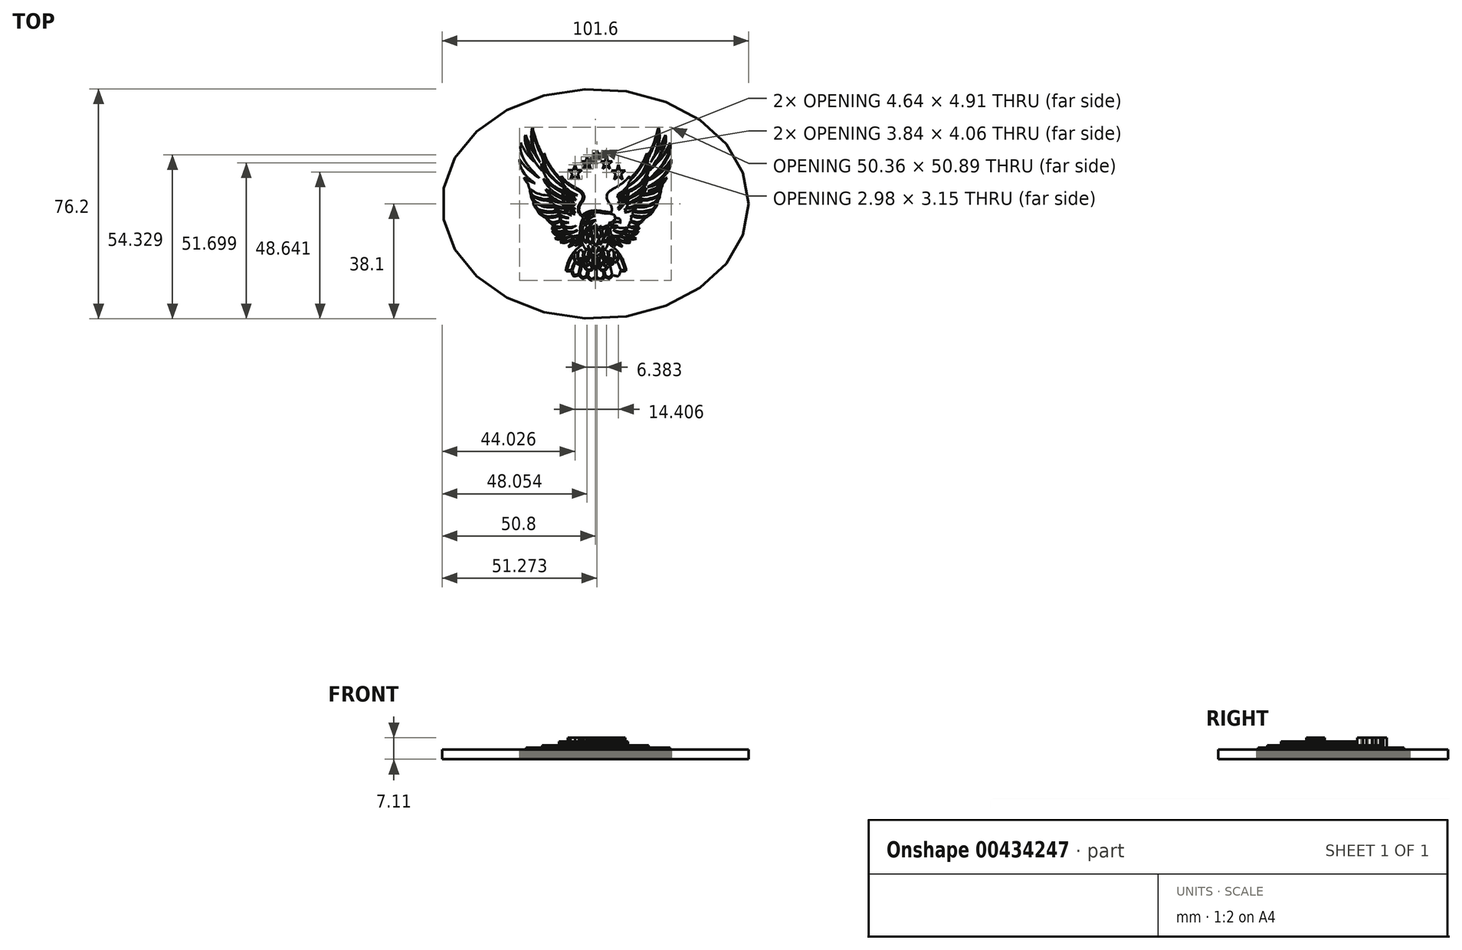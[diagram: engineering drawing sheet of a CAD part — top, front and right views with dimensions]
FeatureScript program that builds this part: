
annotation { "Feature Type Name" : "Feature", "Feature Type Description" : "" }
export const myFeature = defineFeature(function(context is Context, id is Id, definition is map)
    precondition{}
    {
        {
            var Q0;
            Q0=qCreatedBy(makeId("Top.planeOp"),FACE);
            var sketch = newSketch(context, id + "F0", { "sketchPlane" : qUnion([Q0])});
            skLineSegment(sketch, "E0", {"start": v(-20.82, 7.1) * mm, "end": v(-20.84, 7.08) * mm});
            skLineSegment(sketch, "E1", {"start": v(-20.84, 7.08) * mm, "end": v(-20.86, 7.06) * mm});
            skLineSegment(sketch, "E2", {"start": v(-20.86, 7.06) * mm, "end": v(-20.9, 7) * mm});
            skLineSegment(sketch, "E3", {"start": v(-20.9, 7) * mm, "end": v(-20.98, 6.92) * mm});
            skLineSegment(sketch, "E4", {"start": v(-20.98, 6.92) * mm, "end": v(-21.02, 6.88) * mm});
            skLineSegment(sketch, "E5", {"start": v(-21.02, 6.88) * mm, "end": v(-21.04, 6.84) * mm});
            skLineSegment(sketch, "E6", {"start": v(-21.04, 6.84) * mm, "end": v(-21.06, 6.76) * mm});
            skLineSegment(sketch, "E7", {"start": v(-21.06, 6.76) * mm, "end": v(-20.72, 6.6) * mm});
            skLineSegment(sketch, "E8", {"start": v(-20.72, 6.6) * mm, "end": v(-20.26, 6.42) * mm});
            skLineSegment(sketch, "E9", {"start": v(-20.26, 6.42) * mm, "end": v(-19.73, 6.22) * mm});
            skLineSegment(sketch, "E10", {"start": v(-19.73, 6.22) * mm, "end": v(-19.15, 6.01) * mm});
            skLineSegment(sketch, "E11", {"start": v(-19.15, 6.01) * mm, "end": v(-18.58, 5.83) * mm});
            skLineSegment(sketch, "E12", {"start": v(-18.58, 5.83) * mm, "end": v(-18.04, 5.68) * mm});
            skLineSegment(sketch, "E13", {"start": v(-18.04, 5.68) * mm, "end": v(-17.57, 5.58) * mm});
            skLineSegment(sketch, "E14", {"start": v(-17.57, 5.58) * mm, "end": v(-17.21, 5.54) * mm});
            skLineSegment(sketch, "E15", {"start": v(-17.21, 5.54) * mm, "end": v(-17.83, 5.88) * mm});
            skLineSegment(sketch, "E16", {"start": v(-17.83, 5.88) * mm, "end": v(-18.43, 6.24) * mm});
            skLineSegment(sketch, "E17", {"start": v(-18.43, 6.24) * mm, "end": v(-19, 6.59) * mm});
            skLineSegment(sketch, "E18", {"start": v(-19, 6.59) * mm, "end": v(-19.52, 6.93) * mm});
            skLineSegment(sketch, "E19", {"start": v(-19.52, 6.93) * mm, "end": v(-20.03, 7.28) * mm});
            skLineSegment(sketch, "E20", {"start": v(-20.03, 7.28) * mm, "end": v(-20.53, 7.64) * mm});
            skLineSegment(sketch, "E21", {"start": v(-20.53, 7.64) * mm, "end": v(-21.03, 8.03) * mm});
            skLineSegment(sketch, "E22", {"start": v(-21.03, 8.03) * mm, "end": v(-21.52, 8.46) * mm});
            skLineSegment(sketch, "E23", {"start": v(-21.52, 8.46) * mm, "end": v(-22.03, 8.94) * mm});
            skLineSegment(sketch, "E24", {"start": v(-22.03, 8.94) * mm, "end": v(-22.36, 9.27) * mm});
            skLineSegment(sketch, "E25", {"start": v(-22.36, 9.27) * mm, "end": v(-22.68, 9.63) * mm});
            skLineSegment(sketch, "E26", {"start": v(-22.68, 9.63) * mm, "end": v(-22.99, 10) * mm});
            skLineSegment(sketch, "E27", {"start": v(-22.99, 10) * mm, "end": v(-23.28, 10.4) * mm});
            skLineSegment(sketch, "E28", {"start": v(-23.28, 10.4) * mm, "end": v(-23.56, 10.8) * mm});
            skLineSegment(sketch, "E29", {"start": v(-23.56, 10.8) * mm, "end": v(-23.81, 11.21) * mm});
            skLineSegment(sketch, "E30", {"start": v(-23.81, 11.21) * mm, "end": v(-24.04, 11.64) * mm});
            skLineSegment(sketch, "E31", {"start": v(-24.04, 11.64) * mm, "end": v(-24.24, 12.06) * mm});
            skLineSegment(sketch, "E32", {"start": v(-24.24, 12.06) * mm, "end": v(-24.37, 12.37) * mm});
            skLineSegment(sketch, "E33", {"start": v(-24.37, 12.37) * mm, "end": v(-24.52, 12.75) * mm});
            skLineSegment(sketch, "E34", {"start": v(-24.52, 12.75) * mm, "end": v(-24.59, 12.95) * mm});
            skLineSegment(sketch, "E35", {"start": v(-24.59, 12.95) * mm, "end": v(-24.65, 13.15) * mm});
            skLineSegment(sketch, "E36", {"start": v(-24.65, 13.15) * mm, "end": v(-24.7, 13.32) * mm});
            skLineSegment(sketch, "E37", {"start": v(-24.7, 13.32) * mm, "end": v(-24.72, 13.47) * mm});
            skLineSegment(sketch, "E38", {"start": v(-24.72, 13.47) * mm, "end": v(-22.85, 11.41) * mm});
            skLineSegment(sketch, "E39", {"start": v(-22.85, 11.41) * mm, "end": v(-22.45, 11.02) * mm});
            skLineSegment(sketch, "E40", {"start": v(-22.45, 11.02) * mm, "end": v(-22.25, 10.83) * mm});
            skLineSegment(sketch, "E41", {"start": v(-22.25, 10.83) * mm, "end": v(-22.04, 10.64) * mm});
            skLineSegment(sketch, "E42", {"start": v(-22.04, 10.64) * mm, "end": v(-21.83, 10.46) * mm});
            skLineSegment(sketch, "E43", {"start": v(-21.83, 10.46) * mm, "end": v(-21.61, 10.27) * mm});
            skLineSegment(sketch, "E44", {"start": v(-21.61, 10.27) * mm, "end": v(-21.23, 9.96) * mm});
            skLineSegment(sketch, "E45", {"start": v(-21.23, 9.96) * mm, "end": v(-20.76, 9.6) * mm});
            skLineSegment(sketch, "E46", {"start": v(-20.76, 9.6) * mm, "end": v(-20.23, 9.24) * mm});
            skLineSegment(sketch, "E47", {"start": v(-20.23, 9.24) * mm, "end": v(-19.67, 8.87) * mm});
            skLineSegment(sketch, "E48", {"start": v(-19.67, 8.87) * mm, "end": v(-19.1, 8.54) * mm});
            skLineSegment(sketch, "E49", {"start": v(-19.1, 8.54) * mm, "end": v(-18.57, 8.25) * mm});
            skLineSegment(sketch, "E50", {"start": v(-18.57, 8.25) * mm, "end": v(-18.09, 8.03) * mm});
            skLineSegment(sketch, "E51", {"start": v(-18.09, 8.03) * mm, "end": v(-17.69, 7.9) * mm});
            skLineSegment(sketch, "E52", {"start": v(-17.69, 7.9) * mm, "end": v(-20.38, 10.8) * mm});
            skLineSegment(sketch, "E53", {"start": v(-20.38, 10.8) * mm, "end": v(-20.56, 11) * mm});
            skLineSegment(sketch, "E54", {"start": v(-20.56, 11) * mm, "end": v(-20.75, 11.23) * mm});
            skLineSegment(sketch, "E55", {"start": v(-20.75, 11.23) * mm, "end": v(-20.94, 11.46) * mm});
            skLineSegment(sketch, "E56", {"start": v(-20.94, 11.46) * mm, "end": v(-21.14, 11.7) * mm});
            skLineSegment(sketch, "E57", {"start": v(-21.14, 11.7) * mm, "end": v(-21.33, 11.95) * mm});
            skLineSegment(sketch, "E58", {"start": v(-21.33, 11.95) * mm, "end": v(-21.51, 12.19) * mm});
            skLineSegment(sketch, "E59", {"start": v(-21.51, 12.19) * mm, "end": v(-21.7, 12.42) * mm});
            skLineSegment(sketch, "E60", {"start": v(-21.7, 12.42) * mm, "end": v(-21.86, 12.65) * mm});
            skLineSegment(sketch, "E61", {"start": v(-21.86, 12.65) * mm, "end": v(-22.08, 12.95) * mm});
            skLineSegment(sketch, "E62", {"start": v(-22.08, 12.95) * mm, "end": v(-22.31, 13.27) * mm});
            skLineSegment(sketch, "E63", {"start": v(-22.31, 13.27) * mm, "end": v(-22.54, 13.6) * mm});
            skLineSegment(sketch, "E64", {"start": v(-22.54, 13.6) * mm, "end": v(-22.76, 13.94) * mm});
            skLineSegment(sketch, "E65", {"start": v(-22.76, 13.94) * mm, "end": v(-22.98, 14.3) * mm});
            skLineSegment(sketch, "E66", {"start": v(-22.98, 14.3) * mm, "end": v(-23.2, 14.66) * mm});
            skLineSegment(sketch, "E67", {"start": v(-23.2, 14.66) * mm, "end": v(-23.4, 15.02) * mm});
            skLineSegment(sketch, "E68", {"start": v(-23.4, 15.02) * mm, "end": v(-23.58, 15.4) * mm});
            skLineSegment(sketch, "E69", {"start": v(-23.58, 15.4) * mm, "end": v(-23.72, 15.7) * mm});
            skLineSegment(sketch, "E70", {"start": v(-23.72, 15.7) * mm, "end": v(-23.88, 16.08) * mm});
            skLineSegment(sketch, "E71", {"start": v(-23.88, 16.08) * mm, "end": v(-24.06, 16.53) * mm});
            skLineSegment(sketch, "E72", {"start": v(-24.06, 16.53) * mm, "end": v(-24.23, 17.02) * mm});
            skLineSegment(sketch, "E73", {"start": v(-24.23, 17.02) * mm, "end": v(-24.37, 17.52) * mm});
            skLineSegment(sketch, "E74", {"start": v(-24.37, 17.52) * mm, "end": v(-24.49, 18) * mm});
            skLineSegment(sketch, "E75", {"start": v(-24.49, 18) * mm, "end": v(-24.55, 18.45) * mm});
            skLineSegment(sketch, "E76", {"start": v(-24.55, 18.45) * mm, "end": v(-24.55, 18.83) * mm});
            skLineSegment(sketch, "E77", {"start": v(-24.55, 18.83) * mm, "end": v(-24.45, 18.64) * mm});
            skLineSegment(sketch, "E78", {"start": v(-24.45, 18.64) * mm, "end": v(-24.27, 18.34) * mm});
            skLineSegment(sketch, "E79", {"start": v(-24.27, 18.34) * mm, "end": v(-24.03, 17.97) * mm});
            skLineSegment(sketch, "E80", {"start": v(-24.03, 17.97) * mm, "end": v(-23.76, 17.57) * mm});
            skLineSegment(sketch, "E81", {"start": v(-23.76, 17.57) * mm, "end": v(-23.47, 17.15) * mm});
            skLineSegment(sketch, "E82", {"start": v(-23.47, 17.15) * mm, "end": v(-23.2, 16.76) * mm});
            skLineSegment(sketch, "E83", {"start": v(-23.2, 16.76) * mm, "end": v(-22.96, 16.43) * mm});
            skLineSegment(sketch, "E84", {"start": v(-22.96, 16.43) * mm, "end": v(-22.79, 16.18) * mm});
            skLineSegment(sketch, "E85", {"start": v(-22.79, 16.18) * mm, "end": v(-22.51, 15.83) * mm});
            skLineSegment(sketch, "E86", {"start": v(-22.51, 15.83) * mm, "end": v(-21.93, 15.12) * mm});
            skLineSegment(sketch, "E87", {"start": v(-21.93, 15.12) * mm, "end": v(-21.63, 14.8) * mm});
            skLineSegment(sketch, "E88", {"start": v(-21.63, 14.8) * mm, "end": v(-20.56, 13.66) * mm});
            skLineSegment(sketch, "E89", {"start": v(-20.56, 13.66) * mm, "end": v(-20.4, 13.52) * mm});
            skLineSegment(sketch, "E90", {"start": v(-20.4, 13.52) * mm, "end": v(-20.33, 13.43) * mm});
            skLineSegment(sketch, "E91", {"start": v(-20.33, 13.43) * mm, "end": v(-20.26, 13.33) * mm});
            skLineSegment(sketch, "E92", {"start": v(-20.26, 13.33) * mm, "end": v(-19.96, 13) * mm});
            skLineSegment(sketch, "E93", {"start": v(-19.96, 13) * mm, "end": v(-19.58, 12.62) * mm});
            skLineSegment(sketch, "E94", {"start": v(-19.58, 12.62) * mm, "end": v(-19.2, 12.23) * mm});
            skLineSegment(sketch, "E95", {"start": v(-19.2, 12.23) * mm, "end": v(-18.86, 11.9) * mm});
            skLineSegment(sketch, "E96", {"start": v(-18.86, 11.9) * mm, "end": v(-18.72, 11.76) * mm});
            skLineSegment(sketch, "E97", {"start": v(-18.72, 11.76) * mm, "end": v(-18.55, 11.62) * mm});
            skLineSegment(sketch, "E98", {"start": v(-18.55, 11.62) * mm, "end": v(-18.37, 11.46) * mm});
            skLineSegment(sketch, "E99", {"start": v(-18.37, 11.46) * mm, "end": v(-18.2, 11.31) * mm});
            skLineSegment(sketch, "E100", {"start": v(-18.2, 11.31) * mm, "end": v(-18.03, 11.18) * mm});
            skLineSegment(sketch, "E101", {"start": v(-18.03, 11.18) * mm, "end": v(-17.9, 11.09) * mm});
            skLineSegment(sketch, "E102", {"start": v(-17.9, 11.09) * mm, "end": v(-17.8, 11.03) * mm});
            skLineSegment(sketch, "E103", {"start": v(-17.8, 11.03) * mm, "end": v(-17.73, 10.99) * mm});
            skLineSegment(sketch, "E104", {"start": v(-17.73, 10.99) * mm, "end": v(-17.68, 10.95) * mm});
            skLineSegment(sketch, "E105", {"start": v(-17.68, 10.95) * mm, "end": v(-17.63, 10.9) * mm});
            skLineSegment(sketch, "E106", {"start": v(-17.63, 10.9) * mm, "end": v(-17.6, 10.81) * mm});
            skLineSegment(sketch, "E107", {"start": v(-17.6, 10.81) * mm, "end": v(-17.57, 10.69) * mm});
            skLineSegment(sketch, "E108", {"start": v(-17.57, 10.69) * mm, "end": v(-17.51, 10.45) * mm});
            skLineSegment(sketch, "E109", {"start": v(-17.51, 10.45) * mm, "end": v(-17.44, 10.2) * mm});
            skLineSegment(sketch, "E110", {"start": v(-17.44, 10.2) * mm, "end": v(-17.36, 9.97) * mm});
            skLineSegment(sketch, "E111", {"start": v(-17.36, 9.97) * mm, "end": v(-17.26, 9.73) * mm});
            skLineSegment(sketch, "E112", {"start": v(-17.26, 9.73) * mm, "end": v(-17.16, 9.5) * mm});
            skLineSegment(sketch, "E113", {"start": v(-17.16, 9.5) * mm, "end": v(-17.05, 9.28) * mm});
            skLineSegment(sketch, "E114", {"start": v(-17.05, 9.28) * mm, "end": v(-16.94, 9.07) * mm});
            skLineSegment(sketch, "E115", {"start": v(-16.94, 9.07) * mm, "end": v(-16.83, 8.88) * mm});
            skLineSegment(sketch, "E116", {"start": v(-16.83, 8.88) * mm, "end": v(-16.6, 8.5) * mm});
            skLineSegment(sketch, "E117", {"start": v(-16.6, 8.5) * mm, "end": v(-16.33, 8.14) * mm});
            skLineSegment(sketch, "E118", {"start": v(-16.33, 8.14) * mm, "end": v(-16.2, 7.99) * mm});
            skLineSegment(sketch, "E119", {"start": v(-16.2, 7.99) * mm, "end": v(-16.03, 7.78) * mm});
            skLineSegment(sketch, "E120", {"start": v(-16.03, 7.78) * mm, "end": v(-15.94, 7.67) * mm});
            skLineSegment(sketch, "E121", {"start": v(-15.94, 7.67) * mm, "end": v(-15.86, 7.57) * mm});
            skLineSegment(sketch, "E122", {"start": v(-15.86, 7.57) * mm, "end": v(-15.8, 7.48) * mm});
            skLineSegment(sketch, "E123", {"start": v(-15.8, 7.48) * mm, "end": v(-15.77, 7.42) * mm});
            skLineSegment(sketch, "E124", {"start": v(-15.77, 7.42) * mm, "end": v(-16, 7.58) * mm});
            skLineSegment(sketch, "E125", {"start": v(-16, 7.58) * mm, "end": v(-16.26, 7.8) * mm});
            skLineSegment(sketch, "E126", {"start": v(-16.26, 7.8) * mm, "end": v(-16.55, 8.04) * mm});
            skLineSegment(sketch, "E127", {"start": v(-16.55, 8.04) * mm, "end": v(-16.84, 8.3) * mm});
            skLineSegment(sketch, "E128", {"start": v(-16.84, 8.3) * mm, "end": v(-17.13, 8.55) * mm});
            skLineSegment(sketch, "E129", {"start": v(-17.13, 8.55) * mm, "end": v(-17.39, 8.76) * mm});
            skLineSegment(sketch, "E130", {"start": v(-17.39, 8.76) * mm, "end": v(-17.6, 8.92) * mm});
            skLineSegment(sketch, "E131", {"start": v(-17.6, 8.92) * mm, "end": v(-17.75, 9.01) * mm});
            skLineSegment(sketch, "E132", {"start": v(-17.75, 9.01) * mm, "end": v(-17.72, 8.83) * mm});
            skLineSegment(sketch, "E133", {"start": v(-17.72, 8.83) * mm, "end": v(-17.66, 8.61) * mm});
            skLineSegment(sketch, "E134", {"start": v(-17.66, 8.61) * mm, "end": v(-17.59, 8.38) * mm});
            skLineSegment(sketch, "E135", {"start": v(-17.59, 8.38) * mm, "end": v(-17.5, 8.14) * mm});
            skLineSegment(sketch, "E136", {"start": v(-17.5, 8.14) * mm, "end": v(-17.41, 7.9) * mm});
            skLineSegment(sketch, "E137", {"start": v(-17.41, 7.9) * mm, "end": v(-17.32, 7.67) * mm});
            skLineSegment(sketch, "E138", {"start": v(-17.32, 7.67) * mm, "end": v(-17.24, 7.47) * mm});
            skLineSegment(sketch, "E139", {"start": v(-17.24, 7.47) * mm, "end": v(-17.16, 7.3) * mm});
            skLineSegment(sketch, "E140", {"start": v(-17.16, 7.3) * mm, "end": v(-17.07, 7.1) * mm});
            skLineSegment(sketch, "E141", {"start": v(-17.07, 7.1) * mm, "end": v(-16.98, 6.9) * mm});
            skLineSegment(sketch, "E142", {"start": v(-16.98, 6.9) * mm, "end": v(-16.88, 6.72) * mm});
            skLineSegment(sketch, "E143", {"start": v(-16.88, 6.72) * mm, "end": v(-16.78, 6.54) * mm});
            skLineSegment(sketch, "E144", {"start": v(-16.78, 6.54) * mm, "end": v(-16.56, 6.2) * mm});
            skLineSegment(sketch, "E145", {"start": v(-16.56, 6.2) * mm, "end": v(-16.33, 5.85) * mm});
            skLineSegment(sketch, "E146", {"start": v(-16.33, 5.85) * mm, "end": v(-16.15, 5.62) * mm});
            skLineSegment(sketch, "E147", {"start": v(-16.15, 5.62) * mm, "end": v(-15.96, 5.38) * mm});
            skLineSegment(sketch, "E148", {"start": v(-15.96, 5.38) * mm, "end": v(-15.75, 5.15) * mm});
            skLineSegment(sketch, "E149", {"start": v(-15.75, 5.15) * mm, "end": v(-15.52, 4.92) * mm});
            skLineSegment(sketch, "E150", {"start": v(-15.52, 4.92) * mm, "end": v(-15.3, 4.7) * mm});
            skLineSegment(sketch, "E151", {"start": v(-15.3, 4.7) * mm, "end": v(-15.06, 4.49) * mm});
            skLineSegment(sketch, "E152", {"start": v(-15.06, 4.49) * mm, "end": v(-14.82, 4.3) * mm});
            skLineSegment(sketch, "E153", {"start": v(-14.82, 4.3) * mm, "end": v(-14.6, 4.12) * mm});
            skLineSegment(sketch, "E154", {"start": v(-14.6, 4.12) * mm, "end": v(-14.43, 4.01) * mm});
            skLineSegment(sketch, "E155", {"start": v(-14.43, 4.01) * mm, "end": v(-14.26, 3.89) * mm});
            skLineSegment(sketch, "E156", {"start": v(-14.26, 3.89) * mm, "end": v(-14.1, 3.76) * mm});
            skLineSegment(sketch, "E157", {"start": v(-14.1, 3.76) * mm, "end": v(-13.94, 3.64) * mm});
            skLineSegment(sketch, "E158", {"start": v(-13.94, 3.64) * mm, "end": v(-14.2, 3.75) * mm});
            skLineSegment(sketch, "E159", {"start": v(-14.2, 3.75) * mm, "end": v(-14.57, 3.95) * mm});
            skLineSegment(sketch, "E160", {"start": v(-14.57, 3.95) * mm, "end": v(-15, 4.2) * mm});
            skLineSegment(sketch, "E161", {"start": v(-15, 4.2) * mm, "end": v(-15.47, 4.48) * mm});
            skLineSegment(sketch, "E162", {"start": v(-15.47, 4.48) * mm, "end": v(-15.93, 4.77) * mm});
            skLineSegment(sketch, "E163", {"start": v(-15.93, 4.77) * mm, "end": v(-16.36, 5.03) * mm});
            skLineSegment(sketch, "E164", {"start": v(-16.36, 5.03) * mm, "end": v(-16.7, 5.24) * mm});
            skLineSegment(sketch, "E165", {"start": v(-16.7, 5.24) * mm, "end": v(-16.95, 5.36) * mm});
            skLineSegment(sketch, "E166", {"start": v(-16.95, 5.36) * mm, "end": v(-16.85, 5.01) * mm});
            skLineSegment(sketch, "E167", {"start": v(-16.85, 5.01) * mm, "end": v(-16.72, 4.68) * mm});
            skLineSegment(sketch, "E168", {"start": v(-16.72, 4.68) * mm, "end": v(-16.57, 4.36) * mm});
            skLineSegment(sketch, "E169", {"start": v(-16.57, 4.36) * mm, "end": v(-16.42, 4.07) * mm});
            skLineSegment(sketch, "E170", {"start": v(-16.42, 4.07) * mm, "end": v(-16.28, 3.81) * mm});
            skLineSegment(sketch, "E171", {"start": v(-16.28, 3.81) * mm, "end": v(-16.15, 3.6) * mm});
            skLineSegment(sketch, "E172", {"start": v(-16.15, 3.6) * mm, "end": v(-16.05, 3.42) * mm});
            skLineSegment(sketch, "E173", {"start": v(-16.05, 3.42) * mm, "end": v(-15.99, 3.3) * mm});
            skLineSegment(sketch, "E174", {"start": v(-15.99, 3.3) * mm, "end": v(-16.72, 3.37) * mm});
            skLineSegment(sketch, "E175", {"start": v(-16.72, 3.37) * mm, "end": v(-17.6, 3.5) * mm});
            skLineSegment(sketch, "E176", {"start": v(-17.6, 3.5) * mm, "end": v(-18.53, 3.72) * mm});
            skLineSegment(sketch, "E177", {"start": v(-18.53, 3.72) * mm, "end": v(-19.47, 4.01) * mm});
            skLineSegment(sketch, "E178", {"start": v(-19.47, 4.01) * mm, "end": v(-20.34, 4.4) * mm});
            skLineSegment(sketch, "E179", {"start": v(-20.34, 4.4) * mm, "end": v(-21.08, 4.87) * mm});
            skLineSegment(sketch, "E180", {"start": v(-21.08, 4.87) * mm, "end": v(-21.62, 5.46) * mm});
            skLineSegment(sketch, "E181", {"start": v(-21.62, 5.46) * mm, "end": v(-21.89, 6.15) * mm});
            skLineSegment(sketch, "E182", {"start": v(-21.89, 6.15) * mm, "end": v(-21.76, 6.09) * mm});
            skLineSegment(sketch, "E183", {"start": v(-21.76, 6.09) * mm, "end": v(-21.64, 6) * mm});
            skLineSegment(sketch, "E184", {"start": v(-21.64, 6) * mm, "end": v(-21.51, 5.9) * mm});
            skLineSegment(sketch, "E185", {"start": v(-21.51, 5.9) * mm, "end": v(-21.4, 5.81) * mm});
            skLineSegment(sketch, "E186", {"start": v(-21.4, 5.81) * mm, "end": v(-21.03, 5.56) * mm});
            skLineSegment(sketch, "E187", {"start": v(-21.03, 5.56) * mm, "end": v(-20.56, 5.3) * mm});
            skLineSegment(sketch, "E188", {"start": v(-20.56, 5.3) * mm, "end": v(-20.03, 5.05) * mm});
            skLineSegment(sketch, "E189", {"start": v(-20.03, 5.05) * mm, "end": v(-19.46, 4.8) * mm});
            skLineSegment(sketch, "E190", {"start": v(-19.46, 4.8) * mm, "end": v(-18.89, 4.6) * mm});
            skLineSegment(sketch, "E191", {"start": v(-18.89, 4.6) * mm, "end": v(-18.33, 4.44) * mm});
            skLineSegment(sketch, "E192", {"start": v(-18.33, 4.44) * mm, "end": v(-17.84, 4.35) * mm});
            skLineSegment(sketch, "E193", {"start": v(-17.84, 4.35) * mm, "end": v(-17.42, 4.34) * mm});
            skLineSegment(sketch, "E194", {"start": v(-17.42, 4.34) * mm, "end": v(-17.6, 4.36) * mm});
            skLineSegment(sketch, "E195", {"start": v(-17.6, 4.36) * mm, "end": v(-17.92, 4.46) * mm});
            skLineSegment(sketch, "E196", {"start": v(-17.92, 4.46) * mm, "end": v(-18.32, 4.6) * mm});
            skLineSegment(sketch, "E197", {"start": v(-18.32, 4.6) * mm, "end": v(-18.76, 4.76) * mm});
            skLineSegment(sketch, "E198", {"start": v(-18.76, 4.76) * mm, "end": v(-19.2, 4.93) * mm});
            skLineSegment(sketch, "E199", {"start": v(-19.2, 4.93) * mm, "end": v(-19.6, 5.1) * mm});
            skLineSegment(sketch, "E200", {"start": v(-19.6, 5.1) * mm, "end": v(-19.92, 5.23) * mm});
            skLineSegment(sketch, "E201", {"start": v(-19.92, 5.23) * mm, "end": v(-20.1, 5.32) * mm});
            skLineSegment(sketch, "E202", {"start": v(-20.1, 5.32) * mm, "end": v(-20.43, 5.5) * mm});
            skLineSegment(sketch, "E203", {"start": v(-20.43, 5.5) * mm, "end": v(-20.72, 5.67) * mm});
            skLineSegment(sketch, "E204", {"start": v(-20.72, 5.67) * mm, "end": v(-20.99, 5.85) * mm});
            skLineSegment(sketch, "E205", {"start": v(-20.99, 5.85) * mm, "end": v(-21.26, 6.04) * mm});
            skLineSegment(sketch, "E206", {"start": v(-21.26, 6.04) * mm, "end": v(-21.38, 6.15) * mm});
            skLineSegment(sketch, "E207", {"start": v(-21.38, 6.15) * mm, "end": v(-21.5, 6.26) * mm});
            skLineSegment(sketch, "E208", {"start": v(-21.5, 6.26) * mm, "end": v(-21.64, 6.37) * mm});
            skLineSegment(sketch, "E209", {"start": v(-21.64, 6.37) * mm, "end": v(-21.76, 6.48) * mm});
            skLineSegment(sketch, "E210", {"start": v(-21.76, 6.48) * mm, "end": v(-21.87, 6.59) * mm});
            skLineSegment(sketch, "E211", {"start": v(-21.87, 6.59) * mm, "end": v(-21.96, 6.68) * mm});
            skLineSegment(sketch, "E212", {"start": v(-21.96, 6.68) * mm, "end": v(-22.03, 6.76) * mm});
            skLineSegment(sketch, "E213", {"start": v(-22.03, 6.76) * mm, "end": v(-22.1, 6.83) * mm});
            skLineSegment(sketch, "E214", {"start": v(-22.1, 6.83) * mm, "end": v(-22.15, 6.87) * mm});
            skLineSegment(sketch, "E215", {"start": v(-22.15, 6.87) * mm, "end": v(-22.2, 6.9) * mm});
            skLineSegment(sketch, "E216", {"start": v(-22.2, 6.9) * mm, "end": v(-22.27, 6.92) * mm});
            skLineSegment(sketch, "E217", {"start": v(-22.27, 6.92) * mm, "end": v(-22.28, 6.93) * mm});
            skLineSegment(sketch, "E218", {"start": v(-22.28, 6.93) * mm, "end": v(-22.3, 6.92) * mm});
            skLineSegment(sketch, "E219", {"start": v(-22.3, 6.92) * mm, "end": v(-22.37, 6.9) * mm});
            skLineSegment(sketch, "E220", {"start": v(-22.37, 6.9) * mm, "end": v(-22.42, 6.87) * mm});
            skLineSegment(sketch, "E221", {"start": v(-22.42, 6.87) * mm, "end": v(-22.45, 6.85) * mm});
            skLineSegment(sketch, "E222", {"start": v(-22.45, 6.85) * mm, "end": v(-22.47, 6.82) * mm});
            skLineSegment(sketch, "E223", {"start": v(-22.47, 6.82) * mm, "end": v(-22.5, 6.8) * mm});
            skLineSegment(sketch, "E224", {"start": v(-22.5, 6.8) * mm, "end": v(-22.4, 6.63) * mm});
            skLineSegment(sketch, "E225", {"start": v(-22.4, 6.63) * mm, "end": v(-22.32, 6.53) * mm});
            skLineSegment(sketch, "E226", {"start": v(-22.32, 6.53) * mm, "end": v(-22.28, 6.44) * mm});
            skLineSegment(sketch, "E227", {"start": v(-22.28, 6.44) * mm, "end": v(-22.26, 6.37) * mm});
            skLineSegment(sketch, "E228", {"start": v(-22.26, 6.37) * mm, "end": v(-22.21, 6.16) * mm});
            skLineSegment(sketch, "E229", {"start": v(-22.21, 6.16) * mm, "end": v(-22.1, 5.74) * mm});
            skLineSegment(sketch, "E230", {"start": v(-22.1, 5.74) * mm, "end": v(-22.04, 5.57) * mm});
            skLineSegment(sketch, "E231", {"start": v(-22.04, 5.57) * mm, "end": v(-21.98, 5.4) * mm});
            skLineSegment(sketch, "E232", {"start": v(-21.98, 5.4) * mm, "end": v(-21.92, 5.26) * mm});
            skLineSegment(sketch, "E233", {"start": v(-21.92, 5.26) * mm, "end": v(-21.86, 5.12) * mm});
            skLineSegment(sketch, "E234", {"start": v(-21.86, 5.12) * mm, "end": v(-21.8, 5) * mm});
            skLineSegment(sketch, "E235", {"start": v(-21.8, 5) * mm, "end": v(-21.76, 4.88) * mm});
            skLineSegment(sketch, "E236", {"start": v(-21.76, 4.88) * mm, "end": v(-21.73, 4.78) * mm});
            skLineSegment(sketch, "E237", {"start": v(-21.73, 4.78) * mm, "end": v(-21.72, 4.69) * mm});
            skLineSegment(sketch, "E238", {"start": v(-21.72, 4.69) * mm, "end": v(-21.7, 4.26) * mm});
            skLineSegment(sketch, "E239", {"start": v(-21.7, 4.26) * mm, "end": v(-21.66, 3.96) * mm});
            skLineSegment(sketch, "E240", {"start": v(-21.66, 3.96) * mm, "end": v(-21.63, 3.74) * mm});
            skLineSegment(sketch, "E241", {"start": v(-21.63, 3.74) * mm, "end": v(-21.6, 3.58) * mm});
            skLineSegment(sketch, "E242", {"start": v(-21.6, 3.58) * mm, "end": v(-21.56, 3.44) * mm});
            skLineSegment(sketch, "E243", {"start": v(-21.56, 3.44) * mm, "end": v(-21.51, 3.29) * mm});
            skLineSegment(sketch, "E244", {"start": v(-21.51, 3.29) * mm, "end": v(-21.46, 3.1) * mm});
            skLineSegment(sketch, "E245", {"start": v(-21.46, 3.1) * mm, "end": v(-21.4, 2.82) * mm});
            skLineSegment(sketch, "E246", {"start": v(-21.4, 2.82) * mm, "end": v(-21.37, 2.66) * mm});
            skLineSegment(sketch, "E247", {"start": v(-21.37, 2.66) * mm, "end": v(-21.36, 2.5) * mm});
            skLineSegment(sketch, "E248", {"start": v(-21.36, 2.5) * mm, "end": v(-21.35, 2.33) * mm});
            skLineSegment(sketch, "E249", {"start": v(-21.35, 2.33) * mm, "end": v(-21.32, 2.15) * mm});
            skLineSegment(sketch, "E250", {"start": v(-21.32, 2.15) * mm, "end": v(-21.28, 2) * mm});
            skLineSegment(sketch, "E251", {"start": v(-21.28, 2) * mm, "end": v(-21.23, 1.87) * mm});
            skLineSegment(sketch, "E252", {"start": v(-21.23, 1.87) * mm, "end": v(-21.18, 1.74) * mm});
            skLineSegment(sketch, "E253", {"start": v(-21.18, 1.74) * mm, "end": v(-21.12, 1.6) * mm});
            skLineSegment(sketch, "E254", {"start": v(-21.12, 1.6) * mm, "end": v(-21.06, 1.48) * mm});
            skLineSegment(sketch, "E255", {"start": v(-21.06, 1.48) * mm, "end": v(-20.99, 1.37) * mm});
            skLineSegment(sketch, "E256", {"start": v(-20.99, 1.37) * mm, "end": v(-20.92, 1.26) * mm});
            skLineSegment(sketch, "E257", {"start": v(-20.92, 1.26) * mm, "end": v(-20.85, 1.16) * mm});
            skLineSegment(sketch, "E258", {"start": v(-20.85, 1.16) * mm, "end": v(-20.73, 0.99) * mm});
            skLineSegment(sketch, "E259", {"start": v(-20.73, 0.99) * mm, "end": v(-20.66, 0.87) * mm});
            skLineSegment(sketch, "E260", {"start": v(-20.66, 0.87) * mm, "end": v(-20.63, 0.77) * mm});
            skLineSegment(sketch, "E261", {"start": v(-20.63, 0.77) * mm, "end": v(-20.63, 0.68) * mm});
            skLineSegment(sketch, "E262", {"start": v(-20.63, 0.68) * mm, "end": v(-20.63, 0.58) * mm});
            skLineSegment(sketch, "E263", {"start": v(-20.63, 0.58) * mm, "end": v(-20.63, 0.44) * mm});
            skLineSegment(sketch, "E264", {"start": v(-20.63, 0.44) * mm, "end": v(-20.6, 0.25) * mm});
            skLineSegment(sketch, "E265", {"start": v(-20.6, 0.25) * mm, "end": v(-20.55, 0) * mm});
            skLineSegment(sketch, "E266", {"start": v(-20.55, 0) * mm, "end": v(-20.45, -0.32) * mm});
            skLineSegment(sketch, "E267", {"start": v(-20.45, -0.32) * mm, "end": v(-20.35, -0.6) * mm});
            skLineSegment(sketch, "E268", {"start": v(-20.35, -0.6) * mm, "end": v(-20.23, -0.83) * mm});
            skLineSegment(sketch, "E269", {"start": v(-20.23, -0.83) * mm, "end": v(-20.1, -1.04) * mm});
            skLineSegment(sketch, "E270", {"start": v(-20.1, -1.04) * mm, "end": v(-19.97, -1.23) * mm});
            skLineSegment(sketch, "E271", {"start": v(-19.97, -1.23) * mm, "end": v(-19.81, -1.42) * mm});
            skLineSegment(sketch, "E272", {"start": v(-19.81, -1.42) * mm, "end": v(-19.65, -1.62) * mm});
            skLineSegment(sketch, "E273", {"start": v(-19.65, -1.62) * mm, "end": v(-19.47, -1.84) * mm});
            skLineSegment(sketch, "E274", {"start": v(-19.47, -1.84) * mm, "end": v(-19.4, -1.94) * mm});
            skLineSegment(sketch, "E275", {"start": v(-19.4, -1.94) * mm, "end": v(-19.34, -2.05) * mm});
            skLineSegment(sketch, "E276", {"start": v(-19.34, -2.05) * mm, "end": v(-19.28, -2.18) * mm});
            skLineSegment(sketch, "E277", {"start": v(-19.28, -2.18) * mm, "end": v(-19.23, -2.3) * mm});
            skLineSegment(sketch, "E278", {"start": v(-19.23, -2.3) * mm, "end": v(-19.16, -2.44) * mm});
            skLineSegment(sketch, "E279", {"start": v(-19.16, -2.44) * mm, "end": v(-19.1, -2.55) * mm});
            skLineSegment(sketch, "E280", {"start": v(-19.1, -2.55) * mm, "end": v(-19.02, -2.66) * mm});
            skLineSegment(sketch, "E281", {"start": v(-19.02, -2.66) * mm, "end": v(-18.94, -2.77) * mm});
            skLineSegment(sketch, "E282", {"start": v(-18.94, -2.77) * mm, "end": v(-18.64, -3.16) * mm});
            skLineSegment(sketch, "E283", {"start": v(-18.64, -3.16) * mm, "end": v(-18.28, -3.51) * mm});
            skLineSegment(sketch, "E284", {"start": v(-18.28, -3.51) * mm, "end": v(-17.9, -3.81) * mm});
            skLineSegment(sketch, "E285", {"start": v(-17.9, -3.81) * mm, "end": v(-17.5, -4.08) * mm});
            skLineSegment(sketch, "E286", {"start": v(-17.5, -4.08) * mm, "end": v(-17.13, -4.3) * mm});
            skLineSegment(sketch, "E287", {"start": v(-17.13, -4.3) * mm, "end": v(-16.82, -4.47) * mm});
            skLineSegment(sketch, "E288", {"start": v(-16.82, -4.47) * mm, "end": v(-16.6, -4.6) * mm});
            skLineSegment(sketch, "E289", {"start": v(-16.6, -4.6) * mm, "end": v(-16.47, -4.68) * mm});
            skLineSegment(sketch, "E290", {"start": v(-16.47, -4.68) * mm, "end": v(-16.4, -4.77) * mm});
            skLineSegment(sketch, "E291", {"start": v(-16.4, -4.77) * mm, "end": v(-16.32, -4.88) * mm});
            skLineSegment(sketch, "E292", {"start": v(-16.32, -4.88) * mm, "end": v(-16.25, -5) * mm});
            skLineSegment(sketch, "E293", {"start": v(-16.25, -5) * mm, "end": v(-16.18, -5.1) * mm});
            skLineSegment(sketch, "E294", {"start": v(-16.18, -5.1) * mm, "end": v(-16.02, -5.33) * mm});
            skLineSegment(sketch, "E295", {"start": v(-16.02, -5.33) * mm, "end": v(-15.9, -5.47) * mm});
            skLineSegment(sketch, "E296", {"start": v(-15.9, -5.47) * mm, "end": v(-15.81, -5.57) * mm});
            skLineSegment(sketch, "E297", {"start": v(-15.81, -5.57) * mm, "end": v(-15.7, -5.7) * mm});
            skLineSegment(sketch, "E298", {"start": v(-15.7, -5.7) * mm, "end": v(-15.66, -5.77) * mm});
            skLineSegment(sketch, "E299", {"start": v(-15.66, -5.77) * mm, "end": v(-15.62, -5.8) * mm});
            skLineSegment(sketch, "E300", {"start": v(-15.62, -5.8) * mm, "end": v(-15.59, -5.84) * mm});
            skLineSegment(sketch, "E301", {"start": v(-15.59, -5.84) * mm, "end": v(-15.52, -5.9) * mm});
            skLineSegment(sketch, "E302", {"start": v(-15.52, -5.9) * mm, "end": v(-15.41, -5.98) * mm});
            skLineSegment(sketch, "E303", {"start": v(-15.41, -5.98) * mm, "end": v(-15.32, -6.06) * mm});
            skLineSegment(sketch, "E304", {"start": v(-15.32, -6.06) * mm, "end": v(-15.22, -6.14) * mm});
            skLineSegment(sketch, "E305", {"start": v(-15.22, -6.14) * mm, "end": v(-15.1, -6.22) * mm});
            skLineSegment(sketch, "E306", {"start": v(-15.1, -6.22) * mm, "end": v(-14.88, -6.34) * mm});
            skLineSegment(sketch, "E307", {"start": v(-14.88, -6.34) * mm, "end": v(-14.75, -6.4) * mm});
            skLineSegment(sketch, "E308", {"start": v(-14.75, -6.4) * mm, "end": v(-14.68, -6.43) * mm});
            skLineSegment(sketch, "E309", {"start": v(-14.68, -6.43) * mm, "end": v(-14.65, -6.46) * mm});
            skLineSegment(sketch, "E310", {"start": v(-14.65, -6.46) * mm, "end": v(-14.62, -6.5) * mm});
            skLineSegment(sketch, "E311", {"start": v(-14.62, -6.5) * mm, "end": v(-14.58, -6.59) * mm});
            skLineSegment(sketch, "E312", {"start": v(-14.58, -6.59) * mm, "end": v(-14.51, -6.73) * mm});
            skLineSegment(sketch, "E313", {"start": v(-14.51, -6.73) * mm, "end": v(-14.38, -6.97) * mm});
            skLineSegment(sketch, "E314", {"start": v(-14.38, -6.97) * mm, "end": v(-14.28, -7.14) * mm});
            skLineSegment(sketch, "E315", {"start": v(-14.28, -7.14) * mm, "end": v(-14.17, -7.3) * mm});
            skLineSegment(sketch, "E316", {"start": v(-14.17, -7.3) * mm, "end": v(-14.1, -7.37) * mm});
            skLineSegment(sketch, "E317", {"start": v(-14.1, -7.37) * mm, "end": v(-14.04, -7.44) * mm});
            skLineSegment(sketch, "E318", {"start": v(-14.04, -7.44) * mm, "end": v(-13.96, -7.51) * mm});
            skLineSegment(sketch, "E319", {"start": v(-13.96, -7.51) * mm, "end": v(-13.87, -7.58) * mm});
            skLineSegment(sketch, "E320", {"start": v(-13.87, -7.58) * mm, "end": v(-13.65, -7.75) * mm});
            skLineSegment(sketch, "E321", {"start": v(-13.65, -7.75) * mm, "end": v(-14.57, -7.97) * mm});
            skLineSegment(sketch, "E322", {"start": v(-14.57, -7.97) * mm, "end": v(-14.5, -8.18) * mm});
            skLineSegment(sketch, "E323", {"start": v(-14.5, -8.18) * mm, "end": v(-14.38, -8.37) * mm});
            skLineSegment(sketch, "E324", {"start": v(-14.38, -8.37) * mm, "end": v(-14.22, -8.55) * mm});
            skLineSegment(sketch, "E325", {"start": v(-14.22, -8.55) * mm, "end": v(-14.02, -8.71) * mm});
            skLineSegment(sketch, "E326", {"start": v(-14.02, -8.71) * mm, "end": v(-13.64, -8.98) * mm});
            skLineSegment(sketch, "E327", {"start": v(-13.64, -8.98) * mm, "end": v(-13.39, -9.16) * mm});
            skLineSegment(sketch, "E328", {"start": v(-13.39, -9.16) * mm, "end": v(-14.3, -9.05) * mm});
            skLineSegment(sketch, "E329", {"start": v(-14.3, -9.05) * mm, "end": v(-14.2, -9.3) * mm});
            skLineSegment(sketch, "E330", {"start": v(-14.2, -9.3) * mm, "end": v(-14.06, -9.53) * mm});
            skLineSegment(sketch, "E331", {"start": v(-14.06, -9.53) * mm, "end": v(-13.88, -9.75) * mm});
            skLineSegment(sketch, "E332", {"start": v(-13.88, -9.75) * mm, "end": v(-13.66, -9.95) * mm});
            skLineSegment(sketch, "E333", {"start": v(-13.66, -9.95) * mm, "end": v(-13.42, -10.13) * mm});
            skLineSegment(sketch, "E334", {"start": v(-13.42, -10.13) * mm, "end": v(-13.17, -10.28) * mm});
            skLineSegment(sketch, "E335", {"start": v(-13.17, -10.28) * mm, "end": v(-12.91, -10.41) * mm});
            skLineSegment(sketch, "E336", {"start": v(-12.91, -10.41) * mm, "end": v(-12.67, -10.5) * mm});
            skLineSegment(sketch, "E337", {"start": v(-12.67, -10.5) * mm, "end": v(-12.46, -10.55) * mm});
            skLineSegment(sketch, "E338", {"start": v(-12.46, -10.55) * mm, "end": v(-12.23, -10.6) * mm});
            skLineSegment(sketch, "E339", {"start": v(-12.23, -10.6) * mm, "end": v(-12.01, -10.64) * mm});
            skLineSegment(sketch, "E340", {"start": v(-12.01, -10.64) * mm, "end": v(-11.82, -10.7) * mm});
            skLineSegment(sketch, "E341", {"start": v(-11.82, -10.7) * mm, "end": v(-11.9, -10.75) * mm});
            skLineSegment(sketch, "E342", {"start": v(-11.9, -10.75) * mm, "end": v(-12.23, -10.91) * mm});
            skLineSegment(sketch, "E343", {"start": v(-12.23, -10.91) * mm, "end": v(-12.66, -11.1) * mm});
            skLineSegment(sketch, "E344", {"start": v(-12.66, -11.1) * mm, "end": v(-12.88, -11.21) * mm});
            skLineSegment(sketch, "E345", {"start": v(-12.88, -11.21) * mm, "end": v(-13.1, -11.31) * mm});
            skLineSegment(sketch, "E346", {"start": v(-13.1, -11.31) * mm, "end": v(-13.32, -11.41) * mm});
            skLineSegment(sketch, "E347", {"start": v(-13.32, -11.41) * mm, "end": v(-13.53, -11.53) * mm});
            skLineSegment(sketch, "E348", {"start": v(-13.53, -11.53) * mm, "end": v(-13.37, -11.62) * mm});
            skLineSegment(sketch, "E349", {"start": v(-13.37, -11.62) * mm, "end": v(-12.97, -11.74) * mm});
            skLineSegment(sketch, "E350", {"start": v(-12.97, -11.74) * mm, "end": v(-12.55, -11.82) * mm});
            skLineSegment(sketch, "E351", {"start": v(-12.55, -11.82) * mm, "end": v(-12.12, -11.85) * mm});
            skLineSegment(sketch, "E352", {"start": v(-12.12, -11.85) * mm, "end": v(-11.67, -11.84) * mm});
            skLineSegment(sketch, "E353", {"start": v(-11.67, -11.84) * mm, "end": v(-11.23, -11.8) * mm});
            skLineSegment(sketch, "E354", {"start": v(-11.23, -11.8) * mm, "end": v(-10.79, -11.75) * mm});
            skLineSegment(sketch, "E355", {"start": v(-10.79, -11.75) * mm, "end": v(-10.36, -11.68) * mm});
            skLineSegment(sketch, "E356", {"start": v(-10.36, -11.68) * mm, "end": v(-9.96, -11.6) * mm});
            skLineSegment(sketch, "E357", {"start": v(-9.96, -11.6) * mm, "end": v(-10.04, -11.7) * mm});
            skLineSegment(sketch, "E358", {"start": v(-10.04, -11.7) * mm, "end": v(-10.16, -11.81) * mm});
            skLineSegment(sketch, "E359", {"start": v(-10.16, -11.81) * mm, "end": v(-10.32, -11.94) * mm});
            skLineSegment(sketch, "E360", {"start": v(-10.32, -11.94) * mm, "end": v(-10.49, -12.06) * mm});
            skLineSegment(sketch, "E361", {"start": v(-10.49, -12.06) * mm, "end": v(-10.85, -12.3) * mm});
            skLineSegment(sketch, "E362", {"start": v(-10.85, -12.3) * mm, "end": v(-11.15, -12.5) * mm});
            skLineSegment(sketch, "E363", {"start": v(-11.15, -12.5) * mm, "end": v(-11.38, -12.63) * mm});
            skLineSegment(sketch, "E364", {"start": v(-11.38, -12.63) * mm, "end": v(-11.63, -12.78) * mm});
            skLineSegment(sketch, "E365", {"start": v(-11.63, -12.78) * mm, "end": v(-11.42, -12.89) * mm});
            skLineSegment(sketch, "E366", {"start": v(-11.42, -12.89) * mm, "end": v(-10.8, -12.97) * mm});
            skLineSegment(sketch, "E367", {"start": v(-10.8, -12.97) * mm, "end": v(-10.2, -12.94) * mm});
            skLineSegment(sketch, "E368", {"start": v(-10.2, -12.94) * mm, "end": v(-9.64, -12.82) * mm});
            skLineSegment(sketch, "E369", {"start": v(-9.64, -12.82) * mm, "end": v(-9.11, -12.64) * mm});
            skLineSegment(sketch, "E370", {"start": v(-9.11, -12.64) * mm, "end": v(-8.63, -12.43) * mm});
            skLineSegment(sketch, "E371", {"start": v(-8.63, -12.43) * mm, "end": v(-8.2, -12.22) * mm});
            skLineSegment(sketch, "E372", {"start": v(-8.2, -12.22) * mm, "end": v(-7.85, -12.04) * mm});
            skLineSegment(sketch, "E373", {"start": v(-7.85, -12.04) * mm, "end": v(-7.56, -11.92) * mm});
            skLineSegment(sketch, "E374", {"start": v(-7.56, -11.92) * mm, "end": v(-7.69, -12.26) * mm});
            skLineSegment(sketch, "E375", {"start": v(-7.69, -12.26) * mm, "end": v(-7.84, -12.58) * mm});
            skLineSegment(sketch, "E376", {"start": v(-7.84, -12.58) * mm, "end": v(-8.02, -12.9) * mm});
            skLineSegment(sketch, "E377", {"start": v(-8.02, -12.9) * mm, "end": v(-8.2, -13.19) * mm});
            skLineSegment(sketch, "E378", {"start": v(-8.2, -13.19) * mm, "end": v(-8.4, -13.47) * mm});
            skLineSegment(sketch, "E379", {"start": v(-8.4, -13.47) * mm, "end": v(-8.6, -13.74) * mm});
            skLineSegment(sketch, "E380", {"start": v(-8.6, -13.74) * mm, "end": v(-8.8, -14) * mm});
            skLineSegment(sketch, "E381", {"start": v(-8.8, -14) * mm, "end": v(-8.98, -14.23) * mm});
            skLineSegment(sketch, "E382", {"start": v(-8.98, -14.23) * mm, "end": v(-8.68, -14.2) * mm});
            skLineSegment(sketch, "E383", {"start": v(-8.68, -14.2) * mm, "end": v(-8.39, -14.1) * mm});
            skLineSegment(sketch, "E384", {"start": v(-8.39, -14.1) * mm, "end": v(-8.1, -13.99) * mm});
            skLineSegment(sketch, "E385", {"start": v(-8.1, -13.99) * mm, "end": v(-7.82, -13.84) * mm});
            skLineSegment(sketch, "E386", {"start": v(-7.82, -13.84) * mm, "end": v(-7.57, -13.67) * mm});
            skLineSegment(sketch, "E387", {"start": v(-7.57, -13.67) * mm, "end": v(-7.34, -13.5) * mm});
            skLineSegment(sketch, "E388", {"start": v(-7.34, -13.5) * mm, "end": v(-7.14, -13.32) * mm});
            skLineSegment(sketch, "E389", {"start": v(-7.14, -13.32) * mm, "end": v(-6.98, -13.16) * mm});
            skLineSegment(sketch, "E390", {"start": v(-6.98, -13.16) * mm, "end": v(-6.83, -12.97) * mm});
            skLineSegment(sketch, "E391", {"start": v(-6.83, -12.97) * mm, "end": v(-6.74, -12.88) * mm});
            skLineSegment(sketch, "E392", {"start": v(-6.74, -12.88) * mm, "end": v(-6.67, -12.79) * mm});
            skLineSegment(sketch, "E393", {"start": v(-6.67, -12.79) * mm, "end": v(-6.6, -12.69) * mm});
            skLineSegment(sketch, "E394", {"start": v(-6.6, -12.69) * mm, "end": v(-6.52, -12.58) * mm});
            skLineSegment(sketch, "E395", {"start": v(-6.52, -12.58) * mm, "end": v(-6.26, -12.17) * mm});
            skLineSegment(sketch, "E396", {"start": v(-6.26, -12.17) * mm, "end": v(-6.04, -11.8) * mm});
            skLineSegment(sketch, "E397", {"start": v(-6.04, -11.8) * mm, "end": v(-5.96, -11.71) * mm});
            skLineSegment(sketch, "E398", {"start": v(-5.96, -11.71) * mm, "end": v(-6.01, -12.19) * mm});
            skLineSegment(sketch, "E399", {"start": v(-6.01, -12.19) * mm, "end": v(-6.1, -12.59) * mm});
            skLineSegment(sketch, "E400", {"start": v(-6.1, -12.59) * mm, "end": v(-6.2, -12.92) * mm});
            skLineSegment(sketch, "E401", {"start": v(-6.2, -12.92) * mm, "end": v(-6.34, -13.2) * mm});
            skLineSegment(sketch, "E402", {"start": v(-6.34, -13.2) * mm, "end": v(-6.47, -13.44) * mm});
            skLineSegment(sketch, "E403", {"start": v(-6.47, -13.44) * mm, "end": v(-6.59, -13.63) * mm});
            skLineSegment(sketch, "E404", {"start": v(-6.59, -13.63) * mm, "end": v(-6.7, -13.8) * mm});
            skLineSegment(sketch, "E405", {"start": v(-6.7, -13.8) * mm, "end": v(-6.76, -13.94) * mm});
            skLineSegment(sketch, "E406", {"start": v(-6.76, -13.94) * mm, "end": v(-6.5, -13.82) * mm});
            skLineSegment(sketch, "E407", {"start": v(-6.5, -13.82) * mm, "end": v(-6.24, -13.7) * mm});
            skLineSegment(sketch, "E408", {"start": v(-6.24, -13.7) * mm, "end": v(-5.97, -13.56) * mm});
            skLineSegment(sketch, "E409", {"start": v(-5.97, -13.56) * mm, "end": v(-5.72, -13.42) * mm});
            skLineSegment(sketch, "E410", {"start": v(-5.72, -13.42) * mm, "end": v(-5.52, -13.29) * mm});
            skLineSegment(sketch, "E411", {"start": v(-5.52, -13.29) * mm, "end": v(-5.37, -13.19) * mm});
            skLineSegment(sketch, "E412", {"start": v(-5.37, -13.19) * mm, "end": v(-5.27, -13.1) * mm});
            skLineSegment(sketch, "E413", {"start": v(-5.27, -13.1) * mm, "end": v(-5.19, -13.03) * mm});
            skLineSegment(sketch, "E414", {"start": v(-5.19, -13.03) * mm, "end": v(-5.06, -12.9) * mm});
            skLineSegment(sketch, "E415", {"start": v(-5.06, -12.9) * mm, "end": v(-4.86, -12.71) * mm});
            skLineSegment(sketch, "E416", {"start": v(-4.86, -12.71) * mm, "end": v(-4.57, -13.61) * mm});
            skLineSegment(sketch, "E417", {"start": v(-4.57, -13.61) * mm, "end": v(-6.43, -15.2) * mm});
            skLineSegment(sketch, "E418", {"start": v(-6.43, -15.2) * mm, "end": v(-7.03, -15.86) * mm});
            skLineSegment(sketch, "E419", {"start": v(-7.03, -15.86) * mm, "end": v(-7.35, -16.25) * mm});
            skLineSegment(sketch, "E420", {"start": v(-7.35, -16.25) * mm, "end": v(-7.66, -16.67) * mm});
            skLineSegment(sketch, "E421", {"start": v(-7.66, -16.67) * mm, "end": v(-7.96, -17.1) * mm});
            skLineSegment(sketch, "E422", {"start": v(-7.96, -17.1) * mm, "end": v(-8.24, -17.56) * mm});
            skLineSegment(sketch, "E423", {"start": v(-8.24, -17.56) * mm, "end": v(-8.5, -18.03) * mm});
            skLineSegment(sketch, "E424", {"start": v(-8.5, -18.03) * mm, "end": v(-8.73, -18.5) * mm});
            skLineSegment(sketch, "E425", {"start": v(-8.73, -18.5) * mm, "end": v(-8.94, -18.98) * mm});
            skLineSegment(sketch, "E426", {"start": v(-8.94, -18.98) * mm, "end": v(-9.1, -19.45) * mm});
            skLineSegment(sketch, "E427", {"start": v(-9.1, -19.45) * mm, "end": v(-9.21, -19.77) * mm});
            skLineSegment(sketch, "E428", {"start": v(-9.21, -19.77) * mm, "end": v(-9.32, -20.1) * mm});
            skLineSegment(sketch, "E429", {"start": v(-9.32, -20.1) * mm, "end": v(-9.43, -20.45) * mm});
            skLineSegment(sketch, "E430", {"start": v(-9.43, -20.45) * mm, "end": v(-9.53, -20.8) * mm});
            skLineSegment(sketch, "E431", {"start": v(-9.53, -20.8) * mm, "end": v(-9.63, -21.15) * mm});
            skLineSegment(sketch, "E432", {"start": v(-9.63, -21.15) * mm, "end": v(-9.72, -21.5) * mm});
            skLineSegment(sketch, "E433", {"start": v(-9.72, -21.5) * mm, "end": v(-9.79, -21.85) * mm});
            skLineSegment(sketch, "E434", {"start": v(-9.79, -21.85) * mm, "end": v(-9.84, -22.2) * mm});
            skLineSegment(sketch, "E435", {"start": v(-9.84, -22.2) * mm, "end": v(-9.67, -22.29) * mm});
            skLineSegment(sketch, "E436", {"start": v(-9.67, -22.29) * mm, "end": v(-9.44, -22.34) * mm});
            skLineSegment(sketch, "E437", {"start": v(-9.44, -22.34) * mm, "end": v(-9.19, -22.38) * mm});
            skLineSegment(sketch, "E438", {"start": v(-9.19, -22.38) * mm, "end": v(-8.92, -22.4) * mm});
            skLineSegment(sketch, "E439", {"start": v(-8.92, -22.4) * mm, "end": v(-8.64, -22.38) * mm});
            skLineSegment(sketch, "E440", {"start": v(-8.64, -22.38) * mm, "end": v(-8.38, -22.36) * mm});
            skLineSegment(sketch, "E441", {"start": v(-8.38, -22.36) * mm, "end": v(-8.14, -22.33) * mm});
            skLineSegment(sketch, "E442", {"start": v(-8.14, -22.33) * mm, "end": v(-7.94, -22.28) * mm});
            skLineSegment(sketch, "E443", {"start": v(-7.94, -22.28) * mm, "end": v(-7.9, -22.4) * mm});
            skLineSegment(sketch, "E444", {"start": v(-7.9, -22.4) * mm, "end": v(-7.84, -22.6) * mm});
            skLineSegment(sketch, "E445", {"start": v(-7.84, -22.6) * mm, "end": v(-7.78, -22.85) * mm});
            skLineSegment(sketch, "E446", {"start": v(-7.78, -22.85) * mm, "end": v(-7.7, -23.12) * mm});
            skLineSegment(sketch, "E447", {"start": v(-7.7, -23.12) * mm, "end": v(-7.63, -23.38) * mm});
            skLineSegment(sketch, "E448", {"start": v(-7.63, -23.38) * mm, "end": v(-7.54, -23.61) * mm});
            skLineSegment(sketch, "E449", {"start": v(-7.54, -23.61) * mm, "end": v(-7.45, -23.8) * mm});
            skLineSegment(sketch, "E450", {"start": v(-7.45, -23.8) * mm, "end": v(-7.35, -23.9) * mm});
            skLineSegment(sketch, "E451", {"start": v(-7.35, -23.9) * mm, "end": v(-7.13, -23.96) * mm});
            skLineSegment(sketch, "E452", {"start": v(-7.13, -23.96) * mm, "end": v(-6.89, -23.99) * mm});
            skLineSegment(sketch, "E453", {"start": v(-6.89, -23.99) * mm, "end": v(-6.63, -23.97) * mm});
            skLineSegment(sketch, "E454", {"start": v(-6.63, -23.97) * mm, "end": v(-6.38, -23.92) * mm});
            skLineSegment(sketch, "E455", {"start": v(-6.38, -23.92) * mm, "end": v(-6.12, -23.86) * mm});
            skLineSegment(sketch, "E456", {"start": v(-6.12, -23.86) * mm, "end": v(-5.88, -23.79) * mm});
            skLineSegment(sketch, "E457", {"start": v(-5.88, -23.79) * mm, "end": v(-5.65, -23.73) * mm});
            skLineSegment(sketch, "E458", {"start": v(-5.65, -23.73) * mm, "end": v(-5.46, -23.68) * mm});
            skLineSegment(sketch, "E459", {"start": v(-5.46, -23.68) * mm, "end": v(-5.38, -23.76) * mm});
            skLineSegment(sketch, "E460", {"start": v(-5.38, -23.76) * mm, "end": v(-5.34, -23.83) * mm});
            skLineSegment(sketch, "E461", {"start": v(-5.34, -23.83) * mm, "end": v(-5.3, -23.9) * mm});
            skLineSegment(sketch, "E462", {"start": v(-5.3, -23.9) * mm, "end": v(-5.23, -24) * mm});
            skLineSegment(sketch, "E463", {"start": v(-5.23, -24) * mm, "end": v(-5.05, -24.2) * mm});
            skLineSegment(sketch, "E464", {"start": v(-5.05, -24.2) * mm, "end": v(-4.8, -24.44) * mm});
            skLineSegment(sketch, "E465", {"start": v(-4.8, -24.44) * mm, "end": v(-4.67, -24.56) * mm});
            skLineSegment(sketch, "E466", {"start": v(-4.67, -24.56) * mm, "end": v(-4.55, -24.66) * mm});
            skLineSegment(sketch, "E467", {"start": v(-4.55, -24.66) * mm, "end": v(-4.44, -24.74) * mm});
            skLineSegment(sketch, "E468", {"start": v(-4.44, -24.74) * mm, "end": v(-4.34, -24.78) * mm});
            skLineSegment(sketch, "E469", {"start": v(-4.34, -24.78) * mm, "end": v(-4.17, -24.8) * mm});
            skLineSegment(sketch, "E470", {"start": v(-4.17, -24.8) * mm, "end": v(-3.94, -24.75) * mm});
            skLineSegment(sketch, "E471", {"start": v(-3.94, -24.75) * mm, "end": v(-3.69, -24.67) * mm});
            skLineSegment(sketch, "E472", {"start": v(-3.69, -24.67) * mm, "end": v(-3.42, -24.57) * mm});
            skLineSegment(sketch, "E473", {"start": v(-3.42, -24.57) * mm, "end": v(-3.18, -24.46) * mm});
            skLineSegment(sketch, "E474", {"start": v(-3.18, -24.46) * mm, "end": v(-2.96, -24.37) * mm});
            skLineSegment(sketch, "E475", {"start": v(-2.96, -24.37) * mm, "end": v(-2.8, -24.3) * mm});
            skLineSegment(sketch, "E476", {"start": v(-2.8, -24.3) * mm, "end": v(-2.73, -24.27) * mm});
            skLineSegment(sketch, "E477", {"start": v(-2.73, -24.27) * mm, "end": v(-2.68, -24.3) * mm});
            skLineSegment(sketch, "E478", {"start": v(-2.68, -24.3) * mm, "end": v(-2.63, -24.35) * mm});
            skLineSegment(sketch, "E479", {"start": v(-2.63, -24.35) * mm, "end": v(-2.6, -24.41) * mm});
            skLineSegment(sketch, "E480", {"start": v(-2.6, -24.41) * mm, "end": v(-2.55, -24.5) * mm});
            skLineSegment(sketch, "E481", {"start": v(-2.55, -24.5) * mm, "end": v(-2.5, -24.58) * mm});
            skLineSegment(sketch, "E482", {"start": v(-2.5, -24.58) * mm, "end": v(-2.43, -24.69) * mm});
            skLineSegment(sketch, "E483", {"start": v(-2.43, -24.69) * mm, "end": v(-2.34, -24.8) * mm});
            skLineSegment(sketch, "E484", {"start": v(-2.34, -24.8) * mm, "end": v(-2.21, -24.93) * mm});
            skLineSegment(sketch, "E485", {"start": v(-2.21, -24.93) * mm, "end": v(-2.08, -25.04) * mm});
            skLineSegment(sketch, "E486", {"start": v(-2.08, -25.04) * mm, "end": v(-1.87, -25.18) * mm});
            skLineSegment(sketch, "E487", {"start": v(-1.87, -25.18) * mm, "end": v(-1.76, -25.25) * mm});
            skLineSegment(sketch, "E488", {"start": v(-1.76, -25.25) * mm, "end": v(-1.65, -25.31) * mm});
            skLineSegment(sketch, "E489", {"start": v(-1.65, -25.31) * mm, "end": v(-1.55, -25.36) * mm});
            skLineSegment(sketch, "E490", {"start": v(-1.55, -25.36) * mm, "end": v(-1.48, -25.38) * mm});
            skLineSegment(sketch, "E491", {"start": v(-1.48, -25.38) * mm, "end": v(-1.3, -25.37) * mm});
            skLineSegment(sketch, "E492", {"start": v(-1.3, -25.37) * mm, "end": v(-1.08, -25.31) * mm});
            skLineSegment(sketch, "E493", {"start": v(-1.08, -25.31) * mm, "end": v(-0.84, -25.22) * mm});
            skLineSegment(sketch, "E494", {"start": v(-0.84, -25.22) * mm, "end": v(-0.59, -25.1) * mm});
            skLineSegment(sketch, "E495", {"start": v(-0.59, -25.1) * mm, "end": v(-0.35, -24.97) * mm});
            skLineSegment(sketch, "E496", {"start": v(-0.35, -24.97) * mm, "end": v(-0.13, -24.84) * mm});
            skLineSegment(sketch, "E497", {"start": v(-0.13, -24.84) * mm, "end": v(0.06, -24.73) * mm});
            skLineSegment(sketch, "E498", {"start": v(0.06, -24.73) * mm, "end": v(0.19, -24.64) * mm});
            skLineSegment(sketch, "E499", {"start": v(0.19, -24.64) * mm, "end": v(0.34, -24.75) * mm});
            skLineSegment(sketch, "E500", {"start": v(0.34, -24.75) * mm, "end": v(0.52, -24.86) * mm});
            skLineSegment(sketch, "E501", {"start": v(0.52, -24.86) * mm, "end": v(0.72, -24.98) * mm});
            skLineSegment(sketch, "E502", {"start": v(0.72, -24.98) * mm, "end": v(0.94, -25.1) * mm});
            skLineSegment(sketch, "E503", {"start": v(0.94, -25.1) * mm, "end": v(1.17, -25.22) * mm});
            skLineSegment(sketch, "E504", {"start": v(1.17, -25.22) * mm, "end": v(1.4, -25.32) * mm});
            skLineSegment(sketch, "E505", {"start": v(1.4, -25.32) * mm, "end": v(1.62, -25.4) * mm});
            skLineSegment(sketch, "E506", {"start": v(1.62, -25.4) * mm, "end": v(1.83, -25.44) * mm});
            skLineSegment(sketch, "E507", {"start": v(1.83, -25.44) * mm, "end": v(1.94, -25.44) * mm});
            skLineSegment(sketch, "E508", {"start": v(1.94, -25.44) * mm, "end": v(2.03, -25.43) * mm});
            skLineSegment(sketch, "E509", {"start": v(2.03, -25.43) * mm, "end": v(2.12, -25.4) * mm});
            skLineSegment(sketch, "E510", {"start": v(2.12, -25.4) * mm, "end": v(2.2, -25.34) * mm});
            skLineSegment(sketch, "E511", {"start": v(2.2, -25.34) * mm, "end": v(2.36, -25.19) * mm});
            skLineSegment(sketch, "E512", {"start": v(2.36, -25.19) * mm, "end": v(2.55, -24.98) * mm});
            skLineSegment(sketch, "E513", {"start": v(2.55, -24.98) * mm, "end": v(2.83, -24.64) * mm});
            skLineSegment(sketch, "E514", {"start": v(2.83, -24.64) * mm, "end": v(2.9, -24.54) * mm});
            skLineSegment(sketch, "E515", {"start": v(2.9, -24.54) * mm, "end": v(2.95, -24.45) * mm});
            skLineSegment(sketch, "E516", {"start": v(2.95, -24.45) * mm, "end": v(3, -24.36) * mm});
            skLineSegment(sketch, "E517", {"start": v(3, -24.36) * mm, "end": v(3.08, -24.26) * mm});
            skLineSegment(sketch, "E518", {"start": v(3.08, -24.26) * mm, "end": v(3.26, -24.34) * mm});
            skLineSegment(sketch, "E519", {"start": v(3.26, -24.34) * mm, "end": v(3.43, -24.43) * mm});
            skLineSegment(sketch, "E520", {"start": v(3.43, -24.43) * mm, "end": v(3.6, -24.5) * mm});
            skLineSegment(sketch, "E521", {"start": v(3.6, -24.5) * mm, "end": v(3.8, -24.59) * mm});
            skLineSegment(sketch, "E522", {"start": v(3.8, -24.59) * mm, "end": v(4.1, -24.69) * mm});
            skLineSegment(sketch, "E523", {"start": v(4.1, -24.69) * mm, "end": v(4.32, -24.76) * mm});
            skLineSegment(sketch, "E524", {"start": v(4.32, -24.76) * mm, "end": v(4.5, -24.79) * mm});
            skLineSegment(sketch, "E525", {"start": v(4.5, -24.79) * mm, "end": v(4.65, -24.78) * mm});
            skLineSegment(sketch, "E526", {"start": v(4.65, -24.78) * mm, "end": v(4.8, -24.72) * mm});
            skLineSegment(sketch, "E527", {"start": v(4.8, -24.72) * mm, "end": v(4.94, -24.63) * mm});
            skLineSegment(sketch, "E528", {"start": v(4.94, -24.63) * mm, "end": v(5.1, -24.48) * mm});
            skLineSegment(sketch, "E529", {"start": v(5.1, -24.48) * mm, "end": v(5.31, -24.29) * mm});
            skLineSegment(sketch, "E530", {"start": v(5.31, -24.29) * mm, "end": v(5.45, -24.14) * mm});
            skLineSegment(sketch, "E531", {"start": v(5.45, -24.14) * mm, "end": v(5.57, -23.98) * mm});
            skLineSegment(sketch, "E532", {"start": v(5.57, -23.98) * mm, "end": v(5.7, -23.82) * mm});
            skLineSegment(sketch, "E533", {"start": v(5.7, -23.82) * mm, "end": v(5.82, -23.67) * mm});
            skLineSegment(sketch, "E534", {"start": v(5.82, -23.67) * mm, "end": v(5.99, -23.72) * mm});
            skLineSegment(sketch, "E535", {"start": v(5.99, -23.72) * mm, "end": v(6.23, -23.8) * mm});
            skLineSegment(sketch, "E536", {"start": v(6.23, -23.8) * mm, "end": v(6.53, -23.87) * mm});
            skLineSegment(sketch, "E537", {"start": v(6.53, -23.87) * mm, "end": v(6.84, -23.94) * mm});
            skLineSegment(sketch, "E538", {"start": v(6.84, -23.94) * mm, "end": v(7.15, -23.98) * mm});
            skLineSegment(sketch, "E539", {"start": v(7.15, -23.98) * mm, "end": v(7.43, -23.99) * mm});
            skLineSegment(sketch, "E540", {"start": v(7.43, -23.99) * mm, "end": v(7.64, -23.94) * mm});
            skLineSegment(sketch, "E541", {"start": v(7.64, -23.94) * mm, "end": v(7.77, -23.83) * mm});
            skLineSegment(sketch, "E542", {"start": v(7.77, -23.83) * mm, "end": v(7.7, -23.75) * mm});
            skLineSegment(sketch, "E543", {"start": v(7.7, -23.75) * mm, "end": v(7.62, -23.69) * mm});
            skLineSegment(sketch, "E544", {"start": v(7.62, -23.69) * mm, "end": v(7.52, -23.64) * mm});
            skLineSegment(sketch, "E545", {"start": v(7.52, -23.64) * mm, "end": v(7.4, -23.6) * mm});
            skLineSegment(sketch, "E546", {"start": v(7.4, -23.6) * mm, "end": v(7.2, -23.56) * mm});
            skLineSegment(sketch, "E547", {"start": v(7.2, -23.56) * mm, "end": v(7.02, -23.52) * mm});
            skLineSegment(sketch, "E548", {"start": v(7.02, -23.52) * mm, "end": v(6.98, -23.5) * mm});
            skLineSegment(sketch, "E549", {"start": v(6.98, -23.5) * mm, "end": v(6.8, -23.47) * mm});
            skLineSegment(sketch, "E550", {"start": v(6.8, -23.47) * mm, "end": v(6.65, -23.45) * mm});
            skLineSegment(sketch, "E551", {"start": v(6.65, -23.45) * mm, "end": v(6.53, -23.43) * mm});
            skLineSegment(sketch, "E552", {"start": v(6.53, -23.43) * mm, "end": v(6.42, -23.4) * mm});
            skLineSegment(sketch, "E553", {"start": v(6.42, -23.4) * mm, "end": v(6.32, -23.37) * mm});
            skLineSegment(sketch, "E554", {"start": v(6.32, -23.37) * mm, "end": v(6.22, -23.32) * mm});
            skLineSegment(sketch, "E555", {"start": v(6.22, -23.32) * mm, "end": v(6.1, -23.26) * mm});
            skLineSegment(sketch, "E556", {"start": v(6.1, -23.26) * mm, "end": v(5.95, -23.19) * mm});
            skLineSegment(sketch, "E557", {"start": v(5.95, -23.19) * mm, "end": v(5.92, -22.99) * mm});
            skLineSegment(sketch, "E558", {"start": v(5.92, -22.99) * mm, "end": v(5.88, -22.75) * mm});
            skLineSegment(sketch, "E559", {"start": v(5.88, -22.75) * mm, "end": v(5.83, -22.48) * mm});
            skLineSegment(sketch, "E560", {"start": v(5.83, -22.48) * mm, "end": v(5.77, -22.2) * mm});
            skLineSegment(sketch, "E561", {"start": v(5.77, -22.2) * mm, "end": v(5.7, -21.92) * mm});
            skLineSegment(sketch, "E562", {"start": v(5.7, -21.92) * mm, "end": v(5.64, -21.65) * mm});
            skLineSegment(sketch, "E563", {"start": v(5.64, -21.65) * mm, "end": v(5.58, -21.4) * mm});
            skLineSegment(sketch, "E564", {"start": v(5.58, -21.4) * mm, "end": v(5.52, -21.2) * mm});
            skLineSegment(sketch, "E565", {"start": v(5.52, -21.2) * mm, "end": v(5.47, -21.04) * mm});
            skLineSegment(sketch, "E566", {"start": v(5.47, -21.04) * mm, "end": v(5.41, -20.87) * mm});
            skLineSegment(sketch, "E567", {"start": v(5.41, -20.87) * mm, "end": v(5.36, -20.7) * mm});
            skLineSegment(sketch, "E568", {"start": v(5.36, -20.7) * mm, "end": v(5.34, -20.52) * mm});
            skLineSegment(sketch, "E569", {"start": v(5.34, -20.52) * mm, "end": v(5.48, -20.48) * mm});
            skLineSegment(sketch, "E570", {"start": v(5.48, -20.48) * mm, "end": v(5.59, -20.42) * mm});
            skLineSegment(sketch, "E571", {"start": v(5.59, -20.42) * mm, "end": v(5.68, -20.36) * mm});
            skLineSegment(sketch, "E572", {"start": v(5.68, -20.36) * mm, "end": v(5.76, -20.3) * mm});
            skLineSegment(sketch, "E573", {"start": v(5.76, -20.3) * mm, "end": v(5.84, -20.23) * mm});
            skLineSegment(sketch, "E574", {"start": v(5.84, -20.23) * mm, "end": v(5.93, -20.17) * mm});
            skLineSegment(sketch, "E575", {"start": v(5.93, -20.17) * mm, "end": v(6.04, -20.11) * mm});
            skLineSegment(sketch, "E576", {"start": v(6.04, -20.11) * mm, "end": v(6.18, -20.07) * mm});
            skLineSegment(sketch, "E577", {"start": v(6.18, -20.07) * mm, "end": v(6.32, -20.03) * mm});
            skLineSegment(sketch, "E578", {"start": v(6.32, -20.03) * mm, "end": v(6.45, -19.98) * mm});
            skLineSegment(sketch, "E579", {"start": v(6.45, -19.98) * mm, "end": v(6.56, -19.94) * mm});
            skLineSegment(sketch, "E580", {"start": v(6.56, -19.94) * mm, "end": v(6.66, -19.88) * mm});
            skLineSegment(sketch, "E581", {"start": v(6.66, -19.88) * mm, "end": v(6.76, -19.82) * mm});
            skLineSegment(sketch, "E582", {"start": v(6.76, -19.82) * mm, "end": v(6.85, -19.76) * mm});
            skLineSegment(sketch, "E583", {"start": v(6.85, -19.76) * mm, "end": v(6.93, -19.68) * mm});
            skLineSegment(sketch, "E584", {"start": v(6.93, -19.68) * mm, "end": v(7.02, -19.6) * mm});
            skLineSegment(sketch, "E585", {"start": v(7.02, -19.6) * mm, "end": v(7.08, -19.67) * mm});
            skLineSegment(sketch, "E586", {"start": v(7.08, -19.67) * mm, "end": v(7.15, -19.8) * mm});
            skLineSegment(sketch, "E587", {"start": v(7.15, -19.8) * mm, "end": v(7.23, -19.98) * mm});
            skLineSegment(sketch, "E588", {"start": v(7.23, -19.98) * mm, "end": v(7.3, -20.17) * mm});
            skLineSegment(sketch, "E589", {"start": v(7.3, -20.17) * mm, "end": v(7.46, -20.55) * mm});
            skLineSegment(sketch, "E590", {"start": v(7.46, -20.55) * mm, "end": v(7.57, -20.83) * mm});
            skLineSegment(sketch, "E591", {"start": v(7.57, -20.83) * mm, "end": v(7.68, -21.14) * mm});
            skLineSegment(sketch, "E592", {"start": v(7.68, -21.14) * mm, "end": v(7.81, -21.5) * mm});
            skLineSegment(sketch, "E593", {"start": v(7.81, -21.5) * mm, "end": v(7.87, -21.7) * mm});
            skLineSegment(sketch, "E594", {"start": v(7.87, -21.7) * mm, "end": v(7.9, -21.87) * mm});
            skLineSegment(sketch, "E595", {"start": v(7.9, -21.87) * mm, "end": v(7.91, -22.05) * mm});
            skLineSegment(sketch, "E596", {"start": v(7.91, -22.05) * mm, "end": v(7.9, -22.21) * mm});
            skLineSegment(sketch, "E597", {"start": v(7.9, -22.21) * mm, "end": v(8.27, -22.26) * mm});
            skLineSegment(sketch, "E598", {"start": v(8.27, -22.26) * mm, "end": v(8.5, -22.35) * mm});
            skLineSegment(sketch, "E599", {"start": v(8.5, -22.35) * mm, "end": v(8.75, -22.39) * mm});
            skLineSegment(sketch, "E600", {"start": v(8.75, -22.39) * mm, "end": v(9, -22.4) * mm});
            skLineSegment(sketch, "E601", {"start": v(9, -22.4) * mm, "end": v(9.24, -22.38) * mm});
            skLineSegment(sketch, "E602", {"start": v(9.24, -22.38) * mm, "end": v(9.48, -22.35) * mm});
            skLineSegment(sketch, "E603", {"start": v(9.48, -22.35) * mm, "end": v(9.72, -22.31) * mm});
            skLineSegment(sketch, "E604", {"start": v(9.72, -22.31) * mm, "end": v(9.96, -22.27) * mm});
            skLineSegment(sketch, "E605", {"start": v(9.96, -22.27) * mm, "end": v(10.18, -22.24) * mm});
            skLineSegment(sketch, "E606", {"start": v(10.18, -22.24) * mm, "end": v(10.16, -21.96) * mm});
            skLineSegment(sketch, "E607", {"start": v(10.16, -21.96) * mm, "end": v(10.1, -21.61) * mm});
            skLineSegment(sketch, "E608", {"start": v(10.1, -21.61) * mm, "end": v(10, -21.22) * mm});
            skLineSegment(sketch, "E609", {"start": v(10, -21.22) * mm, "end": v(9.9, -20.8) * mm});
            skLineSegment(sketch, "E610", {"start": v(9.9, -20.8) * mm, "end": v(9.77, -20.4) * mm});
            skLineSegment(sketch, "E611", {"start": v(9.77, -20.4) * mm, "end": v(9.65, -20.01) * mm});
            skLineSegment(sketch, "E612", {"start": v(9.65, -20.01) * mm, "end": v(9.53, -19.67) * mm});
            skLineSegment(sketch, "E613", {"start": v(9.53, -19.67) * mm, "end": v(9.44, -19.4) * mm});
            skLineSegment(sketch, "E614", {"start": v(9.44, -19.4) * mm, "end": v(9.29, -19) * mm});
            skLineSegment(sketch, "E615", {"start": v(9.29, -19) * mm, "end": v(9.12, -18.61) * mm});
            skLineSegment(sketch, "E616", {"start": v(9.12, -18.61) * mm, "end": v(8.95, -18.23) * mm});
            skLineSegment(sketch, "E617", {"start": v(8.95, -18.23) * mm, "end": v(8.76, -17.86) * mm});
            skLineSegment(sketch, "E618", {"start": v(8.76, -17.86) * mm, "end": v(8.55, -17.5) * mm});
            skLineSegment(sketch, "E619", {"start": v(8.55, -17.5) * mm, "end": v(8.34, -17.15) * mm});
            skLineSegment(sketch, "E620", {"start": v(8.34, -17.15) * mm, "end": v(8.11, -16.8) * mm});
            skLineSegment(sketch, "E621", {"start": v(8.11, -16.8) * mm, "end": v(7.87, -16.48) * mm});
            skLineSegment(sketch, "E622", {"start": v(7.87, -16.48) * mm, "end": v(7.78, -16.34) * mm});
            skLineSegment(sketch, "E623", {"start": v(7.78, -16.34) * mm, "end": v(7.7, -16.2) * mm});
            skLineSegment(sketch, "E624", {"start": v(7.7, -16.2) * mm, "end": v(7.66, -16.12) * mm});
            skLineSegment(sketch, "E625", {"start": v(7.66, -16.12) * mm, "end": v(7.62, -16.06) * mm});
            skLineSegment(sketch, "E626", {"start": v(7.62, -16.06) * mm, "end": v(7.56, -16) * mm});
            skLineSegment(sketch, "E627", {"start": v(7.56, -16) * mm, "end": v(7.5, -15.93) * mm});
            skLineSegment(sketch, "E628", {"start": v(7.5, -15.93) * mm, "end": v(7.37, -15.83) * mm});
            skLineSegment(sketch, "E629", {"start": v(7.37, -15.83) * mm, "end": v(7.22, -15.68) * mm});
            skLineSegment(sketch, "E630", {"start": v(7.22, -15.68) * mm, "end": v(7.05, -15.5) * mm});
            skLineSegment(sketch, "E631", {"start": v(7.05, -15.5) * mm, "end": v(6.87, -15.32) * mm});
            skLineSegment(sketch, "E632", {"start": v(6.87, -15.32) * mm, "end": v(6.68, -15.12) * mm});
            skLineSegment(sketch, "E633", {"start": v(6.68, -15.12) * mm, "end": v(6.5, -14.93) * mm});
            skLineSegment(sketch, "E634", {"start": v(6.5, -14.93) * mm, "end": v(6.3, -14.75) * mm});
            skLineSegment(sketch, "E635", {"start": v(6.3, -14.75) * mm, "end": v(6.13, -14.59) * mm});
            skLineSegment(sketch, "E636", {"start": v(6.13, -14.59) * mm, "end": v(5.95, -14.43) * mm});
            skLineSegment(sketch, "E637", {"start": v(5.95, -14.43) * mm, "end": v(5.76, -14.27) * mm});
            skLineSegment(sketch, "E638", {"start": v(5.76, -14.27) * mm, "end": v(5.57, -14.1) * mm});
            skLineSegment(sketch, "E639", {"start": v(5.57, -14.1) * mm, "end": v(5.38, -13.95) * mm});
            skLineSegment(sketch, "E640", {"start": v(5.38, -13.95) * mm, "end": v(5.18, -13.8) * mm});
            skLineSegment(sketch, "E641", {"start": v(5.18, -13.8) * mm, "end": v(4.98, -13.66) * mm});
            skLineSegment(sketch, "E642", {"start": v(4.98, -13.66) * mm, "end": v(4.78, -13.53) * mm});
            skLineSegment(sketch, "E643", {"start": v(4.78, -13.53) * mm, "end": v(4.56, -13.4) * mm});
            skLineSegment(sketch, "E644", {"start": v(4.56, -13.4) * mm, "end": v(4.76, -12.63) * mm});
            skLineSegment(sketch, "E645", {"start": v(4.76, -12.63) * mm, "end": v(4.88, -12.73) * mm});
            skLineSegment(sketch, "E646", {"start": v(4.88, -12.73) * mm, "end": v(5.1, -12.93) * mm});
            skLineSegment(sketch, "E647", {"start": v(5.1, -12.93) * mm, "end": v(5.23, -13.04) * mm});
            skLineSegment(sketch, "E648", {"start": v(5.23, -13.04) * mm, "end": v(5.37, -13.16) * mm});
            skLineSegment(sketch, "E649", {"start": v(5.37, -13.16) * mm, "end": v(5.51, -13.27) * mm});
            skLineSegment(sketch, "E650", {"start": v(5.51, -13.27) * mm, "end": v(5.64, -13.37) * mm});
            skLineSegment(sketch, "E651", {"start": v(5.64, -13.37) * mm, "end": v(5.88, -13.51) * mm});
            skLineSegment(sketch, "E652", {"start": v(5.88, -13.51) * mm, "end": v(6.17, -13.67) * mm});
            skLineSegment(sketch, "E653", {"start": v(6.17, -13.67) * mm, "end": v(6.32, -13.74) * mm});
            skLineSegment(sketch, "E654", {"start": v(6.32, -13.74) * mm, "end": v(6.47, -13.81) * mm});
            skLineSegment(sketch, "E655", {"start": v(6.47, -13.81) * mm, "end": v(6.6, -13.87) * mm});
            skLineSegment(sketch, "E656", {"start": v(6.6, -13.87) * mm, "end": v(6.74, -13.92) * mm});
            skLineSegment(sketch, "E657", {"start": v(6.74, -13.92) * mm, "end": v(6.67, -13.78) * mm});
            skLineSegment(sketch, "E658", {"start": v(6.67, -13.78) * mm, "end": v(6.56, -13.6) * mm});
            skLineSegment(sketch, "E659", {"start": v(6.56, -13.6) * mm, "end": v(6.43, -13.37) * mm});
            skLineSegment(sketch, "E660", {"start": v(6.43, -13.37) * mm, "end": v(6.3, -13.1) * mm});
            skLineSegment(sketch, "E661", {"start": v(6.3, -13.1) * mm, "end": v(6.16, -12.8) * mm});
            skLineSegment(sketch, "E662", {"start": v(6.16, -12.8) * mm, "end": v(6.05, -12.46) * mm});
            skLineSegment(sketch, "E663", {"start": v(6.05, -12.46) * mm, "end": v(5.98, -12.08) * mm});
            skLineSegment(sketch, "E664", {"start": v(5.98, -12.08) * mm, "end": v(5.96, -11.67) * mm});
            skLineSegment(sketch, "E665", {"start": v(5.96, -11.67) * mm, "end": v(6.08, -11.88) * mm});
            skLineSegment(sketch, "E666", {"start": v(6.08, -11.88) * mm, "end": v(6.2, -12.09) * mm});
            skLineSegment(sketch, "E667", {"start": v(6.2, -12.09) * mm, "end": v(6.34, -12.3) * mm});
            skLineSegment(sketch, "E668", {"start": v(6.34, -12.3) * mm, "end": v(6.47, -12.5) * mm});
            skLineSegment(sketch, "E669", {"start": v(6.47, -12.5) * mm, "end": v(6.7, -12.8) * mm});
            skLineSegment(sketch, "E670", {"start": v(6.7, -12.8) * mm, "end": v(6.94, -13.1) * mm});
            skLineSegment(sketch, "E671", {"start": v(6.94, -13.1) * mm, "end": v(7.2, -13.38) * mm});
            skLineSegment(sketch, "E672", {"start": v(7.2, -13.38) * mm, "end": v(7.5, -13.63) * mm});
            skLineSegment(sketch, "E673", {"start": v(7.5, -13.63) * mm, "end": v(7.83, -13.85) * mm});
            skLineSegment(sketch, "E674", {"start": v(7.83, -13.85) * mm, "end": v(8.18, -14.03) * mm});
            skLineSegment(sketch, "E675", {"start": v(8.18, -14.03) * mm, "end": v(8.57, -14.16) * mm});
            skLineSegment(sketch, "E676", {"start": v(8.57, -14.16) * mm, "end": v(8.98, -14.24) * mm});
            skLineSegment(sketch, "E677", {"start": v(8.98, -14.24) * mm, "end": v(8.18, -13.16) * mm});
            skLineSegment(sketch, "E678", {"start": v(8.18, -13.16) * mm, "end": v(8.03, -12.92) * mm});
            skLineSegment(sketch, "E679", {"start": v(8.03, -12.92) * mm, "end": v(7.84, -12.57) * mm});
            skLineSegment(sketch, "E680", {"start": v(7.84, -12.57) * mm, "end": v(7.75, -12.39) * mm});
            skLineSegment(sketch, "E681", {"start": v(7.75, -12.39) * mm, "end": v(7.67, -12.2) * mm});
            skLineSegment(sketch, "E682", {"start": v(7.67, -12.2) * mm, "end": v(7.6, -12.05) * mm});
            skLineSegment(sketch, "E683", {"start": v(7.6, -12.05) * mm, "end": v(7.58, -11.92) * mm});
            skLineSegment(sketch, "E684", {"start": v(7.58, -11.92) * mm, "end": v(7.78, -12.03) * mm});
            skLineSegment(sketch, "E685", {"start": v(7.78, -12.03) * mm, "end": v(8, -12.14) * mm});
            skLineSegment(sketch, "E686", {"start": v(8, -12.14) * mm, "end": v(8.2, -12.24) * mm});
            skLineSegment(sketch, "E687", {"start": v(8.2, -12.24) * mm, "end": v(8.43, -12.35) * mm});
            skLineSegment(sketch, "E688", {"start": v(8.43, -12.35) * mm, "end": v(8.65, -12.46) * mm});
            skLineSegment(sketch, "E689", {"start": v(8.65, -12.46) * mm, "end": v(8.88, -12.56) * mm});
            skLineSegment(sketch, "E690", {"start": v(8.88, -12.56) * mm, "end": v(9.12, -12.65) * mm});
            skLineSegment(sketch, "E691", {"start": v(9.12, -12.65) * mm, "end": v(9.36, -12.74) * mm});
            skLineSegment(sketch, "E692", {"start": v(9.36, -12.74) * mm, "end": v(9.59, -12.8) * mm});
            skLineSegment(sketch, "E693", {"start": v(9.59, -12.8) * mm, "end": v(9.87, -12.86) * mm});
            skLineSegment(sketch, "E694", {"start": v(9.87, -12.86) * mm, "end": v(10.2, -12.92) * mm});
            skLineSegment(sketch, "E695", {"start": v(10.2, -12.92) * mm, "end": v(10.53, -12.96) * mm});
            skLineSegment(sketch, "E696", {"start": v(10.53, -12.96) * mm, "end": v(10.86, -12.97) * mm});
            skLineSegment(sketch, "E697", {"start": v(10.86, -12.97) * mm, "end": v(11.17, -12.95) * mm});
            skLineSegment(sketch, "E698", {"start": v(11.17, -12.95) * mm, "end": v(11.44, -12.9) * mm});
            skLineSegment(sketch, "E699", {"start": v(11.44, -12.9) * mm, "end": v(11.65, -12.78) * mm});
            skLineSegment(sketch, "E700", {"start": v(11.65, -12.78) * mm, "end": v(11.46, -12.65) * mm});
            skLineSegment(sketch, "E701", {"start": v(11.46, -12.65) * mm, "end": v(11.26, -12.52) * mm});
            skLineSegment(sketch, "E702", {"start": v(11.26, -12.52) * mm, "end": v(11.04, -12.4) * mm});
            skLineSegment(sketch, "E703", {"start": v(11.04, -12.4) * mm, "end": v(10.8, -12.27) * mm});
            skLineSegment(sketch, "E704", {"start": v(10.8, -12.27) * mm, "end": v(10.58, -12.14) * mm});
            skLineSegment(sketch, "E705", {"start": v(10.58, -12.14) * mm, "end": v(10.36, -11.98) * mm});
            skLineSegment(sketch, "E706", {"start": v(10.36, -11.98) * mm, "end": v(10.16, -11.8) * mm});
            skLineSegment(sketch, "E707", {"start": v(10.16, -11.8) * mm, "end": v(9.98, -11.6) * mm});
            skLineSegment(sketch, "E708", {"start": v(9.98, -11.6) * mm, "end": v(10.2, -11.63) * mm});
            skLineSegment(sketch, "E709", {"start": v(10.2, -11.63) * mm, "end": v(10.43, -11.67) * mm});
            skLineSegment(sketch, "E710", {"start": v(10.43, -11.67) * mm, "end": v(10.65, -11.71) * mm});
            skLineSegment(sketch, "E711", {"start": v(10.65, -11.71) * mm, "end": v(10.87, -11.76) * mm});
            skLineSegment(sketch, "E712", {"start": v(10.87, -11.76) * mm, "end": v(11.1, -11.8) * mm});
            skLineSegment(sketch, "E713", {"start": v(11.1, -11.8) * mm, "end": v(11.33, -11.82) * mm});
            skLineSegment(sketch, "E714", {"start": v(11.33, -11.82) * mm, "end": v(11.57, -11.84) * mm});
            skLineSegment(sketch, "E715", {"start": v(11.57, -11.84) * mm, "end": v(11.82, -11.84) * mm});
            skLineSegment(sketch, "E716", {"start": v(11.82, -11.84) * mm, "end": v(11.93, -11.84) * mm});
            skLineSegment(sketch, "E717", {"start": v(11.93, -11.84) * mm, "end": v(12.25, -11.82) * mm});
            skLineSegment(sketch, "E718", {"start": v(12.25, -11.82) * mm, "end": v(12.53, -11.81) * mm});
            skLineSegment(sketch, "E719", {"start": v(12.53, -11.81) * mm, "end": v(12.67, -11.8) * mm});
            skLineSegment(sketch, "E720", {"start": v(12.67, -11.8) * mm, "end": v(12.82, -11.78) * mm});
            skLineSegment(sketch, "E721", {"start": v(12.82, -11.78) * mm, "end": v(12.98, -11.75) * mm});
            skLineSegment(sketch, "E722", {"start": v(12.98, -11.75) * mm, "end": v(13.15, -11.7) * mm});
            skLineSegment(sketch, "E723", {"start": v(13.15, -11.7) * mm, "end": v(13.53, -11.53) * mm});
            skLineSegment(sketch, "E724", {"start": v(13.53, -11.53) * mm, "end": v(13.33, -11.41) * mm});
            skLineSegment(sketch, "E725", {"start": v(13.33, -11.41) * mm, "end": v(13.12, -11.3) * mm});
            skLineSegment(sketch, "E726", {"start": v(13.12, -11.3) * mm, "end": v(12.9, -11.2) * mm});
            skLineSegment(sketch, "E727", {"start": v(12.9, -11.2) * mm, "end": v(12.68, -11.1) * mm});
            skLineSegment(sketch, "E728", {"start": v(12.68, -11.1) * mm, "end": v(12.45, -11) * mm});
            skLineSegment(sketch, "E729", {"start": v(12.45, -11) * mm, "end": v(12.22, -10.9) * mm});
            skLineSegment(sketch, "E730", {"start": v(12.22, -10.9) * mm, "end": v(12, -10.81) * mm});
            skLineSegment(sketch, "E731", {"start": v(12, -10.81) * mm, "end": v(11.79, -10.7) * mm});
            skLineSegment(sketch, "E732", {"start": v(11.79, -10.7) * mm, "end": v(12, -10.65) * mm});
            skLineSegment(sketch, "E733", {"start": v(12, -10.65) * mm, "end": v(12.2, -10.6) * mm});
            skLineSegment(sketch, "E734", {"start": v(12.2, -10.6) * mm, "end": v(12.38, -10.56) * mm});
            skLineSegment(sketch, "E735", {"start": v(12.38, -10.56) * mm, "end": v(12.56, -10.51) * mm});
            skLineSegment(sketch, "E736", {"start": v(12.56, -10.51) * mm, "end": v(12.73, -10.46) * mm});
            skLineSegment(sketch, "E737", {"start": v(12.73, -10.46) * mm, "end": v(12.92, -10.4) * mm});
            skLineSegment(sketch, "E738", {"start": v(12.92, -10.4) * mm, "end": v(13.1, -10.31) * mm});
            skLineSegment(sketch, "E739", {"start": v(13.1, -10.31) * mm, "end": v(13.32, -10.2) * mm});
            skLineSegment(sketch, "E740", {"start": v(13.32, -10.2) * mm, "end": v(13.47, -10.1) * mm});
            skLineSegment(sketch, "E741", {"start": v(13.47, -10.1) * mm, "end": v(13.62, -10) * mm});
            skLineSegment(sketch, "E742", {"start": v(13.62, -10) * mm, "end": v(13.76, -9.86) * mm});
            skLineSegment(sketch, "E743", {"start": v(13.76, -9.86) * mm, "end": v(13.9, -9.72) * mm});
            skLineSegment(sketch, "E744", {"start": v(13.9, -9.72) * mm, "end": v(14.02, -9.57) * mm});
            skLineSegment(sketch, "E745", {"start": v(14.02, -9.57) * mm, "end": v(14.13, -9.4) * mm});
            skLineSegment(sketch, "E746", {"start": v(14.13, -9.4) * mm, "end": v(14.22, -9.23) * mm});
            skLineSegment(sketch, "E747", {"start": v(14.22, -9.23) * mm, "end": v(14.29, -9.05) * mm});
            skLineSegment(sketch, "E748", {"start": v(14.29, -9.05) * mm, "end": v(13.39, -9.18) * mm});
            skLineSegment(sketch, "E749", {"start": v(13.39, -9.18) * mm, "end": v(13.46, -9.1) * mm});
            skLineSegment(sketch, "E750", {"start": v(13.46, -9.1) * mm, "end": v(13.55, -9.04) * mm});
            skLineSegment(sketch, "E751", {"start": v(13.55, -9.04) * mm, "end": v(13.64, -8.97) * mm});
            skLineSegment(sketch, "E752", {"start": v(13.64, -8.97) * mm, "end": v(13.73, -8.9) * mm});
            skLineSegment(sketch, "E753", {"start": v(13.73, -8.9) * mm, "end": v(13.92, -8.8) * mm});
            skLineSegment(sketch, "E754", {"start": v(13.92, -8.8) * mm, "end": v(14.09, -8.67) * mm});
            skLineSegment(sketch, "E755", {"start": v(14.09, -8.67) * mm, "end": v(14.15, -8.62) * mm});
            skLineSegment(sketch, "E756", {"start": v(14.15, -8.62) * mm, "end": v(14.22, -8.55) * mm});
            skLineSegment(sketch, "E757", {"start": v(14.22, -8.55) * mm, "end": v(14.3, -8.47) * mm});
            skLineSegment(sketch, "E758", {"start": v(14.3, -8.47) * mm, "end": v(14.36, -8.38) * mm});
            skLineSegment(sketch, "E759", {"start": v(14.36, -8.38) * mm, "end": v(14.43, -8.29) * mm});
            skLineSegment(sketch, "E760", {"start": v(14.43, -8.29) * mm, "end": v(14.5, -8.19) * mm});
            skLineSegment(sketch, "E761", {"start": v(14.5, -8.19) * mm, "end": v(14.54, -8.08) * mm});
            skLineSegment(sketch, "E762", {"start": v(14.54, -8.08) * mm, "end": v(14.58, -7.98) * mm});
            skLineSegment(sketch, "E763", {"start": v(14.58, -7.98) * mm, "end": v(13.64, -7.75) * mm});
            skLineSegment(sketch, "E764", {"start": v(13.64, -7.75) * mm, "end": v(13.88, -7.6) * mm});
            skLineSegment(sketch, "E765", {"start": v(13.88, -7.6) * mm, "end": v(14.02, -7.46) * mm});
            skLineSegment(sketch, "E766", {"start": v(14.02, -7.46) * mm, "end": v(14.16, -7.29) * mm});
            skLineSegment(sketch, "E767", {"start": v(14.16, -7.29) * mm, "end": v(14.28, -7.1) * mm});
            skLineSegment(sketch, "E768", {"start": v(14.28, -7.1) * mm, "end": v(14.4, -6.91) * mm});
            skLineSegment(sketch, "E769", {"start": v(14.4, -6.91) * mm, "end": v(14.5, -6.73) * mm});
            skLineSegment(sketch, "E770", {"start": v(14.5, -6.73) * mm, "end": v(14.6, -6.58) * mm});
            skLineSegment(sketch, "E771", {"start": v(14.6, -6.58) * mm, "end": v(14.68, -6.46) * mm});
            skLineSegment(sketch, "E772", {"start": v(14.68, -6.46) * mm, "end": v(14.77, -6.4) * mm});
            skLineSegment(sketch, "E773", {"start": v(14.77, -6.4) * mm, "end": v(15.08, -6.23) * mm});
            skLineSegment(sketch, "E774", {"start": v(15.08, -6.23) * mm, "end": v(15.33, -6.06) * mm});
            skLineSegment(sketch, "E775", {"start": v(15.33, -6.06) * mm, "end": v(15.54, -5.88) * mm});
            skLineSegment(sketch, "E776", {"start": v(15.54, -5.88) * mm, "end": v(15.72, -5.68) * mm});
            skLineSegment(sketch, "E777", {"start": v(15.72, -5.68) * mm, "end": v(15.89, -5.48) * mm});
            skLineSegment(sketch, "E778", {"start": v(15.89, -5.48) * mm, "end": v(16.05, -5.25) * mm});
            skLineSegment(sketch, "E779", {"start": v(16.05, -5.25) * mm, "end": v(16.22, -5) * mm});
            skLineSegment(sketch, "E780", {"start": v(16.22, -5) * mm, "end": v(16.4, -4.74) * mm});
            skLineSegment(sketch, "E781", {"start": v(16.4, -4.74) * mm, "end": v(16.5, -4.67) * mm});
            skLineSegment(sketch, "E782", {"start": v(16.5, -4.67) * mm, "end": v(16.66, -4.55) * mm});
            skLineSegment(sketch, "E783", {"start": v(16.66, -4.55) * mm, "end": v(16.88, -4.42) * mm});
            skLineSegment(sketch, "E784", {"start": v(16.88, -4.42) * mm, "end": v(17.12, -4.28) * mm});
            skLineSegment(sketch, "E785", {"start": v(17.12, -4.28) * mm, "end": v(17.37, -4.13) * mm});
            skLineSegment(sketch, "E786", {"start": v(17.37, -4.13) * mm, "end": v(17.6, -4) * mm});
            skLineSegment(sketch, "E787", {"start": v(17.6, -4) * mm, "end": v(17.79, -3.88) * mm});
            skLineSegment(sketch, "E788", {"start": v(17.79, -3.88) * mm, "end": v(17.92, -3.8) * mm});
            skLineSegment(sketch, "E789", {"start": v(17.92, -3.8) * mm, "end": v(18.38, -3.42) * mm});
            skLineSegment(sketch, "E790", {"start": v(18.38, -3.42) * mm, "end": v(18.78, -3) * mm});
            skLineSegment(sketch, "E791", {"start": v(18.78, -3) * mm, "end": v(18.94, -2.8) * mm});
            skLineSegment(sketch, "E792", {"start": v(18.94, -2.8) * mm, "end": v(19.05, -2.63) * mm});
            skLineSegment(sketch, "E793", {"start": v(19.05, -2.63) * mm, "end": v(19.13, -2.5) * mm});
            skLineSegment(sketch, "E794", {"start": v(19.13, -2.5) * mm, "end": v(19.19, -2.37) * mm});
            skLineSegment(sketch, "E795", {"start": v(19.19, -2.37) * mm, "end": v(19.28, -2.16) * mm});
            skLineSegment(sketch, "E796", {"start": v(19.28, -2.16) * mm, "end": v(19.4, -1.93) * mm});
            skLineSegment(sketch, "E797", {"start": v(19.4, -1.93) * mm, "end": v(19.52, -1.76) * mm});
            skLineSegment(sketch, "E798", {"start": v(19.52, -1.76) * mm, "end": v(19.67, -1.58) * mm});
            skLineSegment(sketch, "E799", {"start": v(19.67, -1.58) * mm, "end": v(19.83, -1.4) * mm});
            skLineSegment(sketch, "E800", {"start": v(19.83, -1.4) * mm, "end": v(20, -1.19) * mm});
            skLineSegment(sketch, "E801", {"start": v(20, -1.19) * mm, "end": v(20.18, -0.94) * mm});
            skLineSegment(sketch, "E802", {"start": v(20.18, -0.94) * mm, "end": v(20.33, -0.64) * mm});
            skLineSegment(sketch, "E803", {"start": v(20.33, -0.64) * mm, "end": v(20.47, -0.27) * mm});
            skLineSegment(sketch, "E804", {"start": v(20.47, -0.27) * mm, "end": v(20.58, 0.17) * mm});
            skLineSegment(sketch, "E805", {"start": v(20.58, 0.17) * mm, "end": v(20.6, 0.35) * mm});
            skLineSegment(sketch, "E806", {"start": v(20.6, 0.35) * mm, "end": v(20.63, 0.56) * mm});
            skLineSegment(sketch, "E807", {"start": v(20.63, 0.56) * mm, "end": v(20.65, 0.76) * mm});
            skLineSegment(sketch, "E808", {"start": v(20.65, 0.76) * mm, "end": v(20.67, 0.92) * mm});
            skLineSegment(sketch, "E809", {"start": v(20.67, 0.92) * mm, "end": v(20.7, 0.96) * mm});
            skLineSegment(sketch, "E810", {"start": v(20.7, 0.96) * mm, "end": v(20.73, 1.02) * mm});
            skLineSegment(sketch, "E811", {"start": v(20.73, 1.02) * mm, "end": v(20.77, 1.08) * mm});
            skLineSegment(sketch, "E812", {"start": v(20.77, 1.08) * mm, "end": v(20.82, 1.15) * mm});
            skLineSegment(sketch, "E813", {"start": v(20.82, 1.15) * mm, "end": v(20.92, 1.28) * mm});
            skLineSegment(sketch, "E814", {"start": v(20.92, 1.28) * mm, "end": v(21, 1.41) * mm});
            skLineSegment(sketch, "E815", {"start": v(21, 1.41) * mm, "end": v(21.1, 1.6) * mm});
            skLineSegment(sketch, "E816", {"start": v(21.1, 1.6) * mm, "end": v(21.18, 1.75) * mm});
            skLineSegment(sketch, "E817", {"start": v(21.18, 1.75) * mm, "end": v(21.24, 1.89) * mm});
            skLineSegment(sketch, "E818", {"start": v(21.24, 1.89) * mm, "end": v(21.27, 2.01) * mm});
            skLineSegment(sketch, "E819", {"start": v(21.27, 2.01) * mm, "end": v(21.32, 2.3) * mm});
            skLineSegment(sketch, "E820", {"start": v(21.32, 2.3) * mm, "end": v(21.37, 2.72) * mm});
            skLineSegment(sketch, "E821", {"start": v(21.37, 2.72) * mm, "end": v(21.43, 2.97) * mm});
            skLineSegment(sketch, "E822", {"start": v(21.43, 2.97) * mm, "end": v(21.52, 3.3) * mm});
            skLineSegment(sketch, "E823", {"start": v(21.52, 3.3) * mm, "end": v(21.56, 3.47) * mm});
            skLineSegment(sketch, "E824", {"start": v(21.56, 3.47) * mm, "end": v(21.6, 3.66) * mm});
            skLineSegment(sketch, "E825", {"start": v(21.6, 3.66) * mm, "end": v(21.65, 3.86) * mm});
            skLineSegment(sketch, "E826", {"start": v(21.65, 3.86) * mm, "end": v(21.68, 4.07) * mm});
            skLineSegment(sketch, "E827", {"start": v(21.68, 4.07) * mm, "end": v(21.71, 4.45) * mm});
            skLineSegment(sketch, "E828", {"start": v(21.71, 4.45) * mm, "end": v(21.75, 4.75) * mm});
            skLineSegment(sketch, "E829", {"start": v(21.75, 4.75) * mm, "end": v(21.78, 4.9) * mm});
            skLineSegment(sketch, "E830", {"start": v(21.78, 4.9) * mm, "end": v(21.82, 5.04) * mm});
            skLineSegment(sketch, "E831", {"start": v(21.82, 5.04) * mm, "end": v(21.89, 5.2) * mm});
            skLineSegment(sketch, "E832", {"start": v(21.89, 5.2) * mm, "end": v(21.97, 5.4) * mm});
            skLineSegment(sketch, "E833", {"start": v(21.97, 5.4) * mm, "end": v(22.07, 5.7) * mm});
            skLineSegment(sketch, "E834", {"start": v(22.07, 5.7) * mm, "end": v(22.18, 6.08) * mm});
            skLineSegment(sketch, "E835", {"start": v(22.18, 6.08) * mm, "end": v(22.24, 6.28) * mm});
            skLineSegment(sketch, "E836", {"start": v(22.24, 6.28) * mm, "end": v(22.3, 6.45) * mm});
            skLineSegment(sketch, "E837", {"start": v(22.3, 6.45) * mm, "end": v(22.34, 6.58) * mm});
            skLineSegment(sketch, "E838", {"start": v(22.34, 6.58) * mm, "end": v(22.38, 6.66) * mm});
            skLineSegment(sketch, "E839", {"start": v(22.38, 6.66) * mm, "end": v(22.78, 7.1) * mm});
            skLineSegment(sketch, "E840", {"start": v(22.78, 7.1) * mm, "end": v(22.93, 7.36) * mm});
            skLineSegment(sketch, "E841", {"start": v(22.93, 7.36) * mm, "end": v(23.14, 7.65) * mm});
            skLineSegment(sketch, "E842", {"start": v(23.14, 7.65) * mm, "end": v(23.38, 8) * mm});
            skLineSegment(sketch, "E843", {"start": v(23.38, 8) * mm, "end": v(23.5, 8.2) * mm});
            skLineSegment(sketch, "E844", {"start": v(23.5, 8.2) * mm, "end": v(23.59, 8.37) * mm});
            skLineSegment(sketch, "E845", {"start": v(23.59, 8.37) * mm, "end": v(23.66, 8.53) * mm});
            skLineSegment(sketch, "E846", {"start": v(23.66, 8.53) * mm, "end": v(23.7, 8.68) * mm});
            skLineSegment(sketch, "E847", {"start": v(23.7, 8.68) * mm, "end": v(23.51, 8.59) * mm});
            skLineSegment(sketch, "E848", {"start": v(23.51, 8.59) * mm, "end": v(23.15, 8.38) * mm});
            skLineSegment(sketch, "E849", {"start": v(23.15, 8.38) * mm, "end": v(22.67, 8.1) * mm});
            skLineSegment(sketch, "E850", {"start": v(22.67, 8.1) * mm, "end": v(22.11, 7.77) * mm});
            skLineSegment(sketch, "E851", {"start": v(22.11, 7.77) * mm, "end": v(21.52, 7.44) * mm});
            skLineSegment(sketch, "E852", {"start": v(21.52, 7.44) * mm, "end": v(20.95, 7.15) * mm});
            skLineSegment(sketch, "E853", {"start": v(20.95, 7.15) * mm, "end": v(20.43, 6.93) * mm});
            skLineSegment(sketch, "E854", {"start": v(20.43, 6.93) * mm, "end": v(20.03, 6.82) * mm});
            skLineSegment(sketch, "E855", {"start": v(20.03, 6.82) * mm, "end": v(20.16, 6.92) * mm});
            skLineSegment(sketch, "E856", {"start": v(20.16, 6.92) * mm, "end": v(20.3, 7.03) * mm});
            skLineSegment(sketch, "E857", {"start": v(20.3, 7.03) * mm, "end": v(20.45, 7.13) * mm});
            skLineSegment(sketch, "E858", {"start": v(20.45, 7.13) * mm, "end": v(20.6, 7.23) * mm});
            skLineSegment(sketch, "E859", {"start": v(20.6, 7.23) * mm, "end": v(20.9, 7.43) * mm});
            skLineSegment(sketch, "E860", {"start": v(20.9, 7.43) * mm, "end": v(21.19, 7.65) * mm});
            skLineSegment(sketch, "E861", {"start": v(21.19, 7.65) * mm, "end": v(21.74, 8.12) * mm});
            skLineSegment(sketch, "E862", {"start": v(21.74, 8.12) * mm, "end": v(22.27, 8.6) * mm});
            skLineSegment(sketch, "E863", {"start": v(22.27, 8.6) * mm, "end": v(22.76, 9.1) * mm});
            skLineSegment(sketch, "E864", {"start": v(22.76, 9.1) * mm, "end": v(23.21, 9.6) * mm});
            skLineSegment(sketch, "E865", {"start": v(23.21, 9.6) * mm, "end": v(23.63, 10.14) * mm});
            skLineSegment(sketch, "E866", {"start": v(23.63, 10.14) * mm, "end": v(24.01, 10.72) * mm});
            skLineSegment(sketch, "E867", {"start": v(24.01, 10.72) * mm, "end": v(24.35, 11.35) * mm});
            skLineSegment(sketch, "E868", {"start": v(24.35, 11.35) * mm, "end": v(24.65, 12.02) * mm});
            skLineSegment(sketch, "E869", {"start": v(24.65, 12.02) * mm, "end": v(24.75, 12.28) * mm});
            skLineSegment(sketch, "E870", {"start": v(24.75, 12.28) * mm, "end": v(24.85, 12.6) * mm});
            skLineSegment(sketch, "E871", {"start": v(24.85, 12.6) * mm, "end": v(24.94, 12.95) * mm});
            skLineSegment(sketch, "E872", {"start": v(24.94, 12.95) * mm, "end": v(25.03, 13.32) * mm});
            skLineSegment(sketch, "E873", {"start": v(25.03, 13.32) * mm, "end": v(25.1, 13.7) * mm});
            skLineSegment(sketch, "E874", {"start": v(25.1, 13.7) * mm, "end": v(25.16, 14.07) * mm});
            skLineSegment(sketch, "E875", {"start": v(25.16, 14.07) * mm, "end": v(25.18, 14.41) * mm});
            skLineSegment(sketch, "E876", {"start": v(25.18, 14.41) * mm, "end": v(25.17, 14.71) * mm});
            skLineSegment(sketch, "E877", {"start": v(25.17, 14.71) * mm, "end": v(24.5, 13.8) * mm});
            skLineSegment(sketch, "E878", {"start": v(24.5, 13.8) * mm, "end": v(24.07, 13.26) * mm});
            skLineSegment(sketch, "E879", {"start": v(24.07, 13.26) * mm, "end": v(23.6, 12.72) * mm});
            skLineSegment(sketch, "E880", {"start": v(23.6, 12.72) * mm, "end": v(23.13, 12.2) * mm});
            skLineSegment(sketch, "E881", {"start": v(23.13, 12.2) * mm, "end": v(22.63, 11.7) * mm});
            skLineSegment(sketch, "E882", {"start": v(22.63, 11.7) * mm, "end": v(22.12, 11.22) * mm});
            skLineSegment(sketch, "E883", {"start": v(22.12, 11.22) * mm, "end": v(21.6, 10.76) * mm});
            skLineSegment(sketch, "E884", {"start": v(21.6, 10.76) * mm, "end": v(21.05, 10.31) * mm});
            skLineSegment(sketch, "E885", {"start": v(21.05, 10.31) * mm, "end": v(20.5, 9.88) * mm});
            skLineSegment(sketch, "E886", {"start": v(20.5, 9.88) * mm, "end": v(20.29, 9.72) * mm});
            skLineSegment(sketch, "E887", {"start": v(20.29, 9.72) * mm, "end": v(20.06, 9.55) * mm});
            skLineSegment(sketch, "E888", {"start": v(20.06, 9.55) * mm, "end": v(19.82, 9.38) * mm});
            skLineSegment(sketch, "E889", {"start": v(19.82, 9.38) * mm, "end": v(19.58, 9.2) * mm});
            skLineSegment(sketch, "E890", {"start": v(19.58, 9.2) * mm, "end": v(19.33, 9.02) * mm});
            skLineSegment(sketch, "E891", {"start": v(19.33, 9.02) * mm, "end": v(19.09, 8.86) * mm});
            skLineSegment(sketch, "E892", {"start": v(19.09, 8.86) * mm, "end": v(18.84, 8.72) * mm});
            skLineSegment(sketch, "E893", {"start": v(18.84, 8.72) * mm, "end": v(18.61, 8.6) * mm});
            skLineSegment(sketch, "E894", {"start": v(18.61, 8.6) * mm, "end": v(18.66, 8.67) * mm});
            skLineSegment(sketch, "E895", {"start": v(18.66, 8.67) * mm, "end": v(18.72, 8.74) * mm});
            skLineSegment(sketch, "E896", {"start": v(18.72, 8.74) * mm, "end": v(18.79, 8.82) * mm});
            skLineSegment(sketch, "E897", {"start": v(18.79, 8.82) * mm, "end": v(18.87, 8.89) * mm});
            skLineSegment(sketch, "E898", {"start": v(18.87, 8.89) * mm, "end": v(19.03, 9.03) * mm});
            skLineSegment(sketch, "E899", {"start": v(19.03, 9.03) * mm, "end": v(19.17, 9.16) * mm});
            skLineSegment(sketch, "E900", {"start": v(19.17, 9.16) * mm, "end": v(19.4, 9.38) * mm});
            skLineSegment(sketch, "E901", {"start": v(19.4, 9.38) * mm, "end": v(19.6, 9.6) * mm});
            skLineSegment(sketch, "E902", {"start": v(19.6, 9.6) * mm, "end": v(19.8, 9.8) * mm});
            skLineSegment(sketch, "E903", {"start": v(19.8, 9.8) * mm, "end": v(20, 10.02) * mm});
            skLineSegment(sketch, "E904", {"start": v(20, 10.02) * mm, "end": v(20.21, 10.24) * mm});
            skLineSegment(sketch, "E905", {"start": v(20.21, 10.24) * mm, "end": v(20.41, 10.46) * mm});
            skLineSegment(sketch, "E906", {"start": v(20.41, 10.46) * mm, "end": v(20.62, 10.67) * mm});
            skLineSegment(sketch, "E907", {"start": v(20.62, 10.67) * mm, "end": v(20.83, 10.89) * mm});
            skLineSegment(sketch, "E908", {"start": v(20.83, 10.89) * mm, "end": v(21.08, 11.15) * mm});
            skLineSegment(sketch, "E909", {"start": v(21.08, 11.15) * mm, "end": v(21.34, 11.44) * mm});
            skLineSegment(sketch, "E910", {"start": v(21.34, 11.44) * mm, "end": v(21.61, 11.76) * mm});
            skLineSegment(sketch, "E911", {"start": v(21.61, 11.76) * mm, "end": v(21.88, 12.1) * mm});
            skLineSegment(sketch, "E912", {"start": v(21.88, 12.1) * mm, "end": v(22.15, 12.43) * mm});
            skLineSegment(sketch, "E913", {"start": v(22.15, 12.43) * mm, "end": v(22.4, 12.77) * mm});
            skLineSegment(sketch, "E914", {"start": v(22.4, 12.77) * mm, "end": v(22.64, 13.1) * mm});
            skLineSegment(sketch, "E915", {"start": v(22.64, 13.1) * mm, "end": v(22.85, 13.41) * mm});
            skLineSegment(sketch, "E916", {"start": v(22.85, 13.41) * mm, "end": v(23.29, 14.09) * mm});
            skLineSegment(sketch, "E917", {"start": v(23.29, 14.09) * mm, "end": v(23.72, 14.82) * mm});
            skLineSegment(sketch, "E918", {"start": v(23.72, 14.82) * mm, "end": v(24.11, 15.6) * mm});
            skLineSegment(sketch, "E919", {"start": v(24.11, 15.6) * mm, "end": v(24.45, 16.45) * mm});
            skLineSegment(sketch, "E920", {"start": v(24.45, 16.45) * mm, "end": v(24.7, 17.33) * mm});
            skLineSegment(sketch, "E921", {"start": v(24.7, 17.33) * mm, "end": v(24.86, 18.27) * mm});
            skLineSegment(sketch, "E922", {"start": v(24.86, 18.27) * mm, "end": v(24.89, 19.25) * mm});
            skLineSegment(sketch, "E923", {"start": v(24.89, 19.25) * mm, "end": v(24.77, 20.27) * mm});
            skLineSegment(sketch, "E924", {"start": v(24.77, 20.27) * mm, "end": v(24.66, 20.08) * mm});
            skLineSegment(sketch, "E925", {"start": v(24.66, 20.08) * mm, "end": v(24.55, 19.84) * mm});
            skLineSegment(sketch, "E926", {"start": v(24.55, 19.84) * mm, "end": v(24.44, 19.6) * mm});
            skLineSegment(sketch, "E927", {"start": v(24.44, 19.6) * mm, "end": v(24.34, 19.38) * mm});
            skLineSegment(sketch, "E928", {"start": v(24.34, 19.38) * mm, "end": v(24.15, 19.01) * mm});
            skLineSegment(sketch, "E929", {"start": v(24.15, 19.01) * mm, "end": v(23.97, 18.68) * mm});
            skLineSegment(sketch, "E930", {"start": v(23.97, 18.68) * mm, "end": v(23.8, 18.37) * mm});
            skLineSegment(sketch, "E931", {"start": v(23.8, 18.37) * mm, "end": v(23.63, 18.06) * mm});
            skLineSegment(sketch, "E932", {"start": v(23.63, 18.06) * mm, "end": v(23.45, 17.77) * mm});
            skLineSegment(sketch, "E933", {"start": v(23.45, 17.77) * mm, "end": v(23.27, 17.46) * mm});
            skLineSegment(sketch, "E934", {"start": v(23.27, 17.46) * mm, "end": v(23.06, 17.14) * mm});
            skLineSegment(sketch, "E935", {"start": v(23.06, 17.14) * mm, "end": v(22.84, 16.8) * mm});
            skLineSegment(sketch, "E936", {"start": v(22.84, 16.8) * mm, "end": v(22.63, 16.5) * mm});
            skLineSegment(sketch, "E937", {"start": v(22.63, 16.5) * mm, "end": v(22.42, 16.21) * mm});
            skLineSegment(sketch, "E938", {"start": v(22.42, 16.21) * mm, "end": v(22.2, 15.93) * mm});
            skLineSegment(sketch, "E939", {"start": v(22.2, 15.93) * mm, "end": v(21.98, 15.65) * mm});
            skLineSegment(sketch, "E940", {"start": v(21.98, 15.65) * mm, "end": v(21.33, 14.93) * mm});
            skLineSegment(sketch, "E941", {"start": v(21.33, 14.93) * mm, "end": v(21.1, 14.68) * mm});
            skLineSegment(sketch, "E942", {"start": v(21.1, 14.68) * mm, "end": v(20.83, 14.41) * mm});
            skLineSegment(sketch, "E943", {"start": v(20.83, 14.41) * mm, "end": v(20.55, 14.16) * mm});
            skLineSegment(sketch, "E944", {"start": v(20.55, 14.16) * mm, "end": v(20.3, 13.95) * mm});
            skLineSegment(sketch, "E945", {"start": v(20.3, 13.95) * mm, "end": v(20.34, 14.07) * mm});
            skLineSegment(sketch, "E946", {"start": v(20.34, 14.07) * mm, "end": v(20.4, 14.18) * mm});
            skLineSegment(sketch, "E947", {"start": v(20.4, 14.18) * mm, "end": v(20.47, 14.3) * mm});
            skLineSegment(sketch, "E948", {"start": v(20.47, 14.3) * mm, "end": v(20.55, 14.43) * mm});
            skLineSegment(sketch, "E949", {"start": v(20.55, 14.43) * mm, "end": v(20.7, 14.66) * mm});
            skLineSegment(sketch, "E950", {"start": v(20.7, 14.66) * mm, "end": v(20.85, 14.87) * mm});
            skLineSegment(sketch, "E951", {"start": v(20.85, 14.87) * mm, "end": v(21.07, 15.23) * mm});
            skLineSegment(sketch, "E952", {"start": v(21.07, 15.23) * mm, "end": v(21.28, 15.6) * mm});
            skLineSegment(sketch, "E953", {"start": v(21.28, 15.6) * mm, "end": v(21.5, 15.96) * mm});
            skLineSegment(sketch, "E954", {"start": v(21.5, 15.96) * mm, "end": v(21.69, 16.33) * mm});
            skLineSegment(sketch, "E955", {"start": v(21.69, 16.33) * mm, "end": v(21.88, 16.7) * mm});
            skLineSegment(sketch, "E956", {"start": v(21.88, 16.7) * mm, "end": v(22.07, 17.09) * mm});
            skLineSegment(sketch, "E957", {"start": v(22.07, 17.09) * mm, "end": v(22.26, 17.47) * mm});
            skLineSegment(sketch, "E958", {"start": v(22.26, 17.47) * mm, "end": v(22.44, 17.86) * mm});
            skLineSegment(sketch, "E959", {"start": v(22.44, 17.86) * mm, "end": v(22.57, 18.14) * mm});
            skLineSegment(sketch, "E960", {"start": v(22.57, 18.14) * mm, "end": v(22.68, 18.4) * mm});
            skLineSegment(sketch, "E961", {"start": v(22.68, 18.4) * mm, "end": v(22.79, 18.68) * mm});
            skLineSegment(sketch, "E962", {"start": v(22.79, 18.68) * mm, "end": v(22.88, 18.95) * mm});
            skLineSegment(sketch, "E963", {"start": v(22.88, 18.95) * mm, "end": v(22.97, 19.23) * mm});
            skLineSegment(sketch, "E964", {"start": v(22.97, 19.23) * mm, "end": v(23.05, 19.52) * mm});
            skLineSegment(sketch, "E965", {"start": v(23.05, 19.52) * mm, "end": v(23.13, 19.82) * mm});
            skLineSegment(sketch, "E966", {"start": v(23.13, 19.82) * mm, "end": v(23.21, 20.13) * mm});
            skLineSegment(sketch, "E967", {"start": v(23.21, 20.13) * mm, "end": v(23.3, 20.52) * mm});
            skLineSegment(sketch, "E968", {"start": v(23.3, 20.52) * mm, "end": v(23.35, 20.88) * mm});
            skLineSegment(sketch, "E969", {"start": v(23.35, 20.88) * mm, "end": v(23.37, 21.22) * mm});
            skLineSegment(sketch, "E970", {"start": v(23.37, 21.22) * mm, "end": v(23.37, 21.55) * mm});
            skLineSegment(sketch, "E971", {"start": v(23.37, 21.55) * mm, "end": v(23.35, 21.87) * mm});
            skLineSegment(sketch, "E972", {"start": v(23.35, 21.87) * mm, "end": v(23.3, 22.2) * mm});
            skLineSegment(sketch, "E973", {"start": v(23.3, 22.2) * mm, "end": v(23.25, 22.53) * mm});
            skLineSegment(sketch, "E974", {"start": v(23.25, 22.53) * mm, "end": v(23.18, 22.89) * mm});
            skLineSegment(sketch, "E975", {"start": v(23.18, 22.89) * mm, "end": v(22.58, 21.4) * mm});
            skLineSegment(sketch, "E976", {"start": v(22.58, 21.4) * mm, "end": v(22.37, 20.95) * mm});
            skLineSegment(sketch, "E977", {"start": v(22.37, 20.95) * mm, "end": v(22.16, 20.5) * mm});
            skLineSegment(sketch, "E978", {"start": v(22.16, 20.5) * mm, "end": v(21.94, 20.06) * mm});
            skLineSegment(sketch, "E979", {"start": v(21.94, 20.06) * mm, "end": v(21.72, 19.62) * mm});
            skLineSegment(sketch, "E980", {"start": v(21.72, 19.62) * mm, "end": v(21.5, 19.19) * mm});
            skLineSegment(sketch, "E981", {"start": v(21.5, 19.19) * mm, "end": v(21.26, 18.76) * mm});
            skLineSegment(sketch, "E982", {"start": v(21.26, 18.76) * mm, "end": v(21.02, 18.33) * mm});
            skLineSegment(sketch, "E983", {"start": v(21.02, 18.33) * mm, "end": v(20.76, 17.91) * mm});
            skLineSegment(sketch, "E984", {"start": v(20.76, 17.91) * mm, "end": v(20.66, 17.75) * mm});
            skLineSegment(sketch, "E985", {"start": v(20.66, 17.75) * mm, "end": v(20.54, 17.56) * mm});
            skLineSegment(sketch, "E986", {"start": v(20.54, 17.56) * mm, "end": v(20.43, 17.38) * mm});
            skLineSegment(sketch, "E987", {"start": v(20.43, 17.38) * mm, "end": v(20.33, 17.26) * mm});
            skLineSegment(sketch, "E988", {"start": v(20.33, 17.26) * mm, "end": v(20.57, 18.05) * mm});
            skLineSegment(sketch, "E989", {"start": v(20.57, 18.05) * mm, "end": v(20.78, 18.81) * mm});
            skLineSegment(sketch, "E990", {"start": v(20.78, 18.81) * mm, "end": v(20.97, 19.56) * mm});
            skLineSegment(sketch, "E991", {"start": v(20.97, 19.56) * mm, "end": v(21.11, 20.3) * mm});
            skLineSegment(sketch, "E992", {"start": v(21.11, 20.3) * mm, "end": v(21.22, 21.05) * mm});
            skLineSegment(sketch, "E993", {"start": v(21.22, 21.05) * mm, "end": v(21.28, 21.82) * mm});
            skLineSegment(sketch, "E994", {"start": v(21.28, 21.82) * mm, "end": v(21.3, 22.63) * mm});
            skLineSegment(sketch, "E995", {"start": v(21.3, 22.63) * mm, "end": v(21.26, 23.47) * mm});
            skLineSegment(sketch, "E996", {"start": v(21.26, 23.47) * mm, "end": v(21.24, 23.67) * mm});
            skLineSegment(sketch, "E997", {"start": v(21.24, 23.67) * mm, "end": v(21.2, 23.92) * mm});
            skLineSegment(sketch, "E998", {"start": v(21.2, 23.92) * mm, "end": v(21.15, 24.2) * mm});
            skLineSegment(sketch, "E999", {"start": v(21.15, 24.2) * mm, "end": v(21.1, 24.51) * mm});
            skLineSegment(sketch, "E1000", {"start": v(21.1, 24.51) * mm, "end": v(21.04, 24.81) * mm});
            skLineSegment(sketch, "E1001", {"start": v(21.04, 24.81) * mm, "end": v(20.97, 25.08) * mm});
            skLineSegment(sketch, "E1002", {"start": v(20.97, 25.08) * mm, "end": v(20.9, 25.3) * mm});
            skLineSegment(sketch, "E1003", {"start": v(20.9, 25.3) * mm, "end": v(20.83, 25.44) * mm});
            skLineSegment(sketch, "E1004", {"start": v(20.83, 25.44) * mm, "end": v(20.69, 24.66) * mm});
            skLineSegment(sketch, "E1005", {"start": v(20.69, 24.66) * mm, "end": v(20.47, 23.74) * mm});
            skLineSegment(sketch, "E1006", {"start": v(20.47, 23.74) * mm, "end": v(20.18, 22.74) * mm});
            skLineSegment(sketch, "E1007", {"start": v(20.18, 22.74) * mm, "end": v(19.86, 21.7) * mm});
            skLineSegment(sketch, "E1008", {"start": v(19.86, 21.7) * mm, "end": v(19.5, 20.66) * mm});
            skLineSegment(sketch, "E1009", {"start": v(19.5, 20.66) * mm, "end": v(19.14, 19.69) * mm});
            skLineSegment(sketch, "E1010", {"start": v(19.14, 19.69) * mm, "end": v(18.8, 18.81) * mm});
            skLineSegment(sketch, "E1011", {"start": v(18.8, 18.81) * mm, "end": v(18.47, 18.08) * mm});
            skLineSegment(sketch, "E1012", {"start": v(18.47, 18.08) * mm, "end": v(18.37, 17.88) * mm});
            skLineSegment(sketch, "E1013", {"start": v(18.37, 17.88) * mm, "end": v(18.23, 17.6) * mm});
            skLineSegment(sketch, "E1014", {"start": v(18.23, 17.6) * mm, "end": v(18.08, 17.27) * mm});
            skLineSegment(sketch, "E1015", {"start": v(18.08, 17.27) * mm, "end": v(17.9, 16.92) * mm});
            skLineSegment(sketch, "E1016", {"start": v(17.9, 16.92) * mm, "end": v(17.74, 16.57) * mm});
            skLineSegment(sketch, "E1017", {"start": v(17.74, 16.57) * mm, "end": v(17.6, 16.26) * mm});
            skLineSegment(sketch, "E1018", {"start": v(17.6, 16.26) * mm, "end": v(17.49, 16) * mm});
            skLineSegment(sketch, "E1019", {"start": v(17.49, 16) * mm, "end": v(17.42, 15.84) * mm});
            skLineSegment(sketch, "E1020", {"start": v(17.42, 15.84) * mm, "end": v(17.35, 15.94) * mm});
            skLineSegment(sketch, "E1021", {"start": v(17.35, 15.94) * mm, "end": v(17.3, 16.04) * mm});
            skLineSegment(sketch, "E1022", {"start": v(17.3, 16.04) * mm, "end": v(17.25, 16.16) * mm});
            skLineSegment(sketch, "E1023", {"start": v(17.25, 16.16) * mm, "end": v(17.21, 16.29) * mm});
            skLineSegment(sketch, "E1024", {"start": v(17.21, 16.29) * mm, "end": v(17.18, 16.4) * mm});
            skLineSegment(sketch, "E1025", {"start": v(17.18, 16.4) * mm, "end": v(17.14, 16.53) * mm});
            skLineSegment(sketch, "E1026", {"start": v(17.14, 16.53) * mm, "end": v(17.09, 16.64) * mm});
            skLineSegment(sketch, "E1027", {"start": v(17.09, 16.64) * mm, "end": v(17.02, 16.73) * mm});
            skLineSegment(sketch, "E1028", {"start": v(17.02, 16.73) * mm, "end": v(16.97, 16.65) * mm});
            skLineSegment(sketch, "E1029", {"start": v(16.97, 16.65) * mm, "end": v(16.9, 16.52) * mm});
            skLineSegment(sketch, "E1030", {"start": v(16.9, 16.52) * mm, "end": v(16.84, 16.35) * mm});
            skLineSegment(sketch, "E1031", {"start": v(16.84, 16.35) * mm, "end": v(16.77, 16.16) * mm});
            skLineSegment(sketch, "E1032", {"start": v(16.77, 16.16) * mm, "end": v(16.63, 15.78) * mm});
            skLineSegment(sketch, "E1033", {"start": v(16.63, 15.78) * mm, "end": v(16.52, 15.49) * mm});
            skLineSegment(sketch, "E1034", {"start": v(16.52, 15.49) * mm, "end": v(16.32, 15.04) * mm});
            skLineSegment(sketch, "E1035", {"start": v(16.32, 15.04) * mm, "end": v(16.1, 14.6) * mm});
            skLineSegment(sketch, "E1036", {"start": v(16.1, 14.6) * mm, "end": v(15.9, 14.15) * mm});
            skLineSegment(sketch, "E1037", {"start": v(15.9, 14.15) * mm, "end": v(15.66, 13.72) * mm});
            skLineSegment(sketch, "E1038", {"start": v(15.66, 13.72) * mm, "end": v(15.42, 13.3) * mm});
            skLineSegment(sketch, "E1039", {"start": v(15.42, 13.3) * mm, "end": v(15.16, 12.87) * mm});
            skLineSegment(sketch, "E1040", {"start": v(15.16, 12.87) * mm, "end": v(14.9, 12.46) * mm});
            skLineSegment(sketch, "E1041", {"start": v(14.9, 12.46) * mm, "end": v(14.61, 12.06) * mm});
            skLineSegment(sketch, "E1042", {"start": v(14.61, 12.06) * mm, "end": v(14.42, 11.8) * mm});
            skLineSegment(sketch, "E1043", {"start": v(14.42, 11.8) * mm, "end": v(14.19, 11.47) * mm});
            skLineSegment(sketch, "E1044", {"start": v(14.19, 11.47) * mm, "end": v(13.92, 11.12) * mm});
            skLineSegment(sketch, "E1045", {"start": v(13.92, 11.12) * mm, "end": v(13.64, 10.75) * mm});
            skLineSegment(sketch, "E1046", {"start": v(13.64, 10.75) * mm, "end": v(13.37, 10.4) * mm});
            skLineSegment(sketch, "E1047", {"start": v(13.37, 10.4) * mm, "end": v(13.1, 10.07) * mm});
            skLineSegment(sketch, "E1048", {"start": v(13.1, 10.07) * mm, "end": v(12.87, 9.79) * mm});
            skLineSegment(sketch, "E1049", {"start": v(12.87, 9.79) * mm, "end": v(12.67, 9.58) * mm});
            skLineSegment(sketch, "E1050", {"start": v(12.67, 9.58) * mm, "end": v(12.23, 9.1) * mm});
            skLineSegment(sketch, "E1051", {"start": v(12.23, 9.1) * mm, "end": v(12.12, 8.99) * mm});
            skLineSegment(sketch, "E1052", {"start": v(12.12, 8.99) * mm, "end": v(12.02, 8.87) * mm});
            skLineSegment(sketch, "E1053", {"start": v(12.02, 8.87) * mm, "end": v(11.91, 8.76) * mm});
            skLineSegment(sketch, "E1054", {"start": v(11.91, 8.76) * mm, "end": v(11.8, 8.65) * mm});
            skLineSegment(sketch, "E1055", {"start": v(11.8, 8.65) * mm, "end": v(11.36, 8.2) * mm});
            skLineSegment(sketch, "E1056", {"start": v(11.36, 8.2) * mm, "end": v(11.3, 8.3) * mm});
            skLineSegment(sketch, "E1057", {"start": v(11.3, 8.3) * mm, "end": v(11.27, 8.4) * mm});
            skLineSegment(sketch, "E1058", {"start": v(11.27, 8.4) * mm, "end": v(11.25, 8.54) * mm});
            skLineSegment(sketch, "E1059", {"start": v(11.25, 8.54) * mm, "end": v(11.23, 8.69) * mm});
            skLineSegment(sketch, "E1060", {"start": v(11.23, 8.69) * mm, "end": v(11.2, 8.99) * mm});
            skLineSegment(sketch, "E1061", {"start": v(11.2, 8.99) * mm, "end": v(11.17, 9.25) * mm});
            skLineSegment(sketch, "E1062", {"start": v(11.17, 9.25) * mm, "end": v(11.1, 9.1) * mm});
            skLineSegment(sketch, "E1063", {"start": v(11.1, 9.1) * mm, "end": v(11.01, 8.93) * mm});
            skLineSegment(sketch, "E1064", {"start": v(11.01, 8.93) * mm, "end": v(10.9, 8.78) * mm});
            skLineSegment(sketch, "E1065", {"start": v(10.9, 8.78) * mm, "end": v(10.78, 8.62) * mm});
            skLineSegment(sketch, "E1066", {"start": v(10.78, 8.62) * mm, "end": v(10.65, 8.48) * mm});
            skLineSegment(sketch, "E1067", {"start": v(10.65, 8.48) * mm, "end": v(10.54, 8.33) * mm});
            skLineSegment(sketch, "E1068", {"start": v(10.54, 8.33) * mm, "end": v(10.44, 8.2) * mm});
            skLineSegment(sketch, "E1069", {"start": v(10.44, 8.2) * mm, "end": v(10.37, 8.07) * mm});
            skLineSegment(sketch, "E1070", {"start": v(10.37, 8.07) * mm, "end": v(10.38, 7.94) * mm});
            skLineSegment(sketch, "E1071", {"start": v(10.38, 7.94) * mm, "end": v(10.38, 7.82) * mm});
            skLineSegment(sketch, "E1072", {"start": v(10.38, 7.82) * mm, "end": v(10.37, 7.73) * mm});
            skLineSegment(sketch, "E1073", {"start": v(10.37, 7.73) * mm, "end": v(10.33, 7.65) * mm});
            skLineSegment(sketch, "E1074", {"start": v(10.33, 7.65) * mm, "end": v(10.29, 7.57) * mm});
            skLineSegment(sketch, "E1075", {"start": v(10.29, 7.57) * mm, "end": v(10.22, 7.5) * mm});
            skLineSegment(sketch, "E1076", {"start": v(10.22, 7.5) * mm, "end": v(10.15, 7.4) * mm});
            skLineSegment(sketch, "E1077", {"start": v(10.15, 7.4) * mm, "end": v(10.06, 7.31) * mm});
            skLineSegment(sketch, "E1078", {"start": v(10.06, 7.31) * mm, "end": v(9.95, 7.21) * mm});
            skLineSegment(sketch, "E1079", {"start": v(9.95, 7.21) * mm, "end": v(9.9, 7.19) * mm});
            skLineSegment(sketch, "E1080", {"start": v(9.9, 7.19) * mm, "end": v(9.9, 7.19) * mm});
            skLineSegment(sketch, "E1081", {"start": v(9.9, 7.19) * mm, "end": v(9.94, 7.16) * mm});
            skLineSegment(sketch, "E1082", {"start": v(9.94, 7.16) * mm, "end": v(10.04, 7.23) * mm});
            skLineSegment(sketch, "E1083", {"start": v(10.04, 7.23) * mm, "end": v(10.2, 7.36) * mm});
            skLineSegment(sketch, "E1084", {"start": v(10.2, 7.36) * mm, "end": v(10.35, 7.5) * mm});
            skLineSegment(sketch, "E1085", {"start": v(10.35, 7.5) * mm, "end": v(10.49, 7.64) * mm});
            skLineSegment(sketch, "E1086", {"start": v(10.49, 7.64) * mm, "end": v(11.03, 8.18) * mm});
            skLineSegment(sketch, "E1087", {"start": v(11.03, 8.18) * mm, "end": v(11, 7.72) * mm});
            skLineSegment(sketch, "E1088", {"start": v(11, 7.72) * mm, "end": v(10.92, 7.28) * mm});
            skLineSegment(sketch, "E1089", {"start": v(10.92, 7.28) * mm, "end": v(10.77, 6.86) * mm});
            skLineSegment(sketch, "E1090", {"start": v(10.77, 6.86) * mm, "end": v(10.58, 6.47) * mm});
            skLineSegment(sketch, "E1091", {"start": v(10.58, 6.47) * mm, "end": v(10.35, 6.1) * mm});
            skLineSegment(sketch, "E1092", {"start": v(10.35, 6.1) * mm, "end": v(10.1, 5.76) * mm});
            skLineSegment(sketch, "E1093", {"start": v(10.1, 5.76) * mm, "end": v(9.82, 5.43) * mm});
            skLineSegment(sketch, "E1094", {"start": v(9.82, 5.43) * mm, "end": v(9.54, 5.12) * mm});
            skLineSegment(sketch, "E1095", {"start": v(9.54, 5.12) * mm, "end": v(9.4, 4.99) * mm});
            skLineSegment(sketch, "E1096", {"start": v(9.4, 4.99) * mm, "end": v(9.33, 4.93) * mm});
            skLineSegment(sketch, "E1097", {"start": v(9.33, 4.93) * mm, "end": v(9.27, 4.9) * mm});
            skLineSegment(sketch, "E1098", {"start": v(9.27, 4.9) * mm, "end": v(9.19, 4.81) * mm});
            skLineSegment(sketch, "E1099", {"start": v(9.19, 4.81) * mm, "end": v(9.1, 4.73) * mm});
            skLineSegment(sketch, "E1100", {"start": v(9.1, 4.73) * mm, "end": v(9.02, 4.66) * mm});
            skLineSegment(sketch, "E1101", {"start": v(9.02, 4.66) * mm, "end": v(8.94, 4.6) * mm});
            skLineSegment(sketch, "E1102", {"start": v(8.94, 4.6) * mm, "end": v(8.85, 4.53) * mm});
            skLineSegment(sketch, "E1103", {"start": v(8.85, 4.53) * mm, "end": v(8.5, 4.26) * mm});
            skLineSegment(sketch, "E1104", {"start": v(8.5, 4.26) * mm, "end": v(8.16, 4.03) * mm});
            skLineSegment(sketch, "E1105", {"start": v(8.16, 4.03) * mm, "end": v(7.85, 3.83) * mm});
            skLineSegment(sketch, "E1106", {"start": v(7.85, 3.83) * mm, "end": v(7.55, 3.65) * mm});
            skLineSegment(sketch, "E1107", {"start": v(7.55, 3.65) * mm, "end": v(7.24, 3.48) * mm});
            skLineSegment(sketch, "E1108", {"start": v(7.24, 3.48) * mm, "end": v(6.92, 3.3) * mm});
            skLineSegment(sketch, "E1109", {"start": v(6.92, 3.3) * mm, "end": v(6.57, 3.13) * mm});
            skLineSegment(sketch, "E1110", {"start": v(6.57, 3.13) * mm, "end": v(6.2, 2.93) * mm});
            skLineSegment(sketch, "E1111", {"start": v(6.2, 2.93) * mm, "end": v(5.97, 2.8) * mm});
            skLineSegment(sketch, "E1112", {"start": v(5.97, 2.8) * mm, "end": v(6.13, 2.82) * mm});
            skLineSegment(sketch, "E1113", {"start": v(6.13, 2.82) * mm, "end": v(6.28, 2.85) * mm});
            skLineSegment(sketch, "E1114", {"start": v(6.28, 2.85) * mm, "end": v(6.43, 2.89) * mm});
            skLineSegment(sketch, "E1115", {"start": v(6.43, 2.89) * mm, "end": v(6.57, 2.92) * mm});
            skLineSegment(sketch, "E1116", {"start": v(6.57, 2.92) * mm, "end": v(6.84, 3) * mm});
            skLineSegment(sketch, "E1117", {"start": v(6.84, 3) * mm, "end": v(7.12, 3.07) * mm});
            skLineSegment(sketch, "E1118", {"start": v(7.12, 3.07) * mm, "end": v(7.12, 2.84) * mm});
            skLineSegment(sketch, "E1119", {"start": v(7.12, 2.84) * mm, "end": v(7.11, 2.63) * mm});
            skLineSegment(sketch, "E1120", {"start": v(7.11, 2.63) * mm, "end": v(7.09, 2.44) * mm});
            skLineSegment(sketch, "E1121", {"start": v(7.09, 2.44) * mm, "end": v(7.04, 2.27) * mm});
            skLineSegment(sketch, "E1122", {"start": v(7.04, 2.27) * mm, "end": v(6.98, 2.1) * mm});
            skLineSegment(sketch, "E1123", {"start": v(6.98, 2.1) * mm, "end": v(6.9, 1.93) * mm});
            skLineSegment(sketch, "E1124", {"start": v(6.9, 1.93) * mm, "end": v(6.82, 1.76) * mm});
            skLineSegment(sketch, "E1125", {"start": v(6.82, 1.76) * mm, "end": v(6.7, 1.58) * mm});
            skLineSegment(sketch, "E1126", {"start": v(6.7, 1.58) * mm, "end": v(6.64, 1.48) * mm});
            skLineSegment(sketch, "E1127", {"start": v(6.64, 1.48) * mm, "end": v(6.56, 1.4) * mm});
            skLineSegment(sketch, "E1128", {"start": v(6.56, 1.4) * mm, "end": v(6.5, 1.31) * mm});
            skLineSegment(sketch, "E1129", {"start": v(6.5, 1.31) * mm, "end": v(6.43, 1.22) * mm});
            skLineSegment(sketch, "E1130", {"start": v(6.43, 1.22) * mm, "end": v(6.6, 1.28) * mm});
            skLineSegment(sketch, "E1131", {"start": v(6.6, 1.28) * mm, "end": v(6.75, 1.35) * mm});
            skLineSegment(sketch, "E1132", {"start": v(6.75, 1.35) * mm, "end": v(6.9, 1.42) * mm});
            skLineSegment(sketch, "E1133", {"start": v(6.9, 1.42) * mm, "end": v(7.03, 1.5) * mm});
            skLineSegment(sketch, "E1134", {"start": v(7.03, 1.5) * mm, "end": v(7.15, 1.57) * mm});
            skLineSegment(sketch, "E1135", {"start": v(7.15, 1.57) * mm, "end": v(7.27, 1.66) * mm});
            skLineSegment(sketch, "E1136", {"start": v(7.27, 1.66) * mm, "end": v(7.38, 1.74) * mm});
            skLineSegment(sketch, "E1137", {"start": v(7.38, 1.74) * mm, "end": v(7.48, 1.84) * mm});
            skLineSegment(sketch, "E1138", {"start": v(7.48, 1.84) * mm, "end": v(7.55, 1.69) * mm});
            skLineSegment(sketch, "E1139", {"start": v(7.55, 1.69) * mm, "end": v(7.58, 1.53) * mm});
            skLineSegment(sketch, "E1140", {"start": v(7.58, 1.53) * mm, "end": v(7.59, 1.36) * mm});
            skLineSegment(sketch, "E1141", {"start": v(7.59, 1.36) * mm, "end": v(7.57, 1.18) * mm});
            skLineSegment(sketch, "E1142", {"start": v(7.57, 1.18) * mm, "end": v(7.53, 1) * mm});
            skLineSegment(sketch, "E1143", {"start": v(7.53, 1) * mm, "end": v(7.48, 0.84) * mm});
            skLineSegment(sketch, "E1144", {"start": v(7.48, 0.84) * mm, "end": v(7.43, 0.69) * mm});
            skLineSegment(sketch, "E1145", {"start": v(7.43, 0.69) * mm, "end": v(7.37, 0.55) * mm});
            skLineSegment(sketch, "E1146", {"start": v(7.37, 0.55) * mm, "end": v(7.3, 0.4) * mm});
            skLineSegment(sketch, "E1147", {"start": v(7.3, 0.4) * mm, "end": v(7.22, 0.28) * mm});
            skLineSegment(sketch, "E1148", {"start": v(7.22, 0.28) * mm, "end": v(7.14, 0.17) * mm});
            skLineSegment(sketch, "E1149", {"start": v(7.14, 0.17) * mm, "end": v(7.05, 0.07) * mm});
            skLineSegment(sketch, "E1150", {"start": v(7.05, 0.07) * mm, "end": v(6.88, -0.13) * mm});
            skLineSegment(sketch, "E1151", {"start": v(6.88, -0.13) * mm, "end": v(6.67, -0.37) * mm});
            skLineSegment(sketch, "E1152", {"start": v(6.67, -0.37) * mm, "end": v(6.82, -0.33) * mm});
            skLineSegment(sketch, "E1153", {"start": v(6.82, -0.33) * mm, "end": v(6.97, -0.29) * mm});
            skLineSegment(sketch, "E1154", {"start": v(6.97, -0.29) * mm, "end": v(7.12, -0.24) * mm});
            skLineSegment(sketch, "E1155", {"start": v(7.12, -0.24) * mm, "end": v(7.27, -0.19) * mm});
            skLineSegment(sketch, "E1156", {"start": v(7.27, -0.19) * mm, "end": v(7.41, -0.14) * mm});
            skLineSegment(sketch, "E1157", {"start": v(7.41, -0.14) * mm, "end": v(7.56, -0.08) * mm});
            skLineSegment(sketch, "E1158", {"start": v(7.56, -0.08) * mm, "end": v(7.64, -0.05) * mm});
            skLineSegment(sketch, "E1159", {"start": v(7.64, -0.05) * mm, "end": v(7.71, -0.02) * mm});
            skLineSegment(sketch, "E1160", {"start": v(7.71, -0.02) * mm, "end": v(7.78, 0) * mm});
            skLineSegment(sketch, "E1161", {"start": v(7.78, 0) * mm, "end": v(7.84, 0) * mm});
            skLineSegment(sketch, "E1162", {"start": v(7.84, 0) * mm, "end": v(7.74, -0.34) * mm});
            skLineSegment(sketch, "E1163", {"start": v(7.74, -0.34) * mm, "end": v(7.6, -0.63) * mm});
            skLineSegment(sketch, "E1164", {"start": v(7.6, -0.63) * mm, "end": v(7.43, -0.9) * mm});
            skLineSegment(sketch, "E1165", {"start": v(7.43, -0.9) * mm, "end": v(7.24, -1.11) * mm});
            skLineSegment(sketch, "E1166", {"start": v(7.24, -1.11) * mm, "end": v(7.07, -1.3) * mm});
            skLineSegment(sketch, "E1167", {"start": v(7.07, -1.3) * mm, "end": v(6.9, -1.48) * mm});
            skLineSegment(sketch, "E1168", {"start": v(6.9, -1.48) * mm, "end": v(6.77, -1.62) * mm});
            skLineSegment(sketch, "E1169", {"start": v(6.77, -1.62) * mm, "end": v(6.69, -1.74) * mm});
            skLineSegment(sketch, "E1170", {"start": v(6.69, -1.74) * mm, "end": v(7.42, -1.59) * mm});
            skLineSegment(sketch, "E1171", {"start": v(7.42, -1.59) * mm, "end": v(7.39, -1.7) * mm});
            skLineSegment(sketch, "E1172", {"start": v(7.39, -1.7) * mm, "end": v(7.36, -1.82) * mm});
            skLineSegment(sketch, "E1173", {"start": v(7.36, -1.82) * mm, "end": v(7.32, -1.92) * mm});
            skLineSegment(sketch, "E1174", {"start": v(7.32, -1.92) * mm, "end": v(7.27, -2.01) * mm});
            skLineSegment(sketch, "E1175", {"start": v(7.27, -2.01) * mm, "end": v(7.18, -2.2) * mm});
            skLineSegment(sketch, "E1176", {"start": v(7.18, -2.2) * mm, "end": v(7.07, -2.36) * mm});
            skLineSegment(sketch, "E1177", {"start": v(7.07, -2.36) * mm, "end": v(6.63, -3.01) * mm});
            skLineSegment(sketch, "E1178", {"start": v(6.63, -3.01) * mm, "end": v(6.88, -2.8) * mm});
            skLineSegment(sketch, "E1179", {"start": v(6.88, -2.8) * mm, "end": v(7.04, -2.64) * mm});
            skLineSegment(sketch, "E1180", {"start": v(7.04, -2.64) * mm, "end": v(7.14, -2.52) * mm});
            skLineSegment(sketch, "E1181", {"start": v(7.14, -2.52) * mm, "end": v(7.23, -2.45) * mm});
            skLineSegment(sketch, "E1182", {"start": v(7.23, -2.45) * mm, "end": v(7.33, -2.4) * mm});
            skLineSegment(sketch, "E1183", {"start": v(7.33, -2.4) * mm, "end": v(7.48, -2.39) * mm});
            skLineSegment(sketch, "E1184", {"start": v(7.48, -2.39) * mm, "end": v(7.73, -2.39) * mm});
            skLineSegment(sketch, "E1185", {"start": v(7.73, -2.39) * mm, "end": v(8.1, -2.4) * mm});
            skLineSegment(sketch, "E1186", {"start": v(8.1, -2.4) * mm, "end": v(8.08, -2.45) * mm});
            skLineSegment(sketch, "E1187", {"start": v(8.08, -2.45) * mm, "end": v(8.06, -2.5) * mm});
            skLineSegment(sketch, "E1188", {"start": v(8.06, -2.5) * mm, "end": v(8.03, -2.55) * mm});
            skLineSegment(sketch, "E1189", {"start": v(8.03, -2.55) * mm, "end": v(8, -2.59) * mm});
            skLineSegment(sketch, "E1190", {"start": v(8, -2.59) * mm, "end": v(7.93, -2.66) * mm});
            skLineSegment(sketch, "E1191", {"start": v(7.93, -2.66) * mm, "end": v(7.85, -2.73) * mm});
            skLineSegment(sketch, "E1192", {"start": v(7.85, -2.73) * mm, "end": v(7.74, -2.85) * mm});
            skLineSegment(sketch, "E1193", {"start": v(7.74, -2.85) * mm, "end": v(7.61, -2.94) * mm});
            skLineSegment(sketch, "E1194", {"start": v(7.61, -2.94) * mm, "end": v(7.48, -3.04) * mm});
            skLineSegment(sketch, "E1195", {"start": v(7.48, -3.04) * mm, "end": v(7.34, -3.12) * mm});
            skLineSegment(sketch, "E1196", {"start": v(7.34, -3.12) * mm, "end": v(7.06, -3.28) * mm});
            skLineSegment(sketch, "E1197", {"start": v(7.06, -3.28) * mm, "end": v(6.78, -3.44) * mm});
            skLineSegment(sketch, "E1198", {"start": v(6.78, -3.44) * mm, "end": v(6.92, -3.42) * mm});
            skLineSegment(sketch, "E1199", {"start": v(6.92, -3.42) * mm, "end": v(7.06, -3.4) * mm});
            skLineSegment(sketch, "E1200", {"start": v(7.06, -3.4) * mm, "end": v(7.21, -3.35) * mm});
            skLineSegment(sketch, "E1201", {"start": v(7.21, -3.35) * mm, "end": v(7.36, -3.29) * mm});
            skLineSegment(sketch, "E1202", {"start": v(7.36, -3.29) * mm, "end": v(7.5, -3.22) * mm});
            skLineSegment(sketch, "E1203", {"start": v(7.5, -3.22) * mm, "end": v(7.64, -3.16) * mm});
            skLineSegment(sketch, "E1204", {"start": v(7.64, -3.16) * mm, "end": v(7.76, -3.09) * mm});
            skLineSegment(sketch, "E1205", {"start": v(7.76, -3.09) * mm, "end": v(7.85, -3.03) * mm});
            skLineSegment(sketch, "E1206", {"start": v(7.85, -3.03) * mm, "end": v(8.03, -2.9) * mm});
            skLineSegment(sketch, "E1207", {"start": v(8.03, -2.9) * mm, "end": v(8.09, -2.85) * mm});
            skLineSegment(sketch, "E1208", {"start": v(8.09, -2.85) * mm, "end": v(8.13, -2.8) * mm});
            skLineSegment(sketch, "E1209", {"start": v(8.13, -2.8) * mm, "end": v(8.25, -2.67) * mm});
            skLineSegment(sketch, "E1210", {"start": v(8.25, -2.67) * mm, "end": v(8.35, -2.57) * mm});
            skLineSegment(sketch, "E1211", {"start": v(8.35, -2.57) * mm, "end": v(8.42, -2.47) * mm});
            skLineSegment(sketch, "E1212", {"start": v(8.42, -2.47) * mm, "end": v(8.48, -2.37) * mm});
            skLineSegment(sketch, "E1213", {"start": v(8.48, -2.37) * mm, "end": v(8.55, -2.25) * mm});
            skLineSegment(sketch, "E1214", {"start": v(8.55, -2.25) * mm, "end": v(7.78, -2.24) * mm});
            skLineSegment(sketch, "E1215", {"start": v(7.78, -2.24) * mm, "end": v(7.9, -2.14) * mm});
            skLineSegment(sketch, "E1216", {"start": v(7.9, -2.14) * mm, "end": v(8.06, -2.03) * mm});
            skLineSegment(sketch, "E1217", {"start": v(8.06, -2.03) * mm, "end": v(8.24, -1.92) * mm});
            skLineSegment(sketch, "E1218", {"start": v(8.24, -1.92) * mm, "end": v(8.43, -1.78) * mm});
            skLineSegment(sketch, "E1219", {"start": v(8.43, -1.78) * mm, "end": v(8.63, -1.6) * mm});
            skLineSegment(sketch, "E1220", {"start": v(8.63, -1.6) * mm, "end": v(8.83, -1.38) * mm});
            skLineSegment(sketch, "E1221", {"start": v(8.83, -1.38) * mm, "end": v(9.03, -1.1) * mm});
            skLineSegment(sketch, "E1222", {"start": v(9.03, -1.1) * mm, "end": v(9.22, -0.72) * mm});
            skLineSegment(sketch, "E1223", {"start": v(9.22, -0.72) * mm, "end": v(9.25, -0.66) * mm});
            skLineSegment(sketch, "E1224", {"start": v(9.25, -0.66) * mm, "end": v(9.28, -0.62) * mm});
            skLineSegment(sketch, "E1225", {"start": v(9.28, -0.62) * mm, "end": v(9.31, -0.58) * mm});
            skLineSegment(sketch, "E1226", {"start": v(9.31, -0.58) * mm, "end": v(9.34, -0.56) * mm});
            skLineSegment(sketch, "E1227", {"start": v(9.34, -0.56) * mm, "end": v(9.43, -0.52) * mm});
            skLineSegment(sketch, "E1228", {"start": v(9.43, -0.52) * mm, "end": v(9.55, -0.47) * mm});
            skLineSegment(sketch, "E1229", {"start": v(9.55, -0.47) * mm, "end": v(9.77, -0.37) * mm});
            skLineSegment(sketch, "E1230", {"start": v(9.77, -0.37) * mm, "end": v(9.98, -0.27) * mm});
            skLineSegment(sketch, "E1231", {"start": v(9.98, -0.27) * mm, "end": v(10.2, -0.17) * mm});
            skLineSegment(sketch, "E1232", {"start": v(10.2, -0.17) * mm, "end": v(10.41, -0.09) * mm});
            skLineSegment(sketch, "E1233", {"start": v(10.41, -0.09) * mm, "end": v(10.37, -0.37) * mm});
            skLineSegment(sketch, "E1234", {"start": v(10.37, -0.37) * mm, "end": v(10.28, -0.63) * mm});
            skLineSegment(sketch, "E1235", {"start": v(10.28, -0.63) * mm, "end": v(10.17, -0.88) * mm});
            skLineSegment(sketch, "E1236", {"start": v(10.17, -0.88) * mm, "end": v(10.04, -1.11) * mm});
            skLineSegment(sketch, "E1237", {"start": v(10.04, -1.11) * mm, "end": v(9.88, -1.32) * mm});
            skLineSegment(sketch, "E1238", {"start": v(9.88, -1.32) * mm, "end": v(9.7, -1.52) * mm});
            skLineSegment(sketch, "E1239", {"start": v(9.7, -1.52) * mm, "end": v(9.52, -1.7) * mm});
            skLineSegment(sketch, "E1240", {"start": v(9.52, -1.7) * mm, "end": v(9.32, -1.87) * mm});
            skLineSegment(sketch, "E1241", {"start": v(9.32, -1.87) * mm, "end": v(9.07, -2.08) * mm});
            skLineSegment(sketch, "E1242", {"start": v(9.07, -2.08) * mm, "end": v(8.87, -2.26) * mm});
            skLineSegment(sketch, "E1243", {"start": v(8.87, -2.26) * mm, "end": v(8.8, -2.33) * mm});
            skLineSegment(sketch, "E1244", {"start": v(8.8, -2.33) * mm, "end": v(9.59, -2.21) * mm});
            skLineSegment(sketch, "E1245", {"start": v(9.59, -2.21) * mm, "end": v(9.5, -2.44) * mm});
            skLineSegment(sketch, "E1246", {"start": v(9.5, -2.44) * mm, "end": v(9.34, -2.69) * mm});
            skLineSegment(sketch, "E1247", {"start": v(9.34, -2.69) * mm, "end": v(9.11, -2.93) * mm});
            skLineSegment(sketch, "E1248", {"start": v(9.11, -2.93) * mm, "end": v(8.85, -3.17) * mm});
            skLineSegment(sketch, "E1249", {"start": v(8.85, -3.17) * mm, "end": v(8.56, -3.4) * mm});
            skLineSegment(sketch, "E1250", {"start": v(8.56, -3.4) * mm, "end": v(8.28, -3.6) * mm});
            skLineSegment(sketch, "E1251", {"start": v(8.28, -3.6) * mm, "end": v(8.02, -3.76) * mm});
            skLineSegment(sketch, "E1252", {"start": v(8.02, -3.76) * mm, "end": v(7.8, -3.88) * mm});
            skLineSegment(sketch, "E1253", {"start": v(7.8, -3.88) * mm, "end": v(7.99, -3.84) * mm});
            skLineSegment(sketch, "E1254", {"start": v(7.99, -3.84) * mm, "end": v(8.18, -3.78) * mm});
            skLineSegment(sketch, "E1255", {"start": v(8.18, -3.78) * mm, "end": v(8.37, -3.71) * mm});
            skLineSegment(sketch, "E1256", {"start": v(8.37, -3.71) * mm, "end": v(8.55, -3.64) * mm});
            skLineSegment(sketch, "E1257", {"start": v(8.55, -3.64) * mm, "end": v(8.73, -3.55) * mm});
            skLineSegment(sketch, "E1258", {"start": v(8.73, -3.55) * mm, "end": v(8.9, -3.45) * mm});
            skLineSegment(sketch, "E1259", {"start": v(8.9, -3.45) * mm, "end": v(9.06, -3.34) * mm});
            skLineSegment(sketch, "E1260", {"start": v(9.06, -3.34) * mm, "end": v(9.21, -3.22) * mm});
            skLineSegment(sketch, "E1261", {"start": v(9.21, -3.22) * mm, "end": v(9.36, -3.14) * mm});
            skLineSegment(sketch, "E1262", {"start": v(9.36, -3.14) * mm, "end": v(9.56, -3.1) * mm});
            skLineSegment(sketch, "E1263", {"start": v(9.56, -3.1) * mm, "end": v(9.8, -3.1) * mm});
            skLineSegment(sketch, "E1264", {"start": v(9.8, -3.1) * mm, "end": v(10.11, -3.1) * mm});
            skLineSegment(sketch, "E1265", {"start": v(10.11, -3.1) * mm, "end": v(10.5, -3.08) * mm});
            skLineSegment(sketch, "E1266", {"start": v(10.5, -3.08) * mm, "end": v(10.94, -3) * mm});
            skLineSegment(sketch, "E1267", {"start": v(10.94, -3) * mm, "end": v(11.48, -2.84) * mm});
            skLineSegment(sketch, "E1268", {"start": v(11.48, -2.84) * mm, "end": v(12.1, -2.57) * mm});
            skLineSegment(sketch, "E1269", {"start": v(12.1, -2.57) * mm, "end": v(12.03, -2.97) * mm});
            skLineSegment(sketch, "E1270", {"start": v(12.03, -2.97) * mm, "end": v(11.87, -3.31) * mm});
            skLineSegment(sketch, "E1271", {"start": v(11.87, -3.31) * mm, "end": v(11.62, -3.6) * mm});
            skLineSegment(sketch, "E1272", {"start": v(11.62, -3.6) * mm, "end": v(11.32, -3.83) * mm});
            skLineSegment(sketch, "E1273", {"start": v(11.32, -3.83) * mm, "end": v(10.97, -4.02) * mm});
            skLineSegment(sketch, "E1274", {"start": v(10.97, -4.02) * mm, "end": v(10.6, -4.18) * mm});
            skLineSegment(sketch, "E1275", {"start": v(10.6, -4.18) * mm, "end": v(10.23, -4.3) * mm});
            skLineSegment(sketch, "E1276", {"start": v(10.23, -4.3) * mm, "end": v(9.87, -4.42) * mm});
            skLineSegment(sketch, "E1277", {"start": v(9.87, -4.42) * mm, "end": v(9.61, -4.48) * mm});
            skLineSegment(sketch, "E1278", {"start": v(9.61, -4.48) * mm, "end": v(9.28, -4.54) * mm});
            skLineSegment(sketch, "E1279", {"start": v(9.28, -4.54) * mm, "end": v(9.12, -4.58) * mm});
            skLineSegment(sketch, "E1280", {"start": v(9.12, -4.58) * mm, "end": v(8.98, -4.62) * mm});
            skLineSegment(sketch, "E1281", {"start": v(8.98, -4.62) * mm, "end": v(8.86, -4.66) * mm});
            skLineSegment(sketch, "E1282", {"start": v(8.86, -4.66) * mm, "end": v(8.77, -4.7) * mm});
            skLineSegment(sketch, "E1283", {"start": v(8.77, -4.7) * mm, "end": v(8.94, -4.71) * mm});
            skLineSegment(sketch, "E1284", {"start": v(8.94, -4.71) * mm, "end": v(9.13, -4.71) * mm});
            skLineSegment(sketch, "E1285", {"start": v(9.13, -4.71) * mm, "end": v(9.32, -4.7) * mm});
            skLineSegment(sketch, "E1286", {"start": v(9.32, -4.7) * mm, "end": v(9.52, -4.7) * mm});
            skLineSegment(sketch, "E1287", {"start": v(9.52, -4.7) * mm, "end": v(9.72, -4.68) * mm});
            skLineSegment(sketch, "E1288", {"start": v(9.72, -4.68) * mm, "end": v(9.91, -4.66) * mm});
            skLineSegment(sketch, "E1289", {"start": v(9.91, -4.66) * mm, "end": v(10.1, -4.63) * mm});
            skLineSegment(sketch, "E1290", {"start": v(10.1, -4.63) * mm, "end": v(10.26, -4.6) * mm});
            skLineSegment(sketch, "E1291", {"start": v(10.26, -4.6) * mm, "end": v(10.5, -4.53) * mm});
            skLineSegment(sketch, "E1292", {"start": v(10.5, -4.53) * mm, "end": v(10.71, -4.47) * mm});
            skLineSegment(sketch, "E1293", {"start": v(10.71, -4.47) * mm, "end": v(10.9, -4.4) * mm});
            skLineSegment(sketch, "E1294", {"start": v(10.9, -4.4) * mm, "end": v(11.04, -4.35) * mm});
            skLineSegment(sketch, "E1295", {"start": v(11.04, -4.35) * mm, "end": v(11.28, -4.25) * mm});
            skLineSegment(sketch, "E1296", {"start": v(11.28, -4.25) * mm, "end": v(11.44, -4.2) * mm});
            skLineSegment(sketch, "E1297", {"start": v(11.44, -4.2) * mm, "end": v(11.51, -4.79) * mm});
            skLineSegment(sketch, "E1298", {"start": v(11.51, -4.79) * mm, "end": v(11.43, -5.24) * mm});
            skLineSegment(sketch, "E1299", {"start": v(11.43, -5.24) * mm, "end": v(11.22, -5.58) * mm});
            skLineSegment(sketch, "E1300", {"start": v(11.22, -5.58) * mm, "end": v(10.9, -5.82) * mm});
            skLineSegment(sketch, "E1301", {"start": v(10.9, -5.82) * mm, "end": v(10.47, -5.98) * mm});
            skLineSegment(sketch, "E1302", {"start": v(10.47, -5.98) * mm, "end": v(9.98, -6.1) * mm});
            skLineSegment(sketch, "E1303", {"start": v(9.98, -6.1) * mm, "end": v(9.44, -6.16) * mm});
            skLineSegment(sketch, "E1304", {"start": v(9.44, -6.16) * mm, "end": v(8.87, -6.22) * mm});
            skLineSegment(sketch, "E1305", {"start": v(8.87, -6.22) * mm, "end": v(8.99, -6.22) * mm});
            skLineSegment(sketch, "E1306", {"start": v(8.99, -6.22) * mm, "end": v(9.1, -6.24) * mm});
            skLineSegment(sketch, "E1307", {"start": v(9.1, -6.24) * mm, "end": v(9.22, -6.27) * mm});
            skLineSegment(sketch, "E1308", {"start": v(9.22, -6.27) * mm, "end": v(9.33, -6.29) * mm});
            skLineSegment(sketch, "E1309", {"start": v(9.33, -6.29) * mm, "end": v(9.47, -6.3) * mm});
            skLineSegment(sketch, "E1310", {"start": v(9.47, -6.3) * mm, "end": v(9.61, -6.3) * mm});
            skLineSegment(sketch, "E1311", {"start": v(9.61, -6.3) * mm, "end": v(9.76, -6.31) * mm});
            skLineSegment(sketch, "E1312", {"start": v(9.76, -6.31) * mm, "end": v(9.9, -6.32) * mm});
            skLineSegment(sketch, "E1313", {"start": v(9.9, -6.32) * mm, "end": v(10.06, -6.32) * mm});
            skLineSegment(sketch, "E1314", {"start": v(10.06, -6.32) * mm, "end": v(10.2, -6.32) * mm});
            skLineSegment(sketch, "E1315", {"start": v(10.2, -6.32) * mm, "end": v(10.34, -6.31) * mm});
            skLineSegment(sketch, "E1316", {"start": v(10.34, -6.31) * mm, "end": v(10.48, -6.3) * mm});
            skLineSegment(sketch, "E1317", {"start": v(10.48, -6.3) * mm, "end": v(10.75, -6.27) * mm});
            skLineSegment(sketch, "E1318", {"start": v(10.75, -6.27) * mm, "end": v(11.03, -6.23) * mm});
            skLineSegment(sketch, "E1319", {"start": v(11.03, -6.23) * mm, "end": v(10.78, -6.76) * mm});
            skLineSegment(sketch, "E1320", {"start": v(10.78, -6.76) * mm, "end": v(10.42, -7.17) * mm});
            skLineSegment(sketch, "E1321", {"start": v(10.42, -7.17) * mm, "end": v(9.99, -7.47) * mm});
            skLineSegment(sketch, "E1322", {"start": v(9.99, -7.47) * mm, "end": v(9.49, -7.67) * mm});
            skLineSegment(sketch, "E1323", {"start": v(9.49, -7.67) * mm, "end": v(8.95, -7.77) * mm});
            skLineSegment(sketch, "E1324", {"start": v(8.95, -7.77) * mm, "end": v(8.4, -7.78) * mm});
            skLineSegment(sketch, "E1325", {"start": v(8.4, -7.78) * mm, "end": v(7.83, -7.7) * mm});
            skLineSegment(sketch, "E1326", {"start": v(7.83, -7.7) * mm, "end": v(7.29, -7.56) * mm});
            skLineSegment(sketch, "E1327", {"start": v(7.29, -7.56) * mm, "end": v(7.34, -7.34) * mm});
            skLineSegment(sketch, "E1328", {"start": v(7.34, -7.34) * mm, "end": v(7.39, -7.13) * mm});
            skLineSegment(sketch, "E1329", {"start": v(7.39, -7.13) * mm, "end": v(7.42, -6.92) * mm});
            skLineSegment(sketch, "E1330", {"start": v(7.42, -6.92) * mm, "end": v(7.44, -6.67) * mm});
            skLineSegment(sketch, "E1331", {"start": v(7.44, -6.67) * mm, "end": v(7.26, -6.7) * mm});
            skLineSegment(sketch, "E1332", {"start": v(7.26, -6.7) * mm, "end": v(7.1, -6.73) * mm});
            skLineSegment(sketch, "E1333", {"start": v(7.1, -6.73) * mm, "end": v(6.99, -6.75) * mm});
            skLineSegment(sketch, "E1334", {"start": v(6.99, -6.75) * mm, "end": v(6.87, -6.75) * mm});
            skLineSegment(sketch, "E1335", {"start": v(6.87, -6.75) * mm, "end": v(6.77, -6.73) * mm});
            skLineSegment(sketch, "E1336", {"start": v(6.77, -6.73) * mm, "end": v(6.65, -6.7) * mm});
            skLineSegment(sketch, "E1337", {"start": v(6.65, -6.7) * mm, "end": v(6.53, -6.64) * mm});
            skLineSegment(sketch, "E1338", {"start": v(6.53, -6.64) * mm, "end": v(6.37, -6.56) * mm});
            skLineSegment(sketch, "E1339", {"start": v(6.37, -6.56) * mm, "end": v(6.48, -6.52) * mm});
            skLineSegment(sketch, "E1340", {"start": v(6.48, -6.52) * mm, "end": v(6.62, -6.48) * mm});
            skLineSegment(sketch, "E1341", {"start": v(6.62, -6.48) * mm, "end": v(6.78, -6.44) * mm});
            skLineSegment(sketch, "E1342", {"start": v(6.78, -6.44) * mm, "end": v(6.96, -6.41) * mm});
            skLineSegment(sketch, "E1343", {"start": v(6.96, -6.41) * mm, "end": v(7.14, -6.39) * mm});
            skLineSegment(sketch, "E1344", {"start": v(7.14, -6.39) * mm, "end": v(7.32, -6.37) * mm});
            skLineSegment(sketch, "E1345", {"start": v(7.32, -6.37) * mm, "end": v(7.47, -6.37) * mm});
            skLineSegment(sketch, "E1346", {"start": v(7.47, -6.37) * mm, "end": v(7.6, -6.38) * mm});
            skLineSegment(sketch, "E1347", {"start": v(7.6, -6.38) * mm, "end": v(7.74, -6.44) * mm});
            skLineSegment(sketch, "E1348", {"start": v(7.74, -6.44) * mm, "end": v(7.86, -6.54) * mm});
            skLineSegment(sketch, "E1349", {"start": v(7.86, -6.54) * mm, "end": v(7.95, -6.66) * mm});
            skLineSegment(sketch, "E1350", {"start": v(7.95, -6.66) * mm, "end": v(8.02, -6.8) * mm});
            skLineSegment(sketch, "E1351", {"start": v(8.02, -6.8) * mm, "end": v(8.1, -7.09) * mm});
            skLineSegment(sketch, "E1352", {"start": v(8.1, -7.09) * mm, "end": v(8.15, -7.27) * mm});
            skLineSegment(sketch, "E1353", {"start": v(8.15, -7.27) * mm, "end": v(8.25, -7.14) * mm});
            skLineSegment(sketch, "E1354", {"start": v(8.25, -7.14) * mm, "end": v(8.36, -6.93) * mm});
            skLineSegment(sketch, "E1355", {"start": v(8.36, -6.93) * mm, "end": v(8.47, -6.67) * mm});
            skLineSegment(sketch, "E1356", {"start": v(8.47, -6.67) * mm, "end": v(8.56, -6.38) * mm});
            skLineSegment(sketch, "E1357", {"start": v(8.56, -6.38) * mm, "end": v(8.64, -6.07) * mm});
            skLineSegment(sketch, "E1358", {"start": v(8.64, -6.07) * mm, "end": v(8.68, -5.76) * mm});
            skLineSegment(sketch, "E1359", {"start": v(8.68, -5.76) * mm, "end": v(8.7, -5.46) * mm});
            skLineSegment(sketch, "E1360", {"start": v(8.7, -5.46) * mm, "end": v(8.66, -5.19) * mm});
            skLineSegment(sketch, "E1361", {"start": v(8.66, -5.19) * mm, "end": v(8.56, -4.92) * mm});
            skLineSegment(sketch, "E1362", {"start": v(8.56, -4.92) * mm, "end": v(8.43, -4.72) * mm});
            skLineSegment(sketch, "E1363", {"start": v(8.43, -4.72) * mm, "end": v(8.26, -4.59) * mm});
            skLineSegment(sketch, "E1364", {"start": v(8.26, -4.59) * mm, "end": v(8.06, -4.5) * mm});
            skLineSegment(sketch, "E1365", {"start": v(8.06, -4.5) * mm, "end": v(7.82, -4.43) * mm});
            skLineSegment(sketch, "E1366", {"start": v(7.82, -4.43) * mm, "end": v(7.56, -4.38) * mm});
            skLineSegment(sketch, "E1367", {"start": v(7.56, -4.38) * mm, "end": v(7.26, -4.32) * mm});
            skLineSegment(sketch, "E1368", {"start": v(7.26, -4.32) * mm, "end": v(6.94, -4.24) * mm});
            skLineSegment(sketch, "E1369", {"start": v(6.94, -4.24) * mm, "end": v(6.88, -4.04) * mm});
            skLineSegment(sketch, "E1370", {"start": v(6.88, -4.04) * mm, "end": v(6.83, -3.83) * mm});
            skLineSegment(sketch, "E1371", {"start": v(6.83, -3.83) * mm, "end": v(6.79, -3.71) * mm});
            skLineSegment(sketch, "E1372", {"start": v(6.79, -3.71) * mm, "end": v(6.72, -3.59) * mm});
            skLineSegment(sketch, "E1373", {"start": v(6.72, -3.59) * mm, "end": v(6.63, -3.45) * mm});
            skLineSegment(sketch, "E1374", {"start": v(6.63, -3.45) * mm, "end": v(6.5, -3.3) * mm});
            skLineSegment(sketch, "E1375", {"start": v(6.5, -3.3) * mm, "end": v(6.37, -3.2) * mm});
            skLineSegment(sketch, "E1376", {"start": v(6.37, -3.2) * mm, "end": v(6.25, -3.13) * mm});
            skLineSegment(sketch, "E1377", {"start": v(6.25, -3.13) * mm, "end": v(6.13, -3.07) * mm});
            skLineSegment(sketch, "E1378", {"start": v(6.13, -3.07) * mm, "end": v(6, -3.03) * mm});
            skLineSegment(sketch, "E1379", {"start": v(6, -3.03) * mm, "end": v(5.9, -3) * mm});
            skLineSegment(sketch, "E1380", {"start": v(5.9, -3) * mm, "end": v(5.78, -2.96) * mm});
            skLineSegment(sketch, "E1381", {"start": v(5.78, -2.96) * mm, "end": v(5.67, -2.92) * mm});
            skLineSegment(sketch, "E1382", {"start": v(5.67, -2.92) * mm, "end": v(5.56, -2.86) * mm});
            skLineSegment(sketch, "E1383", {"start": v(5.56, -2.86) * mm, "end": v(5.73, -2.28) * mm});
            skLineSegment(sketch, "E1384", {"start": v(5.73, -2.28) * mm, "end": v(5.78, -1.74) * mm});
            skLineSegment(sketch, "E1385", {"start": v(5.78, -1.74) * mm, "end": v(5.75, -1.24) * mm});
            skLineSegment(sketch, "E1386", {"start": v(5.75, -1.24) * mm, "end": v(5.64, -0.76) * mm});
            skLineSegment(sketch, "E1387", {"start": v(5.64, -0.76) * mm, "end": v(5.45, -0.3) * mm});
            skLineSegment(sketch, "E1388", {"start": v(5.45, -0.3) * mm, "end": v(5.22, 0.14) * mm});
            skLineSegment(sketch, "E1389", {"start": v(5.22, 0.14) * mm, "end": v(4.94, 0.59) * mm});
            skLineSegment(sketch, "E1390", {"start": v(4.94, 0.59) * mm, "end": v(4.62, 1.03) * mm});
            skLineSegment(sketch, "E1391", {"start": v(4.62, 1.03) * mm, "end": v(4.44, 1.34) * mm});
            skLineSegment(sketch, "E1392", {"start": v(4.44, 1.34) * mm, "end": v(4.32, 1.66) * mm});
            skLineSegment(sketch, "E1393", {"start": v(4.32, 1.66) * mm, "end": v(4.25, 2) * mm});
            skLineSegment(sketch, "E1394", {"start": v(4.25, 2) * mm, "end": v(4.24, 2.35) * mm});
            skLineSegment(sketch, "E1395", {"start": v(4.24, 2.35) * mm, "end": v(4.28, 2.7) * mm});
            skLineSegment(sketch, "E1396", {"start": v(4.28, 2.7) * mm, "end": v(4.39, 3.04) * mm});
            skLineSegment(sketch, "E1397", {"start": v(4.39, 3.04) * mm, "end": v(4.55, 3.37) * mm});
            skLineSegment(sketch, "E1398", {"start": v(4.55, 3.37) * mm, "end": v(4.78, 3.68) * mm});
            skLineSegment(sketch, "E1399", {"start": v(4.78, 3.68) * mm, "end": v(4.88, 3.8) * mm});
            skLineSegment(sketch, "E1400", {"start": v(4.88, 3.8) * mm, "end": v(5, 3.9) * mm});
            skLineSegment(sketch, "E1401", {"start": v(5, 3.9) * mm, "end": v(5.11, 4) * mm});
            skLineSegment(sketch, "E1402", {"start": v(5.11, 4) * mm, "end": v(5.24, 4.08) * mm});
            skLineSegment(sketch, "E1403", {"start": v(5.24, 4.08) * mm, "end": v(5.5, 4.25) * mm});
            skLineSegment(sketch, "E1404", {"start": v(5.5, 4.25) * mm, "end": v(5.82, 4.43) * mm});
            skLineSegment(sketch, "E1405", {"start": v(5.82, 4.43) * mm, "end": v(7.5, 5.42) * mm});
            skLineSegment(sketch, "E1406", {"start": v(7.5, 5.42) * mm, "end": v(7.65, 5.5) * mm});
            skLineSegment(sketch, "E1407", {"start": v(7.65, 5.5) * mm, "end": v(7.78, 5.59) * mm});
            skLineSegment(sketch, "E1408", {"start": v(7.78, 5.59) * mm, "end": v(7.92, 5.67) * mm});
            skLineSegment(sketch, "E1409", {"start": v(7.92, 5.67) * mm, "end": v(8.06, 5.75) * mm});
            skLineSegment(sketch, "E1410", {"start": v(8.06, 5.75) * mm, "end": v(8.06, 6.2) * mm});
            skLineSegment(sketch, "E1411", {"start": v(8.06, 6.2) * mm, "end": v(8.04, 6.2) * mm});
            skLineSegment(sketch, "E1412", {"start": v(8.04, 6.2) * mm, "end": v(7.92, 6.14) * mm});
            skLineSegment(sketch, "E1413", {"start": v(7.92, 6.14) * mm, "end": v(7.67, 6.01) * mm});
            skLineSegment(sketch, "E1414", {"start": v(7.67, 6.01) * mm, "end": v(7.34, 5.82) * mm});
            skLineSegment(sketch, "E1415", {"start": v(7.34, 5.82) * mm, "end": v(6.95, 5.6) * mm});
            skLineSegment(sketch, "E1416", {"start": v(6.95, 5.6) * mm, "end": v(6.55, 5.36) * mm});
            skLineSegment(sketch, "E1417", {"start": v(6.55, 5.36) * mm, "end": v(6.17, 5.14) * mm});
            skLineSegment(sketch, "E1418", {"start": v(6.17, 5.14) * mm, "end": v(5.86, 4.95) * mm});
            skLineSegment(sketch, "E1419", {"start": v(5.86, 4.95) * mm, "end": v(5.64, 4.81) * mm});
            skLineSegment(sketch, "E1420", {"start": v(5.64, 4.81) * mm, "end": v(5.34, 4.62) * mm});
            skLineSegment(sketch, "E1421", {"start": v(5.34, 4.62) * mm, "end": v(5.05, 4.44) * mm});
            skLineSegment(sketch, "E1422", {"start": v(5.05, 4.44) * mm, "end": v(4.77, 4.25) * mm});
            skLineSegment(sketch, "E1423", {"start": v(4.77, 4.25) * mm, "end": v(4.52, 4.05) * mm});
            skLineSegment(sketch, "E1424", {"start": v(4.52, 4.05) * mm, "end": v(4.29, 3.82) * mm});
            skLineSegment(sketch, "E1425", {"start": v(4.29, 3.82) * mm, "end": v(4.1, 3.55) * mm});
            skLineSegment(sketch, "E1426", {"start": v(4.1, 3.55) * mm, "end": v(3.93, 3.23) * mm});
            skLineSegment(sketch, "E1427", {"start": v(3.93, 3.23) * mm, "end": v(3.8, 2.86) * mm});
            skLineSegment(sketch, "E1428", {"start": v(3.8, 2.86) * mm, "end": v(3.75, 2.55) * mm});
            skLineSegment(sketch, "E1429", {"start": v(3.75, 2.55) * mm, "end": v(3.73, 2.25) * mm});
            skLineSegment(sketch, "E1430", {"start": v(3.73, 2.25) * mm, "end": v(3.75, 1.95) * mm});
            skLineSegment(sketch, "E1431", {"start": v(3.75, 1.95) * mm, "end": v(3.8, 1.66) * mm});
            skLineSegment(sketch, "E1432", {"start": v(3.8, 1.66) * mm, "end": v(3.89, 1.37) * mm});
            skLineSegment(sketch, "E1433", {"start": v(3.89, 1.37) * mm, "end": v(4, 1.1) * mm});
            skLineSegment(sketch, "E1434", {"start": v(4, 1.1) * mm, "end": v(4.16, 0.85) * mm});
            skLineSegment(sketch, "E1435", {"start": v(4.16, 0.85) * mm, "end": v(4.34, 0.62) * mm});
            skLineSegment(sketch, "E1436", {"start": v(4.34, 0.62) * mm, "end": v(4.5, 0.43) * mm});
            skLineSegment(sketch, "E1437", {"start": v(4.5, 0.43) * mm, "end": v(4.66, 0.23) * mm});
            skLineSegment(sketch, "E1438", {"start": v(4.66, 0.23) * mm, "end": v(4.81, 0.02) * mm});
            skLineSegment(sketch, "E1439", {"start": v(4.81, 0.02) * mm, "end": v(4.95, -0.2) * mm});
            skLineSegment(sketch, "E1440", {"start": v(4.95, -0.2) * mm, "end": v(5.09, -0.44) * mm});
            skLineSegment(sketch, "E1441", {"start": v(5.09, -0.44) * mm, "end": v(5.2, -0.68) * mm});
            skLineSegment(sketch, "E1442", {"start": v(5.2, -0.68) * mm, "end": v(5.3, -0.93) * mm});
            skLineSegment(sketch, "E1443", {"start": v(5.3, -0.93) * mm, "end": v(5.36, -1.2) * mm});
            skLineSegment(sketch, "E1444", {"start": v(5.36, -1.2) * mm, "end": v(5.4, -1.46) * mm});
            skLineSegment(sketch, "E1445", {"start": v(5.4, -1.46) * mm, "end": v(5.43, -1.68) * mm});
            skLineSegment(sketch, "E1446", {"start": v(5.43, -1.68) * mm, "end": v(5.44, -1.87) * mm});
            skLineSegment(sketch, "E1447", {"start": v(5.44, -1.87) * mm, "end": v(5.42, -2.04) * mm});
            skLineSegment(sketch, "E1448", {"start": v(5.42, -2.04) * mm, "end": v(5.4, -2.2) * mm});
            skLineSegment(sketch, "E1449", {"start": v(5.4, -2.2) * mm, "end": v(5.35, -2.38) * mm});
            skLineSegment(sketch, "E1450", {"start": v(5.35, -2.38) * mm, "end": v(5.3, -2.58) * mm});
            skLineSegment(sketch, "E1451", {"start": v(5.3, -2.58) * mm, "end": v(5.22, -2.81) * mm});
            skLineSegment(sketch, "E1452", {"start": v(5.22, -2.81) * mm, "end": v(4.98, -2.8) * mm});
            skLineSegment(sketch, "E1453", {"start": v(4.98, -2.8) * mm, "end": v(4.74, -2.8) * mm});
            skLineSegment(sketch, "E1454", {"start": v(4.74, -2.8) * mm, "end": v(4.5, -2.78) * mm});
            skLineSegment(sketch, "E1455", {"start": v(4.5, -2.78) * mm, "end": v(4.25, -2.75) * mm});
            skLineSegment(sketch, "E1456", {"start": v(4.25, -2.75) * mm, "end": v(4, -2.72) * mm});
            skLineSegment(sketch, "E1457", {"start": v(4, -2.72) * mm, "end": v(3.75, -2.69) * mm});
            skLineSegment(sketch, "E1458", {"start": v(3.75, -2.69) * mm, "end": v(3.51, -2.65) * mm});
            skLineSegment(sketch, "E1459", {"start": v(3.51, -2.65) * mm, "end": v(3.28, -2.61) * mm});
            skLineSegment(sketch, "E1460", {"start": v(3.28, -2.61) * mm, "end": v(2.7, -2.51) * mm});
            skLineSegment(sketch, "E1461", {"start": v(2.7, -2.51) * mm, "end": v(2.22, -2.4) * mm});
            skLineSegment(sketch, "E1462", {"start": v(2.22, -2.4) * mm, "end": v(1.66, -2.32) * mm});
            skLineSegment(sketch, "E1463", {"start": v(1.66, -2.32) * mm, "end": v(1.05, -2.26) * mm});
            skLineSegment(sketch, "E1464", {"start": v(1.05, -2.26) * mm, "end": v(0.42, -2.23) * mm});
            skLineSegment(sketch, "E1465", {"start": v(0.42, -2.23) * mm, "end": v(-0.22, -2.22) * mm});
            skLineSegment(sketch, "E1466", {"start": v(-0.22, -2.22) * mm, "end": v(-0.84, -2.25) * mm});
            skLineSegment(sketch, "E1467", {"start": v(-0.84, -2.25) * mm, "end": v(-1.42, -2.3) * mm});
            skLineSegment(sketch, "E1468", {"start": v(-1.42, -2.3) * mm, "end": v(-1.93, -2.41) * mm});
            skLineSegment(sketch, "E1469", {"start": v(-1.93, -2.41) * mm, "end": v(-2.24, -2.5) * mm});
            skLineSegment(sketch, "E1470", {"start": v(-2.24, -2.5) * mm, "end": v(-2.57, -2.63) * mm});
            skLineSegment(sketch, "E1471", {"start": v(-2.57, -2.63) * mm, "end": v(-2.9, -2.78) * mm});
            skLineSegment(sketch, "E1472", {"start": v(-2.9, -2.78) * mm, "end": v(-3.25, -2.95) * mm});
            skLineSegment(sketch, "E1473", {"start": v(-3.25, -2.95) * mm, "end": v(-3.56, -3.13) * mm});
            skLineSegment(sketch, "E1474", {"start": v(-3.56, -3.13) * mm, "end": v(-3.84, -3.33) * mm});
            skLineSegment(sketch, "E1475", {"start": v(-3.84, -3.33) * mm, "end": v(-4.07, -3.53) * mm});
            skLineSegment(sketch, "E1476", {"start": v(-4.07, -3.53) * mm, "end": v(-4.23, -3.73) * mm});
            skLineSegment(sketch, "E1477", {"start": v(-4.23, -3.73) * mm, "end": v(-3.08, -3.66) * mm});
            skLineSegment(sketch, "E1478", {"start": v(-3.08, -3.66) * mm, "end": v(-3.8, -4.3) * mm});
            skLineSegment(sketch, "E1479", {"start": v(-3.8, -4.3) * mm, "end": v(-3.98, -4.2) * mm});
            skLineSegment(sketch, "E1480", {"start": v(-3.98, -4.2) * mm, "end": v(-4, -4.19) * mm});
            skLineSegment(sketch, "E1481", {"start": v(-4, -4.19) * mm, "end": v(-4.16, -4.04) * mm});
            skLineSegment(sketch, "E1482", {"start": v(-4.16, -4.04) * mm, "end": v(-4.38, -3.87) * mm});
            skLineSegment(sketch, "E1483", {"start": v(-4.38, -3.87) * mm, "end": v(-4.57, -3.7) * mm});
            skLineSegment(sketch, "E1484", {"start": v(-4.57, -3.7) * mm, "end": v(-4.75, -3.51) * mm});
            skLineSegment(sketch, "E1485", {"start": v(-4.75, -3.51) * mm, "end": v(-4.92, -3.3) * mm});
            skLineSegment(sketch, "E1486", {"start": v(-4.92, -3.3) * mm, "end": v(-5.2, -2.85) * mm});
            skLineSegment(sketch, "E1487", {"start": v(-5.2, -2.85) * mm, "end": v(-5.36, -2.4) * mm});
            skLineSegment(sketch, "E1488", {"start": v(-5.36, -2.4) * mm, "end": v(-5.42, -1.92) * mm});
            skLineSegment(sketch, "E1489", {"start": v(-5.42, -1.92) * mm, "end": v(-5.4, -1.45) * mm});
            skLineSegment(sketch, "E1490", {"start": v(-5.4, -1.45) * mm, "end": v(-5.3, -0.99) * mm});
            skLineSegment(sketch, "E1491", {"start": v(-5.3, -0.99) * mm, "end": v(-5.12, -0.53) * mm});
            skLineSegment(sketch, "E1492", {"start": v(-5.12, -0.53) * mm, "end": v(-4.88, -0.1) * mm});
            skLineSegment(sketch, "E1493", {"start": v(-4.88, -0.1) * mm, "end": v(-4.6, 0.3) * mm});
            skLineSegment(sketch, "E1494", {"start": v(-4.6, 0.3) * mm, "end": v(-4.44, 0.51) * mm});
            skLineSegment(sketch, "E1495", {"start": v(-4.44, 0.51) * mm, "end": v(-4.26, 0.72) * mm});
            skLineSegment(sketch, "E1496", {"start": v(-4.26, 0.72) * mm, "end": v(-4.11, 0.9) * mm});
            skLineSegment(sketch, "E1497", {"start": v(-4.11, 0.9) * mm, "end": v(-4.05, 1) * mm});
            skLineSegment(sketch, "E1498", {"start": v(-4.05, 1) * mm, "end": v(-3.98, 1.11) * mm});
            skLineSegment(sketch, "E1499", {"start": v(-3.98, 1.11) * mm, "end": v(-3.92, 1.27) * mm});
            skLineSegment(sketch, "E1500", {"start": v(-3.92, 1.27) * mm, "end": v(-3.85, 1.47) * mm});
            skLineSegment(sketch, "E1501", {"start": v(-3.85, 1.47) * mm, "end": v(-3.78, 1.81) * mm});
            skLineSegment(sketch, "E1502", {"start": v(-3.78, 1.81) * mm, "end": v(-3.74, 2.15) * mm});
            skLineSegment(sketch, "E1503", {"start": v(-3.74, 2.15) * mm, "end": v(-3.75, 2.47) * mm});
            skLineSegment(sketch, "E1504", {"start": v(-3.75, 2.47) * mm, "end": v(-3.8, 2.79) * mm});
            skLineSegment(sketch, "E1505", {"start": v(-3.8, 2.79) * mm, "end": v(-3.89, 3.09) * mm});
            skLineSegment(sketch, "E1506", {"start": v(-3.89, 3.09) * mm, "end": v(-4, 3.37) * mm});
            skLineSegment(sketch, "E1507", {"start": v(-4, 3.37) * mm, "end": v(-4.15, 3.62) * mm});
            skLineSegment(sketch, "E1508", {"start": v(-4.15, 3.62) * mm, "end": v(-4.32, 3.85) * mm});
            skLineSegment(sketch, "E1509", {"start": v(-4.32, 3.85) * mm, "end": v(-4.6, 4.12) * mm});
            skLineSegment(sketch, "E1510", {"start": v(-4.6, 4.12) * mm, "end": v(-5.02, 4.42) * mm});
            skLineSegment(sketch, "E1511", {"start": v(-5.02, 4.42) * mm, "end": v(-5.52, 4.74) * mm});
            skLineSegment(sketch, "E1512", {"start": v(-5.52, 4.74) * mm, "end": v(-6.06, 5.07) * mm});
            skLineSegment(sketch, "E1513", {"start": v(-6.06, 5.07) * mm, "end": v(-6.63, 5.4) * mm});
            skLineSegment(sketch, "E1514", {"start": v(-6.63, 5.4) * mm, "end": v(-7.17, 5.7) * mm});
            skLineSegment(sketch, "E1515", {"start": v(-7.17, 5.7) * mm, "end": v(-7.65, 5.98) * mm});
            skLineSegment(sketch, "E1516", {"start": v(-7.65, 5.98) * mm, "end": v(-8.03, 6.22) * mm});
            skLineSegment(sketch, "E1517", {"start": v(-8.03, 6.22) * mm, "end": v(-8.26, 6.37) * mm});
            skLineSegment(sketch, "E1518", {"start": v(-8.26, 6.37) * mm, "end": v(-8.49, 6.53) * mm});
            skLineSegment(sketch, "E1519", {"start": v(-8.49, 6.53) * mm, "end": v(-8.7, 6.68) * mm});
            skLineSegment(sketch, "E1520", {"start": v(-8.7, 6.68) * mm, "end": v(-8.93, 6.82) * mm});
            skLineSegment(sketch, "E1521", {"start": v(-8.93, 6.82) * mm, "end": v(-9.22, 7.03) * mm});
            skLineSegment(sketch, "E1522", {"start": v(-9.22, 7.03) * mm, "end": v(-9.55, 7.29) * mm});
            skLineSegment(sketch, "E1523", {"start": v(-9.55, 7.29) * mm, "end": v(-9.89, 7.6) * mm});
            skLineSegment(sketch, "E1524", {"start": v(-9.89, 7.6) * mm, "end": v(-10.22, 7.93) * mm});
            skLineSegment(sketch, "E1525", {"start": v(-10.22, 7.93) * mm, "end": v(-10.53, 8.28) * mm});
            skLineSegment(sketch, "E1526", {"start": v(-10.53, 8.28) * mm, "end": v(-10.8, 8.62) * mm});
            skLineSegment(sketch, "E1527", {"start": v(-10.8, 8.62) * mm, "end": v(-11.01, 8.95) * mm});
            skLineSegment(sketch, "E1528", {"start": v(-11.01, 8.95) * mm, "end": v(-11.15, 9.24) * mm});
            skLineSegment(sketch, "E1529", {"start": v(-11.15, 9.24) * mm, "end": v(-11.17, 9.2) * mm});
            skLineSegment(sketch, "E1530", {"start": v(-11.17, 9.2) * mm, "end": v(-11.2, 9.13) * mm});
            skLineSegment(sketch, "E1531", {"start": v(-11.2, 9.13) * mm, "end": v(-11.21, 9.07) * mm});
            skLineSegment(sketch, "E1532", {"start": v(-11.21, 9.07) * mm, "end": v(-11.22, 9) * mm});
            skLineSegment(sketch, "E1533", {"start": v(-11.22, 9) * mm, "end": v(-11.24, 8.87) * mm});
            skLineSegment(sketch, "E1534", {"start": v(-11.24, 8.87) * mm, "end": v(-11.25, 8.74) * mm});
            skLineSegment(sketch, "E1535", {"start": v(-11.25, 8.74) * mm, "end": v(-11.3, 8.18) * mm});
            skLineSegment(sketch, "E1536", {"start": v(-11.3, 8.18) * mm, "end": v(-11.53, 8.34) * mm});
            skLineSegment(sketch, "E1537", {"start": v(-11.53, 8.34) * mm, "end": v(-11.87, 8.69) * mm});
            skLineSegment(sketch, "E1538", {"start": v(-11.87, 8.69) * mm, "end": v(-12.29, 9.15) * mm});
            skLineSegment(sketch, "E1539", {"start": v(-12.29, 9.15) * mm, "end": v(-12.74, 9.67) * mm});
            skLineSegment(sketch, "E1540", {"start": v(-12.74, 9.67) * mm, "end": v(-13.18, 10.2) * mm});
            skLineSegment(sketch, "E1541", {"start": v(-13.18, 10.2) * mm, "end": v(-13.58, 10.68) * mm});
            skLineSegment(sketch, "E1542", {"start": v(-13.58, 10.68) * mm, "end": v(-13.88, 11.05) * mm});
            skLineSegment(sketch, "E1543", {"start": v(-13.88, 11.05) * mm, "end": v(-14.04, 11.26) * mm});
            skLineSegment(sketch, "E1544", {"start": v(-14.04, 11.26) * mm, "end": v(-14.24, 11.52) * mm});
            skLineSegment(sketch, "E1545", {"start": v(-14.24, 11.52) * mm, "end": v(-14.62, 12.06) * mm});
            skLineSegment(sketch, "E1546", {"start": v(-14.62, 12.06) * mm, "end": v(-14.89, 12.47) * mm});
            skLineSegment(sketch, "E1547", {"start": v(-14.89, 12.47) * mm, "end": v(-15.15, 12.89) * mm});
            skLineSegment(sketch, "E1548", {"start": v(-15.15, 12.89) * mm, "end": v(-15.4, 13.3) * mm});
            skLineSegment(sketch, "E1549", {"start": v(-15.4, 13.3) * mm, "end": v(-15.66, 13.74) * mm});
            skLineSegment(sketch, "E1550", {"start": v(-15.66, 13.74) * mm, "end": v(-15.9, 14.17) * mm});
            skLineSegment(sketch, "E1551", {"start": v(-15.9, 14.17) * mm, "end": v(-16.12, 14.61) * mm});
            skLineSegment(sketch, "E1552", {"start": v(-16.12, 14.61) * mm, "end": v(-16.33, 15.07) * mm});
            skLineSegment(sketch, "E1553", {"start": v(-16.33, 15.07) * mm, "end": v(-16.53, 15.53) * mm});
            skLineSegment(sketch, "E1554", {"start": v(-16.53, 15.53) * mm, "end": v(-16.62, 15.78) * mm});
            skLineSegment(sketch, "E1555", {"start": v(-16.62, 15.78) * mm, "end": v(-16.78, 16.2) * mm});
            skLineSegment(sketch, "E1556", {"start": v(-16.78, 16.2) * mm, "end": v(-16.94, 16.6) * mm});
            skLineSegment(sketch, "E1557", {"start": v(-16.94, 16.6) * mm, "end": v(-17.03, 16.8) * mm});
            skLineSegment(sketch, "E1558", {"start": v(-17.03, 16.8) * mm, "end": v(-17.39, 15.83) * mm});
            skLineSegment(sketch, "E1559", {"start": v(-17.39, 15.83) * mm, "end": v(-17.45, 15.93) * mm});
            skLineSegment(sketch, "E1560", {"start": v(-17.45, 15.93) * mm, "end": v(-17.52, 16.05) * mm});
            skLineSegment(sketch, "E1561", {"start": v(-17.52, 16.05) * mm, "end": v(-17.6, 16.2) * mm});
            skLineSegment(sketch, "E1562", {"start": v(-17.6, 16.2) * mm, "end": v(-17.67, 16.35) * mm});
            skLineSegment(sketch, "E1563", {"start": v(-17.67, 16.35) * mm, "end": v(-17.8, 16.66) * mm});
            skLineSegment(sketch, "E1564", {"start": v(-17.8, 16.66) * mm, "end": v(-17.92, 16.92) * mm});
            skLineSegment(sketch, "E1565", {"start": v(-17.92, 16.92) * mm, "end": v(-18.7, 18.6) * mm});
            skLineSegment(sketch, "E1566", {"start": v(-18.7, 18.6) * mm, "end": v(-19, 19.35) * mm});
            skLineSegment(sketch, "E1567", {"start": v(-19, 19.35) * mm, "end": v(-19.3, 20.1) * mm});
            skLineSegment(sketch, "E1568", {"start": v(-19.3, 20.1) * mm, "end": v(-19.58, 20.87) * mm});
            skLineSegment(sketch, "E1569", {"start": v(-19.58, 20.87) * mm, "end": v(-19.85, 21.63) * mm});
            skLineSegment(sketch, "E1570", {"start": v(-19.85, 21.63) * mm, "end": v(-20.1, 22.41) * mm});
            skLineSegment(sketch, "E1571", {"start": v(-20.1, 22.41) * mm, "end": v(-20.33, 23.2) * mm});
            skLineSegment(sketch, "E1572", {"start": v(-20.33, 23.2) * mm, "end": v(-20.53, 23.98) * mm});
            skLineSegment(sketch, "E1573", {"start": v(-20.53, 23.98) * mm, "end": v(-20.71, 24.78) * mm});
            skLineSegment(sketch, "E1574", {"start": v(-20.71, 24.78) * mm, "end": v(-20.74, 24.94) * mm});
            skLineSegment(sketch, "E1575", {"start": v(-20.74, 24.94) * mm, "end": v(-20.76, 25.12) * mm});
            skLineSegment(sketch, "E1576", {"start": v(-20.76, 25.12) * mm, "end": v(-20.78, 25.2) * mm});
            skLineSegment(sketch, "E1577", {"start": v(-20.78, 25.2) * mm, "end": v(-20.8, 25.29) * mm});
            skLineSegment(sketch, "E1578", {"start": v(-20.8, 25.29) * mm, "end": v(-20.83, 25.36) * mm});
            skLineSegment(sketch, "E1579", {"start": v(-20.83, 25.36) * mm, "end": v(-20.86, 25.43) * mm});
            skLineSegment(sketch, "E1580", {"start": v(-20.86, 25.43) * mm, "end": v(-21.07, 24.64) * mm});
            skLineSegment(sketch, "E1581", {"start": v(-21.07, 24.64) * mm, "end": v(-21.2, 23.86) * mm});
            skLineSegment(sketch, "E1582", {"start": v(-21.2, 23.86) * mm, "end": v(-21.28, 23.07) * mm});
            skLineSegment(sketch, "E1583", {"start": v(-21.28, 23.07) * mm, "end": v(-21.3, 22.29) * mm});
            skLineSegment(sketch, "E1584", {"start": v(-21.3, 22.29) * mm, "end": v(-21.25, 21.5) * mm});
            skLineSegment(sketch, "E1585", {"start": v(-21.25, 21.5) * mm, "end": v(-21.17, 20.71) * mm});
            skLineSegment(sketch, "E1586", {"start": v(-21.17, 20.71) * mm, "end": v(-21.04, 19.92) * mm});
            skLineSegment(sketch, "E1587", {"start": v(-21.04, 19.92) * mm, "end": v(-20.89, 19.13) * mm});
            skLineSegment(sketch, "E1588", {"start": v(-20.89, 19.13) * mm, "end": v(-20.83, 18.9) * mm});
            skLineSegment(sketch, "E1589", {"start": v(-20.83, 18.9) * mm, "end": v(-20.76, 18.66) * mm});
            skLineSegment(sketch, "E1590", {"start": v(-20.76, 18.66) * mm, "end": v(-20.68, 18.4) * mm});
            skLineSegment(sketch, "E1591", {"start": v(-20.68, 18.4) * mm, "end": v(-20.6, 18.15) * mm});
            skLineSegment(sketch, "E1592", {"start": v(-20.6, 18.15) * mm, "end": v(-20.5, 17.9) * mm});
            skLineSegment(sketch, "E1593", {"start": v(-20.5, 17.9) * mm, "end": v(-20.43, 17.66) * mm});
            skLineSegment(sketch, "E1594", {"start": v(-20.43, 17.66) * mm, "end": v(-20.37, 17.45) * mm});
            skLineSegment(sketch, "E1595", {"start": v(-20.37, 17.45) * mm, "end": v(-20.33, 17.27) * mm});
            skLineSegment(sketch, "E1596", {"start": v(-20.33, 17.27) * mm, "end": v(-20.55, 17.58) * mm});
            skLineSegment(sketch, "E1597", {"start": v(-20.55, 17.58) * mm, "end": v(-20.76, 17.9) * mm});
            skLineSegment(sketch, "E1598", {"start": v(-20.76, 17.9) * mm, "end": v(-20.97, 18.23) * mm});
            skLineSegment(sketch, "E1599", {"start": v(-20.97, 18.23) * mm, "end": v(-21.16, 18.56) * mm});
            skLineSegment(sketch, "E1600", {"start": v(-21.16, 18.56) * mm, "end": v(-21.35, 18.9) * mm});
            skLineSegment(sketch, "E1601", {"start": v(-21.35, 18.9) * mm, "end": v(-21.53, 19.25) * mm});
            skLineSegment(sketch, "E1602", {"start": v(-21.53, 19.25) * mm, "end": v(-21.7, 19.59) * mm});
            skLineSegment(sketch, "E1603", {"start": v(-21.7, 19.59) * mm, "end": v(-21.88, 19.92) * mm});
            skLineSegment(sketch, "E1604", {"start": v(-21.88, 19.92) * mm, "end": v(-22.06, 20.28) * mm});
            skLineSegment(sketch, "E1605", {"start": v(-22.06, 20.28) * mm, "end": v(-22.24, 20.64) * mm});
            skLineSegment(sketch, "E1606", {"start": v(-22.24, 20.64) * mm, "end": v(-22.41, 21.01) * mm});
            skLineSegment(sketch, "E1607", {"start": v(-22.41, 21.01) * mm, "end": v(-22.58, 21.38) * mm});
            skLineSegment(sketch, "E1608", {"start": v(-22.58, 21.38) * mm, "end": v(-22.74, 21.76) * mm});
            skLineSegment(sketch, "E1609", {"start": v(-22.74, 21.76) * mm, "end": v(-22.9, 22.14) * mm});
            skLineSegment(sketch, "E1610", {"start": v(-22.9, 22.14) * mm, "end": v(-23.04, 22.52) * mm});
            skLineSegment(sketch, "E1611", {"start": v(-23.04, 22.52) * mm, "end": v(-23.17, 22.9) * mm});
            skLineSegment(sketch, "E1612", {"start": v(-23.17, 22.9) * mm, "end": v(-23.26, 22.6) * mm});
            skLineSegment(sketch, "E1613", {"start": v(-23.26, 22.6) * mm, "end": v(-23.33, 22.27) * mm});
            skLineSegment(sketch, "E1614", {"start": v(-23.33, 22.27) * mm, "end": v(-23.36, 21.93) * mm});
            skLineSegment(sketch, "E1615", {"start": v(-23.36, 21.93) * mm, "end": v(-23.38, 21.57) * mm});
            skLineSegment(sketch, "E1616", {"start": v(-23.38, 21.57) * mm, "end": v(-23.37, 21.21) * mm});
            skLineSegment(sketch, "E1617", {"start": v(-23.37, 21.21) * mm, "end": v(-23.34, 20.86) * mm});
            skLineSegment(sketch, "E1618", {"start": v(-23.34, 20.86) * mm, "end": v(-23.3, 20.52) * mm});
            skLineSegment(sketch, "E1619", {"start": v(-23.3, 20.52) * mm, "end": v(-23.24, 20.2) * mm});
            skLineSegment(sketch, "E1620", {"start": v(-23.24, 20.2) * mm, "end": v(-22.92, 19.05) * mm});
            skLineSegment(sketch, "E1621", {"start": v(-22.92, 19.05) * mm, "end": v(-22.51, 17.98) * mm});
            skLineSegment(sketch, "E1622", {"start": v(-22.51, 17.98) * mm, "end": v(-22.05, 17) * mm});
            skLineSegment(sketch, "E1623", {"start": v(-22.05, 17) * mm, "end": v(-21.58, 16.12) * mm});
            skLineSegment(sketch, "E1624", {"start": v(-21.58, 16.12) * mm, "end": v(-21.13, 15.36) * mm});
            skLineSegment(sketch, "E1625", {"start": v(-21.13, 15.36) * mm, "end": v(-20.74, 14.73) * mm});
            skLineSegment(sketch, "E1626", {"start": v(-20.74, 14.73) * mm, "end": v(-20.45, 14.26) * mm});
            skLineSegment(sketch, "E1627", {"start": v(-20.45, 14.26) * mm, "end": v(-20.3, 13.95) * mm});
            skLineSegment(sketch, "E1628", {"start": v(-20.3, 13.95) * mm, "end": v(-20.5, 14.17) * mm});
            skLineSegment(sketch, "E1629", {"start": v(-20.5, 14.17) * mm, "end": v(-20.75, 14.38) * mm});
            skLineSegment(sketch, "E1630", {"start": v(-20.75, 14.38) * mm, "end": v(-21, 14.6) * mm});
            skLineSegment(sketch, "E1631", {"start": v(-21, 14.6) * mm, "end": v(-21.23, 14.82) * mm});
            skLineSegment(sketch, "E1632", {"start": v(-21.23, 14.82) * mm, "end": v(-22.26, 16) * mm});
            skLineSegment(sketch, "E1633", {"start": v(-22.26, 16) * mm, "end": v(-22.84, 16.8) * mm});
            skLineSegment(sketch, "E1634", {"start": v(-22.84, 16.8) * mm, "end": v(-22.98, 17) * mm});
            skLineSegment(sketch, "E1635", {"start": v(-22.98, 17) * mm, "end": v(-23.11, 17.2) * mm});
            skLineSegment(sketch, "E1636", {"start": v(-23.11, 17.2) * mm, "end": v(-23.24, 17.4) * mm});
            skLineSegment(sketch, "E1637", {"start": v(-23.24, 17.4) * mm, "end": v(-23.37, 17.6) * mm});
            skLineSegment(sketch, "E1638", {"start": v(-23.37, 17.6) * mm, "end": v(-23.5, 17.8) * mm});
            skLineSegment(sketch, "E1639", {"start": v(-23.5, 17.8) * mm, "end": v(-23.62, 18.02) * mm});
            skLineSegment(sketch, "E1640", {"start": v(-23.62, 18.02) * mm, "end": v(-23.75, 18.24) * mm});
            skLineSegment(sketch, "E1641", {"start": v(-23.75, 18.24) * mm, "end": v(-23.88, 18.47) * mm});
            skLineSegment(sketch, "E1642", {"start": v(-23.88, 18.47) * mm, "end": v(-23.99, 18.67) * mm});
            skLineSegment(sketch, "E1643", {"start": v(-23.99, 18.67) * mm, "end": v(-24.1, 18.89) * mm});
            skLineSegment(sketch, "E1644", {"start": v(-24.1, 18.89) * mm, "end": v(-24.23, 19.12) * mm});
            skLineSegment(sketch, "E1645", {"start": v(-24.23, 19.12) * mm, "end": v(-24.36, 19.35) * mm});
            skLineSegment(sketch, "E1646", {"start": v(-24.36, 19.35) * mm, "end": v(-24.48, 19.59) * mm});
            skLineSegment(sketch, "E1647", {"start": v(-24.48, 19.59) * mm, "end": v(-24.59, 19.82) * mm});
            skLineSegment(sketch, "E1648", {"start": v(-24.59, 19.82) * mm, "end": v(-24.68, 20.04) * mm});
            skLineSegment(sketch, "E1649", {"start": v(-24.68, 20.04) * mm, "end": v(-24.76, 20.26) * mm});
            skLineSegment(sketch, "E1650", {"start": v(-24.76, 20.26) * mm, "end": v(-24.87, 19.4) * mm});
            skLineSegment(sketch, "E1651", {"start": v(-24.87, 19.4) * mm, "end": v(-24.88, 18.58) * mm});
            skLineSegment(sketch, "E1652", {"start": v(-24.88, 18.58) * mm, "end": v(-24.8, 17.8) * mm});
            skLineSegment(sketch, "E1653", {"start": v(-24.8, 17.8) * mm, "end": v(-24.62, 17.03) * mm});
            skLineSegment(sketch, "E1654", {"start": v(-24.62, 17.03) * mm, "end": v(-24.38, 16.3) * mm});
            skLineSegment(sketch, "E1655", {"start": v(-24.38, 16.3) * mm, "end": v(-24.08, 15.56) * mm});
            skLineSegment(sketch, "E1656", {"start": v(-24.08, 15.56) * mm, "end": v(-23.72, 14.84) * mm});
            skLineSegment(sketch, "E1657", {"start": v(-23.72, 14.84) * mm, "end": v(-23.32, 14.11) * mm});
            skLineSegment(sketch, "E1658", {"start": v(-23.32, 14.11) * mm, "end": v(-23.16, 13.85) * mm});
            skLineSegment(sketch, "E1659", {"start": v(-23.16, 13.85) * mm, "end": v(-22.99, 13.6) * mm});
            skLineSegment(sketch, "E1660", {"start": v(-22.99, 13.6) * mm, "end": v(-22.81, 13.34) * mm});
            skLineSegment(sketch, "E1661", {"start": v(-22.81, 13.34) * mm, "end": v(-22.63, 13.1) * mm});
            skLineSegment(sketch, "E1662", {"start": v(-22.63, 13.1) * mm, "end": v(-22.45, 12.85) * mm});
            skLineSegment(sketch, "E1663", {"start": v(-22.45, 12.85) * mm, "end": v(-22.26, 12.6) * mm});
            skLineSegment(sketch, "E1664", {"start": v(-22.26, 12.6) * mm, "end": v(-22.07, 12.36) * mm});
            skLineSegment(sketch, "E1665", {"start": v(-22.07, 12.36) * mm, "end": v(-21.89, 12.12) * mm});
            skLineSegment(sketch, "E1666", {"start": v(-21.89, 12.12) * mm, "end": v(-21.58, 11.73) * mm});
            skLineSegment(sketch, "E1667", {"start": v(-21.58, 11.73) * mm, "end": v(-21.26, 11.35) * mm});
            skLineSegment(sketch, "E1668", {"start": v(-21.26, 11.35) * mm, "end": v(-20.93, 10.98) * mm});
            skLineSegment(sketch, "E1669", {"start": v(-20.93, 10.98) * mm, "end": v(-20.59, 10.6) * mm});
            skLineSegment(sketch, "E1670", {"start": v(-20.59, 10.6) * mm, "end": v(-20.25, 10.25) * mm});
            skLineSegment(sketch, "E1671", {"start": v(-20.25, 10.25) * mm, "end": v(-19.9, 9.89) * mm});
            skLineSegment(sketch, "E1672", {"start": v(-19.9, 9.89) * mm, "end": v(-19.55, 9.53) * mm});
            skLineSegment(sketch, "E1673", {"start": v(-19.55, 9.53) * mm, "end": v(-19.2, 9.18) * mm});
            skLineSegment(sketch, "E1674", {"start": v(-19.2, 9.18) * mm, "end": v(-19.05, 9.04) * mm});
            skLineSegment(sketch, "E1675", {"start": v(-19.05, 9.04) * mm, "end": v(-18.88, 8.9) * mm});
            skLineSegment(sketch, "E1676", {"start": v(-18.88, 8.9) * mm, "end": v(-18.8, 8.81) * mm});
            skLineSegment(sketch, "E1677", {"start": v(-18.8, 8.81) * mm, "end": v(-18.73, 8.74) * mm});
            skLineSegment(sketch, "E1678", {"start": v(-18.73, 8.74) * mm, "end": v(-18.66, 8.66) * mm});
            skLineSegment(sketch, "E1679", {"start": v(-18.66, 8.66) * mm, "end": v(-18.62, 8.6) * mm});
            skLineSegment(sketch, "E1680", {"start": v(-18.62, 8.6) * mm, "end": v(-18.83, 8.7) * mm});
            skLineSegment(sketch, "E1681", {"start": v(-18.83, 8.7) * mm, "end": v(-19.07, 8.85) * mm});
            skLineSegment(sketch, "E1682", {"start": v(-19.07, 8.85) * mm, "end": v(-19.31, 9.01) * mm});
            skLineSegment(sketch, "E1683", {"start": v(-19.31, 9.01) * mm, "end": v(-19.57, 9.19) * mm});
            skLineSegment(sketch, "E1684", {"start": v(-19.57, 9.19) * mm, "end": v(-19.82, 9.37) * mm});
            skLineSegment(sketch, "E1685", {"start": v(-19.82, 9.37) * mm, "end": v(-20.06, 9.55) * mm});
            skLineSegment(sketch, "E1686", {"start": v(-20.06, 9.55) * mm, "end": v(-20.3, 9.72) * mm});
            skLineSegment(sketch, "E1687", {"start": v(-20.3, 9.72) * mm, "end": v(-20.5, 9.88) * mm});
            skLineSegment(sketch, "E1688", {"start": v(-20.5, 9.88) * mm, "end": v(-22.22, 11.33) * mm});
            skLineSegment(sketch, "E1689", {"start": v(-22.22, 11.33) * mm, "end": v(-22.63, 11.72) * mm});
            skLineSegment(sketch, "E1690", {"start": v(-22.63, 11.72) * mm, "end": v(-22.79, 11.85) * mm});
            skLineSegment(sketch, "E1691", {"start": v(-22.79, 11.85) * mm, "end": v(-22.94, 12) * mm});
            skLineSegment(sketch, "E1692", {"start": v(-22.94, 12) * mm, "end": v(-23.08, 12.15) * mm});
            skLineSegment(sketch, "E1693", {"start": v(-23.08, 12.15) * mm, "end": v(-23.23, 12.3) * mm});
            skLineSegment(sketch, "E1694", {"start": v(-23.23, 12.3) * mm, "end": v(-23.5, 12.62) * mm});
            skLineSegment(sketch, "E1695", {"start": v(-23.5, 12.62) * mm, "end": v(-23.78, 12.94) * mm});
            skLineSegment(sketch, "E1696", {"start": v(-23.78, 12.94) * mm, "end": v(-24.15, 13.36) * mm});
            skLineSegment(sketch, "E1697", {"start": v(-24.15, 13.36) * mm, "end": v(-25.18, 14.71) * mm});
            skLineSegment(sketch, "E1698", {"start": v(-25.18, 14.71) * mm, "end": v(-25.16, 14.04) * mm});
            skLineSegment(sketch, "E1699", {"start": v(-25.16, 14.04) * mm, "end": v(-25.05, 13.32) * mm});
            skLineSegment(sketch, "E1700", {"start": v(-25.05, 13.32) * mm, "end": v(-24.86, 12.6) * mm});
            skLineSegment(sketch, "E1701", {"start": v(-24.86, 12.6) * mm, "end": v(-24.6, 11.87) * mm});
            skLineSegment(sketch, "E1702", {"start": v(-24.6, 11.87) * mm, "end": v(-24.28, 11.17) * mm});
            skLineSegment(sketch, "E1703", {"start": v(-24.28, 11.17) * mm, "end": v(-23.92, 10.52) * mm});
            skLineSegment(sketch, "E1704", {"start": v(-23.92, 10.52) * mm, "end": v(-23.52, 9.94) * mm});
            skLineSegment(sketch, "E1705", {"start": v(-23.52, 9.94) * mm, "end": v(-23.1, 9.46) * mm});
            skLineSegment(sketch, "E1706", {"start": v(-23.1, 9.46) * mm, "end": v(-23, 9.35) * mm});
            skLineSegment(sketch, "E1707", {"start": v(-23, 9.35) * mm, "end": v(-22.9, 9.24) * mm});
            skLineSegment(sketch, "E1708", {"start": v(-22.9, 9.24) * mm, "end": v(-22.81, 9.13) * mm});
            skLineSegment(sketch, "E1709", {"start": v(-22.81, 9.13) * mm, "end": v(-22.7, 9.01) * mm});
            skLineSegment(sketch, "E1710", {"start": v(-22.7, 9.01) * mm, "end": v(-22.49, 8.81) * mm});
            skLineSegment(sketch, "E1711", {"start": v(-22.49, 8.81) * mm, "end": v(-22.27, 8.6) * mm});
            skLineSegment(sketch, "E1712", {"start": v(-22.27, 8.6) * mm, "end": v(-22.06, 8.4) * mm});
            skLineSegment(sketch, "E1713", {"start": v(-22.06, 8.4) * mm, "end": v(-21.85, 8.2) * mm});
            skLineSegment(sketch, "E1714", {"start": v(-21.85, 8.2) * mm, "end": v(-21.63, 8) * mm});
            skLineSegment(sketch, "E1715", {"start": v(-21.63, 8) * mm, "end": v(-21.4, 7.81) * mm});
            skLineSegment(sketch, "E1716", {"start": v(-21.4, 7.81) * mm, "end": v(-21.16, 7.63) * mm});
            skLineSegment(sketch, "E1717", {"start": v(-21.16, 7.63) * mm, "end": v(-20.92, 7.46) * mm});
            skLineSegment(sketch, "E1718", {"start": v(-20.92, 7.46) * mm, "end": v(-20.7, 7.31) * mm});
            skLineSegment(sketch, "E1719", {"start": v(-20.7, 7.31) * mm, "end": v(-20.42, 7.1) * mm});
            skLineSegment(sketch, "E1720", {"start": v(-20.42, 7.1) * mm, "end": v(-20.28, 6.99) * mm});
            skLineSegment(sketch, "E1721", {"start": v(-20.28, 6.99) * mm, "end": v(-20.15, 6.9) * mm});
            skLineSegment(sketch, "E1722", {"start": v(-20.15, 6.9) * mm, "end": v(-20.04, 6.83) * mm});
            skLineSegment(sketch, "E1723", {"start": v(-20.04, 6.83) * mm, "end": v(-19.97, 6.8) * mm});
            skLineSegment(sketch, "E1724", {"start": v(-19.97, 6.8) * mm, "end": v(-20.19, 6.87) * mm});
            skLineSegment(sketch, "E1725", {"start": v(-20.19, 6.87) * mm, "end": v(-20.4, 6.96) * mm});
            skLineSegment(sketch, "E1726", {"start": v(-20.4, 6.96) * mm, "end": v(-20.62, 7.05) * mm});
            skLineSegment(sketch, "E1727", {"start": v(-20.62, 7.05) * mm, "end": v(-20.82, 7.1) * mm});
            skLineSegment(sketch, "E1728", {"start": v(-5.98, 2.81) * mm, "end": v(-6.12, 2.83) * mm});
            skLineSegment(sketch, "E1729", {"start": v(-6.12, 2.83) * mm, "end": v(-6.27, 2.86) * mm});
            skLineSegment(sketch, "E1730", {"start": v(-6.27, 2.86) * mm, "end": v(-6.44, 2.9) * mm});
            skLineSegment(sketch, "E1731", {"start": v(-6.44, 2.9) * mm, "end": v(-6.61, 2.94) * mm});
            skLineSegment(sketch, "E1732", {"start": v(-6.61, 2.94) * mm, "end": v(-6.77, 2.98) * mm});
            skLineSegment(sketch, "E1733", {"start": v(-6.77, 2.98) * mm, "end": v(-6.92, 3.02) * mm});
            skLineSegment(sketch, "E1734", {"start": v(-6.92, 3.02) * mm, "end": v(-7.04, 3.04) * mm});
            skLineSegment(sketch, "E1735", {"start": v(-7.04, 3.04) * mm, "end": v(-7.13, 3.05) * mm});
            skLineSegment(sketch, "E1736", {"start": v(-7.13, 3.05) * mm, "end": v(-7.13, 2.9) * mm});
            skLineSegment(sketch, "E1737", {"start": v(-7.13, 2.9) * mm, "end": v(-7.12, 2.75) * mm});
            skLineSegment(sketch, "E1738", {"start": v(-7.12, 2.75) * mm, "end": v(-7.11, 2.62) * mm});
            skLineSegment(sketch, "E1739", {"start": v(-7.11, 2.62) * mm, "end": v(-7.1, 2.5) * mm});
            skLineSegment(sketch, "E1740", {"start": v(-7.1, 2.5) * mm, "end": v(-7.07, 2.39) * mm});
            skLineSegment(sketch, "E1741", {"start": v(-7.07, 2.39) * mm, "end": v(-7.04, 2.27) * mm});
            skLineSegment(sketch, "E1742", {"start": v(-7.04, 2.27) * mm, "end": v(-7, 2.14) * mm});
            skLineSegment(sketch, "E1743", {"start": v(-7, 2.14) * mm, "end": v(-6.95, 2) * mm});
            skLineSegment(sketch, "E1744", {"start": v(-6.95, 2) * mm, "end": v(-6.89, 1.86) * mm});
            skLineSegment(sketch, "E1745", {"start": v(-6.89, 1.86) * mm, "end": v(-6.81, 1.74) * mm});
            skLineSegment(sketch, "E1746", {"start": v(-6.81, 1.74) * mm, "end": v(-6.74, 1.62) * mm});
            skLineSegment(sketch, "E1747", {"start": v(-6.74, 1.62) * mm, "end": v(-6.66, 1.52) * mm});
            skLineSegment(sketch, "E1748", {"start": v(-6.66, 1.52) * mm, "end": v(-6.52, 1.35) * mm});
            skLineSegment(sketch, "E1749", {"start": v(-6.52, 1.35) * mm, "end": v(-6.43, 1.22) * mm});
            skLineSegment(sketch, "E1750", {"start": v(-6.43, 1.22) * mm, "end": v(-6.57, 1.27) * mm});
            skLineSegment(sketch, "E1751", {"start": v(-6.57, 1.27) * mm, "end": v(-6.7, 1.32) * mm});
            skLineSegment(sketch, "E1752", {"start": v(-6.7, 1.32) * mm, "end": v(-6.83, 1.38) * mm});
            skLineSegment(sketch, "E1753", {"start": v(-6.83, 1.38) * mm, "end": v(-6.95, 1.44) * mm});
            skLineSegment(sketch, "E1754", {"start": v(-6.95, 1.44) * mm, "end": v(-7.06, 1.5) * mm});
            skLineSegment(sketch, "E1755", {"start": v(-7.06, 1.5) * mm, "end": v(-7.16, 1.58) * mm});
            skLineSegment(sketch, "E1756", {"start": v(-7.16, 1.58) * mm, "end": v(-7.27, 1.66) * mm});
            skLineSegment(sketch, "E1757", {"start": v(-7.27, 1.66) * mm, "end": v(-7.38, 1.75) * mm});
            skLineSegment(sketch, "E1758", {"start": v(-7.38, 1.75) * mm, "end": v(-7.48, 1.84) * mm});
            skLineSegment(sketch, "E1759", {"start": v(-7.48, 1.84) * mm, "end": v(-7.53, 1.7) * mm});
            skLineSegment(sketch, "E1760", {"start": v(-7.53, 1.7) * mm, "end": v(-7.56, 1.54) * mm});
            skLineSegment(sketch, "E1761", {"start": v(-7.56, 1.54) * mm, "end": v(-7.57, 1.37) * mm});
            skLineSegment(sketch, "E1762", {"start": v(-7.57, 1.37) * mm, "end": v(-7.55, 1.18) * mm});
            skLineSegment(sketch, "E1763", {"start": v(-7.55, 1.18) * mm, "end": v(-7.53, 1) * mm});
            skLineSegment(sketch, "E1764", {"start": v(-7.53, 1) * mm, "end": v(-7.49, 0.83) * mm});
            skLineSegment(sketch, "E1765", {"start": v(-7.49, 0.83) * mm, "end": v(-7.43, 0.68) * mm});
            skLineSegment(sketch, "E1766", {"start": v(-7.43, 0.68) * mm, "end": v(-7.37, 0.54) * mm});
            skLineSegment(sketch, "E1767", {"start": v(-7.37, 0.54) * mm, "end": v(-7.25, 0.32) * mm});
            skLineSegment(sketch, "E1768", {"start": v(-7.25, 0.32) * mm, "end": v(-7.14, 0.16) * mm});
            skLineSegment(sketch, "E1769", {"start": v(-7.14, 0.16) * mm, "end": v(-7.04, 0.04) * mm});
            skLineSegment(sketch, "E1770", {"start": v(-7.04, 0.04) * mm, "end": v(-6.96, -0.05) * mm});
            skLineSegment(sketch, "E1771", {"start": v(-6.96, -0.05) * mm, "end": v(-6.88, -0.12) * mm});
            skLineSegment(sketch, "E1772", {"start": v(-6.88, -0.12) * mm, "end": v(-6.81, -0.2) * mm});
            skLineSegment(sketch, "E1773", {"start": v(-6.81, -0.2) * mm, "end": v(-6.74, -0.27) * mm});
            skLineSegment(sketch, "E1774", {"start": v(-6.74, -0.27) * mm, "end": v(-6.67, -0.37) * mm});
            skLineSegment(sketch, "E1775", {"start": v(-6.67, -0.37) * mm, "end": v(-7.85, 0.01) * mm});
            skLineSegment(sketch, "E1776", {"start": v(-7.85, 0.01) * mm, "end": v(-7.8, -0.2) * mm});
            skLineSegment(sketch, "E1777", {"start": v(-7.8, -0.2) * mm, "end": v(-7.71, -0.42) * mm});
            skLineSegment(sketch, "E1778", {"start": v(-7.71, -0.42) * mm, "end": v(-7.6, -0.63) * mm});
            skLineSegment(sketch, "E1779", {"start": v(-7.6, -0.63) * mm, "end": v(-7.47, -0.83) * mm});
            skLineSegment(sketch, "E1780", {"start": v(-7.47, -0.83) * mm, "end": v(-7.32, -1.03) * mm});
            skLineSegment(sketch, "E1781", {"start": v(-7.32, -1.03) * mm, "end": v(-7.17, -1.21) * mm});
            skLineSegment(sketch, "E1782", {"start": v(-7.17, -1.21) * mm, "end": v(-7.01, -1.38) * mm});
            skLineSegment(sketch, "E1783", {"start": v(-7.01, -1.38) * mm, "end": v(-6.86, -1.53) * mm});
            skLineSegment(sketch, "E1784", {"start": v(-6.86, -1.53) * mm, "end": v(-6.8, -1.59) * mm});
            skLineSegment(sketch, "E1785", {"start": v(-6.8, -1.59) * mm, "end": v(-6.76, -1.63) * mm});
            skLineSegment(sketch, "E1786", {"start": v(-6.76, -1.63) * mm, "end": v(-6.73, -1.67) * mm});
            skLineSegment(sketch, "E1787", {"start": v(-6.73, -1.67) * mm, "end": v(-6.68, -1.74) * mm});
            skLineSegment(sketch, "E1788", {"start": v(-6.68, -1.74) * mm, "end": v(-7.42, -1.59) * mm});
            skLineSegment(sketch, "E1789", {"start": v(-7.42, -1.59) * mm, "end": v(-7.37, -1.8) * mm});
            skLineSegment(sketch, "E1790", {"start": v(-7.37, -1.8) * mm, "end": v(-7.3, -1.98) * mm});
            skLineSegment(sketch, "E1791", {"start": v(-7.3, -1.98) * mm, "end": v(-7.2, -2.16) * mm});
            skLineSegment(sketch, "E1792", {"start": v(-7.2, -2.16) * mm, "end": v(-7.1, -2.33) * mm});
            skLineSegment(sketch, "E1793", {"start": v(-7.1, -2.33) * mm, "end": v(-6.98, -2.5) * mm});
            skLineSegment(sketch, "E1794", {"start": v(-6.98, -2.5) * mm, "end": v(-6.87, -2.65) * mm});
            skLineSegment(sketch, "E1795", {"start": v(-6.87, -2.65) * mm, "end": v(-6.77, -2.8) * mm});
            skLineSegment(sketch, "E1796", {"start": v(-6.77, -2.8) * mm, "end": v(-6.7, -2.95) * mm});
            skLineSegment(sketch, "E1797", {"start": v(-6.7, -2.95) * mm, "end": v(-6.85, -2.85) * mm});
            skLineSegment(sketch, "E1798", {"start": v(-6.85, -2.85) * mm, "end": v(-6.95, -2.75) * mm});
            skLineSegment(sketch, "E1799", {"start": v(-6.95, -2.75) * mm, "end": v(-7.02, -2.65) * mm});
            skLineSegment(sketch, "E1800", {"start": v(-7.02, -2.65) * mm, "end": v(-7.07, -2.57) * mm});
            skLineSegment(sketch, "E1801", {"start": v(-7.07, -2.57) * mm, "end": v(-7.13, -2.5) * mm});
            skLineSegment(sketch, "E1802", {"start": v(-7.13, -2.5) * mm, "end": v(-7.23, -2.45) * mm});
            skLineSegment(sketch, "E1803", {"start": v(-7.23, -2.45) * mm, "end": v(-7.38, -2.42) * mm});
            skLineSegment(sketch, "E1804", {"start": v(-7.38, -2.42) * mm, "end": v(-7.6, -2.4) * mm});
            skLineSegment(sketch, "E1805", {"start": v(-7.6, -2.4) * mm, "end": v(-8.11, -2.4) * mm});
            skLineSegment(sketch, "E1806", {"start": v(-8.11, -2.4) * mm, "end": v(-7.99, -2.6) * mm});
            skLineSegment(sketch, "E1807", {"start": v(-7.99, -2.6) * mm, "end": v(-7.85, -2.75) * mm});
            skLineSegment(sketch, "E1808", {"start": v(-7.85, -2.75) * mm, "end": v(-7.7, -2.88) * mm});
            skLineSegment(sketch, "E1809", {"start": v(-7.7, -2.88) * mm, "end": v(-7.54, -2.99) * mm});
            skLineSegment(sketch, "E1810", {"start": v(-7.54, -2.99) * mm, "end": v(-7.37, -3.08) * mm});
            skLineSegment(sketch, "E1811", {"start": v(-7.37, -3.08) * mm, "end": v(-7.2, -3.19) * mm});
            skLineSegment(sketch, "E1812", {"start": v(-7.2, -3.19) * mm, "end": v(-7, -3.3) * mm});
            skLineSegment(sketch, "E1813", {"start": v(-7, -3.3) * mm, "end": v(-6.8, -3.44) * mm});
            skLineSegment(sketch, "E1814", {"start": v(-6.8, -3.44) * mm, "end": v(-7.1, -3.39) * mm});
            skLineSegment(sketch, "E1815", {"start": v(-7.1, -3.39) * mm, "end": v(-7.37, -3.3) * mm});
            skLineSegment(sketch, "E1816", {"start": v(-7.37, -3.3) * mm, "end": v(-7.64, -3.16) * mm});
            skLineSegment(sketch, "E1817", {"start": v(-7.64, -3.16) * mm, "end": v(-7.88, -3) * mm});
            skLineSegment(sketch, "E1818", {"start": v(-7.88, -3) * mm, "end": v(-8.1, -2.83) * mm});
            skLineSegment(sketch, "E1819", {"start": v(-8.1, -2.83) * mm, "end": v(-8.29, -2.64) * mm});
            skLineSegment(sketch, "E1820", {"start": v(-8.29, -2.64) * mm, "end": v(-8.44, -2.44) * mm});
            skLineSegment(sketch, "E1821", {"start": v(-8.44, -2.44) * mm, "end": v(-8.56, -2.24) * mm});
            skLineSegment(sketch, "E1822", {"start": v(-8.56, -2.24) * mm, "end": v(-7.77, -2.24) * mm});
            skLineSegment(sketch, "E1823", {"start": v(-7.77, -2.24) * mm, "end": v(-7.84, -2.18) * mm});
            skLineSegment(sketch, "E1824", {"start": v(-7.84, -2.18) * mm, "end": v(-7.98, -2.09) * mm});
            skLineSegment(sketch, "E1825", {"start": v(-7.98, -2.09) * mm, "end": v(-8.1, -2.03) * mm});
            skLineSegment(sketch, "E1826", {"start": v(-8.1, -2.03) * mm, "end": v(-8.17, -1.99) * mm});
            skLineSegment(sketch, "E1827", {"start": v(-8.17, -1.99) * mm, "end": v(-8.25, -1.93) * mm});
            skLineSegment(sketch, "E1828", {"start": v(-8.25, -1.93) * mm, "end": v(-8.34, -1.86) * mm});
            skLineSegment(sketch, "E1829", {"start": v(-8.34, -1.86) * mm, "end": v(-8.46, -1.76) * mm});
            skLineSegment(sketch, "E1830", {"start": v(-8.46, -1.76) * mm, "end": v(-8.6, -1.63) * mm});
            skLineSegment(sketch, "E1831", {"start": v(-8.6, -1.63) * mm, "end": v(-8.72, -1.5) * mm});
            skLineSegment(sketch, "E1832", {"start": v(-8.72, -1.5) * mm, "end": v(-8.82, -1.4) * mm});
            skLineSegment(sketch, "E1833", {"start": v(-8.82, -1.4) * mm, "end": v(-8.91, -1.28) * mm});
            skLineSegment(sketch, "E1834", {"start": v(-8.91, -1.28) * mm, "end": v(-9, -1.16) * mm});
            skLineSegment(sketch, "E1835", {"start": v(-9, -1.16) * mm, "end": v(-9.07, -1.03) * mm});
            skLineSegment(sketch, "E1836", {"start": v(-9.07, -1.03) * mm, "end": v(-9.15, -0.89) * mm});
            skLineSegment(sketch, "E1837", {"start": v(-9.15, -0.89) * mm, "end": v(-9.23, -0.73) * mm});
            skLineSegment(sketch, "E1838", {"start": v(-9.23, -0.73) * mm, "end": v(-9.26, -0.67) * mm});
            skLineSegment(sketch, "E1839", {"start": v(-9.26, -0.67) * mm, "end": v(-9.3, -0.62) * mm});
            skLineSegment(sketch, "E1840", {"start": v(-9.3, -0.62) * mm, "end": v(-9.32, -0.59) * mm});
            skLineSegment(sketch, "E1841", {"start": v(-9.32, -0.59) * mm, "end": v(-9.35, -0.56) * mm});
            skLineSegment(sketch, "E1842", {"start": v(-9.35, -0.56) * mm, "end": v(-9.43, -0.52) * mm});
            skLineSegment(sketch, "E1843", {"start": v(-9.43, -0.52) * mm, "end": v(-9.55, -0.47) * mm});
            skLineSegment(sketch, "E1844", {"start": v(-9.55, -0.47) * mm, "end": v(-9.77, -0.37) * mm});
            skLineSegment(sketch, "E1845", {"start": v(-9.77, -0.37) * mm, "end": v(-9.98, -0.27) * mm});
            skLineSegment(sketch, "E1846", {"start": v(-9.98, -0.27) * mm, "end": v(-10.2, -0.18) * mm});
            skLineSegment(sketch, "E1847", {"start": v(-10.2, -0.18) * mm, "end": v(-10.43, -0.09) * mm});
            skLineSegment(sketch, "E1848", {"start": v(-10.43, -0.09) * mm, "end": v(-10.35, -0.48) * mm});
            skLineSegment(sketch, "E1849", {"start": v(-10.35, -0.48) * mm, "end": v(-10.22, -0.81) * mm});
            skLineSegment(sketch, "E1850", {"start": v(-10.22, -0.81) * mm, "end": v(-10.06, -1.1) * mm});
            skLineSegment(sketch, "E1851", {"start": v(-10.06, -1.1) * mm, "end": v(-9.87, -1.35) * mm});
            skLineSegment(sketch, "E1852", {"start": v(-9.87, -1.35) * mm, "end": v(-9.65, -1.57) * mm});
            skLineSegment(sketch, "E1853", {"start": v(-9.65, -1.57) * mm, "end": v(-9.42, -1.78) * mm});
            skLineSegment(sketch, "E1854", {"start": v(-9.42, -1.78) * mm, "end": v(-9.18, -1.98) * mm});
            skLineSegment(sketch, "E1855", {"start": v(-9.18, -1.98) * mm, "end": v(-8.94, -2.19) * mm});
            skLineSegment(sketch, "E1856", {"start": v(-8.94, -2.19) * mm, "end": v(-8.8, -2.33) * mm});
            skLineSegment(sketch, "E1857", {"start": v(-8.8, -2.33) * mm, "end": v(-9.6, -2.21) * mm});
            skLineSegment(sketch, "E1858", {"start": v(-9.6, -2.21) * mm, "end": v(-9.51, -2.41) * mm});
            skLineSegment(sketch, "E1859", {"start": v(-9.51, -2.41) * mm, "end": v(-9.4, -2.6) * mm});
            skLineSegment(sketch, "E1860", {"start": v(-9.4, -2.6) * mm, "end": v(-9.25, -2.8) * mm});
            skLineSegment(sketch, "E1861", {"start": v(-9.25, -2.8) * mm, "end": v(-9.09, -2.97) * mm});
            skLineSegment(sketch, "E1862", {"start": v(-9.09, -2.97) * mm, "end": v(-8.9, -3.13) * mm});
            skLineSegment(sketch, "E1863", {"start": v(-8.9, -3.13) * mm, "end": v(-8.72, -3.28) * mm});
            skLineSegment(sketch, "E1864", {"start": v(-8.72, -3.28) * mm, "end": v(-8.54, -3.41) * mm});
            skLineSegment(sketch, "E1865", {"start": v(-8.54, -3.41) * mm, "end": v(-8.36, -3.53) * mm});
            skLineSegment(sketch, "E1866", {"start": v(-8.36, -3.53) * mm, "end": v(-8.25, -3.6) * mm});
            skLineSegment(sketch, "E1867", {"start": v(-8.25, -3.6) * mm, "end": v(-8.1, -3.69) * mm});
            skLineSegment(sketch, "E1868", {"start": v(-8.1, -3.69) * mm, "end": v(-7.97, -3.77) * mm});
            skLineSegment(sketch, "E1869", {"start": v(-7.97, -3.77) * mm, "end": v(-7.86, -3.86) * mm});
            skLineSegment(sketch, "E1870", {"start": v(-7.86, -3.86) * mm, "end": v(-8, -3.84) * mm});
            skLineSegment(sketch, "E1871", {"start": v(-8, -3.84) * mm, "end": v(-8.13, -3.8) * mm});
            skLineSegment(sketch, "E1872", {"start": v(-8.13, -3.8) * mm, "end": v(-8.26, -3.76) * mm});
            skLineSegment(sketch, "E1873", {"start": v(-8.26, -3.76) * mm, "end": v(-8.39, -3.7) * mm});
            skLineSegment(sketch, "E1874", {"start": v(-8.39, -3.7) * mm, "end": v(-8.63, -3.59) * mm});
            skLineSegment(sketch, "E1875", {"start": v(-8.63, -3.59) * mm, "end": v(-8.84, -3.47) * mm});
            skLineSegment(sketch, "E1876", {"start": v(-8.84, -3.47) * mm, "end": v(-9.06, -3.35) * mm});
            skLineSegment(sketch, "E1877", {"start": v(-9.06, -3.35) * mm, "end": v(-9.24, -3.2) * mm});
            skLineSegment(sketch, "E1878", {"start": v(-9.24, -3.2) * mm, "end": v(-9.38, -3.13) * mm});
            skLineSegment(sketch, "E1879", {"start": v(-9.38, -3.13) * mm, "end": v(-9.57, -3.1) * mm});
            skLineSegment(sketch, "E1880", {"start": v(-9.57, -3.1) * mm, "end": v(-9.8, -3.1) * mm});
            skLineSegment(sketch, "E1881", {"start": v(-9.8, -3.1) * mm, "end": v(-10.1, -3.1) * mm});
            skLineSegment(sketch, "E1882", {"start": v(-10.1, -3.1) * mm, "end": v(-10.48, -3.08) * mm});
            skLineSegment(sketch, "E1883", {"start": v(-10.48, -3.08) * mm, "end": v(-10.93, -3) * mm});
            skLineSegment(sketch, "E1884", {"start": v(-10.93, -3) * mm, "end": v(-11.47, -2.84) * mm});
            skLineSegment(sketch, "E1885", {"start": v(-11.47, -2.84) * mm, "end": v(-12.11, -2.58) * mm});
            skLineSegment(sketch, "E1886", {"start": v(-12.11, -2.58) * mm, "end": v(-12.08, -2.84) * mm});
            skLineSegment(sketch, "E1887", {"start": v(-12.08, -2.84) * mm, "end": v(-12, -3.1) * mm});
            skLineSegment(sketch, "E1888", {"start": v(-12, -3.1) * mm, "end": v(-11.87, -3.31) * mm});
            skLineSegment(sketch, "E1889", {"start": v(-11.87, -3.31) * mm, "end": v(-11.71, -3.51) * mm});
            skLineSegment(sketch, "E1890", {"start": v(-11.71, -3.51) * mm, "end": v(-11.52, -3.69) * mm});
            skLineSegment(sketch, "E1891", {"start": v(-11.52, -3.69) * mm, "end": v(-11.32, -3.84) * mm});
            skLineSegment(sketch, "E1892", {"start": v(-11.32, -3.84) * mm, "end": v(-11.1, -3.96) * mm});
            skLineSegment(sketch, "E1893", {"start": v(-11.1, -3.96) * mm, "end": v(-10.9, -4.06) * mm});
            skLineSegment(sketch, "E1894", {"start": v(-10.9, -4.06) * mm, "end": v(-10.64, -4.16) * mm});
            skLineSegment(sketch, "E1895", {"start": v(-10.64, -4.16) * mm, "end": v(-10.4, -4.25) * mm});
            skLineSegment(sketch, "E1896", {"start": v(-10.4, -4.25) * mm, "end": v(-10.14, -4.33) * mm});
            skLineSegment(sketch, "E1897", {"start": v(-10.14, -4.33) * mm, "end": v(-9.87, -4.42) * mm});
            skLineSegment(sketch, "E1898", {"start": v(-9.87, -4.42) * mm, "end": v(-9.61, -4.48) * mm});
            skLineSegment(sketch, "E1899", {"start": v(-9.61, -4.48) * mm, "end": v(-9.3, -4.54) * mm});
            skLineSegment(sketch, "E1900", {"start": v(-9.3, -4.54) * mm, "end": v(-9.14, -4.57) * mm});
            skLineSegment(sketch, "E1901", {"start": v(-9.14, -4.57) * mm, "end": v(-9, -4.6) * mm});
            skLineSegment(sketch, "E1902", {"start": v(-9, -4.6) * mm, "end": v(-8.87, -4.65) * mm});
            skLineSegment(sketch, "E1903", {"start": v(-8.87, -4.65) * mm, "end": v(-8.77, -4.7) * mm});
            skLineSegment(sketch, "E1904", {"start": v(-8.77, -4.7) * mm, "end": v(-9.28, -4.72) * mm});
            skLineSegment(sketch, "E1905", {"start": v(-9.28, -4.72) * mm, "end": v(-9.75, -4.7) * mm});
            skLineSegment(sketch, "E1906", {"start": v(-9.75, -4.7) * mm, "end": v(-10.18, -4.62) * mm});
            skLineSegment(sketch, "E1907", {"start": v(-10.18, -4.62) * mm, "end": v(-10.56, -4.52) * mm});
            skLineSegment(sketch, "E1908", {"start": v(-10.56, -4.52) * mm, "end": v(-10.88, -4.41) * mm});
            skLineSegment(sketch, "E1909", {"start": v(-10.88, -4.41) * mm, "end": v(-11.14, -4.31) * mm});
            skLineSegment(sketch, "E1910", {"start": v(-11.14, -4.31) * mm, "end": v(-11.32, -4.23) * mm});
            skLineSegment(sketch, "E1911", {"start": v(-11.32, -4.23) * mm, "end": v(-11.44, -4.2) * mm});
            skLineSegment(sketch, "E1912", {"start": v(-11.44, -4.2) * mm, "end": v(-11.46, -4.32) * mm});
            skLineSegment(sketch, "E1913", {"start": v(-11.46, -4.32) * mm, "end": v(-11.49, -4.45) * mm});
            skLineSegment(sketch, "E1914", {"start": v(-11.49, -4.45) * mm, "end": v(-11.5, -4.58) * mm});
            skLineSegment(sketch, "E1915", {"start": v(-11.5, -4.58) * mm, "end": v(-11.52, -4.7) * mm});
            skLineSegment(sketch, "E1916", {"start": v(-11.52, -4.7) * mm, "end": v(-11.52, -4.83) * mm});
            skLineSegment(sketch, "E1917", {"start": v(-11.52, -4.83) * mm, "end": v(-11.52, -4.96) * mm});
            skLineSegment(sketch, "E1918", {"start": v(-11.52, -4.96) * mm, "end": v(-11.5, -5.09) * mm});
            skLineSegment(sketch, "E1919", {"start": v(-11.5, -5.09) * mm, "end": v(-11.46, -5.2) * mm});
            skLineSegment(sketch, "E1920", {"start": v(-11.46, -5.2) * mm, "end": v(-11.28, -5.51) * mm});
            skLineSegment(sketch, "E1921", {"start": v(-11.28, -5.51) * mm, "end": v(-11.02, -5.74) * mm});
            skLineSegment(sketch, "E1922", {"start": v(-11.02, -5.74) * mm, "end": v(-10.7, -5.9) * mm});
            skLineSegment(sketch, "E1923", {"start": v(-10.7, -5.9) * mm, "end": v(-10.33, -6.01) * mm});
            skLineSegment(sketch, "E1924", {"start": v(-10.33, -6.01) * mm, "end": v(-9.94, -6.09) * mm});
            skLineSegment(sketch, "E1925", {"start": v(-9.94, -6.09) * mm, "end": v(-9.55, -6.14) * mm});
            skLineSegment(sketch, "E1926", {"start": v(-9.55, -6.14) * mm, "end": v(-9.17, -6.18) * mm});
            skLineSegment(sketch, "E1927", {"start": v(-9.17, -6.18) * mm, "end": v(-8.84, -6.22) * mm});
            skLineSegment(sketch, "E1928", {"start": v(-8.84, -6.22) * mm, "end": v(-9.1, -6.22) * mm});
            skLineSegment(sketch, "E1929", {"start": v(-9.1, -6.22) * mm, "end": v(-9.29, -6.24) * mm});
            skLineSegment(sketch, "E1930", {"start": v(-9.29, -6.24) * mm, "end": v(-9.44, -6.27) * mm});
            skLineSegment(sketch, "E1931", {"start": v(-9.44, -6.27) * mm, "end": v(-9.6, -6.3) * mm});
            skLineSegment(sketch, "E1932", {"start": v(-9.6, -6.3) * mm, "end": v(-9.78, -6.32) * mm});
            skLineSegment(sketch, "E1933", {"start": v(-9.78, -6.32) * mm, "end": v(-10.06, -6.32) * mm});
            skLineSegment(sketch, "E1934", {"start": v(-10.06, -6.32) * mm, "end": v(-10.47, -6.29) * mm});
            skLineSegment(sketch, "E1935", {"start": v(-10.47, -6.29) * mm, "end": v(-11.04, -6.23) * mm});
            skLineSegment(sketch, "E1936", {"start": v(-11.04, -6.23) * mm, "end": v(-10.93, -6.51) * mm});
            skLineSegment(sketch, "E1937", {"start": v(-10.93, -6.51) * mm, "end": v(-10.78, -6.78) * mm});
            skLineSegment(sketch, "E1938", {"start": v(-10.78, -6.78) * mm, "end": v(-10.6, -7.01) * mm});
            skLineSegment(sketch, "E1939", {"start": v(-10.6, -7.01) * mm, "end": v(-10.37, -7.22) * mm});
            skLineSegment(sketch, "E1940", {"start": v(-10.37, -7.22) * mm, "end": v(-10.13, -7.4) * mm});
            skLineSegment(sketch, "E1941", {"start": v(-10.13, -7.4) * mm, "end": v(-9.85, -7.55) * mm});
            skLineSegment(sketch, "E1942", {"start": v(-9.85, -7.55) * mm, "end": v(-9.55, -7.66) * mm});
            skLineSegment(sketch, "E1943", {"start": v(-9.55, -7.66) * mm, "end": v(-9.23, -7.74) * mm});
            skLineSegment(sketch, "E1944", {"start": v(-9.23, -7.74) * mm, "end": v(-9.04, -7.77) * mm});
            skLineSegment(sketch, "E1945", {"start": v(-9.04, -7.77) * mm, "end": v(-8.85, -7.78) * mm});
            skLineSegment(sketch, "E1946", {"start": v(-8.85, -7.78) * mm, "end": v(-8.64, -7.78) * mm});
            skLineSegment(sketch, "E1947", {"start": v(-8.64, -7.78) * mm, "end": v(-8.44, -7.77) * mm});
            skLineSegment(sketch, "E1948", {"start": v(-8.44, -7.77) * mm, "end": v(-8.24, -7.75) * mm});
            skLineSegment(sketch, "E1949", {"start": v(-8.24, -7.75) * mm, "end": v(-8.04, -7.73) * mm});
            skLineSegment(sketch, "E1950", {"start": v(-8.04, -7.73) * mm, "end": v(-7.86, -7.7) * mm});
            skLineSegment(sketch, "E1951", {"start": v(-7.86, -7.7) * mm, "end": v(-7.69, -7.67) * mm});
            skLineSegment(sketch, "E1952", {"start": v(-7.69, -7.67) * mm, "end": v(-7.02, -7.5) * mm});
            skLineSegment(sketch, "E1953", {"start": v(-7.02, -7.5) * mm, "end": v(-6.87, -7.45) * mm});
            skLineSegment(sketch, "E1954", {"start": v(-6.87, -7.45) * mm, "end": v(-6.7, -7.4) * mm});
            skLineSegment(sketch, "E1955", {"start": v(-6.7, -7.4) * mm, "end": v(-6.55, -7.34) * mm});
            skLineSegment(sketch, "E1956", {"start": v(-6.55, -7.34) * mm, "end": v(-6.43, -7.3) * mm});
            skLineSegment(sketch, "E1957", {"start": v(-6.43, -7.3) * mm, "end": v(-7.18, -7.7) * mm});
            skLineSegment(sketch, "E1958", {"start": v(-7.18, -7.7) * mm, "end": v(-7.44, -7.8) * mm});
            skLineSegment(sketch, "E1959", {"start": v(-7.44, -7.8) * mm, "end": v(-7.7, -7.9) * mm});
            skLineSegment(sketch, "E1960", {"start": v(-7.7, -7.9) * mm, "end": v(-7.94, -7.96) * mm});
            skLineSegment(sketch, "E1961", {"start": v(-7.94, -7.96) * mm, "end": v(-8.18, -8) * mm});
            skLineSegment(sketch, "E1962", {"start": v(-8.18, -8) * mm, "end": v(-8.43, -8.04) * mm});
            skLineSegment(sketch, "E1963", {"start": v(-8.43, -8.04) * mm, "end": v(-8.69, -8.06) * mm});
            skLineSegment(sketch, "E1964", {"start": v(-8.69, -8.06) * mm, "end": v(-8.95, -8.07) * mm});
            skLineSegment(sketch, "E1965", {"start": v(-8.95, -8.07) * mm, "end": v(-9.24, -8.07) * mm});
            skLineSegment(sketch, "E1966", {"start": v(-9.24, -8.07) * mm, "end": v(-9.38, -8.06) * mm});
            skLineSegment(sketch, "E1967", {"start": v(-9.38, -8.06) * mm, "end": v(-9.53, -8.05) * mm});
            skLineSegment(sketch, "E1968", {"start": v(-9.53, -8.05) * mm, "end": v(-9.67, -8.02) * mm});
            skLineSegment(sketch, "E1969", {"start": v(-9.67, -8.02) * mm, "end": v(-9.8, -8) * mm});
            skLineSegment(sketch, "E1970", {"start": v(-9.8, -8) * mm, "end": v(-9.94, -7.97) * mm});
            skLineSegment(sketch, "E1971", {"start": v(-9.94, -7.97) * mm, "end": v(-10.07, -7.95) * mm});
            skLineSegment(sketch, "E1972", {"start": v(-10.07, -7.95) * mm, "end": v(-10.19, -7.93) * mm});
            skLineSegment(sketch, "E1973", {"start": v(-10.19, -7.93) * mm, "end": v(-10.3, -7.92) * mm});
            skLineSegment(sketch, "E1974", {"start": v(-10.3, -7.92) * mm, "end": v(-9.97, -8.48) * mm});
            skLineSegment(sketch, "E1975", {"start": v(-9.97, -8.48) * mm, "end": v(-9.58, -8.87) * mm});
            skLineSegment(sketch, "E1976", {"start": v(-9.58, -8.87) * mm, "end": v(-9.13, -9.13) * mm});
            skLineSegment(sketch, "E1977", {"start": v(-9.13, -9.13) * mm, "end": v(-8.65, -9.27) * mm});
            skLineSegment(sketch, "E1978", {"start": v(-8.65, -9.27) * mm, "end": v(-8.13, -9.3) * mm});
            skLineSegment(sketch, "E1979", {"start": v(-8.13, -9.3) * mm, "end": v(-7.59, -9.24) * mm});
            skLineSegment(sketch, "E1980", {"start": v(-7.59, -9.24) * mm, "end": v(-7.03, -9.1) * mm});
            skLineSegment(sketch, "E1981", {"start": v(-7.03, -9.1) * mm, "end": v(-6.47, -8.93) * mm});
            skLineSegment(sketch, "E1982", {"start": v(-6.47, -8.93) * mm, "end": v(-6.16, -8.82) * mm});
            skLineSegment(sketch, "E1983", {"start": v(-6.16, -8.82) * mm, "end": v(-6.07, -8.78) * mm});
            skLineSegment(sketch, "E1984", {"start": v(-6.07, -8.78) * mm, "end": v(-6, -8.74) * mm});
            skLineSegment(sketch, "E1985", {"start": v(-6, -8.74) * mm, "end": v(-5.94, -8.72) * mm});
            skLineSegment(sketch, "E1986", {"start": v(-5.94, -8.72) * mm, "end": v(-5.85, -8.69) * mm});
            skLineSegment(sketch, "E1987", {"start": v(-5.85, -8.69) * mm, "end": v(-5.95, -8.8) * mm});
            skLineSegment(sketch, "E1988", {"start": v(-5.95, -8.8) * mm, "end": v(-6.1, -8.9) * mm});
            skLineSegment(sketch, "E1989", {"start": v(-6.1, -8.9) * mm, "end": v(-6.26, -9.01) * mm});
            skLineSegment(sketch, "E1990", {"start": v(-6.26, -9.01) * mm, "end": v(-6.45, -9.12) * mm});
            skLineSegment(sketch, "E1991", {"start": v(-6.45, -9.12) * mm, "end": v(-6.64, -9.22) * mm});
            skLineSegment(sketch, "E1992", {"start": v(-6.64, -9.22) * mm, "end": v(-6.82, -9.31) * mm});
            skLineSegment(sketch, "E1993", {"start": v(-6.82, -9.31) * mm, "end": v(-6.98, -9.39) * mm});
            skLineSegment(sketch, "E1994", {"start": v(-6.98, -9.39) * mm, "end": v(-7.1, -9.44) * mm});
            skLineSegment(sketch, "E1995", {"start": v(-7.1, -9.44) * mm, "end": v(-7.3, -9.51) * mm});
            skLineSegment(sketch, "E1996", {"start": v(-7.3, -9.51) * mm, "end": v(-7.52, -9.57) * mm});
            skLineSegment(sketch, "E1997", {"start": v(-7.52, -9.57) * mm, "end": v(-7.73, -9.62) * mm});
            skLineSegment(sketch, "E1998", {"start": v(-7.73, -9.62) * mm, "end": v(-7.96, -9.65) * mm});
            skLineSegment(sketch, "E1999", {"start": v(-7.96, -9.65) * mm, "end": v(-8.19, -9.68) * mm});
            skLineSegment(sketch, "E2000", {"start": v(-8.19, -9.68) * mm, "end": v(-8.42, -9.68) * mm});
            skLineSegment(sketch, "E2001", {"start": v(-8.42, -9.68) * mm, "end": v(-8.65, -9.67) * mm});
            skLineSegment(sketch, "E2002", {"start": v(-8.65, -9.67) * mm, "end": v(-8.88, -9.63) * mm});
            skLineSegment(sketch, "E2003", {"start": v(-8.88, -9.63) * mm, "end": v(-8.85, -9.74) * mm});
            skLineSegment(sketch, "E2004", {"start": v(-8.85, -9.74) * mm, "end": v(-8.8, -9.85) * mm});
            skLineSegment(sketch, "E2005", {"start": v(-8.8, -9.85) * mm, "end": v(-8.74, -9.96) * mm});
            skLineSegment(sketch, "E2006", {"start": v(-8.74, -9.96) * mm, "end": v(-8.67, -10.06) * mm});
            skLineSegment(sketch, "E2007", {"start": v(-8.67, -10.06) * mm, "end": v(-8.59, -10.16) * mm});
            skLineSegment(sketch, "E2008", {"start": v(-8.59, -10.16) * mm, "end": v(-8.5, -10.25) * mm});
            skLineSegment(sketch, "E2009", {"start": v(-8.5, -10.25) * mm, "end": v(-8.42, -10.33) * mm});
            skLineSegment(sketch, "E2010", {"start": v(-8.42, -10.33) * mm, "end": v(-8.35, -10.4) * mm});
            skLineSegment(sketch, "E2011", {"start": v(-8.35, -10.4) * mm, "end": v(-8.25, -10.47) * mm});
            skLineSegment(sketch, "E2012", {"start": v(-8.25, -10.47) * mm, "end": v(-8.14, -10.54) * mm});
            skLineSegment(sketch, "E2013", {"start": v(-8.14, -10.54) * mm, "end": v(-8.02, -10.6) * mm});
            skLineSegment(sketch, "E2014", {"start": v(-8.02, -10.6) * mm, "end": v(-7.9, -10.65) * mm});
            skLineSegment(sketch, "E2015", {"start": v(-7.9, -10.65) * mm, "end": v(-7.77, -10.69) * mm});
            skLineSegment(sketch, "E2016", {"start": v(-7.77, -10.69) * mm, "end": v(-7.63, -10.72) * mm});
            skLineSegment(sketch, "E2017", {"start": v(-7.63, -10.72) * mm, "end": v(-7.48, -10.74) * mm});
            skLineSegment(sketch, "E2018", {"start": v(-7.48, -10.74) * mm, "end": v(-7.32, -10.75) * mm});
            skLineSegment(sketch, "E2019", {"start": v(-7.32, -10.75) * mm, "end": v(-7, -10.74) * mm});
            skLineSegment(sketch, "E2020", {"start": v(-7, -10.74) * mm, "end": v(-6.7, -10.7) * mm});
            skLineSegment(sketch, "E2021", {"start": v(-6.7, -10.7) * mm, "end": v(-6.43, -10.65) * mm});
            skLineSegment(sketch, "E2022", {"start": v(-6.43, -10.65) * mm, "end": v(-6.16, -10.58) * mm});
            skLineSegment(sketch, "E2023", {"start": v(-6.16, -10.58) * mm, "end": v(-5.9, -10.5) * mm});
            skLineSegment(sketch, "E2024", {"start": v(-5.9, -10.5) * mm, "end": v(-5.66, -10.4) * mm});
            skLineSegment(sketch, "E2025", {"start": v(-5.66, -10.4) * mm, "end": v(-5.4, -10.3) * mm});
            skLineSegment(sketch, "E2026", {"start": v(-5.4, -10.3) * mm, "end": v(-5.15, -10.2) * mm});
            skLineSegment(sketch, "E2027", {"start": v(-5.15, -10.2) * mm, "end": v(-5.16, -9.71) * mm});
            skLineSegment(sketch, "E2028", {"start": v(-5.16, -9.71) * mm, "end": v(-5.14, -9.15) * mm});
            skLineSegment(sketch, "E2029", {"start": v(-5.14, -9.15) * mm, "end": v(-5.11, -8.54) * mm});
            skLineSegment(sketch, "E2030", {"start": v(-5.11, -8.54) * mm, "end": v(-5.06, -7.92) * mm});
            skLineSegment(sketch, "E2031", {"start": v(-5.06, -7.92) * mm, "end": v(-4.99, -7.3) * mm});
            skLineSegment(sketch, "E2032", {"start": v(-4.99, -7.3) * mm, "end": v(-4.89, -6.7) * mm});
            skLineSegment(sketch, "E2033", {"start": v(-4.89, -6.7) * mm, "end": v(-4.76, -6.16) * mm});
            skLineSegment(sketch, "E2034", {"start": v(-4.76, -6.16) * mm, "end": v(-4.6, -5.7) * mm});
            skLineSegment(sketch, "E2035", {"start": v(-4.6, -5.7) * mm, "end": v(-4.54, -5.55) * mm});
            skLineSegment(sketch, "E2036", {"start": v(-4.54, -5.55) * mm, "end": v(-4.48, -5.41) * mm});
            skLineSegment(sketch, "E2037", {"start": v(-4.48, -5.41) * mm, "end": v(-4.42, -5.27) * mm});
            skLineSegment(sketch, "E2038", {"start": v(-4.42, -5.27) * mm, "end": v(-4.34, -5.13) * mm});
            skLineSegment(sketch, "E2039", {"start": v(-4.34, -5.13) * mm, "end": v(-4.26, -5) * mm});
            skLineSegment(sketch, "E2040", {"start": v(-4.26, -5) * mm, "end": v(-4.17, -4.85) * mm});
            skLineSegment(sketch, "E2041", {"start": v(-4.17, -4.85) * mm, "end": v(-4.08, -4.7) * mm});
            skLineSegment(sketch, "E2042", {"start": v(-4.08, -4.7) * mm, "end": v(-4.02, -4.57) * mm});
            skLineSegment(sketch, "E2043", {"start": v(-4.02, -4.57) * mm, "end": v(-4.59, -4.1) * mm});
            skLineSegment(sketch, "E2044", {"start": v(-4.59, -4.1) * mm, "end": v(-4.65, -4.04) * mm});
            skLineSegment(sketch, "E2045", {"start": v(-4.65, -4.04) * mm, "end": v(-4.7, -4.02) * mm});
            skLineSegment(sketch, "E2046", {"start": v(-4.7, -4.02) * mm, "end": v(-4.73, -3.99) * mm});
            skLineSegment(sketch, "E2047", {"start": v(-4.73, -3.99) * mm, "end": v(-4.8, -3.92) * mm});
            skLineSegment(sketch, "E2048", {"start": v(-4.8, -3.92) * mm, "end": v(-4.96, -3.74) * mm});
            skLineSegment(sketch, "E2049", {"start": v(-4.96, -3.74) * mm, "end": v(-5.1, -3.56) * mm});
            skLineSegment(sketch, "E2050", {"start": v(-5.1, -3.56) * mm, "end": v(-5.26, -3.36) * mm});
            skLineSegment(sketch, "E2051", {"start": v(-5.26, -3.36) * mm, "end": v(-5.42, -3.13) * mm});
            skLineSegment(sketch, "E2052", {"start": v(-5.42, -3.13) * mm, "end": v(-5.66, -2.6) * mm});
            skLineSegment(sketch, "E2053", {"start": v(-5.66, -2.6) * mm, "end": v(-5.78, -2.06) * mm});
            skLineSegment(sketch, "E2054", {"start": v(-5.78, -2.06) * mm, "end": v(-5.78, -1.5) * mm});
            skLineSegment(sketch, "E2055", {"start": v(-5.78, -1.5) * mm, "end": v(-5.68, -0.94) * mm});
            skLineSegment(sketch, "E2056", {"start": v(-5.68, -0.94) * mm, "end": v(-5.5, -0.4) * mm});
            skLineSegment(sketch, "E2057", {"start": v(-5.5, -0.4) * mm, "end": v(-5.25, 0.12) * mm});
            skLineSegment(sketch, "E2058", {"start": v(-5.25, 0.12) * mm, "end": v(-4.95, 0.6) * mm});
            skLineSegment(sketch, "E2059", {"start": v(-4.95, 0.6) * mm, "end": v(-4.62, 1.03) * mm});
            skLineSegment(sketch, "E2060", {"start": v(-4.62, 1.03) * mm, "end": v(-4.55, 1.14) * mm});
            skLineSegment(sketch, "E2061", {"start": v(-4.55, 1.14) * mm, "end": v(-4.48, 1.25) * mm});
            skLineSegment(sketch, "E2062", {"start": v(-4.48, 1.25) * mm, "end": v(-4.42, 1.38) * mm});
            skLineSegment(sketch, "E2063", {"start": v(-4.42, 1.38) * mm, "end": v(-4.38, 1.52) * mm});
            skLineSegment(sketch, "E2064", {"start": v(-4.38, 1.52) * mm, "end": v(-4.33, 1.65) * mm});
            skLineSegment(sketch, "E2065", {"start": v(-4.33, 1.65) * mm, "end": v(-4.3, 1.8) * mm});
            skLineSegment(sketch, "E2066", {"start": v(-4.3, 1.8) * mm, "end": v(-4.27, 1.93) * mm});
            skLineSegment(sketch, "E2067", {"start": v(-4.27, 1.93) * mm, "end": v(-4.25, 2.07) * mm});
            skLineSegment(sketch, "E2068", {"start": v(-4.25, 2.07) * mm, "end": v(-4.22, 2.37) * mm});
            skLineSegment(sketch, "E2069", {"start": v(-4.22, 2.37) * mm, "end": v(-4.25, 2.66) * mm});
            skLineSegment(sketch, "E2070", {"start": v(-4.25, 2.66) * mm, "end": v(-4.32, 2.93) * mm});
            skLineSegment(sketch, "E2071", {"start": v(-4.32, 2.93) * mm, "end": v(-4.43, 3.18) * mm});
            skLineSegment(sketch, "E2072", {"start": v(-4.43, 3.18) * mm, "end": v(-4.57, 3.42) * mm});
            skLineSegment(sketch, "E2073", {"start": v(-4.57, 3.42) * mm, "end": v(-4.74, 3.63) * mm});
            skLineSegment(sketch, "E2074", {"start": v(-4.74, 3.63) * mm, "end": v(-4.94, 3.83) * mm});
            skLineSegment(sketch, "E2075", {"start": v(-4.94, 3.83) * mm, "end": v(-5.15, 4.02) * mm});
            skLineSegment(sketch, "E2076", {"start": v(-5.15, 4.02) * mm, "end": v(-7.84, 5.62) * mm});
            skLineSegment(sketch, "E2077", {"start": v(-7.84, 5.62) * mm, "end": v(-8.27, 5.9) * mm});
            skLineSegment(sketch, "E2078", {"start": v(-8.27, 5.9) * mm, "end": v(-8.51, 6.07) * mm});
            skLineSegment(sketch, "E2079", {"start": v(-8.51, 6.07) * mm, "end": v(-8.77, 6.25) * mm});
            skLineSegment(sketch, "E2080", {"start": v(-8.77, 6.25) * mm, "end": v(-9.04, 6.44) * mm});
            skLineSegment(sketch, "E2081", {"start": v(-9.04, 6.44) * mm, "end": v(-9.3, 6.64) * mm});
            skLineSegment(sketch, "E2082", {"start": v(-9.3, 6.64) * mm, "end": v(-9.57, 6.84) * mm});
            skLineSegment(sketch, "E2083", {"start": v(-9.57, 6.84) * mm, "end": v(-9.83, 7.04) * mm});
            skLineSegment(sketch, "E2084", {"start": v(-9.83, 7.04) * mm, "end": v(-10.07, 7.25) * mm});
            skLineSegment(sketch, "E2085", {"start": v(-10.07, 7.25) * mm, "end": v(-10.3, 7.46) * mm});
            skLineSegment(sketch, "E2086", {"start": v(-10.3, 7.46) * mm, "end": v(-10.47, 7.64) * mm});
            skLineSegment(sketch, "E2087", {"start": v(-10.47, 7.64) * mm, "end": v(-10.66, 7.84) * mm});
            skLineSegment(sketch, "E2088", {"start": v(-10.66, 7.84) * mm, "end": v(-10.85, 8.03) * mm});
            skLineSegment(sketch, "E2089", {"start": v(-10.85, 8.03) * mm, "end": v(-11.03, 8.18) * mm});
            skLineSegment(sketch, "E2090", {"start": v(-11.03, 8.18) * mm, "end": v(-11.02, 7.81) * mm});
            skLineSegment(sketch, "E2091", {"start": v(-11.02, 7.81) * mm, "end": v(-10.95, 7.44) * mm});
            skLineSegment(sketch, "E2092", {"start": v(-10.95, 7.44) * mm, "end": v(-10.84, 7.07) * mm});
            skLineSegment(sketch, "E2093", {"start": v(-10.84, 7.07) * mm, "end": v(-10.7, 6.7) * mm});
            skLineSegment(sketch, "E2094", {"start": v(-10.7, 6.7) * mm, "end": v(-10.51, 6.35) * mm});
            skLineSegment(sketch, "E2095", {"start": v(-10.51, 6.35) * mm, "end": v(-10.31, 6.02) * mm});
            skLineSegment(sketch, "E2096", {"start": v(-10.31, 6.02) * mm, "end": v(-10.1, 5.72) * mm});
            skLineSegment(sketch, "E2097", {"start": v(-10.1, 5.72) * mm, "end": v(-9.88, 5.46) * mm});
            skLineSegment(sketch, "E2098", {"start": v(-9.88, 5.46) * mm, "end": v(-9.7, 5.26) * mm});
            skLineSegment(sketch, "E2099", {"start": v(-9.7, 5.26) * mm, "end": v(-9.53, 5.1) * mm});
            skLineSegment(sketch, "E2100", {"start": v(-9.53, 5.1) * mm, "end": v(-9.37, 4.96) * mm});
            skLineSegment(sketch, "E2101", {"start": v(-9.37, 4.96) * mm, "end": v(-9.2, 4.8) * mm});
            skLineSegment(sketch, "E2102", {"start": v(-9.2, 4.8) * mm, "end": v(-9, 4.63) * mm});
            skLineSegment(sketch, "E2103", {"start": v(-9, 4.63) * mm, "end": v(-8.73, 4.43) * mm});
            skLineSegment(sketch, "E2104", {"start": v(-8.73, 4.43) * mm, "end": v(-8.42, 4.21) * mm});
            skLineSegment(sketch, "E2105", {"start": v(-8.42, 4.21) * mm, "end": v(-8.08, 3.99) * mm});
            skLineSegment(sketch, "E2106", {"start": v(-8.08, 3.99) * mm, "end": v(-7.73, 3.77) * mm});
            skLineSegment(sketch, "E2107", {"start": v(-7.73, 3.77) * mm, "end": v(-7.4, 3.57) * mm});
            skLineSegment(sketch, "E2108", {"start": v(-7.4, 3.57) * mm, "end": v(-7.1, 3.4) * mm});
            skLineSegment(sketch, "E2109", {"start": v(-7.1, 3.4) * mm, "end": v(-6.86, 3.27) * mm});
            skLineSegment(sketch, "E2110", {"start": v(-6.86, 3.27) * mm, "end": v(-6.65, 3.17) * mm});
            skLineSegment(sketch, "E2111", {"start": v(-6.65, 3.17) * mm, "end": v(-6.4, 3.04) * mm});
            skLineSegment(sketch, "E2112", {"start": v(-6.4, 3.04) * mm, "end": v(-6.16, 2.92) * mm});
            skLineSegment(sketch, "E2113", {"start": v(-6.16, 2.92) * mm, "end": v(-5.98, 2.81) * mm});
            skLineSegment(sketch, "E2114", {"start": v(15.77, 7.42) * mm, "end": v(16.02, 7.6) * mm});
            skLineSegment(sketch, "E2115", {"start": v(16.02, 7.6) * mm, "end": v(16.27, 7.81) * mm});
            skLineSegment(sketch, "E2116", {"start": v(16.27, 7.81) * mm, "end": v(16.6, 8.1) * mm});
            skLineSegment(sketch, "E2117", {"start": v(16.6, 8.1) * mm, "end": v(17.04, 8.48) * mm});
            skLineSegment(sketch, "E2118", {"start": v(17.04, 8.48) * mm, "end": v(17.26, 8.66) * mm});
            skLineSegment(sketch, "E2119", {"start": v(17.26, 8.66) * mm, "end": v(17.47, 8.82) * mm});
            skLineSegment(sketch, "E2120", {"start": v(17.47, 8.82) * mm, "end": v(17.63, 8.94) * mm});
            skLineSegment(sketch, "E2121", {"start": v(17.63, 8.94) * mm, "end": v(17.74, 9) * mm});
            skLineSegment(sketch, "E2122", {"start": v(17.74, 9) * mm, "end": v(17.7, 8.8) * mm});
            skLineSegment(sketch, "E2123", {"start": v(17.7, 8.8) * mm, "end": v(17.65, 8.57) * mm});
            skLineSegment(sketch, "E2124", {"start": v(17.65, 8.57) * mm, "end": v(17.58, 8.35) * mm});
            skLineSegment(sketch, "E2125", {"start": v(17.58, 8.35) * mm, "end": v(17.5, 8.12) * mm});
            skLineSegment(sketch, "E2126", {"start": v(17.5, 8.12) * mm, "end": v(17.4, 7.9) * mm});
            skLineSegment(sketch, "E2127", {"start": v(17.4, 7.9) * mm, "end": v(17.32, 7.68) * mm});
            skLineSegment(sketch, "E2128", {"start": v(17.32, 7.68) * mm, "end": v(17.24, 7.48) * mm});
            skLineSegment(sketch, "E2129", {"start": v(17.24, 7.48) * mm, "end": v(17.16, 7.3) * mm});
            skLineSegment(sketch, "E2130", {"start": v(17.16, 7.3) * mm, "end": v(17.09, 7.12) * mm});
            skLineSegment(sketch, "E2131", {"start": v(17.09, 7.12) * mm, "end": v(16.99, 6.92) * mm});
            skLineSegment(sketch, "E2132", {"start": v(16.99, 6.92) * mm, "end": v(16.86, 6.69) * mm});
            skLineSegment(sketch, "E2133", {"start": v(16.86, 6.69) * mm, "end": v(16.73, 6.46) * mm});
            skLineSegment(sketch, "E2134", {"start": v(16.73, 6.46) * mm, "end": v(16.59, 6.23) * mm});
            skLineSegment(sketch, "E2135", {"start": v(16.59, 6.23) * mm, "end": v(16.45, 6.02) * mm});
            skLineSegment(sketch, "E2136", {"start": v(16.45, 6.02) * mm, "end": v(16.33, 5.84) * mm});
            skLineSegment(sketch, "E2137", {"start": v(16.33, 5.84) * mm, "end": v(16.22, 5.7) * mm});
            skLineSegment(sketch, "E2138", {"start": v(16.22, 5.7) * mm, "end": v(16.09, 5.54) * mm});
            skLineSegment(sketch, "E2139", {"start": v(16.09, 5.54) * mm, "end": v(15.82, 5.21) * mm});
            skLineSegment(sketch, "E2140", {"start": v(15.82, 5.21) * mm, "end": v(15.54, 4.93) * mm});
            skLineSegment(sketch, "E2141", {"start": v(15.54, 4.93) * mm, "end": v(15.27, 4.68) * mm});
            skLineSegment(sketch, "E2142", {"start": v(15.27, 4.68) * mm, "end": v(15, 4.45) * mm});
            skLineSegment(sketch, "E2143", {"start": v(15, 4.45) * mm, "end": v(14.72, 4.24) * mm});
            skLineSegment(sketch, "E2144", {"start": v(14.72, 4.24) * mm, "end": v(14.45, 4.05) * mm});
            skLineSegment(sketch, "E2145", {"start": v(14.45, 4.05) * mm, "end": v(14.2, 3.85) * mm});
            skLineSegment(sketch, "E2146", {"start": v(14.2, 3.85) * mm, "end": v(13.94, 3.64) * mm});
            skLineSegment(sketch, "E2147", {"start": v(13.94, 3.64) * mm, "end": v(14.06, 3.69) * mm});
            skLineSegment(sketch, "E2148", {"start": v(14.06, 3.69) * mm, "end": v(14.24, 3.77) * mm});
            skLineSegment(sketch, "E2149", {"start": v(14.24, 3.77) * mm, "end": v(14.46, 3.89) * mm});
            skLineSegment(sketch, "E2150", {"start": v(14.46, 3.89) * mm, "end": v(14.7, 4.02) * mm});
            skLineSegment(sketch, "E2151", {"start": v(14.7, 4.02) * mm, "end": v(14.93, 4.16) * mm});
            skLineSegment(sketch, "E2152", {"start": v(14.93, 4.16) * mm, "end": v(15.15, 4.28) * mm});
            skLineSegment(sketch, "E2153", {"start": v(15.15, 4.28) * mm, "end": v(15.33, 4.4) * mm});
            skLineSegment(sketch, "E2154", {"start": v(15.33, 4.4) * mm, "end": v(15.45, 4.47) * mm});
            skLineSegment(sketch, "E2155", {"start": v(15.45, 4.47) * mm, "end": v(16.17, 4.91) * mm});
            skLineSegment(sketch, "E2156", {"start": v(16.17, 4.91) * mm, "end": v(16.37, 5.02) * mm});
            skLineSegment(sketch, "E2157", {"start": v(16.37, 5.02) * mm, "end": v(16.56, 5.14) * mm});
            skLineSegment(sketch, "E2158", {"start": v(16.56, 5.14) * mm, "end": v(16.74, 5.25) * mm});
            skLineSegment(sketch, "E2159", {"start": v(16.74, 5.25) * mm, "end": v(16.94, 5.37) * mm});
            skLineSegment(sketch, "E2160", {"start": v(16.94, 5.37) * mm, "end": v(16.86, 5.08) * mm});
            skLineSegment(sketch, "E2161", {"start": v(16.86, 5.08) * mm, "end": v(16.76, 4.8) * mm});
            skLineSegment(sketch, "E2162", {"start": v(16.76, 4.8) * mm, "end": v(16.64, 4.53) * mm});
            skLineSegment(sketch, "E2163", {"start": v(16.64, 4.53) * mm, "end": v(16.53, 4.27) * mm});
            skLineSegment(sketch, "E2164", {"start": v(16.53, 4.27) * mm, "end": v(16.46, 4.13) * mm});
            skLineSegment(sketch, "E2165", {"start": v(16.46, 4.13) * mm, "end": v(16.4, 4) * mm});
            skLineSegment(sketch, "E2166", {"start": v(16.4, 4) * mm, "end": v(16.32, 3.88) * mm});
            skLineSegment(sketch, "E2167", {"start": v(16.32, 3.88) * mm, "end": v(16.25, 3.76) * mm});
            skLineSegment(sketch, "E2168", {"start": v(16.25, 3.76) * mm, "end": v(16.1, 3.52) * mm});
            skLineSegment(sketch, "E2169", {"start": v(16.1, 3.52) * mm, "end": v(15.98, 3.3) * mm});
            skLineSegment(sketch, "E2170", {"start": v(15.98, 3.3) * mm, "end": v(16.44, 3.34) * mm});
            skLineSegment(sketch, "E2171", {"start": v(16.44, 3.34) * mm, "end": v(16.92, 3.4) * mm});
            skLineSegment(sketch, "E2172", {"start": v(16.92, 3.4) * mm, "end": v(17.4, 3.47) * mm});
            skLineSegment(sketch, "E2173", {"start": v(17.4, 3.47) * mm, "end": v(17.88, 3.56) * mm});
            skLineSegment(sketch, "E2174", {"start": v(17.88, 3.56) * mm, "end": v(18.34, 3.66) * mm});
            skLineSegment(sketch, "E2175", {"start": v(18.34, 3.66) * mm, "end": v(18.8, 3.78) * mm});
            skLineSegment(sketch, "E2176", {"start": v(18.8, 3.78) * mm, "end": v(19.22, 3.92) * mm});
            skLineSegment(sketch, "E2177", {"start": v(19.22, 3.92) * mm, "end": v(19.6, 4.07) * mm});
            skLineSegment(sketch, "E2178", {"start": v(19.6, 4.07) * mm, "end": v(19.97, 4.22) * mm});
            skLineSegment(sketch, "E2179", {"start": v(19.97, 4.22) * mm, "end": v(20.34, 4.4) * mm});
            skLineSegment(sketch, "E2180", {"start": v(20.34, 4.4) * mm, "end": v(20.7, 4.6) * mm});
            skLineSegment(sketch, "E2181", {"start": v(20.7, 4.6) * mm, "end": v(21.02, 4.83) * mm});
            skLineSegment(sketch, "E2182", {"start": v(21.02, 4.83) * mm, "end": v(21.32, 5.1) * mm});
            skLineSegment(sketch, "E2183", {"start": v(21.32, 5.1) * mm, "end": v(21.57, 5.4) * mm});
            skLineSegment(sketch, "E2184", {"start": v(21.57, 5.4) * mm, "end": v(21.76, 5.75) * mm});
            skLineSegment(sketch, "E2185", {"start": v(21.76, 5.75) * mm, "end": v(21.88, 6.15) * mm});
            skLineSegment(sketch, "E2186", {"start": v(21.88, 6.15) * mm, "end": v(21.7, 6.03) * mm});
            skLineSegment(sketch, "E2187", {"start": v(21.7, 6.03) * mm, "end": v(21.32, 5.78) * mm});
            skLineSegment(sketch, "E2188", {"start": v(21.32, 5.78) * mm, "end": v(21.1, 5.64) * mm});
            skLineSegment(sketch, "E2189", {"start": v(21.1, 5.64) * mm, "end": v(20.86, 5.49) * mm});
            skLineSegment(sketch, "E2190", {"start": v(20.86, 5.49) * mm, "end": v(20.63, 5.36) * mm});
            skLineSegment(sketch, "E2191", {"start": v(20.63, 5.36) * mm, "end": v(20.42, 5.25) * mm});
            skLineSegment(sketch, "E2192", {"start": v(20.42, 5.25) * mm, "end": v(20.1, 5.09) * mm});
            skLineSegment(sketch, "E2193", {"start": v(20.1, 5.09) * mm, "end": v(19.74, 4.93) * mm});
            skLineSegment(sketch, "E2194", {"start": v(19.74, 4.93) * mm, "end": v(19.38, 4.77) * mm});
            skLineSegment(sketch, "E2195", {"start": v(19.38, 4.77) * mm, "end": v(19, 4.63) * mm});
            skLineSegment(sketch, "E2196", {"start": v(19, 4.63) * mm, "end": v(18.62, 4.51) * mm});
            skLineSegment(sketch, "E2197", {"start": v(18.62, 4.51) * mm, "end": v(18.23, 4.42) * mm});
            skLineSegment(sketch, "E2198", {"start": v(18.23, 4.42) * mm, "end": v(17.84, 4.35) * mm});
            skLineSegment(sketch, "E2199", {"start": v(17.84, 4.35) * mm, "end": v(17.45, 4.33) * mm});
            skLineSegment(sketch, "E2200", {"start": v(17.45, 4.33) * mm, "end": v(17.61, 4.36) * mm});
            skLineSegment(sketch, "E2201", {"start": v(17.61, 4.36) * mm, "end": v(17.81, 4.42) * mm});
            skLineSegment(sketch, "E2202", {"start": v(17.81, 4.42) * mm, "end": v(18.03, 4.5) * mm});
            skLineSegment(sketch, "E2203", {"start": v(18.03, 4.5) * mm, "end": v(18.26, 4.57) * mm});
            skLineSegment(sketch, "E2204", {"start": v(18.26, 4.57) * mm, "end": v(18.5, 4.65) * mm});
            skLineSegment(sketch, "E2205", {"start": v(18.5, 4.65) * mm, "end": v(18.71, 4.74) * mm});
            skLineSegment(sketch, "E2206", {"start": v(18.71, 4.74) * mm, "end": v(18.92, 4.81) * mm});
            skLineSegment(sketch, "E2207", {"start": v(18.92, 4.81) * mm, "end": v(19.08, 4.88) * mm});
            skLineSegment(sketch, "E2208", {"start": v(19.08, 4.88) * mm, "end": v(19.38, 5) * mm});
            skLineSegment(sketch, "E2209", {"start": v(19.38, 5) * mm, "end": v(19.67, 5.12) * mm});
            skLineSegment(sketch, "E2210", {"start": v(19.67, 5.12) * mm, "end": v(19.94, 5.24) * mm});
            skLineSegment(sketch, "E2211", {"start": v(19.94, 5.24) * mm, "end": v(20.21, 5.38) * mm});
            skLineSegment(sketch, "E2212", {"start": v(20.21, 5.38) * mm, "end": v(20.47, 5.52) * mm});
            skLineSegment(sketch, "E2213", {"start": v(20.47, 5.52) * mm, "end": v(20.73, 5.68) * mm});
            skLineSegment(sketch, "E2214", {"start": v(20.73, 5.68) * mm, "end": v(20.98, 5.84) * mm});
            skLineSegment(sketch, "E2215", {"start": v(20.98, 5.84) * mm, "end": v(21.23, 6.03) * mm});
            skLineSegment(sketch, "E2216", {"start": v(21.23, 6.03) * mm, "end": v(21.46, 6.2) * mm});
            skLineSegment(sketch, "E2217", {"start": v(21.46, 6.2) * mm, "end": v(21.57, 6.31) * mm});
            skLineSegment(sketch, "E2218", {"start": v(21.57, 6.31) * mm, "end": v(21.66, 6.4) * mm});
            skLineSegment(sketch, "E2219", {"start": v(21.66, 6.4) * mm, "end": v(21.81, 6.57) * mm});
            skLineSegment(sketch, "E2220", {"start": v(21.81, 6.57) * mm, "end": v(22.09, 6.82) * mm});
            skLineSegment(sketch, "E2221", {"start": v(22.09, 6.82) * mm, "end": v(22.42, 7.14) * mm});
            skLineSegment(sketch, "E2222", {"start": v(22.42, 7.14) * mm, "end": v(22.58, 7.3) * mm});
            skLineSegment(sketch, "E2223", {"start": v(22.58, 7.3) * mm, "end": v(22.71, 7.47) * mm});
            skLineSegment(sketch, "E2224", {"start": v(22.71, 7.47) * mm, "end": v(22.82, 7.62) * mm});
            skLineSegment(sketch, "E2225", {"start": v(22.82, 7.62) * mm, "end": v(22.88, 7.76) * mm});
            skLineSegment(sketch, "E2226", {"start": v(22.88, 7.76) * mm, "end": v(21.63, 7.05) * mm});
            skLineSegment(sketch, "E2227", {"start": v(21.63, 7.05) * mm, "end": v(21.2, 6.83) * mm});
            skLineSegment(sketch, "E2228", {"start": v(21.2, 6.83) * mm, "end": v(20.66, 6.6) * mm});
            skLineSegment(sketch, "E2229", {"start": v(20.66, 6.6) * mm, "end": v(20.05, 6.34) * mm});
            skLineSegment(sketch, "E2230", {"start": v(20.05, 6.34) * mm, "end": v(19.4, 6.1) * mm});
            skLineSegment(sketch, "E2231", {"start": v(19.4, 6.1) * mm, "end": v(18.76, 5.88) * mm});
            skLineSegment(sketch, "E2232", {"start": v(18.76, 5.88) * mm, "end": v(18.15, 5.7) * mm});
            skLineSegment(sketch, "E2233", {"start": v(18.15, 5.7) * mm, "end": v(17.62, 5.58) * mm});
            skLineSegment(sketch, "E2234", {"start": v(17.62, 5.58) * mm, "end": v(17.2, 5.54) * mm});
            skLineSegment(sketch, "E2235", {"start": v(17.2, 5.54) * mm, "end": v(18.4, 6.22) * mm});
            skLineSegment(sketch, "E2236", {"start": v(18.4, 6.22) * mm, "end": v(18.67, 6.38) * mm});
            skLineSegment(sketch, "E2237", {"start": v(18.67, 6.38) * mm, "end": v(18.96, 6.56) * mm});
            skLineSegment(sketch, "E2238", {"start": v(18.96, 6.56) * mm, "end": v(19.28, 6.76) * mm});
            skLineSegment(sketch, "E2239", {"start": v(19.28, 6.76) * mm, "end": v(19.6, 6.97) * mm});
            skLineSegment(sketch, "E2240", {"start": v(19.6, 6.97) * mm, "end": v(19.91, 7.18) * mm});
            skLineSegment(sketch, "E2241", {"start": v(19.91, 7.18) * mm, "end": v(20.2, 7.39) * mm});
            skLineSegment(sketch, "E2242", {"start": v(20.2, 7.39) * mm, "end": v(20.47, 7.59) * mm});
            skLineSegment(sketch, "E2243", {"start": v(20.47, 7.59) * mm, "end": v(20.7, 7.77) * mm});
            skLineSegment(sketch, "E2244", {"start": v(20.7, 7.77) * mm, "end": v(20.99, 8.03) * mm});
            skLineSegment(sketch, "E2245", {"start": v(20.99, 8.03) * mm, "end": v(21.27, 8.26) * mm});
            skLineSegment(sketch, "E2246", {"start": v(21.27, 8.26) * mm, "end": v(21.54, 8.5) * mm});
            skLineSegment(sketch, "E2247", {"start": v(21.54, 8.5) * mm, "end": v(21.8, 8.72) * mm});
            skLineSegment(sketch, "E2248", {"start": v(21.8, 8.72) * mm, "end": v(22.07, 8.97) * mm});
            skLineSegment(sketch, "E2249", {"start": v(22.07, 8.97) * mm, "end": v(22.34, 9.24) * mm});
            skLineSegment(sketch, "E2250", {"start": v(22.34, 9.24) * mm, "end": v(22.61, 9.55) * mm});
            skLineSegment(sketch, "E2251", {"start": v(22.61, 9.55) * mm, "end": v(22.9, 9.9) * mm});
            skLineSegment(sketch, "E2252", {"start": v(22.9, 9.9) * mm, "end": v(23.52, 10.74) * mm});
            skLineSegment(sketch, "E2253", {"start": v(23.52, 10.74) * mm, "end": v(23.68, 10.99) * mm});
            skLineSegment(sketch, "E2254", {"start": v(23.68, 10.99) * mm, "end": v(23.85, 11.29) * mm});
            skLineSegment(sketch, "E2255", {"start": v(23.85, 11.29) * mm, "end": v(24.03, 11.62) * mm});
            skLineSegment(sketch, "E2256", {"start": v(24.03, 11.62) * mm, "end": v(24.21, 11.99) * mm});
            skLineSegment(sketch, "E2257", {"start": v(24.21, 11.99) * mm, "end": v(24.38, 12.37) * mm});
            skLineSegment(sketch, "E2258", {"start": v(24.38, 12.37) * mm, "end": v(24.52, 12.74) * mm});
            skLineSegment(sketch, "E2259", {"start": v(24.52, 12.74) * mm, "end": v(24.63, 13.1) * mm});
            skLineSegment(sketch, "E2260", {"start": v(24.63, 13.1) * mm, "end": v(24.7, 13.45) * mm});
            skLineSegment(sketch, "E2261", {"start": v(24.7, 13.45) * mm, "end": v(23.97, 12.62) * mm});
            skLineSegment(sketch, "E2262", {"start": v(23.97, 12.62) * mm, "end": v(23.6, 12.2) * mm});
            skLineSegment(sketch, "E2263", {"start": v(23.6, 12.2) * mm, "end": v(23.22, 11.79) * mm});
            skLineSegment(sketch, "E2264", {"start": v(23.22, 11.79) * mm, "end": v(22.84, 11.42) * mm});
            skLineSegment(sketch, "E2265", {"start": v(22.84, 11.42) * mm, "end": v(22.37, 10.96) * mm});
            skLineSegment(sketch, "E2266", {"start": v(22.37, 10.96) * mm, "end": v(21.9, 10.53) * mm});
            skLineSegment(sketch, "E2267", {"start": v(21.9, 10.53) * mm, "end": v(21.44, 10.12) * mm});
            skLineSegment(sketch, "E2268", {"start": v(21.44, 10.12) * mm, "end": v(20.96, 9.74) * mm});
            skLineSegment(sketch, "E2269", {"start": v(20.96, 9.74) * mm, "end": v(20.47, 9.38) * mm});
            skLineSegment(sketch, "E2270", {"start": v(20.47, 9.38) * mm, "end": v(19.95, 9.04) * mm});
            skLineSegment(sketch, "E2271", {"start": v(19.95, 9.04) * mm, "end": v(19.39, 8.7) * mm});
            skLineSegment(sketch, "E2272", {"start": v(19.39, 8.7) * mm, "end": v(18.79, 8.38) * mm});
            skLineSegment(sketch, "E2273", {"start": v(18.79, 8.38) * mm, "end": v(18.55, 8.26) * mm});
            skLineSegment(sketch, "E2274", {"start": v(18.55, 8.26) * mm, "end": v(18.24, 8.11) * mm});
            skLineSegment(sketch, "E2275", {"start": v(18.24, 8.11) * mm, "end": v(18.08, 8.04) * mm});
            skLineSegment(sketch, "E2276", {"start": v(18.08, 8.04) * mm, "end": v(17.93, 7.98) * mm});
            skLineSegment(sketch, "E2277", {"start": v(17.93, 7.98) * mm, "end": v(17.8, 7.93) * mm});
            skLineSegment(sketch, "E2278", {"start": v(17.8, 7.93) * mm, "end": v(17.7, 7.9) * mm});
            skLineSegment(sketch, "E2279", {"start": v(17.7, 7.9) * mm, "end": v(20.11, 10.48) * mm});
            skLineSegment(sketch, "E2280", {"start": v(20.11, 10.48) * mm, "end": v(20.62, 11.08) * mm});
            skLineSegment(sketch, "E2281", {"start": v(20.62, 11.08) * mm, "end": v(21.1, 11.67) * mm});
            skLineSegment(sketch, "E2282", {"start": v(21.1, 11.67) * mm, "end": v(21.56, 12.25) * mm});
            skLineSegment(sketch, "E2283", {"start": v(21.56, 12.25) * mm, "end": v(22, 12.83) * mm});
            skLineSegment(sketch, "E2284", {"start": v(22, 12.83) * mm, "end": v(22.41, 13.42) * mm});
            skLineSegment(sketch, "E2285", {"start": v(22.41, 13.42) * mm, "end": v(22.81, 14.04) * mm});
            skLineSegment(sketch, "E2286", {"start": v(22.81, 14.04) * mm, "end": v(23.2, 14.7) * mm});
            skLineSegment(sketch, "E2287", {"start": v(23.2, 14.7) * mm, "end": v(23.57, 15.4) * mm});
            skLineSegment(sketch, "E2288", {"start": v(23.57, 15.4) * mm, "end": v(23.72, 15.7) * mm});
            skLineSegment(sketch, "E2289", {"start": v(23.72, 15.7) * mm, "end": v(23.89, 16.1) * mm});
            skLineSegment(sketch, "E2290", {"start": v(23.89, 16.1) * mm, "end": v(24.06, 16.54) * mm});
            skLineSegment(sketch, "E2291", {"start": v(24.06, 16.54) * mm, "end": v(24.23, 17.02) * mm});
            skLineSegment(sketch, "E2292", {"start": v(24.23, 17.02) * mm, "end": v(24.37, 17.5) * mm});
            skLineSegment(sketch, "E2293", {"start": v(24.37, 17.5) * mm, "end": v(24.48, 17.99) * mm});
            skLineSegment(sketch, "E2294", {"start": v(24.48, 17.99) * mm, "end": v(24.54, 18.43) * mm});
            skLineSegment(sketch, "E2295", {"start": v(24.54, 18.43) * mm, "end": v(24.55, 18.83) * mm});
            skLineSegment(sketch, "E2296", {"start": v(24.55, 18.83) * mm, "end": v(24.47, 18.68) * mm});
            skLineSegment(sketch, "E2297", {"start": v(24.47, 18.68) * mm, "end": v(24.3, 18.4) * mm});
            skLineSegment(sketch, "E2298", {"start": v(24.3, 18.4) * mm, "end": v(24.06, 18.04) * mm});
            skLineSegment(sketch, "E2299", {"start": v(24.06, 18.04) * mm, "end": v(23.79, 17.62) * mm});
            skLineSegment(sketch, "E2300", {"start": v(23.79, 17.62) * mm, "end": v(23.5, 17.2) * mm});
            skLineSegment(sketch, "E2301", {"start": v(23.5, 17.2) * mm, "end": v(23.23, 16.8) * mm});
            skLineSegment(sketch, "E2302", {"start": v(23.23, 16.8) * mm, "end": v(23, 16.46) * mm});
            skLineSegment(sketch, "E2303", {"start": v(23, 16.46) * mm, "end": v(22.82, 16.23) * mm});
            skLineSegment(sketch, "E2304", {"start": v(22.82, 16.23) * mm, "end": v(22.52, 15.84) * mm});
            skLineSegment(sketch, "E2305", {"start": v(22.52, 15.84) * mm, "end": v(22.26, 15.51) * mm});
            skLineSegment(sketch, "E2306", {"start": v(22.26, 15.51) * mm, "end": v(22.03, 15.24) * mm});
            skLineSegment(sketch, "E2307", {"start": v(22.03, 15.24) * mm, "end": v(21.8, 14.99) * mm});
            skLineSegment(sketch, "E2308", {"start": v(21.8, 14.99) * mm, "end": v(21.59, 14.75) * mm});
            skLineSegment(sketch, "E2309", {"start": v(21.59, 14.75) * mm, "end": v(21.34, 14.5) * mm});
            skLineSegment(sketch, "E2310", {"start": v(21.34, 14.5) * mm, "end": v(21.06, 14.2) * mm});
            skLineSegment(sketch, "E2311", {"start": v(21.06, 14.2) * mm, "end": v(20.73, 13.86) * mm});
            skLineSegment(sketch, "E2312", {"start": v(20.73, 13.86) * mm, "end": v(19.5, 12.54) * mm});
            skLineSegment(sketch, "E2313", {"start": v(19.5, 12.54) * mm, "end": v(19.2, 12.22) * mm});
            skLineSegment(sketch, "E2314", {"start": v(19.2, 12.22) * mm, "end": v(18.9, 11.93) * mm});
            skLineSegment(sketch, "E2315", {"start": v(18.9, 11.93) * mm, "end": v(18.58, 11.65) * mm});
            skLineSegment(sketch, "E2316", {"start": v(18.58, 11.65) * mm, "end": v(18.24, 11.35) * mm});
            skLineSegment(sketch, "E2317", {"start": v(18.24, 11.35) * mm, "end": v(17.88, 11.08) * mm});
            skLineSegment(sketch, "E2318", {"start": v(17.88, 11.08) * mm, "end": v(17.76, 11) * mm});
            skLineSegment(sketch, "E2319", {"start": v(17.76, 11) * mm, "end": v(17.68, 10.95) * mm});
            skLineSegment(sketch, "E2320", {"start": v(17.68, 10.95) * mm, "end": v(17.65, 10.9) * mm});
            skLineSegment(sketch, "E2321", {"start": v(17.65, 10.9) * mm, "end": v(17.63, 10.86) * mm});
            skLineSegment(sketch, "E2322", {"start": v(17.63, 10.86) * mm, "end": v(17.6, 10.8) * mm});
            skLineSegment(sketch, "E2323", {"start": v(17.6, 10.8) * mm, "end": v(17.58, 10.72) * mm});
            skLineSegment(sketch, "E2324", {"start": v(17.58, 10.72) * mm, "end": v(17.5, 10.43) * mm});
            skLineSegment(sketch, "E2325", {"start": v(17.5, 10.43) * mm, "end": v(17.42, 10.2) * mm});
            skLineSegment(sketch, "E2326", {"start": v(17.42, 10.2) * mm, "end": v(17.35, 9.98) * mm});
            skLineSegment(sketch, "E2327", {"start": v(17.35, 9.98) * mm, "end": v(17.28, 9.78) * mm});
            skLineSegment(sketch, "E2328", {"start": v(17.28, 9.78) * mm, "end": v(17.2, 9.6) * mm});
            skLineSegment(sketch, "E2329", {"start": v(17.2, 9.6) * mm, "end": v(17.1, 9.39) * mm});
            skLineSegment(sketch, "E2330", {"start": v(17.1, 9.39) * mm, "end": v(16.99, 9.16) * mm});
            skLineSegment(sketch, "E2331", {"start": v(16.99, 9.16) * mm, "end": v(16.85, 8.9) * mm});
            skLineSegment(sketch, "E2332", {"start": v(16.85, 8.9) * mm, "end": v(16.74, 8.71) * mm});
            skLineSegment(sketch, "E2333", {"start": v(16.74, 8.71) * mm, "end": v(16.61, 8.52) * mm});
            skLineSegment(sketch, "E2334", {"start": v(16.61, 8.52) * mm, "end": v(16.48, 8.33) * mm});
            skLineSegment(sketch, "E2335", {"start": v(16.48, 8.33) * mm, "end": v(16.35, 8.16) * mm});
            skLineSegment(sketch, "E2336", {"start": v(16.35, 8.16) * mm, "end": v(15.77, 7.42) * mm});
            skLineSegment(sketch, "E2337", {"start": v(-21.06, 6.76) * mm, "end": v(-21.26, 6.85) * mm});
            skLineSegment(sketch, "E2338", {"start": v(-21.26, 6.85) * mm, "end": v(-21.54, 6.98) * mm});
            skLineSegment(sketch, "E2339", {"start": v(-21.54, 6.98) * mm, "end": v(-21.81, 7.12) * mm});
            skLineSegment(sketch, "E2340", {"start": v(-21.81, 7.12) * mm, "end": v(-22, 7.22) * mm});
            skLineSegment(sketch, "E2341", {"start": v(-22, 7.22) * mm, "end": v(-22.2, 7.37) * mm});
            skLineSegment(sketch, "E2342", {"start": v(-22.2, 7.37) * mm, "end": v(-22.45, 7.53) * mm});
            skLineSegment(sketch, "E2343", {"start": v(-22.45, 7.53) * mm, "end": v(-22.57, 7.6) * mm});
            skLineSegment(sketch, "E2344", {"start": v(-22.57, 7.6) * mm, "end": v(-22.7, 7.68) * mm});
            skLineSegment(sketch, "E2345", {"start": v(-22.7, 7.68) * mm, "end": v(-22.8, 7.73) * mm});
            skLineSegment(sketch, "E2346", {"start": v(-22.8, 7.73) * mm, "end": v(-22.9, 7.77) * mm});
            skLineSegment(sketch, "E2347", {"start": v(-22.9, 7.77) * mm, "end": v(-22.82, 7.62) * mm});
            skLineSegment(sketch, "E2348", {"start": v(-22.82, 7.62) * mm, "end": v(-22.73, 7.49) * mm});
            skLineSegment(sketch, "E2349", {"start": v(-22.73, 7.49) * mm, "end": v(-22.64, 7.37) * mm});
            skLineSegment(sketch, "E2350", {"start": v(-22.64, 7.37) * mm, "end": v(-22.54, 7.26) * mm});
            skLineSegment(sketch, "E2351", {"start": v(-22.54, 7.26) * mm, "end": v(-22.35, 7.07) * mm});
            skLineSegment(sketch, "E2352", {"start": v(-22.35, 7.07) * mm, "end": v(-22.2, 6.9) * mm});
            skLineSegment(sketch, "E2353", {"start": v(-22.2, 6.9) * mm, "end": v(-22.15, 6.87) * mm});
            skLineSegment(sketch, "E2354", {"start": v(-22.15, 6.87) * mm, "end": v(-22.1, 6.83) * mm});
            skLineSegment(sketch, "E2355", {"start": v(-22.1, 6.83) * mm, "end": v(-22.03, 6.76) * mm});
            skLineSegment(sketch, "E2356", {"start": v(-22.03, 6.76) * mm, "end": v(-21.96, 6.68) * mm});
            skLineSegment(sketch, "E2357", {"start": v(-21.96, 6.68) * mm, "end": v(-21.87, 6.59) * mm});
            skLineSegment(sketch, "E2358", {"start": v(-21.87, 6.59) * mm, "end": v(-21.76, 6.48) * mm});
            skLineSegment(sketch, "E2359", {"start": v(-21.76, 6.48) * mm, "end": v(-21.64, 6.37) * mm});
            skLineSegment(sketch, "E2360", {"start": v(-21.64, 6.37) * mm, "end": v(-21.5, 6.26) * mm});
            skLineSegment(sketch, "E2361", {"start": v(-21.5, 6.26) * mm, "end": v(-21.38, 6.15) * mm});
            skLineSegment(sketch, "E2362", {"start": v(-21.38, 6.15) * mm, "end": v(-21.26, 6.04) * mm});
            skLineSegment(sketch, "E2363", {"start": v(-21.26, 6.04) * mm, "end": v(-20.99, 5.85) * mm});
            skLineSegment(sketch, "E2364", {"start": v(-20.99, 5.85) * mm, "end": v(-20.72, 5.67) * mm});
            skLineSegment(sketch, "E2365", {"start": v(-20.72, 5.67) * mm, "end": v(-20.43, 5.5) * mm});
            skLineSegment(sketch, "E2366", {"start": v(-20.43, 5.5) * mm, "end": v(-20.1, 5.32) * mm});
            skLineSegment(sketch, "E2367", {"start": v(-20.1, 5.32) * mm, "end": v(-19.92, 5.23) * mm});
            skLineSegment(sketch, "E2368", {"start": v(-19.92, 5.23) * mm, "end": v(-19.6, 5.1) * mm});
            skLineSegment(sketch, "E2369", {"start": v(-19.6, 5.1) * mm, "end": v(-19.2, 4.93) * mm});
            skLineSegment(sketch, "E2370", {"start": v(-19.2, 4.93) * mm, "end": v(-18.76, 4.76) * mm});
            skLineSegment(sketch, "E2371", {"start": v(-18.76, 4.76) * mm, "end": v(-18.32, 4.6) * mm});
            skLineSegment(sketch, "E2372", {"start": v(-18.32, 4.6) * mm, "end": v(-17.92, 4.46) * mm});
            skLineSegment(sketch, "E2373", {"start": v(-17.92, 4.46) * mm, "end": v(-17.6, 4.36) * mm});
            skLineSegment(sketch, "E2374", {"start": v(-17.6, 4.36) * mm, "end": v(-17.42, 4.34) * mm});
            skLineSegment(sketch, "E2375", {"start": v(-17.42, 4.34) * mm, "end": v(-17.84, 4.35) * mm});
            skLineSegment(sketch, "E2376", {"start": v(-17.84, 4.35) * mm, "end": v(-18.33, 4.44) * mm});
            skLineSegment(sketch, "E2377", {"start": v(-18.33, 4.44) * mm, "end": v(-18.89, 4.6) * mm});
            skLineSegment(sketch, "E2378", {"start": v(-18.89, 4.6) * mm, "end": v(-19.46, 4.8) * mm});
            skLineSegment(sketch, "E2379", {"start": v(-19.46, 4.8) * mm, "end": v(-20.03, 5.05) * mm});
            skLineSegment(sketch, "E2380", {"start": v(-20.03, 5.05) * mm, "end": v(-20.56, 5.3) * mm});
            skLineSegment(sketch, "E2381", {"start": v(-20.56, 5.3) * mm, "end": v(-21.03, 5.56) * mm});
            skLineSegment(sketch, "E2382", {"start": v(-21.03, 5.56) * mm, "end": v(-21.4, 5.81) * mm});
            skLineSegment(sketch, "E2383", {"start": v(-21.4, 5.81) * mm, "end": v(-21.51, 5.9) * mm});
            skLineSegment(sketch, "E2384", {"start": v(-21.51, 5.9) * mm, "end": v(-21.64, 6) * mm});
            skLineSegment(sketch, "E2385", {"start": v(-21.64, 6) * mm, "end": v(-21.76, 6.09) * mm});
            skLineSegment(sketch, "E2386", {"start": v(-21.76, 6.09) * mm, "end": v(-21.89, 6.15) * mm});
            skLineSegment(sketch, "E2387", {"start": v(-21.89, 6.15) * mm, "end": v(-21.62, 5.46) * mm});
            skLineSegment(sketch, "E2388", {"start": v(-21.62, 5.46) * mm, "end": v(-21.08, 4.87) * mm});
            skLineSegment(sketch, "E2389", {"start": v(-21.08, 4.87) * mm, "end": v(-20.34, 4.4) * mm});
            skLineSegment(sketch, "E2390", {"start": v(-20.34, 4.4) * mm, "end": v(-19.47, 4.01) * mm});
            skLineSegment(sketch, "E2391", {"start": v(-19.47, 4.01) * mm, "end": v(-18.53, 3.72) * mm});
            skLineSegment(sketch, "E2392", {"start": v(-18.53, 3.72) * mm, "end": v(-17.6, 3.5) * mm});
            skLineSegment(sketch, "E2393", {"start": v(-17.6, 3.5) * mm, "end": v(-16.72, 3.37) * mm});
            skLineSegment(sketch, "E2394", {"start": v(-16.72, 3.37) * mm, "end": v(-15.99, 3.3) * mm});
            skLineSegment(sketch, "E2395", {"start": v(-15.99, 3.3) * mm, "end": v(-16.05, 3.42) * mm});
            skLineSegment(sketch, "E2396", {"start": v(-16.05, 3.42) * mm, "end": v(-16.15, 3.6) * mm});
            skLineSegment(sketch, "E2397", {"start": v(-16.15, 3.6) * mm, "end": v(-16.28, 3.81) * mm});
            skLineSegment(sketch, "E2398", {"start": v(-16.28, 3.81) * mm, "end": v(-16.42, 4.07) * mm});
            skLineSegment(sketch, "E2399", {"start": v(-16.42, 4.07) * mm, "end": v(-16.57, 4.36) * mm});
            skLineSegment(sketch, "E2400", {"start": v(-16.57, 4.36) * mm, "end": v(-16.72, 4.68) * mm});
            skLineSegment(sketch, "E2401", {"start": v(-16.72, 4.68) * mm, "end": v(-16.85, 5.01) * mm});
            skLineSegment(sketch, "E2402", {"start": v(-16.85, 5.01) * mm, "end": v(-16.95, 5.36) * mm});
            skLineSegment(sketch, "E2403", {"start": v(-16.95, 5.36) * mm, "end": v(-16.7, 5.24) * mm});
            skLineSegment(sketch, "E2404", {"start": v(-16.7, 5.24) * mm, "end": v(-16.36, 5.03) * mm});
            skLineSegment(sketch, "E2405", {"start": v(-16.36, 5.03) * mm, "end": v(-15.93, 4.77) * mm});
            skLineSegment(sketch, "E2406", {"start": v(-15.93, 4.77) * mm, "end": v(-15.47, 4.48) * mm});
            skLineSegment(sketch, "E2407", {"start": v(-15.47, 4.48) * mm, "end": v(-15, 4.2) * mm});
            skLineSegment(sketch, "E2408", {"start": v(-15, 4.2) * mm, "end": v(-14.57, 3.95) * mm});
            skLineSegment(sketch, "E2409", {"start": v(-14.57, 3.95) * mm, "end": v(-14.2, 3.75) * mm});
            skLineSegment(sketch, "E2410", {"start": v(-14.2, 3.75) * mm, "end": v(-13.94, 3.64) * mm});
            skLineSegment(sketch, "E2411", {"start": v(-13.94, 3.64) * mm, "end": v(-14.1, 3.76) * mm});
            skLineSegment(sketch, "E2412", {"start": v(-14.1, 3.76) * mm, "end": v(-14.26, 3.89) * mm});
            skLineSegment(sketch, "E2413", {"start": v(-14.26, 3.89) * mm, "end": v(-14.43, 4.01) * mm});
            skLineSegment(sketch, "E2414", {"start": v(-14.43, 4.01) * mm, "end": v(-14.6, 4.12) * mm});
            skLineSegment(sketch, "E2415", {"start": v(-14.6, 4.12) * mm, "end": v(-14.82, 4.3) * mm});
            skLineSegment(sketch, "E2416", {"start": v(-14.82, 4.3) * mm, "end": v(-15.06, 4.49) * mm});
            skLineSegment(sketch, "E2417", {"start": v(-15.06, 4.49) * mm, "end": v(-15.3, 4.7) * mm});
            skLineSegment(sketch, "E2418", {"start": v(-15.3, 4.7) * mm, "end": v(-15.52, 4.92) * mm});
            skLineSegment(sketch, "E2419", {"start": v(-15.52, 4.92) * mm, "end": v(-15.75, 5.15) * mm});
            skLineSegment(sketch, "E2420", {"start": v(-15.75, 5.15) * mm, "end": v(-15.96, 5.38) * mm});
            skLineSegment(sketch, "E2421", {"start": v(-15.96, 5.38) * mm, "end": v(-16.15, 5.62) * mm});
            skLineSegment(sketch, "E2422", {"start": v(-16.15, 5.62) * mm, "end": v(-16.33, 5.85) * mm});
            skLineSegment(sketch, "E2423", {"start": v(-16.33, 5.85) * mm, "end": v(-16.56, 6.2) * mm});
            skLineSegment(sketch, "E2424", {"start": v(-16.56, 6.2) * mm, "end": v(-16.78, 6.54) * mm});
            skLineSegment(sketch, "E2425", {"start": v(-16.78, 6.54) * mm, "end": v(-16.88, 6.72) * mm});
            skLineSegment(sketch, "E2426", {"start": v(-16.88, 6.72) * mm, "end": v(-16.98, 6.9) * mm});
            skLineSegment(sketch, "E2427", {"start": v(-16.98, 6.9) * mm, "end": v(-17.07, 7.1) * mm});
            skLineSegment(sketch, "E2428", {"start": v(-17.07, 7.1) * mm, "end": v(-17.16, 7.3) * mm});
            skLineSegment(sketch, "E2429", {"start": v(-17.16, 7.3) * mm, "end": v(-17.24, 7.47) * mm});
            skLineSegment(sketch, "E2430", {"start": v(-17.24, 7.47) * mm, "end": v(-17.32, 7.67) * mm});
            skLineSegment(sketch, "E2431", {"start": v(-17.32, 7.67) * mm, "end": v(-17.41, 7.9) * mm});
            skLineSegment(sketch, "E2432", {"start": v(-17.41, 7.9) * mm, "end": v(-17.5, 8.14) * mm});
            skLineSegment(sketch, "E2433", {"start": v(-17.5, 8.14) * mm, "end": v(-17.59, 8.38) * mm});
            skLineSegment(sketch, "E2434", {"start": v(-17.59, 8.38) * mm, "end": v(-17.66, 8.61) * mm});
            skLineSegment(sketch, "E2435", {"start": v(-17.66, 8.61) * mm, "end": v(-17.72, 8.83) * mm});
            skLineSegment(sketch, "E2436", {"start": v(-17.72, 8.83) * mm, "end": v(-17.75, 9.01) * mm});
            skLineSegment(sketch, "E2437", {"start": v(-17.75, 9.01) * mm, "end": v(-17.6, 8.92) * mm});
            skLineSegment(sketch, "E2438", {"start": v(-17.6, 8.92) * mm, "end": v(-17.39, 8.76) * mm});
            skLineSegment(sketch, "E2439", {"start": v(-17.39, 8.76) * mm, "end": v(-17.13, 8.55) * mm});
            skLineSegment(sketch, "E2440", {"start": v(-17.13, 8.55) * mm, "end": v(-16.84, 8.3) * mm});
            skLineSegment(sketch, "E2441", {"start": v(-16.84, 8.3) * mm, "end": v(-16.55, 8.04) * mm});
            skLineSegment(sketch, "E2442", {"start": v(-16.55, 8.04) * mm, "end": v(-16.26, 7.8) * mm});
            skLineSegment(sketch, "E2443", {"start": v(-16.26, 7.8) * mm, "end": v(-16, 7.58) * mm});
            skLineSegment(sketch, "E2444", {"start": v(-16, 7.58) * mm, "end": v(-15.77, 7.42) * mm});
            skLineSegment(sketch, "E2445", {"start": v(-15.77, 7.42) * mm, "end": v(-15.8, 7.48) * mm});
            skLineSegment(sketch, "E2446", {"start": v(-15.8, 7.48) * mm, "end": v(-15.86, 7.57) * mm});
            skLineSegment(sketch, "E2447", {"start": v(-15.86, 7.57) * mm, "end": v(-15.94, 7.67) * mm});
            skLineSegment(sketch, "E2448", {"start": v(-15.94, 7.67) * mm, "end": v(-16.03, 7.78) * mm});
            skLineSegment(sketch, "E2449", {"start": v(-16.03, 7.78) * mm, "end": v(-16.2, 7.99) * mm});
            skLineSegment(sketch, "E2450", {"start": v(-16.2, 7.99) * mm, "end": v(-16.33, 8.14) * mm});
            skLineSegment(sketch, "E2451", {"start": v(-16.33, 8.14) * mm, "end": v(-16.6, 8.5) * mm});
            skLineSegment(sketch, "E2452", {"start": v(-16.6, 8.5) * mm, "end": v(-16.83, 8.88) * mm});
            skLineSegment(sketch, "E2453", {"start": v(-16.83, 8.88) * mm, "end": v(-16.94, 9.07) * mm});
            skLineSegment(sketch, "E2454", {"start": v(-16.94, 9.07) * mm, "end": v(-17.05, 9.28) * mm});
            skLineSegment(sketch, "E2455", {"start": v(-17.05, 9.28) * mm, "end": v(-17.16, 9.5) * mm});
            skLineSegment(sketch, "E2456", {"start": v(-17.16, 9.5) * mm, "end": v(-17.26, 9.73) * mm});
            skLineSegment(sketch, "E2457", {"start": v(-17.26, 9.73) * mm, "end": v(-17.36, 9.97) * mm});
            skLineSegment(sketch, "E2458", {"start": v(-17.36, 9.97) * mm, "end": v(-17.44, 10.2) * mm});
            skLineSegment(sketch, "E2459", {"start": v(-17.44, 10.2) * mm, "end": v(-17.51, 10.45) * mm});
            skLineSegment(sketch, "E2460", {"start": v(-17.51, 10.45) * mm, "end": v(-17.57, 10.69) * mm});
            skLineSegment(sketch, "E2461", {"start": v(-17.57, 10.69) * mm, "end": v(-17.6, 10.81) * mm});
            skLineSegment(sketch, "E2462", {"start": v(-17.6, 10.81) * mm, "end": v(-17.63, 10.9) * mm});
            skLineSegment(sketch, "E2463", {"start": v(-17.63, 10.9) * mm, "end": v(-17.68, 10.95) * mm});
            skLineSegment(sketch, "E2464", {"start": v(-17.68, 10.95) * mm, "end": v(-17.73, 10.99) * mm});
            skLineSegment(sketch, "E2465", {"start": v(-17.73, 10.99) * mm, "end": v(-17.8, 11.03) * mm});
            skLineSegment(sketch, "E2466", {"start": v(-17.8, 11.03) * mm, "end": v(-17.9, 11.09) * mm});
            skLineSegment(sketch, "E2467", {"start": v(-17.9, 11.09) * mm, "end": v(-18.03, 11.18) * mm});
            skLineSegment(sketch, "E2468", {"start": v(-18.03, 11.18) * mm, "end": v(-18.2, 11.31) * mm});
            skLineSegment(sketch, "E2469", {"start": v(-18.2, 11.31) * mm, "end": v(-18.37, 11.46) * mm});
            skLineSegment(sketch, "E2470", {"start": v(-18.37, 11.46) * mm, "end": v(-18.55, 11.62) * mm});
            skLineSegment(sketch, "E2471", {"start": v(-18.55, 11.62) * mm, "end": v(-18.72, 11.76) * mm});
            skLineSegment(sketch, "E2472", {"start": v(-18.72, 11.76) * mm, "end": v(-18.86, 11.9) * mm});
            skLineSegment(sketch, "E2473", {"start": v(-18.86, 11.9) * mm, "end": v(-19.2, 12.23) * mm});
            skLineSegment(sketch, "E2474", {"start": v(-19.2, 12.23) * mm, "end": v(-19.58, 12.62) * mm});
            skLineSegment(sketch, "E2475", {"start": v(-19.58, 12.62) * mm, "end": v(-19.96, 13) * mm});
            skLineSegment(sketch, "E2476", {"start": v(-19.96, 13) * mm, "end": v(-20.26, 13.33) * mm});
            skLineSegment(sketch, "E2477", {"start": v(-20.26, 13.33) * mm, "end": v(-20.33, 13.43) * mm});
            skLineSegment(sketch, "E2478", {"start": v(-20.33, 13.43) * mm, "end": v(-20.4, 13.52) * mm});
            skLineSegment(sketch, "E2479", {"start": v(-20.4, 13.52) * mm, "end": v(-20.56, 13.66) * mm});
            skLineSegment(sketch, "E2480", {"start": v(-20.56, 13.66) * mm, "end": v(-21.63, 14.8) * mm});
            skLineSegment(sketch, "E2481", {"start": v(-21.63, 14.8) * mm, "end": v(-21.93, 15.12) * mm});
            skLineSegment(sketch, "E2482", {"start": v(-21.93, 15.12) * mm, "end": v(-22.51, 15.83) * mm});
            skLineSegment(sketch, "E2483", {"start": v(-22.51, 15.83) * mm, "end": v(-22.79, 16.18) * mm});
            skLineSegment(sketch, "E2484", {"start": v(-22.79, 16.18) * mm, "end": v(-22.96, 16.43) * mm});
            skLineSegment(sketch, "E2485", {"start": v(-22.96, 16.43) * mm, "end": v(-23.2, 16.76) * mm});
            skLineSegment(sketch, "E2486", {"start": v(-23.2, 16.76) * mm, "end": v(-23.47, 17.15) * mm});
            skLineSegment(sketch, "E2487", {"start": v(-23.47, 17.15) * mm, "end": v(-23.76, 17.57) * mm});
            skLineSegment(sketch, "E2488", {"start": v(-23.76, 17.57) * mm, "end": v(-24.03, 17.97) * mm});
            skLineSegment(sketch, "E2489", {"start": v(-24.03, 17.97) * mm, "end": v(-24.27, 18.34) * mm});
            skLineSegment(sketch, "E2490", {"start": v(-24.27, 18.34) * mm, "end": v(-24.45, 18.64) * mm});
            skLineSegment(sketch, "E2491", {"start": v(-24.45, 18.64) * mm, "end": v(-24.55, 18.83) * mm});
            skLineSegment(sketch, "E2492", {"start": v(-24.55, 18.83) * mm, "end": v(-24.55, 18.45) * mm});
            skLineSegment(sketch, "E2493", {"start": v(-24.55, 18.45) * mm, "end": v(-24.49, 18) * mm});
            skLineSegment(sketch, "E2494", {"start": v(-24.49, 18) * mm, "end": v(-24.37, 17.52) * mm});
            skLineSegment(sketch, "E2495", {"start": v(-24.37, 17.52) * mm, "end": v(-24.23, 17.02) * mm});
            skLineSegment(sketch, "E2496", {"start": v(-24.23, 17.02) * mm, "end": v(-24.06, 16.53) * mm});
            skLineSegment(sketch, "E2497", {"start": v(-24.06, 16.53) * mm, "end": v(-23.88, 16.08) * mm});
            skLineSegment(sketch, "E2498", {"start": v(-23.88, 16.08) * mm, "end": v(-23.72, 15.7) * mm});
            skLineSegment(sketch, "E2499", {"start": v(-23.72, 15.7) * mm, "end": v(-23.58, 15.4) * mm});
            skLineSegment(sketch, "E2500", {"start": v(-23.58, 15.4) * mm, "end": v(-23.4, 15.02) * mm});
            skLineSegment(sketch, "E2501", {"start": v(-23.4, 15.02) * mm, "end": v(-23.2, 14.66) * mm});
            skLineSegment(sketch, "E2502", {"start": v(-23.2, 14.66) * mm, "end": v(-22.98, 14.3) * mm});
            skLineSegment(sketch, "E2503", {"start": v(-22.98, 14.3) * mm, "end": v(-22.76, 13.94) * mm});
            skLineSegment(sketch, "E2504", {"start": v(-22.76, 13.94) * mm, "end": v(-22.54, 13.6) * mm});
            skLineSegment(sketch, "E2505", {"start": v(-22.54, 13.6) * mm, "end": v(-22.31, 13.27) * mm});
            skLineSegment(sketch, "E2506", {"start": v(-22.31, 13.27) * mm, "end": v(-22.08, 12.95) * mm});
            skLineSegment(sketch, "E2507", {"start": v(-22.08, 12.95) * mm, "end": v(-21.86, 12.65) * mm});
            skLineSegment(sketch, "E2508", {"start": v(-21.86, 12.65) * mm, "end": v(-21.7, 12.42) * mm});
            skLineSegment(sketch, "E2509", {"start": v(-21.7, 12.42) * mm, "end": v(-21.51, 12.19) * mm});
            skLineSegment(sketch, "E2510", {"start": v(-21.51, 12.19) * mm, "end": v(-21.33, 11.95) * mm});
            skLineSegment(sketch, "E2511", {"start": v(-21.33, 11.95) * mm, "end": v(-21.14, 11.7) * mm});
            skLineSegment(sketch, "E2512", {"start": v(-21.14, 11.7) * mm, "end": v(-20.94, 11.46) * mm});
            skLineSegment(sketch, "E2513", {"start": v(-20.94, 11.46) * mm, "end": v(-20.75, 11.23) * mm});
            skLineSegment(sketch, "E2514", {"start": v(-20.75, 11.23) * mm, "end": v(-20.56, 11) * mm});
            skLineSegment(sketch, "E2515", {"start": v(-20.56, 11) * mm, "end": v(-20.38, 10.8) * mm});
            skLineSegment(sketch, "E2516", {"start": v(-20.38, 10.8) * mm, "end": v(-17.69, 7.9) * mm});
            skLineSegment(sketch, "E2517", {"start": v(-17.69, 7.9) * mm, "end": v(-18.09, 8.03) * mm});
            skLineSegment(sketch, "E2518", {"start": v(-18.09, 8.03) * mm, "end": v(-18.57, 8.25) * mm});
            skLineSegment(sketch, "E2519", {"start": v(-18.57, 8.25) * mm, "end": v(-19.1, 8.54) * mm});
            skLineSegment(sketch, "E2520", {"start": v(-19.1, 8.54) * mm, "end": v(-19.67, 8.87) * mm});
            skLineSegment(sketch, "E2521", {"start": v(-19.67, 8.87) * mm, "end": v(-20.23, 9.24) * mm});
            skLineSegment(sketch, "E2522", {"start": v(-20.23, 9.24) * mm, "end": v(-20.76, 9.6) * mm});
            skLineSegment(sketch, "E2523", {"start": v(-20.76, 9.6) * mm, "end": v(-21.23, 9.96) * mm});
            skLineSegment(sketch, "E2524", {"start": v(-21.23, 9.96) * mm, "end": v(-21.61, 10.27) * mm});
            skLineSegment(sketch, "E2525", {"start": v(-21.61, 10.27) * mm, "end": v(-21.83, 10.46) * mm});
            skLineSegment(sketch, "E2526", {"start": v(-21.83, 10.46) * mm, "end": v(-22.04, 10.64) * mm});
            skLineSegment(sketch, "E2527", {"start": v(-22.04, 10.64) * mm, "end": v(-22.25, 10.83) * mm});
            skLineSegment(sketch, "E2528", {"start": v(-22.25, 10.83) * mm, "end": v(-22.45, 11.02) * mm});
            skLineSegment(sketch, "E2529", {"start": v(-22.45, 11.02) * mm, "end": v(-22.85, 11.41) * mm});
            skLineSegment(sketch, "E2530", {"start": v(-22.85, 11.41) * mm, "end": v(-24.72, 13.47) * mm});
            skLineSegment(sketch, "E2531", {"start": v(-24.72, 13.47) * mm, "end": v(-24.7, 13.32) * mm});
            skLineSegment(sketch, "E2532", {"start": v(-24.7, 13.32) * mm, "end": v(-24.65, 13.15) * mm});
            skLineSegment(sketch, "E2533", {"start": v(-24.65, 13.15) * mm, "end": v(-24.59, 12.95) * mm});
            skLineSegment(sketch, "E2534", {"start": v(-24.59, 12.95) * mm, "end": v(-24.52, 12.75) * mm});
            skLineSegment(sketch, "E2535", {"start": v(-24.52, 12.75) * mm, "end": v(-24.37, 12.37) * mm});
            skLineSegment(sketch, "E2536", {"start": v(-24.37, 12.37) * mm, "end": v(-24.24, 12.06) * mm});
            skLineSegment(sketch, "E2537", {"start": v(-24.24, 12.06) * mm, "end": v(-24.04, 11.64) * mm});
            skLineSegment(sketch, "E2538", {"start": v(-24.04, 11.64) * mm, "end": v(-23.81, 11.21) * mm});
            skLineSegment(sketch, "E2539", {"start": v(-23.81, 11.21) * mm, "end": v(-23.56, 10.8) * mm});
            skLineSegment(sketch, "E2540", {"start": v(-23.56, 10.8) * mm, "end": v(-23.28, 10.4) * mm});
            skLineSegment(sketch, "E2541", {"start": v(-23.28, 10.4) * mm, "end": v(-22.99, 10) * mm});
            skLineSegment(sketch, "E2542", {"start": v(-22.99, 10) * mm, "end": v(-22.68, 9.63) * mm});
            skLineSegment(sketch, "E2543", {"start": v(-22.68, 9.63) * mm, "end": v(-22.36, 9.27) * mm});
            skLineSegment(sketch, "E2544", {"start": v(-22.36, 9.27) * mm, "end": v(-22.03, 8.94) * mm});
            skLineSegment(sketch, "E2545", {"start": v(-22.03, 8.94) * mm, "end": v(-21.52, 8.46) * mm});
            skLineSegment(sketch, "E2546", {"start": v(-21.52, 8.46) * mm, "end": v(-21.03, 8.03) * mm});
            skLineSegment(sketch, "E2547", {"start": v(-21.03, 8.03) * mm, "end": v(-20.53, 7.64) * mm});
            skLineSegment(sketch, "E2548", {"start": v(-20.53, 7.64) * mm, "end": v(-20.03, 7.28) * mm});
            skLineSegment(sketch, "E2549", {"start": v(-20.03, 7.28) * mm, "end": v(-19.52, 6.93) * mm});
            skLineSegment(sketch, "E2550", {"start": v(-19.52, 6.93) * mm, "end": v(-19, 6.59) * mm});
            skLineSegment(sketch, "E2551", {"start": v(-19, 6.59) * mm, "end": v(-18.43, 6.24) * mm});
            skLineSegment(sketch, "E2552", {"start": v(-18.43, 6.24) * mm, "end": v(-17.83, 5.88) * mm});
            skLineSegment(sketch, "E2553", {"start": v(-17.83, 5.88) * mm, "end": v(-17.21, 5.54) * mm});
            skLineSegment(sketch, "E2554", {"start": v(-17.21, 5.54) * mm, "end": v(-17.57, 5.58) * mm});
            skLineSegment(sketch, "E2555", {"start": v(-17.57, 5.58) * mm, "end": v(-18.04, 5.68) * mm});
            skLineSegment(sketch, "E2556", {"start": v(-18.04, 5.68) * mm, "end": v(-18.58, 5.83) * mm});
            skLineSegment(sketch, "E2557", {"start": v(-18.58, 5.83) * mm, "end": v(-19.15, 6.01) * mm});
            skLineSegment(sketch, "E2558", {"start": v(-19.15, 6.01) * mm, "end": v(-19.73, 6.22) * mm});
            skLineSegment(sketch, "E2559", {"start": v(-19.73, 6.22) * mm, "end": v(-20.26, 6.42) * mm});
            skLineSegment(sketch, "E2560", {"start": v(-20.26, 6.42) * mm, "end": v(-20.72, 6.6) * mm});
            skLineSegment(sketch, "E2561", {"start": v(-20.72, 6.6) * mm, "end": v(-21.06, 6.76) * mm});
            skLineSegment(sketch, "E2562", {"start": v(-3.31, -15) * mm, "end": v(-3.07, -14.97) * mm});
            skLineSegment(sketch, "E2563", {"start": v(-3.07, -14.97) * mm, "end": v(-2.85, -14.95) * mm});
            skLineSegment(sketch, "E2564", {"start": v(-2.85, -14.95) * mm, "end": v(-2.73, -14.95) * mm});
            skLineSegment(sketch, "E2565", {"start": v(-2.73, -14.95) * mm, "end": v(-2.6, -14.98) * mm});
            skLineSegment(sketch, "E2566", {"start": v(-2.6, -14.98) * mm, "end": v(-2.44, -15.03) * mm});
            skLineSegment(sketch, "E2567", {"start": v(-2.44, -15.03) * mm, "end": v(-2.27, -15.1) * mm});
            skLineSegment(sketch, "E2568", {"start": v(-2.27, -15.1) * mm, "end": v(-2.18, -15.16) * mm});
            skLineSegment(sketch, "E2569", {"start": v(-2.18, -15.16) * mm, "end": v(-2.12, -15.2) * mm});
            skLineSegment(sketch, "E2570", {"start": v(-2.12, -15.2) * mm, "end": v(-2.05, -15.25) * mm});
            skLineSegment(sketch, "E2571", {"start": v(-2.05, -15.25) * mm, "end": v(-1.97, -15.29) * mm});
            skLineSegment(sketch, "E2572", {"start": v(-1.97, -15.29) * mm, "end": v(-2.04, -15.11) * mm});
            skLineSegment(sketch, "E2573", {"start": v(-2.04, -15.11) * mm, "end": v(-2.12, -14.93) * mm});
            skLineSegment(sketch, "E2574", {"start": v(-2.12, -14.93) * mm, "end": v(-2.2, -14.76) * mm});
            skLineSegment(sketch, "E2575", {"start": v(-2.2, -14.76) * mm, "end": v(-2.28, -14.57) * mm});
            skLineSegment(sketch, "E2576", {"start": v(-2.28, -14.57) * mm, "end": v(-2.36, -14.38) * mm});
            skLineSegment(sketch, "E2577", {"start": v(-2.36, -14.38) * mm, "end": v(-2.42, -14.19) * mm});
            skLineSegment(sketch, "E2578", {"start": v(-2.42, -14.19) * mm, "end": v(-2.47, -13.98) * mm});
            skLineSegment(sketch, "E2579", {"start": v(-2.47, -13.98) * mm, "end": v(-2.5, -13.76) * mm});
            skLineSegment(sketch, "E2580", {"start": v(-2.5, -13.76) * mm, "end": v(-2.42, -13.86) * mm});
            skLineSegment(sketch, "E2581", {"start": v(-2.42, -13.86) * mm, "end": v(-2.38, -13.96) * mm});
            skLineSegment(sketch, "E2582", {"start": v(-2.38, -13.96) * mm, "end": v(-2.34, -14.07) * mm});
            skLineSegment(sketch, "E2583", {"start": v(-2.34, -14.07) * mm, "end": v(-2.3, -14.18) * mm});
            skLineSegment(sketch, "E2584", {"start": v(-2.3, -14.18) * mm, "end": v(-2.24, -14.3) * mm});
            skLineSegment(sketch, "E2585", {"start": v(-2.24, -14.3) * mm, "end": v(-2.18, -14.46) * mm});
            skLineSegment(sketch, "E2586", {"start": v(-2.18, -14.46) * mm, "end": v(-2.1, -14.63) * mm});
            skLineSegment(sketch, "E2587", {"start": v(-2.1, -14.63) * mm, "end": v(-2, -14.8) * mm});
            skLineSegment(sketch, "E2588", {"start": v(-2, -14.8) * mm, "end": v(-1.9, -14.97) * mm});
            skLineSegment(sketch, "E2589", {"start": v(-1.9, -14.97) * mm, "end": v(-1.82, -15.12) * mm});
            skLineSegment(sketch, "E2590", {"start": v(-1.82, -15.12) * mm, "end": v(-1.73, -15.24) * mm});
            skLineSegment(sketch, "E2591", {"start": v(-1.73, -15.24) * mm, "end": v(-1.65, -15.33) * mm});
            skLineSegment(sketch, "E2592", {"start": v(-1.65, -15.33) * mm, "end": v(-1.46, -15.44) * mm});
            skLineSegment(sketch, "E2593", {"start": v(-1.46, -15.44) * mm, "end": v(-1.3, -15.4) * mm});
            skLineSegment(sketch, "E2594", {"start": v(-1.3, -15.4) * mm, "end": v(-1.17, -15.22) * mm});
            skLineSegment(sketch, "E2595", {"start": v(-1.17, -15.22) * mm, "end": v(-1.08, -14.97) * mm});
            skLineSegment(sketch, "E2596", {"start": v(-1.08, -14.97) * mm, "end": v(-1, -14.67) * mm});
            skLineSegment(sketch, "E2597", {"start": v(-1, -14.67) * mm, "end": v(-0.95, -14.37) * mm});
            skLineSegment(sketch, "E2598", {"start": v(-0.95, -14.37) * mm, "end": v(-0.92, -14.1) * mm});
            skLineSegment(sketch, "E2599", {"start": v(-0.92, -14.1) * mm, "end": v(-0.9, -13.9) * mm});
            skLineSegment(sketch, "E2600", {"start": v(-0.9, -13.9) * mm, "end": v(-0.84, -14.04) * mm});
            skLineSegment(sketch, "E2601", {"start": v(-0.84, -14.04) * mm, "end": v(-0.77, -14.28) * mm});
            skLineSegment(sketch, "E2602", {"start": v(-0.77, -14.28) * mm, "end": v(-0.68, -14.6) * mm});
            skLineSegment(sketch, "E2603", {"start": v(-0.68, -14.6) * mm, "end": v(-0.57, -14.95) * mm});
            skLineSegment(sketch, "E2604", {"start": v(-0.57, -14.95) * mm, "end": v(-0.45, -15.3) * mm});
            skLineSegment(sketch, "E2605", {"start": v(-0.45, -15.3) * mm, "end": v(-0.31, -15.62) * mm});
            skLineSegment(sketch, "E2606", {"start": v(-0.31, -15.62) * mm, "end": v(-0.16, -15.85) * mm});
            skLineSegment(sketch, "E2607", {"start": v(-0.16, -15.85) * mm, "end": v(0, -15.97) * mm});
            skLineSegment(sketch, "E2608", {"start": v(0, -15.97) * mm, "end": v(0.2, -15.95) * mm});
            skLineSegment(sketch, "E2609", {"start": v(0.2, -15.95) * mm, "end": v(0.38, -15.8) * mm});
            skLineSegment(sketch, "E2610", {"start": v(0.38, -15.8) * mm, "end": v(0.55, -15.53) * mm});
            skLineSegment(sketch, "E2611", {"start": v(0.55, -15.53) * mm, "end": v(0.71, -15.2) * mm});
            skLineSegment(sketch, "E2612", {"start": v(0.71, -15.2) * mm, "end": v(0.85, -14.86) * mm});
            skLineSegment(sketch, "E2613", {"start": v(0.85, -14.86) * mm, "end": v(0.96, -14.53) * mm});
            skLineSegment(sketch, "E2614", {"start": v(0.96, -14.53) * mm, "end": v(1.05, -14.25) * mm});
            skLineSegment(sketch, "E2615", {"start": v(1.05, -14.25) * mm, "end": v(1.1, -14.06) * mm});
            skLineSegment(sketch, "E2616", {"start": v(1.1, -14.06) * mm, "end": v(1.17, -14.27) * mm});
            skLineSegment(sketch, "E2617", {"start": v(1.17, -14.27) * mm, "end": v(1.23, -14.58) * mm});
            skLineSegment(sketch, "E2618", {"start": v(1.23, -14.58) * mm, "end": v(1.3, -14.92) * mm});
            skLineSegment(sketch, "E2619", {"start": v(1.3, -14.92) * mm, "end": v(1.4, -15.21) * mm});
            skLineSegment(sketch, "E2620", {"start": v(1.4, -15.21) * mm, "end": v(1.52, -15.4) * mm});
            skLineSegment(sketch, "E2621", {"start": v(1.52, -15.4) * mm, "end": v(1.7, -15.4) * mm});
            skLineSegment(sketch, "E2622", {"start": v(1.7, -15.4) * mm, "end": v(1.93, -15.17) * mm});
            skLineSegment(sketch, "E2623", {"start": v(1.93, -15.17) * mm, "end": v(2.24, -14.63) * mm});
            skLineSegment(sketch, "E2624", {"start": v(2.24, -14.63) * mm, "end": v(2.4, -14.24) * mm});
            skLineSegment(sketch, "E2625", {"start": v(2.4, -14.24) * mm, "end": v(2.55, -13.83) * mm});
            skLineSegment(sketch, "E2626", {"start": v(2.55, -13.83) * mm, "end": v(2.57, -13.8) * mm});
            skLineSegment(sketch, "E2627", {"start": v(2.57, -13.8) * mm, "end": v(2.52, -14.18) * mm});
            skLineSegment(sketch, "E2628", {"start": v(2.52, -14.18) * mm, "end": v(2.4, -14.57) * mm});
            skLineSegment(sketch, "E2629", {"start": v(2.4, -14.57) * mm, "end": v(2.24, -14.95) * mm});
            skLineSegment(sketch, "E2630", {"start": v(2.24, -14.95) * mm, "end": v(2.06, -15.28) * mm});
            skLineSegment(sketch, "E2631", {"start": v(2.06, -15.28) * mm, "end": v(1.85, -15.53) * mm});
            skLineSegment(sketch, "E2632", {"start": v(1.85, -15.53) * mm, "end": v(1.65, -15.68) * mm});
            skLineSegment(sketch, "E2633", {"start": v(1.65, -15.68) * mm, "end": v(1.46, -15.7) * mm});
            skLineSegment(sketch, "E2634", {"start": v(1.46, -15.7) * mm, "end": v(1.3, -15.55) * mm});
            skLineSegment(sketch, "E2635", {"start": v(1.3, -15.55) * mm, "end": v(1.24, -15.45) * mm});
            skLineSegment(sketch, "E2636", {"start": v(1.24, -15.45) * mm, "end": v(1.2, -15.33) * mm});
            skLineSegment(sketch, "E2637", {"start": v(1.2, -15.33) * mm, "end": v(1.18, -15.22) * mm});
            skLineSegment(sketch, "E2638", {"start": v(1.18, -15.22) * mm, "end": v(1.16, -15.1) * mm});
            skLineSegment(sketch, "E2639", {"start": v(1.16, -15.1) * mm, "end": v(1.14, -14.98) * mm});
            skLineSegment(sketch, "E2640", {"start": v(1.14, -14.98) * mm, "end": v(1.11, -14.86) * mm});
            skLineSegment(sketch, "E2641", {"start": v(1.11, -14.86) * mm, "end": v(1.09, -14.76) * mm});
            skLineSegment(sketch, "E2642", {"start": v(1.09, -14.76) * mm, "end": v(1.05, -14.67) * mm});
            skLineSegment(sketch, "E2643", {"start": v(1.05, -14.67) * mm, "end": v(0.98, -14.88) * mm});
            skLineSegment(sketch, "E2644", {"start": v(0.98, -14.88) * mm, "end": v(0.9, -15.14) * mm});
            skLineSegment(sketch, "E2645", {"start": v(0.9, -15.14) * mm, "end": v(0.8, -15.43) * mm});
            skLineSegment(sketch, "E2646", {"start": v(0.8, -15.43) * mm, "end": v(0.7, -15.71) * mm});
            skLineSegment(sketch, "E2647", {"start": v(0.7, -15.71) * mm, "end": v(0.57, -15.97) * mm});
            skLineSegment(sketch, "E2648", {"start": v(0.57, -15.97) * mm, "end": v(0.42, -16.19) * mm});
            skLineSegment(sketch, "E2649", {"start": v(0.42, -16.19) * mm, "end": v(0.26, -16.33) * mm});
            skLineSegment(sketch, "E2650", {"start": v(0.26, -16.33) * mm, "end": v(0.06, -16.38) * mm});
            skLineSegment(sketch, "E2651", {"start": v(0.06, -16.38) * mm, "end": v(-0.04, -16.35) * mm});
            skLineSegment(sketch, "E2652", {"start": v(-0.04, -16.35) * mm, "end": v(-0.14, -16.3) * mm});
            skLineSegment(sketch, "E2653", {"start": v(-0.14, -16.3) * mm, "end": v(-0.23, -16.2) * mm});
            skLineSegment(sketch, "E2654", {"start": v(-0.23, -16.2) * mm, "end": v(-0.3, -16.1) * mm});
            skLineSegment(sketch, "E2655", {"start": v(-0.3, -16.1) * mm, "end": v(-0.37, -15.98) * mm});
            skLineSegment(sketch, "E2656", {"start": v(-0.37, -15.98) * mm, "end": v(-0.43, -15.86) * mm});
            skLineSegment(sketch, "E2657", {"start": v(-0.43, -15.86) * mm, "end": v(-0.48, -15.74) * mm});
            skLineSegment(sketch, "E2658", {"start": v(-0.48, -15.74) * mm, "end": v(-0.53, -15.62) * mm});
            skLineSegment(sketch, "E2659", {"start": v(-0.53, -15.62) * mm, "end": v(-0.6, -15.36) * mm});
            skLineSegment(sketch, "E2660", {"start": v(-0.6, -15.36) * mm, "end": v(-0.68, -15.04) * mm});
            skLineSegment(sketch, "E2661", {"start": v(-0.68, -15.04) * mm, "end": v(-0.72, -14.88) * mm});
            skLineSegment(sketch, "E2662", {"start": v(-0.72, -14.88) * mm, "end": v(-0.76, -14.74) * mm});
            skLineSegment(sketch, "E2663", {"start": v(-0.76, -14.74) * mm, "end": v(-0.8, -14.63) * mm});
            skLineSegment(sketch, "E2664", {"start": v(-0.8, -14.63) * mm, "end": v(-0.84, -14.55) * mm});
            skLineSegment(sketch, "E2665", {"start": v(-0.84, -14.55) * mm, "end": v(-0.84, -14.68) * mm});
            skLineSegment(sketch, "E2666", {"start": v(-0.84, -14.68) * mm, "end": v(-0.85, -14.86) * mm});
            skLineSegment(sketch, "E2667", {"start": v(-0.85, -14.86) * mm, "end": v(-0.87, -15.07) * mm});
            skLineSegment(sketch, "E2668", {"start": v(-0.87, -15.07) * mm, "end": v(-0.91, -15.28) * mm});
            skLineSegment(sketch, "E2669", {"start": v(-0.91, -15.28) * mm, "end": v(-0.97, -15.49) * mm});
            skLineSegment(sketch, "E2670", {"start": v(-0.97, -15.49) * mm, "end": v(-1.05, -15.66) * mm});
            skLineSegment(sketch, "E2671", {"start": v(-1.05, -15.66) * mm, "end": v(-1.15, -15.8) * mm});
            skLineSegment(sketch, "E2672", {"start": v(-1.15, -15.8) * mm, "end": v(-1.28, -15.85) * mm});
            skLineSegment(sketch, "E2673", {"start": v(-1.28, -15.85) * mm, "end": v(-1.35, -15.85) * mm});
            skLineSegment(sketch, "E2674", {"start": v(-1.35, -15.85) * mm, "end": v(-1.4, -15.84) * mm});
            skLineSegment(sketch, "E2675", {"start": v(-1.4, -15.84) * mm, "end": v(-1.46, -15.82) * mm});
            skLineSegment(sketch, "E2676", {"start": v(-1.46, -15.82) * mm, "end": v(-1.51, -15.8) * mm});
            skLineSegment(sketch, "E2677", {"start": v(-1.51, -15.8) * mm, "end": v(-1.6, -15.72) * mm});
            skLineSegment(sketch, "E2678", {"start": v(-1.6, -15.72) * mm, "end": v(-1.7, -15.67) * mm});
            skLineSegment(sketch, "E2679", {"start": v(-1.7, -15.67) * mm, "end": v(-1.36, -16.25) * mm});
            skLineSegment(sketch, "E2680", {"start": v(-1.36, -16.25) * mm, "end": v(-1.21, -16.56) * mm});
            skLineSegment(sketch, "E2681", {"start": v(-1.21, -16.56) * mm, "end": v(-1.17, -16.66) * mm});
            skLineSegment(sketch, "E2682", {"start": v(-1.17, -16.66) * mm, "end": v(-1.14, -16.72) * mm});
            skLineSegment(sketch, "E2683", {"start": v(-1.14, -16.72) * mm, "end": v(-1.1, -16.75) * mm});
            skLineSegment(sketch, "E2684", {"start": v(-1.1, -16.75) * mm, "end": v(-1, -16.8) * mm});
            skLineSegment(sketch, "E2685", {"start": v(-1, -16.8) * mm, "end": v(-0.89, -16.85) * mm});
            skLineSegment(sketch, "E2686", {"start": v(-0.89, -16.85) * mm, "end": v(-0.72, -16.92) * mm});
            skLineSegment(sketch, "E2687", {"start": v(-0.72, -16.92) * mm, "end": v(-0.53, -17) * mm});
            skLineSegment(sketch, "E2688", {"start": v(-0.53, -17) * mm, "end": v(-0.32, -17.08) * mm});
            skLineSegment(sketch, "E2689", {"start": v(-0.32, -17.08) * mm, "end": v(-0.11, -17.14) * mm});
            skLineSegment(sketch, "E2690", {"start": v(-0.11, -17.14) * mm, "end": v(0.08, -17.2) * mm});
            skLineSegment(sketch, "E2691", {"start": v(0.08, -17.2) * mm, "end": v(0.24, -17.22) * mm});
            skLineSegment(sketch, "E2692", {"start": v(0.24, -17.22) * mm, "end": v(0.36, -17.2) * mm});
            skLineSegment(sketch, "E2693", {"start": v(0.36, -17.2) * mm, "end": v(0.62, -17.1) * mm});
            skLineSegment(sketch, "E2694", {"start": v(0.62, -17.1) * mm, "end": v(1.01, -16.92) * mm});
            skLineSegment(sketch, "E2695", {"start": v(1.01, -16.92) * mm, "end": v(1.2, -16.82) * mm});
            skLineSegment(sketch, "E2696", {"start": v(1.2, -16.82) * mm, "end": v(1.38, -16.73) * mm});
            skLineSegment(sketch, "E2697", {"start": v(1.38, -16.73) * mm, "end": v(1.52, -16.65) * mm});
            skLineSegment(sketch, "E2698", {"start": v(1.52, -16.65) * mm, "end": v(1.59, -16.6) * mm});
            skLineSegment(sketch, "E2699", {"start": v(1.59, -16.6) * mm, "end": v(1.64, -16.53) * mm});
            skLineSegment(sketch, "E2700", {"start": v(1.64, -16.53) * mm, "end": v(1.7, -16.43) * mm});
            skLineSegment(sketch, "E2701", {"start": v(1.7, -16.43) * mm, "end": v(1.76, -16.3) * mm});
            skLineSegment(sketch, "E2702", {"start": v(1.76, -16.3) * mm, "end": v(1.83, -16.15) * mm});
            skLineSegment(sketch, "E2703", {"start": v(1.83, -16.15) * mm, "end": v(1.92, -15.99) * mm});
            skLineSegment(sketch, "E2704", {"start": v(1.92, -15.99) * mm, "end": v(2.02, -15.81) * mm});
            skLineSegment(sketch, "E2705", {"start": v(2.02, -15.81) * mm, "end": v(2.14, -15.63) * mm});
            skLineSegment(sketch, "E2706", {"start": v(2.14, -15.63) * mm, "end": v(2.27, -15.45) * mm});
            skLineSegment(sketch, "E2707", {"start": v(2.27, -15.45) * mm, "end": v(2.47, -15.24) * mm});
            skLineSegment(sketch, "E2708", {"start": v(2.47, -15.24) * mm, "end": v(2.66, -15.1) * mm});
            skLineSegment(sketch, "E2709", {"start": v(2.66, -15.1) * mm, "end": v(2.84, -15.03) * mm});
            skLineSegment(sketch, "E2710", {"start": v(2.84, -15.03) * mm, "end": v(3, -15) * mm});
            skLineSegment(sketch, "E2711", {"start": v(3, -15) * mm, "end": v(3.14, -14.97) * mm});
            skLineSegment(sketch, "E2712", {"start": v(3.14, -14.97) * mm, "end": v(3.26, -14.95) * mm});
            skLineSegment(sketch, "E2713", {"start": v(3.26, -14.95) * mm, "end": v(3.37, -14.9) * mm});
            skLineSegment(sketch, "E2714", {"start": v(3.37, -14.9) * mm, "end": v(3.45, -14.8) * mm});
            skLineSegment(sketch, "E2715", {"start": v(3.45, -14.8) * mm, "end": v(3.63, -14.5) * mm});
            skLineSegment(sketch, "E2716", {"start": v(3.63, -14.5) * mm, "end": v(3.77, -14.2) * mm});
            skLineSegment(sketch, "E2717", {"start": v(3.77, -14.2) * mm, "end": v(3.9, -13.9) * mm});
            skLineSegment(sketch, "E2718", {"start": v(3.9, -13.9) * mm, "end": v(4.05, -13.56) * mm});
            skLineSegment(sketch, "E2719", {"start": v(4.05, -13.56) * mm, "end": v(4.16, -13.22) * mm});
            skLineSegment(sketch, "E2720", {"start": v(4.16, -13.22) * mm, "end": v(4.27, -12.85) * mm});
            skLineSegment(sketch, "E2721", {"start": v(4.27, -12.85) * mm, "end": v(4.37, -12.45) * mm});
            skLineSegment(sketch, "E2722", {"start": v(4.37, -12.45) * mm, "end": v(4.45, -12.04) * mm});
            skLineSegment(sketch, "E2723", {"start": v(4.45, -12.04) * mm, "end": v(4.52, -11.62) * mm});
            skLineSegment(sketch, "E2724", {"start": v(4.52, -11.62) * mm, "end": v(4.57, -11.2) * mm});
            skLineSegment(sketch, "E2725", {"start": v(4.57, -11.2) * mm, "end": v(4.6, -10.8) * mm});
            skLineSegment(sketch, "E2726", {"start": v(4.6, -10.8) * mm, "end": v(4.6, -10.4) * mm});
            skLineSegment(sketch, "E2727", {"start": v(4.6, -10.4) * mm, "end": v(4.44, -10.56) * mm});
            skLineSegment(sketch, "E2728", {"start": v(4.44, -10.56) * mm, "end": v(4.31, -10.64) * mm});
            skLineSegment(sketch, "E2729", {"start": v(4.31, -10.64) * mm, "end": v(4.2, -10.64) * mm});
            skLineSegment(sketch, "E2730", {"start": v(4.2, -10.64) * mm, "end": v(4.13, -10.58) * mm});
            skLineSegment(sketch, "E2731", {"start": v(4.13, -10.58) * mm, "end": v(4.07, -10.47) * mm});
            skLineSegment(sketch, "E2732", {"start": v(4.07, -10.47) * mm, "end": v(4.02, -10.32) * mm});
            skLineSegment(sketch, "E2733", {"start": v(4.02, -10.32) * mm, "end": v(3.98, -10.14) * mm});
            skLineSegment(sketch, "E2734", {"start": v(3.98, -10.14) * mm, "end": v(3.95, -9.94) * mm});
            skLineSegment(sketch, "E2735", {"start": v(3.95, -9.94) * mm, "end": v(3.8, -9) * mm});
            skLineSegment(sketch, "E2736", {"start": v(3.8, -9) * mm, "end": v(3.53, -10.29) * mm});
            skLineSegment(sketch, "E2737", {"start": v(3.53, -10.29) * mm, "end": v(3.44, -10.55) * mm});
            skLineSegment(sketch, "E2738", {"start": v(3.44, -10.55) * mm, "end": v(3.33, -10.75) * mm});
            skLineSegment(sketch, "E2739", {"start": v(3.33, -10.75) * mm, "end": v(3.22, -10.89) * mm});
            skLineSegment(sketch, "E2740", {"start": v(3.22, -10.89) * mm, "end": v(3.1, -10.98) * mm});
            skLineSegment(sketch, "E2741", {"start": v(3.1, -10.98) * mm, "end": v(3, -11.04) * mm});
            skLineSegment(sketch, "E2742", {"start": v(3, -11.04) * mm, "end": v(2.9, -11.08) * mm});
            skLineSegment(sketch, "E2743", {"start": v(2.9, -11.08) * mm, "end": v(2.84, -11.11) * mm});
            skLineSegment(sketch, "E2744", {"start": v(2.84, -11.11) * mm, "end": v(2.8, -11.16) * mm});
            skLineSegment(sketch, "E2745", {"start": v(2.8, -11.16) * mm, "end": v(2.8, -11.29) * mm});
            skLineSegment(sketch, "E2746", {"start": v(2.8, -11.29) * mm, "end": v(2.8, -11.57) * mm});
            skLineSegment(sketch, "E2747", {"start": v(2.8, -11.57) * mm, "end": v(2.85, -11.92) * mm});
            skLineSegment(sketch, "E2748", {"start": v(2.85, -11.92) * mm, "end": v(2.93, -12.26) * mm});
            skLineSegment(sketch, "E2749", {"start": v(2.93, -12.26) * mm, "end": v(3.06, -12.5) * mm});
            skLineSegment(sketch, "E2750", {"start": v(3.06, -12.5) * mm, "end": v(3.25, -12.55) * mm});
            skLineSegment(sketch, "E2751", {"start": v(3.25, -12.55) * mm, "end": v(3.5, -12.33) * mm});
            skLineSegment(sketch, "E2752", {"start": v(3.5, -12.33) * mm, "end": v(3.85, -11.77) * mm});
            skLineSegment(sketch, "E2753", {"start": v(3.85, -11.77) * mm, "end": v(3.93, -11.59) * mm});
            skLineSegment(sketch, "E2754", {"start": v(3.93, -11.59) * mm, "end": v(4.01, -11.39) * mm});
            skLineSegment(sketch, "E2755", {"start": v(4.01, -11.39) * mm, "end": v(4.1, -11.2) * mm});
            skLineSegment(sketch, "E2756", {"start": v(4.1, -11.2) * mm, "end": v(4.19, -11.03) * mm});
            skLineSegment(sketch, "E2757", {"start": v(4.19, -11.03) * mm, "end": v(4.16, -11.21) * mm});
            skLineSegment(sketch, "E2758", {"start": v(4.16, -11.21) * mm, "end": v(4.1, -11.41) * mm});
            skLineSegment(sketch, "E2759", {"start": v(4.1, -11.41) * mm, "end": v(4.03, -11.63) * mm});
            skLineSegment(sketch, "E2760", {"start": v(4.03, -11.63) * mm, "end": v(3.94, -11.84) * mm});
            skLineSegment(sketch, "E2761", {"start": v(3.94, -11.84) * mm, "end": v(3.85, -12.04) * mm});
            skLineSegment(sketch, "E2762", {"start": v(3.85, -12.04) * mm, "end": v(3.75, -12.24) * mm});
            skLineSegment(sketch, "E2763", {"start": v(3.75, -12.24) * mm, "end": v(3.66, -12.4) * mm});
            skLineSegment(sketch, "E2764", {"start": v(3.66, -12.4) * mm, "end": v(3.57, -12.54) * mm});
            skLineSegment(sketch, "E2765", {"start": v(3.57, -12.54) * mm, "end": v(3.33, -12.82) * mm});
            skLineSegment(sketch, "E2766", {"start": v(3.33, -12.82) * mm, "end": v(3.14, -12.92) * mm});
            skLineSegment(sketch, "E2767", {"start": v(3.14, -12.92) * mm, "end": v(2.98, -12.88) * mm});
            skLineSegment(sketch, "E2768", {"start": v(2.98, -12.88) * mm, "end": v(2.86, -12.74) * mm});
            skLineSegment(sketch, "E2769", {"start": v(2.86, -12.74) * mm, "end": v(2.77, -12.55) * mm});
            skLineSegment(sketch, "E2770", {"start": v(2.77, -12.55) * mm, "end": v(2.7, -12.34) * mm});
            skLineSegment(sketch, "E2771", {"start": v(2.7, -12.34) * mm, "end": v(2.66, -12.16) * mm});
            skLineSegment(sketch, "E2772", {"start": v(2.66, -12.16) * mm, "end": v(2.63, -12.05) * mm});
            skLineSegment(sketch, "E2773", {"start": v(2.63, -12.05) * mm, "end": v(2.42, -12.45) * mm});
            skLineSegment(sketch, "E2774", {"start": v(2.42, -12.45) * mm, "end": v(2.2, -12.92) * mm});
            skLineSegment(sketch, "E2775", {"start": v(2.2, -12.92) * mm, "end": v(2.06, -13.14) * mm});
            skLineSegment(sketch, "E2776", {"start": v(2.06, -13.14) * mm, "end": v(1.92, -13.31) * mm});
            skLineSegment(sketch, "E2777", {"start": v(1.92, -13.31) * mm, "end": v(1.75, -13.43) * mm});
            skLineSegment(sketch, "E2778", {"start": v(1.75, -13.43) * mm, "end": v(1.57, -13.47) * mm});
            skLineSegment(sketch, "E2779", {"start": v(1.57, -13.47) * mm, "end": v(1.44, -13.33) * mm});
            skLineSegment(sketch, "E2780", {"start": v(1.44, -13.33) * mm, "end": v(1.35, -13.16) * mm});
            skLineSegment(sketch, "E2781", {"start": v(1.35, -13.16) * mm, "end": v(1.3, -12.98) * mm});
            skLineSegment(sketch, "E2782", {"start": v(1.3, -12.98) * mm, "end": v(1.27, -12.78) * mm});
            skLineSegment(sketch, "E2783", {"start": v(1.27, -12.78) * mm, "end": v(1.25, -12.58) * mm});
            skLineSegment(sketch, "E2784", {"start": v(1.25, -12.58) * mm, "end": v(1.23, -12.37) * mm});
            skLineSegment(sketch, "E2785", {"start": v(1.23, -12.37) * mm, "end": v(1.2, -12.18) * mm});
            skLineSegment(sketch, "E2786", {"start": v(1.2, -12.18) * mm, "end": v(1.15, -12) * mm});
            skLineSegment(sketch, "E2787", {"start": v(1.15, -12) * mm, "end": v(1.07, -12.23) * mm});
            skLineSegment(sketch, "E2788", {"start": v(1.07, -12.23) * mm, "end": v(0.98, -12.53) * mm});
            skLineSegment(sketch, "E2789", {"start": v(0.98, -12.53) * mm, "end": v(0.88, -12.88) * mm});
            skLineSegment(sketch, "E2790", {"start": v(0.88, -12.88) * mm, "end": v(0.75, -13.24) * mm});
            skLineSegment(sketch, "E2791", {"start": v(0.75, -13.24) * mm, "end": v(0.6, -13.56) * mm});
            skLineSegment(sketch, "E2792", {"start": v(0.6, -13.56) * mm, "end": v(0.44, -13.83) * mm});
            skLineSegment(sketch, "E2793", {"start": v(0.44, -13.83) * mm, "end": v(0.25, -14) * mm});
            skLineSegment(sketch, "E2794", {"start": v(0.25, -14) * mm, "end": v(0.03, -14.04) * mm});
            skLineSegment(sketch, "E2795", {"start": v(0.03, -14.04) * mm, "end": v(-0.16, -13.94) * mm});
            skLineSegment(sketch, "E2796", {"start": v(-0.16, -13.94) * mm, "end": v(-0.32, -13.74) * mm});
            skLineSegment(sketch, "E2797", {"start": v(-0.32, -13.74) * mm, "end": v(-0.47, -13.46) * mm});
            skLineSegment(sketch, "E2798", {"start": v(-0.47, -13.46) * mm, "end": v(-0.59, -13.12) * mm});
            skLineSegment(sketch, "E2799", {"start": v(-0.59, -13.12) * mm, "end": v(-0.7, -12.76) * mm});
            skLineSegment(sketch, "E2800", {"start": v(-0.7, -12.76) * mm, "end": v(-0.78, -12.41) * mm});
            skLineSegment(sketch, "E2801", {"start": v(-0.78, -12.41) * mm, "end": v(-0.86, -12.1) * mm});
            skLineSegment(sketch, "E2802", {"start": v(-0.86, -12.1) * mm, "end": v(-0.92, -11.84) * mm});
            skLineSegment(sketch, "E2803", {"start": v(-0.92, -11.84) * mm, "end": v(-1.1, -12.9) * mm});
            skLineSegment(sketch, "E2804", {"start": v(-1.1, -12.9) * mm, "end": v(-1.33, -13.4) * mm});
            skLineSegment(sketch, "E2805", {"start": v(-1.33, -13.4) * mm, "end": v(-1.6, -13.45) * mm});
            skLineSegment(sketch, "E2806", {"start": v(-1.6, -13.45) * mm, "end": v(-1.88, -13.2) * mm});
            skLineSegment(sketch, "E2807", {"start": v(-1.88, -13.2) * mm, "end": v(-2.14, -12.74) * mm});
            skLineSegment(sketch, "E2808", {"start": v(-2.14, -12.74) * mm, "end": v(-2.39, -12.21) * mm});
            skLineSegment(sketch, "E2809", {"start": v(-2.39, -12.21) * mm, "end": v(-2.58, -11.74) * mm});
            skLineSegment(sketch, "E2810", {"start": v(-2.58, -11.74) * mm, "end": v(-2.71, -11.45) * mm});
            skLineSegment(sketch, "E2811", {"start": v(-2.71, -11.45) * mm, "end": v(-2.72, -11.66) * mm});
            skLineSegment(sketch, "E2812", {"start": v(-2.72, -11.66) * mm, "end": v(-2.73, -11.88) * mm});
            skLineSegment(sketch, "E2813", {"start": v(-2.73, -11.88) * mm, "end": v(-2.74, -12.1) * mm});
            skLineSegment(sketch, "E2814", {"start": v(-2.74, -12.1) * mm, "end": v(-2.76, -12.3) * mm});
            skLineSegment(sketch, "E2815", {"start": v(-2.76, -12.3) * mm, "end": v(-2.78, -12.5) * mm});
            skLineSegment(sketch, "E2816", {"start": v(-2.78, -12.5) * mm, "end": v(-2.83, -12.68) * mm});
            skLineSegment(sketch, "E2817", {"start": v(-2.83, -12.68) * mm, "end": v(-2.89, -12.85) * mm});
            skLineSegment(sketch, "E2818", {"start": v(-2.89, -12.85) * mm, "end": v(-2.97, -13) * mm});
            skLineSegment(sketch, "E2819", {"start": v(-2.97, -13) * mm, "end": v(-3.11, -12.99) * mm});
            skLineSegment(sketch, "E2820", {"start": v(-3.11, -12.99) * mm, "end": v(-3.24, -12.94) * mm});
            skLineSegment(sketch, "E2821", {"start": v(-3.24, -12.94) * mm, "end": v(-3.35, -12.85) * mm});
            skLineSegment(sketch, "E2822", {"start": v(-3.35, -12.85) * mm, "end": v(-3.44, -12.74) * mm});
            skLineSegment(sketch, "E2823", {"start": v(-3.44, -12.74) * mm, "end": v(-3.53, -12.6) * mm});
            skLineSegment(sketch, "E2824", {"start": v(-3.53, -12.6) * mm, "end": v(-3.6, -12.46) * mm});
            skLineSegment(sketch, "E2825", {"start": v(-3.6, -12.46) * mm, "end": v(-3.68, -12.3) * mm});
            skLineSegment(sketch, "E2826", {"start": v(-3.68, -12.3) * mm, "end": v(-3.75, -12.14) * mm});
            skLineSegment(sketch, "E2827", {"start": v(-3.75, -12.14) * mm, "end": v(-3.86, -11.88) * mm});
            skLineSegment(sketch, "E2828", {"start": v(-3.86, -11.88) * mm, "end": v(-3.98, -11.54) * mm});
            skLineSegment(sketch, "E2829", {"start": v(-3.98, -11.54) * mm, "end": v(-4.03, -11.36) * mm});
            skLineSegment(sketch, "E2830", {"start": v(-4.03, -11.36) * mm, "end": v(-4.08, -11.2) * mm});
            skLineSegment(sketch, "E2831", {"start": v(-4.08, -11.2) * mm, "end": v(-4.12, -11.04) * mm});
            skLineSegment(sketch, "E2832", {"start": v(-4.12, -11.04) * mm, "end": v(-4.13, -10.92) * mm});
            skLineSegment(sketch, "E2833", {"start": v(-4.13, -10.92) * mm, "end": v(-3.74, -11.75) * mm});
            skLineSegment(sketch, "E2834", {"start": v(-3.74, -11.75) * mm, "end": v(-3.63, -11.96) * mm});
            skLineSegment(sketch, "E2835", {"start": v(-3.63, -11.96) * mm, "end": v(-3.51, -12.2) * mm});
            skLineSegment(sketch, "E2836", {"start": v(-3.51, -12.2) * mm, "end": v(-3.45, -12.3) * mm});
            skLineSegment(sketch, "E2837", {"start": v(-3.45, -12.3) * mm, "end": v(-3.37, -12.39) * mm});
            skLineSegment(sketch, "E2838", {"start": v(-3.37, -12.39) * mm, "end": v(-3.28, -12.46) * mm});
            skLineSegment(sketch, "E2839", {"start": v(-3.28, -12.46) * mm, "end": v(-3.19, -12.5) * mm});
            skLineSegment(sketch, "E2840", {"start": v(-3.19, -12.5) * mm, "end": v(-3.1, -12.44) * mm});
            skLineSegment(sketch, "E2841", {"start": v(-3.1, -12.44) * mm, "end": v(-3.05, -12.37) * mm});
            skLineSegment(sketch, "E2842", {"start": v(-3.05, -12.37) * mm, "end": v(-3, -12.3) * mm});
            skLineSegment(sketch, "E2843", {"start": v(-3, -12.3) * mm, "end": v(-2.98, -12.22) * mm});
            skLineSegment(sketch, "E2844", {"start": v(-2.98, -12.22) * mm, "end": v(-2.88, -11.75) * mm});
            skLineSegment(sketch, "E2845", {"start": v(-2.88, -11.75) * mm, "end": v(-2.84, -11.53) * mm});
            skLineSegment(sketch, "E2846", {"start": v(-2.84, -11.53) * mm, "end": v(-2.8, -11.25) * mm});
            skLineSegment(sketch, "E2847", {"start": v(-2.8, -11.25) * mm, "end": v(-2.78, -11.1) * mm});
            skLineSegment(sketch, "E2848", {"start": v(-2.78, -11.1) * mm, "end": v(-2.77, -10.97) * mm});
            skLineSegment(sketch, "E2849", {"start": v(-2.77, -10.97) * mm, "end": v(-2.77, -10.85) * mm});
            skLineSegment(sketch, "E2850", {"start": v(-2.77, -10.85) * mm, "end": v(-2.78, -10.75) * mm});
            skLineSegment(sketch, "E2851", {"start": v(-2.78, -10.75) * mm, "end": v(-2.84, -10.52) * mm});
            skLineSegment(sketch, "E2852", {"start": v(-2.84, -10.52) * mm, "end": v(-2.9, -10.32) * mm});
            skLineSegment(sketch, "E2853", {"start": v(-2.9, -10.32) * mm, "end": v(-2.93, -10.22) * mm});
            skLineSegment(sketch, "E2854", {"start": v(-2.93, -10.22) * mm, "end": v(-2.96, -10.1) * mm});
            skLineSegment(sketch, "E2855", {"start": v(-2.96, -10.1) * mm, "end": v(-2.98, -9.97) * mm});
            skLineSegment(sketch, "E2856", {"start": v(-2.98, -9.97) * mm, "end": v(-3, -9.82) * mm});
            skLineSegment(sketch, "E2857", {"start": v(-3, -9.82) * mm, "end": v(-3.01, -8.74) * mm});
            skLineSegment(sketch, "E2858", {"start": v(-3.01, -8.74) * mm, "end": v(-3.1, -8.84) * mm});
            skLineSegment(sketch, "E2859", {"start": v(-3.1, -8.84) * mm, "end": v(-3.16, -9) * mm});
            skLineSegment(sketch, "E2860", {"start": v(-3.16, -9) * mm, "end": v(-3.22, -9.17) * mm});
            skLineSegment(sketch, "E2861", {"start": v(-3.22, -9.17) * mm, "end": v(-3.27, -9.37) * mm});
            skLineSegment(sketch, "E2862", {"start": v(-3.27, -9.37) * mm, "end": v(-3.35, -9.8) * mm});
            skLineSegment(sketch, "E2863", {"start": v(-3.35, -9.8) * mm, "end": v(-3.42, -10.14) * mm});
            skLineSegment(sketch, "E2864", {"start": v(-3.42, -10.14) * mm, "end": v(-3.5, -10.34) * mm});
            skLineSegment(sketch, "E2865", {"start": v(-3.5, -10.34) * mm, "end": v(-3.6, -10.5) * mm});
            skLineSegment(sketch, "E2866", {"start": v(-3.6, -10.5) * mm, "end": v(-3.72, -10.6) * mm});
            skLineSegment(sketch, "E2867", {"start": v(-3.72, -10.6) * mm, "end": v(-3.86, -10.63) * mm});
            skLineSegment(sketch, "E2868", {"start": v(-3.86, -10.63) * mm, "end": v(-4, -10.62) * mm});
            skLineSegment(sketch, "E2869", {"start": v(-4, -10.62) * mm, "end": v(-4.14, -10.55) * mm});
            skLineSegment(sketch, "E2870", {"start": v(-4.14, -10.55) * mm, "end": v(-4.27, -10.43) * mm});
            skLineSegment(sketch, "E2871", {"start": v(-4.27, -10.43) * mm, "end": v(-4.38, -10.26) * mm});
            skLineSegment(sketch, "E2872", {"start": v(-4.38, -10.26) * mm, "end": v(-4.48, -9.96) * mm});
            skLineSegment(sketch, "E2873", {"start": v(-4.48, -9.96) * mm, "end": v(-4.53, -9.58) * mm});
            skLineSegment(sketch, "E2874", {"start": v(-4.53, -9.58) * mm, "end": v(-4.52, -9.16) * mm});
            skLineSegment(sketch, "E2875", {"start": v(-4.52, -9.16) * mm, "end": v(-4.48, -8.72) * mm});
            skLineSegment(sketch, "E2876", {"start": v(-4.48, -8.72) * mm, "end": v(-4.4, -8.28) * mm});
            skLineSegment(sketch, "E2877", {"start": v(-4.4, -8.28) * mm, "end": v(-4.32, -7.87) * mm});
            skLineSegment(sketch, "E2878", {"start": v(-4.32, -7.87) * mm, "end": v(-4.2, -7.51) * mm});
            skLineSegment(sketch, "E2879", {"start": v(-4.2, -7.51) * mm, "end": v(-4.1, -7.23) * mm});
            skLineSegment(sketch, "E2880", {"start": v(-4.1, -7.23) * mm, "end": v(-4.1, -7.35) * mm});
            skLineSegment(sketch, "E2881", {"start": v(-4.1, -7.35) * mm, "end": v(-4.12, -7.57) * mm});
            skLineSegment(sketch, "E2882", {"start": v(-4.12, -7.57) * mm, "end": v(-4.16, -7.86) * mm});
            skLineSegment(sketch, "E2883", {"start": v(-4.16, -7.86) * mm, "end": v(-4.21, -8.21) * mm});
            skLineSegment(sketch, "E2884", {"start": v(-4.21, -8.21) * mm, "end": v(-4.26, -8.6) * mm});
            skLineSegment(sketch, "E2885", {"start": v(-4.26, -8.6) * mm, "end": v(-4.3, -9) * mm});
            skLineSegment(sketch, "E2886", {"start": v(-4.3, -9) * mm, "end": v(-4.3, -9.38) * mm});
            skLineSegment(sketch, "E2887", {"start": v(-4.3, -9.38) * mm, "end": v(-4.27, -9.74) * mm});
            skLineSegment(sketch, "E2888", {"start": v(-4.27, -9.74) * mm, "end": v(-4.25, -9.84) * mm});
            skLineSegment(sketch, "E2889", {"start": v(-4.25, -9.84) * mm, "end": v(-4.23, -9.94) * mm});
            skLineSegment(sketch, "E2890", {"start": v(-4.23, -9.94) * mm, "end": v(-4.2, -10.03) * mm});
            skLineSegment(sketch, "E2891", {"start": v(-4.2, -10.03) * mm, "end": v(-4.16, -10.1) * mm});
            skLineSegment(sketch, "E2892", {"start": v(-4.16, -10.1) * mm, "end": v(-4.1, -10.17) * mm});
            skLineSegment(sketch, "E2893", {"start": v(-4.1, -10.17) * mm, "end": v(-4.04, -10.2) * mm});
            skLineSegment(sketch, "E2894", {"start": v(-4.04, -10.2) * mm, "end": v(-3.95, -10.23) * mm});
            skLineSegment(sketch, "E2895", {"start": v(-3.95, -10.23) * mm, "end": v(-3.84, -10.23) * mm});
            skLineSegment(sketch, "E2896", {"start": v(-3.84, -10.23) * mm, "end": v(-3.8, -10.18) * mm});
            skLineSegment(sketch, "E2897", {"start": v(-3.8, -10.18) * mm, "end": v(-3.74, -10.05) * mm});
            skLineSegment(sketch, "E2898", {"start": v(-3.74, -10.05) * mm, "end": v(-3.67, -9.88) * mm});
            skLineSegment(sketch, "E2899", {"start": v(-3.67, -9.88) * mm, "end": v(-3.6, -9.67) * mm});
            skLineSegment(sketch, "E2900", {"start": v(-3.6, -9.67) * mm, "end": v(-3.47, -9.22) * mm});
            skLineSegment(sketch, "E2901", {"start": v(-3.47, -9.22) * mm, "end": v(-3.34, -8.84) * mm});
            skLineSegment(sketch, "E2902", {"start": v(-3.34, -8.84) * mm, "end": v(-3.19, -8.5) * mm});
            skLineSegment(sketch, "E2903", {"start": v(-3.19, -8.5) * mm, "end": v(-3.03, -8.17) * mm});
            skLineSegment(sketch, "E2904", {"start": v(-3.03, -8.17) * mm, "end": v(-2.87, -7.85) * mm});
            skLineSegment(sketch, "E2905", {"start": v(-2.87, -7.85) * mm, "end": v(-2.72, -7.53) * mm});
            skLineSegment(sketch, "E2906", {"start": v(-2.72, -7.53) * mm, "end": v(-2.72, -7.7) * mm});
            skLineSegment(sketch, "E2907", {"start": v(-2.72, -7.7) * mm, "end": v(-2.75, -8.08) * mm});
            skLineSegment(sketch, "E2908", {"start": v(-2.75, -8.08) * mm, "end": v(-2.8, -8.57) * mm});
            skLineSegment(sketch, "E2909", {"start": v(-2.8, -8.57) * mm, "end": v(-2.81, -9.13) * mm});
            skLineSegment(sketch, "E2910", {"start": v(-2.81, -9.13) * mm, "end": v(-2.8, -9.7) * mm});
            skLineSegment(sketch, "E2911", {"start": v(-2.8, -9.7) * mm, "end": v(-2.74, -10.2) * mm});
            skLineSegment(sketch, "E2912", {"start": v(-2.74, -10.2) * mm, "end": v(-2.6, -10.6) * mm});
            skLineSegment(sketch, "E2913", {"start": v(-2.6, -10.6) * mm, "end": v(-2.36, -10.82) * mm});
            skLineSegment(sketch, "E2914", {"start": v(-2.36, -10.82) * mm, "end": v(-2.25, -10.7) * mm});
            skLineSegment(sketch, "E2915", {"start": v(-2.25, -10.7) * mm, "end": v(-2.16, -10.5) * mm});
            skLineSegment(sketch, "E2916", {"start": v(-2.16, -10.5) * mm, "end": v(-2.07, -10.24) * mm});
            skLineSegment(sketch, "E2917", {"start": v(-2.07, -10.24) * mm, "end": v(-1.97, -9.95) * mm});
            skLineSegment(sketch, "E2918", {"start": v(-1.97, -9.95) * mm, "end": v(-1.84, -9.63) * mm});
            skLineSegment(sketch, "E2919", {"start": v(-1.84, -9.63) * mm, "end": v(-1.7, -9.3) * mm});
            skLineSegment(sketch, "E2920", {"start": v(-1.7, -9.3) * mm, "end": v(-1.5, -8.95) * mm});
            skLineSegment(sketch, "E2921", {"start": v(-1.5, -8.95) * mm, "end": v(-1.25, -8.63) * mm});
            skLineSegment(sketch, "E2922", {"start": v(-1.25, -8.63) * mm, "end": v(-1.24, -8.96) * mm});
            skLineSegment(sketch, "E2923", {"start": v(-1.24, -8.96) * mm, "end": v(-1.21, -9.35) * mm});
            skLineSegment(sketch, "E2924", {"start": v(-1.21, -9.35) * mm, "end": v(-1.17, -9.78) * mm});
            skLineSegment(sketch, "E2925", {"start": v(-1.17, -9.78) * mm, "end": v(-1.1, -10.2) * mm});
            skLineSegment(sketch, "E2926", {"start": v(-1.1, -10.2) * mm, "end": v(-1.02, -10.62) * mm});
            skLineSegment(sketch, "E2927", {"start": v(-1.02, -10.62) * mm, "end": v(-0.9, -10.97) * mm});
            skLineSegment(sketch, "E2928", {"start": v(-0.9, -10.97) * mm, "end": v(-0.75, -11.25) * mm});
            skLineSegment(sketch, "E2929", {"start": v(-0.75, -11.25) * mm, "end": v(-0.56, -11.42) * mm});
            skLineSegment(sketch, "E2930", {"start": v(-0.56, -11.42) * mm, "end": v(-0.46, -11.37) * mm});
            skLineSegment(sketch, "E2931", {"start": v(-0.46, -11.37) * mm, "end": v(-0.4, -11.32) * mm});
            skLineSegment(sketch, "E2932", {"start": v(-0.4, -11.32) * mm, "end": v(-0.37, -11.26) * mm});
            skLineSegment(sketch, "E2933", {"start": v(-0.37, -11.26) * mm, "end": v(-0.32, -11.14) * mm});
            skLineSegment(sketch, "E2934", {"start": v(-0.32, -11.14) * mm, "end": v(-0.25, -10.87) * mm});
            skLineSegment(sketch, "E2935", {"start": v(-0.25, -10.87) * mm, "end": v(-0.16, -10.46) * mm});
            skLineSegment(sketch, "E2936", {"start": v(-0.16, -10.46) * mm, "end": v(-0.12, -10.26) * mm});
            skLineSegment(sketch, "E2937", {"start": v(-0.12, -10.26) * mm, "end": v(-0.09, -10.07) * mm});
            skLineSegment(sketch, "E2938", {"start": v(-0.09, -10.07) * mm, "end": v(-0.07, -9.92) * mm});
            skLineSegment(sketch, "E2939", {"start": v(-0.07, -9.92) * mm, "end": v(-0.07, -9.83) * mm});
            skLineSegment(sketch, "E2940", {"start": v(-0.07, -9.83) * mm, "end": v(-0.1, -9.56) * mm});
            skLineSegment(sketch, "E2941", {"start": v(-0.1, -9.56) * mm, "end": v(-0.15, -9.38) * mm});
            skLineSegment(sketch, "E2942", {"start": v(-0.15, -9.38) * mm, "end": v(-0.2, -9.25) * mm});
            skLineSegment(sketch, "E2943", {"start": v(-0.2, -9.25) * mm, "end": v(-0.23, -9.13) * mm});
            skLineSegment(sketch, "E2944", {"start": v(-0.23, -9.13) * mm, "end": v(-0.24, -8.98) * mm});
            skLineSegment(sketch, "E2945", {"start": v(-0.24, -8.98) * mm, "end": v(-0.23, -8.76) * mm});
            skLineSegment(sketch, "E2946", {"start": v(-0.23, -8.76) * mm, "end": v(-0.19, -8.43) * mm});
            skLineSegment(sketch, "E2947", {"start": v(-0.19, -8.43) * mm, "end": v(-0.1, -7.96) * mm});
            skLineSegment(sketch, "E2948", {"start": v(-0.1, -7.96) * mm, "end": v(-0.42, -8.03) * mm});
            skLineSegment(sketch, "E2949", {"start": v(-0.42, -8.03) * mm, "end": v(-0.72, -8.14) * mm});
            skLineSegment(sketch, "E2950", {"start": v(-0.72, -8.14) * mm, "end": v(-1, -8.29) * mm});
            skLineSegment(sketch, "E2951", {"start": v(-1, -8.29) * mm, "end": v(-1.28, -8.47) * mm});
            skLineSegment(sketch, "E2952", {"start": v(-1.28, -8.47) * mm, "end": v(-1.54, -8.67) * mm});
            skLineSegment(sketch, "E2953", {"start": v(-1.54, -8.67) * mm, "end": v(-1.78, -8.89) * mm});
            skLineSegment(sketch, "E2954", {"start": v(-1.78, -8.89) * mm, "end": v(-2, -9.1) * mm});
            skLineSegment(sketch, "E2955", {"start": v(-2, -9.1) * mm, "end": v(-2.23, -9.32) * mm});
            skLineSegment(sketch, "E2956", {"start": v(-2.23, -9.32) * mm, "end": v(-2.24, -8.86) * mm});
            skLineSegment(sketch, "E2957", {"start": v(-2.24, -8.86) * mm, "end": v(-2.22, -8.42) * mm});
            skLineSegment(sketch, "E2958", {"start": v(-2.22, -8.42) * mm, "end": v(-2.17, -8) * mm});
            skLineSegment(sketch, "E2959", {"start": v(-2.17, -8) * mm, "end": v(-2.08, -7.59) * mm});
            skLineSegment(sketch, "E2960", {"start": v(-2.08, -7.59) * mm, "end": v(-1.97, -7.2) * mm});
            skLineSegment(sketch, "E2961", {"start": v(-1.97, -7.2) * mm, "end": v(-1.82, -6.84) * mm});
            skLineSegment(sketch, "E2962", {"start": v(-1.82, -6.84) * mm, "end": v(-1.65, -6.51) * mm});
            skLineSegment(sketch, "E2963", {"start": v(-1.65, -6.51) * mm, "end": v(-1.46, -6.2) * mm});
            skLineSegment(sketch, "E2964", {"start": v(-1.46, -6.2) * mm, "end": v(-1.6, -6.2) * mm});
            skLineSegment(sketch, "E2965", {"start": v(-1.6, -6.2) * mm, "end": v(-1.77, -6.24) * mm});
            skLineSegment(sketch, "E2966", {"start": v(-1.77, -6.24) * mm, "end": v(-1.93, -6.29) * mm});
            skLineSegment(sketch, "E2967", {"start": v(-1.93, -6.29) * mm, "end": v(-2.1, -6.35) * mm});
            skLineSegment(sketch, "E2968", {"start": v(-2.1, -6.35) * mm, "end": v(-2.25, -6.42) * mm});
            skLineSegment(sketch, "E2969", {"start": v(-2.25, -6.42) * mm, "end": v(-2.39, -6.5) * mm});
            skLineSegment(sketch, "E2970", {"start": v(-2.39, -6.5) * mm, "end": v(-2.52, -6.57) * mm});
            skLineSegment(sketch, "E2971", {"start": v(-2.52, -6.57) * mm, "end": v(-2.63, -6.63) * mm});
            skLineSegment(sketch, "E2972", {"start": v(-2.63, -6.63) * mm, "end": v(-2.9, -6.82) * mm});
            skLineSegment(sketch, "E2973", {"start": v(-2.9, -6.82) * mm, "end": v(-3.18, -7.04) * mm});
            skLineSegment(sketch, "E2974", {"start": v(-3.18, -7.04) * mm, "end": v(-3.42, -7.22) * mm});
            skLineSegment(sketch, "E2975", {"start": v(-3.42, -7.22) * mm, "end": v(-3.57, -7.32) * mm});
            skLineSegment(sketch, "E2976", {"start": v(-3.57, -7.32) * mm, "end": v(-3.53, -6.85) * mm});
            skLineSegment(sketch, "E2977", {"start": v(-3.53, -6.85) * mm, "end": v(-3.43, -6.38) * mm});
            skLineSegment(sketch, "E2978", {"start": v(-3.43, -6.38) * mm, "end": v(-3.28, -5.93) * mm});
            skLineSegment(sketch, "E2979", {"start": v(-3.28, -5.93) * mm, "end": v(-3.08, -5.5) * mm});
            skLineSegment(sketch, "E2980", {"start": v(-3.08, -5.5) * mm, "end": v(-2.83, -5.11) * mm});
            skLineSegment(sketch, "E2981", {"start": v(-2.83, -5.11) * mm, "end": v(-2.54, -4.75) * mm});
            skLineSegment(sketch, "E2982", {"start": v(-2.54, -4.75) * mm, "end": v(-2.2, -4.43) * mm});
            skLineSegment(sketch, "E2983", {"start": v(-2.2, -4.43) * mm, "end": v(-1.84, -4.17) * mm});
            skLineSegment(sketch, "E2984", {"start": v(-1.84, -4.17) * mm, "end": v(-1.74, -4.1) * mm});
            skLineSegment(sketch, "E2985", {"start": v(-1.74, -4.1) * mm, "end": v(-1.62, -4.04) * mm});
            skLineSegment(sketch, "E2986", {"start": v(-1.62, -4.04) * mm, "end": v(-1.5, -3.97) * mm});
            skLineSegment(sketch, "E2987", {"start": v(-1.5, -3.97) * mm, "end": v(-1.41, -3.9) * mm});
            skLineSegment(sketch, "E2988", {"start": v(-1.41, -3.9) * mm, "end": v(-1.57, -3.84) * mm});
            skLineSegment(sketch, "E2989", {"start": v(-1.57, -3.84) * mm, "end": v(-1.76, -3.83) * mm});
            skLineSegment(sketch, "E2990", {"start": v(-1.76, -3.83) * mm, "end": v(-1.97, -3.87) * mm});
            skLineSegment(sketch, "E2991", {"start": v(-1.97, -3.87) * mm, "end": v(-2.18, -3.93) * mm});
            skLineSegment(sketch, "E2992", {"start": v(-2.18, -3.93) * mm, "end": v(-2.39, -4.01) * mm});
            skLineSegment(sketch, "E2993", {"start": v(-2.39, -4.01) * mm, "end": v(-2.58, -4.1) * mm});
            skLineSegment(sketch, "E2994", {"start": v(-2.58, -4.1) * mm, "end": v(-2.74, -4.2) * mm});
            skLineSegment(sketch, "E2995", {"start": v(-2.74, -4.2) * mm, "end": v(-2.87, -4.27) * mm});
            skLineSegment(sketch, "E2996", {"start": v(-2.87, -4.27) * mm, "end": v(-3.01, -4.37) * mm});
            skLineSegment(sketch, "E2997", {"start": v(-3.01, -4.37) * mm, "end": v(-3.15, -4.48) * mm});
            skLineSegment(sketch, "E2998", {"start": v(-3.15, -4.48) * mm, "end": v(-3.29, -4.6) * mm});
            skLineSegment(sketch, "E2999", {"start": v(-3.29, -4.6) * mm, "end": v(-3.42, -4.73) * mm});
            skLineSegment(sketch, "E3000", {"start": v(-3.42, -4.73) * mm, "end": v(-3.54, -4.86) * mm});
            skLineSegment(sketch, "E3001", {"start": v(-3.54, -4.86) * mm, "end": v(-3.65, -5) * mm});
            skLineSegment(sketch, "E3002", {"start": v(-3.65, -5) * mm, "end": v(-3.76, -5.14) * mm});
            skLineSegment(sketch, "E3003", {"start": v(-3.76, -5.14) * mm, "end": v(-3.85, -5.28) * mm});
            skLineSegment(sketch, "E3004", {"start": v(-3.85, -5.28) * mm, "end": v(-4.06, -5.65) * mm});
            skLineSegment(sketch, "E3005", {"start": v(-4.06, -5.65) * mm, "end": v(-4.22, -6.02) * mm});
            skLineSegment(sketch, "E3006", {"start": v(-4.22, -6.02) * mm, "end": v(-4.35, -6.38) * mm});
            skLineSegment(sketch, "E3007", {"start": v(-4.35, -6.38) * mm, "end": v(-4.46, -6.76) * mm});
            skLineSegment(sketch, "E3008", {"start": v(-4.46, -6.76) * mm, "end": v(-4.53, -7.15) * mm});
            skLineSegment(sketch, "E3009", {"start": v(-4.53, -7.15) * mm, "end": v(-4.6, -7.56) * mm});
            skLineSegment(sketch, "E3010", {"start": v(-4.6, -7.56) * mm, "end": v(-4.64, -8) * mm});
            skLineSegment(sketch, "E3011", {"start": v(-4.64, -8) * mm, "end": v(-4.69, -8.49) * mm});
            skLineSegment(sketch, "E3012", {"start": v(-4.69, -8.49) * mm, "end": v(-4.72, -8.95) * mm});
            skLineSegment(sketch, "E3013", {"start": v(-4.72, -8.95) * mm, "end": v(-4.75, -9.42) * mm});
            skLineSegment(sketch, "E3014", {"start": v(-4.75, -9.42) * mm, "end": v(-4.76, -9.88) * mm});
            skLineSegment(sketch, "E3015", {"start": v(-4.76, -9.88) * mm, "end": v(-4.75, -10.35) * mm});
            skLineSegment(sketch, "E3016", {"start": v(-4.75, -10.35) * mm, "end": v(-4.73, -10.8) * mm});
            skLineSegment(sketch, "E3017", {"start": v(-4.73, -10.8) * mm, "end": v(-4.69, -11.26) * mm});
            skLineSegment(sketch, "E3018", {"start": v(-4.69, -11.26) * mm, "end": v(-4.63, -11.72) * mm});
            skLineSegment(sketch, "E3019", {"start": v(-4.63, -11.72) * mm, "end": v(-4.54, -12.17) * mm});
            skLineSegment(sketch, "E3020", {"start": v(-4.54, -12.17) * mm, "end": v(-4.5, -12.38) * mm});
            skLineSegment(sketch, "E3021", {"start": v(-4.5, -12.38) * mm, "end": v(-4.44, -12.58) * mm});
            skLineSegment(sketch, "E3022", {"start": v(-4.44, -12.58) * mm, "end": v(-4.4, -12.78) * mm});
            skLineSegment(sketch, "E3023", {"start": v(-4.4, -12.78) * mm, "end": v(-4.34, -12.97) * mm});
            skLineSegment(sketch, "E3024", {"start": v(-4.34, -12.97) * mm, "end": v(-4.28, -13.16) * mm});
            skLineSegment(sketch, "E3025", {"start": v(-4.28, -13.16) * mm, "end": v(-4.22, -13.35) * mm});
            skLineSegment(sketch, "E3026", {"start": v(-4.22, -13.35) * mm, "end": v(-4.15, -13.53) * mm});
            skLineSegment(sketch, "E3027", {"start": v(-4.15, -13.53) * mm, "end": v(-4.07, -13.7) * mm});
            skLineSegment(sketch, "E3028", {"start": v(-4.07, -13.7) * mm, "end": v(-3.9, -14.04) * mm});
            skLineSegment(sketch, "E3029", {"start": v(-3.9, -14.04) * mm, "end": v(-3.72, -14.4) * mm});
            skLineSegment(sketch, "E3030", {"start": v(-3.72, -14.4) * mm, "end": v(-3.62, -14.56) * mm});
            skLineSegment(sketch, "E3031", {"start": v(-3.62, -14.56) * mm, "end": v(-3.52, -14.72) * mm});
            skLineSegment(sketch, "E3032", {"start": v(-3.52, -14.72) * mm, "end": v(-3.42, -14.87) * mm});
            skLineSegment(sketch, "E3033", {"start": v(-3.42, -14.87) * mm, "end": v(-3.31, -15) * mm});
            skLineSegment(sketch, "E3034", {"start": v(9.94, 7.16) * mm, "end": v(9.87, 7.08) * mm});
            skLineSegment(sketch, "E3035", {"start": v(9.87, 7.08) * mm, "end": v(9.78, 6.99) * mm});
            skLineSegment(sketch, "E3036", {"start": v(9.78, 6.99) * mm, "end": v(9.66, 6.89) * mm});
            skLineSegment(sketch, "E3037", {"start": v(9.66, 6.89) * mm, "end": v(9.52, 6.79) * mm});
            skLineSegment(sketch, "E3038", {"start": v(9.52, 6.79) * mm, "end": v(9.25, 6.59) * mm});
            skLineSegment(sketch, "E3039", {"start": v(9.25, 6.59) * mm, "end": v(9.03, 6.43) * mm});
            skLineSegment(sketch, "E3040", {"start": v(9.03, 6.43) * mm, "end": v(8.54, 6.08) * mm});
            skLineSegment(sketch, "E3041", {"start": v(8.54, 6.08) * mm, "end": v(8.06, 5.75) * mm});
            skLineSegment(sketch, "E3042", {"start": v(8.06, 5.75) * mm, "end": v(7.92, 5.67) * mm});
            skLineSegment(sketch, "E3043", {"start": v(7.92, 5.67) * mm, "end": v(7.78, 5.59) * mm});
            skLineSegment(sketch, "E3044", {"start": v(7.78, 5.59) * mm, "end": v(7.65, 5.5) * mm});
            skLineSegment(sketch, "E3045", {"start": v(7.65, 5.5) * mm, "end": v(7.5, 5.42) * mm});
            skLineSegment(sketch, "E3046", {"start": v(7.5, 5.42) * mm, "end": v(5.82, 4.43) * mm});
            skLineSegment(sketch, "E3047", {"start": v(5.82, 4.43) * mm, "end": v(5.5, 4.25) * mm});
            skLineSegment(sketch, "E3048", {"start": v(5.5, 4.25) * mm, "end": v(5.24, 4.08) * mm});
            skLineSegment(sketch, "E3049", {"start": v(5.24, 4.08) * mm, "end": v(5.11, 4) * mm});
            skLineSegment(sketch, "E3050", {"start": v(5.11, 4) * mm, "end": v(5, 3.9) * mm});
            skLineSegment(sketch, "E3051", {"start": v(5, 3.9) * mm, "end": v(4.88, 3.8) * mm});
            skLineSegment(sketch, "E3052", {"start": v(4.88, 3.8) * mm, "end": v(4.78, 3.68) * mm});
            skLineSegment(sketch, "E3053", {"start": v(4.78, 3.68) * mm, "end": v(4.55, 3.37) * mm});
            skLineSegment(sketch, "E3054", {"start": v(4.55, 3.37) * mm, "end": v(4.39, 3.04) * mm});
            skLineSegment(sketch, "E3055", {"start": v(4.39, 3.04) * mm, "end": v(4.28, 2.7) * mm});
            skLineSegment(sketch, "E3056", {"start": v(4.28, 2.7) * mm, "end": v(4.24, 2.35) * mm});
            skLineSegment(sketch, "E3057", {"start": v(4.24, 2.35) * mm, "end": v(4.25, 2) * mm});
            skLineSegment(sketch, "E3058", {"start": v(4.25, 2) * mm, "end": v(4.32, 1.66) * mm});
            skLineSegment(sketch, "E3059", {"start": v(4.32, 1.66) * mm, "end": v(4.44, 1.34) * mm});
            skLineSegment(sketch, "E3060", {"start": v(4.44, 1.34) * mm, "end": v(4.62, 1.03) * mm});
            skLineSegment(sketch, "E3061", {"start": v(4.62, 1.03) * mm, "end": v(4.94, 0.59) * mm});
            skLineSegment(sketch, "E3062", {"start": v(4.94, 0.59) * mm, "end": v(5.22, 0.14) * mm});
            skLineSegment(sketch, "E3063", {"start": v(5.22, 0.14) * mm, "end": v(5.45, -0.3) * mm});
            skLineSegment(sketch, "E3064", {"start": v(5.45, -0.3) * mm, "end": v(5.64, -0.76) * mm});
            skLineSegment(sketch, "E3065", {"start": v(5.64, -0.76) * mm, "end": v(5.75, -1.24) * mm});
            skLineSegment(sketch, "E3066", {"start": v(5.75, -1.24) * mm, "end": v(5.78, -1.74) * mm});
            skLineSegment(sketch, "E3067", {"start": v(5.78, -1.74) * mm, "end": v(5.73, -2.28) * mm});
            skLineSegment(sketch, "E3068", {"start": v(5.73, -2.28) * mm, "end": v(5.56, -2.86) * mm});
            skLineSegment(sketch, "E3069", {"start": v(5.56, -2.86) * mm, "end": v(5.67, -2.92) * mm});
            skLineSegment(sketch, "E3070", {"start": v(5.67, -2.92) * mm, "end": v(5.78, -2.96) * mm});
            skLineSegment(sketch, "E3071", {"start": v(5.78, -2.96) * mm, "end": v(5.9, -3) * mm});
            skLineSegment(sketch, "E3072", {"start": v(5.9, -3) * mm, "end": v(6, -3.03) * mm});
            skLineSegment(sketch, "E3073", {"start": v(6, -3.03) * mm, "end": v(6.13, -3.07) * mm});
            skLineSegment(sketch, "E3074", {"start": v(6.13, -3.07) * mm, "end": v(6.25, -3.13) * mm});
            skLineSegment(sketch, "E3075", {"start": v(6.25, -3.13) * mm, "end": v(6.37, -3.2) * mm});
            skLineSegment(sketch, "E3076", {"start": v(6.37, -3.2) * mm, "end": v(6.5, -3.3) * mm});
            skLineSegment(sketch, "E3077", {"start": v(6.5, -3.3) * mm, "end": v(6.63, -3.45) * mm});
            skLineSegment(sketch, "E3078", {"start": v(6.63, -3.45) * mm, "end": v(6.72, -3.59) * mm});
            skLineSegment(sketch, "E3079", {"start": v(6.72, -3.59) * mm, "end": v(6.79, -3.71) * mm});
            skLineSegment(sketch, "E3080", {"start": v(6.79, -3.71) * mm, "end": v(6.83, -3.83) * mm});
            skLineSegment(sketch, "E3081", {"start": v(6.83, -3.83) * mm, "end": v(6.88, -4.04) * mm});
            skLineSegment(sketch, "E3082", {"start": v(6.88, -4.04) * mm, "end": v(6.94, -4.24) * mm});
            skLineSegment(sketch, "E3083", {"start": v(6.94, -4.24) * mm, "end": v(7.26, -4.32) * mm});
            skLineSegment(sketch, "E3084", {"start": v(7.26, -4.32) * mm, "end": v(7.56, -4.38) * mm});
            skLineSegment(sketch, "E3085", {"start": v(7.56, -4.38) * mm, "end": v(7.82, -4.43) * mm});
            skLineSegment(sketch, "E3086", {"start": v(7.82, -4.43) * mm, "end": v(8.06, -4.5) * mm});
            skLineSegment(sketch, "E3087", {"start": v(8.06, -4.5) * mm, "end": v(8.26, -4.59) * mm});
            skLineSegment(sketch, "E3088", {"start": v(8.26, -4.59) * mm, "end": v(8.43, -4.72) * mm});
            skLineSegment(sketch, "E3089", {"start": v(8.43, -4.72) * mm, "end": v(8.56, -4.92) * mm});
            skLineSegment(sketch, "E3090", {"start": v(8.56, -4.92) * mm, "end": v(8.66, -5.19) * mm});
            skLineSegment(sketch, "E3091", {"start": v(8.66, -5.19) * mm, "end": v(8.7, -5.46) * mm});
            skLineSegment(sketch, "E3092", {"start": v(8.7, -5.46) * mm, "end": v(8.68, -5.76) * mm});
            skLineSegment(sketch, "E3093", {"start": v(8.68, -5.76) * mm, "end": v(8.64, -6.07) * mm});
            skLineSegment(sketch, "E3094", {"start": v(8.64, -6.07) * mm, "end": v(8.56, -6.38) * mm});
            skLineSegment(sketch, "E3095", {"start": v(8.56, -6.38) * mm, "end": v(8.47, -6.67) * mm});
            skLineSegment(sketch, "E3096", {"start": v(8.47, -6.67) * mm, "end": v(8.36, -6.93) * mm});
            skLineSegment(sketch, "E3097", {"start": v(8.36, -6.93) * mm, "end": v(8.25, -7.14) * mm});
            skLineSegment(sketch, "E3098", {"start": v(8.25, -7.14) * mm, "end": v(8.15, -7.27) * mm});
            skLineSegment(sketch, "E3099", {"start": v(8.15, -7.27) * mm, "end": v(8.1, -7.09) * mm});
            skLineSegment(sketch, "E3100", {"start": v(8.1, -7.09) * mm, "end": v(8.02, -6.8) * mm});
            skLineSegment(sketch, "E3101", {"start": v(8.02, -6.8) * mm, "end": v(7.95, -6.66) * mm});
            skLineSegment(sketch, "E3102", {"start": v(7.95, -6.66) * mm, "end": v(7.86, -6.54) * mm});
            skLineSegment(sketch, "E3103", {"start": v(7.86, -6.54) * mm, "end": v(7.74, -6.44) * mm});
            skLineSegment(sketch, "E3104", {"start": v(7.74, -6.44) * mm, "end": v(7.6, -6.38) * mm});
            skLineSegment(sketch, "E3105", {"start": v(7.6, -6.38) * mm, "end": v(7.47, -6.37) * mm});
            skLineSegment(sketch, "E3106", {"start": v(7.47, -6.37) * mm, "end": v(7.32, -6.37) * mm});
            skLineSegment(sketch, "E3107", {"start": v(7.32, -6.37) * mm, "end": v(7.14, -6.39) * mm});
            skLineSegment(sketch, "E3108", {"start": v(7.14, -6.39) * mm, "end": v(6.96, -6.41) * mm});
            skLineSegment(sketch, "E3109", {"start": v(6.96, -6.41) * mm, "end": v(6.78, -6.44) * mm});
            skLineSegment(sketch, "E3110", {"start": v(6.78, -6.44) * mm, "end": v(6.62, -6.48) * mm});
            skLineSegment(sketch, "E3111", {"start": v(6.62, -6.48) * mm, "end": v(6.48, -6.52) * mm});
            skLineSegment(sketch, "E3112", {"start": v(6.48, -6.52) * mm, "end": v(6.37, -6.56) * mm});
            skLineSegment(sketch, "E3113", {"start": v(6.37, -6.56) * mm, "end": v(6.53, -6.64) * mm});
            skLineSegment(sketch, "E3114", {"start": v(6.53, -6.64) * mm, "end": v(6.65, -6.7) * mm});
            skLineSegment(sketch, "E3115", {"start": v(6.65, -6.7) * mm, "end": v(6.77, -6.73) * mm});
            skLineSegment(sketch, "E3116", {"start": v(6.77, -6.73) * mm, "end": v(6.87, -6.75) * mm});
            skLineSegment(sketch, "E3117", {"start": v(6.87, -6.75) * mm, "end": v(6.99, -6.75) * mm});
            skLineSegment(sketch, "E3118", {"start": v(6.99, -6.75) * mm, "end": v(7.1, -6.73) * mm});
            skLineSegment(sketch, "E3119", {"start": v(7.1, -6.73) * mm, "end": v(7.26, -6.7) * mm});
            skLineSegment(sketch, "E3120", {"start": v(7.26, -6.7) * mm, "end": v(7.44, -6.67) * mm});
            skLineSegment(sketch, "E3121", {"start": v(7.44, -6.67) * mm, "end": v(7.42, -6.92) * mm});
            skLineSegment(sketch, "E3122", {"start": v(7.42, -6.92) * mm, "end": v(7.39, -7.13) * mm});
            skLineSegment(sketch, "E3123", {"start": v(7.39, -7.13) * mm, "end": v(7.34, -7.34) * mm});
            skLineSegment(sketch, "E3124", {"start": v(7.34, -7.34) * mm, "end": v(7.29, -7.56) * mm});
            skLineSegment(sketch, "E3125", {"start": v(7.29, -7.56) * mm, "end": v(7.83, -7.7) * mm});
            skLineSegment(sketch, "E3126", {"start": v(7.83, -7.7) * mm, "end": v(8.4, -7.78) * mm});
            skLineSegment(sketch, "E3127", {"start": v(8.4, -7.78) * mm, "end": v(8.95, -7.77) * mm});
            skLineSegment(sketch, "E3128", {"start": v(8.95, -7.77) * mm, "end": v(9.49, -7.67) * mm});
            skLineSegment(sketch, "E3129", {"start": v(9.49, -7.67) * mm, "end": v(9.99, -7.47) * mm});
            skLineSegment(sketch, "E3130", {"start": v(9.99, -7.47) * mm, "end": v(10.42, -7.17) * mm});
            skLineSegment(sketch, "E3131", {"start": v(10.42, -7.17) * mm, "end": v(10.78, -6.76) * mm});
            skLineSegment(sketch, "E3132", {"start": v(10.78, -6.76) * mm, "end": v(11.03, -6.23) * mm});
            skLineSegment(sketch, "E3133", {"start": v(11.03, -6.23) * mm, "end": v(10.75, -6.27) * mm});
            skLineSegment(sketch, "E3134", {"start": v(10.75, -6.27) * mm, "end": v(10.48, -6.3) * mm});
            skLineSegment(sketch, "E3135", {"start": v(10.48, -6.3) * mm, "end": v(10.34, -6.31) * mm});
            skLineSegment(sketch, "E3136", {"start": v(10.34, -6.31) * mm, "end": v(10.2, -6.32) * mm});
            skLineSegment(sketch, "E3137", {"start": v(10.2, -6.32) * mm, "end": v(10.06, -6.32) * mm});
            skLineSegment(sketch, "E3138", {"start": v(10.06, -6.32) * mm, "end": v(9.9, -6.32) * mm});
            skLineSegment(sketch, "E3139", {"start": v(9.9, -6.32) * mm, "end": v(9.76, -6.31) * mm});
            skLineSegment(sketch, "E3140", {"start": v(9.76, -6.31) * mm, "end": v(9.61, -6.3) * mm});
            skLineSegment(sketch, "E3141", {"start": v(9.61, -6.3) * mm, "end": v(9.47, -6.3) * mm});
            skLineSegment(sketch, "E3142", {"start": v(9.47, -6.3) * mm, "end": v(9.33, -6.29) * mm});
            skLineSegment(sketch, "E3143", {"start": v(9.33, -6.29) * mm, "end": v(9.22, -6.27) * mm});
            skLineSegment(sketch, "E3144", {"start": v(9.22, -6.27) * mm, "end": v(9.1, -6.24) * mm});
            skLineSegment(sketch, "E3145", {"start": v(9.1, -6.24) * mm, "end": v(8.99, -6.22) * mm});
            skLineSegment(sketch, "E3146", {"start": v(8.99, -6.22) * mm, "end": v(8.87, -6.22) * mm});
            skLineSegment(sketch, "E3147", {"start": v(8.87, -6.22) * mm, "end": v(9.44, -6.16) * mm});
            skLineSegment(sketch, "E3148", {"start": v(9.44, -6.16) * mm, "end": v(9.98, -6.1) * mm});
            skLineSegment(sketch, "E3149", {"start": v(9.98, -6.1) * mm, "end": v(10.47, -5.98) * mm});
            skLineSegment(sketch, "E3150", {"start": v(10.47, -5.98) * mm, "end": v(10.9, -5.82) * mm});
            skLineSegment(sketch, "E3151", {"start": v(10.9, -5.82) * mm, "end": v(11.22, -5.58) * mm});
            skLineSegment(sketch, "E3152", {"start": v(11.22, -5.58) * mm, "end": v(11.43, -5.24) * mm});
            skLineSegment(sketch, "E3153", {"start": v(11.43, -5.24) * mm, "end": v(11.51, -4.79) * mm});
            skLineSegment(sketch, "E3154", {"start": v(11.51, -4.79) * mm, "end": v(11.44, -4.2) * mm});
            skLineSegment(sketch, "E3155", {"start": v(11.44, -4.2) * mm, "end": v(11.28, -4.25) * mm});
            skLineSegment(sketch, "E3156", {"start": v(11.28, -4.25) * mm, "end": v(11.04, -4.35) * mm});
            skLineSegment(sketch, "E3157", {"start": v(11.04, -4.35) * mm, "end": v(10.9, -4.4) * mm});
            skLineSegment(sketch, "E3158", {"start": v(10.9, -4.4) * mm, "end": v(10.71, -4.47) * mm});
            skLineSegment(sketch, "E3159", {"start": v(10.71, -4.47) * mm, "end": v(10.5, -4.53) * mm});
            skLineSegment(sketch, "E3160", {"start": v(10.5, -4.53) * mm, "end": v(10.26, -4.6) * mm});
            skLineSegment(sketch, "E3161", {"start": v(10.26, -4.6) * mm, "end": v(10.1, -4.63) * mm});
            skLineSegment(sketch, "E3162", {"start": v(10.1, -4.63) * mm, "end": v(9.91, -4.66) * mm});
            skLineSegment(sketch, "E3163", {"start": v(9.91, -4.66) * mm, "end": v(9.72, -4.68) * mm});
            skLineSegment(sketch, "E3164", {"start": v(9.72, -4.68) * mm, "end": v(9.52, -4.7) * mm});
            skLineSegment(sketch, "E3165", {"start": v(9.52, -4.7) * mm, "end": v(9.32, -4.7) * mm});
            skLineSegment(sketch, "E3166", {"start": v(9.32, -4.7) * mm, "end": v(9.13, -4.71) * mm});
            skLineSegment(sketch, "E3167", {"start": v(9.13, -4.71) * mm, "end": v(8.94, -4.71) * mm});
            skLineSegment(sketch, "E3168", {"start": v(8.94, -4.71) * mm, "end": v(8.77, -4.7) * mm});
            skLineSegment(sketch, "E3169", {"start": v(8.77, -4.7) * mm, "end": v(8.86, -4.66) * mm});
            skLineSegment(sketch, "E3170", {"start": v(8.86, -4.66) * mm, "end": v(8.98, -4.62) * mm});
            skLineSegment(sketch, "E3171", {"start": v(8.98, -4.62) * mm, "end": v(9.12, -4.58) * mm});
            skLineSegment(sketch, "E3172", {"start": v(9.12, -4.58) * mm, "end": v(9.28, -4.54) * mm});
            skLineSegment(sketch, "E3173", {"start": v(9.28, -4.54) * mm, "end": v(9.61, -4.48) * mm});
            skLineSegment(sketch, "E3174", {"start": v(9.61, -4.48) * mm, "end": v(9.87, -4.42) * mm});
            skLineSegment(sketch, "E3175", {"start": v(9.87, -4.42) * mm, "end": v(10.23, -4.3) * mm});
            skLineSegment(sketch, "E3176", {"start": v(10.23, -4.3) * mm, "end": v(10.6, -4.18) * mm});
            skLineSegment(sketch, "E3177", {"start": v(10.6, -4.18) * mm, "end": v(10.97, -4.02) * mm});
            skLineSegment(sketch, "E3178", {"start": v(10.97, -4.02) * mm, "end": v(11.32, -3.83) * mm});
            skLineSegment(sketch, "E3179", {"start": v(11.32, -3.83) * mm, "end": v(11.62, -3.6) * mm});
            skLineSegment(sketch, "E3180", {"start": v(11.62, -3.6) * mm, "end": v(11.87, -3.31) * mm});
            skLineSegment(sketch, "E3181", {"start": v(11.87, -3.31) * mm, "end": v(12.03, -2.97) * mm});
            skLineSegment(sketch, "E3182", {"start": v(12.03, -2.97) * mm, "end": v(12.1, -2.57) * mm});
            skLineSegment(sketch, "E3183", {"start": v(12.1, -2.57) * mm, "end": v(11.48, -2.84) * mm});
            skLineSegment(sketch, "E3184", {"start": v(11.48, -2.84) * mm, "end": v(10.94, -3) * mm});
            skLineSegment(sketch, "E3185", {"start": v(10.94, -3) * mm, "end": v(10.5, -3.08) * mm});
            skLineSegment(sketch, "E3186", {"start": v(10.5, -3.08) * mm, "end": v(10.11, -3.1) * mm});
            skLineSegment(sketch, "E3187", {"start": v(10.11, -3.1) * mm, "end": v(9.8, -3.1) * mm});
            skLineSegment(sketch, "E3188", {"start": v(9.8, -3.1) * mm, "end": v(9.56, -3.1) * mm});
            skLineSegment(sketch, "E3189", {"start": v(9.56, -3.1) * mm, "end": v(9.36, -3.14) * mm});
            skLineSegment(sketch, "E3190", {"start": v(9.36, -3.14) * mm, "end": v(9.21, -3.22) * mm});
            skLineSegment(sketch, "E3191", {"start": v(9.21, -3.22) * mm, "end": v(9.06, -3.34) * mm});
            skLineSegment(sketch, "E3192", {"start": v(9.06, -3.34) * mm, "end": v(8.9, -3.45) * mm});
            skLineSegment(sketch, "E3193", {"start": v(8.9, -3.45) * mm, "end": v(8.73, -3.55) * mm});
            skLineSegment(sketch, "E3194", {"start": v(8.73, -3.55) * mm, "end": v(8.55, -3.64) * mm});
            skLineSegment(sketch, "E3195", {"start": v(8.55, -3.64) * mm, "end": v(8.37, -3.71) * mm});
            skLineSegment(sketch, "E3196", {"start": v(8.37, -3.71) * mm, "end": v(8.18, -3.78) * mm});
            skLineSegment(sketch, "E3197", {"start": v(8.18, -3.78) * mm, "end": v(7.99, -3.84) * mm});
            skLineSegment(sketch, "E3198", {"start": v(7.99, -3.84) * mm, "end": v(7.8, -3.88) * mm});
            skLineSegment(sketch, "E3199", {"start": v(7.8, -3.88) * mm, "end": v(8.02, -3.76) * mm});
            skLineSegment(sketch, "E3200", {"start": v(8.02, -3.76) * mm, "end": v(8.28, -3.6) * mm});
            skLineSegment(sketch, "E3201", {"start": v(8.28, -3.6) * mm, "end": v(8.56, -3.4) * mm});
            skLineSegment(sketch, "E3202", {"start": v(8.56, -3.4) * mm, "end": v(8.85, -3.17) * mm});
            skLineSegment(sketch, "E3203", {"start": v(8.85, -3.17) * mm, "end": v(9.11, -2.93) * mm});
            skLineSegment(sketch, "E3204", {"start": v(9.11, -2.93) * mm, "end": v(9.34, -2.69) * mm});
            skLineSegment(sketch, "E3205", {"start": v(9.34, -2.69) * mm, "end": v(9.5, -2.44) * mm});
            skLineSegment(sketch, "E3206", {"start": v(9.5, -2.44) * mm, "end": v(9.59, -2.21) * mm});
            skLineSegment(sketch, "E3207", {"start": v(9.59, -2.21) * mm, "end": v(8.8, -2.33) * mm});
            skLineSegment(sketch, "E3208", {"start": v(8.8, -2.33) * mm, "end": v(8.87, -2.26) * mm});
            skLineSegment(sketch, "E3209", {"start": v(8.87, -2.26) * mm, "end": v(9.07, -2.08) * mm});
            skLineSegment(sketch, "E3210", {"start": v(9.07, -2.08) * mm, "end": v(9.32, -1.87) * mm});
            skLineSegment(sketch, "E3211", {"start": v(9.32, -1.87) * mm, "end": v(9.52, -1.7) * mm});
            skLineSegment(sketch, "E3212", {"start": v(9.52, -1.7) * mm, "end": v(9.7, -1.52) * mm});
            skLineSegment(sketch, "E3213", {"start": v(9.7, -1.52) * mm, "end": v(9.88, -1.32) * mm});
            skLineSegment(sketch, "E3214", {"start": v(9.88, -1.32) * mm, "end": v(10.04, -1.11) * mm});
            skLineSegment(sketch, "E3215", {"start": v(10.04, -1.11) * mm, "end": v(10.17, -0.88) * mm});
            skLineSegment(sketch, "E3216", {"start": v(10.17, -0.88) * mm, "end": v(10.28, -0.63) * mm});
            skLineSegment(sketch, "E3217", {"start": v(10.28, -0.63) * mm, "end": v(10.37, -0.37) * mm});
            skLineSegment(sketch, "E3218", {"start": v(10.37, -0.37) * mm, "end": v(10.41, -0.09) * mm});
            skLineSegment(sketch, "E3219", {"start": v(10.41, -0.09) * mm, "end": v(10.2, -0.17) * mm});
            skLineSegment(sketch, "E3220", {"start": v(10.2, -0.17) * mm, "end": v(9.98, -0.27) * mm});
            skLineSegment(sketch, "E3221", {"start": v(9.98, -0.27) * mm, "end": v(9.77, -0.37) * mm});
            skLineSegment(sketch, "E3222", {"start": v(9.77, -0.37) * mm, "end": v(9.55, -0.47) * mm});
            skLineSegment(sketch, "E3223", {"start": v(9.55, -0.47) * mm, "end": v(9.43, -0.52) * mm});
            skLineSegment(sketch, "E3224", {"start": v(9.43, -0.52) * mm, "end": v(9.34, -0.56) * mm});
            skLineSegment(sketch, "E3225", {"start": v(9.34, -0.56) * mm, "end": v(9.31, -0.58) * mm});
            skLineSegment(sketch, "E3226", {"start": v(9.31, -0.58) * mm, "end": v(9.28, -0.62) * mm});
            skLineSegment(sketch, "E3227", {"start": v(9.28, -0.62) * mm, "end": v(9.25, -0.66) * mm});
            skLineSegment(sketch, "E3228", {"start": v(9.25, -0.66) * mm, "end": v(9.22, -0.72) * mm});
            skLineSegment(sketch, "E3229", {"start": v(9.22, -0.72) * mm, "end": v(9.03, -1.1) * mm});
            skLineSegment(sketch, "E3230", {"start": v(9.03, -1.1) * mm, "end": v(8.83, -1.38) * mm});
            skLineSegment(sketch, "E3231", {"start": v(8.83, -1.38) * mm, "end": v(8.63, -1.6) * mm});
            skLineSegment(sketch, "E3232", {"start": v(8.63, -1.6) * mm, "end": v(8.43, -1.78) * mm});
            skLineSegment(sketch, "E3233", {"start": v(8.43, -1.78) * mm, "end": v(8.24, -1.92) * mm});
            skLineSegment(sketch, "E3234", {"start": v(8.24, -1.92) * mm, "end": v(8.06, -2.03) * mm});
            skLineSegment(sketch, "E3235", {"start": v(8.06, -2.03) * mm, "end": v(7.9, -2.14) * mm});
            skLineSegment(sketch, "E3236", {"start": v(7.9, -2.14) * mm, "end": v(7.78, -2.24) * mm});
            skLineSegment(sketch, "E3237", {"start": v(7.78, -2.24) * mm, "end": v(8.55, -2.25) * mm});
            skLineSegment(sketch, "E3238", {"start": v(8.55, -2.25) * mm, "end": v(8.48, -2.37) * mm});
            skLineSegment(sketch, "E3239", {"start": v(8.48, -2.37) * mm, "end": v(8.42, -2.47) * mm});
            skLineSegment(sketch, "E3240", {"start": v(8.42, -2.47) * mm, "end": v(8.35, -2.57) * mm});
            skLineSegment(sketch, "E3241", {"start": v(8.35, -2.57) * mm, "end": v(8.25, -2.67) * mm});
            skLineSegment(sketch, "E3242", {"start": v(8.25, -2.67) * mm, "end": v(8.13, -2.8) * mm});
            skLineSegment(sketch, "E3243", {"start": v(8.13, -2.8) * mm, "end": v(8.09, -2.85) * mm});
            skLineSegment(sketch, "E3244", {"start": v(8.09, -2.85) * mm, "end": v(8.03, -2.9) * mm});
            skLineSegment(sketch, "E3245", {"start": v(8.03, -2.9) * mm, "end": v(7.85, -3.03) * mm});
            skLineSegment(sketch, "E3246", {"start": v(7.85, -3.03) * mm, "end": v(7.76, -3.09) * mm});
            skLineSegment(sketch, "E3247", {"start": v(7.76, -3.09) * mm, "end": v(7.64, -3.16) * mm});
            skLineSegment(sketch, "E3248", {"start": v(7.64, -3.16) * mm, "end": v(7.5, -3.22) * mm});
            skLineSegment(sketch, "E3249", {"start": v(7.5, -3.22) * mm, "end": v(7.36, -3.29) * mm});
            skLineSegment(sketch, "E3250", {"start": v(7.36, -3.29) * mm, "end": v(7.21, -3.35) * mm});
            skLineSegment(sketch, "E3251", {"start": v(7.21, -3.35) * mm, "end": v(7.06, -3.4) * mm});
            skLineSegment(sketch, "E3252", {"start": v(7.06, -3.4) * mm, "end": v(6.92, -3.42) * mm});
            skLineSegment(sketch, "E3253", {"start": v(6.92, -3.42) * mm, "end": v(6.78, -3.44) * mm});
            skLineSegment(sketch, "E3254", {"start": v(6.78, -3.44) * mm, "end": v(7.06, -3.28) * mm});
            skLineSegment(sketch, "E3255", {"start": v(7.06, -3.28) * mm, "end": v(7.34, -3.12) * mm});
            skLineSegment(sketch, "E3256", {"start": v(7.34, -3.12) * mm, "end": v(7.48, -3.04) * mm});
            skLineSegment(sketch, "E3257", {"start": v(7.48, -3.04) * mm, "end": v(7.61, -2.94) * mm});
            skLineSegment(sketch, "E3258", {"start": v(7.61, -2.94) * mm, "end": v(7.74, -2.85) * mm});
            skLineSegment(sketch, "E3259", {"start": v(7.74, -2.85) * mm, "end": v(7.85, -2.73) * mm});
            skLineSegment(sketch, "E3260", {"start": v(7.85, -2.73) * mm, "end": v(7.93, -2.66) * mm});
            skLineSegment(sketch, "E3261", {"start": v(7.93, -2.66) * mm, "end": v(8, -2.59) * mm});
            skLineSegment(sketch, "E3262", {"start": v(8, -2.59) * mm, "end": v(8.03, -2.55) * mm});
            skLineSegment(sketch, "E3263", {"start": v(8.03, -2.55) * mm, "end": v(8.06, -2.5) * mm});
            skLineSegment(sketch, "E3264", {"start": v(8.06, -2.5) * mm, "end": v(8.08, -2.45) * mm});
            skLineSegment(sketch, "E3265", {"start": v(8.08, -2.45) * mm, "end": v(8.1, -2.4) * mm});
            skLineSegment(sketch, "E3266", {"start": v(8.1, -2.4) * mm, "end": v(7.73, -2.39) * mm});
            skLineSegment(sketch, "E3267", {"start": v(7.73, -2.39) * mm, "end": v(7.48, -2.39) * mm});
            skLineSegment(sketch, "E3268", {"start": v(7.48, -2.39) * mm, "end": v(7.33, -2.4) * mm});
            skLineSegment(sketch, "E3269", {"start": v(7.33, -2.4) * mm, "end": v(7.23, -2.45) * mm});
            skLineSegment(sketch, "E3270", {"start": v(7.23, -2.45) * mm, "end": v(7.14, -2.52) * mm});
            skLineSegment(sketch, "E3271", {"start": v(7.14, -2.52) * mm, "end": v(7.04, -2.64) * mm});
            skLineSegment(sketch, "E3272", {"start": v(7.04, -2.64) * mm, "end": v(6.88, -2.8) * mm});
            skLineSegment(sketch, "E3273", {"start": v(6.88, -2.8) * mm, "end": v(6.63, -3.01) * mm});
            skLineSegment(sketch, "E3274", {"start": v(6.63, -3.01) * mm, "end": v(7.07, -2.36) * mm});
            skLineSegment(sketch, "E3275", {"start": v(7.07, -2.36) * mm, "end": v(7.18, -2.2) * mm});
            skLineSegment(sketch, "E3276", {"start": v(7.18, -2.2) * mm, "end": v(7.27, -2.01) * mm});
            skLineSegment(sketch, "E3277", {"start": v(7.27, -2.01) * mm, "end": v(7.32, -1.92) * mm});
            skLineSegment(sketch, "E3278", {"start": v(7.32, -1.92) * mm, "end": v(7.36, -1.82) * mm});
            skLineSegment(sketch, "E3279", {"start": v(7.36, -1.82) * mm, "end": v(7.39, -1.7) * mm});
            skLineSegment(sketch, "E3280", {"start": v(7.39, -1.7) * mm, "end": v(7.42, -1.59) * mm});
            skLineSegment(sketch, "E3281", {"start": v(7.42, -1.59) * mm, "end": v(6.69, -1.74) * mm});
            skLineSegment(sketch, "E3282", {"start": v(6.69, -1.74) * mm, "end": v(6.77, -1.62) * mm});
            skLineSegment(sketch, "E3283", {"start": v(6.77, -1.62) * mm, "end": v(6.9, -1.48) * mm});
            skLineSegment(sketch, "E3284", {"start": v(6.9, -1.48) * mm, "end": v(7.07, -1.3) * mm});
            skLineSegment(sketch, "E3285", {"start": v(7.07, -1.3) * mm, "end": v(7.24, -1.11) * mm});
            skLineSegment(sketch, "E3286", {"start": v(7.24, -1.11) * mm, "end": v(7.43, -0.9) * mm});
            skLineSegment(sketch, "E3287", {"start": v(7.43, -0.9) * mm, "end": v(7.6, -0.63) * mm});
            skLineSegment(sketch, "E3288", {"start": v(7.6, -0.63) * mm, "end": v(7.74, -0.34) * mm});
            skLineSegment(sketch, "E3289", {"start": v(7.74, -0.34) * mm, "end": v(7.84, 0) * mm});
            skLineSegment(sketch, "E3290", {"start": v(7.84, 0) * mm, "end": v(7.78, 0) * mm});
            skLineSegment(sketch, "E3291", {"start": v(7.78, 0) * mm, "end": v(7.71, -0.02) * mm});
            skLineSegment(sketch, "E3292", {"start": v(7.71, -0.02) * mm, "end": v(7.64, -0.05) * mm});
            skLineSegment(sketch, "E3293", {"start": v(7.64, -0.05) * mm, "end": v(7.56, -0.08) * mm});
            skLineSegment(sketch, "E3294", {"start": v(7.56, -0.08) * mm, "end": v(7.41, -0.14) * mm});
            skLineSegment(sketch, "E3295", {"start": v(7.41, -0.14) * mm, "end": v(7.27, -0.19) * mm});
            skLineSegment(sketch, "E3296", {"start": v(7.27, -0.19) * mm, "end": v(7.12, -0.24) * mm});
            skLineSegment(sketch, "E3297", {"start": v(7.12, -0.24) * mm, "end": v(6.97, -0.29) * mm});
            skLineSegment(sketch, "E3298", {"start": v(6.97, -0.29) * mm, "end": v(6.82, -0.33) * mm});
            skLineSegment(sketch, "E3299", {"start": v(6.82, -0.33) * mm, "end": v(6.67, -0.37) * mm});
            skLineSegment(sketch, "E3300", {"start": v(6.67, -0.37) * mm, "end": v(6.88, -0.13) * mm});
            skLineSegment(sketch, "E3301", {"start": v(6.88, -0.13) * mm, "end": v(7.05, 0.07) * mm});
            skLineSegment(sketch, "E3302", {"start": v(7.05, 0.07) * mm, "end": v(7.14, 0.17) * mm});
            skLineSegment(sketch, "E3303", {"start": v(7.14, 0.17) * mm, "end": v(7.22, 0.28) * mm});
            skLineSegment(sketch, "E3304", {"start": v(7.22, 0.28) * mm, "end": v(7.3, 0.4) * mm});
            skLineSegment(sketch, "E3305", {"start": v(7.3, 0.4) * mm, "end": v(7.37, 0.55) * mm});
            skLineSegment(sketch, "E3306", {"start": v(7.37, 0.55) * mm, "end": v(7.43, 0.69) * mm});
            skLineSegment(sketch, "E3307", {"start": v(7.43, 0.69) * mm, "end": v(7.48, 0.84) * mm});
            skLineSegment(sketch, "E3308", {"start": v(7.48, 0.84) * mm, "end": v(7.53, 1) * mm});
            skLineSegment(sketch, "E3309", {"start": v(7.53, 1) * mm, "end": v(7.57, 1.18) * mm});
            skLineSegment(sketch, "E3310", {"start": v(7.57, 1.18) * mm, "end": v(7.59, 1.36) * mm});
            skLineSegment(sketch, "E3311", {"start": v(7.59, 1.36) * mm, "end": v(7.58, 1.53) * mm});
            skLineSegment(sketch, "E3312", {"start": v(7.58, 1.53) * mm, "end": v(7.55, 1.69) * mm});
            skLineSegment(sketch, "E3313", {"start": v(7.55, 1.69) * mm, "end": v(7.48, 1.84) * mm});
            skLineSegment(sketch, "E3314", {"start": v(7.48, 1.84) * mm, "end": v(7.38, 1.74) * mm});
            skLineSegment(sketch, "E3315", {"start": v(7.38, 1.74) * mm, "end": v(7.27, 1.66) * mm});
            skLineSegment(sketch, "E3316", {"start": v(7.27, 1.66) * mm, "end": v(7.15, 1.57) * mm});
            skLineSegment(sketch, "E3317", {"start": v(7.15, 1.57) * mm, "end": v(7.03, 1.5) * mm});
            skLineSegment(sketch, "E3318", {"start": v(7.03, 1.5) * mm, "end": v(6.9, 1.42) * mm});
            skLineSegment(sketch, "E3319", {"start": v(6.9, 1.42) * mm, "end": v(6.75, 1.35) * mm});
            skLineSegment(sketch, "E3320", {"start": v(6.75, 1.35) * mm, "end": v(6.6, 1.28) * mm});
            skLineSegment(sketch, "E3321", {"start": v(6.6, 1.28) * mm, "end": v(6.43, 1.22) * mm});
            skLineSegment(sketch, "E3322", {"start": v(6.43, 1.22) * mm, "end": v(6.5, 1.31) * mm});
            skLineSegment(sketch, "E3323", {"start": v(6.5, 1.31) * mm, "end": v(6.56, 1.4) * mm});
            skLineSegment(sketch, "E3324", {"start": v(6.56, 1.4) * mm, "end": v(6.64, 1.48) * mm});
            skLineSegment(sketch, "E3325", {"start": v(6.64, 1.48) * mm, "end": v(6.7, 1.58) * mm});
            skLineSegment(sketch, "E3326", {"start": v(6.7, 1.58) * mm, "end": v(6.82, 1.76) * mm});
            skLineSegment(sketch, "E3327", {"start": v(6.82, 1.76) * mm, "end": v(6.9, 1.93) * mm});
            skLineSegment(sketch, "E3328", {"start": v(6.9, 1.93) * mm, "end": v(6.98, 2.1) * mm});
            skLineSegment(sketch, "E3329", {"start": v(6.98, 2.1) * mm, "end": v(7.04, 2.27) * mm});
            skLineSegment(sketch, "E3330", {"start": v(7.04, 2.27) * mm, "end": v(7.09, 2.44) * mm});
            skLineSegment(sketch, "E3331", {"start": v(7.09, 2.44) * mm, "end": v(7.11, 2.63) * mm});
            skLineSegment(sketch, "E3332", {"start": v(7.11, 2.63) * mm, "end": v(7.12, 2.84) * mm});
            skLineSegment(sketch, "E3333", {"start": v(7.12, 2.84) * mm, "end": v(7.12, 3.07) * mm});
            skLineSegment(sketch, "E3334", {"start": v(7.12, 3.07) * mm, "end": v(6.84, 3) * mm});
            skLineSegment(sketch, "E3335", {"start": v(6.84, 3) * mm, "end": v(6.57, 2.92) * mm});
            skLineSegment(sketch, "E3336", {"start": v(6.57, 2.92) * mm, "end": v(6.43, 2.89) * mm});
            skLineSegment(sketch, "E3337", {"start": v(6.43, 2.89) * mm, "end": v(6.28, 2.85) * mm});
            skLineSegment(sketch, "E3338", {"start": v(6.28, 2.85) * mm, "end": v(6.13, 2.82) * mm});
            skLineSegment(sketch, "E3339", {"start": v(6.13, 2.82) * mm, "end": v(5.97, 2.8) * mm});
            skLineSegment(sketch, "E3340", {"start": v(5.97, 2.8) * mm, "end": v(6.2, 2.93) * mm});
            skLineSegment(sketch, "E3341", {"start": v(6.2, 2.93) * mm, "end": v(6.57, 3.13) * mm});
            skLineSegment(sketch, "E3342", {"start": v(6.57, 3.13) * mm, "end": v(6.92, 3.3) * mm});
            skLineSegment(sketch, "E3343", {"start": v(6.92, 3.3) * mm, "end": v(7.24, 3.48) * mm});
            skLineSegment(sketch, "E3344", {"start": v(7.24, 3.48) * mm, "end": v(7.55, 3.65) * mm});
            skLineSegment(sketch, "E3345", {"start": v(7.55, 3.65) * mm, "end": v(7.85, 3.83) * mm});
            skLineSegment(sketch, "E3346", {"start": v(7.85, 3.83) * mm, "end": v(8.16, 4.03) * mm});
            skLineSegment(sketch, "E3347", {"start": v(8.16, 4.03) * mm, "end": v(8.5, 4.26) * mm});
            skLineSegment(sketch, "E3348", {"start": v(8.5, 4.26) * mm, "end": v(8.85, 4.53) * mm});
            skLineSegment(sketch, "E3349", {"start": v(8.85, 4.53) * mm, "end": v(8.94, 4.6) * mm});
            skLineSegment(sketch, "E3350", {"start": v(8.94, 4.6) * mm, "end": v(9.02, 4.66) * mm});
            skLineSegment(sketch, "E3351", {"start": v(9.02, 4.66) * mm, "end": v(9.1, 4.73) * mm});
            skLineSegment(sketch, "E3352", {"start": v(9.1, 4.73) * mm, "end": v(9.19, 4.81) * mm});
            skLineSegment(sketch, "E3353", {"start": v(9.19, 4.81) * mm, "end": v(9.27, 4.9) * mm});
            skLineSegment(sketch, "E3354", {"start": v(9.27, 4.9) * mm, "end": v(9.33, 4.93) * mm});
            skLineSegment(sketch, "E3355", {"start": v(9.33, 4.93) * mm, "end": v(9.4, 4.99) * mm});
            skLineSegment(sketch, "E3356", {"start": v(9.4, 4.99) * mm, "end": v(9.54, 5.12) * mm});
            skLineSegment(sketch, "E3357", {"start": v(9.54, 5.12) * mm, "end": v(9.82, 5.43) * mm});
            skLineSegment(sketch, "E3358", {"start": v(9.82, 5.43) * mm, "end": v(10.1, 5.76) * mm});
            skLineSegment(sketch, "E3359", {"start": v(10.1, 5.76) * mm, "end": v(10.35, 6.1) * mm});
            skLineSegment(sketch, "E3360", {"start": v(10.35, 6.1) * mm, "end": v(10.58, 6.47) * mm});
            skLineSegment(sketch, "E3361", {"start": v(10.58, 6.47) * mm, "end": v(10.77, 6.86) * mm});
            skLineSegment(sketch, "E3362", {"start": v(10.77, 6.86) * mm, "end": v(10.92, 7.28) * mm});
            skLineSegment(sketch, "E3363", {"start": v(10.92, 7.28) * mm, "end": v(11, 7.72) * mm});
            skLineSegment(sketch, "E3364", {"start": v(11, 7.72) * mm, "end": v(11.03, 8.18) * mm});
            skLineSegment(sketch, "E3365", {"start": v(11.03, 8.18) * mm, "end": v(10.49, 7.64) * mm});
            skLineSegment(sketch, "E3366", {"start": v(10.49, 7.64) * mm, "end": v(10.35, 7.5) * mm});
            skLineSegment(sketch, "E3367", {"start": v(10.35, 7.5) * mm, "end": v(10.2, 7.36) * mm});
            skLineSegment(sketch, "E3368", {"start": v(10.2, 7.36) * mm, "end": v(10.04, 7.23) * mm});
            skLineSegment(sketch, "E3369", {"start": v(10.04, 7.23) * mm, "end": v(9.94, 7.16) * mm});
            skLineSegment(sketch, "E3370", {"start": v(-2.87, -3.41) * mm, "end": v(-2.67, -3.4) * mm});
            skLineSegment(sketch, "E3371", {"start": v(-2.67, -3.4) * mm, "end": v(-2.47, -3.4) * mm});
            skLineSegment(sketch, "E3372", {"start": v(-2.47, -3.4) * mm, "end": v(-2.26, -3.4) * mm});
            skLineSegment(sketch, "E3373", {"start": v(-2.26, -3.4) * mm, "end": v(-2.04, -3.4) * mm});
            skLineSegment(sketch, "E3374", {"start": v(-2.04, -3.4) * mm, "end": v(-1.83, -3.41) * mm});
            skLineSegment(sketch, "E3375", {"start": v(-1.83, -3.41) * mm, "end": v(-1.63, -3.43) * mm});
            skLineSegment(sketch, "E3376", {"start": v(-1.63, -3.43) * mm, "end": v(-1.43, -3.45) * mm});
            skLineSegment(sketch, "E3377", {"start": v(-1.43, -3.45) * mm, "end": v(-1.24, -3.49) * mm});
            skLineSegment(sketch, "E3378", {"start": v(-1.24, -3.49) * mm, "end": v(-1.08, -3.53) * mm});
            skLineSegment(sketch, "E3379", {"start": v(-1.08, -3.53) * mm, "end": v(-0.9, -3.57) * mm});
            skLineSegment(sketch, "E3380", {"start": v(-0.9, -3.57) * mm, "end": v(-0.74, -3.62) * mm});
            skLineSegment(sketch, "E3381", {"start": v(-0.74, -3.62) * mm, "end": v(-0.57, -3.67) * mm});
            skLineSegment(sketch, "E3382", {"start": v(-0.57, -3.67) * mm, "end": v(-0.4, -3.74) * mm});
            skLineSegment(sketch, "E3383", {"start": v(-0.4, -3.74) * mm, "end": v(-0.26, -3.81) * mm});
            skLineSegment(sketch, "E3384", {"start": v(-0.26, -3.81) * mm, "end": v(-0.13, -3.9) * mm});
            skLineSegment(sketch, "E3385", {"start": v(-0.13, -3.9) * mm, "end": v(-0.02, -3.98) * mm});
            skLineSegment(sketch, "E3386", {"start": v(-0.02, -3.98) * mm, "end": v(-0.29, -4.05) * mm});
            skLineSegment(sketch, "E3387", {"start": v(-0.29, -4.05) * mm, "end": v(-0.55, -4.13) * mm});
            skLineSegment(sketch, "E3388", {"start": v(-0.55, -4.13) * mm, "end": v(-0.79, -4.22) * mm});
            skLineSegment(sketch, "E3389", {"start": v(-0.79, -4.22) * mm, "end": v(-1.02, -4.33) * mm});
            skLineSegment(sketch, "E3390", {"start": v(-1.02, -4.33) * mm, "end": v(-1.23, -4.45) * mm});
            skLineSegment(sketch, "E3391", {"start": v(-1.23, -4.45) * mm, "end": v(-1.43, -4.57) * mm});
            skLineSegment(sketch, "E3392", {"start": v(-1.43, -4.57) * mm, "end": v(-1.62, -4.7) * mm});
            skLineSegment(sketch, "E3393", {"start": v(-1.62, -4.7) * mm, "end": v(-1.8, -4.83) * mm});
            skLineSegment(sketch, "E3394", {"start": v(-1.8, -4.83) * mm, "end": v(-1.93, -4.94) * mm});
            skLineSegment(sketch, "E3395", {"start": v(-1.93, -4.94) * mm, "end": v(-2.1, -5.1) * mm});
            skLineSegment(sketch, "E3396", {"start": v(-2.1, -5.1) * mm, "end": v(-2.27, -5.29) * mm});
            skLineSegment(sketch, "E3397", {"start": v(-2.27, -5.29) * mm, "end": v(-2.45, -5.5) * mm});
            skLineSegment(sketch, "E3398", {"start": v(-2.45, -5.5) * mm, "end": v(-2.62, -5.72) * mm});
            skLineSegment(sketch, "E3399", {"start": v(-2.62, -5.72) * mm, "end": v(-2.77, -5.94) * mm});
            skLineSegment(sketch, "E3400", {"start": v(-2.77, -5.94) * mm, "end": v(-2.88, -6.14) * mm});
            skLineSegment(sketch, "E3401", {"start": v(-2.88, -6.14) * mm, "end": v(-2.92, -6.3) * mm});
            skLineSegment(sketch, "E3402", {"start": v(-2.92, -6.3) * mm, "end": v(-2.63, -6.16) * mm});
            skLineSegment(sketch, "E3403", {"start": v(-2.63, -6.16) * mm, "end": v(-2.27, -6) * mm});
            skLineSegment(sketch, "E3404", {"start": v(-2.27, -6) * mm, "end": v(-1.88, -5.85) * mm});
            skLineSegment(sketch, "E3405", {"start": v(-1.88, -5.85) * mm, "end": v(-1.45, -5.7) * mm});
            skLineSegment(sketch, "E3406", {"start": v(-1.45, -5.7) * mm, "end": v(-1.01, -5.58) * mm});
            skLineSegment(sketch, "E3407", {"start": v(-1.01, -5.58) * mm, "end": v(-0.58, -5.48) * mm});
            skLineSegment(sketch, "E3408", {"start": v(-0.58, -5.48) * mm, "end": v(-0.16, -5.43) * mm});
            skLineSegment(sketch, "E3409", {"start": v(-0.16, -5.43) * mm, "end": v(0.22, -5.42) * mm});
            skLineSegment(sketch, "E3410", {"start": v(0.22, -5.42) * mm, "end": v(-0.15, -5.6) * mm});
            skLineSegment(sketch, "E3411", {"start": v(-0.15, -5.6) * mm, "end": v(-0.5, -5.85) * mm});
            skLineSegment(sketch, "E3412", {"start": v(-0.5, -5.85) * mm, "end": v(-0.82, -6.16) * mm});
            skLineSegment(sketch, "E3413", {"start": v(-0.82, -6.16) * mm, "end": v(-1.1, -6.51) * mm});
            skLineSegment(sketch, "E3414", {"start": v(-1.1, -6.51) * mm, "end": v(-1.34, -6.9) * mm});
            skLineSegment(sketch, "E3415", {"start": v(-1.34, -6.9) * mm, "end": v(-1.53, -7.3) * mm});
            skLineSegment(sketch, "E3416", {"start": v(-1.53, -7.3) * mm, "end": v(-1.67, -7.7) * mm});
            skLineSegment(sketch, "E3417", {"start": v(-1.67, -7.7) * mm, "end": v(-1.74, -8.1) * mm});
            skLineSegment(sketch, "E3418", {"start": v(-1.74, -8.1) * mm, "end": v(-1.65, -8.05) * mm});
            skLineSegment(sketch, "E3419", {"start": v(-1.65, -8.05) * mm, "end": v(-1.55, -8) * mm});
            skLineSegment(sketch, "E3420", {"start": v(-1.55, -8) * mm, "end": v(-1.44, -7.92) * mm});
            skLineSegment(sketch, "E3421", {"start": v(-1.44, -7.92) * mm, "end": v(-1.32, -7.83) * mm});
            skLineSegment(sketch, "E3422", {"start": v(-1.32, -7.83) * mm, "end": v(-1.18, -7.74) * mm});
            skLineSegment(sketch, "E3423", {"start": v(-1.18, -7.74) * mm, "end": v(-1.03, -7.64) * mm});
            skLineSegment(sketch, "E3424", {"start": v(-1.03, -7.64) * mm, "end": v(-0.86, -7.55) * mm});
            skLineSegment(sketch, "E3425", {"start": v(-0.86, -7.55) * mm, "end": v(-0.68, -7.46) * mm});
            skLineSegment(sketch, "E3426", {"start": v(-0.68, -7.46) * mm, "end": v(-0.37, -7.33) * mm});
            skLineSegment(sketch, "E3427", {"start": v(-0.37, -7.33) * mm, "end": v(-0.06, -7.22) * mm});
            skLineSegment(sketch, "E3428", {"start": v(-0.06, -7.22) * mm, "end": v(0.1, -7.17) * mm});
            skLineSegment(sketch, "E3429", {"start": v(0.1, -7.17) * mm, "end": v(0.27, -7.13) * mm});
            skLineSegment(sketch, "E3430", {"start": v(0.27, -7.13) * mm, "end": v(0.44, -7.1) * mm});
            skLineSegment(sketch, "E3431", {"start": v(0.44, -7.1) * mm, "end": v(0.61, -7.08) * mm});
            skLineSegment(sketch, "E3432", {"start": v(0.61, -7.08) * mm, "end": v(0.55, -7.27) * mm});
            skLineSegment(sketch, "E3433", {"start": v(0.55, -7.27) * mm, "end": v(0.48, -7.44) * mm});
            skLineSegment(sketch, "E3434", {"start": v(0.48, -7.44) * mm, "end": v(0.4, -7.62) * mm});
            skLineSegment(sketch, "E3435", {"start": v(0.4, -7.62) * mm, "end": v(0.34, -7.8) * mm});
            skLineSegment(sketch, "E3436", {"start": v(0.34, -7.8) * mm, "end": v(0.27, -8) * mm});
            skLineSegment(sketch, "E3437", {"start": v(0.27, -8) * mm, "end": v(0.22, -8.22) * mm});
            skLineSegment(sketch, "E3438", {"start": v(0.22, -8.22) * mm, "end": v(0.19, -8.5) * mm});
            skLineSegment(sketch, "E3439", {"start": v(0.19, -8.5) * mm, "end": v(0.18, -8.82) * mm});
            skLineSegment(sketch, "E3440", {"start": v(0.18, -8.82) * mm, "end": v(1, -7.97) * mm});
            skLineSegment(sketch, "E3441", {"start": v(1, -7.97) * mm, "end": v(1.2, -7.81) * mm});
            skLineSegment(sketch, "E3442", {"start": v(1.2, -7.81) * mm, "end": v(1.47, -7.6) * mm});
            skLineSegment(sketch, "E3443", {"start": v(1.47, -7.6) * mm, "end": v(1.62, -7.5) * mm});
            skLineSegment(sketch, "E3444", {"start": v(1.62, -7.5) * mm, "end": v(1.77, -7.41) * mm});
            skLineSegment(sketch, "E3445", {"start": v(1.77, -7.41) * mm, "end": v(1.9, -7.34) * mm});
            skLineSegment(sketch, "E3446", {"start": v(1.9, -7.34) * mm, "end": v(2.02, -7.3) * mm});
            skLineSegment(sketch, "E3447", {"start": v(2.02, -7.3) * mm, "end": v(1.95, -7.56) * mm});
            skLineSegment(sketch, "E3448", {"start": v(1.95, -7.56) * mm, "end": v(1.86, -7.81) * mm});
            skLineSegment(sketch, "E3449", {"start": v(1.86, -7.81) * mm, "end": v(1.83, -7.95) * mm});
            skLineSegment(sketch, "E3450", {"start": v(1.83, -7.95) * mm, "end": v(1.82, -8.09) * mm});
            skLineSegment(sketch, "E3451", {"start": v(1.82, -8.09) * mm, "end": v(1.83, -8.25) * mm});
            skLineSegment(sketch, "E3452", {"start": v(1.83, -8.25) * mm, "end": v(1.87, -8.43) * mm});
            skLineSegment(sketch, "E3453", {"start": v(1.87, -8.43) * mm, "end": v(1.99, -8.31) * mm});
            skLineSegment(sketch, "E3454", {"start": v(1.99, -8.31) * mm, "end": v(2.12, -8.2) * mm});
            skLineSegment(sketch, "E3455", {"start": v(2.12, -8.2) * mm, "end": v(2.26, -8.07) * mm});
            skLineSegment(sketch, "E3456", {"start": v(2.26, -8.07) * mm, "end": v(2.4, -7.95) * mm});
            skLineSegment(sketch, "E3457", {"start": v(2.4, -7.95) * mm, "end": v(2.67, -7.75) * mm});
            skLineSegment(sketch, "E3458", {"start": v(2.67, -7.75) * mm, "end": v(2.95, -7.58) * mm});
            skLineSegment(sketch, "E3459", {"start": v(2.95, -7.58) * mm, "end": v(3.24, -7.44) * mm});
            skLineSegment(sketch, "E3460", {"start": v(3.24, -7.44) * mm, "end": v(3.53, -7.34) * mm});
            skLineSegment(sketch, "E3461", {"start": v(3.53, -7.34) * mm, "end": v(3.84, -7.26) * mm});
            skLineSegment(sketch, "E3462", {"start": v(3.84, -7.26) * mm, "end": v(4.16, -7.2) * mm});
            skLineSegment(sketch, "E3463", {"start": v(4.16, -7.2) * mm, "end": v(4.5, -7.18) * mm});
            skLineSegment(sketch, "E3464", {"start": v(4.5, -7.18) * mm, "end": v(4.86, -7.17) * mm});
            skLineSegment(sketch, "E3465", {"start": v(4.86, -7.17) * mm, "end": v(4.84, -7) * mm});
            skLineSegment(sketch, "E3466", {"start": v(4.84, -7) * mm, "end": v(4.8, -6.87) * mm});
            skLineSegment(sketch, "E3467", {"start": v(4.8, -6.87) * mm, "end": v(4.76, -6.76) * mm});
            skLineSegment(sketch, "E3468", {"start": v(4.76, -6.76) * mm, "end": v(4.7, -6.66) * mm});
            skLineSegment(sketch, "E3469", {"start": v(4.7, -6.66) * mm, "end": v(4.63, -6.58) * mm});
            skLineSegment(sketch, "E3470", {"start": v(4.63, -6.58) * mm, "end": v(4.55, -6.51) * mm});
            skLineSegment(sketch, "E3471", {"start": v(4.55, -6.51) * mm, "end": v(4.46, -6.44) * mm});
            skLineSegment(sketch, "E3472", {"start": v(4.46, -6.44) * mm, "end": v(4.35, -6.36) * mm});
            skLineSegment(sketch, "E3473", {"start": v(4.35, -6.36) * mm, "end": v(4.55, -6.33) * mm});
            skLineSegment(sketch, "E3474", {"start": v(4.55, -6.33) * mm, "end": v(4.73, -6.29) * mm});
            skLineSegment(sketch, "E3475", {"start": v(4.73, -6.29) * mm, "end": v(4.91, -6.24) * mm});
            skLineSegment(sketch, "E3476", {"start": v(4.91, -6.24) * mm, "end": v(5.08, -6.19) * mm});
            skLineSegment(sketch, "E3477", {"start": v(5.08, -6.19) * mm, "end": v(5.25, -6.12) * mm});
            skLineSegment(sketch, "E3478", {"start": v(5.25, -6.12) * mm, "end": v(5.4, -6.05) * mm});
            skLineSegment(sketch, "E3479", {"start": v(5.4, -6.05) * mm, "end": v(5.55, -5.97) * mm});
            skLineSegment(sketch, "E3480", {"start": v(5.55, -5.97) * mm, "end": v(5.7, -5.87) * mm});
            skLineSegment(sketch, "E3481", {"start": v(5.7, -5.87) * mm, "end": v(5.78, -5.8) * mm});
            skLineSegment(sketch, "E3482", {"start": v(5.78, -5.8) * mm, "end": v(5.9, -5.7) * mm});
            skLineSegment(sketch, "E3483", {"start": v(5.9, -5.7) * mm, "end": v(6.02, -5.57) * mm});
            skLineSegment(sketch, "E3484", {"start": v(6.02, -5.57) * mm, "end": v(6.16, -5.43) * mm});
            skLineSegment(sketch, "E3485", {"start": v(6.16, -5.43) * mm, "end": v(6.3, -5.28) * mm});
            skLineSegment(sketch, "E3486", {"start": v(6.3, -5.28) * mm, "end": v(6.4, -5.14) * mm});
            skLineSegment(sketch, "E3487", {"start": v(6.4, -5.14) * mm, "end": v(6.5, -5.02) * mm});
            skLineSegment(sketch, "E3488", {"start": v(6.5, -5.02) * mm, "end": v(6.54, -4.92) * mm});
            skLineSegment(sketch, "E3489", {"start": v(6.54, -4.92) * mm, "end": v(6.54, -5.02) * mm});
            skLineSegment(sketch, "E3490", {"start": v(6.54, -5.02) * mm, "end": v(6.53, -5.12) * mm});
            skLineSegment(sketch, "E3491", {"start": v(6.53, -5.12) * mm, "end": v(6.5, -5.22) * mm});
            skLineSegment(sketch, "E3492", {"start": v(6.5, -5.22) * mm, "end": v(6.48, -5.3) * mm});
            skLineSegment(sketch, "E3493", {"start": v(6.48, -5.3) * mm, "end": v(6.41, -5.48) * mm});
            skLineSegment(sketch, "E3494", {"start": v(6.41, -5.48) * mm, "end": v(6.33, -5.63) * mm});
            skLineSegment(sketch, "E3495", {"start": v(6.33, -5.63) * mm, "end": v(6.27, -5.73) * mm});
            skLineSegment(sketch, "E3496", {"start": v(6.27, -5.73) * mm, "end": v(6.21, -5.8) * mm});
            skLineSegment(sketch, "E3497", {"start": v(6.21, -5.8) * mm, "end": v(6.15, -5.88) * mm});
            skLineSegment(sketch, "E3498", {"start": v(6.15, -5.88) * mm, "end": v(6.09, -5.95) * mm});
            skLineSegment(sketch, "E3499", {"start": v(6.09, -5.95) * mm, "end": v(6.03, -6.01) * mm});
            skLineSegment(sketch, "E3500", {"start": v(6.03, -6.01) * mm, "end": v(5.97, -6.07) * mm});
            skLineSegment(sketch, "E3501", {"start": v(5.97, -6.07) * mm, "end": v(5.93, -6.14) * mm});
            skLineSegment(sketch, "E3502", {"start": v(5.93, -6.14) * mm, "end": v(5.89, -6.2) * mm});
            skLineSegment(sketch, "E3503", {"start": v(5.89, -6.2) * mm, "end": v(6.17, -6.2) * mm});
            skLineSegment(sketch, "E3504", {"start": v(6.17, -6.2) * mm, "end": v(6.45, -6.16) * mm});
            skLineSegment(sketch, "E3505", {"start": v(6.45, -6.16) * mm, "end": v(6.72, -6.1) * mm});
            skLineSegment(sketch, "E3506", {"start": v(6.72, -6.1) * mm, "end": v(6.97, -6.03) * mm});
            skLineSegment(sketch, "E3507", {"start": v(6.97, -6.03) * mm, "end": v(7.22, -5.98) * mm});
            skLineSegment(sketch, "E3508", {"start": v(7.22, -5.98) * mm, "end": v(7.44, -5.96) * mm});
            skLineSegment(sketch, "E3509", {"start": v(7.44, -5.96) * mm, "end": v(7.66, -5.98) * mm});
            skLineSegment(sketch, "E3510", {"start": v(7.66, -5.98) * mm, "end": v(7.86, -6.07) * mm});
            skLineSegment(sketch, "E3511", {"start": v(7.86, -6.07) * mm, "end": v(7.93, -6.13) * mm});
            skLineSegment(sketch, "E3512", {"start": v(7.93, -6.13) * mm, "end": v(7.98, -6.18) * mm});
            skLineSegment(sketch, "E3513", {"start": v(7.98, -6.18) * mm, "end": v(8.01, -6.23) * mm});
            skLineSegment(sketch, "E3514", {"start": v(8.01, -6.23) * mm, "end": v(8.04, -6.29) * mm});
            skLineSegment(sketch, "E3515", {"start": v(8.04, -6.29) * mm, "end": v(8.06, -6.34) * mm});
            skLineSegment(sketch, "E3516", {"start": v(8.06, -6.34) * mm, "end": v(8.08, -6.4) * mm});
            skLineSegment(sketch, "E3517", {"start": v(8.08, -6.4) * mm, "end": v(8.1, -6.47) * mm});
            skLineSegment(sketch, "E3518", {"start": v(8.1, -6.47) * mm, "end": v(8.15, -6.55) * mm});
            skLineSegment(sketch, "E3519", {"start": v(8.15, -6.55) * mm, "end": v(8.2, -6.36) * mm});
            skLineSegment(sketch, "E3520", {"start": v(8.2, -6.36) * mm, "end": v(8.25, -6.14) * mm});
            skLineSegment(sketch, "E3521", {"start": v(8.25, -6.14) * mm, "end": v(8.27, -5.9) * mm});
            skLineSegment(sketch, "E3522", {"start": v(8.27, -5.9) * mm, "end": v(8.26, -5.64) * mm});
            skLineSegment(sketch, "E3523", {"start": v(8.26, -5.64) * mm, "end": v(8.23, -5.4) * mm});
            skLineSegment(sketch, "E3524", {"start": v(8.23, -5.4) * mm, "end": v(8.17, -5.2) * mm});
            skLineSegment(sketch, "E3525", {"start": v(8.17, -5.2) * mm, "end": v(8.09, -5.02) * mm});
            skLineSegment(sketch, "E3526", {"start": v(8.09, -5.02) * mm, "end": v(7.97, -4.91) * mm});
            skLineSegment(sketch, "E3527", {"start": v(7.97, -4.91) * mm, "end": v(7.83, -4.86) * mm});
            skLineSegment(sketch, "E3528", {"start": v(7.83, -4.86) * mm, "end": v(7.64, -4.82) * mm});
            skLineSegment(sketch, "E3529", {"start": v(7.64, -4.82) * mm, "end": v(7.4, -4.78) * mm});
            skLineSegment(sketch, "E3530", {"start": v(7.4, -4.78) * mm, "end": v(7.16, -4.75) * mm});
            skLineSegment(sketch, "E3531", {"start": v(7.16, -4.75) * mm, "end": v(6.9, -4.72) * mm});
            skLineSegment(sketch, "E3532", {"start": v(6.9, -4.72) * mm, "end": v(6.66, -4.67) * mm});
            skLineSegment(sketch, "E3533", {"start": v(6.66, -4.67) * mm, "end": v(6.43, -4.61) * mm});
            skLineSegment(sketch, "E3534", {"start": v(6.43, -4.61) * mm, "end": v(6.23, -4.53) * mm});
            skLineSegment(sketch, "E3535", {"start": v(6.23, -4.53) * mm, "end": v(6.3, -4.45) * mm});
            skLineSegment(sketch, "E3536", {"start": v(6.3, -4.45) * mm, "end": v(6.37, -4.38) * mm});
            skLineSegment(sketch, "E3537", {"start": v(6.37, -4.38) * mm, "end": v(6.4, -4.32) * mm});
            skLineSegment(sketch, "E3538", {"start": v(6.4, -4.32) * mm, "end": v(6.43, -4.26) * mm});
            skLineSegment(sketch, "E3539", {"start": v(6.43, -4.26) * mm, "end": v(6.44, -4.16) * mm});
            skLineSegment(sketch, "E3540", {"start": v(6.44, -4.16) * mm, "end": v(6.42, -4.04) * mm});
            skLineSegment(sketch, "E3541", {"start": v(6.42, -4.04) * mm, "end": v(6.34, -3.86) * mm});
            skLineSegment(sketch, "E3542", {"start": v(6.34, -3.86) * mm, "end": v(6.2, -3.7) * mm});
            skLineSegment(sketch, "E3543", {"start": v(6.2, -3.7) * mm, "end": v(6.01, -3.59) * mm});
            skLineSegment(sketch, "E3544", {"start": v(6.01, -3.59) * mm, "end": v(5.8, -3.5) * mm});
            skLineSegment(sketch, "E3545", {"start": v(5.8, -3.5) * mm, "end": v(5.56, -3.43) * mm});
            skLineSegment(sketch, "E3546", {"start": v(5.56, -3.43) * mm, "end": v(5.32, -3.37) * mm});
            skLineSegment(sketch, "E3547", {"start": v(5.32, -3.37) * mm, "end": v(5.1, -3.34) * mm});
            skLineSegment(sketch, "E3548", {"start": v(5.1, -3.34) * mm, "end": v(4.9, -3.31) * mm});
            skLineSegment(sketch, "E3549", {"start": v(4.9, -3.31) * mm, "end": v(3.27, -3.16) * mm});
            skLineSegment(sketch, "E3550", {"start": v(3.27, -3.16) * mm, "end": v(3.03, -3.14) * mm});
            skLineSegment(sketch, "E3551", {"start": v(3.03, -3.14) * mm, "end": v(2.77, -3.11) * mm});
            skLineSegment(sketch, "E3552", {"start": v(2.77, -3.11) * mm, "end": v(2.5, -3.07) * mm});
            skLineSegment(sketch, "E3553", {"start": v(2.5, -3.07) * mm, "end": v(2.26, -3.04) * mm});
            skLineSegment(sketch, "E3554", {"start": v(2.26, -3.04) * mm, "end": v(1.62, -2.95) * mm});
            skLineSegment(sketch, "E3555", {"start": v(1.62, -2.95) * mm, "end": v(1.03, -2.86) * mm});
            skLineSegment(sketch, "E3556", {"start": v(1.03, -2.86) * mm, "end": v(0.47, -2.8) * mm});
            skLineSegment(sketch, "E3557", {"start": v(0.47, -2.8) * mm, "end": v(-0.08, -2.76) * mm});
            skLineSegment(sketch, "E3558", {"start": v(-0.08, -2.76) * mm, "end": v(-0.62, -2.77) * mm});
            skLineSegment(sketch, "E3559", {"start": v(-0.62, -2.77) * mm, "end": v(-1.17, -2.82) * mm});
            skLineSegment(sketch, "E3560", {"start": v(-1.17, -2.82) * mm, "end": v(-1.75, -2.95) * mm});
            skLineSegment(sketch, "E3561", {"start": v(-1.75, -2.95) * mm, "end": v(-2.37, -3.14) * mm});
            skLineSegment(sketch, "E3562", {"start": v(-2.37, -3.14) * mm, "end": v(-2.87, -3.41) * mm});
            skLineSegment(sketch, "E3563", {"start": v(-18.36, 13.8) * mm, "end": v(-18.4, 13.86) * mm});
            skLineSegment(sketch, "E3564", {"start": v(-18.4, 13.86) * mm, "end": v(-18.58, 14.1) * mm});
            skLineSegment(sketch, "E3565", {"start": v(-18.58, 14.1) * mm, "end": v(-18.8, 14.43) * mm});
            skLineSegment(sketch, "E3566", {"start": v(-18.8, 14.43) * mm, "end": v(-19.04, 14.8) * mm});
            skLineSegment(sketch, "E3567", {"start": v(-19.04, 14.8) * mm, "end": v(-19.3, 15.21) * mm});
            skLineSegment(sketch, "E3568", {"start": v(-19.3, 15.21) * mm, "end": v(-19.56, 15.62) * mm});
            skLineSegment(sketch, "E3569", {"start": v(-19.56, 15.62) * mm, "end": v(-19.8, 16) * mm});
            skLineSegment(sketch, "E3570", {"start": v(-19.8, 16) * mm, "end": v(-20.02, 16.32) * mm});
            skLineSegment(sketch, "E3571", {"start": v(-20.02, 16.32) * mm, "end": v(-20.2, 16.56) * mm});
            skLineSegment(sketch, "E3572", {"start": v(-20.2, 16.56) * mm, "end": v(-20.55, 17.02) * mm});
            skLineSegment(sketch, "E3573", {"start": v(-20.55, 17.02) * mm, "end": v(-20.88, 17.47) * mm});
            skLineSegment(sketch, "E3574", {"start": v(-20.88, 17.47) * mm, "end": v(-21.19, 17.93) * mm});
            skLineSegment(sketch, "E3575", {"start": v(-21.19, 17.93) * mm, "end": v(-21.48, 18.4) * mm});
            skLineSegment(sketch, "E3576", {"start": v(-21.48, 18.4) * mm, "end": v(-21.76, 18.87) * mm});
            skLineSegment(sketch, "E3577", {"start": v(-21.76, 18.87) * mm, "end": v(-22.03, 19.36) * mm});
            skLineSegment(sketch, "E3578", {"start": v(-22.03, 19.36) * mm, "end": v(-22.29, 19.86) * mm});
            skLineSegment(sketch, "E3579", {"start": v(-22.29, 19.86) * mm, "end": v(-22.54, 20.4) * mm});
            skLineSegment(sketch, "E3580", {"start": v(-22.54, 20.4) * mm, "end": v(-23.05, 21.45) * mm});
            skLineSegment(sketch, "E3581", {"start": v(-23.05, 21.45) * mm, "end": v(-23, 20.93) * mm});
            skLineSegment(sketch, "E3582", {"start": v(-23, 20.93) * mm, "end": v(-22.9, 20.36) * mm});
            skLineSegment(sketch, "E3583", {"start": v(-22.9, 20.36) * mm, "end": v(-22.76, 19.75) * mm});
            skLineSegment(sketch, "E3584", {"start": v(-22.76, 19.75) * mm, "end": v(-22.57, 19.14) * mm});
            skLineSegment(sketch, "E3585", {"start": v(-22.57, 19.14) * mm, "end": v(-22.36, 18.53) * mm});
            skLineSegment(sketch, "E3586", {"start": v(-22.36, 18.53) * mm, "end": v(-22.14, 17.95) * mm});
            skLineSegment(sketch, "E3587", {"start": v(-22.14, 17.95) * mm, "end": v(-21.9, 17.4) * mm});
            skLineSegment(sketch, "E3588", {"start": v(-21.9, 17.4) * mm, "end": v(-21.68, 16.91) * mm});
            skLineSegment(sketch, "E3589", {"start": v(-21.68, 16.91) * mm, "end": v(-21, 15.6) * mm});
            skLineSegment(sketch, "E3590", {"start": v(-21, 15.6) * mm, "end": v(-20.73, 15.12) * mm});
            skLineSegment(sketch, "E3591", {"start": v(-20.73, 15.12) * mm, "end": v(-20.46, 14.66) * mm});
            skLineSegment(sketch, "E3592", {"start": v(-20.46, 14.66) * mm, "end": v(-20.19, 14.2) * mm});
            skLineSegment(sketch, "E3593", {"start": v(-20.19, 14.2) * mm, "end": v(-19.9, 13.75) * mm});
            skLineSegment(sketch, "E3594", {"start": v(-19.9, 13.75) * mm, "end": v(-19.6, 13.3) * mm});
            skLineSegment(sketch, "E3595", {"start": v(-19.6, 13.3) * mm, "end": v(-19.3, 12.87) * mm});
            skLineSegment(sketch, "E3596", {"start": v(-19.3, 12.87) * mm, "end": v(-18.99, 12.44) * mm});
            skLineSegment(sketch, "E3597", {"start": v(-18.99, 12.44) * mm, "end": v(-18.66, 12.02) * mm});
            skLineSegment(sketch, "E3598", {"start": v(-18.66, 12.02) * mm, "end": v(-18.47, 11.8) * mm});
            skLineSegment(sketch, "E3599", {"start": v(-18.47, 11.8) * mm, "end": v(-18.17, 11.49) * mm});
            skLineSegment(sketch, "E3600", {"start": v(-18.17, 11.49) * mm, "end": v(-18.01, 11.33) * mm});
            skLineSegment(sketch, "E3601", {"start": v(-18.01, 11.33) * mm, "end": v(-17.87, 11.2) * mm});
            skLineSegment(sketch, "E3602", {"start": v(-17.87, 11.2) * mm, "end": v(-17.75, 11.09) * mm});
            skLineSegment(sketch, "E3603", {"start": v(-17.75, 11.09) * mm, "end": v(-17.67, 11.03) * mm});
            skLineSegment(sketch, "E3604", {"start": v(-17.67, 11.03) * mm, "end": v(-17.68, 11.2) * mm});
            skLineSegment(sketch, "E3605", {"start": v(-17.68, 11.2) * mm, "end": v(-17.7, 11.36) * mm});
            skLineSegment(sketch, "E3606", {"start": v(-17.7, 11.36) * mm, "end": v(-17.74, 11.53) * mm});
            skLineSegment(sketch, "E3607", {"start": v(-17.74, 11.53) * mm, "end": v(-17.78, 11.7) * mm});
            skLineSegment(sketch, "E3608", {"start": v(-17.78, 11.7) * mm, "end": v(-17.81, 11.9) * mm});
            skLineSegment(sketch, "E3609", {"start": v(-17.81, 11.9) * mm, "end": v(-17.84, 12.09) * mm});
            skLineSegment(sketch, "E3610", {"start": v(-17.84, 12.09) * mm, "end": v(-17.86, 12.3) * mm});
            skLineSegment(sketch, "E3611", {"start": v(-17.86, 12.3) * mm, "end": v(-17.87, 12.5) * mm});
            skLineSegment(sketch, "E3612", {"start": v(-17.87, 12.5) * mm, "end": v(-17.89, 12.69) * mm});
            skLineSegment(sketch, "E3613", {"start": v(-17.89, 12.69) * mm, "end": v(-17.92, 12.9) * mm});
            skLineSegment(sketch, "E3614", {"start": v(-17.92, 12.9) * mm, "end": v(-17.94, 13.02) * mm});
            skLineSegment(sketch, "E3615", {"start": v(-17.94, 13.02) * mm, "end": v(-17.95, 13.14) * mm});
            skLineSegment(sketch, "E3616", {"start": v(-17.95, 13.14) * mm, "end": v(-17.95, 13.26) * mm});
            skLineSegment(sketch, "E3617", {"start": v(-17.95, 13.26) * mm, "end": v(-17.94, 13.38) * mm});
            skLineSegment(sketch, "E3618", {"start": v(-17.94, 13.38) * mm, "end": v(-16.93, 11.92) * mm});
            skLineSegment(sketch, "E3619", {"start": v(-16.93, 11.92) * mm, "end": v(-17.27, 13.44) * mm});
            skLineSegment(sketch, "E3620", {"start": v(-17.27, 13.44) * mm, "end": v(-17.3, 13.64) * mm});
            skLineSegment(sketch, "E3621", {"start": v(-17.3, 13.64) * mm, "end": v(-17.32, 13.86) * mm});
            skLineSegment(sketch, "E3622", {"start": v(-17.32, 13.86) * mm, "end": v(-17.34, 14.1) * mm});
            skLineSegment(sketch, "E3623", {"start": v(-17.34, 14.1) * mm, "end": v(-17.37, 14.33) * mm});
            skLineSegment(sketch, "E3624", {"start": v(-17.37, 14.33) * mm, "end": v(-17.4, 14.56) * mm});
            skLineSegment(sketch, "E3625", {"start": v(-17.4, 14.56) * mm, "end": v(-17.43, 14.78) * mm});
            skLineSegment(sketch, "E3626", {"start": v(-17.43, 14.78) * mm, "end": v(-17.48, 14.98) * mm});
            skLineSegment(sketch, "E3627", {"start": v(-17.48, 14.98) * mm, "end": v(-17.54, 15.14) * mm});
            skLineSegment(sketch, "E3628", {"start": v(-17.54, 15.14) * mm, "end": v(-17.68, 15.44) * mm});
            skLineSegment(sketch, "E3629", {"start": v(-17.68, 15.44) * mm, "end": v(-17.84, 15.77) * mm});
            skLineSegment(sketch, "E3630", {"start": v(-17.84, 15.77) * mm, "end": v(-18, 16.12) * mm});
            skLineSegment(sketch, "E3631", {"start": v(-18, 16.12) * mm, "end": v(-18.17, 16.48) * mm});
            skLineSegment(sketch, "E3632", {"start": v(-18.17, 16.48) * mm, "end": v(-18.34, 16.85) * mm});
            skLineSegment(sketch, "E3633", {"start": v(-18.34, 16.85) * mm, "end": v(-18.5, 17.2) * mm});
            skLineSegment(sketch, "E3634", {"start": v(-18.5, 17.2) * mm, "end": v(-18.64, 17.53) * mm});
            skLineSegment(sketch, "E3635", {"start": v(-18.64, 17.53) * mm, "end": v(-18.77, 17.83) * mm});
            skLineSegment(sketch, "E3636", {"start": v(-18.77, 17.83) * mm, "end": v(-19.34, 19.21) * mm});
            skLineSegment(sketch, "E3637", {"start": v(-19.34, 19.21) * mm, "end": v(-19.46, 19.5) * mm});
            skLineSegment(sketch, "E3638", {"start": v(-19.46, 19.5) * mm, "end": v(-19.6, 19.85) * mm});
            skLineSegment(sketch, "E3639", {"start": v(-19.6, 19.85) * mm, "end": v(-19.74, 20.23) * mm});
            skLineSegment(sketch, "E3640", {"start": v(-19.74, 20.23) * mm, "end": v(-19.88, 20.63) * mm});
            skLineSegment(sketch, "E3641", {"start": v(-19.88, 20.63) * mm, "end": v(-20.02, 21.03) * mm});
            skLineSegment(sketch, "E3642", {"start": v(-20.02, 21.03) * mm, "end": v(-20.15, 21.42) * mm});
            skLineSegment(sketch, "E3643", {"start": v(-20.15, 21.42) * mm, "end": v(-20.27, 21.78) * mm});
            skLineSegment(sketch, "E3644", {"start": v(-20.27, 21.78) * mm, "end": v(-20.38, 22.1) * mm});
            skLineSegment(sketch, "E3645", {"start": v(-20.38, 22.1) * mm, "end": v(-20.48, 22.45) * mm});
            skLineSegment(sketch, "E3646", {"start": v(-20.48, 22.45) * mm, "end": v(-20.6, 22.85) * mm});
            skLineSegment(sketch, "E3647", {"start": v(-20.6, 22.85) * mm, "end": v(-20.66, 23.05) * mm});
            skLineSegment(sketch, "E3648", {"start": v(-20.66, 23.05) * mm, "end": v(-20.72, 23.24) * mm});
            skLineSegment(sketch, "E3649", {"start": v(-20.72, 23.24) * mm, "end": v(-20.78, 23.4) * mm});
            skLineSegment(sketch, "E3650", {"start": v(-20.78, 23.4) * mm, "end": v(-20.84, 23.55) * mm});
            skLineSegment(sketch, "E3651", {"start": v(-20.84, 23.55) * mm, "end": v(-20.93, 22.73) * mm});
            skLineSegment(sketch, "E3652", {"start": v(-20.93, 22.73) * mm, "end": v(-20.92, 21.79) * mm});
            skLineSegment(sketch, "E3653", {"start": v(-20.92, 21.79) * mm, "end": v(-20.82, 20.76) * mm});
            skLineSegment(sketch, "E3654", {"start": v(-20.82, 20.76) * mm, "end": v(-20.65, 19.68) * mm});
            skLineSegment(sketch, "E3655", {"start": v(-20.65, 19.68) * mm, "end": v(-20.4, 18.6) * mm});
            skLineSegment(sketch, "E3656", {"start": v(-20.4, 18.6) * mm, "end": v(-20.12, 17.58) * mm});
            skLineSegment(sketch, "E3657", {"start": v(-20.12, 17.58) * mm, "end": v(-19.8, 16.63) * mm});
            skLineSegment(sketch, "E3658", {"start": v(-19.8, 16.63) * mm, "end": v(-19.44, 15.82) * mm});
            skLineSegment(sketch, "E3659", {"start": v(-19.44, 15.82) * mm, "end": v(-18.91, 14.8) * mm});
            skLineSegment(sketch, "E3660", {"start": v(-18.91, 14.8) * mm, "end": v(-18.78, 14.55) * mm});
            skLineSegment(sketch, "E3661", {"start": v(-18.78, 14.55) * mm, "end": v(-18.63, 14.3) * mm});
            skLineSegment(sketch, "E3662", {"start": v(-18.63, 14.3) * mm, "end": v(-18.5, 14.06) * mm});
            skLineSegment(sketch, "E3663", {"start": v(-18.5, 14.06) * mm, "end": v(-18.36, 13.8) * mm});
            skLineSegment(sketch, "E3664", {"start": v(16.91, 11.93) * mm, "end": v(17.68, 13) * mm});
            skLineSegment(sketch, "E3665", {"start": v(17.68, 13) * mm, "end": v(17.75, 13.1) * mm});
            skLineSegment(sketch, "E3666", {"start": v(17.75, 13.1) * mm, "end": v(17.8, 13.19) * mm});
            skLineSegment(sketch, "E3667", {"start": v(17.8, 13.19) * mm, "end": v(17.86, 13.27) * mm});
            skLineSegment(sketch, "E3668", {"start": v(17.86, 13.27) * mm, "end": v(17.94, 13.36) * mm});
            skLineSegment(sketch, "E3669", {"start": v(17.94, 13.36) * mm, "end": v(17.94, 13.17) * mm});
            skLineSegment(sketch, "E3670", {"start": v(17.94, 13.17) * mm, "end": v(17.93, 12.89) * mm});
            skLineSegment(sketch, "E3671", {"start": v(17.93, 12.89) * mm, "end": v(17.9, 12.55) * mm});
            skLineSegment(sketch, "E3672", {"start": v(17.9, 12.55) * mm, "end": v(17.86, 12.19) * mm});
            skLineSegment(sketch, "E3673", {"start": v(17.86, 12.19) * mm, "end": v(17.8, 11.82) * mm});
            skLineSegment(sketch, "E3674", {"start": v(17.8, 11.82) * mm, "end": v(17.76, 11.49) * mm});
            skLineSegment(sketch, "E3675", {"start": v(17.76, 11.49) * mm, "end": v(17.7, 11.22) * mm});
            skLineSegment(sketch, "E3676", {"start": v(17.7, 11.22) * mm, "end": v(17.66, 11.03) * mm});
            skLineSegment(sketch, "E3677", {"start": v(17.66, 11.03) * mm, "end": v(17.8, 11.12) * mm});
            skLineSegment(sketch, "E3678", {"start": v(17.8, 11.12) * mm, "end": v(17.98, 11.27) * mm});
            skLineSegment(sketch, "E3679", {"start": v(17.98, 11.27) * mm, "end": v(18.17, 11.46) * mm});
            skLineSegment(sketch, "E3680", {"start": v(18.17, 11.46) * mm, "end": v(18.37, 11.68) * mm});
            skLineSegment(sketch, "E3681", {"start": v(18.37, 11.68) * mm, "end": v(18.76, 12.14) * mm});
            skLineSegment(sketch, "E3682", {"start": v(18.76, 12.14) * mm, "end": v(19.05, 12.5) * mm});
            skLineSegment(sketch, "E3683", {"start": v(19.05, 12.5) * mm, "end": v(19.47, 13.08) * mm});
            skLineSegment(sketch, "E3684", {"start": v(19.47, 13.08) * mm, "end": v(20.23, 14.28) * mm});
            skLineSegment(sketch, "E3685", {"start": v(20.23, 14.28) * mm, "end": v(20.37, 14.52) * mm});
            skLineSegment(sketch, "E3686", {"start": v(20.37, 14.52) * mm, "end": v(20.5, 14.75) * mm});
            skLineSegment(sketch, "E3687", {"start": v(20.5, 14.75) * mm, "end": v(20.64, 14.98) * mm});
            skLineSegment(sketch, "E3688", {"start": v(20.64, 14.98) * mm, "end": v(20.78, 15.2) * mm});
            skLineSegment(sketch, "E3689", {"start": v(20.78, 15.2) * mm, "end": v(20.9, 15.43) * mm});
            skLineSegment(sketch, "E3690", {"start": v(20.9, 15.43) * mm, "end": v(21.04, 15.67) * mm});
            skLineSegment(sketch, "E3691", {"start": v(21.04, 15.67) * mm, "end": v(21.17, 15.9) * mm});
            skLineSegment(sketch, "E3692", {"start": v(21.17, 15.9) * mm, "end": v(21.3, 16.16) * mm});
            skLineSegment(sketch, "E3693", {"start": v(21.3, 16.16) * mm, "end": v(21.6, 16.77) * mm});
            skLineSegment(sketch, "E3694", {"start": v(21.6, 16.77) * mm, "end": v(21.9, 17.4) * mm});
            skLineSegment(sketch, "E3695", {"start": v(21.9, 17.4) * mm, "end": v(22.18, 18.06) * mm});
            skLineSegment(sketch, "E3696", {"start": v(22.18, 18.06) * mm, "end": v(22.44, 18.73) * mm});
            skLineSegment(sketch, "E3697", {"start": v(22.44, 18.73) * mm, "end": v(22.66, 19.42) * mm});
            skLineSegment(sketch, "E3698", {"start": v(22.66, 19.42) * mm, "end": v(22.85, 20.1) * mm});
            skLineSegment(sketch, "E3699", {"start": v(22.85, 20.1) * mm, "end": v(22.98, 20.79) * mm});
            skLineSegment(sketch, "E3700", {"start": v(22.98, 20.79) * mm, "end": v(23.04, 21.46) * mm});
            skLineSegment(sketch, "E3701", {"start": v(23.04, 21.46) * mm, "end": v(22.96, 21.35) * mm});
            skLineSegment(sketch, "E3702", {"start": v(22.96, 21.35) * mm, "end": v(22.9, 21.2) * mm});
            skLineSegment(sketch, "E3703", {"start": v(22.9, 21.2) * mm, "end": v(22.66, 20.68) * mm});
            skLineSegment(sketch, "E3704", {"start": v(22.66, 20.68) * mm, "end": v(22.55, 20.42) * mm});
            skLineSegment(sketch, "E3705", {"start": v(22.55, 20.42) * mm, "end": v(21.77, 18.9) * mm});
            skLineSegment(sketch, "E3706", {"start": v(21.77, 18.9) * mm, "end": v(21.6, 18.6) * mm});
            skLineSegment(sketch, "E3707", {"start": v(21.6, 18.6) * mm, "end": v(21.42, 18.3) * mm});
            skLineSegment(sketch, "E3708", {"start": v(21.42, 18.3) * mm, "end": v(21.24, 18) * mm});
            skLineSegment(sketch, "E3709", {"start": v(21.24, 18) * mm, "end": v(21.04, 17.71) * mm});
            skLineSegment(sketch, "E3710", {"start": v(21.04, 17.71) * mm, "end": v(20.84, 17.42) * mm});
            skLineSegment(sketch, "E3711", {"start": v(20.84, 17.42) * mm, "end": v(20.64, 17.14) * mm});
            skLineSegment(sketch, "E3712", {"start": v(20.64, 17.14) * mm, "end": v(20.43, 16.86) * mm});
            skLineSegment(sketch, "E3713", {"start": v(20.43, 16.86) * mm, "end": v(20.22, 16.58) * mm});
            skLineSegment(sketch, "E3714", {"start": v(20.22, 16.58) * mm, "end": v(18.69, 14.28) * mm});
            skLineSegment(sketch, "E3715", {"start": v(18.69, 14.28) * mm, "end": v(18.54, 14.06) * mm});
            skLineSegment(sketch, "E3716", {"start": v(18.54, 14.06) * mm, "end": v(18.49, 13.98) * mm});
            skLineSegment(sketch, "E3717", {"start": v(18.49, 13.98) * mm, "end": v(18.45, 13.92) * mm});
            skLineSegment(sketch, "E3718", {"start": v(18.45, 13.92) * mm, "end": v(18.42, 13.87) * mm});
            skLineSegment(sketch, "E3719", {"start": v(18.42, 13.87) * mm, "end": v(18.35, 13.82) * mm});
            skLineSegment(sketch, "E3720", {"start": v(18.35, 13.82) * mm, "end": v(19.43, 15.82) * mm});
            skLineSegment(sketch, "E3721", {"start": v(19.43, 15.82) * mm, "end": v(19.66, 16.28) * mm});
            skLineSegment(sketch, "E3722", {"start": v(19.66, 16.28) * mm, "end": v(19.87, 16.84) * mm});
            skLineSegment(sketch, "E3723", {"start": v(19.87, 16.84) * mm, "end": v(20.08, 17.47) * mm});
            skLineSegment(sketch, "E3724", {"start": v(20.08, 17.47) * mm, "end": v(20.28, 18.14) * mm});
            skLineSegment(sketch, "E3725", {"start": v(20.28, 18.14) * mm, "end": v(20.45, 18.83) * mm});
            skLineSegment(sketch, "E3726", {"start": v(20.45, 18.83) * mm, "end": v(20.6, 19.49) * mm});
            skLineSegment(sketch, "E3727", {"start": v(20.6, 19.49) * mm, "end": v(20.72, 20.1) * mm});
            skLineSegment(sketch, "E3728", {"start": v(20.72, 20.1) * mm, "end": v(20.8, 20.63) * mm});
            skLineSegment(sketch, "E3729", {"start": v(20.8, 20.63) * mm, "end": v(20.82, 20.9) * mm});
            skLineSegment(sketch, "E3730", {"start": v(20.82, 20.9) * mm, "end": v(20.86, 21.26) * mm});
            skLineSegment(sketch, "E3731", {"start": v(20.86, 21.26) * mm, "end": v(20.89, 21.68) * mm});
            skLineSegment(sketch, "E3732", {"start": v(20.89, 21.68) * mm, "end": v(20.91, 22.13) * mm});
            skLineSegment(sketch, "E3733", {"start": v(20.91, 22.13) * mm, "end": v(20.92, 22.57) * mm});
            skLineSegment(sketch, "E3734", {"start": v(20.92, 22.57) * mm, "end": v(20.91, 22.97) * mm});
            skLineSegment(sketch, "E3735", {"start": v(20.91, 22.97) * mm, "end": v(20.88, 23.3) * mm});
            skLineSegment(sketch, "E3736", {"start": v(20.88, 23.3) * mm, "end": v(20.82, 23.52) * mm});
            skLineSegment(sketch, "E3737", {"start": v(20.82, 23.52) * mm, "end": v(20.37, 22.06) * mm});
            skLineSegment(sketch, "E3738", {"start": v(20.37, 22.06) * mm, "end": v(20.2, 21.52) * mm});
            skLineSegment(sketch, "E3739", {"start": v(20.2, 21.52) * mm, "end": v(20.02, 20.99) * mm});
            skLineSegment(sketch, "E3740", {"start": v(20.02, 20.99) * mm, "end": v(19.83, 20.46) * mm});
            skLineSegment(sketch, "E3741", {"start": v(19.83, 20.46) * mm, "end": v(19.63, 19.94) * mm});
            skLineSegment(sketch, "E3742", {"start": v(19.63, 19.94) * mm, "end": v(19.42, 19.42) * mm});
            skLineSegment(sketch, "E3743", {"start": v(19.42, 19.42) * mm, "end": v(19.2, 18.9) * mm});
            skLineSegment(sketch, "E3744", {"start": v(19.2, 18.9) * mm, "end": v(19, 18.38) * mm});
            skLineSegment(sketch, "E3745", {"start": v(19, 18.38) * mm, "end": v(18.78, 17.86) * mm});
            skLineSegment(sketch, "E3746", {"start": v(18.78, 17.86) * mm, "end": v(18.64, 17.52) * mm});
            skLineSegment(sketch, "E3747", {"start": v(18.64, 17.52) * mm, "end": v(18.49, 17.2) * mm});
            skLineSegment(sketch, "E3748", {"start": v(18.49, 17.2) * mm, "end": v(18.34, 16.86) * mm});
            skLineSegment(sketch, "E3749", {"start": v(18.34, 16.86) * mm, "end": v(18.2, 16.53) * mm});
            skLineSegment(sketch, "E3750", {"start": v(18.2, 16.53) * mm, "end": v(18.05, 16.2) * mm});
            skLineSegment(sketch, "E3751", {"start": v(18.05, 16.2) * mm, "end": v(17.9, 15.86) * mm});
            skLineSegment(sketch, "E3752", {"start": v(17.9, 15.86) * mm, "end": v(17.72, 15.51) * mm});
            skLineSegment(sketch, "E3753", {"start": v(17.72, 15.51) * mm, "end": v(17.56, 15.2) * mm});
            skLineSegment(sketch, "E3754", {"start": v(17.56, 15.2) * mm, "end": v(17.5, 15.05) * mm});
            skLineSegment(sketch, "E3755", {"start": v(17.5, 15.05) * mm, "end": v(17.47, 14.88) * mm});
            skLineSegment(sketch, "E3756", {"start": v(17.47, 14.88) * mm, "end": v(17.43, 14.68) * mm});
            skLineSegment(sketch, "E3757", {"start": v(17.43, 14.68) * mm, "end": v(17.4, 14.46) * mm});
            skLineSegment(sketch, "E3758", {"start": v(17.4, 14.46) * mm, "end": v(17.37, 14.22) * mm});
            skLineSegment(sketch, "E3759", {"start": v(17.37, 14.22) * mm, "end": v(17.34, 13.99) * mm});
            skLineSegment(sketch, "E3760", {"start": v(17.34, 13.99) * mm, "end": v(17.31, 13.75) * mm});
            skLineSegment(sketch, "E3761", {"start": v(17.31, 13.75) * mm, "end": v(17.28, 13.52) * mm});
            skLineSegment(sketch, "E3762", {"start": v(17.28, 13.52) * mm, "end": v(17.24, 13.31) * mm});
            skLineSegment(sketch, "E3763", {"start": v(17.24, 13.31) * mm, "end": v(17.2, 13.1) * mm});
            skLineSegment(sketch, "E3764", {"start": v(17.2, 13.1) * mm, "end": v(17.16, 12.9) * mm});
            skLineSegment(sketch, "E3765", {"start": v(17.16, 12.9) * mm, "end": v(17.12, 12.71) * mm});
            skLineSegment(sketch, "E3766", {"start": v(17.12, 12.71) * mm, "end": v(17.07, 12.51) * mm});
            skLineSegment(sketch, "E3767", {"start": v(17.07, 12.51) * mm, "end": v(17.02, 12.32) * mm});
            skLineSegment(sketch, "E3768", {"start": v(17.02, 12.32) * mm, "end": v(16.97, 12.13) * mm});
            skLineSegment(sketch, "E3769", {"start": v(16.97, 12.13) * mm, "end": v(16.91, 11.93) * mm});
            skLineSegment(sketch, "E3770", {"start": v(10.25, 4.11) * mm, "end": v(10.31, 4.13) * mm});
            skLineSegment(sketch, "E3771", {"start": v(10.31, 4.13) * mm, "end": v(10.37, 4.15) * mm});
            skLineSegment(sketch, "E3772", {"start": v(10.37, 4.15) * mm, "end": v(10.42, 4.17) * mm});
            skLineSegment(sketch, "E3773", {"start": v(10.42, 4.17) * mm, "end": v(10.47, 4.2) * mm});
            skLineSegment(sketch, "E3774", {"start": v(10.47, 4.2) * mm, "end": v(10.55, 4.26) * mm});
            skLineSegment(sketch, "E3775", {"start": v(10.55, 4.26) * mm, "end": v(10.64, 4.32) * mm});
            skLineSegment(sketch, "E3776", {"start": v(10.64, 4.32) * mm, "end": v(10.76, 4.38) * mm});
            skLineSegment(sketch, "E3777", {"start": v(10.76, 4.38) * mm, "end": v(10.85, 4.42) * mm});
            skLineSegment(sketch, "E3778", {"start": v(10.85, 4.42) * mm, "end": v(10.94, 4.48) * mm});
            skLineSegment(sketch, "E3779", {"start": v(10.94, 4.48) * mm, "end": v(11.03, 4.55) * mm});
            skLineSegment(sketch, "E3780", {"start": v(11.03, 4.55) * mm, "end": v(11.08, 4.53) * mm});
            skLineSegment(sketch, "E3781", {"start": v(11.08, 4.53) * mm, "end": v(11.1, 4.54) * mm});
            skLineSegment(sketch, "E3782", {"start": v(11.1, 4.54) * mm, "end": v(11.08, 4.55) * mm});
            skLineSegment(sketch, "E3783", {"start": v(11.08, 4.55) * mm, "end": v(11.05, 4.56) * mm});
            skLineSegment(sketch, "E3784", {"start": v(11.05, 4.56) * mm, "end": v(11.02, 4.57) * mm});
            skLineSegment(sketch, "E3785", {"start": v(11.02, 4.57) * mm, "end": v(11, 4.57) * mm});
            skLineSegment(sketch, "E3786", {"start": v(11, 4.57) * mm, "end": v(11.02, 4.55) * mm});
            skLineSegment(sketch, "E3787", {"start": v(11.02, 4.55) * mm, "end": v(11.07, 4.52) * mm});
            skLineSegment(sketch, "E3788", {"start": v(11.07, 4.52) * mm, "end": v(11.13, 4.48) * mm});
            skLineSegment(sketch, "E3789", {"start": v(11.13, 4.48) * mm, "end": v(11.17, 4.46) * mm});
            skLineSegment(sketch, "E3790", {"start": v(11.17, 4.46) * mm, "end": v(11.2, 4.46) * mm});
            skLineSegment(sketch, "E3791", {"start": v(11.2, 4.46) * mm, "end": v(11.22, 4.48) * mm});
            skLineSegment(sketch, "E3792", {"start": v(11.22, 4.48) * mm, "end": v(11.28, 4.5) * mm});
            skLineSegment(sketch, "E3793", {"start": v(11.28, 4.5) * mm, "end": v(11.74, 4.74) * mm});
            skLineSegment(sketch, "E3794", {"start": v(11.74, 4.74) * mm, "end": v(12.2, 4.98) * mm});
            skLineSegment(sketch, "E3795", {"start": v(12.2, 4.98) * mm, "end": v(12.63, 5.22) * mm});
            skLineSegment(sketch, "E3796", {"start": v(12.63, 5.22) * mm, "end": v(13.06, 5.48) * mm});
            skLineSegment(sketch, "E3797", {"start": v(13.06, 5.48) * mm, "end": v(13.48, 5.75) * mm});
            skLineSegment(sketch, "E3798", {"start": v(13.48, 5.75) * mm, "end": v(13.9, 6.04) * mm});
            skLineSegment(sketch, "E3799", {"start": v(13.9, 6.04) * mm, "end": v(14.3, 6.35) * mm});
            skLineSegment(sketch, "E3800", {"start": v(14.3, 6.35) * mm, "end": v(14.68, 6.7) * mm});
            skLineSegment(sketch, "E3801", {"start": v(14.68, 6.7) * mm, "end": v(15.15, 7.14) * mm});
            skLineSegment(sketch, "E3802", {"start": v(15.15, 7.14) * mm, "end": v(15.27, 7.27) * mm});
            skLineSegment(sketch, "E3803", {"start": v(15.27, 7.27) * mm, "end": v(15.38, 7.42) * mm});
            skLineSegment(sketch, "E3804", {"start": v(15.38, 7.42) * mm, "end": v(15.58, 7.65) * mm});
            skLineSegment(sketch, "E3805", {"start": v(15.58, 7.65) * mm, "end": v(15.78, 7.9) * mm});
            skLineSegment(sketch, "E3806", {"start": v(15.78, 7.9) * mm, "end": v(15.97, 8.16) * mm});
            skLineSegment(sketch, "E3807", {"start": v(15.97, 8.16) * mm, "end": v(16.16, 8.44) * mm});
            skLineSegment(sketch, "E3808", {"start": v(16.16, 8.44) * mm, "end": v(16.34, 8.73) * mm});
            skLineSegment(sketch, "E3809", {"start": v(16.34, 8.73) * mm, "end": v(16.5, 9.03) * mm});
            skLineSegment(sketch, "E3810", {"start": v(16.5, 9.03) * mm, "end": v(16.67, 9.35) * mm});
            skLineSegment(sketch, "E3811", {"start": v(16.67, 9.35) * mm, "end": v(16.82, 9.69) * mm});
            skLineSegment(sketch, "E3812", {"start": v(16.82, 9.69) * mm, "end": v(16.93, 9.98) * mm});
            skLineSegment(sketch, "E3813", {"start": v(16.93, 9.98) * mm, "end": v(17.06, 10.32) * mm});
            skLineSegment(sketch, "E3814", {"start": v(17.06, 10.32) * mm, "end": v(17.19, 10.71) * mm});
            skLineSegment(sketch, "E3815", {"start": v(17.19, 10.71) * mm, "end": v(17.32, 11.12) * mm});
            skLineSegment(sketch, "E3816", {"start": v(17.32, 11.12) * mm, "end": v(17.43, 11.53) * mm});
            skLineSegment(sketch, "E3817", {"start": v(17.43, 11.53) * mm, "end": v(17.53, 11.93) * mm});
            skLineSegment(sketch, "E3818", {"start": v(17.53, 11.93) * mm, "end": v(17.6, 12.3) * mm});
            skLineSegment(sketch, "E3819", {"start": v(17.6, 12.3) * mm, "end": v(17.65, 12.6) * mm});
            skLineSegment(sketch, "E3820", {"start": v(17.65, 12.6) * mm, "end": v(15.79, 10) * mm});
            skLineSegment(sketch, "E3821", {"start": v(15.79, 10) * mm, "end": v(15.47, 9.62) * mm});
            skLineSegment(sketch, "E3822", {"start": v(15.47, 9.62) * mm, "end": v(15.1, 9.2) * mm});
            skLineSegment(sketch, "E3823", {"start": v(15.1, 9.2) * mm, "end": v(14.67, 8.78) * mm});
            skLineSegment(sketch, "E3824", {"start": v(14.67, 8.78) * mm, "end": v(14.22, 8.35) * mm});
            skLineSegment(sketch, "E3825", {"start": v(14.22, 8.35) * mm, "end": v(13.76, 7.93) * mm});
            skLineSegment(sketch, "E3826", {"start": v(13.76, 7.93) * mm, "end": v(13.3, 7.53) * mm});
            skLineSegment(sketch, "E3827", {"start": v(13.3, 7.53) * mm, "end": v(12.88, 7.17) * mm});
            skLineSegment(sketch, "E3828", {"start": v(12.88, 7.17) * mm, "end": v(12.48, 6.85) * mm});
            skLineSegment(sketch, "E3829", {"start": v(12.48, 6.85) * mm, "end": v(12.2, 6.64) * mm});
            skLineSegment(sketch, "E3830", {"start": v(12.2, 6.64) * mm, "end": v(12.02, 6.5) * mm});
            skLineSegment(sketch, "E3831", {"start": v(12.02, 6.5) * mm, "end": v(11.83, 6.37) * mm});
            skLineSegment(sketch, "E3832", {"start": v(11.83, 6.37) * mm, "end": v(11.64, 6.24) * mm});
            skLineSegment(sketch, "E3833", {"start": v(11.64, 6.24) * mm, "end": v(11.44, 6.1) * mm});
            skLineSegment(sketch, "E3834", {"start": v(11.44, 6.1) * mm, "end": v(11.24, 5.98) * mm});
            skLineSegment(sketch, "E3835", {"start": v(11.24, 5.98) * mm, "end": v(11.05, 5.86) * mm});
            skLineSegment(sketch, "E3836", {"start": v(11.05, 5.86) * mm, "end": v(10.87, 5.75) * mm});
            skLineSegment(sketch, "E3837", {"start": v(10.87, 5.75) * mm, "end": v(10.7, 5.63) * mm});
            skLineSegment(sketch, "E3838", {"start": v(10.7, 5.63) * mm, "end": v(10.65, 5.6) * mm});
            skLineSegment(sketch, "E3839", {"start": v(10.65, 5.6) * mm, "end": v(10.62, 5.56) * mm});
            skLineSegment(sketch, "E3840", {"start": v(10.62, 5.56) * mm, "end": v(10.6, 5.53) * mm});
            skLineSegment(sketch, "E3841", {"start": v(10.6, 5.53) * mm, "end": v(10.58, 5.5) * mm});
            skLineSegment(sketch, "E3842", {"start": v(10.58, 5.5) * mm, "end": v(10.56, 5.41) * mm});
            skLineSegment(sketch, "E3843", {"start": v(10.56, 5.41) * mm, "end": v(10.55, 5.28) * mm});
            skLineSegment(sketch, "E3844", {"start": v(10.55, 5.28) * mm, "end": v(10.47, 4.87) * mm});
            skLineSegment(sketch, "E3845", {"start": v(10.47, 4.87) * mm, "end": v(10.25, 4.11) * mm});
            skLineSegment(sketch, "E3846", {"start": v(-11.03, 4.54) * mm, "end": v(-10.86, 4.44) * mm});
            skLineSegment(sketch, "E3847", {"start": v(-10.86, 4.44) * mm, "end": v(-10.65, 4.3) * mm});
            skLineSegment(sketch, "E3848", {"start": v(-10.65, 4.3) * mm, "end": v(-10.54, 4.24) * mm});
            skLineSegment(sketch, "E3849", {"start": v(-10.54, 4.24) * mm, "end": v(-10.44, 4.18) * mm});
            skLineSegment(sketch, "E3850", {"start": v(-10.44, 4.18) * mm, "end": v(-10.34, 4.13) * mm});
            skLineSegment(sketch, "E3851", {"start": v(-10.34, 4.13) * mm, "end": v(-10.25, 4.1) * mm});
            skLineSegment(sketch, "E3852", {"start": v(-10.25, 4.1) * mm, "end": v(-10.33, 4.34) * mm});
            skLineSegment(sketch, "E3853", {"start": v(-10.33, 4.34) * mm, "end": v(-10.4, 4.58) * mm});
            skLineSegment(sketch, "E3854", {"start": v(-10.4, 4.58) * mm, "end": v(-10.45, 4.81) * mm});
            skLineSegment(sketch, "E3855", {"start": v(-10.45, 4.81) * mm, "end": v(-10.5, 5.04) * mm});
            skLineSegment(sketch, "E3856", {"start": v(-10.5, 5.04) * mm, "end": v(-10.53, 5.24) * mm});
            skLineSegment(sketch, "E3857", {"start": v(-10.53, 5.24) * mm, "end": v(-10.57, 5.4) * mm});
            skLineSegment(sketch, "E3858", {"start": v(-10.57, 5.4) * mm, "end": v(-10.62, 5.54) * mm});
            skLineSegment(sketch, "E3859", {"start": v(-10.62, 5.54) * mm, "end": v(-10.68, 5.62) * mm});
            skLineSegment(sketch, "E3860", {"start": v(-10.68, 5.62) * mm, "end": v(-11, 5.8) * mm});
            skLineSegment(sketch, "E3861", {"start": v(-11, 5.8) * mm, "end": v(-11.93, 6.42) * mm});
            skLineSegment(sketch, "E3862", {"start": v(-11.93, 6.42) * mm, "end": v(-12.81, 7.1) * mm});
            skLineSegment(sketch, "E3863", {"start": v(-12.81, 7.1) * mm, "end": v(-13.65, 7.8) * mm});
            skLineSegment(sketch, "E3864", {"start": v(-13.65, 7.8) * mm, "end": v(-14.45, 8.57) * mm});
            skLineSegment(sketch, "E3865", {"start": v(-14.45, 8.57) * mm, "end": v(-15.21, 9.37) * mm});
            skLineSegment(sketch, "E3866", {"start": v(-15.21, 9.37) * mm, "end": v(-15.93, 10.2) * mm});
            skLineSegment(sketch, "E3867", {"start": v(-15.93, 10.2) * mm, "end": v(-16.61, 11.08) * mm});
            skLineSegment(sketch, "E3868", {"start": v(-16.61, 11.08) * mm, "end": v(-17.26, 12) * mm});
            skLineSegment(sketch, "E3869", {"start": v(-17.26, 12) * mm, "end": v(-17.35, 12.15) * mm});
            skLineSegment(sketch, "E3870", {"start": v(-17.35, 12.15) * mm, "end": v(-17.46, 12.33) * mm});
            skLineSegment(sketch, "E3871", {"start": v(-17.46, 12.33) * mm, "end": v(-17.51, 12.42) * mm});
            skLineSegment(sketch, "E3872", {"start": v(-17.51, 12.42) * mm, "end": v(-17.57, 12.5) * mm});
            skLineSegment(sketch, "E3873", {"start": v(-17.57, 12.5) * mm, "end": v(-17.62, 12.56) * mm});
            skLineSegment(sketch, "E3874", {"start": v(-17.62, 12.56) * mm, "end": v(-17.66, 12.61) * mm});
            skLineSegment(sketch, "E3875", {"start": v(-17.66, 12.61) * mm, "end": v(-17.48, 11.74) * mm});
            skLineSegment(sketch, "E3876", {"start": v(-17.48, 11.74) * mm, "end": v(-17.26, 10.91) * mm});
            skLineSegment(sketch, "E3877", {"start": v(-17.26, 10.91) * mm, "end": v(-17, 10.14) * mm});
            skLineSegment(sketch, "E3878", {"start": v(-17, 10.14) * mm, "end": v(-16.7, 9.4) * mm});
            skLineSegment(sketch, "E3879", {"start": v(-16.7, 9.4) * mm, "end": v(-16.34, 8.73) * mm});
            skLineSegment(sketch, "E3880", {"start": v(-16.34, 8.73) * mm, "end": v(-15.93, 8.09) * mm});
            skLineSegment(sketch, "E3881", {"start": v(-15.93, 8.09) * mm, "end": v(-15.47, 7.5) * mm});
            skLineSegment(sketch, "E3882", {"start": v(-15.47, 7.5) * mm, "end": v(-14.94, 6.94) * mm});
            skLineSegment(sketch, "E3883", {"start": v(-14.94, 6.94) * mm, "end": v(-14.7, 6.72) * mm});
            skLineSegment(sketch, "E3884", {"start": v(-14.7, 6.72) * mm, "end": v(-14.47, 6.5) * mm});
            skLineSegment(sketch, "E3885", {"start": v(-14.47, 6.5) * mm, "end": v(-14.05, 6.17) * mm});
            skLineSegment(sketch, "E3886", {"start": v(-14.05, 6.17) * mm, "end": v(-13.67, 5.88) * mm});
            skLineSegment(sketch, "E3887", {"start": v(-13.67, 5.88) * mm, "end": v(-13.32, 5.64) * mm});
            skLineSegment(sketch, "E3888", {"start": v(-13.32, 5.64) * mm, "end": v(-12.98, 5.42) * mm});
            skLineSegment(sketch, "E3889", {"start": v(-12.98, 5.42) * mm, "end": v(-12.62, 5.21) * mm});
            skLineSegment(sketch, "E3890", {"start": v(-12.62, 5.21) * mm, "end": v(-12.24, 5) * mm});
            skLineSegment(sketch, "E3891", {"start": v(-12.24, 5) * mm, "end": v(-11.8, 4.77) * mm});
            skLineSegment(sketch, "E3892", {"start": v(-11.8, 4.77) * mm, "end": v(-11.3, 4.52) * mm});
            skLineSegment(sketch, "E3893", {"start": v(-11.3, 4.52) * mm, "end": v(-11.23, 4.48) * mm});
            skLineSegment(sketch, "E3894", {"start": v(-11.23, 4.48) * mm, "end": v(-11.17, 4.46) * mm});
            skLineSegment(sketch, "E3895", {"start": v(-11.17, 4.46) * mm, "end": v(-11.14, 4.45) * mm});
            skLineSegment(sketch, "E3896", {"start": v(-11.14, 4.45) * mm, "end": v(-11.13, 4.46) * mm});
            skLineSegment(sketch, "E3897", {"start": v(-11.13, 4.46) * mm, "end": v(-11.12, 4.47) * mm});
            skLineSegment(sketch, "E3898", {"start": v(-11.12, 4.47) * mm, "end": v(-11.1, 4.5) * mm});
            skLineSegment(sketch, "E3899", {"start": v(-11.1, 4.5) * mm, "end": v(-11.08, 4.52) * mm});
            skLineSegment(sketch, "E3900", {"start": v(-11.08, 4.52) * mm, "end": v(-11.03, 4.54) * mm});
            skLineSegment(sketch, "E3901", {"start": v(-10.61, 5.84) * mm, "end": v(-10.63, 5.92) * mm});
            skLineSegment(sketch, "E3902", {"start": v(-10.63, 5.92) * mm, "end": v(-10.65, 6) * mm});
            skLineSegment(sketch, "E3903", {"start": v(-10.65, 6) * mm, "end": v(-10.7, 6.09) * mm});
            skLineSegment(sketch, "E3904", {"start": v(-10.7, 6.09) * mm, "end": v(-10.74, 6.18) * mm});
            skLineSegment(sketch, "E3905", {"start": v(-10.74, 6.18) * mm, "end": v(-10.84, 6.36) * mm});
            skLineSegment(sketch, "E3906", {"start": v(-10.84, 6.36) * mm, "end": v(-10.93, 6.53) * mm});
            skLineSegment(sketch, "E3907", {"start": v(-10.93, 6.53) * mm, "end": v(-11.05, 6.81) * mm});
            skLineSegment(sketch, "E3908", {"start": v(-11.05, 6.81) * mm, "end": v(-11.11, 7) * mm});
            skLineSegment(sketch, "E3909", {"start": v(-11.11, 7) * mm, "end": v(-11.13, 7.11) * mm});
            skLineSegment(sketch, "E3910", {"start": v(-11.13, 7.11) * mm, "end": v(-11.15, 7.2) * mm});
            skLineSegment(sketch, "E3911", {"start": v(-11.15, 7.2) * mm, "end": v(-11.18, 7.28) * mm});
            skLineSegment(sketch, "E3912", {"start": v(-11.18, 7.28) * mm, "end": v(-11.25, 7.38) * mm});
            skLineSegment(sketch, "E3913", {"start": v(-11.25, 7.38) * mm, "end": v(-11.4, 7.55) * mm});
            skLineSegment(sketch, "E3914", {"start": v(-11.4, 7.55) * mm, "end": v(-11.65, 7.8) * mm});
            skLineSegment(sketch, "E3915", {"start": v(-11.65, 7.8) * mm, "end": v(-11.87, 8.03) * mm});
            skLineSegment(sketch, "E3916", {"start": v(-11.87, 8.03) * mm, "end": v(-12.11, 8.3) * mm});
            skLineSegment(sketch, "E3917", {"start": v(-12.11, 8.3) * mm, "end": v(-12.37, 8.57) * mm});
            skLineSegment(sketch, "E3918", {"start": v(-12.37, 8.57) * mm, "end": v(-12.63, 8.87) * mm});
            skLineSegment(sketch, "E3919", {"start": v(-12.63, 8.87) * mm, "end": v(-12.88, 9.17) * mm});
            skLineSegment(sketch, "E3920", {"start": v(-12.88, 9.17) * mm, "end": v(-13.13, 9.47) * mm});
            skLineSegment(sketch, "E3921", {"start": v(-13.13, 9.47) * mm, "end": v(-13.36, 9.74) * mm});
            skLineSegment(sketch, "E3922", {"start": v(-13.36, 9.74) * mm, "end": v(-13.55, 10) * mm});
            skLineSegment(sketch, "E3923", {"start": v(-13.55, 10) * mm, "end": v(-13.78, 10.27) * mm});
            skLineSegment(sketch, "E3924", {"start": v(-13.78, 10.27) * mm, "end": v(-14.04, 10.62) * mm});
            skLineSegment(sketch, "E3925", {"start": v(-14.04, 10.62) * mm, "end": v(-14.27, 10.94) * mm});
            skLineSegment(sketch, "E3926", {"start": v(-14.27, 10.94) * mm, "end": v(-14.5, 11.25) * mm});
            skLineSegment(sketch, "E3927", {"start": v(-14.5, 11.25) * mm, "end": v(-14.7, 11.55) * mm});
            skLineSegment(sketch, "E3928", {"start": v(-14.7, 11.55) * mm, "end": v(-14.92, 11.87) * mm});
            skLineSegment(sketch, "E3929", {"start": v(-14.92, 11.87) * mm, "end": v(-15.15, 12.2) * mm});
            skLineSegment(sketch, "E3930", {"start": v(-15.15, 12.2) * mm, "end": v(-15.38, 12.57) * mm});
            skLineSegment(sketch, "E3931", {"start": v(-15.38, 12.57) * mm, "end": v(-15.63, 13) * mm});
            skLineSegment(sketch, "E3932", {"start": v(-15.63, 13) * mm, "end": v(-15.82, 13.32) * mm});
            skLineSegment(sketch, "E3933", {"start": v(-15.82, 13.32) * mm, "end": v(-16, 13.66) * mm});
            skLineSegment(sketch, "E3934", {"start": v(-16, 13.66) * mm, "end": v(-16.17, 14) * mm});
            skLineSegment(sketch, "E3935", {"start": v(-16.17, 14) * mm, "end": v(-16.34, 14.33) * mm});
            skLineSegment(sketch, "E3936", {"start": v(-16.34, 14.33) * mm, "end": v(-16.52, 14.7) * mm});
            skLineSegment(sketch, "E3937", {"start": v(-16.52, 14.7) * mm, "end": v(-16.66, 15) * mm});
            skLineSegment(sketch, "E3938", {"start": v(-16.66, 15) * mm, "end": v(-16.77, 15.26) * mm});
            skLineSegment(sketch, "E3939", {"start": v(-16.77, 15.26) * mm, "end": v(-16.9, 15.53) * mm});
            skLineSegment(sketch, "E3940", {"start": v(-16.9, 15.53) * mm, "end": v(-16.93, 15.61) * mm});
            skLineSegment(sketch, "E3941", {"start": v(-16.93, 15.61) * mm, "end": v(-16.95, 15.65) * mm});
            skLineSegment(sketch, "E3942", {"start": v(-16.95, 15.65) * mm, "end": v(-16.97, 15.67) * mm});
            skLineSegment(sketch, "E3943", {"start": v(-16.97, 15.67) * mm, "end": v(-17.03, 15.7) * mm});
            skLineSegment(sketch, "E3944", {"start": v(-17.03, 15.7) * mm, "end": v(-17.06, 15.51) * mm});
            skLineSegment(sketch, "E3945", {"start": v(-17.06, 15.51) * mm, "end": v(-17.06, 15.29) * mm});
            skLineSegment(sketch, "E3946", {"start": v(-17.06, 15.29) * mm, "end": v(-17.06, 15.04) * mm});
            skLineSegment(sketch, "E3947", {"start": v(-17.06, 15.04) * mm, "end": v(-17.04, 14.79) * mm});
            skLineSegment(sketch, "E3948", {"start": v(-17.04, 14.79) * mm, "end": v(-17, 14.53) * mm});
            skLineSegment(sketch, "E3949", {"start": v(-17, 14.53) * mm, "end": v(-16.98, 14.28) * mm});
            skLineSegment(sketch, "E3950", {"start": v(-16.98, 14.28) * mm, "end": v(-16.94, 14.05) * mm});
            skLineSegment(sketch, "E3951", {"start": v(-16.94, 14.05) * mm, "end": v(-16.9, 13.85) * mm});
            skLineSegment(sketch, "E3952", {"start": v(-16.9, 13.85) * mm, "end": v(-16.86, 13.59) * mm});
            skLineSegment(sketch, "E3953", {"start": v(-16.86, 13.59) * mm, "end": v(-16.81, 13.39) * mm});
            skLineSegment(sketch, "E3954", {"start": v(-16.81, 13.39) * mm, "end": v(-16.78, 13.22) * mm});
            skLineSegment(sketch, "E3955", {"start": v(-16.78, 13.22) * mm, "end": v(-16.74, 13.08) * mm});
            skLineSegment(sketch, "E3956", {"start": v(-16.74, 13.08) * mm, "end": v(-16.7, 12.94) * mm});
            skLineSegment(sketch, "E3957", {"start": v(-16.7, 12.94) * mm, "end": v(-16.64, 12.78) * mm});
            skLineSegment(sketch, "E3958", {"start": v(-16.64, 12.78) * mm, "end": v(-16.57, 12.57) * mm});
            skLineSegment(sketch, "E3959", {"start": v(-16.57, 12.57) * mm, "end": v(-16.49, 12.31) * mm});
            skLineSegment(sketch, "E3960", {"start": v(-16.49, 12.31) * mm, "end": v(-16.36, 11.98) * mm});
            skLineSegment(sketch, "E3961", {"start": v(-16.36, 11.98) * mm, "end": v(-16.2, 11.62) * mm});
            skLineSegment(sketch, "E3962", {"start": v(-16.2, 11.62) * mm, "end": v(-16.01, 11.25) * mm});
            skLineSegment(sketch, "E3963", {"start": v(-16.01, 11.25) * mm, "end": v(-15.8, 10.89) * mm});
            skLineSegment(sketch, "E3964", {"start": v(-15.8, 10.89) * mm, "end": v(-15.6, 10.53) * mm});
            skLineSegment(sketch, "E3965", {"start": v(-15.6, 10.53) * mm, "end": v(-15.38, 10.2) * mm});
            skLineSegment(sketch, "E3966", {"start": v(-15.38, 10.2) * mm, "end": v(-15.18, 9.92) * mm});
            skLineSegment(sketch, "E3967", {"start": v(-15.18, 9.92) * mm, "end": v(-15, 9.68) * mm});
            skLineSegment(sketch, "E3968", {"start": v(-15, 9.68) * mm, "end": v(-14.04, 8.6) * mm});
            skLineSegment(sketch, "E3969", {"start": v(-14.04, 8.6) * mm, "end": v(-13.9, 8.47) * mm});
            skLineSegment(sketch, "E3970", {"start": v(-13.9, 8.47) * mm, "end": v(-13.78, 8.35) * mm});
            skLineSegment(sketch, "E3971", {"start": v(-13.78, 8.35) * mm, "end": v(-13.53, 8.1) * mm});
            skLineSegment(sketch, "E3972", {"start": v(-13.53, 8.1) * mm, "end": v(-13.28, 7.87) * mm});
            skLineSegment(sketch, "E3973", {"start": v(-13.28, 7.87) * mm, "end": v(-12.95, 7.58) * mm});
            skLineSegment(sketch, "E3974", {"start": v(-12.95, 7.58) * mm, "end": v(-12.55, 7.24) * mm});
            skLineSegment(sketch, "E3975", {"start": v(-12.55, 7.24) * mm, "end": v(-12.12, 6.9) * mm});
            skLineSegment(sketch, "E3976", {"start": v(-12.12, 6.9) * mm, "end": v(-11.68, 6.55) * mm});
            skLineSegment(sketch, "E3977", {"start": v(-11.68, 6.55) * mm, "end": v(-11.26, 6.25) * mm});
            skLineSegment(sketch, "E3978", {"start": v(-11.26, 6.25) * mm, "end": v(-10.9, 6) * mm});
            skLineSegment(sketch, "E3979", {"start": v(-10.9, 6) * mm, "end": v(-10.61, 5.84) * mm});
            skLineSegment(sketch, "E3980", {"start": v(10.63, 5.83) * mm, "end": v(11.2, 6.22) * mm});
            skLineSegment(sketch, "E3981", {"start": v(11.2, 6.22) * mm, "end": v(11.58, 6.5) * mm});
            skLineSegment(sketch, "E3982", {"start": v(11.58, 6.5) * mm, "end": v(11.95, 6.78) * mm});
            skLineSegment(sketch, "E3983", {"start": v(11.95, 6.78) * mm, "end": v(12.31, 7.05) * mm});
            skLineSegment(sketch, "E3984", {"start": v(12.31, 7.05) * mm, "end": v(12.66, 7.33) * mm});
            skLineSegment(sketch, "E3985", {"start": v(12.66, 7.33) * mm, "end": v(13, 7.62) * mm});
            skLineSegment(sketch, "E3986", {"start": v(13, 7.62) * mm, "end": v(13.35, 7.91) * mm});
            skLineSegment(sketch, "E3987", {"start": v(13.35, 7.91) * mm, "end": v(13.68, 8.23) * mm});
            skLineSegment(sketch, "E3988", {"start": v(13.68, 8.23) * mm, "end": v(14.02, 8.57) * mm});
            skLineSegment(sketch, "E3989", {"start": v(14.02, 8.57) * mm, "end": v(14.41, 9) * mm});
            skLineSegment(sketch, "E3990", {"start": v(14.41, 9) * mm, "end": v(14.78, 9.42) * mm});
            skLineSegment(sketch, "E3991", {"start": v(14.78, 9.42) * mm, "end": v(15.12, 9.86) * mm});
            skLineSegment(sketch, "E3992", {"start": v(15.12, 9.86) * mm, "end": v(15.43, 10.3) * mm});
            skLineSegment(sketch, "E3993", {"start": v(15.43, 10.3) * mm, "end": v(15.73, 10.77) * mm});
            skLineSegment(sketch, "E3994", {"start": v(15.73, 10.77) * mm, "end": v(16, 11.26) * mm});
            skLineSegment(sketch, "E3995", {"start": v(16, 11.26) * mm, "end": v(16.25, 11.77) * mm});
            skLineSegment(sketch, "E3996", {"start": v(16.25, 11.77) * mm, "end": v(16.48, 12.31) * mm});
            skLineSegment(sketch, "E3997", {"start": v(16.48, 12.31) * mm, "end": v(16.56, 12.51) * mm});
            skLineSegment(sketch, "E3998", {"start": v(16.56, 12.51) * mm, "end": v(16.62, 12.71) * mm});
            skLineSegment(sketch, "E3999", {"start": v(16.62, 12.71) * mm, "end": v(16.67, 12.9) * mm});
            skLineSegment(sketch, "E4000", {"start": v(16.67, 12.9) * mm, "end": v(16.72, 13.1) * mm});
            skLineSegment(sketch, "E4001", {"start": v(16.72, 13.1) * mm, "end": v(16.77, 13.3) * mm});
            skLineSegment(sketch, "E4002", {"start": v(16.77, 13.3) * mm, "end": v(16.82, 13.5) * mm});
            skLineSegment(sketch, "E4003", {"start": v(16.82, 13.5) * mm, "end": v(16.87, 13.7) * mm});
            skLineSegment(sketch, "E4004", {"start": v(16.87, 13.7) * mm, "end": v(16.92, 13.91) * mm});
            skLineSegment(sketch, "E4005", {"start": v(16.92, 13.91) * mm, "end": v(16.95, 14.05) * mm});
            skLineSegment(sketch, "E4006", {"start": v(16.95, 14.05) * mm, "end": v(16.99, 14.26) * mm});
            skLineSegment(sketch, "E4007", {"start": v(16.99, 14.26) * mm, "end": v(17.02, 14.52) * mm});
            skLineSegment(sketch, "E4008", {"start": v(17.02, 14.52) * mm, "end": v(17.04, 14.81) * mm});
            skLineSegment(sketch, "E4009", {"start": v(17.04, 14.81) * mm, "end": v(17.06, 15.1) * mm});
            skLineSegment(sketch, "E4010", {"start": v(17.06, 15.1) * mm, "end": v(17.06, 15.35) * mm});
            skLineSegment(sketch, "E4011", {"start": v(17.06, 15.35) * mm, "end": v(17.03, 15.56) * mm});
            skLineSegment(sketch, "E4012", {"start": v(17.03, 15.56) * mm, "end": v(16.99, 15.7) * mm});
            skLineSegment(sketch, "E4013", {"start": v(16.99, 15.7) * mm, "end": v(16.66, 15.01) * mm});
            skLineSegment(sketch, "E4014", {"start": v(16.66, 15.01) * mm, "end": v(16.35, 14.33) * mm});
            skLineSegment(sketch, "E4015", {"start": v(16.35, 14.33) * mm, "end": v(16, 13.67) * mm});
            skLineSegment(sketch, "E4016", {"start": v(16, 13.67) * mm, "end": v(15.89, 13.46) * mm});
            skLineSegment(sketch, "E4017", {"start": v(15.89, 13.46) * mm, "end": v(15.75, 13.21) * mm});
            skLineSegment(sketch, "E4018", {"start": v(15.75, 13.21) * mm, "end": v(15.6, 12.94) * mm});
            skLineSegment(sketch, "E4019", {"start": v(15.6, 12.94) * mm, "end": v(15.43, 12.66) * mm});
            skLineSegment(sketch, "E4020", {"start": v(15.43, 12.66) * mm, "end": v(15.26, 12.38) * mm});
            skLineSegment(sketch, "E4021", {"start": v(15.26, 12.38) * mm, "end": v(15.1, 12.13) * mm});
            skLineSegment(sketch, "E4022", {"start": v(15.1, 12.13) * mm, "end": v(14.96, 11.91) * mm});
            skLineSegment(sketch, "E4023", {"start": v(14.96, 11.91) * mm, "end": v(14.84, 11.74) * mm});
            skLineSegment(sketch, "E4024", {"start": v(14.84, 11.74) * mm, "end": v(14.64, 11.44) * mm});
            skLineSegment(sketch, "E4025", {"start": v(14.64, 11.44) * mm, "end": v(14, 10.55) * mm});
            skLineSegment(sketch, "E4026", {"start": v(14, 10.55) * mm, "end": v(13.86, 10.37) * mm});
            skLineSegment(sketch, "E4027", {"start": v(13.86, 10.37) * mm, "end": v(13.7, 10.17) * mm});
            skLineSegment(sketch, "E4028", {"start": v(13.7, 10.17) * mm, "end": v(13.53, 9.94) * mm});
            skLineSegment(sketch, "E4029", {"start": v(13.53, 9.94) * mm, "end": v(13.34, 9.72) * mm});
            skLineSegment(sketch, "E4030", {"start": v(13.34, 9.72) * mm, "end": v(13.16, 9.49) * mm});
            skLineSegment(sketch, "E4031", {"start": v(13.16, 9.49) * mm, "end": v(12.97, 9.27) * mm});
            skLineSegment(sketch, "E4032", {"start": v(12.97, 9.27) * mm, "end": v(12.8, 9.07) * mm});
            skLineSegment(sketch, "E4033", {"start": v(12.8, 9.07) * mm, "end": v(12.65, 8.9) * mm});
            skLineSegment(sketch, "E4034", {"start": v(12.65, 8.9) * mm, "end": v(12.53, 8.76) * mm});
            skLineSegment(sketch, "E4035", {"start": v(12.53, 8.76) * mm, "end": v(12.34, 8.56) * mm});
            skLineSegment(sketch, "E4036", {"start": v(12.34, 8.56) * mm, "end": v(12.1, 8.32) * mm});
            skLineSegment(sketch, "E4037", {"start": v(12.1, 8.32) * mm, "end": v(11.85, 8.05) * mm});
            skLineSegment(sketch, "E4038", {"start": v(11.85, 8.05) * mm, "end": v(11.6, 7.78) * mm});
            skLineSegment(sketch, "E4039", {"start": v(11.6, 7.78) * mm, "end": v(11.4, 7.55) * mm});
            skLineSegment(sketch, "E4040", {"start": v(11.4, 7.55) * mm, "end": v(11.24, 7.37) * mm});
            skLineSegment(sketch, "E4041", {"start": v(11.24, 7.37) * mm, "end": v(11.18, 7.28) * mm});
            skLineSegment(sketch, "E4042", {"start": v(11.18, 7.28) * mm, "end": v(11.1, 7) * mm});
            skLineSegment(sketch, "E4043", {"start": v(11.1, 7) * mm, "end": v(11, 6.73) * mm});
            skLineSegment(sketch, "E4044", {"start": v(11, 6.73) * mm, "end": v(10.95, 6.6) * mm});
            skLineSegment(sketch, "E4045", {"start": v(10.95, 6.6) * mm, "end": v(10.9, 6.46) * mm});
            skLineSegment(sketch, "E4046", {"start": v(10.9, 6.46) * mm, "end": v(10.83, 6.33) * mm});
            skLineSegment(sketch, "E4047", {"start": v(10.83, 6.33) * mm, "end": v(10.76, 6.2) * mm});
            skLineSegment(sketch, "E4048", {"start": v(10.76, 6.2) * mm, "end": v(10.7, 6.1) * mm});
            skLineSegment(sketch, "E4049", {"start": v(10.7, 6.1) * mm, "end": v(10.65, 6.02) * mm});
            skLineSegment(sketch, "E4050", {"start": v(10.65, 6.02) * mm, "end": v(10.63, 5.98) * mm});
            skLineSegment(sketch, "E4051", {"start": v(10.63, 5.98) * mm, "end": v(10.62, 5.94) * mm});
            skLineSegment(sketch, "E4052", {"start": v(10.62, 5.94) * mm, "end": v(10.62, 5.89) * mm});
            skLineSegment(sketch, "E4053", {"start": v(10.62, 5.89) * mm, "end": v(10.63, 5.83) * mm});
            skLineSegment(sketch, "E4054", {"start": v(4.92, -7.77) * mm, "end": v(4.95, -8.1) * mm});
            skLineSegment(sketch, "E4055", {"start": v(4.95, -8.1) * mm, "end": v(4.97, -8.41) * mm});
            skLineSegment(sketch, "E4056", {"start": v(4.97, -8.41) * mm, "end": v(4.98, -8.7) * mm});
            skLineSegment(sketch, "E4057", {"start": v(4.98, -8.7) * mm, "end": v(5, -8.97) * mm});
            skLineSegment(sketch, "E4058", {"start": v(5, -8.97) * mm, "end": v(5.01, -9.25) * mm});
            skLineSegment(sketch, "E4059", {"start": v(5.01, -9.25) * mm, "end": v(5.02, -9.53) * mm});
            skLineSegment(sketch, "E4060", {"start": v(5.02, -9.53) * mm, "end": v(5.03, -9.83) * mm});
            skLineSegment(sketch, "E4061", {"start": v(5.03, -9.83) * mm, "end": v(5.03, -10.15) * mm});
            skLineSegment(sketch, "E4062", {"start": v(5.03, -10.15) * mm, "end": v(5.43, -10.32) * mm});
            skLineSegment(sketch, "E4063", {"start": v(5.43, -10.32) * mm, "end": v(5.89, -10.5) * mm});
            skLineSegment(sketch, "E4064", {"start": v(5.89, -10.5) * mm, "end": v(6.39, -10.63) * mm});
            skLineSegment(sketch, "E4065", {"start": v(6.39, -10.63) * mm, "end": v(6.9, -10.72) * mm});
            skLineSegment(sketch, "E4066", {"start": v(6.9, -10.72) * mm, "end": v(7.4, -10.74) * mm});
            skLineSegment(sketch, "E4067", {"start": v(7.4, -10.74) * mm, "end": v(7.88, -10.66) * mm});
            skLineSegment(sketch, "E4068", {"start": v(7.88, -10.66) * mm, "end": v(8.3, -10.45) * mm});
            skLineSegment(sketch, "E4069", {"start": v(8.3, -10.45) * mm, "end": v(8.64, -10.1) * mm});
            skLineSegment(sketch, "E4070", {"start": v(8.64, -10.1) * mm, "end": v(8.7, -10) * mm});
            skLineSegment(sketch, "E4071", {"start": v(8.7, -10) * mm, "end": v(8.78, -9.88) * mm});
            skLineSegment(sketch, "E4072", {"start": v(8.78, -9.88) * mm, "end": v(8.85, -9.76) * mm});
            skLineSegment(sketch, "E4073", {"start": v(8.85, -9.76) * mm, "end": v(8.89, -9.65) * mm});
            skLineSegment(sketch, "E4074", {"start": v(8.89, -9.65) * mm, "end": v(8.62, -9.65) * mm});
            skLineSegment(sketch, "E4075", {"start": v(8.62, -9.65) * mm, "end": v(8.34, -9.65) * mm});
            skLineSegment(sketch, "E4076", {"start": v(8.34, -9.65) * mm, "end": v(8.07, -9.65) * mm});
            skLineSegment(sketch, "E4077", {"start": v(8.07, -9.65) * mm, "end": v(7.8, -9.62) * mm});
            skLineSegment(sketch, "E4078", {"start": v(7.8, -9.62) * mm, "end": v(7.52, -9.58) * mm});
            skLineSegment(sketch, "E4079", {"start": v(7.52, -9.58) * mm, "end": v(7.25, -9.52) * mm});
            skLineSegment(sketch, "E4080", {"start": v(7.25, -9.52) * mm, "end": v(7, -9.42) * mm});
            skLineSegment(sketch, "E4081", {"start": v(7, -9.42) * mm, "end": v(6.75, -9.3) * mm});
            skLineSegment(sketch, "E4082", {"start": v(6.75, -9.3) * mm, "end": v(6.54, -9.18) * mm});
            skLineSegment(sketch, "E4083", {"start": v(6.54, -9.18) * mm, "end": v(6.3, -9.04) * mm});
            skLineSegment(sketch, "E4084", {"start": v(6.3, -9.04) * mm, "end": v(6.17, -8.96) * mm});
            skLineSegment(sketch, "E4085", {"start": v(6.17, -8.96) * mm, "end": v(6.05, -8.88) * mm});
            skLineSegment(sketch, "E4086", {"start": v(6.05, -8.88) * mm, "end": v(5.94, -8.79) * mm});
            skLineSegment(sketch, "E4087", {"start": v(5.94, -8.79) * mm, "end": v(5.85, -8.69) * mm});
            skLineSegment(sketch, "E4088", {"start": v(5.85, -8.69) * mm, "end": v(6.36, -8.86) * mm});
            skLineSegment(sketch, "E4089", {"start": v(6.36, -8.86) * mm, "end": v(6.9, -9.04) * mm});
            skLineSegment(sketch, "E4090", {"start": v(6.9, -9.04) * mm, "end": v(7.43, -9.2) * mm});
            skLineSegment(sketch, "E4091", {"start": v(7.43, -9.2) * mm, "end": v(7.97, -9.3) * mm});
            skLineSegment(sketch, "E4092", {"start": v(7.97, -9.3) * mm, "end": v(8.5, -9.3) * mm});
            skLineSegment(sketch, "E4093", {"start": v(8.5, -9.3) * mm, "end": v(9.02, -9.18) * mm});
            skLineSegment(sketch, "E4094", {"start": v(9.02, -9.18) * mm, "end": v(9.52, -8.9) * mm});
            skLineSegment(sketch, "E4095", {"start": v(9.52, -8.9) * mm, "end": v(10, -8.42) * mm});
            skLineSegment(sketch, "E4096", {"start": v(10, -8.42) * mm, "end": v(10.08, -8.32) * mm});
            skLineSegment(sketch, "E4097", {"start": v(10.08, -8.32) * mm, "end": v(10.15, -8.2) * mm});
            skLineSegment(sketch, "E4098", {"start": v(10.15, -8.2) * mm, "end": v(10.23, -8.06) * mm});
            skLineSegment(sketch, "E4099", {"start": v(10.23, -8.06) * mm, "end": v(10.3, -7.92) * mm});
            skLineSegment(sketch, "E4100", {"start": v(10.3, -7.92) * mm, "end": v(10.1, -7.95) * mm});
            skLineSegment(sketch, "E4101", {"start": v(10.1, -7.95) * mm, "end": v(9.83, -8) * mm});
            skLineSegment(sketch, "E4102", {"start": v(9.83, -8) * mm, "end": v(9.67, -8.03) * mm});
            skLineSegment(sketch, "E4103", {"start": v(9.67, -8.03) * mm, "end": v(9.48, -8.05) * mm});
            skLineSegment(sketch, "E4104", {"start": v(9.48, -8.05) * mm, "end": v(9.25, -8.07) * mm});
            skLineSegment(sketch, "E4105", {"start": v(9.25, -8.07) * mm, "end": v(8.98, -8.08) * mm});
            skLineSegment(sketch, "E4106", {"start": v(8.98, -8.08) * mm, "end": v(8.6, -8.06) * mm});
            skLineSegment(sketch, "E4107", {"start": v(8.6, -8.06) * mm, "end": v(8.27, -8.03) * mm});
            skLineSegment(sketch, "E4108", {"start": v(8.27, -8.03) * mm, "end": v(8.02, -7.98) * mm});
            skLineSegment(sketch, "E4109", {"start": v(8.02, -7.98) * mm, "end": v(7.81, -7.92) * mm});
            skLineSegment(sketch, "E4110", {"start": v(7.81, -7.92) * mm, "end": v(7.64, -7.86) * mm});
            skLineSegment(sketch, "E4111", {"start": v(7.64, -7.86) * mm, "end": v(7.49, -7.8) * mm});
            skLineSegment(sketch, "E4112", {"start": v(7.49, -7.8) * mm, "end": v(7.34, -7.76) * mm});
            skLineSegment(sketch, "E4113", {"start": v(7.34, -7.76) * mm, "end": v(7.19, -7.73) * mm});
            skLineSegment(sketch, "E4114", {"start": v(7.19, -7.73) * mm, "end": v(7.07, -7.84) * mm});
            skLineSegment(sketch, "E4115", {"start": v(7.07, -7.84) * mm, "end": v(6.97, -7.93) * mm});
            skLineSegment(sketch, "E4116", {"start": v(6.97, -7.93) * mm, "end": v(6.88, -8) * mm});
            skLineSegment(sketch, "E4117", {"start": v(6.88, -8) * mm, "end": v(6.8, -8.04) * mm});
            skLineSegment(sketch, "E4118", {"start": v(6.8, -8.04) * mm, "end": v(6.7, -8.06) * mm});
            skLineSegment(sketch, "E4119", {"start": v(6.7, -8.06) * mm, "end": v(6.57, -8.06) * mm});
            skLineSegment(sketch, "E4120", {"start": v(6.57, -8.06) * mm, "end": v(6.41, -8.03) * mm});
            skLineSegment(sketch, "E4121", {"start": v(6.41, -8.03) * mm, "end": v(6.2, -7.98) * mm});
            skLineSegment(sketch, "E4122", {"start": v(6.2, -7.98) * mm, "end": v(5.88, -7.9) * mm});
            skLineSegment(sketch, "E4123", {"start": v(5.88, -7.9) * mm, "end": v(5.58, -7.84) * mm});
            skLineSegment(sketch, "E4124", {"start": v(5.58, -7.84) * mm, "end": v(5.27, -7.8) * mm});
            skLineSegment(sketch, "E4125", {"start": v(5.27, -7.8) * mm, "end": v(4.92, -7.77) * mm});
            skLineSegment(sketch, "E4126", {"start": v(2.94, -18.16) * mm, "end": v(2.88, -18.02) * mm});
            skLineSegment(sketch, "E4127", {"start": v(2.88, -18.02) * mm, "end": v(2.9, -17.88) * mm});
            skLineSegment(sketch, "E4128", {"start": v(2.9, -17.88) * mm, "end": v(2.96, -17.76) * mm});
            skLineSegment(sketch, "E4129", {"start": v(2.96, -17.76) * mm, "end": v(3.07, -17.66) * mm});
            skLineSegment(sketch, "E4130", {"start": v(3.07, -17.66) * mm, "end": v(3.21, -17.59) * mm});
            skLineSegment(sketch, "E4131", {"start": v(3.21, -17.59) * mm, "end": v(3.38, -17.56) * mm});
            skLineSegment(sketch, "E4132", {"start": v(3.38, -17.56) * mm, "end": v(3.55, -17.6) * mm});
            skLineSegment(sketch, "E4133", {"start": v(3.55, -17.6) * mm, "end": v(3.73, -17.7) * mm});
            skLineSegment(sketch, "E4134", {"start": v(3.73, -17.7) * mm, "end": v(3.85, -17.83) * mm});
            skLineSegment(sketch, "E4135", {"start": v(3.85, -17.83) * mm, "end": v(3.9, -17.9) * mm});
            skLineSegment(sketch, "E4136", {"start": v(3.9, -17.9) * mm, "end": v(3.97, -17.98) * mm});
            skLineSegment(sketch, "E4137", {"start": v(3.97, -17.98) * mm, "end": v(4, -18) * mm});
            skLineSegment(sketch, "E4138", {"start": v(4, -18) * mm, "end": v(4.05, -17.78) * mm});
            skLineSegment(sketch, "E4139", {"start": v(4.05, -17.78) * mm, "end": v(4.1, -17.57) * mm});
            skLineSegment(sketch, "E4140", {"start": v(4.1, -17.57) * mm, "end": v(4.13, -17.37) * mm});
            skLineSegment(sketch, "E4141", {"start": v(4.13, -17.37) * mm, "end": v(4.15, -17.19) * mm});
            skLineSegment(sketch, "E4142", {"start": v(4.15, -17.19) * mm, "end": v(4.15, -17) * mm});
            skLineSegment(sketch, "E4143", {"start": v(4.15, -17) * mm, "end": v(4.14, -16.8) * mm});
            skLineSegment(sketch, "E4144", {"start": v(4.14, -16.8) * mm, "end": v(4.1, -16.56) * mm});
            skLineSegment(sketch, "E4145", {"start": v(4.1, -16.56) * mm, "end": v(4.04, -16.3) * mm});
            skLineSegment(sketch, "E4146", {"start": v(4.04, -16.3) * mm, "end": v(4, -16.11) * mm});
            skLineSegment(sketch, "E4147", {"start": v(4, -16.11) * mm, "end": v(3.93, -15.92) * mm});
            skLineSegment(sketch, "E4148", {"start": v(3.93, -15.92) * mm, "end": v(3.85, -15.74) * mm});
            skLineSegment(sketch, "E4149", {"start": v(3.85, -15.74) * mm, "end": v(3.75, -15.57) * mm});
            skLineSegment(sketch, "E4150", {"start": v(3.75, -15.57) * mm, "end": v(3.62, -15.43) * mm});
            skLineSegment(sketch, "E4151", {"start": v(3.62, -15.43) * mm, "end": v(3.48, -15.33) * mm});
            skLineSegment(sketch, "E4152", {"start": v(3.48, -15.33) * mm, "end": v(3.3, -15.27) * mm});
            skLineSegment(sketch, "E4153", {"start": v(3.3, -15.27) * mm, "end": v(3.1, -15.27) * mm});
            skLineSegment(sketch, "E4154", {"start": v(3.1, -15.27) * mm, "end": v(3, -15.3) * mm});
            skLineSegment(sketch, "E4155", {"start": v(3, -15.3) * mm, "end": v(2.92, -15.32) * mm});
            skLineSegment(sketch, "E4156", {"start": v(2.92, -15.32) * mm, "end": v(2.83, -15.37) * mm});
            skLineSegment(sketch, "E4157", {"start": v(2.83, -15.37) * mm, "end": v(2.75, -15.41) * mm});
            skLineSegment(sketch, "E4158", {"start": v(2.75, -15.41) * mm, "end": v(2.6, -15.52) * mm});
            skLineSegment(sketch, "E4159", {"start": v(2.6, -15.52) * mm, "end": v(2.5, -15.63) * mm});
            skLineSegment(sketch, "E4160", {"start": v(2.5, -15.63) * mm, "end": v(2.4, -15.74) * mm});
            skLineSegment(sketch, "E4161", {"start": v(2.4, -15.74) * mm, "end": v(2.29, -15.9) * mm});
            skLineSegment(sketch, "E4162", {"start": v(2.29, -15.9) * mm, "end": v(2.17, -16.08) * mm});
            skLineSegment(sketch, "E4163", {"start": v(2.17, -16.08) * mm, "end": v(2.09, -16.22) * mm});
            skLineSegment(sketch, "E4164", {"start": v(2.09, -16.22) * mm, "end": v(1.93, -16.55) * mm});
            skLineSegment(sketch, "E4165", {"start": v(1.93, -16.55) * mm, "end": v(1.77, -16.9) * mm});
            skLineSegment(sketch, "E4166", {"start": v(1.77, -16.9) * mm, "end": v(1.7, -17.08) * mm});
            skLineSegment(sketch, "E4167", {"start": v(1.7, -17.08) * mm, "end": v(1.64, -17.26) * mm});
            skLineSegment(sketch, "E4168", {"start": v(1.64, -17.26) * mm, "end": v(1.59, -17.45) * mm});
            skLineSegment(sketch, "E4169", {"start": v(1.59, -17.45) * mm, "end": v(1.54, -17.64) * mm});
            skLineSegment(sketch, "E4170", {"start": v(1.54, -17.64) * mm, "end": v(1.48, -18.01) * mm});
            skLineSegment(sketch, "E4171", {"start": v(1.48, -18.01) * mm, "end": v(1.44, -18.45) * mm});
            skLineSegment(sketch, "E4172", {"start": v(1.44, -18.45) * mm, "end": v(1.41, -18.94) * mm});
            skLineSegment(sketch, "E4173", {"start": v(1.41, -18.94) * mm, "end": v(1.4, -19.45) * mm});
            skLineSegment(sketch, "E4174", {"start": v(1.4, -19.45) * mm, "end": v(1.41, -19.96) * mm});
            skLineSegment(sketch, "E4175", {"start": v(1.41, -19.96) * mm, "end": v(1.44, -20.44) * mm});
            skLineSegment(sketch, "E4176", {"start": v(1.44, -20.44) * mm, "end": v(1.49, -20.88) * mm});
            skLineSegment(sketch, "E4177", {"start": v(1.49, -20.88) * mm, "end": v(1.55, -21.25) * mm});
            skLineSegment(sketch, "E4178", {"start": v(1.55, -21.25) * mm, "end": v(1.58, -21.33) * mm});
            skLineSegment(sketch, "E4179", {"start": v(1.58, -21.33) * mm, "end": v(1.6, -21.42) * mm});
            skLineSegment(sketch, "E4180", {"start": v(1.6, -21.42) * mm, "end": v(1.64, -21.5) * mm});
            skLineSegment(sketch, "E4181", {"start": v(1.64, -21.5) * mm, "end": v(1.68, -21.58) * mm});
            skLineSegment(sketch, "E4182", {"start": v(1.68, -21.58) * mm, "end": v(1.76, -21.66) * mm});
            skLineSegment(sketch, "E4183", {"start": v(1.76, -21.66) * mm, "end": v(1.89, -21.72) * mm});
            skLineSegment(sketch, "E4184", {"start": v(1.89, -21.72) * mm, "end": v(2.04, -21.77) * mm});
            skLineSegment(sketch, "E4185", {"start": v(2.04, -21.77) * mm, "end": v(2.2, -21.8) * mm});
            skLineSegment(sketch, "E4186", {"start": v(2.2, -21.8) * mm, "end": v(2.39, -21.82) * mm});
            skLineSegment(sketch, "E4187", {"start": v(2.39, -21.82) * mm, "end": v(2.57, -21.82) * mm});
            skLineSegment(sketch, "E4188", {"start": v(2.57, -21.82) * mm, "end": v(2.73, -21.8) * mm});
            skLineSegment(sketch, "E4189", {"start": v(2.73, -21.8) * mm, "end": v(2.87, -21.76) * mm});
            skLineSegment(sketch, "E4190", {"start": v(2.87, -21.76) * mm, "end": v(3.02, -21.7) * mm});
            skLineSegment(sketch, "E4191", {"start": v(3.02, -21.7) * mm, "end": v(3.16, -21.6) * mm});
            skLineSegment(sketch, "E4192", {"start": v(3.16, -21.6) * mm, "end": v(3.3, -21.48) * mm});
            skLineSegment(sketch, "E4193", {"start": v(3.3, -21.48) * mm, "end": v(3.43, -21.34) * mm});
            skLineSegment(sketch, "E4194", {"start": v(3.43, -21.34) * mm, "end": v(3.54, -21.19) * mm});
            skLineSegment(sketch, "E4195", {"start": v(3.54, -21.19) * mm, "end": v(3.64, -21.03) * mm});
            skLineSegment(sketch, "E4196", {"start": v(3.64, -21.03) * mm, "end": v(3.71, -20.86) * mm});
            skLineSegment(sketch, "E4197", {"start": v(3.71, -20.86) * mm, "end": v(3.76, -20.69) * mm});
            skLineSegment(sketch, "E4198", {"start": v(3.76, -20.69) * mm, "end": v(3.53, -20.72) * mm});
            skLineSegment(sketch, "E4199", {"start": v(3.53, -20.72) * mm, "end": v(3.32, -20.74) * mm});
            skLineSegment(sketch, "E4200", {"start": v(3.32, -20.74) * mm, "end": v(3.22, -20.73) * mm});
            skLineSegment(sketch, "E4201", {"start": v(3.22, -20.73) * mm, "end": v(3.13, -20.7) * mm});
            skLineSegment(sketch, "E4202", {"start": v(3.13, -20.7) * mm, "end": v(3.03, -20.66) * mm});
            skLineSegment(sketch, "E4203", {"start": v(3.03, -20.66) * mm, "end": v(2.93, -20.58) * mm});
            skLineSegment(sketch, "E4204", {"start": v(2.93, -20.58) * mm, "end": v(2.84, -20.48) * mm});
            skLineSegment(sketch, "E4205", {"start": v(2.84, -20.48) * mm, "end": v(2.77, -20.38) * mm});
            skLineSegment(sketch, "E4206", {"start": v(2.77, -20.38) * mm, "end": v(2.72, -20.28) * mm});
            skLineSegment(sketch, "E4207", {"start": v(2.72, -20.28) * mm, "end": v(2.69, -20.18) * mm});
            skLineSegment(sketch, "E4208", {"start": v(2.69, -20.18) * mm, "end": v(2.66, -20.1) * mm});
            skLineSegment(sketch, "E4209", {"start": v(2.66, -20.1) * mm, "end": v(2.63, -20) * mm});
            skLineSegment(sketch, "E4210", {"start": v(2.63, -20) * mm, "end": v(2.6, -19.93) * mm});
            skLineSegment(sketch, "E4211", {"start": v(2.6, -19.93) * mm, "end": v(2.56, -19.87) * mm});
            skLineSegment(sketch, "E4212", {"start": v(2.56, -19.87) * mm, "end": v(2.41, -19.78) * mm});
            skLineSegment(sketch, "E4213", {"start": v(2.41, -19.78) * mm, "end": v(2.27, -19.82) * mm});
            skLineSegment(sketch, "E4214", {"start": v(2.27, -19.82) * mm, "end": v(2.14, -19.96) * mm});
            skLineSegment(sketch, "E4215", {"start": v(2.14, -19.96) * mm, "end": v(2.03, -20.17) * mm});
            skLineSegment(sketch, "E4216", {"start": v(2.03, -20.17) * mm, "end": v(1.93, -20.42) * mm});
            skLineSegment(sketch, "E4217", {"start": v(1.93, -20.42) * mm, "end": v(1.85, -20.66) * mm});
            skLineSegment(sketch, "E4218", {"start": v(1.85, -20.66) * mm, "end": v(1.79, -20.87) * mm});
            skLineSegment(sketch, "E4219", {"start": v(1.79, -20.87) * mm, "end": v(1.75, -21.02) * mm});
            skLineSegment(sketch, "E4220", {"start": v(1.75, -21.02) * mm, "end": v(1.74, -20.54) * mm});
            skLineSegment(sketch, "E4221", {"start": v(1.74, -20.54) * mm, "end": v(1.8, -20.16) * mm});
            skLineSegment(sketch, "E4222", {"start": v(1.8, -20.16) * mm, "end": v(1.93, -19.86) * mm});
            skLineSegment(sketch, "E4223", {"start": v(1.93, -19.86) * mm, "end": v(2.08, -19.64) * mm});
            skLineSegment(sketch, "E4224", {"start": v(2.08, -19.64) * mm, "end": v(2.24, -19.48) * mm});
            skLineSegment(sketch, "E4225", {"start": v(2.24, -19.48) * mm, "end": v(2.4, -19.37) * mm});
            skLineSegment(sketch, "E4226", {"start": v(2.4, -19.37) * mm, "end": v(2.53, -19.3) * mm});
            skLineSegment(sketch, "E4227", {"start": v(2.53, -19.3) * mm, "end": v(2.6, -19.24) * mm});
            skLineSegment(sketch, "E4228", {"start": v(2.6, -19.24) * mm, "end": v(2.65, -19.18) * mm});
            skLineSegment(sketch, "E4229", {"start": v(2.65, -19.18) * mm, "end": v(2.68, -19.1) * mm});
            skLineSegment(sketch, "E4230", {"start": v(2.68, -19.1) * mm, "end": v(2.7, -18.99) * mm});
            skLineSegment(sketch, "E4231", {"start": v(2.7, -18.99) * mm, "end": v(2.7, -18.88) * mm});
            skLineSegment(sketch, "E4232", {"start": v(2.7, -18.88) * mm, "end": v(2.72, -18.65) * mm});
            skLineSegment(sketch, "E4233", {"start": v(2.72, -18.65) * mm, "end": v(2.73, -18.46) * mm});
            skLineSegment(sketch, "E4234", {"start": v(2.73, -18.46) * mm, "end": v(2.52, -18.37) * mm});
            skLineSegment(sketch, "E4235", {"start": v(2.52, -18.37) * mm, "end": v(2.38, -18.27) * mm});
            skLineSegment(sketch, "E4236", {"start": v(2.38, -18.27) * mm, "end": v(2.3, -18.14) * mm});
            skLineSegment(sketch, "E4237", {"start": v(2.3, -18.14) * mm, "end": v(2.29, -18) * mm});
            skLineSegment(sketch, "E4238", {"start": v(2.29, -18) * mm, "end": v(2.3, -17.83) * mm});
            skLineSegment(sketch, "E4239", {"start": v(2.3, -17.83) * mm, "end": v(2.33, -17.66) * mm});
            skLineSegment(sketch, "E4240", {"start": v(2.33, -17.66) * mm, "end": v(2.37, -17.49) * mm});
            skLineSegment(sketch, "E4241", {"start": v(2.37, -17.49) * mm, "end": v(2.4, -17.3) * mm});
            skLineSegment(sketch, "E4242", {"start": v(2.4, -17.3) * mm, "end": v(2.42, -17.1) * mm});
            skLineSegment(sketch, "E4243", {"start": v(2.42, -17.1) * mm, "end": v(2.43, -16.92) * mm});
            skLineSegment(sketch, "E4244", {"start": v(2.43, -16.92) * mm, "end": v(2.45, -16.74) * mm});
            skLineSegment(sketch, "E4245", {"start": v(2.45, -16.74) * mm, "end": v(2.48, -16.53) * mm});
            skLineSegment(sketch, "E4246", {"start": v(2.48, -16.53) * mm, "end": v(2.54, -16.34) * mm});
            skLineSegment(sketch, "E4247", {"start": v(2.54, -16.34) * mm, "end": v(2.6, -16.19) * mm});
            skLineSegment(sketch, "E4248", {"start": v(2.6, -16.19) * mm, "end": v(2.66, -16.05) * mm});
            skLineSegment(sketch, "E4249", {"start": v(2.66, -16.05) * mm, "end": v(2.72, -15.89) * mm});
            skLineSegment(sketch, "E4250", {"start": v(2.72, -15.89) * mm, "end": v(2.89, -16.58) * mm});
            skLineSegment(sketch, "E4251", {"start": v(2.89, -16.58) * mm, "end": v(2.9, -16.71) * mm});
            skLineSegment(sketch, "E4252", {"start": v(2.9, -16.71) * mm, "end": v(2.92, -16.8) * mm});
            skLineSegment(sketch, "E4253", {"start": v(2.92, -16.8) * mm, "end": v(2.92, -16.88) * mm});
            skLineSegment(sketch, "E4254", {"start": v(2.92, -16.88) * mm, "end": v(2.91, -16.94) * mm});
            skLineSegment(sketch, "E4255", {"start": v(2.91, -16.94) * mm, "end": v(2.86, -17.05) * mm});
            skLineSegment(sketch, "E4256", {"start": v(2.86, -17.05) * mm, "end": v(2.76, -17.23) * mm});
            skLineSegment(sketch, "E4257", {"start": v(2.76, -17.23) * mm, "end": v(2.64, -17.5) * mm});
            skLineSegment(sketch, "E4258", {"start": v(2.64, -17.5) * mm, "end": v(2.59, -17.72) * mm});
            skLineSegment(sketch, "E4259", {"start": v(2.59, -17.72) * mm, "end": v(2.58, -17.91) * mm});
            skLineSegment(sketch, "E4260", {"start": v(2.58, -17.91) * mm, "end": v(2.62, -18.06) * mm});
            skLineSegment(sketch, "E4261", {"start": v(2.62, -18.06) * mm, "end": v(2.68, -18.17) * mm});
            skLineSegment(sketch, "E4262", {"start": v(2.68, -18.17) * mm, "end": v(2.76, -18.22) * mm});
            skLineSegment(sketch, "E4263", {"start": v(2.76, -18.22) * mm, "end": v(2.85, -18.22) * mm});
            skLineSegment(sketch, "E4264", {"start": v(2.85, -18.22) * mm, "end": v(2.94, -18.16) * mm});
            skLineSegment(sketch, "E4265", {"start": v(-3.57, -18.03) * mm, "end": v(-3.48, -17.9) * mm});
            skLineSegment(sketch, "E4266", {"start": v(-3.48, -17.9) * mm, "end": v(-3.36, -17.75) * mm});
            skLineSegment(sketch, "E4267", {"start": v(-3.36, -17.75) * mm, "end": v(-3.27, -17.67) * mm});
            skLineSegment(sketch, "E4268", {"start": v(-3.27, -17.67) * mm, "end": v(-3.17, -17.61) * mm});
            skLineSegment(sketch, "E4269", {"start": v(-3.17, -17.61) * mm, "end": v(-3.05, -17.57) * mm});
            skLineSegment(sketch, "E4270", {"start": v(-3.05, -17.57) * mm, "end": v(-2.9, -17.56) * mm});
            skLineSegment(sketch, "E4271", {"start": v(-2.9, -17.56) * mm, "end": v(-2.77, -17.59) * mm});
            skLineSegment(sketch, "E4272", {"start": v(-2.77, -17.59) * mm, "end": v(-2.67, -17.63) * mm});
            skLineSegment(sketch, "E4273", {"start": v(-2.67, -17.63) * mm, "end": v(-2.59, -17.7) * mm});
            skLineSegment(sketch, "E4274", {"start": v(-2.59, -17.7) * mm, "end": v(-2.54, -17.79) * mm});
            skLineSegment(sketch, "E4275", {"start": v(-2.54, -17.79) * mm, "end": v(-2.5, -17.9) * mm});
            skLineSegment(sketch, "E4276", {"start": v(-2.5, -17.9) * mm, "end": v(-2.49, -18) * mm});
            skLineSegment(sketch, "E4277", {"start": v(-2.49, -18) * mm, "end": v(-2.48, -18.14) * mm});
            skLineSegment(sketch, "E4278", {"start": v(-2.48, -18.14) * mm, "end": v(-2.49, -18.28) * mm});
            skLineSegment(sketch, "E4279", {"start": v(-2.49, -18.28) * mm, "end": v(-2.34, -18.2) * mm});
            skLineSegment(sketch, "E4280", {"start": v(-2.34, -18.2) * mm, "end": v(-2.23, -18.1) * mm});
            skLineSegment(sketch, "E4281", {"start": v(-2.23, -18.1) * mm, "end": v(-2.17, -18) * mm});
            skLineSegment(sketch, "E4282", {"start": v(-2.17, -18) * mm, "end": v(-2.15, -17.88) * mm});
            skLineSegment(sketch, "E4283", {"start": v(-2.15, -17.88) * mm, "end": v(-2.16, -17.75) * mm});
            skLineSegment(sketch, "E4284", {"start": v(-2.16, -17.75) * mm, "end": v(-2.2, -17.6) * mm});
            skLineSegment(sketch, "E4285", {"start": v(-2.2, -17.6) * mm, "end": v(-2.26, -17.42) * mm});
            skLineSegment(sketch, "E4286", {"start": v(-2.26, -17.42) * mm, "end": v(-2.34, -17.23) * mm});
            skLineSegment(sketch, "E4287", {"start": v(-2.34, -17.23) * mm, "end": v(-2.43, -17.06) * mm});
            skLineSegment(sketch, "E4288", {"start": v(-2.43, -17.06) * mm, "end": v(-2.5, -16.96) * mm});
            skLineSegment(sketch, "E4289", {"start": v(-2.5, -16.96) * mm, "end": v(-2.5, -16.9) * mm});
            skLineSegment(sketch, "E4290", {"start": v(-2.5, -16.9) * mm, "end": v(-2.51, -16.84) * mm});
            skLineSegment(sketch, "E4291", {"start": v(-2.51, -16.84) * mm, "end": v(-2.5, -16.75) * mm});
            skLineSegment(sketch, "E4292", {"start": v(-2.5, -16.75) * mm, "end": v(-2.48, -16.62) * mm});
            skLineSegment(sketch, "E4293", {"start": v(-2.48, -16.62) * mm, "end": v(-2.45, -16.44) * mm});
            skLineSegment(sketch, "E4294", {"start": v(-2.45, -16.44) * mm, "end": v(-2.42, -16.25) * mm});
            skLineSegment(sketch, "E4295", {"start": v(-2.42, -16.25) * mm, "end": v(-2.4, -16.16) * mm});
            skLineSegment(sketch, "E4296", {"start": v(-2.4, -16.16) * mm, "end": v(-2.38, -16.07) * mm});
            skLineSegment(sketch, "E4297", {"start": v(-2.38, -16.07) * mm, "end": v(-2.35, -15.99) * mm});
            skLineSegment(sketch, "E4298", {"start": v(-2.35, -15.99) * mm, "end": v(-2.32, -15.9) * mm});
            skLineSegment(sketch, "E4299", {"start": v(-2.32, -15.9) * mm, "end": v(-2.24, -16.06) * mm});
            skLineSegment(sketch, "E4300", {"start": v(-2.24, -16.06) * mm, "end": v(-2.17, -16.19) * mm});
            skLineSegment(sketch, "E4301", {"start": v(-2.17, -16.19) * mm, "end": v(-2.14, -16.26) * mm});
            skLineSegment(sketch, "E4302", {"start": v(-2.14, -16.26) * mm, "end": v(-2.1, -16.33) * mm});
            skLineSegment(sketch, "E4303", {"start": v(-2.1, -16.33) * mm, "end": v(-2.08, -16.42) * mm});
            skLineSegment(sketch, "E4304", {"start": v(-2.08, -16.42) * mm, "end": v(-2.06, -16.53) * mm});
            skLineSegment(sketch, "E4305", {"start": v(-2.06, -16.53) * mm, "end": v(-2.03, -16.73) * mm});
            skLineSegment(sketch, "E4306", {"start": v(-2.03, -16.73) * mm, "end": v(-2.02, -16.95) * mm});
            skLineSegment(sketch, "E4307", {"start": v(-2.02, -16.95) * mm, "end": v(-2.01, -17.15) * mm});
            skLineSegment(sketch, "E4308", {"start": v(-2.01, -17.15) * mm, "end": v(-1.99, -17.34) * mm});
            skLineSegment(sketch, "E4309", {"start": v(-1.99, -17.34) * mm, "end": v(-1.95, -17.52) * mm});
            skLineSegment(sketch, "E4310", {"start": v(-1.95, -17.52) * mm, "end": v(-1.9, -17.7) * mm});
            skLineSegment(sketch, "E4311", {"start": v(-1.9, -17.7) * mm, "end": v(-1.88, -17.88) * mm});
            skLineSegment(sketch, "E4312", {"start": v(-1.88, -17.88) * mm, "end": v(-1.88, -18.04) * mm});
            skLineSegment(sketch, "E4313", {"start": v(-1.88, -18.04) * mm, "end": v(-1.9, -18.18) * mm});
            skLineSegment(sketch, "E4314", {"start": v(-1.9, -18.18) * mm, "end": v(-1.99, -18.3) * mm});
            skLineSegment(sketch, "E4315", {"start": v(-1.99, -18.3) * mm, "end": v(-2.12, -18.39) * mm});
            skLineSegment(sketch, "E4316", {"start": v(-2.12, -18.39) * mm, "end": v(-2.32, -18.45) * mm});
            skLineSegment(sketch, "E4317", {"start": v(-2.32, -18.45) * mm, "end": v(-2.3, -18.73) * mm});
            skLineSegment(sketch, "E4318", {"start": v(-2.3, -18.73) * mm, "end": v(-2.28, -18.93) * mm});
            skLineSegment(sketch, "E4319", {"start": v(-2.28, -18.93) * mm, "end": v(-2.26, -19.07) * mm});
            skLineSegment(sketch, "E4320", {"start": v(-2.26, -19.07) * mm, "end": v(-2.23, -19.16) * mm});
            skLineSegment(sketch, "E4321", {"start": v(-2.23, -19.16) * mm, "end": v(-2.19, -19.22) * mm});
            skLineSegment(sketch, "E4322", {"start": v(-2.19, -19.22) * mm, "end": v(-2.13, -19.27) * mm});
            skLineSegment(sketch, "E4323", {"start": v(-2.13, -19.27) * mm, "end": v(-2.04, -19.32) * mm});
            skLineSegment(sketch, "E4324", {"start": v(-2.04, -19.32) * mm, "end": v(-1.92, -19.4) * mm});
            skLineSegment(sketch, "E4325", {"start": v(-1.92, -19.4) * mm, "end": v(-1.76, -19.52) * mm});
            skLineSegment(sketch, "E4326", {"start": v(-1.76, -19.52) * mm, "end": v(-1.62, -19.69) * mm});
            skLineSegment(sketch, "E4327", {"start": v(-1.62, -19.69) * mm, "end": v(-1.5, -19.87) * mm});
            skLineSegment(sketch, "E4328", {"start": v(-1.5, -19.87) * mm, "end": v(-1.42, -20.08) * mm});
            skLineSegment(sketch, "E4329", {"start": v(-1.42, -20.08) * mm, "end": v(-1.36, -20.3) * mm});
            skLineSegment(sketch, "E4330", {"start": v(-1.36, -20.3) * mm, "end": v(-1.33, -20.54) * mm});
            skLineSegment(sketch, "E4331", {"start": v(-1.33, -20.54) * mm, "end": v(-1.32, -20.77) * mm});
            skLineSegment(sketch, "E4332", {"start": v(-1.32, -20.77) * mm, "end": v(-1.34, -21.01) * mm});
            skLineSegment(sketch, "E4333", {"start": v(-1.34, -21.01) * mm, "end": v(-1.35, -20.88) * mm});
            skLineSegment(sketch, "E4334", {"start": v(-1.35, -20.88) * mm, "end": v(-1.4, -20.69) * mm});
            skLineSegment(sketch, "E4335", {"start": v(-1.4, -20.69) * mm, "end": v(-1.48, -20.46) * mm});
            skLineSegment(sketch, "E4336", {"start": v(-1.48, -20.46) * mm, "end": v(-1.58, -20.22) * mm});
            skLineSegment(sketch, "E4337", {"start": v(-1.58, -20.22) * mm, "end": v(-1.7, -20.01) * mm});
            skLineSegment(sketch, "E4338", {"start": v(-1.7, -20.01) * mm, "end": v(-1.83, -19.86) * mm});
            skLineSegment(sketch, "E4339", {"start": v(-1.83, -19.86) * mm, "end": v(-1.98, -19.8) * mm});
            skLineSegment(sketch, "E4340", {"start": v(-1.98, -19.8) * mm, "end": v(-2.12, -19.85) * mm});
            skLineSegment(sketch, "E4341", {"start": v(-2.12, -19.85) * mm, "end": v(-2.16, -19.9) * mm});
            skLineSegment(sketch, "E4342", {"start": v(-2.16, -19.9) * mm, "end": v(-2.19, -19.97) * mm});
            skLineSegment(sketch, "E4343", {"start": v(-2.19, -19.97) * mm, "end": v(-2.22, -20.05) * mm});
            skLineSegment(sketch, "E4344", {"start": v(-2.22, -20.05) * mm, "end": v(-2.26, -20.16) * mm});
            skLineSegment(sketch, "E4345", {"start": v(-2.26, -20.16) * mm, "end": v(-2.3, -20.26) * mm});
            skLineSegment(sketch, "E4346", {"start": v(-2.3, -20.26) * mm, "end": v(-2.35, -20.37) * mm});
            skLineSegment(sketch, "E4347", {"start": v(-2.35, -20.37) * mm, "end": v(-2.41, -20.47) * mm});
            skLineSegment(sketch, "E4348", {"start": v(-2.41, -20.47) * mm, "end": v(-2.5, -20.56) * mm});
            skLineSegment(sketch, "E4349", {"start": v(-2.5, -20.56) * mm, "end": v(-2.6, -20.64) * mm});
            skLineSegment(sketch, "E4350", {"start": v(-2.6, -20.64) * mm, "end": v(-2.69, -20.7) * mm});
            skLineSegment(sketch, "E4351", {"start": v(-2.69, -20.7) * mm, "end": v(-2.78, -20.73) * mm});
            skLineSegment(sketch, "E4352", {"start": v(-2.78, -20.73) * mm, "end": v(-2.88, -20.74) * mm});
            skLineSegment(sketch, "E4353", {"start": v(-2.88, -20.74) * mm, "end": v(-2.98, -20.74) * mm});
            skLineSegment(sketch, "E4354", {"start": v(-2.98, -20.74) * mm, "end": v(-3.1, -20.73) * mm});
            skLineSegment(sketch, "E4355", {"start": v(-3.1, -20.73) * mm, "end": v(-3.22, -20.7) * mm});
            skLineSegment(sketch, "E4356", {"start": v(-3.22, -20.7) * mm, "end": v(-3.35, -20.68) * mm});
            skLineSegment(sketch, "E4357", {"start": v(-3.35, -20.68) * mm, "end": v(-3.3, -20.86) * mm});
            skLineSegment(sketch, "E4358", {"start": v(-3.3, -20.86) * mm, "end": v(-3.21, -21.03) * mm});
            skLineSegment(sketch, "E4359", {"start": v(-3.21, -21.03) * mm, "end": v(-3.12, -21.19) * mm});
            skLineSegment(sketch, "E4360", {"start": v(-3.12, -21.19) * mm, "end": v(-3.01, -21.34) * mm});
            skLineSegment(sketch, "E4361", {"start": v(-3.01, -21.34) * mm, "end": v(-2.9, -21.47) * mm});
            skLineSegment(sketch, "E4362", {"start": v(-2.9, -21.47) * mm, "end": v(-2.76, -21.6) * mm});
            skLineSegment(sketch, "E4363", {"start": v(-2.76, -21.6) * mm, "end": v(-2.61, -21.69) * mm});
            skLineSegment(sketch, "E4364", {"start": v(-2.61, -21.69) * mm, "end": v(-2.46, -21.76) * mm});
            skLineSegment(sketch, "E4365", {"start": v(-2.46, -21.76) * mm, "end": v(-2.34, -21.8) * mm});
            skLineSegment(sketch, "E4366", {"start": v(-2.34, -21.8) * mm, "end": v(-2.23, -21.83) * mm});
            skLineSegment(sketch, "E4367", {"start": v(-2.23, -21.83) * mm, "end": v(-2.14, -21.84) * mm});
            skLineSegment(sketch, "E4368", {"start": v(-2.14, -21.84) * mm, "end": v(-2.05, -21.84) * mm});
            skLineSegment(sketch, "E4369", {"start": v(-2.05, -21.84) * mm, "end": v(-1.86, -21.8) * mm});
            skLineSegment(sketch, "E4370", {"start": v(-1.86, -21.8) * mm, "end": v(-1.63, -21.76) * mm});
            skLineSegment(sketch, "E4371", {"start": v(-1.63, -21.76) * mm, "end": v(-1.51, -21.73) * mm});
            skLineSegment(sketch, "E4372", {"start": v(-1.51, -21.73) * mm, "end": v(-1.42, -21.7) * mm});
            skLineSegment(sketch, "E4373", {"start": v(-1.42, -21.7) * mm, "end": v(-1.34, -21.65) * mm});
            skLineSegment(sketch, "E4374", {"start": v(-1.34, -21.65) * mm, "end": v(-1.28, -21.6) * mm});
            skLineSegment(sketch, "E4375", {"start": v(-1.28, -21.6) * mm, "end": v(-1.23, -21.54) * mm});
            skLineSegment(sketch, "E4376", {"start": v(-1.23, -21.54) * mm, "end": v(-1.2, -21.46) * mm});
            skLineSegment(sketch, "E4377", {"start": v(-1.2, -21.46) * mm, "end": v(-1.17, -21.36) * mm});
            skLineSegment(sketch, "E4378", {"start": v(-1.17, -21.36) * mm, "end": v(-1.14, -21.25) * mm});
            skLineSegment(sketch, "E4379", {"start": v(-1.14, -21.25) * mm, "end": v(-1.06, -20.76) * mm});
            skLineSegment(sketch, "E4380", {"start": v(-1.06, -20.76) * mm, "end": v(-1, -20.26) * mm});
            skLineSegment(sketch, "E4381", {"start": v(-1, -20.26) * mm, "end": v(-0.98, -19.75) * mm});
            skLineSegment(sketch, "E4382", {"start": v(-0.98, -19.75) * mm, "end": v(-0.97, -19.23) * mm});
            skLineSegment(sketch, "E4383", {"start": v(-0.97, -19.23) * mm, "end": v(-1, -18.72) * mm});
            skLineSegment(sketch, "E4384", {"start": v(-1, -18.72) * mm, "end": v(-1.04, -18.21) * mm});
            skLineSegment(sketch, "E4385", {"start": v(-1.04, -18.21) * mm, "end": v(-1.12, -17.72) * mm});
            skLineSegment(sketch, "E4386", {"start": v(-1.12, -17.72) * mm, "end": v(-1.23, -17.24) * mm});
            skLineSegment(sketch, "E4387", {"start": v(-1.23, -17.24) * mm, "end": v(-1.31, -16.99) * mm});
            skLineSegment(sketch, "E4388", {"start": v(-1.31, -16.99) * mm, "end": v(-1.43, -16.7) * mm});
            skLineSegment(sketch, "E4389", {"start": v(-1.43, -16.7) * mm, "end": v(-1.58, -16.38) * mm});
            skLineSegment(sketch, "E4390", {"start": v(-1.58, -16.38) * mm, "end": v(-1.76, -16.07) * mm});
            skLineSegment(sketch, "E4391", {"start": v(-1.76, -16.07) * mm, "end": v(-1.97, -15.78) * mm});
            skLineSegment(sketch, "E4392", {"start": v(-1.97, -15.78) * mm, "end": v(-2.2, -15.53) * mm});
            skLineSegment(sketch, "E4393", {"start": v(-2.2, -15.53) * mm, "end": v(-2.44, -15.36) * mm});
            skLineSegment(sketch, "E4394", {"start": v(-2.44, -15.36) * mm, "end": v(-2.69, -15.27) * mm});
            skLineSegment(sketch, "E4395", {"start": v(-2.69, -15.27) * mm, "end": v(-3.03, -15.31) * mm});
            skLineSegment(sketch, "E4396", {"start": v(-3.03, -15.31) * mm, "end": v(-3.3, -15.52) * mm});
            skLineSegment(sketch, "E4397", {"start": v(-3.3, -15.52) * mm, "end": v(-3.5, -15.86) * mm});
            skLineSegment(sketch, "E4398", {"start": v(-3.5, -15.86) * mm, "end": v(-3.63, -16.28) * mm});
            skLineSegment(sketch, "E4399", {"start": v(-3.63, -16.28) * mm, "end": v(-3.7, -16.75) * mm});
            skLineSegment(sketch, "E4400", {"start": v(-3.7, -16.75) * mm, "end": v(-3.7, -17.22) * mm});
            skLineSegment(sketch, "E4401", {"start": v(-3.7, -17.22) * mm, "end": v(-3.66, -17.66) * mm});
            skLineSegment(sketch, "E4402", {"start": v(-3.66, -17.66) * mm, "end": v(-3.57, -18.03) * mm});
            skLineSegment(sketch, "E4403", {"start": v(0.35, -17.81) * mm, "end": v(0.35, -22.62) * mm});
            skLineSegment(sketch, "E4404", {"start": v(0.35, -22.62) * mm, "end": v(0.35, -22.78) * mm});
            skLineSegment(sketch, "E4405", {"start": v(0.35, -22.78) * mm, "end": v(0.34, -23) * mm});
            skLineSegment(sketch, "E4406", {"start": v(0.34, -23) * mm, "end": v(0.34, -23.26) * mm});
            skLineSegment(sketch, "E4407", {"start": v(0.34, -23.26) * mm, "end": v(0.35, -23.53) * mm});
            skLineSegment(sketch, "E4408", {"start": v(0.35, -23.53) * mm, "end": v(0.37, -23.8) * mm});
            skLineSegment(sketch, "E4409", {"start": v(0.37, -23.8) * mm, "end": v(0.4, -24.03) * mm});
            skLineSegment(sketch, "E4410", {"start": v(0.4, -24.03) * mm, "end": v(0.45, -24.21) * mm});
            skLineSegment(sketch, "E4411", {"start": v(0.45, -24.21) * mm, "end": v(0.53, -24.32) * mm});
            skLineSegment(sketch, "E4412", {"start": v(0.53, -24.32) * mm, "end": v(0.63, -24.4) * mm});
            skLineSegment(sketch, "E4413", {"start": v(0.63, -24.4) * mm, "end": v(0.78, -24.48) * mm});
            skLineSegment(sketch, "E4414", {"start": v(0.78, -24.48) * mm, "end": v(0.95, -24.58) * mm});
            skLineSegment(sketch, "E4415", {"start": v(0.95, -24.58) * mm, "end": v(1.15, -24.68) * mm});
            skLineSegment(sketch, "E4416", {"start": v(1.15, -24.68) * mm, "end": v(1.36, -24.76) * mm});
            skLineSegment(sketch, "E4417", {"start": v(1.36, -24.76) * mm, "end": v(1.56, -24.82) * mm});
            skLineSegment(sketch, "E4418", {"start": v(1.56, -24.82) * mm, "end": v(1.75, -24.84) * mm});
            skLineSegment(sketch, "E4419", {"start": v(1.75, -24.84) * mm, "end": v(1.92, -24.81) * mm});
            skLineSegment(sketch, "E4420", {"start": v(1.92, -24.81) * mm, "end": v(1.97, -24.78) * mm});
            skLineSegment(sketch, "E4421", {"start": v(1.97, -24.78) * mm, "end": v(2.03, -24.73) * mm});
            skLineSegment(sketch, "E4422", {"start": v(2.03, -24.73) * mm, "end": v(2.1, -24.67) * mm});
            skLineSegment(sketch, "E4423", {"start": v(2.1, -24.67) * mm, "end": v(2.16, -24.6) * mm});
            skLineSegment(sketch, "E4424", {"start": v(2.16, -24.6) * mm, "end": v(2.28, -24.44) * mm});
            skLineSegment(sketch, "E4425", {"start": v(2.28, -24.44) * mm, "end": v(2.36, -24.33) * mm});
            skLineSegment(sketch, "E4426", {"start": v(2.36, -24.33) * mm, "end": v(2.45, -24.2) * mm});
            skLineSegment(sketch, "E4427", {"start": v(2.45, -24.2) * mm, "end": v(2.57, -24.03) * mm});
            skLineSegment(sketch, "E4428", {"start": v(2.57, -24.03) * mm, "end": v(2.67, -23.87) * mm});
            skLineSegment(sketch, "E4429", {"start": v(2.67, -23.87) * mm, "end": v(2.73, -23.76) * mm});
            skLineSegment(sketch, "E4430", {"start": v(2.73, -23.76) * mm, "end": v(2.74, -23.65) * mm});
            skLineSegment(sketch, "E4431", {"start": v(2.74, -23.65) * mm, "end": v(2.71, -23.44) * mm});
            skLineSegment(sketch, "E4432", {"start": v(2.71, -23.44) * mm, "end": v(2.67, -23.17) * mm});
            skLineSegment(sketch, "E4433", {"start": v(2.67, -23.17) * mm, "end": v(2.62, -22.88) * mm});
            skLineSegment(sketch, "E4434", {"start": v(2.62, -22.88) * mm, "end": v(2.56, -22.6) * mm});
            skLineSegment(sketch, "E4435", {"start": v(2.56, -22.6) * mm, "end": v(2.5, -22.36) * mm});
            skLineSegment(sketch, "E4436", {"start": v(2.5, -22.36) * mm, "end": v(2.46, -22.21) * mm});
            skLineSegment(sketch, "E4437", {"start": v(2.46, -22.21) * mm, "end": v(2.42, -22.18) * mm});
            skLineSegment(sketch, "E4438", {"start": v(2.42, -22.18) * mm, "end": v(2.36, -22.16) * mm});
            skLineSegment(sketch, "E4439", {"start": v(2.36, -22.16) * mm, "end": v(2.32, -22.15) * mm});
            skLineSegment(sketch, "E4440", {"start": v(2.32, -22.15) * mm, "end": v(2.07, -22.1) * mm});
            skLineSegment(sketch, "E4441", {"start": v(2.07, -22.1) * mm, "end": v(1.84, -22.07) * mm});
            skLineSegment(sketch, "E4442", {"start": v(1.84, -22.07) * mm, "end": v(1.65, -22.03) * mm});
            skLineSegment(sketch, "E4443", {"start": v(1.65, -22.03) * mm, "end": v(1.49, -21.93) * mm});
            skLineSegment(sketch, "E4444", {"start": v(1.49, -21.93) * mm, "end": v(1.35, -21.75) * mm});
            skLineSegment(sketch, "E4445", {"start": v(1.35, -21.75) * mm, "end": v(1.25, -21.45) * mm});
            skLineSegment(sketch, "E4446", {"start": v(1.25, -21.45) * mm, "end": v(1.17, -21) * mm});
            skLineSegment(sketch, "E4447", {"start": v(1.17, -21) * mm, "end": v(1.13, -20.36) * mm});
            skLineSegment(sketch, "E4448", {"start": v(1.13, -20.36) * mm, "end": v(1.12, -20.16) * mm});
            skLineSegment(sketch, "E4449", {"start": v(1.12, -20.16) * mm, "end": v(1.11, -19.97) * mm});
            skLineSegment(sketch, "E4450", {"start": v(1.11, -19.97) * mm, "end": v(1.1, -19.78) * mm});
            skLineSegment(sketch, "E4451", {"start": v(1.1, -19.78) * mm, "end": v(1.1, -19.59) * mm});
            skLineSegment(sketch, "E4452", {"start": v(1.1, -19.59) * mm, "end": v(1.1, -19.4) * mm});
            skLineSegment(sketch, "E4453", {"start": v(1.1, -19.4) * mm, "end": v(1.1, -19.2) * mm});
            skLineSegment(sketch, "E4454", {"start": v(1.1, -19.2) * mm, "end": v(1.12, -19.01) * mm});
            skLineSegment(sketch, "E4455", {"start": v(1.12, -19.01) * mm, "end": v(1.12, -18.82) * mm});
            skLineSegment(sketch, "E4456", {"start": v(1.12, -18.82) * mm, "end": v(1.15, -18.5) * mm});
            skLineSegment(sketch, "E4457", {"start": v(1.15, -18.5) * mm, "end": v(1.16, -18.3) * mm});
            skLineSegment(sketch, "E4458", {"start": v(1.16, -18.3) * mm, "end": v(1.17, -18.2) * mm});
            skLineSegment(sketch, "E4459", {"start": v(1.17, -18.2) * mm, "end": v(1.16, -18.15) * mm});
            skLineSegment(sketch, "E4460", {"start": v(1.16, -18.15) * mm, "end": v(1.13, -18.1) * mm});
            skLineSegment(sketch, "E4461", {"start": v(1.13, -18.1) * mm, "end": v(1.08, -18.02) * mm});
            skLineSegment(sketch, "E4462", {"start": v(1.08, -18.02) * mm, "end": v(1, -17.86) * mm});
            skLineSegment(sketch, "E4463", {"start": v(1, -17.86) * mm, "end": v(0.9, -17.58) * mm});
            skLineSegment(sketch, "E4464", {"start": v(0.9, -17.58) * mm, "end": v(0.35, -17.81) * mm});
            skLineSegment(sketch, "E4465", {"start": v(13.84, -1.02) * mm, "end": v(13.75, -1.2) * mm});
            skLineSegment(sketch, "E4466", {"start": v(13.75, -1.2) * mm, "end": v(13.63, -1.39) * mm});
            skLineSegment(sketch, "E4467", {"start": v(13.63, -1.39) * mm, "end": v(13.48, -1.57) * mm});
            skLineSegment(sketch, "E4468", {"start": v(13.48, -1.57) * mm, "end": v(13.32, -1.73) * mm});
            skLineSegment(sketch, "E4469", {"start": v(13.32, -1.73) * mm, "end": v(13.03, -2.01) * mm});
            skLineSegment(sketch, "E4470", {"start": v(13.03, -2.01) * mm, "end": v(12.84, -2.2) * mm});
            skLineSegment(sketch, "E4471", {"start": v(12.84, -2.2) * mm, "end": v(12.82, -2.22) * mm});
            skLineSegment(sketch, "E4472", {"start": v(12.82, -2.22) * mm, "end": v(12.8, -2.25) * mm});
            skLineSegment(sketch, "E4473", {"start": v(12.8, -2.25) * mm, "end": v(13, -2.3) * mm});
            skLineSegment(sketch, "E4474", {"start": v(13, -2.3) * mm, "end": v(13.15, -2.34) * mm});
            skLineSegment(sketch, "E4475", {"start": v(13.15, -2.34) * mm, "end": v(13.34, -2.4) * mm});
            skLineSegment(sketch, "E4476", {"start": v(13.34, -2.4) * mm, "end": v(13.65, -2.45) * mm});
            skLineSegment(sketch, "E4477", {"start": v(13.65, -2.45) * mm, "end": v(14.2, -2.51) * mm});
            skLineSegment(sketch, "E4478", {"start": v(14.2, -2.51) * mm, "end": v(14.82, -2.53) * mm});
            skLineSegment(sketch, "E4479", {"start": v(14.82, -2.53) * mm, "end": v(15.47, -2.5) * mm});
            skLineSegment(sketch, "E4480", {"start": v(15.47, -2.5) * mm, "end": v(16.13, -2.44) * mm});
            skLineSegment(sketch, "E4481", {"start": v(16.13, -2.44) * mm, "end": v(16.78, -2.35) * mm});
            skLineSegment(sketch, "E4482", {"start": v(16.78, -2.35) * mm, "end": v(17.4, -2.23) * mm});
            skLineSegment(sketch, "E4483", {"start": v(17.4, -2.23) * mm, "end": v(17.98, -2.09) * mm});
            skLineSegment(sketch, "E4484", {"start": v(17.98, -2.09) * mm, "end": v(18.48, -1.93) * mm});
            skLineSegment(sketch, "E4485", {"start": v(18.48, -1.93) * mm, "end": v(18.68, -1.86) * mm});
            skLineSegment(sketch, "E4486", {"start": v(18.68, -1.86) * mm, "end": v(18.86, -1.77) * mm});
            skLineSegment(sketch, "E4487", {"start": v(18.86, -1.77) * mm, "end": v(19, -1.68) * mm});
            skLineSegment(sketch, "E4488", {"start": v(19, -1.68) * mm, "end": v(19.14, -1.57) * mm});
            skLineSegment(sketch, "E4489", {"start": v(19.14, -1.57) * mm, "end": v(19.26, -1.45) * mm});
            skLineSegment(sketch, "E4490", {"start": v(19.26, -1.45) * mm, "end": v(19.39, -1.3) * mm});
            skLineSegment(sketch, "E4491", {"start": v(19.39, -1.3) * mm, "end": v(19.51, -1.14) * mm});
            skLineSegment(sketch, "E4492", {"start": v(19.51, -1.14) * mm, "end": v(19.65, -0.94) * mm});
            skLineSegment(sketch, "E4493", {"start": v(19.65, -0.94) * mm, "end": v(19.76, -0.78) * mm});
            skLineSegment(sketch, "E4494", {"start": v(19.76, -0.78) * mm, "end": v(19.86, -0.6) * mm});
            skLineSegment(sketch, "E4495", {"start": v(19.86, -0.6) * mm, "end": v(19.95, -0.4) * mm});
            skLineSegment(sketch, "E4496", {"start": v(19.95, -0.4) * mm, "end": v(20.03, -0.21) * mm});
            skLineSegment(sketch, "E4497", {"start": v(20.03, -0.21) * mm, "end": v(20.1, 0) * mm});
            skLineSegment(sketch, "E4498", {"start": v(20.1, 0) * mm, "end": v(20.14, 0.22) * mm});
            skLineSegment(sketch, "E4499", {"start": v(20.14, 0.22) * mm, "end": v(20.17, 0.44) * mm});
            skLineSegment(sketch, "E4500", {"start": v(20.17, 0.44) * mm, "end": v(20.18, 0.67) * mm});
            skLineSegment(sketch, "E4501", {"start": v(20.18, 0.67) * mm, "end": v(19.74, 0.3) * mm});
            skLineSegment(sketch, "E4502", {"start": v(19.74, 0.3) * mm, "end": v(19.24, -0.05) * mm});
            skLineSegment(sketch, "E4503", {"start": v(19.24, -0.05) * mm, "end": v(18.7, -0.35) * mm});
            skLineSegment(sketch, "E4504", {"start": v(18.7, -0.35) * mm, "end": v(18.11, -0.61) * mm});
            skLineSegment(sketch, "E4505", {"start": v(18.11, -0.61) * mm, "end": v(17.5, -0.83) * mm});
            skLineSegment(sketch, "E4506", {"start": v(17.5, -0.83) * mm, "end": v(16.9, -1) * mm});
            skLineSegment(sketch, "E4507", {"start": v(16.9, -1) * mm, "end": v(16.29, -1.11) * mm});
            skLineSegment(sketch, "E4508", {"start": v(16.29, -1.11) * mm, "end": v(15.7, -1.17) * mm});
            skLineSegment(sketch, "E4509", {"start": v(15.7, -1.17) * mm, "end": v(15.4, -1.18) * mm});
            skLineSegment(sketch, "E4510", {"start": v(15.4, -1.18) * mm, "end": v(15.15, -1.18) * mm});
            skLineSegment(sketch, "E4511", {"start": v(15.15, -1.18) * mm, "end": v(14.93, -1.17) * mm});
            skLineSegment(sketch, "E4512", {"start": v(14.93, -1.17) * mm, "end": v(14.73, -1.16) * mm});
            skLineSegment(sketch, "E4513", {"start": v(14.73, -1.16) * mm, "end": v(14.53, -1.13) * mm});
            skLineSegment(sketch, "E4514", {"start": v(14.53, -1.13) * mm, "end": v(14.32, -1.1) * mm});
            skLineSegment(sketch, "E4515", {"start": v(14.32, -1.1) * mm, "end": v(14.1, -1.06) * mm});
            skLineSegment(sketch, "E4516", {"start": v(14.1, -1.06) * mm, "end": v(13.84, -1.02) * mm});
            skLineSegment(sketch, "E4517", {"start": v(-12.8, -2.18) * mm, "end": v(-12.88, -2.14) * mm});
            skLineSegment(sketch, "E4518", {"start": v(-12.88, -2.14) * mm, "end": v(-12.96, -2.09) * mm});
            skLineSegment(sketch, "E4519", {"start": v(-12.96, -2.09) * mm, "end": v(-13.04, -2.02) * mm});
            skLineSegment(sketch, "E4520", {"start": v(-13.04, -2.02) * mm, "end": v(-13.12, -1.95) * mm});
            skLineSegment(sketch, "E4521", {"start": v(-13.12, -1.95) * mm, "end": v(-13.26, -1.8) * mm});
            skLineSegment(sketch, "E4522", {"start": v(-13.26, -1.8) * mm, "end": v(-13.38, -1.67) * mm});
            skLineSegment(sketch, "E4523", {"start": v(-13.38, -1.67) * mm, "end": v(-13.53, -1.5) * mm});
            skLineSegment(sketch, "E4524", {"start": v(-13.53, -1.5) * mm, "end": v(-13.65, -1.32) * mm});
            skLineSegment(sketch, "E4525", {"start": v(-13.65, -1.32) * mm, "end": v(-13.76, -1.17) * mm});
            skLineSegment(sketch, "E4526", {"start": v(-13.76, -1.17) * mm, "end": v(-13.86, -1.03) * mm});
            skLineSegment(sketch, "E4527", {"start": v(-13.86, -1.03) * mm, "end": v(-14.13, -1.07) * mm});
            skLineSegment(sketch, "E4528", {"start": v(-14.13, -1.07) * mm, "end": v(-14.34, -1.1) * mm});
            skLineSegment(sketch, "E4529", {"start": v(-14.34, -1.1) * mm, "end": v(-14.52, -1.14) * mm});
            skLineSegment(sketch, "E4530", {"start": v(-14.52, -1.14) * mm, "end": v(-14.69, -1.16) * mm});
            skLineSegment(sketch, "E4531", {"start": v(-14.69, -1.16) * mm, "end": v(-14.86, -1.18) * mm});
            skLineSegment(sketch, "E4532", {"start": v(-14.86, -1.18) * mm, "end": v(-15.08, -1.2) * mm});
            skLineSegment(sketch, "E4533", {"start": v(-15.08, -1.2) * mm, "end": v(-15.36, -1.19) * mm});
            skLineSegment(sketch, "E4534", {"start": v(-15.36, -1.19) * mm, "end": v(-15.73, -1.17) * mm});
            skLineSegment(sketch, "E4535", {"start": v(-15.73, -1.17) * mm, "end": v(-16.16, -1.13) * mm});
            skLineSegment(sketch, "E4536", {"start": v(-16.16, -1.13) * mm, "end": v(-16.59, -1.06) * mm});
            skLineSegment(sketch, "E4537", {"start": v(-16.59, -1.06) * mm, "end": v(-17, -0.97) * mm});
            skLineSegment(sketch, "E4538", {"start": v(-17, -0.97) * mm, "end": v(-17.4, -0.86) * mm});
            skLineSegment(sketch, "E4539", {"start": v(-17.4, -0.86) * mm, "end": v(-17.79, -0.72) * mm});
            skLineSegment(sketch, "E4540", {"start": v(-17.79, -0.72) * mm, "end": v(-18.18, -0.57) * mm});
            skLineSegment(sketch, "E4541", {"start": v(-18.18, -0.57) * mm, "end": v(-18.56, -0.4) * mm});
            skLineSegment(sketch, "E4542", {"start": v(-18.56, -0.4) * mm, "end": v(-18.94, -0.22) * mm});
            skLineSegment(sketch, "E4543", {"start": v(-18.94, -0.22) * mm, "end": v(-19.19, -0.09) * mm});
            skLineSegment(sketch, "E4544", {"start": v(-19.19, -0.09) * mm, "end": v(-19.4, 0.05) * mm});
            skLineSegment(sketch, "E4545", {"start": v(-19.4, 0.05) * mm, "end": v(-19.6, 0.19) * mm});
            skLineSegment(sketch, "E4546", {"start": v(-19.6, 0.19) * mm, "end": v(-19.76, 0.32) * mm});
            skLineSegment(sketch, "E4547", {"start": v(-19.76, 0.32) * mm, "end": v(-19.9, 0.43) * mm});
            skLineSegment(sketch, "E4548", {"start": v(-19.9, 0.43) * mm, "end": v(-20, 0.53) * mm});
            skLineSegment(sketch, "E4549", {"start": v(-20, 0.53) * mm, "end": v(-20.1, 0.6) * mm});
            skLineSegment(sketch, "E4550", {"start": v(-20.1, 0.6) * mm, "end": v(-20.17, 0.65) * mm});
            skLineSegment(sketch, "E4551", {"start": v(-20.17, 0.65) * mm, "end": v(-20.14, 0.26) * mm});
            skLineSegment(sketch, "E4552", {"start": v(-20.14, 0.26) * mm, "end": v(-20.07, -0.08) * mm});
            skLineSegment(sketch, "E4553", {"start": v(-20.07, -0.08) * mm, "end": v(-19.96, -0.4) * mm});
            skLineSegment(sketch, "E4554", {"start": v(-19.96, -0.4) * mm, "end": v(-19.83, -0.69) * mm});
            skLineSegment(sketch, "E4555", {"start": v(-19.83, -0.69) * mm, "end": v(-19.66, -0.95) * mm});
            skLineSegment(sketch, "E4556", {"start": v(-19.66, -0.95) * mm, "end": v(-19.47, -1.2) * mm});
            skLineSegment(sketch, "E4557", {"start": v(-19.47, -1.2) * mm, "end": v(-19.26, -1.43) * mm});
            skLineSegment(sketch, "E4558", {"start": v(-19.26, -1.43) * mm, "end": v(-19.03, -1.65) * mm});
            skLineSegment(sketch, "E4559", {"start": v(-19.03, -1.65) * mm, "end": v(-18.89, -1.76) * mm});
            skLineSegment(sketch, "E4560", {"start": v(-18.89, -1.76) * mm, "end": v(-18.71, -1.86) * mm});
            skLineSegment(sketch, "E4561", {"start": v(-18.71, -1.86) * mm, "end": v(-18.52, -1.93) * mm});
            skLineSegment(sketch, "E4562", {"start": v(-18.52, -1.93) * mm, "end": v(-18.31, -2) * mm});
            skLineSegment(sketch, "E4563", {"start": v(-18.31, -2) * mm, "end": v(-18.1, -2.06) * mm});
            skLineSegment(sketch, "E4564", {"start": v(-18.1, -2.06) * mm, "end": v(-17.89, -2.1) * mm});
            skLineSegment(sketch, "E4565", {"start": v(-17.89, -2.1) * mm, "end": v(-17.68, -2.15) * mm});
            skLineSegment(sketch, "E4566", {"start": v(-17.68, -2.15) * mm, "end": v(-17.5, -2.2) * mm});
            skLineSegment(sketch, "E4567", {"start": v(-17.5, -2.2) * mm, "end": v(-16.99, -2.32) * mm});
            skLineSegment(sketch, "E4568", {"start": v(-16.99, -2.32) * mm, "end": v(-15.15, -2.52) * mm});
            skLineSegment(sketch, "E4569", {"start": v(-15.15, -2.52) * mm, "end": v(-14.9, -2.53) * mm});
            skLineSegment(sketch, "E4570", {"start": v(-14.9, -2.53) * mm, "end": v(-14.65, -2.53) * mm});
            skLineSegment(sketch, "E4571", {"start": v(-14.65, -2.53) * mm, "end": v(-14.42, -2.52) * mm});
            skLineSegment(sketch, "E4572", {"start": v(-14.42, -2.52) * mm, "end": v(-14.2, -2.5) * mm});
            skLineSegment(sketch, "E4573", {"start": v(-14.2, -2.5) * mm, "end": v(-13.97, -2.49) * mm});
            skLineSegment(sketch, "E4574", {"start": v(-13.97, -2.49) * mm, "end": v(-13.74, -2.45) * mm});
            skLineSegment(sketch, "E4575", {"start": v(-13.74, -2.45) * mm, "end": v(-13.5, -2.42) * mm});
            skLineSegment(sketch, "E4576", {"start": v(-13.5, -2.42) * mm, "end": v(-13.26, -2.37) * mm});
            skLineSegment(sketch, "E4577", {"start": v(-13.26, -2.37) * mm, "end": v(-13, -2.33) * mm});
            skLineSegment(sketch, "E4578", {"start": v(-13, -2.33) * mm, "end": v(-12.93, -2.3) * mm});
            skLineSegment(sketch, "E4579", {"start": v(-12.93, -2.3) * mm, "end": v(-12.88, -2.28) * mm});
            skLineSegment(sketch, "E4580", {"start": v(-12.88, -2.28) * mm, "end": v(-12.84, -2.24) * mm});
            skLineSegment(sketch, "E4581", {"start": v(-12.84, -2.24) * mm, "end": v(-12.8, -2.18) * mm});
            skLineSegment(sketch, "E4582", {"start": v(-2.1, -22.17) * mm, "end": v(-2.35, -23.38) * mm});
            skLineSegment(sketch, "E4583", {"start": v(-2.35, -23.38) * mm, "end": v(-2.37, -23.53) * mm});
            skLineSegment(sketch, "E4584", {"start": v(-2.37, -23.53) * mm, "end": v(-2.38, -23.67) * mm});
            skLineSegment(sketch, "E4585", {"start": v(-2.38, -23.67) * mm, "end": v(-2.38, -23.78) * mm});
            skLineSegment(sketch, "E4586", {"start": v(-2.38, -23.78) * mm, "end": v(-2.35, -23.9) * mm});
            skLineSegment(sketch, "E4587", {"start": v(-2.35, -23.9) * mm, "end": v(-2.3, -24) * mm});
            skLineSegment(sketch, "E4588", {"start": v(-2.3, -24) * mm, "end": v(-2.22, -24.11) * mm});
            skLineSegment(sketch, "E4589", {"start": v(-2.22, -24.11) * mm, "end": v(-2.1, -24.24) * mm});
            skLineSegment(sketch, "E4590", {"start": v(-2.1, -24.24) * mm, "end": v(-1.96, -24.4) * mm});
            skLineSegment(sketch, "E4591", {"start": v(-1.96, -24.4) * mm, "end": v(-1.73, -24.62) * mm});
            skLineSegment(sketch, "E4592", {"start": v(-1.73, -24.62) * mm, "end": v(-1.52, -24.77) * mm});
            skLineSegment(sketch, "E4593", {"start": v(-1.52, -24.77) * mm, "end": v(-1.34, -24.85) * mm});
            skLineSegment(sketch, "E4594", {"start": v(-1.34, -24.85) * mm, "end": v(-1.18, -24.86) * mm});
            skLineSegment(sketch, "E4595", {"start": v(-1.18, -24.86) * mm, "end": v(-1.03, -24.83) * mm});
            skLineSegment(sketch, "E4596", {"start": v(-1.03, -24.83) * mm, "end": v(-0.87, -24.76) * mm});
            skLineSegment(sketch, "E4597", {"start": v(-0.87, -24.76) * mm, "end": v(-0.7, -24.66) * mm});
            skLineSegment(sketch, "E4598", {"start": v(-0.7, -24.66) * mm, "end": v(-0.52, -24.54) * mm});
            skLineSegment(sketch, "E4599", {"start": v(-0.52, -24.54) * mm, "end": v(-0.05, -24.26) * mm});
            skLineSegment(sketch, "E4600", {"start": v(-0.05, -24.26) * mm, "end": v(-0.04, -23.86) * mm});
            skLineSegment(sketch, "E4601", {"start": v(-0.04, -23.86) * mm, "end": v(-0.04, -23.46) * mm});
            skLineSegment(sketch, "E4602", {"start": v(-0.04, -23.46) * mm, "end": v(-0.03, -23.05) * mm});
            skLineSegment(sketch, "E4603", {"start": v(-0.03, -23.05) * mm, "end": v(-0.03, -22.65) * mm});
            skLineSegment(sketch, "E4604", {"start": v(-0.03, -22.65) * mm, "end": v(-0.03, -22.25) * mm});
            skLineSegment(sketch, "E4605", {"start": v(-0.03, -22.25) * mm, "end": v(-0.02, -21.84) * mm});
            skLineSegment(sketch, "E4606", {"start": v(-0.02, -21.84) * mm, "end": v(-0.02, -21.44) * mm});
            skLineSegment(sketch, "E4607", {"start": v(-0.02, -21.44) * mm, "end": v(-0.03, -21.03) * mm});
            skLineSegment(sketch, "E4608", {"start": v(-0.03, -21.03) * mm, "end": v(-0.03, -20.63) * mm});
            skLineSegment(sketch, "E4609", {"start": v(-0.03, -20.63) * mm, "end": v(-0.02, -20.22) * mm});
            skLineSegment(sketch, "E4610", {"start": v(-0.02, -20.22) * mm, "end": v(-0.02, -19.81) * mm});
            skLineSegment(sketch, "E4611", {"start": v(-0.02, -19.81) * mm, "end": v(-0.01, -19.4) * mm});
            skLineSegment(sketch, "E4612", {"start": v(-0.01, -19.4) * mm, "end": v(0, -19) * mm});
            skLineSegment(sketch, "E4613", {"start": v(0, -19) * mm, "end": v(0, -18.6) * mm});
            skLineSegment(sketch, "E4614", {"start": v(0, -18.6) * mm, "end": v(0, -18.19) * mm});
            skLineSegment(sketch, "E4615", {"start": v(0, -18.19) * mm, "end": v(0, -17.78) * mm});
            skLineSegment(sketch, "E4616", {"start": v(0, -17.78) * mm, "end": v(-0.03, -17.76) * mm});
            skLineSegment(sketch, "E4617", {"start": v(-0.03, -17.76) * mm, "end": v(-0.24, -17.67) * mm});
            skLineSegment(sketch, "E4618", {"start": v(-0.24, -17.67) * mm, "end": v(-0.52, -17.58) * mm});
            skLineSegment(sketch, "E4619", {"start": v(-0.52, -17.58) * mm, "end": v(-0.62, -17.74) * mm});
            skLineSegment(sketch, "E4620", {"start": v(-0.62, -17.74) * mm, "end": v(-0.68, -17.88) * mm});
            skLineSegment(sketch, "E4621", {"start": v(-0.68, -17.88) * mm, "end": v(-0.72, -18.02) * mm});
            skLineSegment(sketch, "E4622", {"start": v(-0.72, -18.02) * mm, "end": v(-0.74, -18.16) * mm});
            skLineSegment(sketch, "E4623", {"start": v(-0.74, -18.16) * mm, "end": v(-0.74, -18.3) * mm});
            skLineSegment(sketch, "E4624", {"start": v(-0.74, -18.3) * mm, "end": v(-0.73, -18.46) * mm});
            skLineSegment(sketch, "E4625", {"start": v(-0.73, -18.46) * mm, "end": v(-0.72, -18.63) * mm});
            skLineSegment(sketch, "E4626", {"start": v(-0.72, -18.63) * mm, "end": v(-0.7, -18.83) * mm});
            skLineSegment(sketch, "E4627", {"start": v(-0.7, -18.83) * mm, "end": v(-0.68, -19) * mm});
            skLineSegment(sketch, "E4628", {"start": v(-0.68, -19) * mm, "end": v(-0.67, -19.2) * mm});
            skLineSegment(sketch, "E4629", {"start": v(-0.67, -19.2) * mm, "end": v(-0.67, -19.4) * mm});
            skLineSegment(sketch, "E4630", {"start": v(-0.67, -19.4) * mm, "end": v(-0.67, -19.61) * mm});
            skLineSegment(sketch, "E4631", {"start": v(-0.67, -19.61) * mm, "end": v(-0.67, -19.82) * mm});
            skLineSegment(sketch, "E4632", {"start": v(-0.67, -19.82) * mm, "end": v(-0.68, -20.02) * mm});
            skLineSegment(sketch, "E4633", {"start": v(-0.68, -20.02) * mm, "end": v(-0.69, -20.21) * mm});
            skLineSegment(sketch, "E4634", {"start": v(-0.69, -20.21) * mm, "end": v(-0.7, -20.4) * mm});
            skLineSegment(sketch, "E4635", {"start": v(-0.7, -20.4) * mm, "end": v(-0.75, -20.9) * mm});
            skLineSegment(sketch, "E4636", {"start": v(-0.75, -20.9) * mm, "end": v(-0.8, -21.3) * mm});
            skLineSegment(sketch, "E4637", {"start": v(-0.8, -21.3) * mm, "end": v(-0.86, -21.6) * mm});
            skLineSegment(sketch, "E4638", {"start": v(-0.86, -21.6) * mm, "end": v(-0.96, -21.81) * mm});
            skLineSegment(sketch, "E4639", {"start": v(-0.96, -21.81) * mm, "end": v(-1.12, -21.96) * mm});
            skLineSegment(sketch, "E4640", {"start": v(-1.12, -21.96) * mm, "end": v(-1.35, -22.06) * mm});
            skLineSegment(sketch, "E4641", {"start": v(-1.35, -22.06) * mm, "end": v(-1.67, -22.12) * mm});
            skLineSegment(sketch, "E4642", {"start": v(-1.67, -22.12) * mm, "end": v(-2.1, -22.17) * mm});
            skLineSegment(sketch, "E4643", {"start": v(14.1, -0.67) * mm, "end": v(14.39, -0.68) * mm});
            skLineSegment(sketch, "E4644", {"start": v(14.39, -0.68) * mm, "end": v(14.64, -0.68) * mm});
            skLineSegment(sketch, "E4645", {"start": v(14.64, -0.68) * mm, "end": v(14.87, -0.68) * mm});
            skLineSegment(sketch, "E4646", {"start": v(14.87, -0.68) * mm, "end": v(15.08, -0.68) * mm});
            skLineSegment(sketch, "E4647", {"start": v(15.08, -0.68) * mm, "end": v(15.27, -0.68) * mm});
            skLineSegment(sketch, "E4648", {"start": v(15.27, -0.68) * mm, "end": v(15.47, -0.68) * mm});
            skLineSegment(sketch, "E4649", {"start": v(15.47, -0.68) * mm, "end": v(15.66, -0.68) * mm});
            skLineSegment(sketch, "E4650", {"start": v(15.66, -0.68) * mm, "end": v(15.86, -0.68) * mm});
            skLineSegment(sketch, "E4651", {"start": v(15.86, -0.68) * mm, "end": v(15.98, -0.68) * mm});
            skLineSegment(sketch, "E4652", {"start": v(15.98, -0.68) * mm, "end": v(16.06, -0.66) * mm});
            skLineSegment(sketch, "E4653", {"start": v(16.06, -0.66) * mm, "end": v(16.15, -0.64) * mm});
            skLineSegment(sketch, "E4654", {"start": v(16.15, -0.64) * mm, "end": v(16.32, -0.6) * mm});
            skLineSegment(sketch, "E4655", {"start": v(16.32, -0.6) * mm, "end": v(16.6, -0.57) * mm});
            skLineSegment(sketch, "E4656", {"start": v(16.6, -0.57) * mm, "end": v(16.86, -0.52) * mm});
            skLineSegment(sketch, "E4657", {"start": v(16.86, -0.52) * mm, "end": v(17.12, -0.47) * mm});
            skLineSegment(sketch, "E4658", {"start": v(17.12, -0.47) * mm, "end": v(17.37, -0.4) * mm});
            skLineSegment(sketch, "E4659", {"start": v(17.37, -0.4) * mm, "end": v(17.62, -0.33) * mm});
            skLineSegment(sketch, "E4660", {"start": v(17.62, -0.33) * mm, "end": v(17.87, -0.26) * mm});
            skLineSegment(sketch, "E4661", {"start": v(17.87, -0.26) * mm, "end": v(18.1, -0.17) * mm});
            skLineSegment(sketch, "E4662", {"start": v(18.1, -0.17) * mm, "end": v(18.33, -0.08) * mm});
            skLineSegment(sketch, "E4663", {"start": v(18.33, -0.08) * mm, "end": v(18.65, 0.05) * mm});
            skLineSegment(sketch, "E4664", {"start": v(18.65, 0.05) * mm, "end": v(18.97, 0.2) * mm});
            skLineSegment(sketch, "E4665", {"start": v(18.97, 0.2) * mm, "end": v(19.28, 0.37) * mm});
            skLineSegment(sketch, "E4666", {"start": v(19.28, 0.37) * mm, "end": v(19.58, 0.55) * mm});
            skLineSegment(sketch, "E4667", {"start": v(19.58, 0.55) * mm, "end": v(19.86, 0.75) * mm});
            skLineSegment(sketch, "E4668", {"start": v(19.86, 0.75) * mm, "end": v(20.11, 0.98) * mm});
            skLineSegment(sketch, "E4669", {"start": v(20.11, 0.98) * mm, "end": v(20.34, 1.24) * mm});
            skLineSegment(sketch, "E4670", {"start": v(20.34, 1.24) * mm, "end": v(20.52, 1.53) * mm});
            skLineSegment(sketch, "E4671", {"start": v(20.52, 1.53) * mm, "end": v(20.63, 1.75) * mm});
            skLineSegment(sketch, "E4672", {"start": v(20.63, 1.75) * mm, "end": v(20.72, 1.97) * mm});
            skLineSegment(sketch, "E4673", {"start": v(20.72, 1.97) * mm, "end": v(20.79, 2.2) * mm});
            skLineSegment(sketch, "E4674", {"start": v(20.79, 2.2) * mm, "end": v(20.85, 2.47) * mm});
            skLineSegment(sketch, "E4675", {"start": v(20.85, 2.47) * mm, "end": v(20.76, 2.42) * mm});
            skLineSegment(sketch, "E4676", {"start": v(20.76, 2.42) * mm, "end": v(20.57, 2.32) * mm});
            skLineSegment(sketch, "E4677", {"start": v(20.57, 2.32) * mm, "end": v(20.29, 2.17) * mm});
            skLineSegment(sketch, "E4678", {"start": v(20.29, 2.17) * mm, "end": v(19.9, 1.98) * mm});
            skLineSegment(sketch, "E4679", {"start": v(19.9, 1.98) * mm, "end": v(19.4, 1.77) * mm});
            skLineSegment(sketch, "E4680", {"start": v(19.4, 1.77) * mm, "end": v(18.8, 1.55) * mm});
            skLineSegment(sketch, "E4681", {"start": v(18.8, 1.55) * mm, "end": v(18.08, 1.34) * mm});
            skLineSegment(sketch, "E4682", {"start": v(18.08, 1.34) * mm, "end": v(17.23, 1.14) * mm});
            skLineSegment(sketch, "E4683", {"start": v(17.23, 1.14) * mm, "end": v(17.1, 1.12) * mm});
            skLineSegment(sketch, "E4684", {"start": v(17.1, 1.12) * mm, "end": v(16.97, 1.1) * mm});
            skLineSegment(sketch, "E4685", {"start": v(16.97, 1.1) * mm, "end": v(16.85, 1.1) * mm});
            skLineSegment(sketch, "E4686", {"start": v(16.85, 1.1) * mm, "end": v(16.75, 1.09) * mm});
            skLineSegment(sketch, "E4687", {"start": v(16.75, 1.09) * mm, "end": v(15.61, 0.96) * mm});
            skLineSegment(sketch, "E4688", {"start": v(15.61, 0.96) * mm, "end": v(15.43, 0.95) * mm});
            skLineSegment(sketch, "E4689", {"start": v(15.43, 0.95) * mm, "end": v(15.33, 0.93) * mm});
            skLineSegment(sketch, "E4690", {"start": v(15.33, 0.93) * mm, "end": v(15.29, 0.88) * mm});
            skLineSegment(sketch, "E4691", {"start": v(15.29, 0.88) * mm, "end": v(15.26, 0.78) * mm});
            skLineSegment(sketch, "E4692", {"start": v(15.26, 0.78) * mm, "end": v(15.2, 0.63) * mm});
            skLineSegment(sketch, "E4693", {"start": v(15.2, 0.63) * mm, "end": v(15.06, 0.4) * mm});
            skLineSegment(sketch, "E4694", {"start": v(15.06, 0.4) * mm, "end": v(14.82, 0.08) * mm});
            skLineSegment(sketch, "E4695", {"start": v(14.82, 0.08) * mm, "end": v(14.43, -0.35) * mm});
            skLineSegment(sketch, "E4696", {"start": v(14.43, -0.35) * mm, "end": v(14.19, -0.56) * mm});
            skLineSegment(sketch, "E4697", {"start": v(14.19, -0.56) * mm, "end": v(14.1, -0.67) * mm});
            skLineSegment(sketch, "E4698", {"start": v(-14.13, -0.67) * mm, "end": v(-14.13, -0.64) * mm});
            skLineSegment(sketch, "E4699", {"start": v(-14.13, -0.64) * mm, "end": v(-14.13, -0.61) * mm});
            skLineSegment(sketch, "E4700", {"start": v(-14.13, -0.61) * mm, "end": v(-14.17, -0.58) * mm});
            skLineSegment(sketch, "E4701", {"start": v(-14.17, -0.58) * mm, "end": v(-14.25, -0.5) * mm});
            skLineSegment(sketch, "E4702", {"start": v(-14.25, -0.5) * mm, "end": v(-14.42, -0.36) * mm});
            skLineSegment(sketch, "E4703", {"start": v(-14.42, -0.36) * mm, "end": v(-14.58, -0.2) * mm});
            skLineSegment(sketch, "E4704", {"start": v(-14.58, -0.2) * mm, "end": v(-14.74, -0.04) * mm});
            skLineSegment(sketch, "E4705", {"start": v(-14.74, -0.04) * mm, "end": v(-14.89, 0.13) * mm});
            skLineSegment(sketch, "E4706", {"start": v(-14.89, 0.13) * mm, "end": v(-15.02, 0.32) * mm});
            skLineSegment(sketch, "E4707", {"start": v(-15.02, 0.32) * mm, "end": v(-15.14, 0.52) * mm});
            skLineSegment(sketch, "E4708", {"start": v(-15.14, 0.52) * mm, "end": v(-15.24, 0.72) * mm});
            skLineSegment(sketch, "E4709", {"start": v(-15.24, 0.72) * mm, "end": v(-15.31, 0.94) * mm});
            skLineSegment(sketch, "E4710", {"start": v(-15.31, 0.94) * mm, "end": v(-16.03, 1) * mm});
            skLineSegment(sketch, "E4711", {"start": v(-16.03, 1) * mm, "end": v(-16.68, 1.07) * mm});
            skLineSegment(sketch, "E4712", {"start": v(-16.68, 1.07) * mm, "end": v(-17.3, 1.16) * mm});
            skLineSegment(sketch, "E4713", {"start": v(-17.3, 1.16) * mm, "end": v(-17.87, 1.28) * mm});
            skLineSegment(sketch, "E4714", {"start": v(-17.87, 1.28) * mm, "end": v(-18.45, 1.43) * mm});
            skLineSegment(sketch, "E4715", {"start": v(-18.45, 1.43) * mm, "end": v(-19.03, 1.62) * mm});
            skLineSegment(sketch, "E4716", {"start": v(-19.03, 1.62) * mm, "end": v(-19.63, 1.86) * mm});
            skLineSegment(sketch, "E4717", {"start": v(-19.63, 1.86) * mm, "end": v(-20.27, 2.15) * mm});
            skLineSegment(sketch, "E4718", {"start": v(-20.27, 2.15) * mm, "end": v(-20.43, 2.24) * mm});
            skLineSegment(sketch, "E4719", {"start": v(-20.43, 2.24) * mm, "end": v(-20.59, 2.34) * mm});
            skLineSegment(sketch, "E4720", {"start": v(-20.59, 2.34) * mm, "end": v(-20.74, 2.42) * mm});
            skLineSegment(sketch, "E4721", {"start": v(-20.74, 2.42) * mm, "end": v(-20.86, 2.47) * mm});
            skLineSegment(sketch, "E4722", {"start": v(-20.86, 2.47) * mm, "end": v(-20.8, 2.25) * mm});
            skLineSegment(sketch, "E4723", {"start": v(-20.8, 2.25) * mm, "end": v(-20.74, 2.02) * mm});
            skLineSegment(sketch, "E4724", {"start": v(-20.74, 2.02) * mm, "end": v(-20.66, 1.8) * mm});
            skLineSegment(sketch, "E4725", {"start": v(-20.66, 1.8) * mm, "end": v(-20.56, 1.57) * mm});
            skLineSegment(sketch, "E4726", {"start": v(-20.56, 1.57) * mm, "end": v(-20.44, 1.37) * mm});
            skLineSegment(sketch, "E4727", {"start": v(-20.44, 1.37) * mm, "end": v(-20.3, 1.18) * mm});
            skLineSegment(sketch, "E4728", {"start": v(-20.3, 1.18) * mm, "end": v(-20.15, 1) * mm});
            skLineSegment(sketch, "E4729", {"start": v(-20.15, 1) * mm, "end": v(-19.98, 0.86) * mm});
            skLineSegment(sketch, "E4730", {"start": v(-19.98, 0.86) * mm, "end": v(-19.3, 0.4) * mm});
            skLineSegment(sketch, "E4731", {"start": v(-19.3, 0.4) * mm, "end": v(-18.62, 0.03) * mm});
            skLineSegment(sketch, "E4732", {"start": v(-18.62, 0.03) * mm, "end": v(-17.92, -0.24) * mm});
            skLineSegment(sketch, "E4733", {"start": v(-17.92, -0.24) * mm, "end": v(-17.2, -0.45) * mm});
            skLineSegment(sketch, "E4734", {"start": v(-17.2, -0.45) * mm, "end": v(-16.47, -0.58) * mm});
            skLineSegment(sketch, "E4735", {"start": v(-16.47, -0.58) * mm, "end": v(-15.72, -0.66) * mm});
            skLineSegment(sketch, "E4736", {"start": v(-15.72, -0.66) * mm, "end": v(-14.94, -0.69) * mm});
            skLineSegment(sketch, "E4737", {"start": v(-14.94, -0.69) * mm, "end": v(-14.13, -0.67) * mm});
            skLineSegment(sketch, "E4738", {"start": v(13.21, 1.12) * mm, "end": v(13.37, 1.16) * mm});
            skLineSegment(sketch, "E4739", {"start": v(13.37, 1.16) * mm, "end": v(13.62, 1.25) * mm});
            skLineSegment(sketch, "E4740", {"start": v(13.62, 1.25) * mm, "end": v(13.94, 1.37) * mm});
            skLineSegment(sketch, "E4741", {"start": v(13.94, 1.37) * mm, "end": v(14.3, 1.51) * mm});
            skLineSegment(sketch, "E4742", {"start": v(14.3, 1.51) * mm, "end": v(14.66, 1.66) * mm});
            skLineSegment(sketch, "E4743", {"start": v(14.66, 1.66) * mm, "end": v(15, 1.8) * mm});
            skLineSegment(sketch, "E4744", {"start": v(15, 1.8) * mm, "end": v(15.3, 1.9) * mm});
            skLineSegment(sketch, "E4745", {"start": v(15.3, 1.9) * mm, "end": v(15.52, 1.97) * mm});
            skLineSegment(sketch, "E4746", {"start": v(15.52, 1.97) * mm, "end": v(15.48, 1.42) * mm});
            skLineSegment(sketch, "E4747", {"start": v(15.48, 1.42) * mm, "end": v(16.12, 1.46) * mm});
            skLineSegment(sketch, "E4748", {"start": v(16.12, 1.46) * mm, "end": v(16.82, 1.54) * mm});
            skLineSegment(sketch, "E4749", {"start": v(16.82, 1.54) * mm, "end": v(17.54, 1.67) * mm});
            skLineSegment(sketch, "E4750", {"start": v(17.54, 1.67) * mm, "end": v(18.27, 1.84) * mm});
            skLineSegment(sketch, "E4751", {"start": v(18.27, 1.84) * mm, "end": v(18.98, 2.04) * mm});
            skLineSegment(sketch, "E4752", {"start": v(18.98, 2.04) * mm, "end": v(19.66, 2.29) * mm});
            skLineSegment(sketch, "E4753", {"start": v(19.66, 2.29) * mm, "end": v(20.29, 2.57) * mm});
            skLineSegment(sketch, "E4754", {"start": v(20.29, 2.57) * mm, "end": v(20.83, 2.88) * mm});
            skLineSegment(sketch, "E4755", {"start": v(20.83, 2.88) * mm, "end": v(20.9, 2.94) * mm});
            skLineSegment(sketch, "E4756", {"start": v(20.9, 2.94) * mm, "end": v(20.95, 3.02) * mm});
            skLineSegment(sketch, "E4757", {"start": v(20.95, 3.02) * mm, "end": v(21, 3.12) * mm});
            skLineSegment(sketch, "E4758", {"start": v(21, 3.12) * mm, "end": v(21.06, 3.22) * mm});
            skLineSegment(sketch, "E4759", {"start": v(21.06, 3.22) * mm, "end": v(21.14, 3.45) * mm});
            skLineSegment(sketch, "E4760", {"start": v(21.14, 3.45) * mm, "end": v(21.2, 3.64) * mm});
            skLineSegment(sketch, "E4761", {"start": v(21.2, 3.64) * mm, "end": v(21.23, 3.8) * mm});
            skLineSegment(sketch, "E4762", {"start": v(21.23, 3.8) * mm, "end": v(21.25, 3.93) * mm});
            skLineSegment(sketch, "E4763", {"start": v(21.25, 3.93) * mm, "end": v(21.27, 4.06) * mm});
            skLineSegment(sketch, "E4764", {"start": v(21.27, 4.06) * mm, "end": v(21.27, 4.18) * mm});
            skLineSegment(sketch, "E4765", {"start": v(21.27, 4.18) * mm, "end": v(21.27, 4.44) * mm});
            skLineSegment(sketch, "E4766", {"start": v(21.27, 4.44) * mm, "end": v(21.28, 4.73) * mm});
            skLineSegment(sketch, "E4767", {"start": v(21.28, 4.73) * mm, "end": v(21.19, 4.67) * mm});
            skLineSegment(sketch, "E4768", {"start": v(21.19, 4.67) * mm, "end": v(21.1, 4.58) * mm});
            skLineSegment(sketch, "E4769", {"start": v(21.1, 4.58) * mm, "end": v(21, 4.49) * mm});
            skLineSegment(sketch, "E4770", {"start": v(21, 4.49) * mm, "end": v(20.9, 4.4) * mm});
            skLineSegment(sketch, "E4771", {"start": v(20.9, 4.4) * mm, "end": v(20.53, 4.12) * mm});
            skLineSegment(sketch, "E4772", {"start": v(20.53, 4.12) * mm, "end": v(20.1, 3.86) * mm});
            skLineSegment(sketch, "E4773", {"start": v(20.1, 3.86) * mm, "end": v(19.64, 3.64) * mm});
            skLineSegment(sketch, "E4774", {"start": v(19.64, 3.64) * mm, "end": v(19.14, 3.44) * mm});
            skLineSegment(sketch, "E4775", {"start": v(19.14, 3.44) * mm, "end": v(18.63, 3.28) * mm});
            skLineSegment(sketch, "E4776", {"start": v(18.63, 3.28) * mm, "end": v(18.12, 3.14) * mm});
            skLineSegment(sketch, "E4777", {"start": v(18.12, 3.14) * mm, "end": v(17.63, 3.03) * mm});
            skLineSegment(sketch, "E4778", {"start": v(17.63, 3.03) * mm, "end": v(17.17, 2.95) * mm});
            skLineSegment(sketch, "E4779", {"start": v(17.17, 2.95) * mm, "end": v(16.85, 2.9) * mm});
            skLineSegment(sketch, "E4780", {"start": v(16.85, 2.9) * mm, "end": v(16.52, 2.87) * mm});
            skLineSegment(sketch, "E4781", {"start": v(16.52, 2.87) * mm, "end": v(16.2, 2.83) * mm});
            skLineSegment(sketch, "E4782", {"start": v(16.2, 2.83) * mm, "end": v(15.86, 2.81) * mm});
            skLineSegment(sketch, "E4783", {"start": v(15.86, 2.81) * mm, "end": v(15.68, 2.8) * mm});
            skLineSegment(sketch, "E4784", {"start": v(15.68, 2.8) * mm, "end": v(15.55, 2.76) * mm});
            skLineSegment(sketch, "E4785", {"start": v(15.55, 2.76) * mm, "end": v(15.46, 2.72) * mm});
            skLineSegment(sketch, "E4786", {"start": v(15.46, 2.72) * mm, "end": v(15.4, 2.66) * mm});
            skLineSegment(sketch, "E4787", {"start": v(15.4, 2.66) * mm, "end": v(15.33, 2.58) * mm});
            skLineSegment(sketch, "E4788", {"start": v(15.33, 2.58) * mm, "end": v(15.25, 2.48) * mm});
            skLineSegment(sketch, "E4789", {"start": v(15.25, 2.48) * mm, "end": v(15.13, 2.35) * mm});
            skLineSegment(sketch, "E4790", {"start": v(15.13, 2.35) * mm, "end": v(14.96, 2.2) * mm});
            skLineSegment(sketch, "E4791", {"start": v(14.96, 2.2) * mm, "end": v(14.84, 2.12) * mm});
            skLineSegment(sketch, "E4792", {"start": v(14.84, 2.12) * mm, "end": v(14.64, 1.97) * mm});
            skLineSegment(sketch, "E4793", {"start": v(14.64, 1.97) * mm, "end": v(14.38, 1.8) * mm});
            skLineSegment(sketch, "E4794", {"start": v(14.38, 1.8) * mm, "end": v(14.1, 1.61) * mm});
            skLineSegment(sketch, "E4795", {"start": v(14.1, 1.61) * mm, "end": v(13.82, 1.43) * mm});
            skLineSegment(sketch, "E4796", {"start": v(13.82, 1.43) * mm, "end": v(13.56, 1.28) * mm});
            skLineSegment(sketch, "E4797", {"start": v(13.56, 1.28) * mm, "end": v(13.35, 1.17) * mm});
            skLineSegment(sketch, "E4798", {"start": v(13.35, 1.17) * mm, "end": v(13.21, 1.12) * mm});
            skLineSegment(sketch, "E4799", {"start": v(-15.47, 1.42) * mm, "end": v(-15.53, 1.97) * mm});
            skLineSegment(sketch, "E4800", {"start": v(-15.53, 1.97) * mm, "end": v(-15.36, 1.92) * mm});
            skLineSegment(sketch, "E4801", {"start": v(-15.36, 1.92) * mm, "end": v(-15.08, 1.82) * mm});
            skLineSegment(sketch, "E4802", {"start": v(-15.08, 1.82) * mm, "end": v(-14.75, 1.7) * mm});
            skLineSegment(sketch, "E4803", {"start": v(-14.75, 1.7) * mm, "end": v(-14.4, 1.55) * mm});
            skLineSegment(sketch, "E4804", {"start": v(-14.4, 1.55) * mm, "end": v(-14.05, 1.41) * mm});
            skLineSegment(sketch, "E4805", {"start": v(-14.05, 1.41) * mm, "end": v(-13.76, 1.3) * mm});
            skLineSegment(sketch, "E4806", {"start": v(-13.76, 1.3) * mm, "end": v(-13.55, 1.21) * mm});
            skLineSegment(sketch, "E4807", {"start": v(-13.55, 1.21) * mm, "end": v(-13.46, 1.18) * mm});
            skLineSegment(sketch, "E4808", {"start": v(-13.46, 1.18) * mm, "end": v(-13.3, 1.15) * mm});
            skLineSegment(sketch, "E4809", {"start": v(-13.3, 1.15) * mm, "end": v(-13.47, 1.25) * mm});
            skLineSegment(sketch, "E4810", {"start": v(-13.47, 1.25) * mm, "end": v(-13.65, 1.36) * mm});
            skLineSegment(sketch, "E4811", {"start": v(-13.65, 1.36) * mm, "end": v(-13.86, 1.46) * mm});
            skLineSegment(sketch, "E4812", {"start": v(-13.86, 1.46) * mm, "end": v(-14.1, 1.6) * mm});
            skLineSegment(sketch, "E4813", {"start": v(-14.1, 1.6) * mm, "end": v(-14.37, 1.76) * mm});
            skLineSegment(sketch, "E4814", {"start": v(-14.37, 1.76) * mm, "end": v(-14.68, 1.98) * mm});
            skLineSegment(sketch, "E4815", {"start": v(-14.68, 1.98) * mm, "end": v(-15.01, 2.26) * mm});
            skLineSegment(sketch, "E4816", {"start": v(-15.01, 2.26) * mm, "end": v(-15.39, 2.62) * mm});
            skLineSegment(sketch, "E4817", {"start": v(-15.39, 2.62) * mm, "end": v(-15.46, 2.69) * mm});
            skLineSegment(sketch, "E4818", {"start": v(-15.46, 2.69) * mm, "end": v(-15.51, 2.74) * mm});
            skLineSegment(sketch, "E4819", {"start": v(-15.51, 2.74) * mm, "end": v(-15.56, 2.77) * mm});
            skLineSegment(sketch, "E4820", {"start": v(-15.56, 2.77) * mm, "end": v(-15.6, 2.8) * mm});
            skLineSegment(sketch, "E4821", {"start": v(-15.6, 2.8) * mm, "end": v(-15.72, 2.8) * mm});
            skLineSegment(sketch, "E4822", {"start": v(-15.72, 2.8) * mm, "end": v(-15.94, 2.81) * mm});
            skLineSegment(sketch, "E4823", {"start": v(-15.94, 2.81) * mm, "end": v(-16.59, 2.87) * mm});
            skLineSegment(sketch, "E4824", {"start": v(-16.59, 2.87) * mm, "end": v(-17.24, 2.96) * mm});
            skLineSegment(sketch, "E4825", {"start": v(-17.24, 2.96) * mm, "end": v(-17.9, 3.08) * mm});
            skLineSegment(sketch, "E4826", {"start": v(-17.9, 3.08) * mm, "end": v(-18.54, 3.25) * mm});
            skLineSegment(sketch, "E4827", {"start": v(-18.54, 3.25) * mm, "end": v(-19.17, 3.45) * mm});
            skLineSegment(sketch, "E4828", {"start": v(-19.17, 3.45) * mm, "end": v(-19.78, 3.7) * mm});
            skLineSegment(sketch, "E4829", {"start": v(-19.78, 3.7) * mm, "end": v(-20.35, 4.01) * mm});
            skLineSegment(sketch, "E4830", {"start": v(-20.35, 4.01) * mm, "end": v(-20.88, 4.37) * mm});
            skLineSegment(sketch, "E4831", {"start": v(-20.88, 4.37) * mm, "end": v(-20.98, 4.46) * mm});
            skLineSegment(sketch, "E4832", {"start": v(-20.98, 4.46) * mm, "end": v(-21.06, 4.55) * mm});
            skLineSegment(sketch, "E4833", {"start": v(-21.06, 4.55) * mm, "end": v(-21.1, 4.6) * mm});
            skLineSegment(sketch, "E4834", {"start": v(-21.1, 4.6) * mm, "end": v(-21.15, 4.64) * mm});
            skLineSegment(sketch, "E4835", {"start": v(-21.15, 4.64) * mm, "end": v(-21.2, 4.68) * mm});
            skLineSegment(sketch, "E4836", {"start": v(-21.2, 4.68) * mm, "end": v(-21.27, 4.72) * mm});
            skLineSegment(sketch, "E4837", {"start": v(-21.27, 4.72) * mm, "end": v(-21.28, 4.52) * mm});
            skLineSegment(sketch, "E4838", {"start": v(-21.28, 4.52) * mm, "end": v(-21.27, 4.28) * mm});
            skLineSegment(sketch, "E4839", {"start": v(-21.27, 4.28) * mm, "end": v(-21.25, 4) * mm});
            skLineSegment(sketch, "E4840", {"start": v(-21.25, 4) * mm, "end": v(-21.22, 3.73) * mm});
            skLineSegment(sketch, "E4841", {"start": v(-21.22, 3.73) * mm, "end": v(-21.16, 3.46) * mm});
            skLineSegment(sketch, "E4842", {"start": v(-21.16, 3.46) * mm, "end": v(-21.08, 3.21) * mm});
            skLineSegment(sketch, "E4843", {"start": v(-21.08, 3.21) * mm, "end": v(-20.97, 3.01) * mm});
            skLineSegment(sketch, "E4844", {"start": v(-20.97, 3.01) * mm, "end": v(-20.84, 2.88) * mm});
            skLineSegment(sketch, "E4845", {"start": v(-20.84, 2.88) * mm, "end": v(-20.3, 2.57) * mm});
            skLineSegment(sketch, "E4846", {"start": v(-20.3, 2.57) * mm, "end": v(-19.67, 2.3) * mm});
            skLineSegment(sketch, "E4847", {"start": v(-19.67, 2.3) * mm, "end": v(-18.97, 2.05) * mm});
            skLineSegment(sketch, "E4848", {"start": v(-18.97, 2.05) * mm, "end": v(-18.23, 1.84) * mm});
            skLineSegment(sketch, "E4849", {"start": v(-18.23, 1.84) * mm, "end": v(-17.49, 1.67) * mm});
            skLineSegment(sketch, "E4850", {"start": v(-17.49, 1.67) * mm, "end": v(-16.76, 1.54) * mm});
            skLineSegment(sketch, "E4851", {"start": v(-16.76, 1.54) * mm, "end": v(-16.08, 1.46) * mm});
            skLineSegment(sketch, "E4852", {"start": v(-16.08, 1.46) * mm, "end": v(-15.47, 1.42) * mm});
            skLineSegment(sketch, "E4853", {"start": v(11.08, 3.92) * mm, "end": v(11.02, 3.63) * mm});
            skLineSegment(sketch, "E4854", {"start": v(11.02, 3.63) * mm, "end": v(10.97, 3.4) * mm});
            skLineSegment(sketch, "E4855", {"start": v(10.97, 3.4) * mm, "end": v(10.93, 3.23) * mm});
            skLineSegment(sketch, "E4856", {"start": v(10.93, 3.23) * mm, "end": v(10.89, 3.08) * mm});
            skLineSegment(sketch, "E4857", {"start": v(10.89, 3.08) * mm, "end": v(10.83, 2.94) * mm});
            skLineSegment(sketch, "E4858", {"start": v(10.83, 2.94) * mm, "end": v(10.77, 2.79) * mm});
            skLineSegment(sketch, "E4859", {"start": v(10.77, 2.79) * mm, "end": v(10.68, 2.6) * mm});
            skLineSegment(sketch, "E4860", {"start": v(10.68, 2.6) * mm, "end": v(10.56, 2.36) * mm});
            skLineSegment(sketch, "E4861", {"start": v(10.56, 2.36) * mm, "end": v(10.5, 2.24) * mm});
            skLineSegment(sketch, "E4862", {"start": v(10.5, 2.24) * mm, "end": v(10.42, 2.14) * mm});
            skLineSegment(sketch, "E4863", {"start": v(10.42, 2.14) * mm, "end": v(10.35, 2.04) * mm});
            skLineSegment(sketch, "E4864", {"start": v(10.35, 2.04) * mm, "end": v(10.28, 1.95) * mm});
            skLineSegment(sketch, "E4865", {"start": v(10.28, 1.95) * mm, "end": v(10.38, 2) * mm});
            skLineSegment(sketch, "E4866", {"start": v(10.38, 2) * mm, "end": v(10.47, 2.05) * mm});
            skLineSegment(sketch, "E4867", {"start": v(10.47, 2.05) * mm, "end": v(10.57, 2.11) * mm});
            skLineSegment(sketch, "E4868", {"start": v(10.57, 2.11) * mm, "end": v(10.67, 2.19) * mm});
            skLineSegment(sketch, "E4869", {"start": v(10.67, 2.19) * mm, "end": v(10.77, 2.26) * mm});
            skLineSegment(sketch, "E4870", {"start": v(10.77, 2.26) * mm, "end": v(10.87, 2.33) * mm});
            skLineSegment(sketch, "E4871", {"start": v(10.87, 2.33) * mm, "end": v(10.96, 2.39) * mm});
            skLineSegment(sketch, "E4872", {"start": v(10.96, 2.39) * mm, "end": v(11.06, 2.44) * mm});
            skLineSegment(sketch, "E4873", {"start": v(11.06, 2.44) * mm, "end": v(11.05, 2.11) * mm});
            skLineSegment(sketch, "E4874", {"start": v(11.05, 2.11) * mm, "end": v(11.26, 2.23) * mm});
            skLineSegment(sketch, "E4875", {"start": v(11.26, 2.23) * mm, "end": v(11.6, 2.43) * mm});
            skLineSegment(sketch, "E4876", {"start": v(11.6, 2.43) * mm, "end": v(12.02, 2.7) * mm});
            skLineSegment(sketch, "E4877", {"start": v(12.02, 2.7) * mm, "end": v(12.48, 3.01) * mm});
            skLineSegment(sketch, "E4878", {"start": v(12.48, 3.01) * mm, "end": v(12.93, 3.32) * mm});
            skLineSegment(sketch, "E4879", {"start": v(12.93, 3.32) * mm, "end": v(13.34, 3.61) * mm});
            skLineSegment(sketch, "E4880", {"start": v(13.34, 3.61) * mm, "end": v(13.66, 3.84) * mm});
            skLineSegment(sketch, "E4881", {"start": v(13.66, 3.84) * mm, "end": v(13.85, 3.99) * mm});
            skLineSegment(sketch, "E4882", {"start": v(13.85, 3.99) * mm, "end": v(14.2, 4.28) * mm});
            skLineSegment(sketch, "E4883", {"start": v(14.2, 4.28) * mm, "end": v(14.47, 4.5) * mm});
            skLineSegment(sketch, "E4884", {"start": v(14.47, 4.5) * mm, "end": v(14.75, 4.75) * mm});
            skLineSegment(sketch, "E4885", {"start": v(14.75, 4.75) * mm, "end": v(15.09, 5.08) * mm});
            skLineSegment(sketch, "E4886", {"start": v(15.09, 5.08) * mm, "end": v(15.48, 5.48) * mm});
            skLineSegment(sketch, "E4887", {"start": v(15.48, 5.48) * mm, "end": v(15.73, 5.73) * mm});
            skLineSegment(sketch, "E4888", {"start": v(15.73, 5.73) * mm, "end": v(15.99, 6.06) * mm});
            skLineSegment(sketch, "E4889", {"start": v(15.99, 6.06) * mm, "end": v(16.26, 6.45) * mm});
            skLineSegment(sketch, "E4890", {"start": v(16.26, 6.45) * mm, "end": v(16.53, 6.86) * mm});
            skLineSegment(sketch, "E4891", {"start": v(16.53, 6.86) * mm, "end": v(16.77, 7.27) * mm});
            skLineSegment(sketch, "E4892", {"start": v(16.77, 7.27) * mm, "end": v(16.99, 7.67) * mm});
            skLineSegment(sketch, "E4893", {"start": v(16.99, 7.67) * mm, "end": v(17.15, 8.04) * mm});
            skLineSegment(sketch, "E4894", {"start": v(17.15, 8.04) * mm, "end": v(17.26, 8.34) * mm});
            skLineSegment(sketch, "E4895", {"start": v(17.26, 8.34) * mm, "end": v(16.63, 7.7) * mm});
            skLineSegment(sketch, "E4896", {"start": v(16.63, 7.7) * mm, "end": v(16.46, 7.55) * mm});
            skLineSegment(sketch, "E4897", {"start": v(16.46, 7.55) * mm, "end": v(16.31, 7.4) * mm});
            skLineSegment(sketch, "E4898", {"start": v(16.31, 7.4) * mm, "end": v(16.15, 7.23) * mm});
            skLineSegment(sketch, "E4899", {"start": v(16.15, 7.23) * mm, "end": v(15.96, 7.05) * mm});
            skLineSegment(sketch, "E4900", {"start": v(15.96, 7.05) * mm, "end": v(15.6, 6.73) * mm});
            skLineSegment(sketch, "E4901", {"start": v(15.6, 6.73) * mm, "end": v(15.25, 6.43) * mm});
            skLineSegment(sketch, "E4902", {"start": v(15.25, 6.43) * mm, "end": v(15.07, 6.28) * mm});
            skLineSegment(sketch, "E4903", {"start": v(15.07, 6.28) * mm, "end": v(14.9, 6.13) * mm});
            skLineSegment(sketch, "E4904", {"start": v(14.9, 6.13) * mm, "end": v(14.7, 5.98) * mm});
            skLineSegment(sketch, "E4905", {"start": v(14.7, 5.98) * mm, "end": v(14.5, 5.83) * mm});
            skLineSegment(sketch, "E4906", {"start": v(14.5, 5.83) * mm, "end": v(14.1, 5.54) * mm});
            skLineSegment(sketch, "E4907", {"start": v(14.1, 5.54) * mm, "end": v(13.69, 5.27) * mm});
            skLineSegment(sketch, "E4908", {"start": v(13.69, 5.27) * mm, "end": v(13.28, 5.02) * mm});
            skLineSegment(sketch, "E4909", {"start": v(13.28, 5.02) * mm, "end": v(12.87, 4.77) * mm});
            skLineSegment(sketch, "E4910", {"start": v(12.87, 4.77) * mm, "end": v(12.45, 4.54) * mm});
            skLineSegment(sketch, "E4911", {"start": v(12.45, 4.54) * mm, "end": v(12.01, 4.33) * mm});
            skLineSegment(sketch, "E4912", {"start": v(12.01, 4.33) * mm, "end": v(11.56, 4.12) * mm});
            skLineSegment(sketch, "E4913", {"start": v(11.56, 4.12) * mm, "end": v(11.08, 3.92) * mm});
            skLineSegment(sketch, "E4914", {"start": v(-11.05, 2.12) * mm, "end": v(-11.06, 2.44) * mm});
            skLineSegment(sketch, "E4915", {"start": v(-11.06, 2.44) * mm, "end": v(-10.87, 2.32) * mm});
            skLineSegment(sketch, "E4916", {"start": v(-10.87, 2.32) * mm, "end": v(-10.67, 2.18) * mm});
            skLineSegment(sketch, "E4917", {"start": v(-10.67, 2.18) * mm, "end": v(-10.58, 2.11) * mm});
            skLineSegment(sketch, "E4918", {"start": v(-10.58, 2.11) * mm, "end": v(-10.48, 2.05) * mm});
            skLineSegment(sketch, "E4919", {"start": v(-10.48, 2.05) * mm, "end": v(-10.39, 1.99) * mm});
            skLineSegment(sketch, "E4920", {"start": v(-10.39, 1.99) * mm, "end": v(-10.3, 1.94) * mm});
            skLineSegment(sketch, "E4921", {"start": v(-10.3, 1.94) * mm, "end": v(-10.42, 2.12) * mm});
            skLineSegment(sketch, "E4922", {"start": v(-10.42, 2.12) * mm, "end": v(-10.55, 2.33) * mm});
            skLineSegment(sketch, "E4923", {"start": v(-10.55, 2.33) * mm, "end": v(-10.67, 2.56) * mm});
            skLineSegment(sketch, "E4924", {"start": v(-10.67, 2.56) * mm, "end": v(-10.78, 2.81) * mm});
            skLineSegment(sketch, "E4925", {"start": v(-10.78, 2.81) * mm, "end": v(-10.88, 3.08) * mm});
            skLineSegment(sketch, "E4926", {"start": v(-10.88, 3.08) * mm, "end": v(-10.97, 3.35) * mm});
            skLineSegment(sketch, "E4927", {"start": v(-10.97, 3.35) * mm, "end": v(-11.03, 3.64) * mm});
            skLineSegment(sketch, "E4928", {"start": v(-11.03, 3.64) * mm, "end": v(-11.08, 3.92) * mm});
            skLineSegment(sketch, "E4929", {"start": v(-11.08, 3.92) * mm, "end": v(-11.3, 4) * mm});
            skLineSegment(sketch, "E4930", {"start": v(-11.3, 4) * mm, "end": v(-11.52, 4.1) * mm});
            skLineSegment(sketch, "E4931", {"start": v(-11.52, 4.1) * mm, "end": v(-11.77, 4.2) * mm});
            skLineSegment(sketch, "E4932", {"start": v(-11.77, 4.2) * mm, "end": v(-12.01, 4.32) * mm});
            skLineSegment(sketch, "E4933", {"start": v(-12.01, 4.32) * mm, "end": v(-12.26, 4.44) * mm});
            skLineSegment(sketch, "E4934", {"start": v(-12.26, 4.44) * mm, "end": v(-12.5, 4.56) * mm});
            skLineSegment(sketch, "E4935", {"start": v(-12.5, 4.56) * mm, "end": v(-12.7, 4.67) * mm});
            skLineSegment(sketch, "E4936", {"start": v(-12.7, 4.67) * mm, "end": v(-12.9, 4.78) * mm});
            skLineSegment(sketch, "E4937", {"start": v(-12.9, 4.78) * mm, "end": v(-13.34, 5.05) * mm});
            skLineSegment(sketch, "E4938", {"start": v(-13.34, 5.05) * mm, "end": v(-13.75, 5.31) * mm});
            skLineSegment(sketch, "E4939", {"start": v(-13.75, 5.31) * mm, "end": v(-14.14, 5.57) * mm});
            skLineSegment(sketch, "E4940", {"start": v(-14.14, 5.57) * mm, "end": v(-14.5, 5.84) * mm});
            skLineSegment(sketch, "E4941", {"start": v(-14.5, 5.84) * mm, "end": v(-14.86, 6.11) * mm});
            skLineSegment(sketch, "E4942", {"start": v(-14.86, 6.11) * mm, "end": v(-15.21, 6.4) * mm});
            skLineSegment(sketch, "E4943", {"start": v(-15.21, 6.4) * mm, "end": v(-15.58, 6.7) * mm});
            skLineSegment(sketch, "E4944", {"start": v(-15.58, 6.7) * mm, "end": v(-15.96, 7.04) * mm});
            skLineSegment(sketch, "E4945", {"start": v(-15.96, 7.04) * mm, "end": v(-16.22, 7.3) * mm});
            skLineSegment(sketch, "E4946", {"start": v(-16.22, 7.3) * mm, "end": v(-16.66, 7.72) * mm});
            skLineSegment(sketch, "E4947", {"start": v(-16.66, 7.72) * mm, "end": v(-16.87, 7.94) * mm});
            skLineSegment(sketch, "E4948", {"start": v(-16.87, 7.94) * mm, "end": v(-17.06, 8.14) * mm});
            skLineSegment(sketch, "E4949", {"start": v(-17.06, 8.14) * mm, "end": v(-17.2, 8.29) * mm});
            skLineSegment(sketch, "E4950", {"start": v(-17.2, 8.29) * mm, "end": v(-17.25, 8.37) * mm});
            skLineSegment(sketch, "E4951", {"start": v(-17.25, 8.37) * mm, "end": v(-17.2, 8.13) * mm});
            skLineSegment(sketch, "E4952", {"start": v(-17.2, 8.13) * mm, "end": v(-17.07, 7.8) * mm});
            skLineSegment(sketch, "E4953", {"start": v(-17.07, 7.8) * mm, "end": v(-16.86, 7.4) * mm});
            skLineSegment(sketch, "E4954", {"start": v(-16.86, 7.4) * mm, "end": v(-16.6, 6.97) * mm});
            skLineSegment(sketch, "E4955", {"start": v(-16.6, 6.97) * mm, "end": v(-16.31, 6.53) * mm});
            skLineSegment(sketch, "E4956", {"start": v(-16.31, 6.53) * mm, "end": v(-16.02, 6.12) * mm});
            skLineSegment(sketch, "E4957", {"start": v(-16.02, 6.12) * mm, "end": v(-15.75, 5.77) * mm});
            skLineSegment(sketch, "E4958", {"start": v(-15.75, 5.77) * mm, "end": v(-15.53, 5.52) * mm});
            skLineSegment(sketch, "E4959", {"start": v(-15.53, 5.52) * mm, "end": v(-15.3, 5.29) * mm});
            skLineSegment(sketch, "E4960", {"start": v(-15.3, 5.29) * mm, "end": v(-15.08, 5.07) * mm});
            skLineSegment(sketch, "E4961", {"start": v(-15.08, 5.07) * mm, "end": v(-14.86, 4.86) * mm});
            skLineSegment(sketch, "E4962", {"start": v(-14.86, 4.86) * mm, "end": v(-14.64, 4.65) * mm});
            skLineSegment(sketch, "E4963", {"start": v(-14.64, 4.65) * mm, "end": v(-14.42, 4.45) * mm});
            skLineSegment(sketch, "E4964", {"start": v(-14.42, 4.45) * mm, "end": v(-14.19, 4.25) * mm});
            skLineSegment(sketch, "E4965", {"start": v(-14.19, 4.25) * mm, "end": v(-13.94, 4.06) * mm});
            skLineSegment(sketch, "E4966", {"start": v(-13.94, 4.06) * mm, "end": v(-13.68, 3.86) * mm});
            skLineSegment(sketch, "E4967", {"start": v(-13.68, 3.86) * mm, "end": v(-11.05, 2.12) * mm});
            skLineSegment(sketch, "E4968", {"start": v(-7.1, -23.5) * mm, "end": v(-6.9, -23.52) * mm});
            skLineSegment(sketch, "E4969", {"start": v(-6.9, -23.52) * mm, "end": v(-6.67, -23.5) * mm});
            skLineSegment(sketch, "E4970", {"start": v(-6.67, -23.5) * mm, "end": v(-6.44, -23.48) * mm});
            skLineSegment(sketch, "E4971", {"start": v(-6.44, -23.48) * mm, "end": v(-6.24, -23.45) * mm});
            skLineSegment(sketch, "E4972", {"start": v(-6.24, -23.45) * mm, "end": v(-6.11, -23.41) * mm});
            skLineSegment(sketch, "E4973", {"start": v(-6.11, -23.41) * mm, "end": v(-5.95, -23.35) * mm});
            skLineSegment(sketch, "E4974", {"start": v(-5.95, -23.35) * mm, "end": v(-5.8, -23.29) * mm});
            skLineSegment(sketch, "E4975", {"start": v(-5.8, -23.29) * mm, "end": v(-5.68, -23.21) * mm});
            skLineSegment(sketch, "E4976", {"start": v(-5.68, -23.21) * mm, "end": v(-5.63, -23.16) * mm});
            skLineSegment(sketch, "E4977", {"start": v(-5.63, -23.16) * mm, "end": v(-5.6, -23.1) * mm});
            skLineSegment(sketch, "E4978", {"start": v(-5.6, -23.1) * mm, "end": v(-5.57, -23.02) * mm});
            skLineSegment(sketch, "E4979", {"start": v(-5.57, -23.02) * mm, "end": v(-5.55, -22.93) * mm});
            skLineSegment(sketch, "E4980", {"start": v(-5.55, -22.93) * mm, "end": v(-5.52, -22.73) * mm});
            skLineSegment(sketch, "E4981", {"start": v(-5.52, -22.73) * mm, "end": v(-5.49, -22.49) * mm});
            skLineSegment(sketch, "E4982", {"start": v(-5.49, -22.49) * mm, "end": v(-4.98, -20.53) * mm});
            skLineSegment(sketch, "E4983", {"start": v(-4.98, -20.53) * mm, "end": v(-5.2, -20.4) * mm});
            skLineSegment(sketch, "E4984", {"start": v(-5.2, -20.4) * mm, "end": v(-5.34, -20.3) * mm});
            skLineSegment(sketch, "E4985", {"start": v(-5.34, -20.3) * mm, "end": v(-5.44, -20.2) * mm});
            skLineSegment(sketch, "E4986", {"start": v(-5.44, -20.2) * mm, "end": v(-5.5, -20.17) * mm});
            skLineSegment(sketch, "E4987", {"start": v(-5.5, -20.17) * mm, "end": v(-5.58, -20.13) * mm});
            skLineSegment(sketch, "E4988", {"start": v(-5.58, -20.13) * mm, "end": v(-5.69, -20.1) * mm});
            skLineSegment(sketch, "E4989", {"start": v(-5.69, -20.1) * mm, "end": v(-5.83, -20.05) * mm});
            skLineSegment(sketch, "E4990", {"start": v(-5.83, -20.05) * mm, "end": v(-5.99, -20) * mm});
            skLineSegment(sketch, "E4991", {"start": v(-5.99, -20) * mm, "end": v(-6.12, -19.96) * mm});
            skLineSegment(sketch, "E4992", {"start": v(-6.12, -19.96) * mm, "end": v(-6.22, -19.9) * mm});
            skLineSegment(sketch, "E4993", {"start": v(-6.22, -19.9) * mm, "end": v(-6.31, -19.85) * mm});
            skLineSegment(sketch, "E4994", {"start": v(-6.31, -19.85) * mm, "end": v(-6.4, -19.8) * mm});
            skLineSegment(sketch, "E4995", {"start": v(-6.4, -19.8) * mm, "end": v(-6.47, -19.72) * mm});
            skLineSegment(sketch, "E4996", {"start": v(-6.47, -19.72) * mm, "end": v(-6.56, -19.63) * mm});
            skLineSegment(sketch, "E4997", {"start": v(-6.56, -19.63) * mm, "end": v(-6.65, -19.53) * mm});
            skLineSegment(sketch, "E4998", {"start": v(-6.65, -19.53) * mm, "end": v(-6.73, -19.69) * mm});
            skLineSegment(sketch, "E4999", {"start": v(-6.73, -19.69) * mm, "end": v(-6.84, -19.9) * mm});
            skLineSegment(sketch, "E5000", {"start": v(-6.84, -19.9) * mm, "end": v(-6.95, -20.16) * mm});
            skLineSegment(sketch, "E5001", {"start": v(-6.95, -20.16) * mm, "end": v(-7.07, -20.45) * mm});
            skLineSegment(sketch, "E5002", {"start": v(-7.07, -20.45) * mm, "end": v(-7.18, -20.73) * mm});
            skLineSegment(sketch, "E5003", {"start": v(-7.18, -20.73) * mm, "end": v(-7.28, -21) * mm});
            skLineSegment(sketch, "E5004", {"start": v(-7.28, -21) * mm, "end": v(-7.37, -21.24) * mm});
            skLineSegment(sketch, "E5005", {"start": v(-7.37, -21.24) * mm, "end": v(-7.43, -21.43) * mm});
            skLineSegment(sketch, "E5006", {"start": v(-7.43, -21.43) * mm, "end": v(-7.48, -21.6) * mm});
            skLineSegment(sketch, "E5007", {"start": v(-7.48, -21.6) * mm, "end": v(-7.52, -21.74) * mm});
            skLineSegment(sketch, "E5008", {"start": v(-7.52, -21.74) * mm, "end": v(-7.55, -21.85) * mm});
            skLineSegment(sketch, "E5009", {"start": v(-7.55, -21.85) * mm, "end": v(-7.57, -21.96) * mm});
            skLineSegment(sketch, "E5010", {"start": v(-7.57, -21.96) * mm, "end": v(-7.57, -22.07) * mm});
            skLineSegment(sketch, "E5011", {"start": v(-7.57, -22.07) * mm, "end": v(-7.55, -22.19) * mm});
            skLineSegment(sketch, "E5012", {"start": v(-7.55, -22.19) * mm, "end": v(-7.53, -22.34) * mm});
            skLineSegment(sketch, "E5013", {"start": v(-7.53, -22.34) * mm, "end": v(-7.49, -22.53) * mm});
            skLineSegment(sketch, "E5014", {"start": v(-7.49, -22.53) * mm, "end": v(-7.42, -22.77) * mm});
            skLineSegment(sketch, "E5015", {"start": v(-7.42, -22.77) * mm, "end": v(-7.33, -23.05) * mm});
            skLineSegment(sketch, "E5016", {"start": v(-7.33, -23.05) * mm, "end": v(-7.27, -23.19) * mm});
            skLineSegment(sketch, "E5017", {"start": v(-7.27, -23.19) * mm, "end": v(-7.22, -23.31) * mm});
            skLineSegment(sketch, "E5018", {"start": v(-7.22, -23.31) * mm, "end": v(-7.16, -23.42) * mm});
            skLineSegment(sketch, "E5019", {"start": v(-7.16, -23.42) * mm, "end": v(-7.1, -23.5) * mm});
            skLineSegment(sketch, "E5020", {"start": v(6.98, -23.5) * mm, "end": v(7.5, -23.52) * mm});
            skLineSegment(sketch, "E5021", {"start": v(7.5, -23.52) * mm, "end": v(7.6, -23.2) * mm});
            skLineSegment(sketch, "E5022", {"start": v(7.6, -23.2) * mm, "end": v(7.7, -22.9) * mm});
            skLineSegment(sketch, "E5023", {"start": v(7.7, -22.9) * mm, "end": v(7.75, -22.75) * mm});
            skLineSegment(sketch, "E5024", {"start": v(7.75, -22.75) * mm, "end": v(7.8, -22.59) * mm});
            skLineSegment(sketch, "E5025", {"start": v(7.8, -22.59) * mm, "end": v(7.85, -22.4) * mm});
            skLineSegment(sketch, "E5026", {"start": v(7.85, -22.4) * mm, "end": v(7.9, -22.21) * mm});
            skLineSegment(sketch, "E5027", {"start": v(7.9, -22.21) * mm, "end": v(7.91, -22.05) * mm});
            skLineSegment(sketch, "E5028", {"start": v(7.91, -22.05) * mm, "end": v(7.9, -21.87) * mm});
            skLineSegment(sketch, "E5029", {"start": v(7.9, -21.87) * mm, "end": v(7.87, -21.7) * mm});
            skLineSegment(sketch, "E5030", {"start": v(7.87, -21.7) * mm, "end": v(7.81, -21.5) * mm});
            skLineSegment(sketch, "E5031", {"start": v(7.81, -21.5) * mm, "end": v(7.68, -21.14) * mm});
            skLineSegment(sketch, "E5032", {"start": v(7.68, -21.14) * mm, "end": v(7.57, -20.83) * mm});
            skLineSegment(sketch, "E5033", {"start": v(7.57, -20.83) * mm, "end": v(7.46, -20.55) * mm});
            skLineSegment(sketch, "E5034", {"start": v(7.46, -20.55) * mm, "end": v(7.3, -20.17) * mm});
            skLineSegment(sketch, "E5035", {"start": v(7.3, -20.17) * mm, "end": v(7.23, -19.98) * mm});
            skLineSegment(sketch, "E5036", {"start": v(7.23, -19.98) * mm, "end": v(7.15, -19.8) * mm});
            skLineSegment(sketch, "E5037", {"start": v(7.15, -19.8) * mm, "end": v(7.08, -19.67) * mm});
            skLineSegment(sketch, "E5038", {"start": v(7.08, -19.67) * mm, "end": v(7.02, -19.6) * mm});
            skLineSegment(sketch, "E5039", {"start": v(7.02, -19.6) * mm, "end": v(6.93, -19.68) * mm});
            skLineSegment(sketch, "E5040", {"start": v(6.93, -19.68) * mm, "end": v(6.85, -19.76) * mm});
            skLineSegment(sketch, "E5041", {"start": v(6.85, -19.76) * mm, "end": v(6.76, -19.82) * mm});
            skLineSegment(sketch, "E5042", {"start": v(6.76, -19.82) * mm, "end": v(6.66, -19.88) * mm});
            skLineSegment(sketch, "E5043", {"start": v(6.66, -19.88) * mm, "end": v(6.56, -19.94) * mm});
            skLineSegment(sketch, "E5044", {"start": v(6.56, -19.94) * mm, "end": v(6.45, -19.98) * mm});
            skLineSegment(sketch, "E5045", {"start": v(6.45, -19.98) * mm, "end": v(6.32, -20.03) * mm});
            skLineSegment(sketch, "E5046", {"start": v(6.32, -20.03) * mm, "end": v(6.18, -20.07) * mm});
            skLineSegment(sketch, "E5047", {"start": v(6.18, -20.07) * mm, "end": v(6.04, -20.11) * mm});
            skLineSegment(sketch, "E5048", {"start": v(6.04, -20.11) * mm, "end": v(5.93, -20.17) * mm});
            skLineSegment(sketch, "E5049", {"start": v(5.93, -20.17) * mm, "end": v(5.84, -20.23) * mm});
            skLineSegment(sketch, "E5050", {"start": v(5.84, -20.23) * mm, "end": v(5.76, -20.3) * mm});
            skLineSegment(sketch, "E5051", {"start": v(5.76, -20.3) * mm, "end": v(5.68, -20.36) * mm});
            skLineSegment(sketch, "E5052", {"start": v(5.68, -20.36) * mm, "end": v(5.59, -20.42) * mm});
            skLineSegment(sketch, "E5053", {"start": v(5.59, -20.42) * mm, "end": v(5.48, -20.48) * mm});
            skLineSegment(sketch, "E5054", {"start": v(5.48, -20.48) * mm, "end": v(5.34, -20.52) * mm});
            skLineSegment(sketch, "E5055", {"start": v(5.34, -20.52) * mm, "end": v(5.36, -20.7) * mm});
            skLineSegment(sketch, "E5056", {"start": v(5.36, -20.7) * mm, "end": v(5.41, -20.87) * mm});
            skLineSegment(sketch, "E5057", {"start": v(5.41, -20.87) * mm, "end": v(5.47, -21.04) * mm});
            skLineSegment(sketch, "E5058", {"start": v(5.47, -21.04) * mm, "end": v(5.52, -21.2) * mm});
            skLineSegment(sketch, "E5059", {"start": v(5.52, -21.2) * mm, "end": v(5.58, -21.4) * mm});
            skLineSegment(sketch, "E5060", {"start": v(5.58, -21.4) * mm, "end": v(5.64, -21.65) * mm});
            skLineSegment(sketch, "E5061", {"start": v(5.64, -21.65) * mm, "end": v(5.7, -21.92) * mm});
            skLineSegment(sketch, "E5062", {"start": v(5.7, -21.92) * mm, "end": v(5.77, -22.2) * mm});
            skLineSegment(sketch, "E5063", {"start": v(5.77, -22.2) * mm, "end": v(5.83, -22.48) * mm});
            skLineSegment(sketch, "E5064", {"start": v(5.83, -22.48) * mm, "end": v(5.88, -22.75) * mm});
            skLineSegment(sketch, "E5065", {"start": v(5.88, -22.75) * mm, "end": v(5.92, -22.99) * mm});
            skLineSegment(sketch, "E5066", {"start": v(5.92, -22.99) * mm, "end": v(5.95, -23.19) * mm});
            skLineSegment(sketch, "E5067", {"start": v(5.95, -23.19) * mm, "end": v(6.1, -23.26) * mm});
            skLineSegment(sketch, "E5068", {"start": v(6.1, -23.26) * mm, "end": v(6.22, -23.32) * mm});
            skLineSegment(sketch, "E5069", {"start": v(6.22, -23.32) * mm, "end": v(6.32, -23.37) * mm});
            skLineSegment(sketch, "E5070", {"start": v(6.32, -23.37) * mm, "end": v(6.42, -23.4) * mm});
            skLineSegment(sketch, "E5071", {"start": v(6.42, -23.4) * mm, "end": v(6.53, -23.43) * mm});
            skLineSegment(sketch, "E5072", {"start": v(6.53, -23.43) * mm, "end": v(6.65, -23.45) * mm});
            skLineSegment(sketch, "E5073", {"start": v(6.65, -23.45) * mm, "end": v(6.8, -23.47) * mm});
            skLineSegment(sketch, "E5074", {"start": v(6.8, -23.47) * mm, "end": v(6.98, -23.5) * mm});
            skLineSegment(sketch, "E5075", {"start": v(15.1, -2.98) * mm, "end": v(14.46, -2.96) * mm});
            skLineSegment(sketch, "E5076", {"start": v(14.46, -2.96) * mm, "end": v(13.94, -2.91) * mm});
            skLineSegment(sketch, "E5077", {"start": v(13.94, -2.91) * mm, "end": v(13.52, -2.85) * mm});
            skLineSegment(sketch, "E5078", {"start": v(13.52, -2.85) * mm, "end": v(13.2, -2.77) * mm});
            skLineSegment(sketch, "E5079", {"start": v(13.2, -2.77) * mm, "end": v(12.95, -2.7) * mm});
            skLineSegment(sketch, "E5080", {"start": v(12.95, -2.7) * mm, "end": v(12.76, -2.63) * mm});
            skLineSegment(sketch, "E5081", {"start": v(12.76, -2.63) * mm, "end": v(12.6, -2.57) * mm});
            skLineSegment(sketch, "E5082", {"start": v(12.6, -2.57) * mm, "end": v(12.46, -2.55) * mm});
            skLineSegment(sketch, "E5083", {"start": v(12.46, -2.55) * mm, "end": v(12.44, -2.67) * mm});
            skLineSegment(sketch, "E5084", {"start": v(12.44, -2.67) * mm, "end": v(12.42, -2.8) * mm});
            skLineSegment(sketch, "E5085", {"start": v(12.42, -2.8) * mm, "end": v(12.39, -2.92) * mm});
            skLineSegment(sketch, "E5086", {"start": v(12.39, -2.92) * mm, "end": v(12.35, -3.05) * mm});
            skLineSegment(sketch, "E5087", {"start": v(12.35, -3.05) * mm, "end": v(12.31, -3.17) * mm});
            skLineSegment(sketch, "E5088", {"start": v(12.31, -3.17) * mm, "end": v(12.27, -3.28) * mm});
            skLineSegment(sketch, "E5089", {"start": v(12.27, -3.28) * mm, "end": v(12.22, -3.38) * mm});
            skLineSegment(sketch, "E5090", {"start": v(12.22, -3.38) * mm, "end": v(12.17, -3.47) * mm});
            skLineSegment(sketch, "E5091", {"start": v(12.17, -3.47) * mm, "end": v(12.43, -3.65) * mm});
            skLineSegment(sketch, "E5092", {"start": v(12.43, -3.65) * mm, "end": v(12.76, -3.8) * mm});
            skLineSegment(sketch, "E5093", {"start": v(12.76, -3.8) * mm, "end": v(13.12, -3.9) * mm});
            skLineSegment(sketch, "E5094", {"start": v(13.12, -3.9) * mm, "end": v(13.52, -4) * mm});
            skLineSegment(sketch, "E5095", {"start": v(13.52, -4) * mm, "end": v(13.94, -4.07) * mm});
            skLineSegment(sketch, "E5096", {"start": v(13.94, -4.07) * mm, "end": v(14.35, -4.11) * mm});
            skLineSegment(sketch, "E5097", {"start": v(14.35, -4.11) * mm, "end": v(14.76, -4.14) * mm});
            skLineSegment(sketch, "E5098", {"start": v(14.76, -4.14) * mm, "end": v(15.15, -4.15) * mm});
            skLineSegment(sketch, "E5099", {"start": v(15.15, -4.15) * mm, "end": v(15.5, -4.14) * mm});
            skLineSegment(sketch, "E5100", {"start": v(15.5, -4.14) * mm, "end": v(15.84, -4.12) * mm});
            skLineSegment(sketch, "E5101", {"start": v(15.84, -4.12) * mm, "end": v(16.16, -4.1) * mm});
            skLineSegment(sketch, "E5102", {"start": v(16.16, -4.1) * mm, "end": v(16.5, -4.05) * mm});
            skLineSegment(sketch, "E5103", {"start": v(16.5, -4.05) * mm, "end": v(16.7, -4.02) * mm});
            skLineSegment(sketch, "E5104", {"start": v(16.7, -4.02) * mm, "end": v(16.85, -3.99) * mm});
            skLineSegment(sketch, "E5105", {"start": v(16.85, -3.99) * mm, "end": v(16.98, -3.95) * mm});
            skLineSegment(sketch, "E5106", {"start": v(16.98, -3.95) * mm, "end": v(17.1, -3.9) * mm});
            skLineSegment(sketch, "E5107", {"start": v(17.1, -3.9) * mm, "end": v(17.2, -3.84) * mm});
            skLineSegment(sketch, "E5108", {"start": v(17.2, -3.84) * mm, "end": v(17.3, -3.78) * mm});
            skLineSegment(sketch, "E5109", {"start": v(17.3, -3.78) * mm, "end": v(17.4, -3.7) * mm});
            skLineSegment(sketch, "E5110", {"start": v(17.4, -3.7) * mm, "end": v(17.53, -3.6) * mm});
            skLineSegment(sketch, "E5111", {"start": v(17.53, -3.6) * mm, "end": v(17.7, -3.47) * mm});
            skLineSegment(sketch, "E5112", {"start": v(17.7, -3.47) * mm, "end": v(17.88, -3.29) * mm});
            skLineSegment(sketch, "E5113", {"start": v(17.88, -3.29) * mm, "end": v(18.09, -3.08) * mm});
            skLineSegment(sketch, "E5114", {"start": v(18.09, -3.08) * mm, "end": v(18.29, -2.86) * mm});
            skLineSegment(sketch, "E5115", {"start": v(18.29, -2.86) * mm, "end": v(18.48, -2.62) * mm});
            skLineSegment(sketch, "E5116", {"start": v(18.48, -2.62) * mm, "end": v(18.63, -2.4) * mm});
            skLineSegment(sketch, "E5117", {"start": v(18.63, -2.4) * mm, "end": v(18.75, -2.19) * mm});
            skLineSegment(sketch, "E5118", {"start": v(18.75, -2.19) * mm, "end": v(18.8, -2) * mm});
            skLineSegment(sketch, "E5119", {"start": v(18.8, -2) * mm, "end": v(18.67, -2.11) * mm});
            skLineSegment(sketch, "E5120", {"start": v(18.67, -2.11) * mm, "end": v(18.5, -2.22) * mm});
            skLineSegment(sketch, "E5121", {"start": v(18.5, -2.22) * mm, "end": v(18.28, -2.32) * mm});
            skLineSegment(sketch, "E5122", {"start": v(18.28, -2.32) * mm, "end": v(18.06, -2.42) * mm});
            skLineSegment(sketch, "E5123", {"start": v(18.06, -2.42) * mm, "end": v(17.83, -2.5) * mm});
            skLineSegment(sketch, "E5124", {"start": v(17.83, -2.5) * mm, "end": v(17.61, -2.59) * mm});
            skLineSegment(sketch, "E5125", {"start": v(17.61, -2.59) * mm, "end": v(17.41, -2.65) * mm});
            skLineSegment(sketch, "E5126", {"start": v(17.41, -2.65) * mm, "end": v(17.25, -2.7) * mm});
            skLineSegment(sketch, "E5127", {"start": v(17.25, -2.7) * mm, "end": v(16.99, -2.77) * mm});
            skLineSegment(sketch, "E5128", {"start": v(16.99, -2.77) * mm, "end": v(16.73, -2.83) * mm});
            skLineSegment(sketch, "E5129", {"start": v(16.73, -2.83) * mm, "end": v(16.47, -2.88) * mm});
            skLineSegment(sketch, "E5130", {"start": v(16.47, -2.88) * mm, "end": v(16.2, -2.91) * mm});
            skLineSegment(sketch, "E5131", {"start": v(16.2, -2.91) * mm, "end": v(15.94, -2.94) * mm});
            skLineSegment(sketch, "E5132", {"start": v(15.94, -2.94) * mm, "end": v(15.67, -2.96) * mm});
            skLineSegment(sketch, "E5133", {"start": v(15.67, -2.96) * mm, "end": v(15.4, -2.98) * mm});
            skLineSegment(sketch, "E5134", {"start": v(15.4, -2.98) * mm, "end": v(15.1, -2.98) * mm});
            skLineSegment(sketch, "E5135", {"start": v(-12.16, -3.48) * mm, "end": v(-12.27, -3.25) * mm});
            skLineSegment(sketch, "E5136", {"start": v(-12.27, -3.25) * mm, "end": v(-12.36, -3.05) * mm});
            skLineSegment(sketch, "E5137", {"start": v(-12.36, -3.05) * mm, "end": v(-12.4, -2.94) * mm});
            skLineSegment(sketch, "E5138", {"start": v(-12.4, -2.94) * mm, "end": v(-12.42, -2.83) * mm});
            skLineSegment(sketch, "E5139", {"start": v(-12.42, -2.83) * mm, "end": v(-12.44, -2.7) * mm});
            skLineSegment(sketch, "E5140", {"start": v(-12.44, -2.7) * mm, "end": v(-12.46, -2.55) * mm});
            skLineSegment(sketch, "E5141", {"start": v(-12.46, -2.55) * mm, "end": v(-12.67, -2.59) * mm});
            skLineSegment(sketch, "E5142", {"start": v(-12.67, -2.59) * mm, "end": v(-12.88, -2.66) * mm});
            skLineSegment(sketch, "E5143", {"start": v(-12.88, -2.66) * mm, "end": v(-13.13, -2.74) * mm});
            skLineSegment(sketch, "E5144", {"start": v(-13.13, -2.74) * mm, "end": v(-13.44, -2.83) * mm});
            skLineSegment(sketch, "E5145", {"start": v(-13.44, -2.83) * mm, "end": v(-13.84, -2.91) * mm});
            skLineSegment(sketch, "E5146", {"start": v(-13.84, -2.91) * mm, "end": v(-14.35, -2.96) * mm});
            skLineSegment(sketch, "E5147", {"start": v(-14.35, -2.96) * mm, "end": v(-15, -2.98) * mm});
            skLineSegment(sketch, "E5148", {"start": v(-15, -2.98) * mm, "end": v(-15.82, -2.95) * mm});
            skLineSegment(sketch, "E5149", {"start": v(-15.82, -2.95) * mm, "end": v(-16.24, -2.91) * mm});
            skLineSegment(sketch, "E5150", {"start": v(-16.24, -2.91) * mm, "end": v(-16.64, -2.86) * mm});
            skLineSegment(sketch, "E5151", {"start": v(-16.64, -2.86) * mm, "end": v(-17.03, -2.77) * mm});
            skLineSegment(sketch, "E5152", {"start": v(-17.03, -2.77) * mm, "end": v(-17.4, -2.67) * mm});
            skLineSegment(sketch, "E5153", {"start": v(-17.4, -2.67) * mm, "end": v(-17.77, -2.54) * mm});
            skLineSegment(sketch, "E5154", {"start": v(-17.77, -2.54) * mm, "end": v(-18.12, -2.39) * mm});
            skLineSegment(sketch, "E5155", {"start": v(-18.12, -2.39) * mm, "end": v(-18.47, -2.2) * mm});
            skLineSegment(sketch, "E5156", {"start": v(-18.47, -2.2) * mm, "end": v(-18.82, -2) * mm});
            skLineSegment(sketch, "E5157", {"start": v(-18.82, -2) * mm, "end": v(-18.71, -2.2) * mm});
            skLineSegment(sketch, "E5158", {"start": v(-18.71, -2.2) * mm, "end": v(-18.62, -2.38) * mm});
            skLineSegment(sketch, "E5159", {"start": v(-18.62, -2.38) * mm, "end": v(-18.52, -2.55) * mm});
            skLineSegment(sketch, "E5160", {"start": v(-18.52, -2.55) * mm, "end": v(-18.4, -2.73) * mm});
            skLineSegment(sketch, "E5161", {"start": v(-18.4, -2.73) * mm, "end": v(-18.3, -2.88) * mm});
            skLineSegment(sketch, "E5162", {"start": v(-18.3, -2.88) * mm, "end": v(-18.15, -3.03) * mm});
            skLineSegment(sketch, "E5163", {"start": v(-18.15, -3.03) * mm, "end": v(-18, -3.2) * mm});
            skLineSegment(sketch, "E5164", {"start": v(-18, -3.2) * mm, "end": v(-17.83, -3.35) * mm});
            skLineSegment(sketch, "E5165", {"start": v(-17.83, -3.35) * mm, "end": v(-17.65, -3.5) * mm});
            skLineSegment(sketch, "E5166", {"start": v(-17.65, -3.5) * mm, "end": v(-17.48, -3.64) * mm});
            skLineSegment(sketch, "E5167", {"start": v(-17.48, -3.64) * mm, "end": v(-17.31, -3.76) * mm});
            skLineSegment(sketch, "E5168", {"start": v(-17.31, -3.76) * mm, "end": v(-17.16, -3.86) * mm});
            skLineSegment(sketch, "E5169", {"start": v(-17.16, -3.86) * mm, "end": v(-16.77, -4) * mm});
            skLineSegment(sketch, "E5170", {"start": v(-16.77, -4) * mm, "end": v(-16.2, -4.1) * mm});
            skLineSegment(sketch, "E5171", {"start": v(-16.2, -4.1) * mm, "end": v(-15.52, -4.15) * mm});
            skLineSegment(sketch, "E5172", {"start": v(-15.52, -4.15) * mm, "end": v(-14.76, -4.14) * mm});
            skLineSegment(sketch, "E5173", {"start": v(-14.76, -4.14) * mm, "end": v(-14, -4.07) * mm});
            skLineSegment(sketch, "E5174", {"start": v(-14, -4.07) * mm, "end": v(-13.26, -3.93) * mm});
            skLineSegment(sketch, "E5175", {"start": v(-13.26, -3.93) * mm, "end": v(-12.64, -3.74) * mm});
            skLineSegment(sketch, "E5176", {"start": v(-12.64, -3.74) * mm, "end": v(-12.16, -3.48) * mm});
            skLineSegment(sketch, "E5177", {"start": v(-10, 0.03) * mm, "end": v(-10.18, 0.22) * mm});
            skLineSegment(sketch, "E5178", {"start": v(-10.18, 0.22) * mm, "end": v(-10.32, 0.34) * mm});
            skLineSegment(sketch, "E5179", {"start": v(-10.32, 0.34) * mm, "end": v(-10.38, 0.4) * mm});
            skLineSegment(sketch, "E5180", {"start": v(-10.38, 0.4) * mm, "end": v(-10.45, 0.49) * mm});
            skLineSegment(sketch, "E5181", {"start": v(-10.45, 0.49) * mm, "end": v(-10.53, 0.6) * mm});
            skLineSegment(sketch, "E5182", {"start": v(-10.53, 0.6) * mm, "end": v(-10.63, 0.75) * mm});
            skLineSegment(sketch, "E5183", {"start": v(-10.63, 0.75) * mm, "end": v(-10.7, 0.87) * mm});
            skLineSegment(sketch, "E5184", {"start": v(-10.7, 0.87) * mm, "end": v(-10.75, 0.98) * mm});
            skLineSegment(sketch, "E5185", {"start": v(-10.75, 0.98) * mm, "end": v(-10.8, 1.1) * mm});
            skLineSegment(sketch, "E5186", {"start": v(-10.8, 1.1) * mm, "end": v(-10.85, 1.24) * mm});
            skLineSegment(sketch, "E5187", {"start": v(-10.85, 1.24) * mm, "end": v(-10.9, 1.4) * mm});
            skLineSegment(sketch, "E5188", {"start": v(-10.9, 1.4) * mm, "end": v(-10.94, 1.51) * mm});
            skLineSegment(sketch, "E5189", {"start": v(-10.94, 1.51) * mm, "end": v(-10.96, 1.56) * mm});
            skLineSegment(sketch, "E5190", {"start": v(-10.96, 1.56) * mm, "end": v(-11, 1.6) * mm});
            skLineSegment(sketch, "E5191", {"start": v(-11, 1.6) * mm, "end": v(-11.04, 1.64) * mm});
            skLineSegment(sketch, "E5192", {"start": v(-11.04, 1.64) * mm, "end": v(-11.11, 1.68) * mm});
            skLineSegment(sketch, "E5193", {"start": v(-11.11, 1.68) * mm, "end": v(-11.35, 1.78) * mm});
            skLineSegment(sketch, "E5194", {"start": v(-11.35, 1.78) * mm, "end": v(-11.6, 1.9) * mm});
            skLineSegment(sketch, "E5195", {"start": v(-11.6, 1.9) * mm, "end": v(-11.84, 2.01) * mm});
            skLineSegment(sketch, "E5196", {"start": v(-11.84, 2.01) * mm, "end": v(-12.08, 2.13) * mm});
            skLineSegment(sketch, "E5197", {"start": v(-12.08, 2.13) * mm, "end": v(-12.32, 2.25) * mm});
            skLineSegment(sketch, "E5198", {"start": v(-12.32, 2.25) * mm, "end": v(-12.56, 2.38) * mm});
            skLineSegment(sketch, "E5199", {"start": v(-12.56, 2.38) * mm, "end": v(-12.78, 2.5) * mm});
            skLineSegment(sketch, "E5200", {"start": v(-12.78, 2.5) * mm, "end": v(-13, 2.63) * mm});
            skLineSegment(sketch, "E5201", {"start": v(-13, 2.63) * mm, "end": v(-16.47, 4.76) * mm});
            skLineSegment(sketch, "E5202", {"start": v(-16.47, 4.76) * mm, "end": v(-16.37, 4.52) * mm});
            skLineSegment(sketch, "E5203", {"start": v(-16.37, 4.52) * mm, "end": v(-16.24, 4.28) * mm});
            skLineSegment(sketch, "E5204", {"start": v(-16.24, 4.28) * mm, "end": v(-16.09, 4.04) * mm});
            skLineSegment(sketch, "E5205", {"start": v(-16.09, 4.04) * mm, "end": v(-15.92, 3.8) * mm});
            skLineSegment(sketch, "E5206", {"start": v(-15.92, 3.8) * mm, "end": v(-15.74, 3.57) * mm});
            skLineSegment(sketch, "E5207", {"start": v(-15.74, 3.57) * mm, "end": v(-15.55, 3.35) * mm});
            skLineSegment(sketch, "E5208", {"start": v(-15.55, 3.35) * mm, "end": v(-15.36, 3.14) * mm});
            skLineSegment(sketch, "E5209", {"start": v(-15.36, 3.14) * mm, "end": v(-15.18, 2.94) * mm});
            skLineSegment(sketch, "E5210", {"start": v(-15.18, 2.94) * mm, "end": v(-15.03, 2.78) * mm});
            skLineSegment(sketch, "E5211", {"start": v(-15.03, 2.78) * mm, "end": v(-14.86, 2.63) * mm});
            skLineSegment(sketch, "E5212", {"start": v(-14.86, 2.63) * mm, "end": v(-14.7, 2.5) * mm});
            skLineSegment(sketch, "E5213", {"start": v(-14.7, 2.5) * mm, "end": v(-14.52, 2.35) * mm});
            skLineSegment(sketch, "E5214", {"start": v(-14.52, 2.35) * mm, "end": v(-14.17, 2.09) * mm});
            skLineSegment(sketch, "E5215", {"start": v(-14.17, 2.09) * mm, "end": v(-13.8, 1.82) * mm});
            skLineSegment(sketch, "E5216", {"start": v(-13.8, 1.82) * mm, "end": v(-13.47, 1.6) * mm});
            skLineSegment(sketch, "E5217", {"start": v(-13.47, 1.6) * mm, "end": v(-13, 1.34) * mm});
            skLineSegment(sketch, "E5218", {"start": v(-13, 1.34) * mm, "end": v(-12.44, 1.05) * mm});
            skLineSegment(sketch, "E5219", {"start": v(-12.44, 1.05) * mm, "end": v(-11.84, 0.76) * mm});
            skLineSegment(sketch, "E5220", {"start": v(-11.84, 0.76) * mm, "end": v(-11.25, 0.48) * mm});
            skLineSegment(sketch, "E5221", {"start": v(-11.25, 0.48) * mm, "end": v(-10.71, 0.26) * mm});
            skLineSegment(sketch, "E5222", {"start": v(-10.71, 0.26) * mm, "end": v(-10.28, 0.1) * mm});
            skLineSegment(sketch, "E5223", {"start": v(-10.28, 0.1) * mm, "end": v(-10, 0.03) * mm});
            skLineSegment(sketch, "E5224", {"start": v(5.98, -13.27) * mm, "end": v(5.93, -13) * mm});
            skLineSegment(sketch, "E5225", {"start": v(5.93, -13) * mm, "end": v(5.88, -12.73) * mm});
            skLineSegment(sketch, "E5226", {"start": v(5.88, -12.73) * mm, "end": v(5.83, -12.46) * mm});
            skLineSegment(sketch, "E5227", {"start": v(5.83, -12.46) * mm, "end": v(5.78, -12.18) * mm});
            skLineSegment(sketch, "E5228", {"start": v(5.78, -12.18) * mm, "end": v(5.76, -11.9) * mm});
            skLineSegment(sketch, "E5229", {"start": v(5.76, -11.9) * mm, "end": v(5.76, -11.6) * mm});
            skLineSegment(sketch, "E5230", {"start": v(5.76, -11.6) * mm, "end": v(5.8, -11.32) * mm});
            skLineSegment(sketch, "E5231", {"start": v(5.8, -11.32) * mm, "end": v(5.9, -11.04) * mm});
            skLineSegment(sketch, "E5232", {"start": v(5.9, -11.04) * mm, "end": v(6, -11.22) * mm});
            skLineSegment(sketch, "E5233", {"start": v(6, -11.22) * mm, "end": v(6.11, -11.43) * mm});
            skLineSegment(sketch, "E5234", {"start": v(6.11, -11.43) * mm, "end": v(6.22, -11.65) * mm});
            skLineSegment(sketch, "E5235", {"start": v(6.22, -11.65) * mm, "end": v(6.33, -11.85) * mm});
            skLineSegment(sketch, "E5236", {"start": v(6.33, -11.85) * mm, "end": v(6.45, -12.03) * mm});
            skLineSegment(sketch, "E5237", {"start": v(6.45, -12.03) * mm, "end": v(6.57, -12.21) * mm});
            skLineSegment(sketch, "E5238", {"start": v(6.57, -12.21) * mm, "end": v(6.7, -12.4) * mm});
            skLineSegment(sketch, "E5239", {"start": v(6.7, -12.4) * mm, "end": v(6.85, -12.58) * mm});
            skLineSegment(sketch, "E5240", {"start": v(6.85, -12.58) * mm, "end": v(7, -12.76) * mm});
            skLineSegment(sketch, "E5241", {"start": v(7, -12.76) * mm, "end": v(7.15, -12.92) * mm});
            skLineSegment(sketch, "E5242", {"start": v(7.15, -12.92) * mm, "end": v(7.3, -13.07) * mm});
            skLineSegment(sketch, "E5243", {"start": v(7.3, -13.07) * mm, "end": v(7.48, -13.2) * mm});
            skLineSegment(sketch, "E5244", {"start": v(7.48, -13.2) * mm, "end": v(7.63, -13.32) * mm});
            skLineSegment(sketch, "E5245", {"start": v(7.63, -13.32) * mm, "end": v(7.86, -13.47) * mm});
            skLineSegment(sketch, "E5246", {"start": v(7.86, -13.47) * mm, "end": v(7.97, -13.55) * mm});
            skLineSegment(sketch, "E5247", {"start": v(7.97, -13.55) * mm, "end": v(8.09, -13.62) * mm});
            skLineSegment(sketch, "E5248", {"start": v(8.09, -13.62) * mm, "end": v(8.2, -13.67) * mm});
            skLineSegment(sketch, "E5249", {"start": v(8.2, -13.67) * mm, "end": v(8.28, -13.7) * mm});
            skLineSegment(sketch, "E5250", {"start": v(8.28, -13.7) * mm, "end": v(8.12, -13.45) * mm});
            skLineSegment(sketch, "E5251", {"start": v(8.12, -13.45) * mm, "end": v(7.96, -13.2) * mm});
            skLineSegment(sketch, "E5252", {"start": v(7.96, -13.2) * mm, "end": v(7.8, -12.95) * mm});
            skLineSegment(sketch, "E5253", {"start": v(7.8, -12.95) * mm, "end": v(7.64, -12.68) * mm});
            skLineSegment(sketch, "E5254", {"start": v(7.64, -12.68) * mm, "end": v(7.5, -12.4) * mm});
            skLineSegment(sketch, "E5255", {"start": v(7.5, -12.4) * mm, "end": v(7.37, -12.08) * mm});
            skLineSegment(sketch, "E5256", {"start": v(7.37, -12.08) * mm, "end": v(7.28, -11.76) * mm});
            skLineSegment(sketch, "E5257", {"start": v(7.28, -11.76) * mm, "end": v(7.22, -11.4) * mm});
            skLineSegment(sketch, "E5258", {"start": v(7.22, -11.4) * mm, "end": v(7.33, -11.45) * mm});
            skLineSegment(sketch, "E5259", {"start": v(7.33, -11.45) * mm, "end": v(7.47, -11.53) * mm});
            skLineSegment(sketch, "E5260", {"start": v(7.47, -11.53) * mm, "end": v(7.64, -11.62) * mm});
            skLineSegment(sketch, "E5261", {"start": v(7.64, -11.62) * mm, "end": v(7.82, -11.72) * mm});
            skLineSegment(sketch, "E5262", {"start": v(7.82, -11.72) * mm, "end": v(8.03, -11.84) * mm});
            skLineSegment(sketch, "E5263", {"start": v(8.03, -11.84) * mm, "end": v(8.25, -11.95) * mm});
            skLineSegment(sketch, "E5264", {"start": v(8.25, -11.95) * mm, "end": v(8.5, -12.06) * mm});
            skLineSegment(sketch, "E5265", {"start": v(8.5, -12.06) * mm, "end": v(8.75, -12.17) * mm});
            skLineSegment(sketch, "E5266", {"start": v(8.75, -12.17) * mm, "end": v(8.95, -12.25) * mm});
            skLineSegment(sketch, "E5267", {"start": v(8.95, -12.25) * mm, "end": v(9.17, -12.32) * mm});
            skLineSegment(sketch, "E5268", {"start": v(9.17, -12.32) * mm, "end": v(9.4, -12.4) * mm});
            skLineSegment(sketch, "E5269", {"start": v(9.4, -12.4) * mm, "end": v(9.66, -12.46) * mm});
            skLineSegment(sketch, "E5270", {"start": v(9.66, -12.46) * mm, "end": v(9.91, -12.52) * mm});
            skLineSegment(sketch, "E5271", {"start": v(9.91, -12.52) * mm, "end": v(10.17, -12.56) * mm});
            skLineSegment(sketch, "E5272", {"start": v(10.17, -12.56) * mm, "end": v(10.42, -12.58) * mm});
            skLineSegment(sketch, "E5273", {"start": v(10.42, -12.58) * mm, "end": v(10.65, -12.59) * mm});
            skLineSegment(sketch, "E5274", {"start": v(10.65, -12.59) * mm, "end": v(10.59, -12.52) * mm});
            skLineSegment(sketch, "E5275", {"start": v(10.59, -12.52) * mm, "end": v(10.5, -12.46) * mm});
            skLineSegment(sketch, "E5276", {"start": v(10.5, -12.46) * mm, "end": v(10.38, -12.38) * mm});
            skLineSegment(sketch, "E5277", {"start": v(10.38, -12.38) * mm, "end": v(10.25, -12.29) * mm});
            skLineSegment(sketch, "E5278", {"start": v(10.25, -12.29) * mm, "end": v(10.1, -12.17) * mm});
            skLineSegment(sketch, "E5279", {"start": v(10.1, -12.17) * mm, "end": v(9.94, -12.03) * mm});
            skLineSegment(sketch, "E5280", {"start": v(9.94, -12.03) * mm, "end": v(9.78, -11.84) * mm});
            skLineSegment(sketch, "E5281", {"start": v(9.78, -11.84) * mm, "end": v(9.6, -11.61) * mm});
            skLineSegment(sketch, "E5282", {"start": v(9.6, -11.61) * mm, "end": v(9.55, -11.52) * mm});
            skLineSegment(sketch, "E5283", {"start": v(9.55, -11.52) * mm, "end": v(9.51, -11.46) * mm});
            skLineSegment(sketch, "E5284", {"start": v(9.51, -11.46) * mm, "end": v(9.49, -11.43) * mm});
            skLineSegment(sketch, "E5285", {"start": v(9.49, -11.43) * mm, "end": v(9.46, -11.4) * mm});
            skLineSegment(sketch, "E5286", {"start": v(9.46, -11.4) * mm, "end": v(9.42, -11.38) * mm});
            skLineSegment(sketch, "E5287", {"start": v(9.42, -11.38) * mm, "end": v(9.37, -11.36) * mm});
            skLineSegment(sketch, "E5288", {"start": v(9.37, -11.36) * mm, "end": v(8.3, -10.9) * mm});
            skLineSegment(sketch, "E5289", {"start": v(8.3, -10.9) * mm, "end": v(8.24, -10.89) * mm});
            skLineSegment(sketch, "E5290", {"start": v(8.24, -10.89) * mm, "end": v(8.19, -10.9) * mm});
            skLineSegment(sketch, "E5291", {"start": v(8.19, -10.9) * mm, "end": v(8.11, -10.92) * mm});
            skLineSegment(sketch, "E5292", {"start": v(8.11, -10.92) * mm, "end": v(8.03, -10.95) * mm});
            skLineSegment(sketch, "E5293", {"start": v(8.03, -10.95) * mm, "end": v(7.93, -10.98) * mm});
            skLineSegment(sketch, "E5294", {"start": v(7.93, -10.98) * mm, "end": v(7.81, -11.02) * mm});
            skLineSegment(sketch, "E5295", {"start": v(7.81, -11.02) * mm, "end": v(7.68, -11.05) * mm});
            skLineSegment(sketch, "E5296", {"start": v(7.68, -11.05) * mm, "end": v(7.53, -11.08) * mm});
            skLineSegment(sketch, "E5297", {"start": v(7.53, -11.08) * mm, "end": v(7.17, -11.12) * mm});
            skLineSegment(sketch, "E5298", {"start": v(7.17, -11.12) * mm, "end": v(6.82, -11.1) * mm});
            skLineSegment(sketch, "E5299", {"start": v(6.82, -11.1) * mm, "end": v(6.48, -11.04) * mm});
            skLineSegment(sketch, "E5300", {"start": v(6.48, -11.04) * mm, "end": v(6.16, -10.95) * mm});
            skLineSegment(sketch, "E5301", {"start": v(6.16, -10.95) * mm, "end": v(5.85, -10.85) * mm});
            skLineSegment(sketch, "E5302", {"start": v(5.85, -10.85) * mm, "end": v(5.55, -10.74) * mm});
            skLineSegment(sketch, "E5303", {"start": v(5.55, -10.74) * mm, "end": v(5.27, -10.63) * mm});
            skLineSegment(sketch, "E5304", {"start": v(5.27, -10.63) * mm, "end": v(5, -10.55) * mm});
            skLineSegment(sketch, "E5305", {"start": v(5, -10.55) * mm, "end": v(4.94, -11.48) * mm});
            skLineSegment(sketch, "E5306", {"start": v(4.94, -11.48) * mm, "end": v(4.9, -11.75) * mm});
            skLineSegment(sketch, "E5307", {"start": v(4.9, -11.75) * mm, "end": v(4.87, -11.96) * mm});
            skLineSegment(sketch, "E5308", {"start": v(4.87, -11.96) * mm, "end": v(4.87, -12.13) * mm});
            skLineSegment(sketch, "E5309", {"start": v(4.87, -12.13) * mm, "end": v(4.9, -12.28) * mm});
            skLineSegment(sketch, "E5310", {"start": v(4.9, -12.28) * mm, "end": v(5, -12.43) * mm});
            skLineSegment(sketch, "E5311", {"start": v(5, -12.43) * mm, "end": v(5.14, -12.6) * mm});
            skLineSegment(sketch, "E5312", {"start": v(5.14, -12.6) * mm, "end": v(5.37, -12.81) * mm});
            skLineSegment(sketch, "E5313", {"start": v(5.37, -12.81) * mm, "end": v(5.69, -13.08) * mm});
            skLineSegment(sketch, "E5314", {"start": v(5.69, -13.08) * mm, "end": v(5.84, -13.18) * mm});
            skLineSegment(sketch, "E5315", {"start": v(5.84, -13.18) * mm, "end": v(5.98, -13.27) * mm});
            skLineSegment(sketch, "E5316", {"start": v(10, 0.04) * mm, "end": v(10.3, 0.1) * mm});
            skLineSegment(sketch, "E5317", {"start": v(10.3, 0.1) * mm, "end": v(10.74, 0.27) * mm});
            skLineSegment(sketch, "E5318", {"start": v(10.74, 0.27) * mm, "end": v(11.28, 0.5) * mm});
            skLineSegment(sketch, "E5319", {"start": v(11.28, 0.5) * mm, "end": v(11.87, 0.78) * mm});
            skLineSegment(sketch, "E5320", {"start": v(11.87, 0.78) * mm, "end": v(12.47, 1.07) * mm});
            skLineSegment(sketch, "E5321", {"start": v(12.47, 1.07) * mm, "end": v(13.02, 1.36) * mm});
            skLineSegment(sketch, "E5322", {"start": v(13.02, 1.36) * mm, "end": v(13.48, 1.62) * mm});
            skLineSegment(sketch, "E5323", {"start": v(13.48, 1.62) * mm, "end": v(13.8, 1.82) * mm});
            skLineSegment(sketch, "E5324", {"start": v(13.8, 1.82) * mm, "end": v(14.22, 2.13) * mm});
            skLineSegment(sketch, "E5325", {"start": v(14.22, 2.13) * mm, "end": v(14.62, 2.44) * mm});
            skLineSegment(sketch, "E5326", {"start": v(14.62, 2.44) * mm, "end": v(15, 2.77) * mm});
            skLineSegment(sketch, "E5327", {"start": v(15, 2.77) * mm, "end": v(15.35, 3.12) * mm});
            skLineSegment(sketch, "E5328", {"start": v(15.35, 3.12) * mm, "end": v(15.68, 3.49) * mm});
            skLineSegment(sketch, "E5329", {"start": v(15.68, 3.49) * mm, "end": v(15.97, 3.88) * mm});
            skLineSegment(sketch, "E5330", {"start": v(15.97, 3.88) * mm, "end": v(16.24, 4.3) * mm});
            skLineSegment(sketch, "E5331", {"start": v(16.24, 4.3) * mm, "end": v(16.47, 4.76) * mm});
            skLineSegment(sketch, "E5332", {"start": v(16.47, 4.76) * mm, "end": v(14.79, 3.67) * mm});
            skLineSegment(sketch, "E5333", {"start": v(14.79, 3.67) * mm, "end": v(14.43, 3.45) * mm});
            skLineSegment(sketch, "E5334", {"start": v(14.43, 3.45) * mm, "end": v(14, 3.2) * mm});
            skLineSegment(sketch, "E5335", {"start": v(14, 3.2) * mm, "end": v(13.52, 2.92) * mm});
            skLineSegment(sketch, "E5336", {"start": v(13.52, 2.92) * mm, "end": v(13.02, 2.64) * mm});
            skLineSegment(sketch, "E5337", {"start": v(13.02, 2.64) * mm, "end": v(12.51, 2.37) * mm});
            skLineSegment(sketch, "E5338", {"start": v(12.51, 2.37) * mm, "end": v(12.02, 2.11) * mm});
            skLineSegment(sketch, "E5339", {"start": v(12.02, 2.11) * mm, "end": v(11.55, 1.88) * mm});
            skLineSegment(sketch, "E5340", {"start": v(11.55, 1.88) * mm, "end": v(11.14, 1.69) * mm});
            skLineSegment(sketch, "E5341", {"start": v(11.14, 1.69) * mm, "end": v(11.04, 1.63) * mm});
            skLineSegment(sketch, "E5342", {"start": v(11.04, 1.63) * mm, "end": v(10.97, 1.58) * mm});
            skLineSegment(sketch, "E5343", {"start": v(10.97, 1.58) * mm, "end": v(10.93, 1.51) * mm});
            skLineSegment(sketch, "E5344", {"start": v(10.93, 1.51) * mm, "end": v(10.9, 1.43) * mm});
            skLineSegment(sketch, "E5345", {"start": v(10.9, 1.43) * mm, "end": v(10.88, 1.33) * mm});
            skLineSegment(sketch, "E5346", {"start": v(10.88, 1.33) * mm, "end": v(10.83, 1.19) * mm});
            skLineSegment(sketch, "E5347", {"start": v(10.83, 1.19) * mm, "end": v(10.76, 1) * mm});
            skLineSegment(sketch, "E5348", {"start": v(10.76, 1) * mm, "end": v(10.64, 0.78) * mm});
            skLineSegment(sketch, "E5349", {"start": v(10.64, 0.78) * mm, "end": v(10.57, 0.68) * mm});
            skLineSegment(sketch, "E5350", {"start": v(10.57, 0.68) * mm, "end": v(10.5, 0.57) * mm});
            skLineSegment(sketch, "E5351", {"start": v(10.5, 0.57) * mm, "end": v(10.42, 0.47) * mm});
            skLineSegment(sketch, "E5352", {"start": v(10.42, 0.47) * mm, "end": v(10.34, 0.36) * mm});
            skLineSegment(sketch, "E5353", {"start": v(10.34, 0.36) * mm, "end": v(10.25, 0.27) * mm});
            skLineSegment(sketch, "E5354", {"start": v(10.25, 0.27) * mm, "end": v(10.16, 0.18) * mm});
            skLineSegment(sketch, "E5355", {"start": v(10.16, 0.18) * mm, "end": v(10.08, 0.1) * mm});
            skLineSegment(sketch, "E5356", {"start": v(10.08, 0.1) * mm, "end": v(10, 0.04) * mm});
            skLineSegment(sketch, "E5357", {"start": v(-10.66, -12.6) * mm, "end": v(-10.28, -12.57) * mm});
            skLineSegment(sketch, "E5358", {"start": v(-10.28, -12.57) * mm, "end": v(-9.92, -12.52) * mm});
            skLineSegment(sketch, "E5359", {"start": v(-9.92, -12.52) * mm, "end": v(-9.58, -12.45) * mm});
            skLineSegment(sketch, "E5360", {"start": v(-9.58, -12.45) * mm, "end": v(-9.25, -12.35) * mm});
            skLineSegment(sketch, "E5361", {"start": v(-9.25, -12.35) * mm, "end": v(-8.93, -12.24) * mm});
            skLineSegment(sketch, "E5362", {"start": v(-8.93, -12.24) * mm, "end": v(-8.62, -12.1) * mm});
            skLineSegment(sketch, "E5363", {"start": v(-8.62, -12.1) * mm, "end": v(-8.3, -11.97) * mm});
            skLineSegment(sketch, "E5364", {"start": v(-8.3, -11.97) * mm, "end": v(-7.98, -11.82) * mm});
            skLineSegment(sketch, "E5365", {"start": v(-7.98, -11.82) * mm, "end": v(-7.8, -11.72) * mm});
            skLineSegment(sketch, "E5366", {"start": v(-7.8, -11.72) * mm, "end": v(-7.6, -11.6) * mm});
            skLineSegment(sketch, "E5367", {"start": v(-7.6, -11.6) * mm, "end": v(-7.4, -11.5) * mm});
            skLineSegment(sketch, "E5368", {"start": v(-7.4, -11.5) * mm, "end": v(-7.24, -11.4) * mm});
            skLineSegment(sketch, "E5369", {"start": v(-7.24, -11.4) * mm, "end": v(-7.26, -11.65) * mm});
            skLineSegment(sketch, "E5370", {"start": v(-7.26, -11.65) * mm, "end": v(-7.32, -11.92) * mm});
            skLineSegment(sketch, "E5371", {"start": v(-7.32, -11.92) * mm, "end": v(-7.42, -12.2) * mm});
            skLineSegment(sketch, "E5372", {"start": v(-7.42, -12.2) * mm, "end": v(-7.54, -12.48) * mm});
            skLineSegment(sketch, "E5373", {"start": v(-7.54, -12.48) * mm, "end": v(-7.68, -12.76) * mm});
            skLineSegment(sketch, "E5374", {"start": v(-7.68, -12.76) * mm, "end": v(-7.83, -13.02) * mm});
            skLineSegment(sketch, "E5375", {"start": v(-7.83, -13.02) * mm, "end": v(-7.97, -13.25) * mm});
            skLineSegment(sketch, "E5376", {"start": v(-7.97, -13.25) * mm, "end": v(-8.1, -13.45) * mm});
            skLineSegment(sketch, "E5377", {"start": v(-8.1, -13.45) * mm, "end": v(-8.29, -13.7) * mm});
            skLineSegment(sketch, "E5378", {"start": v(-8.29, -13.7) * mm, "end": v(-8.04, -13.6) * mm});
            skLineSegment(sketch, "E5379", {"start": v(-8.04, -13.6) * mm, "end": v(-7.78, -13.44) * mm});
            skLineSegment(sketch, "E5380", {"start": v(-7.78, -13.44) * mm, "end": v(-7.5, -13.22) * mm});
            skLineSegment(sketch, "E5381", {"start": v(-7.5, -13.22) * mm, "end": v(-7.21, -12.96) * mm});
            skLineSegment(sketch, "E5382", {"start": v(-7.21, -12.96) * mm, "end": v(-6.95, -12.68) * mm});
            skLineSegment(sketch, "E5383", {"start": v(-6.95, -12.68) * mm, "end": v(-6.7, -12.4) * mm});
            skLineSegment(sketch, "E5384", {"start": v(-6.7, -12.4) * mm, "end": v(-6.5, -12.12) * mm});
            skLineSegment(sketch, "E5385", {"start": v(-6.5, -12.12) * mm, "end": v(-6.35, -11.88) * mm});
            skLineSegment(sketch, "E5386", {"start": v(-6.35, -11.88) * mm, "end": v(-6.25, -11.7) * mm});
            skLineSegment(sketch, "E5387", {"start": v(-6.25, -11.7) * mm, "end": v(-6.12, -11.44) * mm});
            skLineSegment(sketch, "E5388", {"start": v(-6.12, -11.44) * mm, "end": v(-5.99, -11.19) * mm});
            skLineSegment(sketch, "E5389", {"start": v(-5.99, -11.19) * mm, "end": v(-5.9, -11.05) * mm});
            skLineSegment(sketch, "E5390", {"start": v(-5.9, -11.05) * mm, "end": v(-5.83, -11.25) * mm});
            skLineSegment(sketch, "E5391", {"start": v(-5.83, -11.25) * mm, "end": v(-5.79, -11.52) * mm});
            skLineSegment(sketch, "E5392", {"start": v(-5.79, -11.52) * mm, "end": v(-5.78, -11.83) * mm});
            skLineSegment(sketch, "E5393", {"start": v(-5.78, -11.83) * mm, "end": v(-5.79, -12.16) * mm});
            skLineSegment(sketch, "E5394", {"start": v(-5.79, -12.16) * mm, "end": v(-5.82, -12.5) * mm});
            skLineSegment(sketch, "E5395", {"start": v(-5.82, -12.5) * mm, "end": v(-5.87, -12.8) * mm});
            skLineSegment(sketch, "E5396", {"start": v(-5.87, -12.8) * mm, "end": v(-5.93, -13.07) * mm});
            skLineSegment(sketch, "E5397", {"start": v(-5.93, -13.07) * mm, "end": v(-6, -13.26) * mm});
            skLineSegment(sketch, "E5398", {"start": v(-6, -13.26) * mm, "end": v(-5.9, -13.22) * mm});
            skLineSegment(sketch, "E5399", {"start": v(-5.9, -13.22) * mm, "end": v(-5.75, -13.13) * mm});
            skLineSegment(sketch, "E5400", {"start": v(-5.75, -13.13) * mm, "end": v(-5.59, -13) * mm});
            skLineSegment(sketch, "E5401", {"start": v(-5.59, -13) * mm, "end": v(-5.43, -12.87) * mm});
            skLineSegment(sketch, "E5402", {"start": v(-5.43, -12.87) * mm, "end": v(-5.27, -12.73) * mm});
            skLineSegment(sketch, "E5403", {"start": v(-5.27, -12.73) * mm, "end": v(-5.13, -12.6) * mm});
            skLineSegment(sketch, "E5404", {"start": v(-5.13, -12.6) * mm, "end": v(-5.03, -12.47) * mm});
            skLineSegment(sketch, "E5405", {"start": v(-5.03, -12.47) * mm, "end": v(-4.97, -12.37) * mm});
            skLineSegment(sketch, "E5406", {"start": v(-4.97, -12.37) * mm, "end": v(-4.97, -12.28) * mm});
            skLineSegment(sketch, "E5407", {"start": v(-4.97, -12.28) * mm, "end": v(-4.98, -12.1) * mm});
            skLineSegment(sketch, "E5408", {"start": v(-4.98, -12.1) * mm, "end": v(-5, -11.84) * mm});
            skLineSegment(sketch, "E5409", {"start": v(-5, -11.84) * mm, "end": v(-5.03, -11.55) * mm});
            skLineSegment(sketch, "E5410", {"start": v(-5.03, -11.55) * mm, "end": v(-5.06, -11.25) * mm});
            skLineSegment(sketch, "E5411", {"start": v(-5.06, -11.25) * mm, "end": v(-5.1, -10.98) * mm});
            skLineSegment(sketch, "E5412", {"start": v(-5.1, -10.98) * mm, "end": v(-5.12, -10.75) * mm});
            skLineSegment(sketch, "E5413", {"start": v(-5.12, -10.75) * mm, "end": v(-5.14, -10.6) * mm});
            skLineSegment(sketch, "E5414", {"start": v(-5.14, -10.6) * mm, "end": v(-5.33, -10.67) * mm});
            skLineSegment(sketch, "E5415", {"start": v(-5.33, -10.67) * mm, "end": v(-5.56, -10.75) * mm});
            skLineSegment(sketch, "E5416", {"start": v(-5.56, -10.75) * mm, "end": v(-5.83, -10.85) * mm});
            skLineSegment(sketch, "E5417", {"start": v(-5.83, -10.85) * mm, "end": v(-6.12, -10.95) * mm});
            skLineSegment(sketch, "E5418", {"start": v(-6.12, -10.95) * mm, "end": v(-6.45, -11.04) * mm});
            skLineSegment(sketch, "E5419", {"start": v(-6.45, -11.04) * mm, "end": v(-6.8, -11.1) * mm});
            skLineSegment(sketch, "E5420", {"start": v(-6.8, -11.1) * mm, "end": v(-7.17, -11.11) * mm});
            skLineSegment(sketch, "E5421", {"start": v(-7.17, -11.11) * mm, "end": v(-7.57, -11.07) * mm});
            skLineSegment(sketch, "E5422", {"start": v(-7.57, -11.07) * mm, "end": v(-7.85, -11.01) * mm});
            skLineSegment(sketch, "E5423", {"start": v(-7.85, -11.01) * mm, "end": v(-8.03, -10.95) * mm});
            skLineSegment(sketch, "E5424", {"start": v(-8.03, -10.95) * mm, "end": v(-8.14, -10.9) * mm});
            skLineSegment(sketch, "E5425", {"start": v(-8.14, -10.9) * mm, "end": v(-8.21, -10.89) * mm});
            skLineSegment(sketch, "E5426", {"start": v(-8.21, -10.89) * mm, "end": v(-8.3, -10.9) * mm});
            skLineSegment(sketch, "E5427", {"start": v(-8.3, -10.9) * mm, "end": v(-8.44, -10.95) * mm});
            skLineSegment(sketch, "E5428", {"start": v(-8.44, -10.95) * mm, "end": v(-8.66, -11.06) * mm});
            skLineSegment(sketch, "E5429", {"start": v(-8.66, -11.06) * mm, "end": v(-9, -11.22) * mm});
            skLineSegment(sketch, "E5430", {"start": v(-9, -11.22) * mm, "end": v(-9.22, -11.3) * mm});
            skLineSegment(sketch, "E5431", {"start": v(-9.22, -11.3) * mm, "end": v(-9.36, -11.35) * mm});
            skLineSegment(sketch, "E5432", {"start": v(-9.36, -11.35) * mm, "end": v(-9.42, -11.38) * mm});
            skLineSegment(sketch, "E5433", {"start": v(-9.42, -11.38) * mm, "end": v(-9.47, -11.43) * mm});
            skLineSegment(sketch, "E5434", {"start": v(-9.47, -11.43) * mm, "end": v(-9.54, -11.5) * mm});
            skLineSegment(sketch, "E5435", {"start": v(-9.54, -11.5) * mm, "end": v(-9.61, -11.6) * mm});
            skLineSegment(sketch, "E5436", {"start": v(-9.61, -11.6) * mm, "end": v(-9.7, -11.72) * mm});
            skLineSegment(sketch, "E5437", {"start": v(-9.7, -11.72) * mm, "end": v(-9.78, -11.83) * mm});
            skLineSegment(sketch, "E5438", {"start": v(-9.78, -11.83) * mm, "end": v(-9.86, -11.94) * mm});
            skLineSegment(sketch, "E5439", {"start": v(-9.86, -11.94) * mm, "end": v(-9.96, -12.04) * mm});
            skLineSegment(sketch, "E5440", {"start": v(-9.96, -12.04) * mm, "end": v(-10.05, -12.13) * mm});
            skLineSegment(sketch, "E5441", {"start": v(-10.05, -12.13) * mm, "end": v(-10.15, -12.22) * mm});
            skLineSegment(sketch, "E5442", {"start": v(-10.15, -12.22) * mm, "end": v(-10.25, -12.3) * mm});
            skLineSegment(sketch, "E5443", {"start": v(-10.25, -12.3) * mm, "end": v(-10.36, -12.37) * mm});
            skLineSegment(sketch, "E5444", {"start": v(-10.36, -12.37) * mm, "end": v(-10.44, -12.42) * mm});
            skLineSegment(sketch, "E5445", {"start": v(-10.44, -12.42) * mm, "end": v(-10.52, -12.47) * mm});
            skLineSegment(sketch, "E5446", {"start": v(-10.52, -12.47) * mm, "end": v(-10.6, -12.52) * mm});
            skLineSegment(sketch, "E5447", {"start": v(-10.6, -12.52) * mm, "end": v(-10.66, -12.6) * mm});
            skLineSegment(sketch, "E5448", {"start": v(-9.39, -21.9) * mm, "end": v(-9.3, -21.94) * mm});
            skLineSegment(sketch, "E5449", {"start": v(-9.3, -21.94) * mm, "end": v(-9.19, -21.97) * mm});
            skLineSegment(sketch, "E5450", {"start": v(-9.19, -21.97) * mm, "end": v(-9.08, -21.99) * mm});
            skLineSegment(sketch, "E5451", {"start": v(-9.08, -21.99) * mm, "end": v(-8.96, -22) * mm});
            skLineSegment(sketch, "E5452", {"start": v(-8.96, -22) * mm, "end": v(-8.85, -22) * mm});
            skLineSegment(sketch, "E5453", {"start": v(-8.85, -22) * mm, "end": v(-8.73, -22) * mm});
            skLineSegment(sketch, "E5454", {"start": v(-8.73, -22) * mm, "end": v(-8.61, -21.99) * mm});
            skLineSegment(sketch, "E5455", {"start": v(-8.61, -21.99) * mm, "end": v(-8.5, -21.97) * mm});
            skLineSegment(sketch, "E5456", {"start": v(-8.5, -21.97) * mm, "end": v(-8.42, -21.95) * mm});
            skLineSegment(sketch, "E5457", {"start": v(-8.42, -21.95) * mm, "end": v(-8.32, -21.93) * mm});
            skLineSegment(sketch, "E5458", {"start": v(-8.32, -21.93) * mm, "end": v(-8.23, -21.9) * mm});
            skLineSegment(sketch, "E5459", {"start": v(-8.23, -21.9) * mm, "end": v(-8.13, -21.86) * mm});
            skLineSegment(sketch, "E5460", {"start": v(-8.13, -21.86) * mm, "end": v(-8.04, -21.82) * mm});
            skLineSegment(sketch, "E5461", {"start": v(-8.04, -21.82) * mm, "end": v(-7.96, -21.76) * mm});
            skLineSegment(sketch, "E5462", {"start": v(-7.96, -21.76) * mm, "end": v(-7.9, -21.7) * mm});
            skLineSegment(sketch, "E5463", {"start": v(-7.9, -21.7) * mm, "end": v(-7.85, -21.63) * mm});
            skLineSegment(sketch, "E5464", {"start": v(-7.85, -21.63) * mm, "end": v(-7.78, -21.46) * mm});
            skLineSegment(sketch, "E5465", {"start": v(-7.78, -21.46) * mm, "end": v(-7.71, -21.27) * mm});
            skLineSegment(sketch, "E5466", {"start": v(-7.71, -21.27) * mm, "end": v(-7.65, -21.07) * mm});
            skLineSegment(sketch, "E5467", {"start": v(-7.65, -21.07) * mm, "end": v(-7.59, -20.9) * mm});
            skLineSegment(sketch, "E5468", {"start": v(-7.59, -20.9) * mm, "end": v(-7, -19.44) * mm});
            skLineSegment(sketch, "E5469", {"start": v(-7, -19.44) * mm, "end": v(-6.94, -19.31) * mm});
            skLineSegment(sketch, "E5470", {"start": v(-6.94, -19.31) * mm, "end": v(-6.9, -19.22) * mm});
            skLineSegment(sketch, "E5471", {"start": v(-6.9, -19.22) * mm, "end": v(-6.88, -19.14) * mm});
            skLineSegment(sketch, "E5472", {"start": v(-6.88, -19.14) * mm, "end": v(-6.87, -19.07) * mm});
            skLineSegment(sketch, "E5473", {"start": v(-6.87, -19.07) * mm, "end": v(-6.88, -19) * mm});
            skLineSegment(sketch, "E5474", {"start": v(-6.88, -19) * mm, "end": v(-6.9, -18.93) * mm});
            skLineSegment(sketch, "E5475", {"start": v(-6.9, -18.93) * mm, "end": v(-6.94, -18.83) * mm});
            skLineSegment(sketch, "E5476", {"start": v(-6.94, -18.83) * mm, "end": v(-6.99, -18.7) * mm});
            skLineSegment(sketch, "E5477", {"start": v(-6.99, -18.7) * mm, "end": v(-7.05, -18.52) * mm});
            skLineSegment(sketch, "E5478", {"start": v(-7.05, -18.52) * mm, "end": v(-7.12, -18.33) * mm});
            skLineSegment(sketch, "E5479", {"start": v(-7.12, -18.33) * mm, "end": v(-7.18, -18.14) * mm});
            skLineSegment(sketch, "E5480", {"start": v(-7.18, -18.14) * mm, "end": v(-7.22, -17.94) * mm});
            skLineSegment(sketch, "E5481", {"start": v(-7.22, -17.94) * mm, "end": v(-7.26, -17.74) * mm});
            skLineSegment(sketch, "E5482", {"start": v(-7.26, -17.74) * mm, "end": v(-7.3, -17.49) * mm});
            skLineSegment(sketch, "E5483", {"start": v(-7.3, -17.49) * mm, "end": v(-7.32, -17.36) * mm});
            skLineSegment(sketch, "E5484", {"start": v(-7.32, -17.36) * mm, "end": v(-7.34, -17.25) * mm});
            skLineSegment(sketch, "E5485", {"start": v(-7.34, -17.25) * mm, "end": v(-7.37, -17.15) * mm});
            skLineSegment(sketch, "E5486", {"start": v(-7.37, -17.15) * mm, "end": v(-7.4, -17.08) * mm});
            skLineSegment(sketch, "E5487", {"start": v(-7.4, -17.08) * mm, "end": v(-7.7, -17.54) * mm});
            skLineSegment(sketch, "E5488", {"start": v(-7.7, -17.54) * mm, "end": v(-8.01, -18.1) * mm});
            skLineSegment(sketch, "E5489", {"start": v(-8.01, -18.1) * mm, "end": v(-8.3, -18.74) * mm});
            skLineSegment(sketch, "E5490", {"start": v(-8.3, -18.74) * mm, "end": v(-8.58, -19.41) * mm});
            skLineSegment(sketch, "E5491", {"start": v(-8.58, -19.41) * mm, "end": v(-8.84, -20.1) * mm});
            skLineSegment(sketch, "E5492", {"start": v(-8.84, -20.1) * mm, "end": v(-9.06, -20.76) * mm});
            skLineSegment(sketch, "E5493", {"start": v(-9.06, -20.76) * mm, "end": v(-9.25, -21.37) * mm});
            skLineSegment(sketch, "E5494", {"start": v(-9.25, -21.37) * mm, "end": v(-9.39, -21.9) * mm});
            skLineSegment(sketch, "E5495", {"start": v(-2.65, -22.12) * mm, "end": v(-2.93, -21.93) * mm});
            skLineSegment(sketch, "E5496", {"start": v(-2.93, -21.93) * mm, "end": v(-3.14, -21.78) * mm});
            skLineSegment(sketch, "E5497", {"start": v(-3.14, -21.78) * mm, "end": v(-3.23, -21.7) * mm});
            skLineSegment(sketch, "E5498", {"start": v(-3.23, -21.7) * mm, "end": v(-3.32, -21.61) * mm});
            skLineSegment(sketch, "E5499", {"start": v(-3.32, -21.61) * mm, "end": v(-3.42, -21.5) * mm});
            skLineSegment(sketch, "E5500", {"start": v(-3.42, -21.5) * mm, "end": v(-3.52, -21.36) * mm});
            skLineSegment(sketch, "E5501", {"start": v(-3.52, -21.36) * mm, "end": v(-3.6, -21.26) * mm});
            skLineSegment(sketch, "E5502", {"start": v(-3.6, -21.26) * mm, "end": v(-3.7, -21.11) * mm});
            skLineSegment(sketch, "E5503", {"start": v(-3.7, -21.11) * mm, "end": v(-3.8, -20.97) * mm});
            skLineSegment(sketch, "E5504", {"start": v(-3.8, -20.97) * mm, "end": v(-3.87, -20.88) * mm});
            skLineSegment(sketch, "E5505", {"start": v(-3.87, -20.88) * mm, "end": v(-3.93, -20.84) * mm});
            skLineSegment(sketch, "E5506", {"start": v(-3.93, -20.84) * mm, "end": v(-4, -20.81) * mm});
            skLineSegment(sketch, "E5507", {"start": v(-4, -20.81) * mm, "end": v(-4.1, -20.79) * mm});
            skLineSegment(sketch, "E5508", {"start": v(-4.1, -20.79) * mm, "end": v(-4.18, -20.77) * mm});
            skLineSegment(sketch, "E5509", {"start": v(-4.18, -20.77) * mm, "end": v(-4.36, -20.74) * mm});
            skLineSegment(sketch, "E5510", {"start": v(-4.36, -20.74) * mm, "end": v(-4.52, -20.7) * mm});
            skLineSegment(sketch, "E5511", {"start": v(-4.52, -20.7) * mm, "end": v(-4.58, -20.9) * mm});
            skLineSegment(sketch, "E5512", {"start": v(-4.58, -20.9) * mm, "end": v(-4.66, -21.12) * mm});
            skLineSegment(sketch, "E5513", {"start": v(-4.66, -21.12) * mm, "end": v(-4.72, -21.34) * mm});
            skLineSegment(sketch, "E5514", {"start": v(-4.72, -21.34) * mm, "end": v(-4.77, -21.54) * mm});
            skLineSegment(sketch, "E5515", {"start": v(-4.77, -21.54) * mm, "end": v(-4.86, -21.98) * mm});
            skLineSegment(sketch, "E5516", {"start": v(-4.86, -21.98) * mm, "end": v(-4.96, -22.36) * mm});
            skLineSegment(sketch, "E5517", {"start": v(-4.96, -22.36) * mm, "end": v(-5.04, -22.7) * mm});
            skLineSegment(sketch, "E5518", {"start": v(-5.04, -22.7) * mm, "end": v(-5.08, -22.98) * mm});
            skLineSegment(sketch, "E5519", {"start": v(-5.08, -22.98) * mm, "end": v(-5.07, -23.25) * mm});
            skLineSegment(sketch, "E5520", {"start": v(-5.07, -23.25) * mm, "end": v(-5, -23.5) * mm});
            skLineSegment(sketch, "E5521", {"start": v(-5, -23.5) * mm, "end": v(-4.84, -23.75) * mm});
            skLineSegment(sketch, "E5522", {"start": v(-4.84, -23.75) * mm, "end": v(-4.6, -24.02) * mm});
            skLineSegment(sketch, "E5523", {"start": v(-4.6, -24.02) * mm, "end": v(-4.52, -24.1) * mm});
            skLineSegment(sketch, "E5524", {"start": v(-4.52, -24.1) * mm, "end": v(-4.44, -24.16) * mm});
            skLineSegment(sketch, "E5525", {"start": v(-4.44, -24.16) * mm, "end": v(-4.37, -24.21) * mm});
            skLineSegment(sketch, "E5526", {"start": v(-4.37, -24.21) * mm, "end": v(-4.3, -24.26) * mm});
            skLineSegment(sketch, "E5527", {"start": v(-4.3, -24.26) * mm, "end": v(-4.2, -24.3) * mm});
            skLineSegment(sketch, "E5528", {"start": v(-4.2, -24.3) * mm, "end": v(-4.11, -24.3) * mm});
            skLineSegment(sketch, "E5529", {"start": v(-4.11, -24.3) * mm, "end": v(-4, -24.3) * mm});
            skLineSegment(sketch, "E5530", {"start": v(-4, -24.3) * mm, "end": v(-3.87, -24.28) * mm});
            skLineSegment(sketch, "E5531", {"start": v(-3.87, -24.28) * mm, "end": v(-3.76, -24.24) * mm});
            skLineSegment(sketch, "E5532", {"start": v(-3.76, -24.24) * mm, "end": v(-3.65, -24.2) * mm});
            skLineSegment(sketch, "E5533", {"start": v(-3.65, -24.2) * mm, "end": v(-3.55, -24.16) * mm});
            skLineSegment(sketch, "E5534", {"start": v(-3.55, -24.16) * mm, "end": v(-3.45, -24.11) * mm});
            skLineSegment(sketch, "E5535", {"start": v(-3.45, -24.11) * mm, "end": v(-3.36, -24.06) * mm});
            skLineSegment(sketch, "E5536", {"start": v(-3.36, -24.06) * mm, "end": v(-3.28, -24) * mm});
            skLineSegment(sketch, "E5537", {"start": v(-3.28, -24) * mm, "end": v(-3.2, -23.95) * mm});
            skLineSegment(sketch, "E5538", {"start": v(-3.2, -23.95) * mm, "end": v(-3.13, -23.88) * mm});
            skLineSegment(sketch, "E5539", {"start": v(-3.13, -23.88) * mm, "end": v(-3.05, -23.76) * mm});
            skLineSegment(sketch, "E5540", {"start": v(-3.05, -23.76) * mm, "end": v(-2.97, -23.56) * mm});
            skLineSegment(sketch, "E5541", {"start": v(-2.97, -23.56) * mm, "end": v(-2.9, -23.32) * mm});
            skLineSegment(sketch, "E5542", {"start": v(-2.9, -23.32) * mm, "end": v(-2.83, -23.06) * mm});
            skLineSegment(sketch, "E5543", {"start": v(-2.83, -23.06) * mm, "end": v(-2.77, -22.78) * mm});
            skLineSegment(sketch, "E5544", {"start": v(-2.77, -22.78) * mm, "end": v(-2.72, -22.52) * mm});
            skLineSegment(sketch, "E5545", {"start": v(-2.72, -22.52) * mm, "end": v(-2.68, -22.3) * mm});
            skLineSegment(sketch, "E5546", {"start": v(-2.68, -22.3) * mm, "end": v(-2.65, -22.12) * mm});
            skLineSegment(sketch, "E5547", {"start": v(3, -22.12) * mm, "end": v(3.04, -22.34) * mm});
            skLineSegment(sketch, "E5548", {"start": v(3.04, -22.34) * mm, "end": v(3.1, -22.56) * mm});
            skLineSegment(sketch, "E5549", {"start": v(3.1, -22.56) * mm, "end": v(3.15, -22.8) * mm});
            skLineSegment(sketch, "E5550", {"start": v(3.15, -22.8) * mm, "end": v(3.2, -23.03) * mm});
            skLineSegment(sketch, "E5551", {"start": v(3.2, -23.03) * mm, "end": v(3.23, -23.23) * mm});
            skLineSegment(sketch, "E5552", {"start": v(3.23, -23.23) * mm, "end": v(3.27, -23.42) * mm});
            skLineSegment(sketch, "E5553", {"start": v(3.27, -23.42) * mm, "end": v(3.32, -23.6) * mm});
            skLineSegment(sketch, "E5554", {"start": v(3.32, -23.6) * mm, "end": v(3.4, -23.75) * mm});
            skLineSegment(sketch, "E5555", {"start": v(3.4, -23.75) * mm, "end": v(3.5, -23.9) * mm});
            skLineSegment(sketch, "E5556", {"start": v(3.5, -23.9) * mm, "end": v(3.66, -24.03) * mm});
            skLineSegment(sketch, "E5557", {"start": v(3.66, -24.03) * mm, "end": v(3.86, -24.15) * mm});
            skLineSegment(sketch, "E5558", {"start": v(3.86, -24.15) * mm, "end": v(4.14, -24.25) * mm});
            skLineSegment(sketch, "E5559", {"start": v(4.14, -24.25) * mm, "end": v(4.3, -24.3) * mm});
            skLineSegment(sketch, "E5560", {"start": v(4.3, -24.3) * mm, "end": v(4.41, -24.31) * mm});
            skLineSegment(sketch, "E5561", {"start": v(4.41, -24.31) * mm, "end": v(4.51, -24.3) * mm});
            skLineSegment(sketch, "E5562", {"start": v(4.51, -24.3) * mm, "end": v(4.6, -24.29) * mm});
            skLineSegment(sketch, "E5563", {"start": v(4.6, -24.29) * mm, "end": v(4.66, -24.25) * mm});
            skLineSegment(sketch, "E5564", {"start": v(4.66, -24.25) * mm, "end": v(4.74, -24.2) * mm});
            skLineSegment(sketch, "E5565", {"start": v(4.74, -24.2) * mm, "end": v(4.82, -24.13) * mm});
            skLineSegment(sketch, "E5566", {"start": v(4.82, -24.13) * mm, "end": v(4.91, -24.05) * mm});
            skLineSegment(sketch, "E5567", {"start": v(4.91, -24.05) * mm, "end": v(5.13, -23.85) * mm});
            skLineSegment(sketch, "E5568", {"start": v(5.13, -23.85) * mm, "end": v(5.28, -23.65) * mm});
            skLineSegment(sketch, "E5569", {"start": v(5.28, -23.65) * mm, "end": v(5.37, -23.46) * mm});
            skLineSegment(sketch, "E5570", {"start": v(5.37, -23.46) * mm, "end": v(5.41, -23.27) * mm});
            skLineSegment(sketch, "E5571", {"start": v(5.41, -23.27) * mm, "end": v(5.42, -23.08) * mm});
            skLineSegment(sketch, "E5572", {"start": v(5.42, -23.08) * mm, "end": v(5.4, -22.89) * mm});
            skLineSegment(sketch, "E5573", {"start": v(5.4, -22.89) * mm, "end": v(5.37, -22.7) * mm});
            skLineSegment(sketch, "E5574", {"start": v(5.37, -22.7) * mm, "end": v(5.33, -22.5) * mm});
            skLineSegment(sketch, "E5575", {"start": v(5.33, -22.5) * mm, "end": v(5.3, -22.29) * mm});
            skLineSegment(sketch, "E5576", {"start": v(5.3, -22.29) * mm, "end": v(5.24, -22.06) * mm});
            skLineSegment(sketch, "E5577", {"start": v(5.24, -22.06) * mm, "end": v(5.19, -21.84) * mm});
            skLineSegment(sketch, "E5578", {"start": v(5.19, -21.84) * mm, "end": v(5.13, -21.62) * mm});
            skLineSegment(sketch, "E5579", {"start": v(5.13, -21.62) * mm, "end": v(5.07, -21.4) * mm});
            skLineSegment(sketch, "E5580", {"start": v(5.07, -21.4) * mm, "end": v(5, -21.18) * mm});
            skLineSegment(sketch, "E5581", {"start": v(5, -21.18) * mm, "end": v(4.95, -20.96) * mm});
            skLineSegment(sketch, "E5582", {"start": v(4.95, -20.96) * mm, "end": v(4.89, -20.74) * mm});
            skLineSegment(sketch, "E5583", {"start": v(4.89, -20.74) * mm, "end": v(4.72, -20.76) * mm});
            skLineSegment(sketch, "E5584", {"start": v(4.72, -20.76) * mm, "end": v(4.54, -20.78) * mm});
            skLineSegment(sketch, "E5585", {"start": v(4.54, -20.78) * mm, "end": v(4.46, -20.8) * mm});
            skLineSegment(sketch, "E5586", {"start": v(4.46, -20.8) * mm, "end": v(4.38, -20.83) * mm});
            skLineSegment(sketch, "E5587", {"start": v(4.38, -20.83) * mm, "end": v(4.32, -20.86) * mm});
            skLineSegment(sketch, "E5588", {"start": v(4.32, -20.86) * mm, "end": v(4.27, -20.9) * mm});
            skLineSegment(sketch, "E5589", {"start": v(4.27, -20.9) * mm, "end": v(4.06, -21.18) * mm});
            skLineSegment(sketch, "E5590", {"start": v(4.06, -21.18) * mm, "end": v(3.84, -21.5) * mm});
            skLineSegment(sketch, "E5591", {"start": v(3.84, -21.5) * mm, "end": v(3.7, -21.67) * mm});
            skLineSegment(sketch, "E5592", {"start": v(3.7, -21.67) * mm, "end": v(3.51, -21.83) * mm});
            skLineSegment(sketch, "E5593", {"start": v(3.51, -21.83) * mm, "end": v(3.29, -21.98) * mm});
            skLineSegment(sketch, "E5594", {"start": v(3.29, -21.98) * mm, "end": v(3, -22.12) * mm});
            skLineSegment(sketch, "E5595", {"start": v(7.8, -17.17) * mm, "end": v(7.75, -17.39) * mm});
            skLineSegment(sketch, "E5596", {"start": v(7.75, -17.39) * mm, "end": v(7.66, -17.77) * mm});
            skLineSegment(sketch, "E5597", {"start": v(7.66, -17.77) * mm, "end": v(7.62, -17.99) * mm});
            skLineSegment(sketch, "E5598", {"start": v(7.62, -17.99) * mm, "end": v(7.56, -18.21) * mm});
            skLineSegment(sketch, "E5599", {"start": v(7.56, -18.21) * mm, "end": v(7.5, -18.42) * mm});
            skLineSegment(sketch, "E5600", {"start": v(7.5, -18.42) * mm, "end": v(7.44, -18.62) * mm});
            skLineSegment(sketch, "E5601", {"start": v(7.44, -18.62) * mm, "end": v(7.37, -18.78) * mm});
            skLineSegment(sketch, "E5602", {"start": v(7.37, -18.78) * mm, "end": v(7.3, -18.95) * mm});
            skLineSegment(sketch, "E5603", {"start": v(7.3, -18.95) * mm, "end": v(7.28, -19.04) * mm});
            skLineSegment(sketch, "E5604", {"start": v(7.28, -19.04) * mm, "end": v(7.26, -19.12) * mm});
            skLineSegment(sketch, "E5605", {"start": v(7.26, -19.12) * mm, "end": v(7.26, -19.2) * mm});
            skLineSegment(sketch, "E5606", {"start": v(7.26, -19.2) * mm, "end": v(7.28, -19.28) * mm});
            skLineSegment(sketch, "E5607", {"start": v(7.28, -19.28) * mm, "end": v(7.34, -19.44) * mm});
            skLineSegment(sketch, "E5608", {"start": v(7.34, -19.44) * mm, "end": v(7.41, -19.6) * mm});
            skLineSegment(sketch, "E5609", {"start": v(7.41, -19.6) * mm, "end": v(7.49, -19.75) * mm});
            skLineSegment(sketch, "E5610", {"start": v(7.49, -19.75) * mm, "end": v(7.56, -19.91) * mm});
            skLineSegment(sketch, "E5611", {"start": v(7.56, -19.91) * mm, "end": v(8.18, -21.59) * mm});
            skLineSegment(sketch, "E5612", {"start": v(8.18, -21.59) * mm, "end": v(8.22, -21.68) * mm});
            skLineSegment(sketch, "E5613", {"start": v(8.22, -21.68) * mm, "end": v(8.25, -21.74) * mm});
            skLineSegment(sketch, "E5614", {"start": v(8.25, -21.74) * mm, "end": v(8.3, -21.78) * mm});
            skLineSegment(sketch, "E5615", {"start": v(8.3, -21.78) * mm, "end": v(8.4, -21.82) * mm});
            skLineSegment(sketch, "E5616", {"start": v(8.4, -21.82) * mm, "end": v(8.53, -21.88) * mm});
            skLineSegment(sketch, "E5617", {"start": v(8.53, -21.88) * mm, "end": v(8.67, -21.92) * mm});
            skLineSegment(sketch, "E5618", {"start": v(8.67, -21.92) * mm, "end": v(8.82, -21.95) * mm});
            skLineSegment(sketch, "E5619", {"start": v(8.82, -21.95) * mm, "end": v(8.98, -21.98) * mm});
            skLineSegment(sketch, "E5620", {"start": v(8.98, -21.98) * mm, "end": v(9.13, -22) * mm});
            skLineSegment(sketch, "E5621", {"start": v(9.13, -22) * mm, "end": v(9.29, -22) * mm});
            skLineSegment(sketch, "E5622", {"start": v(9.29, -22) * mm, "end": v(9.44, -22) * mm});
            skLineSegment(sketch, "E5623", {"start": v(9.44, -22) * mm, "end": v(9.58, -21.97) * mm});
            skLineSegment(sketch, "E5624", {"start": v(9.58, -21.97) * mm, "end": v(9.67, -21.94) * mm});
            skLineSegment(sketch, "E5625", {"start": v(9.67, -21.94) * mm, "end": v(9.72, -21.91) * mm});
            skLineSegment(sketch, "E5626", {"start": v(9.72, -21.91) * mm, "end": v(9.74, -21.86) * mm});
            skLineSegment(sketch, "E5627", {"start": v(9.74, -21.86) * mm, "end": v(9.72, -21.78) * mm});
            skLineSegment(sketch, "E5628", {"start": v(9.72, -21.78) * mm, "end": v(9.68, -21.66) * mm});
            skLineSegment(sketch, "E5629", {"start": v(9.68, -21.66) * mm, "end": v(9.63, -21.5) * mm});
            skLineSegment(sketch, "E5630", {"start": v(9.63, -21.5) * mm, "end": v(9.56, -21.28) * mm});
            skLineSegment(sketch, "E5631", {"start": v(9.56, -21.28) * mm, "end": v(9.48, -21) * mm});
            skLineSegment(sketch, "E5632", {"start": v(9.48, -21) * mm, "end": v(9.36, -20.53) * mm});
            skLineSegment(sketch, "E5633", {"start": v(9.36, -20.53) * mm, "end": v(9.19, -20.03) * mm});
            skLineSegment(sketch, "E5634", {"start": v(9.19, -20.03) * mm, "end": v(8.99, -19.52) * mm});
            skLineSegment(sketch, "E5635", {"start": v(8.99, -19.52) * mm, "end": v(8.76, -19) * mm});
            skLineSegment(sketch, "E5636", {"start": v(8.76, -19) * mm, "end": v(8.53, -18.49) * mm});
            skLineSegment(sketch, "E5637", {"start": v(8.53, -18.49) * mm, "end": v(8.28, -18) * mm});
            skLineSegment(sketch, "E5638", {"start": v(8.28, -18) * mm, "end": v(8.04, -17.56) * mm});
            skLineSegment(sketch, "E5639", {"start": v(8.04, -17.56) * mm, "end": v(7.8, -17.17) * mm});
            skLineSegment(sketch, "E5640", {"start": v(-15.98, -4.52) * mm, "end": v(-15.93, -4.73) * mm});
            skLineSegment(sketch, "E5641", {"start": v(-15.93, -4.73) * mm, "end": v(-15.84, -4.93) * mm});
            skLineSegment(sketch, "E5642", {"start": v(-15.84, -4.93) * mm, "end": v(-15.72, -5.12) * mm});
            skLineSegment(sketch, "E5643", {"start": v(-15.72, -5.12) * mm, "end": v(-15.58, -5.3) * mm});
            skLineSegment(sketch, "E5644", {"start": v(-15.58, -5.3) * mm, "end": v(-15.43, -5.47) * mm});
            skLineSegment(sketch, "E5645", {"start": v(-15.43, -5.47) * mm, "end": v(-15.26, -5.62) * mm});
            skLineSegment(sketch, "E5646", {"start": v(-15.26, -5.62) * mm, "end": v(-15.1, -5.76) * mm});
            skLineSegment(sketch, "E5647", {"start": v(-15.1, -5.76) * mm, "end": v(-14.93, -5.89) * mm});
            skLineSegment(sketch, "E5648", {"start": v(-14.93, -5.89) * mm, "end": v(-14.64, -6.02) * mm});
            skLineSegment(sketch, "E5649", {"start": v(-14.64, -6.02) * mm, "end": v(-14.25, -6.08) * mm});
            skLineSegment(sketch, "E5650", {"start": v(-14.25, -6.08) * mm, "end": v(-13.8, -6.07) * mm});
            skLineSegment(sketch, "E5651", {"start": v(-13.8, -6.07) * mm, "end": v(-13.3, -6) * mm});
            skLineSegment(sketch, "E5652", {"start": v(-13.3, -6) * mm, "end": v(-12.82, -5.9) * mm});
            skLineSegment(sketch, "E5653", {"start": v(-12.82, -5.9) * mm, "end": v(-12.38, -5.75) * mm});
            skLineSegment(sketch, "E5654", {"start": v(-12.38, -5.75) * mm, "end": v(-12, -5.56) * mm});
            skLineSegment(sketch, "E5655", {"start": v(-12, -5.56) * mm, "end": v(-11.74, -5.36) * mm});
            skLineSegment(sketch, "E5656", {"start": v(-11.74, -5.36) * mm, "end": v(-11.82, -5.03) * mm});
            skLineSegment(sketch, "E5657", {"start": v(-11.82, -5.03) * mm, "end": v(-11.86, -4.76) * mm});
            skLineSegment(sketch, "E5658", {"start": v(-11.86, -4.76) * mm, "end": v(-11.87, -4.55) * mm});
            skLineSegment(sketch, "E5659", {"start": v(-11.87, -4.55) * mm, "end": v(-11.86, -4.37) * mm});
            skLineSegment(sketch, "E5660", {"start": v(-11.86, -4.37) * mm, "end": v(-11.85, -4.23) * mm});
            skLineSegment(sketch, "E5661", {"start": v(-11.85, -4.23) * mm, "end": v(-11.84, -4.1) * mm});
            skLineSegment(sketch, "E5662", {"start": v(-11.84, -4.1) * mm, "end": v(-11.85, -4) * mm});
            skLineSegment(sketch, "E5663", {"start": v(-11.85, -4) * mm, "end": v(-11.88, -3.89) * mm});
            skLineSegment(sketch, "E5664", {"start": v(-11.88, -3.89) * mm, "end": v(-11.94, -3.89) * mm});
            skLineSegment(sketch, "E5665", {"start": v(-11.94, -3.89) * mm, "end": v(-12.03, -3.93) * mm});
            skLineSegment(sketch, "E5666", {"start": v(-12.03, -3.93) * mm, "end": v(-12.2, -4.03) * mm});
            skLineSegment(sketch, "E5667", {"start": v(-12.2, -4.03) * mm, "end": v(-12.3, -4.08) * mm});
            skLineSegment(sketch, "E5668", {"start": v(-12.3, -4.08) * mm, "end": v(-12.41, -4.14) * mm});
            skLineSegment(sketch, "E5669", {"start": v(-12.41, -4.14) * mm, "end": v(-12.54, -4.2) * mm});
            skLineSegment(sketch, "E5670", {"start": v(-12.54, -4.2) * mm, "end": v(-12.67, -4.26) * mm});
            skLineSegment(sketch, "E5671", {"start": v(-12.67, -4.26) * mm, "end": v(-13.1, -4.4) * mm});
            skLineSegment(sketch, "E5672", {"start": v(-13.1, -4.4) * mm, "end": v(-13.52, -4.5) * mm});
            skLineSegment(sketch, "E5673", {"start": v(-13.52, -4.5) * mm, "end": v(-13.92, -4.56) * mm});
            skLineSegment(sketch, "E5674", {"start": v(-13.92, -4.56) * mm, "end": v(-14.31, -4.6) * mm});
            skLineSegment(sketch, "E5675", {"start": v(-14.31, -4.6) * mm, "end": v(-14.7, -4.6) * mm});
            skLineSegment(sketch, "E5676", {"start": v(-14.7, -4.6) * mm, "end": v(-15.11, -4.6) * mm});
            skLineSegment(sketch, "E5677", {"start": v(-15.11, -4.6) * mm, "end": v(-15.53, -4.56) * mm});
            skLineSegment(sketch, "E5678", {"start": v(-15.53, -4.56) * mm, "end": v(-15.98, -4.52) * mm});
            skLineSegment(sketch, "E5679", {"start": v(11.9, -4.53) * mm, "end": v(11.89, -4.65) * mm});
            skLineSegment(sketch, "E5680", {"start": v(11.89, -4.65) * mm, "end": v(11.88, -4.76) * mm});
            skLineSegment(sketch, "E5681", {"start": v(11.88, -4.76) * mm, "end": v(11.86, -4.87) * mm});
            skLineSegment(sketch, "E5682", {"start": v(11.86, -4.87) * mm, "end": v(11.84, -4.97) * mm});
            skLineSegment(sketch, "E5683", {"start": v(11.84, -4.97) * mm, "end": v(11.79, -5.16) * mm});
            skLineSegment(sketch, "E5684", {"start": v(11.79, -5.16) * mm, "end": v(11.74, -5.36) * mm});
            skLineSegment(sketch, "E5685", {"start": v(11.74, -5.36) * mm, "end": v(11.92, -5.52) * mm});
            skLineSegment(sketch, "E5686", {"start": v(11.92, -5.52) * mm, "end": v(12.19, -5.67) * mm});
            skLineSegment(sketch, "E5687", {"start": v(12.19, -5.67) * mm, "end": v(12.5, -5.8) * mm});
            skLineSegment(sketch, "E5688", {"start": v(12.5, -5.8) * mm, "end": v(12.86, -5.9) * mm});
            skLineSegment(sketch, "E5689", {"start": v(12.86, -5.9) * mm, "end": v(13.24, -6) * mm});
            skLineSegment(sketch, "E5690", {"start": v(13.24, -6) * mm, "end": v(13.62, -6.05) * mm});
            skLineSegment(sketch, "E5691", {"start": v(13.62, -6.05) * mm, "end": v(13.97, -6.08) * mm});
            skLineSegment(sketch, "E5692", {"start": v(13.97, -6.08) * mm, "end": v(14.28, -6.07) * mm});
            skLineSegment(sketch, "E5693", {"start": v(14.28, -6.07) * mm, "end": v(14.48, -6.04) * mm});
            skLineSegment(sketch, "E5694", {"start": v(14.48, -6.04) * mm, "end": v(14.65, -6) * mm});
            skLineSegment(sketch, "E5695", {"start": v(14.65, -6) * mm, "end": v(14.79, -5.95) * mm});
            skLineSegment(sketch, "E5696", {"start": v(14.79, -5.95) * mm, "end": v(14.92, -5.89) * mm});
            skLineSegment(sketch, "E5697", {"start": v(14.92, -5.89) * mm, "end": v(15.03, -5.81) * mm});
            skLineSegment(sketch, "E5698", {"start": v(15.03, -5.81) * mm, "end": v(15.14, -5.73) * mm});
            skLineSegment(sketch, "E5699", {"start": v(15.14, -5.73) * mm, "end": v(15.24, -5.63) * mm});
            skLineSegment(sketch, "E5700", {"start": v(15.24, -5.63) * mm, "end": v(15.35, -5.52) * mm});
            skLineSegment(sketch, "E5701", {"start": v(15.35, -5.52) * mm, "end": v(15.45, -5.43) * mm});
            skLineSegment(sketch, "E5702", {"start": v(15.45, -5.43) * mm, "end": v(15.55, -5.33) * mm});
            skLineSegment(sketch, "E5703", {"start": v(15.55, -5.33) * mm, "end": v(15.64, -5.22) * mm});
            skLineSegment(sketch, "E5704", {"start": v(15.64, -5.22) * mm, "end": v(15.73, -5.1) * mm});
            skLineSegment(sketch, "E5705", {"start": v(15.73, -5.1) * mm, "end": v(15.81, -4.98) * mm});
            skLineSegment(sketch, "E5706", {"start": v(15.81, -4.98) * mm, "end": v(15.88, -4.84) * mm});
            skLineSegment(sketch, "E5707", {"start": v(15.88, -4.84) * mm, "end": v(15.94, -4.69) * mm});
            skLineSegment(sketch, "E5708", {"start": v(15.94, -4.69) * mm, "end": v(15.98, -4.52) * mm});
            skLineSegment(sketch, "E5709", {"start": v(15.98, -4.52) * mm, "end": v(15.6, -4.56) * mm});
            skLineSegment(sketch, "E5710", {"start": v(15.6, -4.56) * mm, "end": v(15.3, -4.59) * mm});
            skLineSegment(sketch, "E5711", {"start": v(15.3, -4.59) * mm, "end": v(15.09, -4.61) * mm});
            skLineSegment(sketch, "E5712", {"start": v(15.09, -4.61) * mm, "end": v(14.9, -4.63) * mm});
            skLineSegment(sketch, "E5713", {"start": v(14.9, -4.63) * mm, "end": v(14.7, -4.63) * mm});
            skLineSegment(sketch, "E5714", {"start": v(14.7, -4.63) * mm, "end": v(14.45, -4.61) * mm});
            skLineSegment(sketch, "E5715", {"start": v(14.45, -4.61) * mm, "end": v(14.13, -4.58) * mm});
            skLineSegment(sketch, "E5716", {"start": v(14.13, -4.58) * mm, "end": v(13.7, -4.53) * mm});
            skLineSegment(sketch, "E5717", {"start": v(13.7, -4.53) * mm, "end": v(13.42, -4.48) * mm});
            skLineSegment(sketch, "E5718", {"start": v(13.42, -4.48) * mm, "end": v(13.16, -4.42) * mm});
            skLineSegment(sketch, "E5719", {"start": v(13.16, -4.42) * mm, "end": v(12.93, -4.35) * mm});
            skLineSegment(sketch, "E5720", {"start": v(12.93, -4.35) * mm, "end": v(12.71, -4.27) * mm});
            skLineSegment(sketch, "E5721", {"start": v(12.71, -4.27) * mm, "end": v(12.5, -4.17) * mm});
            skLineSegment(sketch, "E5722", {"start": v(12.5, -4.17) * mm, "end": v(12.3, -4.07) * mm});
            skLineSegment(sketch, "E5723", {"start": v(12.3, -4.07) * mm, "end": v(12.1, -3.96) * mm});
            skLineSegment(sketch, "E5724", {"start": v(12.1, -3.96) * mm, "end": v(11.9, -3.85) * mm});
            skLineSegment(sketch, "E5725", {"start": v(11.9, -3.85) * mm, "end": v(11.86, -3.94) * mm});
            skLineSegment(sketch, "E5726", {"start": v(11.86, -3.94) * mm, "end": v(11.85, -4.01) * mm});
            skLineSegment(sketch, "E5727", {"start": v(11.85, -4.01) * mm, "end": v(11.84, -4.08) * mm});
            skLineSegment(sketch, "E5728", {"start": v(11.84, -4.08) * mm, "end": v(11.85, -4.16) * mm});
            skLineSegment(sketch, "E5729", {"start": v(11.85, -4.16) * mm, "end": v(11.87, -4.32) * mm});
            skLineSegment(sketch, "E5730", {"start": v(11.87, -4.32) * mm, "end": v(11.9, -4.53) * mm});
            skLineSegment(sketch, "E5731", {"start": v(-10.3, -1.27) * mm, "end": v(-10.37, -1.14) * mm});
            skLineSegment(sketch, "E5732", {"start": v(-10.37, -1.14) * mm, "end": v(-10.44, -1.02) * mm});
            skLineSegment(sketch, "E5733", {"start": v(-10.44, -1.02) * mm, "end": v(-10.5, -0.9) * mm});
            skLineSegment(sketch, "E5734", {"start": v(-10.5, -0.9) * mm, "end": v(-10.57, -0.74) * mm});
            skLineSegment(sketch, "E5735", {"start": v(-10.57, -0.74) * mm, "end": v(-10.62, -0.6) * mm});
            skLineSegment(sketch, "E5736", {"start": v(-10.62, -0.6) * mm, "end": v(-10.65, -0.42) * mm});
            skLineSegment(sketch, "E5737", {"start": v(-10.65, -0.42) * mm, "end": v(-10.67, -0.33) * mm});
            skLineSegment(sketch, "E5738", {"start": v(-10.67, -0.33) * mm, "end": v(-10.7, -0.25) * mm});
            skLineSegment(sketch, "E5739", {"start": v(-10.7, -0.25) * mm, "end": v(-10.72, -0.18) * mm});
            skLineSegment(sketch, "E5740", {"start": v(-10.72, -0.18) * mm, "end": v(-10.75, -0.13) * mm});
            skLineSegment(sketch, "E5741", {"start": v(-10.75, -0.13) * mm, "end": v(-12.96, 0.58) * mm});
            skLineSegment(sketch, "E5742", {"start": v(-12.96, 0.58) * mm, "end": v(-13.24, 0.68) * mm});
            skLineSegment(sketch, "E5743", {"start": v(-13.24, 0.68) * mm, "end": v(-13.5, 0.78) * mm});
            skLineSegment(sketch, "E5744", {"start": v(-13.5, 0.78) * mm, "end": v(-13.77, 0.88) * mm});
            skLineSegment(sketch, "E5745", {"start": v(-13.77, 0.88) * mm, "end": v(-14.03, 1) * mm});
            skLineSegment(sketch, "E5746", {"start": v(-14.03, 1) * mm, "end": v(-14.29, 1.1) * mm});
            skLineSegment(sketch, "E5747", {"start": v(-14.29, 1.1) * mm, "end": v(-14.54, 1.21) * mm});
            skLineSegment(sketch, "E5748", {"start": v(-14.54, 1.21) * mm, "end": v(-14.8, 1.32) * mm});
            skLineSegment(sketch, "E5749", {"start": v(-14.8, 1.32) * mm, "end": v(-15.06, 1.42) * mm});
            skLineSegment(sketch, "E5750", {"start": v(-15.06, 1.42) * mm, "end": v(-14.98, 1.13) * mm});
            skLineSegment(sketch, "E5751", {"start": v(-14.98, 1.13) * mm, "end": v(-14.87, 0.86) * mm});
            skLineSegment(sketch, "E5752", {"start": v(-14.87, 0.86) * mm, "end": v(-14.7, 0.61) * mm});
            skLineSegment(sketch, "E5753", {"start": v(-14.7, 0.61) * mm, "end": v(-14.52, 0.39) * mm});
            skLineSegment(sketch, "E5754", {"start": v(-14.52, 0.39) * mm, "end": v(-14.32, 0.18) * mm});
            skLineSegment(sketch, "E5755", {"start": v(-14.32, 0.18) * mm, "end": v(-14.1, 0) * mm});
            skLineSegment(sketch, "E5756", {"start": v(-14.1, 0) * mm, "end": v(-13.86, -0.18) * mm});
            skLineSegment(sketch, "E5757", {"start": v(-13.86, -0.18) * mm, "end": v(-13.63, -0.34) * mm});
            skLineSegment(sketch, "E5758", {"start": v(-13.63, -0.34) * mm, "end": v(-13.33, -0.5) * mm});
            skLineSegment(sketch, "E5759", {"start": v(-13.33, -0.5) * mm, "end": v(-12.95, -0.66) * mm});
            skLineSegment(sketch, "E5760", {"start": v(-12.95, -0.66) * mm, "end": v(-12.53, -0.81) * mm});
            skLineSegment(sketch, "E5761", {"start": v(-12.53, -0.81) * mm, "end": v(-12.07, -0.95) * mm});
            skLineSegment(sketch, "E5762", {"start": v(-12.07, -0.95) * mm, "end": v(-11.6, -1.06) * mm});
            skLineSegment(sketch, "E5763", {"start": v(-11.6, -1.06) * mm, "end": v(-11.13, -1.16) * mm});
            skLineSegment(sketch, "E5764", {"start": v(-11.13, -1.16) * mm, "end": v(-10.7, -1.23) * mm});
            skLineSegment(sketch, "E5765", {"start": v(-10.7, -1.23) * mm, "end": v(-10.3, -1.27) * mm});
            skLineSegment(sketch, "E5766", {"start": v(10.7, -0.12) * mm, "end": v(10.67, -0.36) * mm});
            skLineSegment(sketch, "E5767", {"start": v(10.67, -0.36) * mm, "end": v(10.64, -0.55) * mm});
            skLineSegment(sketch, "E5768", {"start": v(10.64, -0.55) * mm, "end": v(10.6, -0.7) * mm});
            skLineSegment(sketch, "E5769", {"start": v(10.6, -0.7) * mm, "end": v(10.54, -0.82) * mm});
            skLineSegment(sketch, "E5770", {"start": v(10.54, -0.82) * mm, "end": v(10.43, -1.03) * mm});
            skLineSegment(sketch, "E5771", {"start": v(10.43, -1.03) * mm, "end": v(10.3, -1.27) * mm});
            skLineSegment(sketch, "E5772", {"start": v(10.3, -1.27) * mm, "end": v(10.65, -1.24) * mm});
            skLineSegment(sketch, "E5773", {"start": v(10.65, -1.24) * mm, "end": v(11.03, -1.18) * mm});
            skLineSegment(sketch, "E5774", {"start": v(11.03, -1.18) * mm, "end": v(11.43, -1.1) * mm});
            skLineSegment(sketch, "E5775", {"start": v(11.43, -1.1) * mm, "end": v(11.83, -1.01) * mm});
            skLineSegment(sketch, "E5776", {"start": v(11.83, -1.01) * mm, "end": v(12.22, -0.9) * mm});
            skLineSegment(sketch, "E5777", {"start": v(12.22, -0.9) * mm, "end": v(12.6, -0.78) * mm});
            skLineSegment(sketch, "E5778", {"start": v(12.6, -0.78) * mm, "end": v(12.96, -0.65) * mm});
            skLineSegment(sketch, "E5779", {"start": v(12.96, -0.65) * mm, "end": v(13.27, -0.52) * mm});
            skLineSegment(sketch, "E5780", {"start": v(13.27, -0.52) * mm, "end": v(13.57, -0.37) * mm});
            skLineSegment(sketch, "E5781", {"start": v(13.57, -0.37) * mm, "end": v(13.86, -0.2) * mm});
            skLineSegment(sketch, "E5782", {"start": v(13.86, -0.2) * mm, "end": v(14.14, 0) * mm});
            skLineSegment(sketch, "E5783", {"start": v(14.14, 0) * mm, "end": v(14.39, 0.24) * mm});
            skLineSegment(sketch, "E5784", {"start": v(14.39, 0.24) * mm, "end": v(14.6, 0.5) * mm});
            skLineSegment(sketch, "E5785", {"start": v(14.6, 0.5) * mm, "end": v(14.8, 0.78) * mm});
            skLineSegment(sketch, "E5786", {"start": v(14.8, 0.78) * mm, "end": v(14.95, 1.08) * mm});
            skLineSegment(sketch, "E5787", {"start": v(14.95, 1.08) * mm, "end": v(15.05, 1.42) * mm});
            skLineSegment(sketch, "E5788", {"start": v(15.05, 1.42) * mm, "end": v(14.08, 1) * mm});
            skLineSegment(sketch, "E5789", {"start": v(14.08, 1) * mm, "end": v(13.9, 0.92) * mm});
            skLineSegment(sketch, "E5790", {"start": v(13.9, 0.92) * mm, "end": v(13.64, 0.82) * mm});
            skLineSegment(sketch, "E5791", {"start": v(13.64, 0.82) * mm, "end": v(13.34, 0.71) * mm});
            skLineSegment(sketch, "E5792", {"start": v(13.34, 0.71) * mm, "end": v(13, 0.6) * mm});
            skLineSegment(sketch, "E5793", {"start": v(13, 0.6) * mm, "end": v(12.67, 0.48) * mm});
            skLineSegment(sketch, "E5794", {"start": v(12.67, 0.48) * mm, "end": v(12.36, 0.38) * mm});
            skLineSegment(sketch, "E5795", {"start": v(12.36, 0.38) * mm, "end": v(12.08, 0.29) * mm});
            skLineSegment(sketch, "E5796", {"start": v(12.08, 0.29) * mm, "end": v(11.87, 0.22) * mm});
            skLineSegment(sketch, "E5797", {"start": v(11.87, 0.22) * mm, "end": v(11.58, 0.14) * mm});
            skLineSegment(sketch, "E5798", {"start": v(11.58, 0.14) * mm, "end": v(11.26, 0.05) * mm});
            skLineSegment(sketch, "E5799", {"start": v(11.26, 0.05) * mm, "end": v(10.96, -0.03) * mm});
            skLineSegment(sketch, "E5800", {"start": v(10.96, -0.03) * mm, "end": v(10.7, -0.12) * mm});
            skLineSegment(sketch, "E5801", {"start": v(4.59, -18.34) * mm, "end": v(4.67, -18.3) * mm});
            skLineSegment(sketch, "E5802", {"start": v(4.67, -18.3) * mm, "end": v(4.73, -18.24) * mm});
            skLineSegment(sketch, "E5803", {"start": v(4.73, -18.24) * mm, "end": v(4.79, -18.19) * mm});
            skLineSegment(sketch, "E5804", {"start": v(4.79, -18.19) * mm, "end": v(4.84, -18.13) * mm});
            skLineSegment(sketch, "E5805", {"start": v(4.84, -18.13) * mm, "end": v(4.9, -18.09) * mm});
            skLineSegment(sketch, "E5806", {"start": v(4.9, -18.09) * mm, "end": v(4.98, -18.04) * mm});
            skLineSegment(sketch, "E5807", {"start": v(4.98, -18.04) * mm, "end": v(5.07, -18.02) * mm});
            skLineSegment(sketch, "E5808", {"start": v(5.07, -18.02) * mm, "end": v(5.2, -18) * mm});
            skLineSegment(sketch, "E5809", {"start": v(5.2, -18) * mm, "end": v(5.31, -18.01) * mm});
            skLineSegment(sketch, "E5810", {"start": v(5.31, -18.01) * mm, "end": v(5.4, -18.04) * mm});
            skLineSegment(sketch, "E5811", {"start": v(5.4, -18.04) * mm, "end": v(5.48, -18.08) * mm});
            skLineSegment(sketch, "E5812", {"start": v(5.48, -18.08) * mm, "end": v(5.54, -18.12) * mm});
            skLineSegment(sketch, "E5813", {"start": v(5.54, -18.12) * mm, "end": v(5.65, -18.24) * mm});
            skLineSegment(sketch, "E5814", {"start": v(5.65, -18.24) * mm, "end": v(5.77, -18.36) * mm});
            skLineSegment(sketch, "E5815", {"start": v(5.77, -18.36) * mm, "end": v(5.94, -18.25) * mm});
            skLineSegment(sketch, "E5816", {"start": v(5.94, -18.25) * mm, "end": v(6.05, -18.08) * mm});
            skLineSegment(sketch, "E5817", {"start": v(6.05, -18.08) * mm, "end": v(6.11, -17.88) * mm});
            skLineSegment(sketch, "E5818", {"start": v(6.11, -17.88) * mm, "end": v(6.14, -17.64) * mm});
            skLineSegment(sketch, "E5819", {"start": v(6.14, -17.64) * mm, "end": v(6.15, -17.38) * mm});
            skLineSegment(sketch, "E5820", {"start": v(6.15, -17.38) * mm, "end": v(6.13, -17.12) * mm});
            skLineSegment(sketch, "E5821", {"start": v(6.13, -17.12) * mm, "end": v(6.11, -16.86) * mm});
            skLineSegment(sketch, "E5822", {"start": v(6.11, -16.86) * mm, "end": v(6.1, -16.63) * mm});
            skLineSegment(sketch, "E5823", {"start": v(6.1, -16.63) * mm, "end": v(6.08, -16.38) * mm});
            skLineSegment(sketch, "E5824", {"start": v(6.08, -16.38) * mm, "end": v(6.05, -16.13) * mm});
            skLineSegment(sketch, "E5825", {"start": v(6.05, -16.13) * mm, "end": v(6.02, -15.9) * mm});
            skLineSegment(sketch, "E5826", {"start": v(6.02, -15.9) * mm, "end": v(5.96, -15.7) * mm});
            skLineSegment(sketch, "E5827", {"start": v(5.96, -15.7) * mm, "end": v(5.86, -15.52) * mm});
            skLineSegment(sketch, "E5828", {"start": v(5.86, -15.52) * mm, "end": v(5.72, -15.38) * mm});
            skLineSegment(sketch, "E5829", {"start": v(5.72, -15.38) * mm, "end": v(5.53, -15.3) * mm});
            skLineSegment(sketch, "E5830", {"start": v(5.53, -15.3) * mm, "end": v(5.28, -15.3) * mm});
            skLineSegment(sketch, "E5831", {"start": v(5.28, -15.3) * mm, "end": v(5.07, -15.33) * mm});
            skLineSegment(sketch, "E5832", {"start": v(5.07, -15.33) * mm, "end": v(4.89, -15.42) * mm});
            skLineSegment(sketch, "E5833", {"start": v(4.89, -15.42) * mm, "end": v(4.73, -15.54) * mm});
            skLineSegment(sketch, "E5834", {"start": v(4.73, -15.54) * mm, "end": v(4.61, -15.7) * mm});
            skLineSegment(sketch, "E5835", {"start": v(4.61, -15.7) * mm, "end": v(4.52, -15.89) * mm});
            skLineSegment(sketch, "E5836", {"start": v(4.52, -15.89) * mm, "end": v(4.47, -16.1) * mm});
            skLineSegment(sketch, "E5837", {"start": v(4.47, -16.1) * mm, "end": v(4.46, -16.33) * mm});
            skLineSegment(sketch, "E5838", {"start": v(4.46, -16.33) * mm, "end": v(4.49, -16.57) * mm});
            skLineSegment(sketch, "E5839", {"start": v(4.49, -16.57) * mm, "end": v(4.55, -16.84) * mm});
            skLineSegment(sketch, "E5840", {"start": v(4.55, -16.84) * mm, "end": v(4.58, -17) * mm});
            skLineSegment(sketch, "E5841", {"start": v(4.58, -17) * mm, "end": v(4.58, -17.07) * mm});
            skLineSegment(sketch, "E5842", {"start": v(4.58, -17.07) * mm, "end": v(4.56, -17.16) * mm});
            skLineSegment(sketch, "E5843", {"start": v(4.56, -17.16) * mm, "end": v(4.53, -17.27) * mm});
            skLineSegment(sketch, "E5844", {"start": v(4.53, -17.27) * mm, "end": v(4.5, -17.42) * mm});
            skLineSegment(sketch, "E5845", {"start": v(4.5, -17.42) * mm, "end": v(4.46, -17.57) * mm});
            skLineSegment(sketch, "E5846", {"start": v(4.46, -17.57) * mm, "end": v(4.44, -17.7) * mm});
            skLineSegment(sketch, "E5847", {"start": v(4.44, -17.7) * mm, "end": v(4.44, -17.82) * mm});
            skLineSegment(sketch, "E5848", {"start": v(4.44, -17.82) * mm, "end": v(4.46, -17.92) * mm});
            skLineSegment(sketch, "E5849", {"start": v(4.46, -17.92) * mm, "end": v(4.52, -18.11) * mm});
            skLineSegment(sketch, "E5850", {"start": v(4.52, -18.11) * mm, "end": v(4.59, -18.34) * mm});
            skLineSegment(sketch, "E5851", {"start": v(-5.36, -18.36) * mm, "end": v(-5.3, -18.3) * mm});
            skLineSegment(sketch, "E5852", {"start": v(-5.3, -18.3) * mm, "end": v(-5.24, -18.25) * mm});
            skLineSegment(sketch, "E5853", {"start": v(-5.24, -18.25) * mm, "end": v(-5.19, -18.2) * mm});
            skLineSegment(sketch, "E5854", {"start": v(-5.19, -18.2) * mm, "end": v(-5.14, -18.14) * mm});
            skLineSegment(sketch, "E5855", {"start": v(-5.14, -18.14) * mm, "end": v(-5.08, -18.09) * mm});
            skLineSegment(sketch, "E5856", {"start": v(-5.08, -18.09) * mm, "end": v(-5, -18.05) * mm});
            skLineSegment(sketch, "E5857", {"start": v(-5, -18.05) * mm, "end": v(-4.92, -18.02) * mm});
            skLineSegment(sketch, "E5858", {"start": v(-4.92, -18.02) * mm, "end": v(-4.81, -18) * mm});
            skLineSegment(sketch, "E5859", {"start": v(-4.81, -18) * mm, "end": v(-4.7, -18) * mm});
            skLineSegment(sketch, "E5860", {"start": v(-4.7, -18) * mm, "end": v(-4.6, -18.03) * mm});
            skLineSegment(sketch, "E5861", {"start": v(-4.6, -18.03) * mm, "end": v(-4.51, -18.07) * mm});
            skLineSegment(sketch, "E5862", {"start": v(-4.51, -18.07) * mm, "end": v(-4.44, -18.12) * mm});
            skLineSegment(sketch, "E5863", {"start": v(-4.44, -18.12) * mm, "end": v(-4.32, -18.23) * mm});
            skLineSegment(sketch, "E5864", {"start": v(-4.32, -18.23) * mm, "end": v(-4.18, -18.34) * mm});
            skLineSegment(sketch, "E5865", {"start": v(-4.18, -18.34) * mm, "end": v(-4.1, -18.12) * mm});
            skLineSegment(sketch, "E5866", {"start": v(-4.1, -18.12) * mm, "end": v(-4.04, -17.94) * mm});
            skLineSegment(sketch, "E5867", {"start": v(-4.04, -17.94) * mm, "end": v(-4.02, -17.85) * mm});
            skLineSegment(sketch, "E5868", {"start": v(-4.02, -17.85) * mm, "end": v(-4.02, -17.74) * mm});
            skLineSegment(sketch, "E5869", {"start": v(-4.02, -17.74) * mm, "end": v(-4.03, -17.6) * mm});
            skLineSegment(sketch, "E5870", {"start": v(-4.03, -17.6) * mm, "end": v(-4.06, -17.45) * mm});
            skLineSegment(sketch, "E5871", {"start": v(-4.06, -17.45) * mm, "end": v(-4.14, -17.16) * mm});
            skLineSegment(sketch, "E5872", {"start": v(-4.14, -17.16) * mm, "end": v(-4.16, -17.03) * mm});
            skLineSegment(sketch, "E5873", {"start": v(-4.16, -17.03) * mm, "end": v(-4.14, -16.9) * mm});
            skLineSegment(sketch, "E5874", {"start": v(-4.14, -16.9) * mm, "end": v(-4.08, -16.6) * mm});
            skLineSegment(sketch, "E5875", {"start": v(-4.08, -16.6) * mm, "end": v(-4.05, -16.14) * mm});
            skLineSegment(sketch, "E5876", {"start": v(-4.05, -16.14) * mm, "end": v(-4.15, -15.78) * mm});
            skLineSegment(sketch, "E5877", {"start": v(-4.15, -15.78) * mm, "end": v(-4.34, -15.52) * mm});
            skLineSegment(sketch, "E5878", {"start": v(-4.34, -15.52) * mm, "end": v(-4.58, -15.36) * mm});
            skLineSegment(sketch, "E5879", {"start": v(-4.58, -15.36) * mm, "end": v(-4.86, -15.3) * mm});
            skLineSegment(sketch, "E5880", {"start": v(-4.86, -15.3) * mm, "end": v(-5.13, -15.32) * mm});
            skLineSegment(sketch, "E5881", {"start": v(-5.13, -15.32) * mm, "end": v(-5.36, -15.44) * mm});
            skLineSegment(sketch, "E5882", {"start": v(-5.36, -15.44) * mm, "end": v(-5.53, -15.65) * mm});
            skLineSegment(sketch, "E5883", {"start": v(-5.53, -15.65) * mm, "end": v(-5.58, -15.76) * mm});
            skLineSegment(sketch, "E5884", {"start": v(-5.58, -15.76) * mm, "end": v(-5.6, -15.87) * mm});
            skLineSegment(sketch, "E5885", {"start": v(-5.6, -15.87) * mm, "end": v(-5.63, -15.99) * mm});
            skLineSegment(sketch, "E5886", {"start": v(-5.63, -15.99) * mm, "end": v(-5.65, -16.11) * mm});
            skLineSegment(sketch, "E5887", {"start": v(-5.65, -16.11) * mm, "end": v(-5.66, -16.36) * mm});
            skLineSegment(sketch, "E5888", {"start": v(-5.66, -16.36) * mm, "end": v(-5.67, -16.61) * mm});
            skLineSegment(sketch, "E5889", {"start": v(-5.67, -16.61) * mm, "end": v(-5.69, -16.86) * mm});
            skLineSegment(sketch, "E5890", {"start": v(-5.69, -16.86) * mm, "end": v(-5.7, -17.12) * mm});
            skLineSegment(sketch, "E5891", {"start": v(-5.7, -17.12) * mm, "end": v(-5.72, -17.37) * mm});
            skLineSegment(sketch, "E5892", {"start": v(-5.72, -17.37) * mm, "end": v(-5.72, -17.63) * mm});
            skLineSegment(sketch, "E5893", {"start": v(-5.72, -17.63) * mm, "end": v(-5.7, -17.86) * mm});
            skLineSegment(sketch, "E5894", {"start": v(-5.7, -17.86) * mm, "end": v(-5.63, -18.07) * mm});
            skLineSegment(sketch, "E5895", {"start": v(-5.63, -18.07) * mm, "end": v(-5.52, -18.24) * mm});
            skLineSegment(sketch, "E5896", {"start": v(-5.52, -18.24) * mm, "end": v(-5.36, -18.36) * mm});
            skLineSegment(sketch, "E5897", {"start": v(2.85, -10.65) * mm, "end": v(3, -10.59) * mm});
            skLineSegment(sketch, "E5898", {"start": v(3, -10.59) * mm, "end": v(3.13, -10.44) * mm});
            skLineSegment(sketch, "E5899", {"start": v(3.13, -10.44) * mm, "end": v(3.24, -10.22) * mm});
            skLineSegment(sketch, "E5900", {"start": v(3.24, -10.22) * mm, "end": v(3.33, -9.96) * mm});
            skLineSegment(sketch, "E5901", {"start": v(3.33, -9.96) * mm, "end": v(3.4, -9.67) * mm});
            skLineSegment(sketch, "E5902", {"start": v(3.4, -9.67) * mm, "end": v(3.47, -9.38) * mm});
            skLineSegment(sketch, "E5903", {"start": v(3.47, -9.38) * mm, "end": v(3.53, -9.1) * mm});
            skLineSegment(sketch, "E5904", {"start": v(3.53, -9.1) * mm, "end": v(3.59, -8.85) * mm});
            skLineSegment(sketch, "E5905", {"start": v(3.59, -8.85) * mm, "end": v(3.63, -8.67) * mm});
            skLineSegment(sketch, "E5906", {"start": v(3.63, -8.67) * mm, "end": v(3.69, -8.5) * mm});
            skLineSegment(sketch, "E5907", {"start": v(3.69, -8.5) * mm, "end": v(3.73, -8.3) * mm});
            skLineSegment(sketch, "E5908", {"start": v(3.73, -8.3) * mm, "end": v(3.77, -8.13) * mm});
            skLineSegment(sketch, "E5909", {"start": v(3.77, -8.13) * mm, "end": v(3.86, -8.32) * mm});
            skLineSegment(sketch, "E5910", {"start": v(3.86, -8.32) * mm, "end": v(3.93, -8.59) * mm});
            skLineSegment(sketch, "E5911", {"start": v(3.93, -8.59) * mm, "end": v(4, -8.9) * mm});
            skLineSegment(sketch, "E5912", {"start": v(4, -8.9) * mm, "end": v(4.05, -9.23) * mm});
            skLineSegment(sketch, "E5913", {"start": v(4.05, -9.23) * mm, "end": v(4.1, -9.56) * mm});
            skLineSegment(sketch, "E5914", {"start": v(4.1, -9.56) * mm, "end": v(4.16, -9.85) * mm});
            skLineSegment(sketch, "E5915", {"start": v(4.16, -9.85) * mm, "end": v(4.23, -10.09) * mm});
            skLineSegment(sketch, "E5916", {"start": v(4.23, -10.09) * mm, "end": v(4.31, -10.23) * mm});
            skLineSegment(sketch, "E5917", {"start": v(4.31, -10.23) * mm, "end": v(4.43, -10.18) * mm});
            skLineSegment(sketch, "E5918", {"start": v(4.43, -10.18) * mm, "end": v(4.52, -10.08) * mm});
            skLineSegment(sketch, "E5919", {"start": v(4.52, -10.08) * mm, "end": v(4.57, -9.94) * mm});
            skLineSegment(sketch, "E5920", {"start": v(4.57, -9.94) * mm, "end": v(4.6, -9.79) * mm});
            skLineSegment(sketch, "E5921", {"start": v(4.6, -9.79) * mm, "end": v(4.61, -9.61) * mm});
            skLineSegment(sketch, "E5922", {"start": v(4.61, -9.61) * mm, "end": v(4.6, -9.44) * mm});
            skLineSegment(sketch, "E5923", {"start": v(4.6, -9.44) * mm, "end": v(4.6, -9.27) * mm});
            skLineSegment(sketch, "E5924", {"start": v(4.6, -9.27) * mm, "end": v(4.6, -9.11) * mm});
            skLineSegment(sketch, "E5925", {"start": v(4.6, -9.11) * mm, "end": v(4.58, -8.78) * mm});
            skLineSegment(sketch, "E5926", {"start": v(4.58, -8.78) * mm, "end": v(4.56, -8.45) * mm});
            skLineSegment(sketch, "E5927", {"start": v(4.56, -8.45) * mm, "end": v(4.54, -8.11) * mm});
            skLineSegment(sketch, "E5928", {"start": v(4.54, -8.11) * mm, "end": v(4.52, -7.78) * mm});
            skLineSegment(sketch, "E5929", {"start": v(4.52, -7.78) * mm, "end": v(4.2, -7.79) * mm});
            skLineSegment(sketch, "E5930", {"start": v(4.2, -7.79) * mm, "end": v(3.9, -7.84) * mm});
            skLineSegment(sketch, "E5931", {"start": v(3.9, -7.84) * mm, "end": v(3.6, -7.92) * mm});
            skLineSegment(sketch, "E5932", {"start": v(3.6, -7.92) * mm, "end": v(3.34, -8.04) * mm});
            skLineSegment(sketch, "E5933", {"start": v(3.34, -8.04) * mm, "end": v(3.09, -8.17) * mm});
            skLineSegment(sketch, "E5934", {"start": v(3.09, -8.17) * mm, "end": v(2.86, -8.3) * mm});
            skLineSegment(sketch, "E5935", {"start": v(2.86, -8.3) * mm, "end": v(2.65, -8.46) * mm});
            skLineSegment(sketch, "E5936", {"start": v(2.65, -8.46) * mm, "end": v(2.46, -8.6) * mm});
            skLineSegment(sketch, "E5937", {"start": v(2.46, -8.6) * mm, "end": v(2.34, -8.7) * mm});
            skLineSegment(sketch, "E5938", {"start": v(2.34, -8.7) * mm, "end": v(2.26, -8.78) * mm});
            skLineSegment(sketch, "E5939", {"start": v(2.26, -8.78) * mm, "end": v(2.22, -8.85) * mm});
            skLineSegment(sketch, "E5940", {"start": v(2.22, -8.85) * mm, "end": v(2.21, -8.93) * mm});
            skLineSegment(sketch, "E5941", {"start": v(2.21, -8.93) * mm, "end": v(2.28, -9.17) * mm});
            skLineSegment(sketch, "E5942", {"start": v(2.28, -9.17) * mm, "end": v(2.42, -9.63) * mm});
            skLineSegment(sketch, "E5943", {"start": v(2.42, -9.63) * mm, "end": v(2.49, -9.92) * mm});
            skLineSegment(sketch, "E5944", {"start": v(2.49, -9.92) * mm, "end": v(2.57, -10.22) * mm});
            skLineSegment(sketch, "E5945", {"start": v(2.57, -10.22) * mm, "end": v(2.62, -10.36) * mm});
            skLineSegment(sketch, "E5946", {"start": v(2.62, -10.36) * mm, "end": v(2.68, -10.49) * mm});
            skLineSegment(sketch, "E5947", {"start": v(2.68, -10.49) * mm, "end": v(2.76, -10.58) * mm});
            skLineSegment(sketch, "E5948", {"start": v(2.76, -10.58) * mm, "end": v(2.85, -10.65) * mm});
            skLineSegment(sketch, "E5949", {"start": v(-0.8, -11.71) * mm, "end": v(-0.75, -11.9) * mm});
            skLineSegment(sketch, "E5950", {"start": v(-0.75, -11.9) * mm, "end": v(-0.68, -12.16) * mm});
            skLineSegment(sketch, "E5951", {"start": v(-0.68, -12.16) * mm, "end": v(-0.6, -12.46) * mm});
            skLineSegment(sketch, "E5952", {"start": v(-0.6, -12.46) * mm, "end": v(-0.5, -12.78) * mm});
            skLineSegment(sketch, "E5953", {"start": v(-0.5, -12.78) * mm, "end": v(-0.37, -13.09) * mm});
            skLineSegment(sketch, "E5954", {"start": v(-0.37, -13.09) * mm, "end": v(-0.24, -13.34) * mm});
            skLineSegment(sketch, "E5955", {"start": v(-0.24, -13.34) * mm, "end": v(-0.1, -13.52) * mm});
            skLineSegment(sketch, "E5956", {"start": v(-0.1, -13.52) * mm, "end": v(0.06, -13.6) * mm});
            skLineSegment(sketch, "E5957", {"start": v(0.06, -13.6) * mm, "end": v(0.24, -13.53) * mm});
            skLineSegment(sketch, "E5958", {"start": v(0.24, -13.53) * mm, "end": v(0.41, -13.33) * mm});
            skLineSegment(sketch, "E5959", {"start": v(0.41, -13.33) * mm, "end": v(0.58, -13.05) * mm});
            skLineSegment(sketch, "E5960", {"start": v(0.58, -13.05) * mm, "end": v(0.74, -12.7) * mm});
            skLineSegment(sketch, "E5961", {"start": v(0.74, -12.7) * mm, "end": v(0.88, -12.34) * mm});
            skLineSegment(sketch, "E5962", {"start": v(0.88, -12.34) * mm, "end": v(1, -11.99) * mm});
            skLineSegment(sketch, "E5963", {"start": v(1, -11.99) * mm, "end": v(1.08, -11.7) * mm});
            skLineSegment(sketch, "E5964", {"start": v(1.08, -11.7) * mm, "end": v(1.14, -11.49) * mm});
            skLineSegment(sketch, "E5965", {"start": v(1.14, -11.49) * mm, "end": v(1.07, -11.43) * mm});
            skLineSegment(sketch, "E5966", {"start": v(1.07, -11.43) * mm, "end": v(1.05, -11.41) * mm});
            skLineSegment(sketch, "E5967", {"start": v(1.05, -11.41) * mm, "end": v(0.95, -11.35) * mm});
            skLineSegment(sketch, "E5968", {"start": v(0.95, -11.35) * mm, "end": v(0.87, -11.3) * mm});
            skLineSegment(sketch, "E5969", {"start": v(0.87, -11.3) * mm, "end": v(0.8, -11.22) * mm});
            skLineSegment(sketch, "E5970", {"start": v(0.8, -11.22) * mm, "end": v(0.75, -11.15) * mm});
            skLineSegment(sketch, "E5971", {"start": v(0.75, -11.15) * mm, "end": v(0.7, -11.06) * mm});
            skLineSegment(sketch, "E5972", {"start": v(0.7, -11.06) * mm, "end": v(0.63, -10.89) * mm});
            skLineSegment(sketch, "E5973", {"start": v(0.63, -10.89) * mm, "end": v(0.56, -10.7) * mm});
            skLineSegment(sketch, "E5974", {"start": v(0.56, -10.7) * mm, "end": v(0.5, -10.44) * mm});
            skLineSegment(sketch, "E5975", {"start": v(0.5, -10.44) * mm, "end": v(0.44, -10.13) * mm});
            skLineSegment(sketch, "E5976", {"start": v(0.44, -10.13) * mm, "end": v(0.4, -9.97) * mm});
            skLineSegment(sketch, "E5977", {"start": v(0.4, -9.97) * mm, "end": v(0.36, -9.83) * mm});
            skLineSegment(sketch, "E5978", {"start": v(0.36, -9.83) * mm, "end": v(0.32, -9.71) * mm});
            skLineSegment(sketch, "E5979", {"start": v(0.32, -9.71) * mm, "end": v(0.27, -9.63) * mm});
            skLineSegment(sketch, "E5980", {"start": v(0.27, -9.63) * mm, "end": v(0.2, -9.88) * mm});
            skLineSegment(sketch, "E5981", {"start": v(0.2, -9.88) * mm, "end": v(0.14, -10.22) * mm});
            skLineSegment(sketch, "E5982", {"start": v(0.14, -10.22) * mm, "end": v(0.1, -10.6) * mm});
            skLineSegment(sketch, "E5983", {"start": v(0.1, -10.6) * mm, "end": v(0.05, -10.99) * mm});
            skLineSegment(sketch, "E5984", {"start": v(0.05, -10.99) * mm, "end": v(-0.05, -11.33) * mm});
            skLineSegment(sketch, "E5985", {"start": v(-0.05, -11.33) * mm, "end": v(-0.2, -11.6) * mm});
            skLineSegment(sketch, "E5986", {"start": v(-0.2, -11.6) * mm, "end": v(-0.45, -11.73) * mm});
            skLineSegment(sketch, "E5987", {"start": v(-0.45, -11.73) * mm, "end": v(-0.8, -11.71) * mm});
            skLineSegment(sketch, "E5988", {"start": v(10.23, -8.88) * mm, "end": v(10.63, -8.96) * mm});
            skLineSegment(sketch, "E5989", {"start": v(10.63, -8.96) * mm, "end": v(11.02, -9.04) * mm});
            skLineSegment(sketch, "E5990", {"start": v(11.02, -9.04) * mm, "end": v(11.42, -9.1) * mm});
            skLineSegment(sketch, "E5991", {"start": v(11.42, -9.1) * mm, "end": v(11.82, -9.14) * mm});
            skLineSegment(sketch, "E5992", {"start": v(11.82, -9.14) * mm, "end": v(12.22, -9.13) * mm});
            skLineSegment(sketch, "E5993", {"start": v(12.22, -9.13) * mm, "end": v(12.62, -9.07) * mm});
            skLineSegment(sketch, "E5994", {"start": v(12.62, -9.07) * mm, "end": v(13.03, -8.94) * mm});
            skLineSegment(sketch, "E5995", {"start": v(13.03, -8.94) * mm, "end": v(13.45, -8.74) * mm});
            skLineSegment(sketch, "E5996", {"start": v(13.45, -8.74) * mm, "end": v(13.64, -8.62) * mm});
            skLineSegment(sketch, "E5997", {"start": v(13.64, -8.62) * mm, "end": v(13.84, -8.47) * mm});
            skLineSegment(sketch, "E5998", {"start": v(13.84, -8.47) * mm, "end": v(13.94, -8.4) * mm});
            skLineSegment(sketch, "E5999", {"start": v(13.94, -8.4) * mm, "end": v(14.02, -8.31) * mm});
            skLineSegment(sketch, "E6000", {"start": v(14.02, -8.31) * mm, "end": v(14.09, -8.24) * mm});
            skLineSegment(sketch, "E6001", {"start": v(14.09, -8.24) * mm, "end": v(14.14, -8.17) * mm});
            skLineSegment(sketch, "E6002", {"start": v(14.14, -8.17) * mm, "end": v(13.47, -8.13) * mm});
            skLineSegment(sketch, "E6003", {"start": v(13.47, -8.13) * mm, "end": v(13, -8.11) * mm});
            skLineSegment(sketch, "E6004", {"start": v(13, -8.11) * mm, "end": v(12.66, -8.1) * mm});
            skLineSegment(sketch, "E6005", {"start": v(12.66, -8.1) * mm, "end": v(12.38, -8.07) * mm});
            skLineSegment(sketch, "E6006", {"start": v(12.38, -8.07) * mm, "end": v(12.11, -8.02) * mm});
            skLineSegment(sketch, "E6007", {"start": v(12.11, -8.02) * mm, "end": v(11.78, -7.94) * mm});
            skLineSegment(sketch, "E6008", {"start": v(11.78, -7.94) * mm, "end": v(11.32, -7.8) * mm});
            skLineSegment(sketch, "E6009", {"start": v(11.32, -7.8) * mm, "end": v(10.68, -7.6) * mm});
            skLineSegment(sketch, "E6010", {"start": v(10.68, -7.6) * mm, "end": v(10.66, -7.77) * mm});
            skLineSegment(sketch, "E6011", {"start": v(10.66, -7.77) * mm, "end": v(10.62, -7.95) * mm});
            skLineSegment(sketch, "E6012", {"start": v(10.62, -7.95) * mm, "end": v(10.58, -8.13) * mm});
            skLineSegment(sketch, "E6013", {"start": v(10.58, -8.13) * mm, "end": v(10.53, -8.28) * mm});
            skLineSegment(sketch, "E6014", {"start": v(10.53, -8.28) * mm, "end": v(10.46, -8.44) * mm});
            skLineSegment(sketch, "E6015", {"start": v(10.46, -8.44) * mm, "end": v(10.38, -8.58) * mm});
            skLineSegment(sketch, "E6016", {"start": v(10.38, -8.58) * mm, "end": v(10.34, -8.64) * mm});
            skLineSegment(sketch, "E6017", {"start": v(10.34, -8.64) * mm, "end": v(10.3, -8.72) * mm});
            skLineSegment(sketch, "E6018", {"start": v(10.3, -8.72) * mm, "end": v(10.26, -8.8) * mm});
            skLineSegment(sketch, "E6019", {"start": v(10.26, -8.8) * mm, "end": v(10.23, -8.88) * mm});
            skLineSegment(sketch, "E6020", {"start": v(-14.14, -8.16) * mm, "end": v(-13.97, -8.38) * mm});
            skLineSegment(sketch, "E6021", {"start": v(-13.97, -8.38) * mm, "end": v(-13.75, -8.57) * mm});
            skLineSegment(sketch, "E6022", {"start": v(-13.75, -8.57) * mm, "end": v(-13.48, -8.74) * mm});
            skLineSegment(sketch, "E6023", {"start": v(-13.48, -8.74) * mm, "end": v(-13.18, -8.88) * mm});
            skLineSegment(sketch, "E6024", {"start": v(-13.18, -8.88) * mm, "end": v(-12.85, -8.99) * mm});
            skLineSegment(sketch, "E6025", {"start": v(-12.85, -8.99) * mm, "end": v(-12.52, -9.07) * mm});
            skLineSegment(sketch, "E6026", {"start": v(-12.52, -9.07) * mm, "end": v(-12.18, -9.12) * mm});
            skLineSegment(sketch, "E6027", {"start": v(-12.18, -9.12) * mm, "end": v(-11.86, -9.14) * mm});
            skLineSegment(sketch, "E6028", {"start": v(-11.86, -9.14) * mm, "end": v(-11.62, -9.13) * mm});
            skLineSegment(sketch, "E6029", {"start": v(-11.62, -9.13) * mm, "end": v(-11.4, -9.1) * mm});
            skLineSegment(sketch, "E6030", {"start": v(-11.4, -9.1) * mm, "end": v(-11.2, -9.08) * mm});
            skLineSegment(sketch, "E6031", {"start": v(-11.2, -9.08) * mm, "end": v(-11, -9.04) * mm});
            skLineSegment(sketch, "E6032", {"start": v(-11, -9.04) * mm, "end": v(-10.81, -9) * mm});
            skLineSegment(sketch, "E6033", {"start": v(-10.81, -9) * mm, "end": v(-10.62, -8.95) * mm});
            skLineSegment(sketch, "E6034", {"start": v(-10.62, -8.95) * mm, "end": v(-10.43, -8.91) * mm});
            skLineSegment(sketch, "E6035", {"start": v(-10.43, -8.91) * mm, "end": v(-10.22, -8.88) * mm});
            skLineSegment(sketch, "E6036", {"start": v(-10.22, -8.88) * mm, "end": v(-10.35, -8.61) * mm});
            skLineSegment(sketch, "E6037", {"start": v(-10.35, -8.61) * mm, "end": v(-10.49, -8.36) * mm});
            skLineSegment(sketch, "E6038", {"start": v(-10.49, -8.36) * mm, "end": v(-10.55, -8.21) * mm});
            skLineSegment(sketch, "E6039", {"start": v(-10.55, -8.21) * mm, "end": v(-10.6, -8.04) * mm});
            skLineSegment(sketch, "E6040", {"start": v(-10.6, -8.04) * mm, "end": v(-10.66, -7.84) * mm});
            skLineSegment(sketch, "E6041", {"start": v(-10.66, -7.84) * mm, "end": v(-10.7, -7.6) * mm});
            skLineSegment(sketch, "E6042", {"start": v(-10.7, -7.6) * mm, "end": v(-11.1, -7.76) * mm});
            skLineSegment(sketch, "E6043", {"start": v(-11.1, -7.76) * mm, "end": v(-11.5, -7.88) * mm});
            skLineSegment(sketch, "E6044", {"start": v(-11.5, -7.88) * mm, "end": v(-11.91, -7.97) * mm});
            skLineSegment(sketch, "E6045", {"start": v(-11.91, -7.97) * mm, "end": v(-12.33, -8.04) * mm});
            skLineSegment(sketch, "E6046", {"start": v(-12.33, -8.04) * mm, "end": v(-12.76, -8.1) * mm});
            skLineSegment(sketch, "E6047", {"start": v(-12.76, -8.1) * mm, "end": v(-13.2, -8.13) * mm});
            skLineSegment(sketch, "E6048", {"start": v(-13.2, -8.13) * mm, "end": v(-13.66, -8.15) * mm});
            skLineSegment(sketch, "E6049", {"start": v(-13.66, -8.15) * mm, "end": v(-14.14, -8.16) * mm});
            skLineSegment(sketch, "E6050", {"start": v(-6.1, -19.53) * mm, "end": v(-6.09, -19.47) * mm});
            skLineSegment(sketch, "E6051", {"start": v(-6.09, -19.47) * mm, "end": v(-6.05, -19.4) * mm});
            skLineSegment(sketch, "E6052", {"start": v(-6.05, -19.4) * mm, "end": v(-6, -19.36) * mm});
            skLineSegment(sketch, "E6053", {"start": v(-6, -19.36) * mm, "end": v(-5.92, -19.3) * mm});
            skLineSegment(sketch, "E6054", {"start": v(-5.92, -19.3) * mm, "end": v(-5.82, -19.26) * mm});
            skLineSegment(sketch, "E6055", {"start": v(-5.82, -19.26) * mm, "end": v(-5.7, -19.22) * mm});
            skLineSegment(sketch, "E6056", {"start": v(-5.7, -19.22) * mm, "end": v(-5.55, -19.18) * mm});
            skLineSegment(sketch, "E6057", {"start": v(-5.55, -19.18) * mm, "end": v(-5.37, -19.13) * mm});
            skLineSegment(sketch, "E6058", {"start": v(-5.37, -19.13) * mm, "end": v(-5.15, -19.08) * mm});
            skLineSegment(sketch, "E6059", {"start": v(-5.15, -19.08) * mm, "end": v(-5.2, -19) * mm});
            skLineSegment(sketch, "E6060", {"start": v(-5.2, -19) * mm, "end": v(-5.23, -18.92) * mm});
            skLineSegment(sketch, "E6061", {"start": v(-5.23, -18.92) * mm, "end": v(-5.27, -18.85) * mm});
            skLineSegment(sketch, "E6062", {"start": v(-5.27, -18.85) * mm, "end": v(-5.32, -18.8) * mm});
            skLineSegment(sketch, "E6063", {"start": v(-5.32, -18.8) * mm, "end": v(-5.37, -18.74) * mm});
            skLineSegment(sketch, "E6064", {"start": v(-5.37, -18.74) * mm, "end": v(-5.43, -18.7) * mm});
            skLineSegment(sketch, "E6065", {"start": v(-5.43, -18.7) * mm, "end": v(-5.5, -18.65) * mm});
            skLineSegment(sketch, "E6066", {"start": v(-5.5, -18.65) * mm, "end": v(-5.59, -18.6) * mm});
            skLineSegment(sketch, "E6067", {"start": v(-5.59, -18.6) * mm, "end": v(-5.8, -18.44) * mm});
            skLineSegment(sketch, "E6068", {"start": v(-5.8, -18.44) * mm, "end": v(-5.94, -18.24) * mm});
            skLineSegment(sketch, "E6069", {"start": v(-5.94, -18.24) * mm, "end": v(-6, -18) * mm});
            skLineSegment(sketch, "E6070", {"start": v(-6, -18) * mm, "end": v(-6.01, -17.73) * mm});
            skLineSegment(sketch, "E6071", {"start": v(-6.01, -17.73) * mm, "end": v(-6, -17.4) * mm});
            skLineSegment(sketch, "E6072", {"start": v(-6, -17.4) * mm, "end": v(-5.96, -17.05) * mm});
            skLineSegment(sketch, "E6073", {"start": v(-5.96, -17.05) * mm, "end": v(-5.92, -16.65) * mm});
            skLineSegment(sketch, "E6074", {"start": v(-5.92, -16.65) * mm, "end": v(-5.91, -16.21) * mm});
            skLineSegment(sketch, "E6075", {"start": v(-5.91, -16.21) * mm, "end": v(-6.31, -16.16) * mm});
            skLineSegment(sketch, "E6076", {"start": v(-6.31, -16.16) * mm, "end": v(-6.61, -16.19) * mm});
            skLineSegment(sketch, "E6077", {"start": v(-6.61, -16.19) * mm, "end": v(-6.83, -16.29) * mm});
            skLineSegment(sketch, "E6078", {"start": v(-6.83, -16.29) * mm, "end": v(-6.96, -16.45) * mm});
            skLineSegment(sketch, "E6079", {"start": v(-6.96, -16.45) * mm, "end": v(-7.04, -16.68) * mm});
            skLineSegment(sketch, "E6080", {"start": v(-7.04, -16.68) * mm, "end": v(-7.06, -16.95) * mm});
            skLineSegment(sketch, "E6081", {"start": v(-7.06, -16.95) * mm, "end": v(-7.04, -17.27) * mm});
            skLineSegment(sketch, "E6082", {"start": v(-7.04, -17.27) * mm, "end": v(-6.98, -17.62) * mm});
            skLineSegment(sketch, "E6083", {"start": v(-6.98, -17.62) * mm, "end": v(-6.93, -17.91) * mm});
            skLineSegment(sketch, "E6084", {"start": v(-6.93, -17.91) * mm, "end": v(-6.87, -18.2) * mm});
            skLineSegment(sketch, "E6085", {"start": v(-6.87, -18.2) * mm, "end": v(-6.8, -18.5) * mm});
            skLineSegment(sketch, "E6086", {"start": v(-6.8, -18.5) * mm, "end": v(-6.71, -18.77) * mm});
            skLineSegment(sketch, "E6087", {"start": v(-6.71, -18.77) * mm, "end": v(-6.6, -19.01) * mm});
            skLineSegment(sketch, "E6088", {"start": v(-6.6, -19.01) * mm, "end": v(-6.47, -19.23) * mm});
            skLineSegment(sketch, "E6089", {"start": v(-6.47, -19.23) * mm, "end": v(-6.3, -19.4) * mm});
            skLineSegment(sketch, "E6090", {"start": v(-6.3, -19.4) * mm, "end": v(-6.1, -19.53) * mm});
            skLineSegment(sketch, "E6091", {"start": v(6.33, -16.24) * mm, "end": v(6.35, -16.64) * mm});
            skLineSegment(sketch, "E6092", {"start": v(6.35, -16.64) * mm, "end": v(6.38, -17.01) * mm});
            skLineSegment(sketch, "E6093", {"start": v(6.38, -17.01) * mm, "end": v(6.42, -17.36) * mm});
            skLineSegment(sketch, "E6094", {"start": v(6.42, -17.36) * mm, "end": v(6.43, -17.69) * mm});
            skLineSegment(sketch, "E6095", {"start": v(6.43, -17.69) * mm, "end": v(6.42, -17.98) * mm});
            skLineSegment(sketch, "E6096", {"start": v(6.42, -17.98) * mm, "end": v(6.36, -18.22) * mm});
            skLineSegment(sketch, "E6097", {"start": v(6.36, -18.22) * mm, "end": v(6.23, -18.43) * mm});
            skLineSegment(sketch, "E6098", {"start": v(6.23, -18.43) * mm, "end": v(6.03, -18.59) * mm});
            skLineSegment(sketch, "E6099", {"start": v(6.03, -18.59) * mm, "end": v(5.94, -18.64) * mm});
            skLineSegment(sketch, "E6100", {"start": v(5.94, -18.64) * mm, "end": v(5.86, -18.69) * mm});
            skLineSegment(sketch, "E6101", {"start": v(5.86, -18.69) * mm, "end": v(5.8, -18.74) * mm});
            skLineSegment(sketch, "E6102", {"start": v(5.8, -18.74) * mm, "end": v(5.74, -18.79) * mm});
            skLineSegment(sketch, "E6103", {"start": v(5.74, -18.79) * mm, "end": v(5.7, -18.84) * mm});
            skLineSegment(sketch, "E6104", {"start": v(5.7, -18.84) * mm, "end": v(5.65, -18.9) * mm});
            skLineSegment(sketch, "E6105", {"start": v(5.65, -18.9) * mm, "end": v(5.61, -18.99) * mm});
            skLineSegment(sketch, "E6106", {"start": v(5.61, -18.99) * mm, "end": v(5.57, -19.08) * mm});
            skLineSegment(sketch, "E6107", {"start": v(5.57, -19.08) * mm, "end": v(5.71, -19.11) * mm});
            skLineSegment(sketch, "E6108", {"start": v(5.71, -19.11) * mm, "end": v(5.85, -19.14) * mm});
            skLineSegment(sketch, "E6109", {"start": v(5.85, -19.14) * mm, "end": v(5.99, -19.17) * mm});
            skLineSegment(sketch, "E6110", {"start": v(5.99, -19.17) * mm, "end": v(6.13, -19.22) * mm});
            skLineSegment(sketch, "E6111", {"start": v(6.13, -19.22) * mm, "end": v(6.28, -19.27) * mm});
            skLineSegment(sketch, "E6112", {"start": v(6.28, -19.27) * mm, "end": v(6.38, -19.32) * mm});
            skLineSegment(sketch, "E6113", {"start": v(6.38, -19.32) * mm, "end": v(6.41, -19.36) * mm});
            skLineSegment(sketch, "E6114", {"start": v(6.41, -19.36) * mm, "end": v(6.45, -19.4) * mm});
            skLineSegment(sketch, "E6115", {"start": v(6.45, -19.4) * mm, "end": v(6.48, -19.45) * mm});
            skLineSegment(sketch, "E6116", {"start": v(6.48, -19.45) * mm, "end": v(6.52, -19.52) * mm});
            skLineSegment(sketch, "E6117", {"start": v(6.52, -19.52) * mm, "end": v(6.71, -19.4) * mm});
            skLineSegment(sketch, "E6118", {"start": v(6.71, -19.4) * mm, "end": v(6.88, -19.24) * mm});
            skLineSegment(sketch, "E6119", {"start": v(6.88, -19.24) * mm, "end": v(7.01, -19.03) * mm});
            skLineSegment(sketch, "E6120", {"start": v(7.01, -19.03) * mm, "end": v(7.12, -18.79) * mm});
            skLineSegment(sketch, "E6121", {"start": v(7.12, -18.79) * mm, "end": v(7.22, -18.52) * mm});
            skLineSegment(sketch, "E6122", {"start": v(7.22, -18.52) * mm, "end": v(7.3, -18.24) * mm});
            skLineSegment(sketch, "E6123", {"start": v(7.3, -18.24) * mm, "end": v(7.35, -17.95) * mm});
            skLineSegment(sketch, "E6124", {"start": v(7.35, -17.95) * mm, "end": v(7.4, -17.66) * mm});
            skLineSegment(sketch, "E6125", {"start": v(7.4, -17.66) * mm, "end": v(7.44, -17.44) * mm});
            skLineSegment(sketch, "E6126", {"start": v(7.44, -17.44) * mm, "end": v(7.48, -17.21) * mm});
            skLineSegment(sketch, "E6127", {"start": v(7.48, -17.21) * mm, "end": v(7.5, -16.98) * mm});
            skLineSegment(sketch, "E6128", {"start": v(7.5, -16.98) * mm, "end": v(7.5, -16.76) * mm});
            skLineSegment(sketch, "E6129", {"start": v(7.5, -16.76) * mm, "end": v(7.44, -16.56) * mm});
            skLineSegment(sketch, "E6130", {"start": v(7.44, -16.56) * mm, "end": v(7.35, -16.4) * mm});
            skLineSegment(sketch, "E6131", {"start": v(7.35, -16.4) * mm, "end": v(7.19, -16.27) * mm});
            skLineSegment(sketch, "E6132", {"start": v(7.19, -16.27) * mm, "end": v(6.95, -16.19) * mm});
            skLineSegment(sketch, "E6133", {"start": v(6.95, -16.19) * mm, "end": v(6.65, -16.17) * mm});
            skLineSegment(sketch, "E6134", {"start": v(6.65, -16.17) * mm, "end": v(6.5, -16.18) * mm});
            skLineSegment(sketch, "E6135", {"start": v(6.5, -16.18) * mm, "end": v(6.33, -16.24) * mm});
            skLineSegment(sketch, "E6136", {"start": v(-14.3, -6.4) * mm, "end": v(-14.2, -6.55) * mm});
            skLineSegment(sketch, "E6137", {"start": v(-14.2, -6.55) * mm, "end": v(-14.08, -6.71) * mm});
            skLineSegment(sketch, "E6138", {"start": v(-14.08, -6.71) * mm, "end": v(-13.93, -6.88) * mm});
            skLineSegment(sketch, "E6139", {"start": v(-13.93, -6.88) * mm, "end": v(-13.76, -7.03) * mm});
            skLineSegment(sketch, "E6140", {"start": v(-13.76, -7.03) * mm, "end": v(-13.57, -7.18) * mm});
            skLineSegment(sketch, "E6141", {"start": v(-13.57, -7.18) * mm, "end": v(-13.38, -7.3) * mm});
            skLineSegment(sketch, "E6142", {"start": v(-13.38, -7.3) * mm, "end": v(-13.17, -7.4) * mm});
            skLineSegment(sketch, "E6143", {"start": v(-13.17, -7.4) * mm, "end": v(-12.97, -7.48) * mm});
            skLineSegment(sketch, "E6144", {"start": v(-12.97, -7.48) * mm, "end": v(-12.74, -7.53) * mm});
            skLineSegment(sketch, "E6145", {"start": v(-12.74, -7.53) * mm, "end": v(-12.47, -7.56) * mm});
            skLineSegment(sketch, "E6146", {"start": v(-12.47, -7.56) * mm, "end": v(-12.19, -7.58) * mm});
            skLineSegment(sketch, "E6147", {"start": v(-12.19, -7.58) * mm, "end": v(-11.9, -7.58) * mm});
            skLineSegment(sketch, "E6148", {"start": v(-11.9, -7.58) * mm, "end": v(-11.6, -7.56) * mm});
            skLineSegment(sketch, "E6149", {"start": v(-11.6, -7.56) * mm, "end": v(-11.33, -7.52) * mm});
            skLineSegment(sketch, "E6150", {"start": v(-11.33, -7.52) * mm, "end": v(-11.08, -7.45) * mm});
            skLineSegment(sketch, "E6151", {"start": v(-11.08, -7.45) * mm, "end": v(-10.87, -7.36) * mm});
            skLineSegment(sketch, "E6152", {"start": v(-10.87, -7.36) * mm, "end": v(-10.9, -7.3) * mm});
            skLineSegment(sketch, "E6153", {"start": v(-10.9, -7.3) * mm, "end": v(-10.96, -7.21) * mm});
            skLineSegment(sketch, "E6154", {"start": v(-10.96, -7.21) * mm, "end": v(-11.02, -7.13) * mm});
            skLineSegment(sketch, "E6155", {"start": v(-11.02, -7.13) * mm, "end": v(-11.08, -7.04) * mm});
            skLineSegment(sketch, "E6156", {"start": v(-11.08, -7.04) * mm, "end": v(-11.2, -6.82) * mm});
            skLineSegment(sketch, "E6157", {"start": v(-11.2, -6.82) * mm, "end": v(-11.3, -6.64) * mm});
            skLineSegment(sketch, "E6158", {"start": v(-11.3, -6.64) * mm, "end": v(-11.35, -6.49) * mm});
            skLineSegment(sketch, "E6159", {"start": v(-11.35, -6.49) * mm, "end": v(-11.39, -6.36) * mm});
            skLineSegment(sketch, "E6160", {"start": v(-11.39, -6.36) * mm, "end": v(-11.41, -6.23) * mm});
            skLineSegment(sketch, "E6161", {"start": v(-11.41, -6.23) * mm, "end": v(-11.43, -6.1) * mm});
            skLineSegment(sketch, "E6162", {"start": v(-11.43, -6.1) * mm, "end": v(-11.47, -5.97) * mm});
            skLineSegment(sketch, "E6163", {"start": v(-11.47, -5.97) * mm, "end": v(-11.52, -5.8) * mm});
            skLineSegment(sketch, "E6164", {"start": v(-11.52, -5.8) * mm, "end": v(-11.87, -6) * mm});
            skLineSegment(sketch, "E6165", {"start": v(-11.87, -6) * mm, "end": v(-12.18, -6.17) * mm});
            skLineSegment(sketch, "E6166", {"start": v(-12.18, -6.17) * mm, "end": v(-12.47, -6.3) * mm});
            skLineSegment(sketch, "E6167", {"start": v(-12.47, -6.3) * mm, "end": v(-12.75, -6.4) * mm});
            skLineSegment(sketch, "E6168", {"start": v(-12.75, -6.4) * mm, "end": v(-13.06, -6.45) * mm});
            skLineSegment(sketch, "E6169", {"start": v(-13.06, -6.45) * mm, "end": v(-13.4, -6.47) * mm});
            skLineSegment(sketch, "E6170", {"start": v(-13.4, -6.47) * mm, "end": v(-13.81, -6.45) * mm});
            skLineSegment(sketch, "E6171", {"start": v(-13.81, -6.45) * mm, "end": v(-14.3, -6.4) * mm});
            skLineSegment(sketch, "E6172", {"start": v(10.87, -7.36) * mm, "end": v(11.07, -7.45) * mm});
            skLineSegment(sketch, "E6173", {"start": v(11.07, -7.45) * mm, "end": v(11.32, -7.52) * mm});
            skLineSegment(sketch, "E6174", {"start": v(11.32, -7.52) * mm, "end": v(11.59, -7.56) * mm});
            skLineSegment(sketch, "E6175", {"start": v(11.59, -7.56) * mm, "end": v(11.88, -7.58) * mm});
            skLineSegment(sketch, "E6176", {"start": v(11.88, -7.58) * mm, "end": v(12.16, -7.58) * mm});
            skLineSegment(sketch, "E6177", {"start": v(12.16, -7.58) * mm, "end": v(12.45, -7.57) * mm});
            skLineSegment(sketch, "E6178", {"start": v(12.45, -7.57) * mm, "end": v(12.7, -7.53) * mm});
            skLineSegment(sketch, "E6179", {"start": v(12.7, -7.53) * mm, "end": v(12.94, -7.49) * mm});
            skLineSegment(sketch, "E6180", {"start": v(12.94, -7.49) * mm, "end": v(13.15, -7.42) * mm});
            skLineSegment(sketch, "E6181", {"start": v(13.15, -7.42) * mm, "end": v(13.36, -7.32) * mm});
            skLineSegment(sketch, "E6182", {"start": v(13.36, -7.32) * mm, "end": v(13.56, -7.2) * mm});
            skLineSegment(sketch, "E6183", {"start": v(13.56, -7.2) * mm, "end": v(13.75, -7.05) * mm});
            skLineSegment(sketch, "E6184", {"start": v(13.75, -7.05) * mm, "end": v(13.92, -6.9) * mm});
            skLineSegment(sketch, "E6185", {"start": v(13.92, -6.9) * mm, "end": v(14.07, -6.73) * mm});
            skLineSegment(sketch, "E6186", {"start": v(14.07, -6.73) * mm, "end": v(14.2, -6.56) * mm});
            skLineSegment(sketch, "E6187", {"start": v(14.2, -6.56) * mm, "end": v(14.29, -6.4) * mm});
            skLineSegment(sketch, "E6188", {"start": v(14.29, -6.4) * mm, "end": v(14.06, -6.42) * mm});
            skLineSegment(sketch, "E6189", {"start": v(14.06, -6.42) * mm, "end": v(13.86, -6.45) * mm});
            skLineSegment(sketch, "E6190", {"start": v(13.86, -6.45) * mm, "end": v(13.68, -6.47) * mm});
            skLineSegment(sketch, "E6191", {"start": v(13.68, -6.47) * mm, "end": v(13.5, -6.48) * mm});
            skLineSegment(sketch, "E6192", {"start": v(13.5, -6.48) * mm, "end": v(13.33, -6.48) * mm});
            skLineSegment(sketch, "E6193", {"start": v(13.33, -6.48) * mm, "end": v(13.15, -6.46) * mm});
            skLineSegment(sketch, "E6194", {"start": v(13.15, -6.46) * mm, "end": v(12.95, -6.43) * mm});
            skLineSegment(sketch, "E6195", {"start": v(12.95, -6.43) * mm, "end": v(12.72, -6.38) * mm});
            skLineSegment(sketch, "E6196", {"start": v(12.72, -6.38) * mm, "end": v(12.56, -6.33) * mm});
            skLineSegment(sketch, "E6197", {"start": v(12.56, -6.33) * mm, "end": v(12.4, -6.27) * mm});
            skLineSegment(sketch, "E6198", {"start": v(12.4, -6.27) * mm, "end": v(12.22, -6.2) * mm});
            skLineSegment(sketch, "E6199", {"start": v(12.22, -6.2) * mm, "end": v(12.08, -6.14) * mm});
            skLineSegment(sketch, "E6200", {"start": v(12.08, -6.14) * mm, "end": v(11.93, -6.06) * mm});
            skLineSegment(sketch, "E6201", {"start": v(11.93, -6.06) * mm, "end": v(11.8, -5.96) * mm});
            skLineSegment(sketch, "E6202", {"start": v(11.8, -5.96) * mm, "end": v(11.66, -5.88) * mm});
            skLineSegment(sketch, "E6203", {"start": v(11.66, -5.88) * mm, "end": v(11.51, -5.8) * mm});
            skLineSegment(sketch, "E6204", {"start": v(11.51, -5.8) * mm, "end": v(11.47, -5.93) * mm});
            skLineSegment(sketch, "E6205", {"start": v(11.47, -5.93) * mm, "end": v(11.45, -6.05) * mm});
            skLineSegment(sketch, "E6206", {"start": v(11.45, -6.05) * mm, "end": v(11.43, -6.16) * mm});
            skLineSegment(sketch, "E6207", {"start": v(11.43, -6.16) * mm, "end": v(11.41, -6.28) * mm});
            skLineSegment(sketch, "E6208", {"start": v(11.41, -6.28) * mm, "end": v(11.38, -6.41) * mm});
            skLineSegment(sketch, "E6209", {"start": v(11.38, -6.41) * mm, "end": v(11.33, -6.57) * mm});
            skLineSegment(sketch, "E6210", {"start": v(11.33, -6.57) * mm, "end": v(11.24, -6.77) * mm});
            skLineSegment(sketch, "E6211", {"start": v(11.24, -6.77) * mm, "end": v(11.1, -7.02) * mm});
            skLineSegment(sketch, "E6212", {"start": v(11.1, -7.02) * mm, "end": v(11.03, -7.1) * mm});
            skLineSegment(sketch, "E6213", {"start": v(11.03, -7.1) * mm, "end": v(10.97, -7.2) * mm});
            skLineSegment(sketch, "E6214", {"start": v(10.97, -7.2) * mm, "end": v(10.9, -7.28) * mm});
            skLineSegment(sketch, "E6215", {"start": v(10.9, -7.28) * mm, "end": v(10.87, -7.36) * mm});
            skLineSegment(sketch, "E6216", {"start": v(-9.66, -2.83) * mm, "end": v(-9.72, -2.72) * mm});
            skLineSegment(sketch, "E6217", {"start": v(-9.72, -2.72) * mm, "end": v(-9.78, -2.63) * mm});
            skLineSegment(sketch, "E6218", {"start": v(-9.78, -2.63) * mm, "end": v(-9.84, -2.53) * mm});
            skLineSegment(sketch, "E6219", {"start": v(-9.84, -2.53) * mm, "end": v(-9.9, -2.4) * mm});
            skLineSegment(sketch, "E6220", {"start": v(-9.9, -2.4) * mm, "end": v(-9.97, -2.3) * mm});
            skLineSegment(sketch, "E6221", {"start": v(-9.97, -2.3) * mm, "end": v(-10.02, -2.17) * mm});
            skLineSegment(sketch, "E6222", {"start": v(-10.02, -2.17) * mm, "end": v(-10.08, -2.03) * mm});
            skLineSegment(sketch, "E6223", {"start": v(-10.08, -2.03) * mm, "end": v(-10.12, -1.89) * mm});
            skLineSegment(sketch, "E6224", {"start": v(-10.12, -1.89) * mm, "end": v(-9.56, -2) * mm});
            skLineSegment(sketch, "E6225", {"start": v(-9.56, -2) * mm, "end": v(-9.9, -1.69) * mm});
            skLineSegment(sketch, "E6226", {"start": v(-9.9, -1.69) * mm, "end": v(-9.99, -1.65) * mm});
            skLineSegment(sketch, "E6227", {"start": v(-9.99, -1.65) * mm, "end": v(-10.13, -1.61) * mm});
            skLineSegment(sketch, "E6228", {"start": v(-10.13, -1.61) * mm, "end": v(-10.33, -1.59) * mm});
            skLineSegment(sketch, "E6229", {"start": v(-10.33, -1.59) * mm, "end": v(-10.55, -1.56) * mm});
            skLineSegment(sketch, "E6230", {"start": v(-10.55, -1.56) * mm, "end": v(-10.8, -1.54) * mm});
            skLineSegment(sketch, "E6231", {"start": v(-10.8, -1.54) * mm, "end": v(-11.05, -1.5) * mm});
            skLineSegment(sketch, "E6232", {"start": v(-11.05, -1.5) * mm, "end": v(-11.3, -1.48) * mm});
            skLineSegment(sketch, "E6233", {"start": v(-11.3, -1.48) * mm, "end": v(-11.52, -1.44) * mm});
            skLineSegment(sketch, "E6234", {"start": v(-11.52, -1.44) * mm, "end": v(-11.86, -1.36) * mm});
            skLineSegment(sketch, "E6235", {"start": v(-11.86, -1.36) * mm, "end": v(-12.16, -1.28) * mm});
            skLineSegment(sketch, "E6236", {"start": v(-12.16, -1.28) * mm, "end": v(-12.42, -1.2) * mm});
            skLineSegment(sketch, "E6237", {"start": v(-12.42, -1.2) * mm, "end": v(-12.65, -1.13) * mm});
            skLineSegment(sketch, "E6238", {"start": v(-12.65, -1.13) * mm, "end": v(-12.86, -1.06) * mm});
            skLineSegment(sketch, "E6239", {"start": v(-12.86, -1.06) * mm, "end": v(-13.06, -1) * mm});
            skLineSegment(sketch, "E6240", {"start": v(-13.06, -1) * mm, "end": v(-13.27, -0.94) * mm});
            skLineSegment(sketch, "E6241", {"start": v(-13.27, -0.94) * mm, "end": v(-13.48, -0.88) * mm});
            skLineSegment(sketch, "E6242", {"start": v(-13.48, -0.88) * mm, "end": v(-13.38, -1.08) * mm});
            skLineSegment(sketch, "E6243", {"start": v(-13.38, -1.08) * mm, "end": v(-13.23, -1.28) * mm});
            skLineSegment(sketch, "E6244", {"start": v(-13.23, -1.28) * mm, "end": v(-13.05, -1.48) * mm});
            skLineSegment(sketch, "E6245", {"start": v(-13.05, -1.48) * mm, "end": v(-12.84, -1.67) * mm});
            skLineSegment(sketch, "E6246", {"start": v(-12.84, -1.67) * mm, "end": v(-12.62, -1.86) * mm});
            skLineSegment(sketch, "E6247", {"start": v(-12.62, -1.86) * mm, "end": v(-12.4, -2.03) * mm});
            skLineSegment(sketch, "E6248", {"start": v(-12.4, -2.03) * mm, "end": v(-12.18, -2.17) * mm});
            skLineSegment(sketch, "E6249", {"start": v(-12.18, -2.17) * mm, "end": v(-11.99, -2.28) * mm});
            skLineSegment(sketch, "E6250", {"start": v(-11.99, -2.28) * mm, "end": v(-11.77, -2.38) * mm});
            skLineSegment(sketch, "E6251", {"start": v(-11.77, -2.38) * mm, "end": v(-11.51, -2.48) * mm});
            skLineSegment(sketch, "E6252", {"start": v(-11.51, -2.48) * mm, "end": v(-11.21, -2.58) * mm});
            skLineSegment(sketch, "E6253", {"start": v(-11.21, -2.58) * mm, "end": v(-10.89, -2.67) * mm});
            skLineSegment(sketch, "E6254", {"start": v(-10.89, -2.67) * mm, "end": v(-10.56, -2.74) * mm});
            skLineSegment(sketch, "E6255", {"start": v(-10.56, -2.74) * mm, "end": v(-10.24, -2.8) * mm});
            skLineSegment(sketch, "E6256", {"start": v(-10.24, -2.8) * mm, "end": v(-9.93, -2.82) * mm});
            skLineSegment(sketch, "E6257", {"start": v(-9.93, -2.82) * mm, "end": v(-9.66, -2.83) * mm});
            skLineSegment(sketch, "E6258", {"start": v(9.5, -2) * mm, "end": v(10.1, -1.88) * mm});
            skLineSegment(sketch, "E6259", {"start": v(10.1, -1.88) * mm, "end": v(10.07, -2.05) * mm});
            skLineSegment(sketch, "E6260", {"start": v(10.07, -2.05) * mm, "end": v(10.01, -2.2) * mm});
            skLineSegment(sketch, "E6261", {"start": v(10.01, -2.2) * mm, "end": v(9.95, -2.33) * mm});
            skLineSegment(sketch, "E6262", {"start": v(9.95, -2.33) * mm, "end": v(9.89, -2.44) * mm});
            skLineSegment(sketch, "E6263", {"start": v(9.89, -2.44) * mm, "end": v(9.76, -2.63) * mm});
            skLineSegment(sketch, "E6264", {"start": v(9.76, -2.63) * mm, "end": v(9.66, -2.83) * mm});
            skLineSegment(sketch, "E6265", {"start": v(9.66, -2.83) * mm, "end": v(9.94, -2.82) * mm});
            skLineSegment(sketch, "E6266", {"start": v(9.94, -2.82) * mm, "end": v(10.25, -2.79) * mm});
            skLineSegment(sketch, "E6267", {"start": v(10.25, -2.79) * mm, "end": v(10.58, -2.73) * mm});
            skLineSegment(sketch, "E6268", {"start": v(10.58, -2.73) * mm, "end": v(10.9, -2.66) * mm});
            skLineSegment(sketch, "E6269", {"start": v(10.9, -2.66) * mm, "end": v(11.21, -2.58) * mm});
            skLineSegment(sketch, "E6270", {"start": v(11.21, -2.58) * mm, "end": v(11.5, -2.49) * mm});
            skLineSegment(sketch, "E6271", {"start": v(11.5, -2.49) * mm, "end": v(11.77, -2.38) * mm});
            skLineSegment(sketch, "E6272", {"start": v(11.77, -2.38) * mm, "end": v(11.99, -2.28) * mm});
            skLineSegment(sketch, "E6273", {"start": v(11.99, -2.28) * mm, "end": v(12.18, -2.16) * mm});
            skLineSegment(sketch, "E6274", {"start": v(12.18, -2.16) * mm, "end": v(12.4, -2.02) * mm});
            skLineSegment(sketch, "E6275", {"start": v(12.4, -2.02) * mm, "end": v(12.62, -1.85) * mm});
            skLineSegment(sketch, "E6276", {"start": v(12.62, -1.85) * mm, "end": v(12.84, -1.67) * mm});
            skLineSegment(sketch, "E6277", {"start": v(12.84, -1.67) * mm, "end": v(13.05, -1.47) * mm});
            skLineSegment(sketch, "E6278", {"start": v(13.05, -1.47) * mm, "end": v(13.24, -1.27) * mm});
            skLineSegment(sketch, "E6279", {"start": v(13.24, -1.27) * mm, "end": v(13.38, -1.07) * mm});
            skLineSegment(sketch, "E6280", {"start": v(13.38, -1.07) * mm, "end": v(13.48, -0.88) * mm});
            skLineSegment(sketch, "E6281", {"start": v(13.48, -0.88) * mm, "end": v(13.06, -1) * mm});
            skLineSegment(sketch, "E6282", {"start": v(13.06, -1) * mm, "end": v(12.7, -1.11) * mm});
            skLineSegment(sketch, "E6283", {"start": v(12.7, -1.11) * mm, "end": v(12.36, -1.22) * mm});
            skLineSegment(sketch, "E6284", {"start": v(12.36, -1.22) * mm, "end": v(12.03, -1.32) * mm});
            skLineSegment(sketch, "E6285", {"start": v(12.03, -1.32) * mm, "end": v(11.68, -1.41) * mm});
            skLineSegment(sketch, "E6286", {"start": v(11.68, -1.41) * mm, "end": v(11.3, -1.49) * mm});
            skLineSegment(sketch, "E6287", {"start": v(11.3, -1.49) * mm, "end": v(10.87, -1.55) * mm});
            skLineSegment(sketch, "E6288", {"start": v(10.87, -1.55) * mm, "end": v(10.35, -1.59) * mm});
            skLineSegment(sketch, "E6289", {"start": v(10.35, -1.59) * mm, "end": v(10.13, -1.61) * mm});
            skLineSegment(sketch, "E6290", {"start": v(10.13, -1.61) * mm, "end": v(9.98, -1.65) * mm});
            skLineSegment(sketch, "E6291", {"start": v(9.98, -1.65) * mm, "end": v(9.9, -1.69) * mm});
            skLineSegment(sketch, "E6292", {"start": v(9.9, -1.69) * mm, "end": v(9.84, -1.74) * mm});
            skLineSegment(sketch, "E6293", {"start": v(9.84, -1.74) * mm, "end": v(9.8, -1.8) * mm});
            skLineSegment(sketch, "E6294", {"start": v(9.8, -1.8) * mm, "end": v(9.74, -1.86) * mm});
            skLineSegment(sketch, "E6295", {"start": v(9.74, -1.86) * mm, "end": v(9.65, -1.93) * mm});
            skLineSegment(sketch, "E6296", {"start": v(9.65, -1.93) * mm, "end": v(9.5, -2) * mm});
            skLineSegment(sketch, "E6297", {"start": v(9.43, -9.6) * mm, "end": v(9.66, -9.77) * mm});
            skLineSegment(sketch, "E6298", {"start": v(9.66, -9.77) * mm, "end": v(10.06, -9.98) * mm});
            skLineSegment(sketch, "E6299", {"start": v(10.06, -9.98) * mm, "end": v(10.46, -10.14) * mm});
            skLineSegment(sketch, "E6300", {"start": v(10.46, -10.14) * mm, "end": v(10.87, -10.27) * mm});
            skLineSegment(sketch, "E6301", {"start": v(10.87, -10.27) * mm, "end": v(11.29, -10.34) * mm});
            skLineSegment(sketch, "E6302", {"start": v(11.29, -10.34) * mm, "end": v(11.7, -10.36) * mm});
            skLineSegment(sketch, "E6303", {"start": v(11.7, -10.36) * mm, "end": v(12.13, -10.32) * mm});
            skLineSegment(sketch, "E6304", {"start": v(12.13, -10.32) * mm, "end": v(12.55, -10.21) * mm});
            skLineSegment(sketch, "E6305", {"start": v(12.55, -10.21) * mm, "end": v(12.98, -10.03) * mm});
            skLineSegment(sketch, "E6306", {"start": v(12.98, -10.03) * mm, "end": v(13.1, -9.96) * mm});
            skLineSegment(sketch, "E6307", {"start": v(13.1, -9.96) * mm, "end": v(13.23, -9.89) * mm});
            skLineSegment(sketch, "E6308", {"start": v(13.23, -9.89) * mm, "end": v(13.35, -9.8) * mm});
            skLineSegment(sketch, "E6309", {"start": v(13.35, -9.8) * mm, "end": v(13.48, -9.72) * mm});
            skLineSegment(sketch, "E6310", {"start": v(13.48, -9.72) * mm, "end": v(13.6, -9.63) * mm});
            skLineSegment(sketch, "E6311", {"start": v(13.6, -9.63) * mm, "end": v(13.7, -9.54) * mm});
            skLineSegment(sketch, "E6312", {"start": v(13.7, -9.54) * mm, "end": v(13.8, -9.45) * mm});
            skLineSegment(sketch, "E6313", {"start": v(13.8, -9.45) * mm, "end": v(13.89, -9.36) * mm});
            skLineSegment(sketch, "E6314", {"start": v(13.89, -9.36) * mm, "end": v(13.62, -9.38) * mm});
            skLineSegment(sketch, "E6315", {"start": v(13.62, -9.38) * mm, "end": v(13.4, -9.4) * mm});
            skLineSegment(sketch, "E6316", {"start": v(13.4, -9.4) * mm, "end": v(13.2, -9.44) * mm});
            skLineSegment(sketch, "E6317", {"start": v(13.2, -9.44) * mm, "end": v(12.99, -9.47) * mm});
            skLineSegment(sketch, "E6318", {"start": v(12.99, -9.47) * mm, "end": v(12.77, -9.49) * mm});
            skLineSegment(sketch, "E6319", {"start": v(12.77, -9.49) * mm, "end": v(12.52, -9.5) * mm});
            skLineSegment(sketch, "E6320", {"start": v(12.52, -9.5) * mm, "end": v(12.2, -9.5) * mm});
            skLineSegment(sketch, "E6321", {"start": v(12.2, -9.5) * mm, "end": v(11.82, -9.48) * mm});
            skLineSegment(sketch, "E6322", {"start": v(11.82, -9.48) * mm, "end": v(11.62, -9.46) * mm});
            skLineSegment(sketch, "E6323", {"start": v(11.62, -9.46) * mm, "end": v(11.44, -9.45) * mm});
            skLineSegment(sketch, "E6324", {"start": v(11.44, -9.45) * mm, "end": v(11.28, -9.42) * mm});
            skLineSegment(sketch, "E6325", {"start": v(11.28, -9.42) * mm, "end": v(11.12, -9.4) * mm});
            skLineSegment(sketch, "E6326", {"start": v(11.12, -9.4) * mm, "end": v(10.96, -9.36) * mm});
            skLineSegment(sketch, "E6327", {"start": v(10.96, -9.36) * mm, "end": v(10.8, -9.33) * mm});
            skLineSegment(sketch, "E6328", {"start": v(10.8, -9.33) * mm, "end": v(10.63, -9.28) * mm});
            skLineSegment(sketch, "E6329", {"start": v(10.63, -9.28) * mm, "end": v(10.45, -9.23) * mm});
            skLineSegment(sketch, "E6330", {"start": v(10.45, -9.23) * mm, "end": v(10.32, -9.2) * mm});
            skLineSegment(sketch, "E6331", {"start": v(10.32, -9.2) * mm, "end": v(10.22, -9.17) * mm});
            skLineSegment(sketch, "E6332", {"start": v(10.22, -9.17) * mm, "end": v(10.18, -9.15) * mm});
            skLineSegment(sketch, "E6333", {"start": v(10.18, -9.15) * mm, "end": v(10.14, -9.12) * mm});
            skLineSegment(sketch, "E6334", {"start": v(10.14, -9.12) * mm, "end": v(10.1, -9.08) * mm});
            skLineSegment(sketch, "E6335", {"start": v(10.1, -9.08) * mm, "end": v(10.07, -9.02) * mm});
            skLineSegment(sketch, "E6336", {"start": v(10.07, -9.02) * mm, "end": v(10.03, -9.1) * mm});
            skLineSegment(sketch, "E6337", {"start": v(10.03, -9.1) * mm, "end": v(9.96, -9.18) * mm});
            skLineSegment(sketch, "E6338", {"start": v(9.96, -9.18) * mm, "end": v(9.88, -9.26) * mm});
            skLineSegment(sketch, "E6339", {"start": v(9.88, -9.26) * mm, "end": v(9.8, -9.34) * mm});
            skLineSegment(sketch, "E6340", {"start": v(9.8, -9.34) * mm, "end": v(9.6, -9.48) * mm});
            skLineSegment(sketch, "E6341", {"start": v(9.6, -9.48) * mm, "end": v(9.43, -9.6) * mm});
            skLineSegment(sketch, "E6342", {"start": v(-12.36, -9.5) * mm, "end": v(-12.56, -9.5) * mm});
            skLineSegment(sketch, "E6343", {"start": v(-12.56, -9.5) * mm, "end": v(-12.75, -9.5) * mm});
            skLineSegment(sketch, "E6344", {"start": v(-12.75, -9.5) * mm, "end": v(-12.94, -9.48) * mm});
            skLineSegment(sketch, "E6345", {"start": v(-12.94, -9.48) * mm, "end": v(-13.13, -9.46) * mm});
            skLineSegment(sketch, "E6346", {"start": v(-13.13, -9.46) * mm, "end": v(-13.31, -9.44) * mm});
            skLineSegment(sketch, "E6347", {"start": v(-13.31, -9.44) * mm, "end": v(-13.5, -9.41) * mm});
            skLineSegment(sketch, "E6348", {"start": v(-13.5, -9.41) * mm, "end": v(-13.69, -9.38) * mm});
            skLineSegment(sketch, "E6349", {"start": v(-13.69, -9.38) * mm, "end": v(-13.87, -9.35) * mm});
            skLineSegment(sketch, "E6350", {"start": v(-13.87, -9.35) * mm, "end": v(-13.8, -9.46) * mm});
            skLineSegment(sketch, "E6351", {"start": v(-13.8, -9.46) * mm, "end": v(-13.68, -9.55) * mm});
            skLineSegment(sketch, "E6352", {"start": v(-13.68, -9.55) * mm, "end": v(-13.57, -9.64) * mm});
            skLineSegment(sketch, "E6353", {"start": v(-13.57, -9.64) * mm, "end": v(-13.47, -9.72) * mm});
            skLineSegment(sketch, "E6354", {"start": v(-13.47, -9.72) * mm, "end": v(-13.29, -9.85) * mm});
            skLineSegment(sketch, "E6355", {"start": v(-13.29, -9.85) * mm, "end": v(-13.1, -9.97) * mm});
            skLineSegment(sketch, "E6356", {"start": v(-13.1, -9.97) * mm, "end": v(-12.9, -10.07) * mm});
            skLineSegment(sketch, "E6357", {"start": v(-12.9, -10.07) * mm, "end": v(-12.69, -10.17) * mm});
            skLineSegment(sketch, "E6358", {"start": v(-12.69, -10.17) * mm, "end": v(-12.47, -10.24) * mm});
            skLineSegment(sketch, "E6359", {"start": v(-12.47, -10.24) * mm, "end": v(-12.25, -10.3) * mm});
            skLineSegment(sketch, "E6360", {"start": v(-12.25, -10.3) * mm, "end": v(-12.02, -10.34) * mm});
            skLineSegment(sketch, "E6361", {"start": v(-12.02, -10.34) * mm, "end": v(-11.78, -10.36) * mm});
            skLineSegment(sketch, "E6362", {"start": v(-11.78, -10.36) * mm, "end": v(-11.51, -10.35) * mm});
            skLineSegment(sketch, "E6363", {"start": v(-11.51, -10.35) * mm, "end": v(-11.22, -10.32) * mm});
            skLineSegment(sketch, "E6364", {"start": v(-11.22, -10.32) * mm, "end": v(-10.91, -10.27) * mm});
            skLineSegment(sketch, "E6365", {"start": v(-10.91, -10.27) * mm, "end": v(-10.6, -10.19) * mm});
            skLineSegment(sketch, "E6366", {"start": v(-10.6, -10.19) * mm, "end": v(-10.3, -10.09) * mm});
            skLineSegment(sketch, "E6367", {"start": v(-10.3, -10.09) * mm, "end": v(-10, -9.97) * mm});
            skLineSegment(sketch, "E6368", {"start": v(-10, -9.97) * mm, "end": v(-9.73, -9.83) * mm});
            skLineSegment(sketch, "E6369", {"start": v(-9.73, -9.83) * mm, "end": v(-9.5, -9.68) * mm});
            skLineSegment(sketch, "E6370", {"start": v(-9.5, -9.68) * mm, "end": v(-9.44, -9.61) * mm});
            skLineSegment(sketch, "E6371", {"start": v(-9.44, -9.61) * mm, "end": v(-9.66, -9.43) * mm});
            skLineSegment(sketch, "E6372", {"start": v(-9.66, -9.43) * mm, "end": v(-9.75, -9.37) * mm});
            skLineSegment(sketch, "E6373", {"start": v(-9.75, -9.37) * mm, "end": v(-9.86, -9.27) * mm});
            skLineSegment(sketch, "E6374", {"start": v(-9.86, -9.27) * mm, "end": v(-10.1, -9) * mm});
            skLineSegment(sketch, "E6375", {"start": v(-10.1, -9) * mm, "end": v(-10.1, -9.07) * mm});
            skLineSegment(sketch, "E6376", {"start": v(-10.1, -9.07) * mm, "end": v(-10.1, -9.1) * mm});
            skLineSegment(sketch, "E6377", {"start": v(-10.1, -9.1) * mm, "end": v(-10.12, -9.12) * mm});
            skLineSegment(sketch, "E6378", {"start": v(-10.12, -9.12) * mm, "end": v(-10.19, -9.14) * mm});
            skLineSegment(sketch, "E6379", {"start": v(-10.19, -9.14) * mm, "end": v(-10.3, -9.18) * mm});
            skLineSegment(sketch, "E6380", {"start": v(-10.3, -9.18) * mm, "end": v(-10.49, -9.24) * mm});
            skLineSegment(sketch, "E6381", {"start": v(-10.49, -9.24) * mm, "end": v(-10.72, -9.3) * mm});
            skLineSegment(sketch, "E6382", {"start": v(-10.72, -9.3) * mm, "end": v(-10.95, -9.36) * mm});
            skLineSegment(sketch, "E6383", {"start": v(-10.95, -9.36) * mm, "end": v(-11.18, -9.4) * mm});
            skLineSegment(sketch, "E6384", {"start": v(-11.18, -9.4) * mm, "end": v(-11.4, -9.44) * mm});
            skLineSegment(sketch, "E6385", {"start": v(-11.4, -9.44) * mm, "end": v(-11.63, -9.47) * mm});
            skLineSegment(sketch, "E6386", {"start": v(-11.63, -9.47) * mm, "end": v(-11.86, -9.5) * mm});
            skLineSegment(sketch, "E6387", {"start": v(-11.86, -9.5) * mm, "end": v(-12.1, -9.5) * mm});
            skLineSegment(sketch, "E6388", {"start": v(-12.1, -9.5) * mm, "end": v(-12.36, -9.5) * mm});
            skLineSegment(sketch, "E6389", {"start": v(-2.62, -11.08) * mm, "end": v(-2.53, -11.4) * mm});
            skLineSegment(sketch, "E6390", {"start": v(-2.53, -11.4) * mm, "end": v(-2.37, -11.8) * mm});
            skLineSegment(sketch, "E6391", {"start": v(-2.37, -11.8) * mm, "end": v(-2.18, -12.22) * mm});
            skLineSegment(sketch, "E6392", {"start": v(-2.18, -12.22) * mm, "end": v(-1.95, -12.6) * mm});
            skLineSegment(sketch, "E6393", {"start": v(-1.95, -12.6) * mm, "end": v(-1.72, -12.85) * mm});
            skLineSegment(sketch, "E6394", {"start": v(-1.72, -12.85) * mm, "end": v(-1.49, -12.91) * mm});
            skLineSegment(sketch, "E6395", {"start": v(-1.49, -12.91) * mm, "end": v(-1.29, -12.7) * mm});
            skLineSegment(sketch, "E6396", {"start": v(-1.29, -12.7) * mm, "end": v(-1.13, -12.17) * mm});
            skLineSegment(sketch, "E6397", {"start": v(-1.13, -12.17) * mm, "end": v(-1.08, -11.92) * mm});
            skLineSegment(sketch, "E6398", {"start": v(-1.08, -11.92) * mm, "end": v(-1.04, -11.7) * mm});
            skLineSegment(sketch, "E6399", {"start": v(-1.04, -11.7) * mm, "end": v(-1.04, -11.6) * mm});
            skLineSegment(sketch, "E6400", {"start": v(-1.04, -11.6) * mm, "end": v(-1.04, -11.5) * mm});
            skLineSegment(sketch, "E6401", {"start": v(-1.04, -11.5) * mm, "end": v(-1.06, -11.4) * mm});
            skLineSegment(sketch, "E6402", {"start": v(-1.06, -11.4) * mm, "end": v(-1.1, -11.28) * mm});
            skLineSegment(sketch, "E6403", {"start": v(-1.1, -11.28) * mm, "end": v(-1.18, -11.06) * mm});
            skLineSegment(sketch, "E6404", {"start": v(-1.18, -11.06) * mm, "end": v(-1.24, -10.83) * mm});
            skLineSegment(sketch, "E6405", {"start": v(-1.24, -10.83) * mm, "end": v(-1.29, -10.6) * mm});
            skLineSegment(sketch, "E6406", {"start": v(-1.29, -10.6) * mm, "end": v(-1.32, -10.34) * mm});
            skLineSegment(sketch, "E6407", {"start": v(-1.32, -10.34) * mm, "end": v(-1.35, -10.1) * mm});
            skLineSegment(sketch, "E6408", {"start": v(-1.35, -10.1) * mm, "end": v(-1.36, -9.84) * mm});
            skLineSegment(sketch, "E6409", {"start": v(-1.36, -9.84) * mm, "end": v(-1.37, -9.59) * mm});
            skLineSegment(sketch, "E6410", {"start": v(-1.37, -9.59) * mm, "end": v(-1.38, -9.34) * mm});
            skLineSegment(sketch, "E6411", {"start": v(-1.38, -9.34) * mm, "end": v(-1.49, -9.46) * mm});
            skLineSegment(sketch, "E6412", {"start": v(-1.49, -9.46) * mm, "end": v(-1.58, -9.6) * mm});
            skLineSegment(sketch, "E6413", {"start": v(-1.58, -9.6) * mm, "end": v(-1.65, -9.73) * mm});
            skLineSegment(sketch, "E6414", {"start": v(-1.65, -9.73) * mm, "end": v(-1.7, -9.88) * mm});
            skLineSegment(sketch, "E6415", {"start": v(-1.7, -9.88) * mm, "end": v(-1.8, -10.19) * mm});
            skLineSegment(sketch, "E6416", {"start": v(-1.8, -10.19) * mm, "end": v(-1.88, -10.5) * mm});
            skLineSegment(sketch, "E6417", {"start": v(-1.88, -10.5) * mm, "end": v(-1.93, -10.7) * mm});
            skLineSegment(sketch, "E6418", {"start": v(-1.93, -10.7) * mm, "end": v(-1.98, -10.86) * mm});
            skLineSegment(sketch, "E6419", {"start": v(-1.98, -10.86) * mm, "end": v(-2.04, -11) * mm});
            skLineSegment(sketch, "E6420", {"start": v(-2.04, -11) * mm, "end": v(-2.12, -11.12) * mm});
            skLineSegment(sketch, "E6421", {"start": v(-2.12, -11.12) * mm, "end": v(-2.2, -11.2) * mm});
            skLineSegment(sketch, "E6422", {"start": v(-2.2, -11.2) * mm, "end": v(-2.32, -11.21) * mm});
            skLineSegment(sketch, "E6423", {"start": v(-2.32, -11.21) * mm, "end": v(-2.45, -11.18) * mm});
            skLineSegment(sketch, "E6424", {"start": v(-2.45, -11.18) * mm, "end": v(-2.62, -11.08) * mm});
            skLineSegment(sketch, "E6425", {"start": v(-12.83, -11.44) * mm, "end": v(-12.48, -11.46) * mm});
            skLineSegment(sketch, "E6426", {"start": v(-12.48, -11.46) * mm, "end": v(-12.15, -11.48) * mm});
            skLineSegment(sketch, "E6427", {"start": v(-12.15, -11.48) * mm, "end": v(-11.83, -11.49) * mm});
            skLineSegment(sketch, "E6428", {"start": v(-11.83, -11.49) * mm, "end": v(-11.51, -11.48) * mm});
            skLineSegment(sketch, "E6429", {"start": v(-11.51, -11.48) * mm, "end": v(-11.2, -11.46) * mm});
            skLineSegment(sketch, "E6430", {"start": v(-11.2, -11.46) * mm, "end": v(-10.87, -11.42) * mm});
            skLineSegment(sketch, "E6431", {"start": v(-10.87, -11.42) * mm, "end": v(-10.53, -11.35) * mm});
            skLineSegment(sketch, "E6432", {"start": v(-10.53, -11.35) * mm, "end": v(-10.16, -11.27) * mm});
            skLineSegment(sketch, "E6433", {"start": v(-10.16, -11.27) * mm, "end": v(-10, -11.22) * mm});
            skLineSegment(sketch, "E6434", {"start": v(-10, -11.22) * mm, "end": v(-9.79, -11.16) * mm});
            skLineSegment(sketch, "E6435", {"start": v(-9.79, -11.16) * mm, "end": v(-9.55, -11.1) * mm});
            skLineSegment(sketch, "E6436", {"start": v(-9.55, -11.1) * mm, "end": v(-9.3, -11.01) * mm});
            skLineSegment(sketch, "E6437", {"start": v(-9.3, -11.01) * mm, "end": v(-9.06, -10.93) * mm});
            skLineSegment(sketch, "E6438", {"start": v(-9.06, -10.93) * mm, "end": v(-8.85, -10.85) * mm});
            skLineSegment(sketch, "E6439", {"start": v(-8.85, -10.85) * mm, "end": v(-8.67, -10.77) * mm});
            skLineSegment(sketch, "E6440", {"start": v(-8.67, -10.77) * mm, "end": v(-8.54, -10.7) * mm});
            skLineSegment(sketch, "E6441", {"start": v(-8.54, -10.7) * mm, "end": v(-8.63, -10.6) * mm});
            skLineSegment(sketch, "E6442", {"start": v(-8.63, -10.6) * mm, "end": v(-8.77, -10.47) * mm});
            skLineSegment(sketch, "E6443", {"start": v(-8.77, -10.47) * mm, "end": v(-8.85, -10.4) * mm});
            skLineSegment(sketch, "E6444", {"start": v(-8.85, -10.4) * mm, "end": v(-8.93, -10.31) * mm});
            skLineSegment(sketch, "E6445", {"start": v(-8.93, -10.31) * mm, "end": v(-9.02, -10.21) * mm});
            skLineSegment(sketch, "E6446", {"start": v(-9.02, -10.21) * mm, "end": v(-9.1, -10.1) * mm});
            skLineSegment(sketch, "E6447", {"start": v(-9.1, -10.1) * mm, "end": v(-9.14, -10.04) * mm});
            skLineSegment(sketch, "E6448", {"start": v(-9.14, -10.04) * mm, "end": v(-9.18, -9.99) * mm});
            skLineSegment(sketch, "E6449", {"start": v(-9.18, -9.99) * mm, "end": v(-9.22, -9.94) * mm});
            skLineSegment(sketch, "E6450", {"start": v(-9.22, -9.94) * mm, "end": v(-9.28, -9.88) * mm});
            skLineSegment(sketch, "E6451", {"start": v(-9.28, -9.88) * mm, "end": v(-9.48, -9.99) * mm});
            skLineSegment(sketch, "E6452", {"start": v(-9.48, -9.99) * mm, "end": v(-9.68, -10.1) * mm});
            skLineSegment(sketch, "E6453", {"start": v(-9.68, -10.1) * mm, "end": v(-9.88, -10.21) * mm});
            skLineSegment(sketch, "E6454", {"start": v(-9.88, -10.21) * mm, "end": v(-10.09, -10.32) * mm});
            skLineSegment(sketch, "E6455", {"start": v(-10.09, -10.32) * mm, "end": v(-10.3, -10.43) * mm});
            skLineSegment(sketch, "E6456", {"start": v(-10.3, -10.43) * mm, "end": v(-10.5, -10.54) * mm});
            skLineSegment(sketch, "E6457", {"start": v(-10.5, -10.54) * mm, "end": v(-10.72, -10.64) * mm});
            skLineSegment(sketch, "E6458", {"start": v(-10.72, -10.64) * mm, "end": v(-10.95, -10.74) * mm});
            skLineSegment(sketch, "E6459", {"start": v(-10.95, -10.74) * mm, "end": v(-11.87, -11.1) * mm});
            skLineSegment(sketch, "E6460", {"start": v(-11.87, -11.1) * mm, "end": v(-12.1, -11.2) * mm});
            skLineSegment(sketch, "E6461", {"start": v(-12.1, -11.2) * mm, "end": v(-12.37, -11.27) * mm});
            skLineSegment(sketch, "E6462", {"start": v(-12.37, -11.27) * mm, "end": v(-12.61, -11.35) * mm});
            skLineSegment(sketch, "E6463", {"start": v(-12.61, -11.35) * mm, "end": v(-12.83, -11.44) * mm});
            skLineSegment(sketch, "E6464", {"start": v(8.53, -10.7) * mm, "end": v(9, -10.9) * mm});
            skLineSegment(sketch, "E6465", {"start": v(9, -10.9) * mm, "end": v(9.51, -11.07) * mm});
            skLineSegment(sketch, "E6466", {"start": v(9.51, -11.07) * mm, "end": v(10.04, -11.23) * mm});
            skLineSegment(sketch, "E6467", {"start": v(10.04, -11.23) * mm, "end": v(10.58, -11.35) * mm});
            skLineSegment(sketch, "E6468", {"start": v(10.58, -11.35) * mm, "end": v(11.14, -11.44) * mm});
            skLineSegment(sketch, "E6469", {"start": v(11.14, -11.44) * mm, "end": v(11.7, -11.5) * mm});
            skLineSegment(sketch, "E6470", {"start": v(11.7, -11.5) * mm, "end": v(12.26, -11.5) * mm});
            skLineSegment(sketch, "E6471", {"start": v(12.26, -11.5) * mm, "end": v(12.82, -11.44) * mm});
            skLineSegment(sketch, "E6472", {"start": v(12.82, -11.44) * mm, "end": v(12.63, -11.36) * mm});
            skLineSegment(sketch, "E6473", {"start": v(12.63, -11.36) * mm, "end": v(12.37, -11.27) * mm});
            skLineSegment(sketch, "E6474", {"start": v(12.37, -11.27) * mm, "end": v(12.1, -11.19) * mm});
            skLineSegment(sketch, "E6475", {"start": v(12.1, -11.19) * mm, "end": v(11.87, -11.1) * mm});
            skLineSegment(sketch, "E6476", {"start": v(11.87, -11.1) * mm, "end": v(11.55, -10.98) * mm});
            skLineSegment(sketch, "E6477", {"start": v(11.55, -10.98) * mm, "end": v(11.27, -10.87) * mm});
            skLineSegment(sketch, "E6478", {"start": v(11.27, -10.87) * mm, "end": v(11, -10.76) * mm});
            skLineSegment(sketch, "E6479", {"start": v(11, -10.76) * mm, "end": v(10.75, -10.65) * mm});
            skLineSegment(sketch, "E6480", {"start": v(10.75, -10.65) * mm, "end": v(10.5, -10.53) * mm});
            skLineSegment(sketch, "E6481", {"start": v(10.5, -10.53) * mm, "end": v(10.23, -10.4) * mm});
            skLineSegment(sketch, "E6482", {"start": v(10.23, -10.4) * mm, "end": v(9.96, -10.26) * mm});
            skLineSegment(sketch, "E6483", {"start": v(9.96, -10.26) * mm, "end": v(9.67, -10.1) * mm});
            skLineSegment(sketch, "E6484", {"start": v(9.67, -10.1) * mm, "end": v(9.57, -10.04) * mm});
            skLineSegment(sketch, "E6485", {"start": v(9.57, -10.04) * mm, "end": v(9.46, -9.98) * mm});
            skLineSegment(sketch, "E6486", {"start": v(9.46, -9.98) * mm, "end": v(9.35, -9.92) * mm});
            skLineSegment(sketch, "E6487", {"start": v(9.35, -9.92) * mm, "end": v(9.24, -9.88) * mm});
            skLineSegment(sketch, "E6488", {"start": v(9.24, -9.88) * mm, "end": v(9.17, -10) * mm});
            skLineSegment(sketch, "E6489", {"start": v(9.17, -10) * mm, "end": v(9.1, -10.1) * mm});
            skLineSegment(sketch, "E6490", {"start": v(9.1, -10.1) * mm, "end": v(9.02, -10.2) * mm});
            skLineSegment(sketch, "E6491", {"start": v(9.02, -10.2) * mm, "end": v(8.93, -10.31) * mm});
            skLineSegment(sketch, "E6492", {"start": v(8.93, -10.31) * mm, "end": v(8.83, -10.43) * mm});
            skLineSegment(sketch, "E6493", {"start": v(8.83, -10.43) * mm, "end": v(8.72, -10.52) * mm});
            skLineSegment(sketch, "E6494", {"start": v(8.72, -10.52) * mm, "end": v(8.62, -10.6) * mm});
            skLineSegment(sketch, "E6495", {"start": v(8.62, -10.6) * mm, "end": v(8.53, -10.7) * mm});
            skLineSegment(sketch, "E6496", {"start": v(2.02, -9.08) * mm, "end": v(1.88, -9.22) * mm});
            skLineSegment(sketch, "E6497", {"start": v(1.88, -9.22) * mm, "end": v(1.82, -9.29) * mm});
            skLineSegment(sketch, "E6498", {"start": v(1.82, -9.29) * mm, "end": v(1.8, -9.33) * mm});
            skLineSegment(sketch, "E6499", {"start": v(1.8, -9.33) * mm, "end": v(1.73, -9.4) * mm});
            skLineSegment(sketch, "E6500", {"start": v(1.73, -9.4) * mm, "end": v(1.7, -9.39) * mm});
            skLineSegment(sketch, "E6501", {"start": v(1.7, -9.39) * mm, "end": v(1.5, -8.92) * mm});
            skLineSegment(sketch, "E6502", {"start": v(1.5, -8.92) * mm, "end": v(1.46, -8.75) * mm});
            skLineSegment(sketch, "E6503", {"start": v(1.46, -8.75) * mm, "end": v(1.44, -8.62) * mm});
            skLineSegment(sketch, "E6504", {"start": v(1.44, -8.62) * mm, "end": v(1.42, -8.48) * mm});
            skLineSegment(sketch, "E6505", {"start": v(1.42, -8.48) * mm, "end": v(1.42, -8.3) * mm});
            skLineSegment(sketch, "E6506", {"start": v(1.42, -8.3) * mm, "end": v(1.3, -8.38) * mm});
            skLineSegment(sketch, "E6507", {"start": v(1.3, -8.38) * mm, "end": v(1.17, -8.47) * mm});
            skLineSegment(sketch, "E6508", {"start": v(1.17, -8.47) * mm, "end": v(1.04, -8.58) * mm});
            skLineSegment(sketch, "E6509", {"start": v(1.04, -8.58) * mm, "end": v(0.9, -8.7) * mm});
            skLineSegment(sketch, "E6510", {"start": v(0.9, -8.7) * mm, "end": v(0.78, -8.81) * mm});
            skLineSegment(sketch, "E6511", {"start": v(0.78, -8.81) * mm, "end": v(0.66, -8.93) * mm});
            skLineSegment(sketch, "E6512", {"start": v(0.66, -8.93) * mm, "end": v(0.56, -9.05) * mm});
            skLineSegment(sketch, "E6513", {"start": v(0.56, -9.05) * mm, "end": v(0.48, -9.16) * mm});
            skLineSegment(sketch, "E6514", {"start": v(0.48, -9.16) * mm, "end": v(0.45, -9.23) * mm});
            skLineSegment(sketch, "E6515", {"start": v(0.45, -9.23) * mm, "end": v(0.45, -9.32) * mm});
            skLineSegment(sketch, "E6516", {"start": v(0.45, -9.32) * mm, "end": v(0.46, -9.4) * mm});
            skLineSegment(sketch, "E6517", {"start": v(0.46, -9.4) * mm, "end": v(0.48, -9.5) * mm});
            skLineSegment(sketch, "E6518", {"start": v(0.48, -9.5) * mm, "end": v(0.55, -9.68) * mm});
            skLineSegment(sketch, "E6519", {"start": v(0.55, -9.68) * mm, "end": v(0.62, -9.84) * mm});
            skLineSegment(sketch, "E6520", {"start": v(0.62, -9.84) * mm, "end": v(0.7, -10.07) * mm});
            skLineSegment(sketch, "E6521", {"start": v(0.7, -10.07) * mm, "end": v(0.78, -10.36) * mm});
            skLineSegment(sketch, "E6522", {"start": v(0.78, -10.36) * mm, "end": v(0.89, -10.65) * mm});
            skLineSegment(sketch, "E6523", {"start": v(0.89, -10.65) * mm, "end": v(1, -10.9) * mm});
            skLineSegment(sketch, "E6524", {"start": v(1, -10.9) * mm, "end": v(1.14, -11.08) * mm});
            skLineSegment(sketch, "E6525", {"start": v(1.14, -11.08) * mm, "end": v(1.3, -11.12) * mm});
            skLineSegment(sketch, "E6526", {"start": v(1.3, -11.12) * mm, "end": v(1.47, -10.97) * mm});
            skLineSegment(sketch, "E6527", {"start": v(1.47, -10.97) * mm, "end": v(1.67, -10.6) * mm});
            skLineSegment(sketch, "E6528", {"start": v(1.67, -10.6) * mm, "end": v(2.02, -9.08) * mm});
            skLineSegment(sketch, "E6529", {"start": v(1.27, -11.45) * mm, "end": v(1.28, -11.6) * mm});
            skLineSegment(sketch, "E6530", {"start": v(1.28, -11.6) * mm, "end": v(1.29, -11.75) * mm});
            skLineSegment(sketch, "E6531", {"start": v(1.29, -11.75) * mm, "end": v(1.3, -11.9) * mm});
            skLineSegment(sketch, "E6532", {"start": v(1.3, -11.9) * mm, "end": v(1.33, -12.04) * mm});
            skLineSegment(sketch, "E6533", {"start": v(1.33, -12.04) * mm, "end": v(1.35, -12.19) * mm});
            skLineSegment(sketch, "E6534", {"start": v(1.35, -12.19) * mm, "end": v(1.4, -12.33) * mm});
            skLineSegment(sketch, "E6535", {"start": v(1.4, -12.33) * mm, "end": v(1.43, -12.47) * mm});
            skLineSegment(sketch, "E6536", {"start": v(1.43, -12.47) * mm, "end": v(1.49, -12.6) * mm});
            skLineSegment(sketch, "E6537", {"start": v(1.49, -12.6) * mm, "end": v(1.67, -12.88) * mm});
            skLineSegment(sketch, "E6538", {"start": v(1.67, -12.88) * mm, "end": v(1.86, -12.88) * mm});
            skLineSegment(sketch, "E6539", {"start": v(1.86, -12.88) * mm, "end": v(2.06, -12.67) * mm});
            skLineSegment(sketch, "E6540", {"start": v(2.06, -12.67) * mm, "end": v(2.26, -12.34) * mm});
            skLineSegment(sketch, "E6541", {"start": v(2.26, -12.34) * mm, "end": v(2.43, -11.95) * mm});
            skLineSegment(sketch, "E6542", {"start": v(2.43, -11.95) * mm, "end": v(2.57, -11.56) * mm});
            skLineSegment(sketch, "E6543", {"start": v(2.57, -11.56) * mm, "end": v(2.67, -11.27) * mm});
            skLineSegment(sketch, "E6544", {"start": v(2.67, -11.27) * mm, "end": v(2.72, -11.12) * mm});
            skLineSegment(sketch, "E6545", {"start": v(2.72, -11.12) * mm, "end": v(2.61, -11) * mm});
            skLineSegment(sketch, "E6546", {"start": v(2.61, -11) * mm, "end": v(2.5, -10.85) * mm});
            skLineSegment(sketch, "E6547", {"start": v(2.5, -10.85) * mm, "end": v(2.45, -10.74) * mm});
            skLineSegment(sketch, "E6548", {"start": v(2.45, -10.74) * mm, "end": v(2.42, -10.64) * mm});
            skLineSegment(sketch, "E6549", {"start": v(2.42, -10.64) * mm, "end": v(2.4, -10.54) * mm});
            skLineSegment(sketch, "E6550", {"start": v(2.4, -10.54) * mm, "end": v(2.38, -10.41) * mm});
            skLineSegment(sketch, "E6551", {"start": v(2.38, -10.41) * mm, "end": v(2.35, -10.2) * mm});
            skLineSegment(sketch, "E6552", {"start": v(2.35, -10.2) * mm, "end": v(2.32, -9.96) * mm});
            skLineSegment(sketch, "E6553", {"start": v(2.32, -9.96) * mm, "end": v(2.3, -9.84) * mm});
            skLineSegment(sketch, "E6554", {"start": v(2.3, -9.84) * mm, "end": v(2.26, -9.73) * mm});
            skLineSegment(sketch, "E6555", {"start": v(2.26, -9.73) * mm, "end": v(2.23, -9.63) * mm});
            skLineSegment(sketch, "E6556", {"start": v(2.23, -9.63) * mm, "end": v(2.19, -9.55) * mm});
            skLineSegment(sketch, "E6557", {"start": v(2.19, -9.55) * mm, "end": v(2.15, -9.74) * mm});
            skLineSegment(sketch, "E6558", {"start": v(2.15, -9.74) * mm, "end": v(2.1, -9.95) * mm});
            skLineSegment(sketch, "E6559", {"start": v(2.1, -9.95) * mm, "end": v(2.05, -10.17) * mm});
            skLineSegment(sketch, "E6560", {"start": v(2.05, -10.17) * mm, "end": v(2, -10.39) * mm});
            skLineSegment(sketch, "E6561", {"start": v(2, -10.39) * mm, "end": v(1.93, -10.6) * mm});
            skLineSegment(sketch, "E6562", {"start": v(1.93, -10.6) * mm, "end": v(1.86, -10.8) * mm});
            skLineSegment(sketch, "E6563", {"start": v(1.86, -10.8) * mm, "end": v(1.77, -10.98) * mm});
            skLineSegment(sketch, "E6564", {"start": v(1.77, -10.98) * mm, "end": v(1.67, -11.13) * mm});
            skLineSegment(sketch, "E6565", {"start": v(1.67, -11.13) * mm, "end": v(1.56, -11.25) * mm});
            skLineSegment(sketch, "E6566", {"start": v(1.56, -11.25) * mm, "end": v(1.49, -11.31) * mm});
            skLineSegment(sketch, "E6567", {"start": v(1.49, -11.31) * mm, "end": v(1.4, -11.37) * mm});
            skLineSegment(sketch, "E6568", {"start": v(1.4, -11.37) * mm, "end": v(1.27, -11.45) * mm});
            skLineSegment(sketch, "E6569", {"start": v(-9.73, 1.72) * mm, "end": v(-9.79, 1.9) * mm});
            skLineSegment(sketch, "E6570", {"start": v(-9.79, 1.9) * mm, "end": v(-9.85, 2.07) * mm});
            skLineSegment(sketch, "E6571", {"start": v(-9.85, 2.07) * mm, "end": v(-9.88, 2.16) * mm});
            skLineSegment(sketch, "E6572", {"start": v(-9.88, 2.16) * mm, "end": v(-9.9, 2.25) * mm});
            skLineSegment(sketch, "E6573", {"start": v(-9.9, 2.25) * mm, "end": v(-9.92, 2.35) * mm});
            skLineSegment(sketch, "E6574", {"start": v(-9.92, 2.35) * mm, "end": v(-9.93, 2.46) * mm});
            skLineSegment(sketch, "E6575", {"start": v(-9.93, 2.46) * mm, "end": v(-9.8, 2.34) * mm});
            skLineSegment(sketch, "E6576", {"start": v(-9.8, 2.34) * mm, "end": v(-9.62, 2.2) * mm});
            skLineSegment(sketch, "E6577", {"start": v(-9.62, 2.2) * mm, "end": v(-9.42, 2.04) * mm});
            skLineSegment(sketch, "E6578", {"start": v(-9.42, 2.04) * mm, "end": v(-9.2, 1.88) * mm});
            skLineSegment(sketch, "E6579", {"start": v(-9.2, 1.88) * mm, "end": v(-8.98, 1.73) * mm});
            skLineSegment(sketch, "E6580", {"start": v(-8.98, 1.73) * mm, "end": v(-8.78, 1.6) * mm});
            skLineSegment(sketch, "E6581", {"start": v(-8.78, 1.6) * mm, "end": v(-8.6, 1.5) * mm});
            skLineSegment(sketch, "E6582", {"start": v(-8.6, 1.5) * mm, "end": v(-8.46, 1.43) * mm});
            skLineSegment(sketch, "E6583", {"start": v(-8.46, 1.43) * mm, "end": v(-8.52, 1.5) * mm});
            skLineSegment(sketch, "E6584", {"start": v(-8.52, 1.5) * mm, "end": v(-8.59, 1.58) * mm});
            skLineSegment(sketch, "E6585", {"start": v(-8.59, 1.58) * mm, "end": v(-8.67, 1.67) * mm});
            skLineSegment(sketch, "E6586", {"start": v(-8.67, 1.67) * mm, "end": v(-8.78, 1.78) * mm});
            skLineSegment(sketch, "E6587", {"start": v(-8.78, 1.78) * mm, "end": v(-8.89, 1.9) * mm});
            skLineSegment(sketch, "E6588", {"start": v(-8.89, 1.9) * mm, "end": v(-9, 2.07) * mm});
            skLineSegment(sketch, "E6589", {"start": v(-9, 2.07) * mm, "end": v(-9.14, 2.28) * mm});
            skLineSegment(sketch, "E6590", {"start": v(-9.14, 2.28) * mm, "end": v(-9.27, 2.53) * mm});
            skLineSegment(sketch, "E6591", {"start": v(-9.27, 2.53) * mm, "end": v(-9.36, 2.75) * mm});
            skLineSegment(sketch, "E6592", {"start": v(-9.36, 2.75) * mm, "end": v(-9.4, 2.89) * mm});
            skLineSegment(sketch, "E6593", {"start": v(-9.4, 2.89) * mm, "end": v(-9.41, 2.97) * mm});
            skLineSegment(sketch, "E6594", {"start": v(-9.41, 2.97) * mm, "end": v(-9.43, 3.02) * mm});
            skLineSegment(sketch, "E6595", {"start": v(-9.43, 3.02) * mm, "end": v(-9.48, 3.08) * mm});
            skLineSegment(sketch, "E6596", {"start": v(-9.48, 3.08) * mm, "end": v(-9.58, 3.16) * mm});
            skLineSegment(sketch, "E6597", {"start": v(-9.58, 3.16) * mm, "end": v(-9.78, 3.32) * mm});
            skLineSegment(sketch, "E6598", {"start": v(-9.78, 3.32) * mm, "end": v(-10.1, 3.57) * mm});
            skLineSegment(sketch, "E6599", {"start": v(-10.1, 3.57) * mm, "end": v(-10.28, 3.7) * mm});
            skLineSegment(sketch, "E6600", {"start": v(-10.28, 3.7) * mm, "end": v(-10.45, 3.85) * mm});
            skLineSegment(sketch, "E6601", {"start": v(-10.45, 3.85) * mm, "end": v(-10.63, 3.98) * mm});
            skLineSegment(sketch, "E6602", {"start": v(-10.63, 3.98) * mm, "end": v(-10.81, 4.1) * mm});
            skLineSegment(sketch, "E6603", {"start": v(-10.81, 4.1) * mm, "end": v(-10.8, 3.9) * mm});
            skLineSegment(sketch, "E6604", {"start": v(-10.8, 3.9) * mm, "end": v(-10.78, 3.72) * mm});
            skLineSegment(sketch, "E6605", {"start": v(-10.78, 3.72) * mm, "end": v(-10.75, 3.55) * mm});
            skLineSegment(sketch, "E6606", {"start": v(-10.75, 3.55) * mm, "end": v(-10.7, 3.38) * mm});
            skLineSegment(sketch, "E6607", {"start": v(-10.7, 3.38) * mm, "end": v(-10.66, 3.22) * mm});
            skLineSegment(sketch, "E6608", {"start": v(-10.66, 3.22) * mm, "end": v(-10.6, 3.06) * mm});
            skLineSegment(sketch, "E6609", {"start": v(-10.6, 3.06) * mm, "end": v(-10.53, 2.9) * mm});
            skLineSegment(sketch, "E6610", {"start": v(-10.53, 2.9) * mm, "end": v(-10.46, 2.75) * mm});
            skLineSegment(sketch, "E6611", {"start": v(-10.46, 2.75) * mm, "end": v(-10.39, 2.63) * mm});
            skLineSegment(sketch, "E6612", {"start": v(-10.39, 2.63) * mm, "end": v(-10.3, 2.5) * mm});
            skLineSegment(sketch, "E6613", {"start": v(-10.3, 2.5) * mm, "end": v(-10.21, 2.35) * mm});
            skLineSegment(sketch, "E6614", {"start": v(-10.21, 2.35) * mm, "end": v(-10.11, 2.2) * mm});
            skLineSegment(sketch, "E6615", {"start": v(-10.11, 2.2) * mm, "end": v(-10, 2.05) * mm});
            skLineSegment(sketch, "E6616", {"start": v(-10, 2.05) * mm, "end": v(-9.9, 1.92) * mm});
            skLineSegment(sketch, "E6617", {"start": v(-9.9, 1.92) * mm, "end": v(-9.81, 1.81) * mm});
            skLineSegment(sketch, "E6618", {"start": v(-9.81, 1.81) * mm, "end": v(-9.73, 1.72) * mm});
            skLineSegment(sketch, "E6619", {"start": v(8.5, 1.46) * mm, "end": v(8.61, 1.5) * mm});
            skLineSegment(sketch, "E6620", {"start": v(8.61, 1.5) * mm, "end": v(8.72, 1.55) * mm});
            skLineSegment(sketch, "E6621", {"start": v(8.72, 1.55) * mm, "end": v(8.81, 1.6) * mm});
            skLineSegment(sketch, "E6622", {"start": v(8.81, 1.6) * mm, "end": v(8.9, 1.67) * mm});
            skLineSegment(sketch, "E6623", {"start": v(8.9, 1.67) * mm, "end": v(9.07, 1.8) * mm});
            skLineSegment(sketch, "E6624", {"start": v(9.07, 1.8) * mm, "end": v(9.24, 1.93) * mm});
            skLineSegment(sketch, "E6625", {"start": v(9.24, 1.93) * mm, "end": v(9.43, 2.07) * mm});
            skLineSegment(sketch, "E6626", {"start": v(9.43, 2.07) * mm, "end": v(9.62, 2.22) * mm});
            skLineSegment(sketch, "E6627", {"start": v(9.62, 2.22) * mm, "end": v(9.8, 2.36) * mm});
            skLineSegment(sketch, "E6628", {"start": v(9.8, 2.36) * mm, "end": v(9.95, 2.45) * mm});
            skLineSegment(sketch, "E6629", {"start": v(9.95, 2.45) * mm, "end": v(9.74, 1.72) * mm});
            skLineSegment(sketch, "E6630", {"start": v(9.74, 1.72) * mm, "end": v(9.8, 1.82) * mm});
            skLineSegment(sketch, "E6631", {"start": v(9.8, 1.82) * mm, "end": v(9.9, 1.94) * mm});
            skLineSegment(sketch, "E6632", {"start": v(9.9, 1.94) * mm, "end": v(10, 2.07) * mm});
            skLineSegment(sketch, "E6633", {"start": v(10, 2.07) * mm, "end": v(10.1, 2.19) * mm});
            skLineSegment(sketch, "E6634", {"start": v(10.1, 2.19) * mm, "end": v(10.24, 2.41) * mm});
            skLineSegment(sketch, "E6635", {"start": v(10.24, 2.41) * mm, "end": v(10.38, 2.63) * mm});
            skLineSegment(sketch, "E6636", {"start": v(10.38, 2.63) * mm, "end": v(10.5, 2.85) * mm});
            skLineSegment(sketch, "E6637", {"start": v(10.5, 2.85) * mm, "end": v(10.6, 3.07) * mm});
            skLineSegment(sketch, "E6638", {"start": v(10.6, 3.07) * mm, "end": v(10.7, 3.3) * mm});
            skLineSegment(sketch, "E6639", {"start": v(10.7, 3.3) * mm, "end": v(10.76, 3.56) * mm});
            skLineSegment(sketch, "E6640", {"start": v(10.76, 3.56) * mm, "end": v(10.8, 3.83) * mm});
            skLineSegment(sketch, "E6641", {"start": v(10.8, 3.83) * mm, "end": v(10.83, 4.11) * mm});
            skLineSegment(sketch, "E6642", {"start": v(10.83, 4.11) * mm, "end": v(9.78, 3.3) * mm});
            skLineSegment(sketch, "E6643", {"start": v(9.78, 3.3) * mm, "end": v(9.68, 3.24) * mm});
            skLineSegment(sketch, "E6644", {"start": v(9.68, 3.24) * mm, "end": v(9.59, 3.18) * mm});
            skLineSegment(sketch, "E6645", {"start": v(9.59, 3.18) * mm, "end": v(9.55, 3.15) * mm});
            skLineSegment(sketch, "E6646", {"start": v(9.55, 3.15) * mm, "end": v(9.5, 3.11) * mm});
            skLineSegment(sketch, "E6647", {"start": v(9.5, 3.11) * mm, "end": v(9.47, 3.07) * mm});
            skLineSegment(sketch, "E6648", {"start": v(9.47, 3.07) * mm, "end": v(9.44, 3.02) * mm});
            skLineSegment(sketch, "E6649", {"start": v(9.44, 3.02) * mm, "end": v(9.31, 2.7) * mm});
            skLineSegment(sketch, "E6650", {"start": v(9.31, 2.7) * mm, "end": v(9.17, 2.37) * mm});
            skLineSegment(sketch, "E6651", {"start": v(9.17, 2.37) * mm, "end": v(9.08, 2.19) * mm});
            skLineSegment(sketch, "E6652", {"start": v(9.08, 2.19) * mm, "end": v(8.97, 2.01) * mm});
            skLineSegment(sketch, "E6653", {"start": v(8.97, 2.01) * mm, "end": v(8.84, 1.84) * mm});
            skLineSegment(sketch, "E6654", {"start": v(8.84, 1.84) * mm, "end": v(8.67, 1.66) * mm});
            skLineSegment(sketch, "E6655", {"start": v(8.67, 1.66) * mm, "end": v(8.5, 1.46) * mm});
            skLineSegment(sketch, "E6656", {"start": v(-22.5, 6.8) * mm, "end": v(-22.47, 6.82) * mm});
            skLineSegment(sketch, "E6657", {"start": v(-22.47, 6.82) * mm, "end": v(-22.45, 6.85) * mm});
            skLineSegment(sketch, "E6658", {"start": v(-22.45, 6.85) * mm, "end": v(-22.42, 6.87) * mm});
            skLineSegment(sketch, "E6659", {"start": v(-22.42, 6.87) * mm, "end": v(-22.37, 6.9) * mm});
            skLineSegment(sketch, "E6660", {"start": v(-22.37, 6.9) * mm, "end": v(-22.3, 6.92) * mm});
            skLineSegment(sketch, "E6661", {"start": v(-22.3, 6.92) * mm, "end": v(-22.28, 6.93) * mm});
            skLineSegment(sketch, "E6662", {"start": v(-22.28, 6.93) * mm, "end": v(-22.27, 6.92) * mm});
            skLineSegment(sketch, "E6663", {"start": v(-22.27, 6.92) * mm, "end": v(-22.2, 6.9) * mm});
            skLineSegment(sketch, "E6664", {"start": v(-22.2, 6.9) * mm, "end": v(-22.35, 7.07) * mm});
            skLineSegment(sketch, "E6665", {"start": v(-22.35, 7.07) * mm, "end": v(-22.54, 7.26) * mm});
            skLineSegment(sketch, "E6666", {"start": v(-22.54, 7.26) * mm, "end": v(-22.64, 7.37) * mm});
            skLineSegment(sketch, "E6667", {"start": v(-22.64, 7.37) * mm, "end": v(-22.73, 7.49) * mm});
            skLineSegment(sketch, "E6668", {"start": v(-22.73, 7.49) * mm, "end": v(-22.82, 7.62) * mm});
            skLineSegment(sketch, "E6669", {"start": v(-22.82, 7.62) * mm, "end": v(-22.9, 7.77) * mm});
            skLineSegment(sketch, "E6670", {"start": v(-22.9, 7.77) * mm, "end": v(-22.8, 7.73) * mm});
            skLineSegment(sketch, "E6671", {"start": v(-22.8, 7.73) * mm, "end": v(-22.7, 7.68) * mm});
            skLineSegment(sketch, "E6672", {"start": v(-22.7, 7.68) * mm, "end": v(-22.57, 7.6) * mm});
            skLineSegment(sketch, "E6673", {"start": v(-22.57, 7.6) * mm, "end": v(-22.45, 7.53) * mm});
            skLineSegment(sketch, "E6674", {"start": v(-22.45, 7.53) * mm, "end": v(-22.2, 7.37) * mm});
            skLineSegment(sketch, "E6675", {"start": v(-22.2, 7.37) * mm, "end": v(-22, 7.22) * mm});
            skLineSegment(sketch, "E6676", {"start": v(-22, 7.22) * mm, "end": v(-21.81, 7.12) * mm});
            skLineSegment(sketch, "E6677", {"start": v(-21.81, 7.12) * mm, "end": v(-21.54, 6.98) * mm});
            skLineSegment(sketch, "E6678", {"start": v(-21.54, 6.98) * mm, "end": v(-21.26, 6.85) * mm});
            skLineSegment(sketch, "E6679", {"start": v(-21.26, 6.85) * mm, "end": v(-21.06, 6.76) * mm});
            skLineSegment(sketch, "E6680", {"start": v(-21.06, 6.76) * mm, "end": v(-21.04, 6.84) * mm});
            skLineSegment(sketch, "E6681", {"start": v(-21.04, 6.84) * mm, "end": v(-21.02, 6.88) * mm});
            skLineSegment(sketch, "E6682", {"start": v(-21.02, 6.88) * mm, "end": v(-20.98, 6.92) * mm});
            skLineSegment(sketch, "E6683", {"start": v(-20.98, 6.92) * mm, "end": v(-20.9, 7) * mm});
            skLineSegment(sketch, "E6684", {"start": v(-20.9, 7) * mm, "end": v(-20.86, 7.06) * mm});
            skLineSegment(sketch, "E6685", {"start": v(-20.86, 7.06) * mm, "end": v(-20.84, 7.08) * mm});
            skLineSegment(sketch, "E6686", {"start": v(-20.84, 7.08) * mm, "end": v(-20.82, 7.1) * mm});
            skLineSegment(sketch, "E6687", {"start": v(-20.82, 7.1) * mm, "end": v(-21.12, 7.26) * mm});
            skLineSegment(sketch, "E6688", {"start": v(-21.12, 7.26) * mm, "end": v(-21.37, 7.4) * mm});
            skLineSegment(sketch, "E6689", {"start": v(-21.37, 7.4) * mm, "end": v(-21.63, 7.53) * mm});
            skLineSegment(sketch, "E6690", {"start": v(-21.63, 7.53) * mm, "end": v(-21.93, 7.67) * mm});
            skLineSegment(sketch, "E6691", {"start": v(-21.93, 7.67) * mm, "end": v(-23.02, 8.28) * mm});
            skLineSegment(sketch, "E6692", {"start": v(-23.02, 8.28) * mm, "end": v(-23.18, 8.42) * mm});
            skLineSegment(sketch, "E6693", {"start": v(-23.18, 8.42) * mm, "end": v(-23.36, 8.52) * mm});
            skLineSegment(sketch, "E6694", {"start": v(-23.36, 8.52) * mm, "end": v(-23.74, 8.71) * mm});
            skLineSegment(sketch, "E6695", {"start": v(-23.74, 8.71) * mm, "end": v(-23.68, 8.57) * mm});
            skLineSegment(sketch, "E6696", {"start": v(-23.68, 8.57) * mm, "end": v(-23.63, 8.45) * mm});
            skLineSegment(sketch, "E6697", {"start": v(-23.63, 8.45) * mm, "end": v(-23.57, 8.33) * mm});
            skLineSegment(sketch, "E6698", {"start": v(-23.57, 8.33) * mm, "end": v(-23.5, 8.19) * mm});
            skLineSegment(sketch, "E6699", {"start": v(-23.5, 8.19) * mm, "end": v(-23.18, 7.7) * mm});
            skLineSegment(sketch, "E6700", {"start": v(-23.18, 7.7) * mm, "end": v(-22.86, 7.23) * mm});
            skLineSegment(sketch, "E6701", {"start": v(-22.86, 7.23) * mm, "end": v(-22.78, 7.12) * mm});
            skLineSegment(sketch, "E6702", {"start": v(-22.78, 7.12) * mm, "end": v(-22.7, 7) * mm});
            skLineSegment(sketch, "E6703", {"start": v(-22.7, 7) * mm, "end": v(-22.65, 6.94) * mm});
            skLineSegment(sketch, "E6704", {"start": v(-22.65, 6.94) * mm, "end": v(-22.6, 6.89) * mm});
            skLineSegment(sketch, "E6705", {"start": v(-22.6, 6.89) * mm, "end": v(-22.55, 6.83) * mm});
            skLineSegment(sketch, "E6706", {"start": v(-22.55, 6.83) * mm, "end": v(-22.5, 6.8) * mm});
            skLineSegment(sketch, "E6707", {"start": v(8.51, -0.29) * mm, "end": v(8.67, -0.21) * mm});
            skLineSegment(sketch, "E6708", {"start": v(8.67, -0.21) * mm, "end": v(8.81, -0.13) * mm});
            skLineSegment(sketch, "E6709", {"start": v(8.81, -0.13) * mm, "end": v(8.95, -0.03) * mm});
            skLineSegment(sketch, "E6710", {"start": v(8.95, -0.03) * mm, "end": v(9.08, 0.06) * mm});
            skLineSegment(sketch, "E6711", {"start": v(9.08, 0.06) * mm, "end": v(9.33, 0.27) * mm});
            skLineSegment(sketch, "E6712", {"start": v(9.33, 0.27) * mm, "end": v(9.55, 0.46) * mm});
            skLineSegment(sketch, "E6713", {"start": v(9.55, 0.46) * mm, "end": v(9.44, -0.22) * mm});
            skLineSegment(sketch, "E6714", {"start": v(9.44, -0.22) * mm, "end": v(9.68, -0.04) * mm});
            skLineSegment(sketch, "E6715", {"start": v(9.68, -0.04) * mm, "end": v(9.9, 0.18) * mm});
            skLineSegment(sketch, "E6716", {"start": v(9.9, 0.18) * mm, "end": v(10.12, 0.43) * mm});
            skLineSegment(sketch, "E6717", {"start": v(10.12, 0.43) * mm, "end": v(10.32, 0.7) * mm});
            skLineSegment(sketch, "E6718", {"start": v(10.32, 0.7) * mm, "end": v(10.48, 1) * mm});
            skLineSegment(sketch, "E6719", {"start": v(10.48, 1) * mm, "end": v(10.62, 1.31) * mm});
            skLineSegment(sketch, "E6720", {"start": v(10.62, 1.31) * mm, "end": v(10.72, 1.63) * mm});
            skLineSegment(sketch, "E6721", {"start": v(10.72, 1.63) * mm, "end": v(10.78, 1.95) * mm});
            skLineSegment(sketch, "E6722", {"start": v(10.78, 1.95) * mm, "end": v(9.44, 1.05) * mm});
            skLineSegment(sketch, "E6723", {"start": v(9.44, 1.05) * mm, "end": v(9.35, 0.93) * mm});
            skLineSegment(sketch, "E6724", {"start": v(9.35, 0.93) * mm, "end": v(9.24, 0.73) * mm});
            skLineSegment(sketch, "E6725", {"start": v(9.24, 0.73) * mm, "end": v(9.12, 0.51) * mm});
            skLineSegment(sketch, "E6726", {"start": v(9.12, 0.51) * mm, "end": v(9.02, 0.35) * mm});
            skLineSegment(sketch, "E6727", {"start": v(9.02, 0.35) * mm, "end": v(8.51, -0.29) * mm});
            skLineSegment(sketch, "E6728", {"start": v(-9.42, -0.22) * mm, "end": v(-9.57, 0.47) * mm});
            skLineSegment(sketch, "E6729", {"start": v(-9.57, 0.47) * mm, "end": v(-9.33, 0.27) * mm});
            skLineSegment(sketch, "E6730", {"start": v(-9.33, 0.27) * mm, "end": v(-9.09, 0.07) * mm});
            skLineSegment(sketch, "E6731", {"start": v(-9.09, 0.07) * mm, "end": v(-8.96, -0.03) * mm});
            skLineSegment(sketch, "E6732", {"start": v(-8.96, -0.03) * mm, "end": v(-8.82, -0.12) * mm});
            skLineSegment(sketch, "E6733", {"start": v(-8.82, -0.12) * mm, "end": v(-8.67, -0.21) * mm});
            skLineSegment(sketch, "E6734", {"start": v(-8.67, -0.21) * mm, "end": v(-8.52, -0.29) * mm});
            skLineSegment(sketch, "E6735", {"start": v(-8.52, -0.29) * mm, "end": v(-8.58, -0.2) * mm});
            skLineSegment(sketch, "E6736", {"start": v(-8.58, -0.2) * mm, "end": v(-8.77, 0.04) * mm});
            skLineSegment(sketch, "E6737", {"start": v(-8.77, 0.04) * mm, "end": v(-8.9, 0.2) * mm});
            skLineSegment(sketch, "E6738", {"start": v(-8.9, 0.2) * mm, "end": v(-9.02, 0.37) * mm});
            skLineSegment(sketch, "E6739", {"start": v(-9.02, 0.37) * mm, "end": v(-9.21, 0.66) * mm});
            skLineSegment(sketch, "E6740", {"start": v(-9.21, 0.66) * mm, "end": v(-9.33, 0.84) * mm});
            skLineSegment(sketch, "E6741", {"start": v(-9.33, 0.84) * mm, "end": v(-9.4, 0.96) * mm});
            skLineSegment(sketch, "E6742", {"start": v(-9.4, 0.96) * mm, "end": v(-9.45, 1.04) * mm});
            skLineSegment(sketch, "E6743", {"start": v(-9.45, 1.04) * mm, "end": v(-9.5, 1.1) * mm});
            skLineSegment(sketch, "E6744", {"start": v(-9.5, 1.1) * mm, "end": v(-9.68, 1.22) * mm});
            skLineSegment(sketch, "E6745", {"start": v(-9.68, 1.22) * mm, "end": v(-10.1, 1.49) * mm});
            skLineSegment(sketch, "E6746", {"start": v(-10.1, 1.49) * mm, "end": v(-10.26, 1.6) * mm});
            skLineSegment(sketch, "E6747", {"start": v(-10.26, 1.6) * mm, "end": v(-10.43, 1.72) * mm});
            skLineSegment(sketch, "E6748", {"start": v(-10.43, 1.72) * mm, "end": v(-10.6, 1.84) * mm});
            skLineSegment(sketch, "E6749", {"start": v(-10.6, 1.84) * mm, "end": v(-10.78, 1.95) * mm});
            skLineSegment(sketch, "E6750", {"start": v(-10.78, 1.95) * mm, "end": v(-10.72, 1.62) * mm});
            skLineSegment(sketch, "E6751", {"start": v(-10.72, 1.62) * mm, "end": v(-10.6, 1.28) * mm});
            skLineSegment(sketch, "E6752", {"start": v(-10.6, 1.28) * mm, "end": v(-10.44, 0.94) * mm});
            skLineSegment(sketch, "E6753", {"start": v(-10.44, 0.94) * mm, "end": v(-10.25, 0.61) * mm});
            skLineSegment(sketch, "E6754", {"start": v(-10.25, 0.61) * mm, "end": v(-10.04, 0.32) * mm});
            skLineSegment(sketch, "E6755", {"start": v(-10.04, 0.32) * mm, "end": v(-9.82, 0.07) * mm});
            skLineSegment(sketch, "E6756", {"start": v(-9.82, 0.07) * mm, "end": v(-9.6, -0.11) * mm});
            skLineSegment(sketch, "E6757", {"start": v(-9.6, -0.11) * mm, "end": v(-9.42, -0.22) * mm});
            skLineSegment(sketch, "E6758", {"start": v(2.43, -4.62) * mm, "end": v(2.64, -4.6) * mm});
            skLineSegment(sketch, "E6759", {"start": v(2.64, -4.6) * mm, "end": v(2.84, -4.56) * mm});
            skLineSegment(sketch, "E6760", {"start": v(2.84, -4.56) * mm, "end": v(3.05, -4.5) * mm});
            skLineSegment(sketch, "E6761", {"start": v(3.05, -4.5) * mm, "end": v(3.25, -4.44) * mm});
            skLineSegment(sketch, "E6762", {"start": v(3.25, -4.44) * mm, "end": v(3.45, -4.37) * mm});
            skLineSegment(sketch, "E6763", {"start": v(3.45, -4.37) * mm, "end": v(3.63, -4.33) * mm});
            skLineSegment(sketch, "E6764", {"start": v(3.63, -4.33) * mm, "end": v(3.8, -4.3) * mm});
            skLineSegment(sketch, "E6765", {"start": v(3.8, -4.3) * mm, "end": v(3.95, -4.31) * mm});
            skLineSegment(sketch, "E6766", {"start": v(3.95, -4.31) * mm, "end": v(3.96, -4.53) * mm});
            skLineSegment(sketch, "E6767", {"start": v(3.96, -4.53) * mm, "end": v(3.97, -4.73) * mm});
            skLineSegment(sketch, "E6768", {"start": v(3.97, -4.73) * mm, "end": v(3.98, -4.83) * mm});
            skLineSegment(sketch, "E6769", {"start": v(3.98, -4.83) * mm, "end": v(4, -4.92) * mm});
            skLineSegment(sketch, "E6770", {"start": v(4, -4.92) * mm, "end": v(4.04, -5) * mm});
            skLineSegment(sketch, "E6771", {"start": v(4.04, -5) * mm, "end": v(4.1, -5.08) * mm});
            skLineSegment(sketch, "E6772", {"start": v(4.1, -5.08) * mm, "end": v(4.14, -5.14) * mm});
            skLineSegment(sketch, "E6773", {"start": v(4.14, -5.14) * mm, "end": v(4.2, -5.2) * mm});
            skLineSegment(sketch, "E6774", {"start": v(4.2, -5.2) * mm, "end": v(4.27, -5.24) * mm});
            skLineSegment(sketch, "E6775", {"start": v(4.27, -5.24) * mm, "end": v(4.35, -5.27) * mm});
            skLineSegment(sketch, "E6776", {"start": v(4.35, -5.27) * mm, "end": v(4.43, -5.3) * mm});
            skLineSegment(sketch, "E6777", {"start": v(4.43, -5.3) * mm, "end": v(4.53, -5.3) * mm});
            skLineSegment(sketch, "E6778", {"start": v(4.53, -5.3) * mm, "end": v(4.63, -5.3) * mm});
            skLineSegment(sketch, "E6779", {"start": v(4.63, -5.3) * mm, "end": v(4.74, -5.29) * mm});
            skLineSegment(sketch, "E6780", {"start": v(4.74, -5.29) * mm, "end": v(4.84, -5.25) * mm});
            skLineSegment(sketch, "E6781", {"start": v(4.84, -5.25) * mm, "end": v(4.93, -5.2) * mm});
            skLineSegment(sketch, "E6782", {"start": v(4.93, -5.2) * mm, "end": v(5, -5.14) * mm});
            skLineSegment(sketch, "E6783", {"start": v(5, -5.14) * mm, "end": v(5.08, -5.08) * mm});
            skLineSegment(sketch, "E6784", {"start": v(5.08, -5.08) * mm, "end": v(5.19, -4.97) * mm});
            skLineSegment(sketch, "E6785", {"start": v(5.19, -4.97) * mm, "end": v(5.26, -4.89) * mm});
            skLineSegment(sketch, "E6786", {"start": v(5.26, -4.89) * mm, "end": v(5.38, -4.84) * mm});
            skLineSegment(sketch, "E6787", {"start": v(5.38, -4.84) * mm, "end": v(5.6, -4.75) * mm});
            skLineSegment(sketch, "E6788", {"start": v(5.6, -4.75) * mm, "end": v(5.82, -4.67) * mm});
            skLineSegment(sketch, "E6789", {"start": v(5.82, -4.67) * mm, "end": v(5.92, -4.64) * mm});
            skLineSegment(sketch, "E6790", {"start": v(5.92, -4.64) * mm, "end": v(5.54, -4.61) * mm});
            skLineSegment(sketch, "E6791", {"start": v(5.54, -4.61) * mm, "end": v(5.17, -4.57) * mm});
            skLineSegment(sketch, "E6792", {"start": v(5.17, -4.57) * mm, "end": v(5, -4.53) * mm});
            skLineSegment(sketch, "E6793", {"start": v(5, -4.53) * mm, "end": v(4.83, -4.47) * mm});
            skLineSegment(sketch, "E6794", {"start": v(4.83, -4.47) * mm, "end": v(4.66, -4.38) * mm});
            skLineSegment(sketch, "E6795", {"start": v(4.66, -4.38) * mm, "end": v(4.49, -4.27) * mm});
            skLineSegment(sketch, "E6796", {"start": v(4.49, -4.27) * mm, "end": v(4.4, -4.18) * mm});
            skLineSegment(sketch, "E6797", {"start": v(4.4, -4.18) * mm, "end": v(4.3, -4.1) * mm});
            skLineSegment(sketch, "E6798", {"start": v(4.3, -4.1) * mm, "end": v(4.2, -4.03) * mm});
            skLineSegment(sketch, "E6799", {"start": v(4.2, -4.03) * mm, "end": v(4.1, -3.98) * mm});
            skLineSegment(sketch, "E6800", {"start": v(4.1, -3.98) * mm, "end": v(3.95, -3.96) * mm});
            skLineSegment(sketch, "E6801", {"start": v(3.95, -3.96) * mm, "end": v(3.77, -3.98) * mm});
            skLineSegment(sketch, "E6802", {"start": v(3.77, -3.98) * mm, "end": v(3.54, -4.06) * mm});
            skLineSegment(sketch, "E6803", {"start": v(3.54, -4.06) * mm, "end": v(3.23, -4.2) * mm});
            skLineSegment(sketch, "E6804", {"start": v(3.23, -4.2) * mm, "end": v(2.43, -4.62) * mm});
            skLineSegment(sketch, "E6805", {"start": v(-3.8, -18.51) * mm, "end": v(-3.82, -18.71) * mm});
            skLineSegment(sketch, "E6806", {"start": v(-3.82, -18.71) * mm, "end": v(-3.83, -18.93) * mm});
            skLineSegment(sketch, "E6807", {"start": v(-3.83, -18.93) * mm, "end": v(-3.83, -19.17) * mm});
            skLineSegment(sketch, "E6808", {"start": v(-3.83, -19.17) * mm, "end": v(-3.8, -19.4) * mm});
            skLineSegment(sketch, "E6809", {"start": v(-3.8, -19.4) * mm, "end": v(-3.76, -19.63) * mm});
            skLineSegment(sketch, "E6810", {"start": v(-3.76, -19.63) * mm, "end": v(-3.71, -19.85) * mm});
            skLineSegment(sketch, "E6811", {"start": v(-3.71, -19.85) * mm, "end": v(-3.64, -20.03) * mm});
            skLineSegment(sketch, "E6812", {"start": v(-3.64, -20.03) * mm, "end": v(-3.55, -20.2) * mm});
            skLineSegment(sketch, "E6813", {"start": v(-3.55, -20.2) * mm, "end": v(-3.46, -20.3) * mm});
            skLineSegment(sketch, "E6814", {"start": v(-3.46, -20.3) * mm, "end": v(-3.35, -20.4) * mm});
            skLineSegment(sketch, "E6815", {"start": v(-3.35, -20.4) * mm, "end": v(-3.21, -20.47) * mm});
            skLineSegment(sketch, "E6816", {"start": v(-3.21, -20.47) * mm, "end": v(-3.07, -20.51) * mm});
            skLineSegment(sketch, "E6817", {"start": v(-3.07, -20.51) * mm, "end": v(-2.93, -20.52) * mm});
            skLineSegment(sketch, "E6818", {"start": v(-2.93, -20.52) * mm, "end": v(-2.8, -20.48) * mm});
            skLineSegment(sketch, "E6819", {"start": v(-2.8, -20.48) * mm, "end": v(-2.68, -20.38) * mm});
            skLineSegment(sketch, "E6820", {"start": v(-2.68, -20.38) * mm, "end": v(-2.6, -20.21) * mm});
            skLineSegment(sketch, "E6821", {"start": v(-2.6, -20.21) * mm, "end": v(-2.54, -20.03) * mm});
            skLineSegment(sketch, "E6822", {"start": v(-2.54, -20.03) * mm, "end": v(-2.53, -19.9) * mm});
            skLineSegment(sketch, "E6823", {"start": v(-2.53, -19.9) * mm, "end": v(-2.54, -19.82) * mm});
            skLineSegment(sketch, "E6824", {"start": v(-2.54, -19.82) * mm, "end": v(-2.58, -19.75) * mm});
            skLineSegment(sketch, "E6825", {"start": v(-2.58, -19.75) * mm, "end": v(-2.72, -19.66) * mm});
            skLineSegment(sketch, "E6826", {"start": v(-2.72, -19.66) * mm, "end": v(-2.93, -19.52) * mm});
            skLineSegment(sketch, "E6827", {"start": v(-2.93, -19.52) * mm, "end": v(-3.02, -19.45) * mm});
            skLineSegment(sketch, "E6828", {"start": v(-3.02, -19.45) * mm, "end": v(-3.1, -19.37) * mm});
            skLineSegment(sketch, "E6829", {"start": v(-3.1, -19.37) * mm, "end": v(-3.17, -19.28) * mm});
            skLineSegment(sketch, "E6830", {"start": v(-3.17, -19.28) * mm, "end": v(-3.23, -19.16) * mm});
            skLineSegment(sketch, "E6831", {"start": v(-3.23, -19.16) * mm, "end": v(-3.36, -18.84) * mm});
            skLineSegment(sketch, "E6832", {"start": v(-3.36, -18.84) * mm, "end": v(-3.47, -18.6) * mm});
            skLineSegment(sketch, "E6833", {"start": v(-3.47, -18.6) * mm, "end": v(-3.52, -18.52) * mm});
            skLineSegment(sketch, "E6834", {"start": v(-3.52, -18.52) * mm, "end": v(-3.6, -18.48) * mm});
            skLineSegment(sketch, "E6835", {"start": v(-3.6, -18.48) * mm, "end": v(-3.68, -18.47) * mm});
            skLineSegment(sketch, "E6836", {"start": v(-3.68, -18.47) * mm, "end": v(-3.8, -18.51) * mm});
            skLineSegment(sketch, "E6837", {"start": v(2.98, -19.73) * mm, "end": v(2.97, -19.83) * mm});
            skLineSegment(sketch, "E6838", {"start": v(2.97, -19.83) * mm, "end": v(2.97, -19.93) * mm});
            skLineSegment(sketch, "E6839", {"start": v(2.97, -19.93) * mm, "end": v(2.98, -20.03) * mm});
            skLineSegment(sketch, "E6840", {"start": v(2.98, -20.03) * mm, "end": v(3, -20.13) * mm});
            skLineSegment(sketch, "E6841", {"start": v(3, -20.13) * mm, "end": v(3.02, -20.23) * mm});
            skLineSegment(sketch, "E6842", {"start": v(3.02, -20.23) * mm, "end": v(3.05, -20.32) * mm});
            skLineSegment(sketch, "E6843", {"start": v(3.05, -20.32) * mm, "end": v(3.1, -20.4) * mm});
            skLineSegment(sketch, "E6844", {"start": v(3.1, -20.4) * mm, "end": v(3.15, -20.45) * mm});
            skLineSegment(sketch, "E6845", {"start": v(3.15, -20.45) * mm, "end": v(3.31, -20.49) * mm});
            skLineSegment(sketch, "E6846", {"start": v(3.31, -20.49) * mm, "end": v(3.46, -20.5) * mm});
            skLineSegment(sketch, "E6847", {"start": v(3.46, -20.5) * mm, "end": v(3.6, -20.48) * mm});
            skLineSegment(sketch, "E6848", {"start": v(3.6, -20.48) * mm, "end": v(3.71, -20.44) * mm});
            skLineSegment(sketch, "E6849", {"start": v(3.71, -20.44) * mm, "end": v(3.81, -20.37) * mm});
            skLineSegment(sketch, "E6850", {"start": v(3.81, -20.37) * mm, "end": v(3.9, -20.28) * mm});
            skLineSegment(sketch, "E6851", {"start": v(3.9, -20.28) * mm, "end": v(3.98, -20.18) * mm});
            skLineSegment(sketch, "E6852", {"start": v(3.98, -20.18) * mm, "end": v(4.04, -20.05) * mm});
            skLineSegment(sketch, "E6853", {"start": v(4.04, -20.05) * mm, "end": v(4.1, -19.91) * mm});
            skLineSegment(sketch, "E6854", {"start": v(4.1, -19.91) * mm, "end": v(4.14, -19.72) * mm});
            skLineSegment(sketch, "E6855", {"start": v(4.14, -19.72) * mm, "end": v(4.2, -19.49) * mm});
            skLineSegment(sketch, "E6856", {"start": v(4.2, -19.49) * mm, "end": v(4.23, -19.24) * mm});
            skLineSegment(sketch, "E6857", {"start": v(4.23, -19.24) * mm, "end": v(4.25, -19) * mm});
            skLineSegment(sketch, "E6858", {"start": v(4.25, -19) * mm, "end": v(4.26, -18.8) * mm});
            skLineSegment(sketch, "E6859", {"start": v(4.26, -18.8) * mm, "end": v(4.24, -18.63) * mm});
            skLineSegment(sketch, "E6860", {"start": v(4.24, -18.63) * mm, "end": v(4.19, -18.53) * mm});
            skLineSegment(sketch, "E6861", {"start": v(4.19, -18.53) * mm, "end": v(4.08, -18.47) * mm});
            skLineSegment(sketch, "E6862", {"start": v(4.08, -18.47) * mm, "end": v(4, -18.49) * mm});
            skLineSegment(sketch, "E6863", {"start": v(4, -18.49) * mm, "end": v(3.91, -18.56) * mm});
            skLineSegment(sketch, "E6864", {"start": v(3.91, -18.56) * mm, "end": v(3.85, -18.66) * mm});
            skLineSegment(sketch, "E6865", {"start": v(3.85, -18.66) * mm, "end": v(3.76, -18.9) * mm});
            skLineSegment(sketch, "E6866", {"start": v(3.76, -18.9) * mm, "end": v(3.71, -19.06) * mm});
            skLineSegment(sketch, "E6867", {"start": v(3.71, -19.06) * mm, "end": v(3.65, -19.17) * mm});
            skLineSegment(sketch, "E6868", {"start": v(3.65, -19.17) * mm, "end": v(3.58, -19.28) * mm});
            skLineSegment(sketch, "E6869", {"start": v(3.58, -19.28) * mm, "end": v(3.5, -19.38) * mm});
            skLineSegment(sketch, "E6870", {"start": v(3.5, -19.38) * mm, "end": v(3.42, -19.47) * mm});
            skLineSegment(sketch, "E6871", {"start": v(3.42, -19.47) * mm, "end": v(3.32, -19.55) * mm});
            skLineSegment(sketch, "E6872", {"start": v(3.32, -19.55) * mm, "end": v(3.22, -19.62) * mm});
            skLineSegment(sketch, "E6873", {"start": v(3.22, -19.62) * mm, "end": v(3.1, -19.68) * mm});
            skLineSegment(sketch, "E6874", {"start": v(3.1, -19.68) * mm, "end": v(2.98, -19.73) * mm});
            skLineSegment(sketch, "E6875", {"start": v(-9.58, 3.46) * mm, "end": v(-9.54, 3.53) * mm});
            skLineSegment(sketch, "E6876", {"start": v(-9.54, 3.53) * mm, "end": v(-9.53, 3.6) * mm});
            skLineSegment(sketch, "E6877", {"start": v(-9.53, 3.6) * mm, "end": v(-9.52, 3.68) * mm});
            skLineSegment(sketch, "E6878", {"start": v(-9.52, 3.68) * mm, "end": v(-9.52, 3.75) * mm});
            skLineSegment(sketch, "E6879", {"start": v(-9.52, 3.75) * mm, "end": v(-9.24, 3.5) * mm});
            skLineSegment(sketch, "E6880", {"start": v(-9.24, 3.5) * mm, "end": v(-8.94, 3.23) * mm});
            skLineSegment(sketch, "E6881", {"start": v(-8.94, 3.23) * mm, "end": v(-8.79, 3.1) * mm});
            skLineSegment(sketch, "E6882", {"start": v(-8.79, 3.1) * mm, "end": v(-8.63, 2.99) * mm});
            skLineSegment(sketch, "E6883", {"start": v(-8.63, 2.99) * mm, "end": v(-8.47, 2.88) * mm});
            skLineSegment(sketch, "E6884", {"start": v(-8.47, 2.88) * mm, "end": v(-8.31, 2.8) * mm});
            skLineSegment(sketch, "E6885", {"start": v(-8.31, 2.8) * mm, "end": v(-8.4, 2.93) * mm});
            skLineSegment(sketch, "E6886", {"start": v(-8.4, 2.93) * mm, "end": v(-8.57, 3.18) * mm});
            skLineSegment(sketch, "E6887", {"start": v(-8.57, 3.18) * mm, "end": v(-8.68, 3.34) * mm});
            skLineSegment(sketch, "E6888", {"start": v(-8.68, 3.34) * mm, "end": v(-8.79, 3.52) * mm});
            skLineSegment(sketch, "E6889", {"start": v(-8.79, 3.52) * mm, "end": v(-8.9, 3.71) * mm});
            skLineSegment(sketch, "E6890", {"start": v(-8.9, 3.71) * mm, "end": v(-9.01, 3.9) * mm});
            skLineSegment(sketch, "E6891", {"start": v(-9.01, 3.9) * mm, "end": v(-9.1, 4.11) * mm});
            skLineSegment(sketch, "E6892", {"start": v(-9.1, 4.11) * mm, "end": v(-9.18, 4.3) * mm});
            skLineSegment(sketch, "E6893", {"start": v(-9.18, 4.3) * mm, "end": v(-9.23, 4.38) * mm});
            skLineSegment(sketch, "E6894", {"start": v(-9.23, 4.38) * mm, "end": v(-9.3, 4.46) * mm});
            skLineSegment(sketch, "E6895", {"start": v(-9.3, 4.46) * mm, "end": v(-9.38, 4.55) * mm});
            skLineSegment(sketch, "E6896", {"start": v(-9.38, 4.55) * mm, "end": v(-9.49, 4.64) * mm});
            skLineSegment(sketch, "E6897", {"start": v(-9.49, 4.64) * mm, "end": v(-9.82, 4.93) * mm});
            skLineSegment(sketch, "E6898", {"start": v(-9.82, 4.93) * mm, "end": v(-10.38, 5.6) * mm});
            skLineSegment(sketch, "E6899", {"start": v(-10.38, 5.6) * mm, "end": v(-10.36, 5.24) * mm});
            skLineSegment(sketch, "E6900", {"start": v(-10.36, 5.24) * mm, "end": v(-10.27, 4.89) * mm});
            skLineSegment(sketch, "E6901", {"start": v(-10.27, 4.89) * mm, "end": v(-10.15, 4.55) * mm});
            skLineSegment(sketch, "E6902", {"start": v(-10.15, 4.55) * mm, "end": v(-10, 4.23) * mm});
            skLineSegment(sketch, "E6903", {"start": v(-10, 4.23) * mm, "end": v(-9.86, 3.95) * mm});
            skLineSegment(sketch, "E6904", {"start": v(-9.86, 3.95) * mm, "end": v(-9.73, 3.72) * mm});
            skLineSegment(sketch, "E6905", {"start": v(-9.73, 3.72) * mm, "end": v(-9.63, 3.56) * mm});
            skLineSegment(sketch, "E6906", {"start": v(-9.63, 3.56) * mm, "end": v(-9.58, 3.46) * mm});
            skLineSegment(sketch, "E6907", {"start": v(8.28, 2.78) * mm, "end": v(8.44, 2.86) * mm});
            skLineSegment(sketch, "E6908", {"start": v(8.44, 2.86) * mm, "end": v(8.6, 2.97) * mm});
            skLineSegment(sketch, "E6909", {"start": v(8.6, 2.97) * mm, "end": v(8.77, 3.1) * mm});
            skLineSegment(sketch, "E6910", {"start": v(8.77, 3.1) * mm, "end": v(8.93, 3.23) * mm});
            skLineSegment(sketch, "E6911", {"start": v(8.93, 3.23) * mm, "end": v(9.24, 3.5) * mm});
            skLineSegment(sketch, "E6912", {"start": v(9.24, 3.5) * mm, "end": v(9.51, 3.75) * mm});
            skLineSegment(sketch, "E6913", {"start": v(9.51, 3.75) * mm, "end": v(9.59, 3.54) * mm});
            skLineSegment(sketch, "E6914", {"start": v(9.59, 3.54) * mm, "end": v(9.6, 3.56) * mm});
            skLineSegment(sketch, "E6915", {"start": v(9.6, 3.56) * mm, "end": v(9.7, 3.67) * mm});
            skLineSegment(sketch, "E6916", {"start": v(9.7, 3.67) * mm, "end": v(9.82, 3.87) * mm});
            skLineSegment(sketch, "E6917", {"start": v(9.82, 3.87) * mm, "end": v(9.95, 4.1) * mm});
            skLineSegment(sketch, "E6918", {"start": v(9.95, 4.1) * mm, "end": v(10.06, 4.34) * mm});
            skLineSegment(sketch, "E6919", {"start": v(10.06, 4.34) * mm, "end": v(10.16, 4.6) * mm});
            skLineSegment(sketch, "E6920", {"start": v(10.16, 4.6) * mm, "end": v(10.25, 4.87) * mm});
            skLineSegment(sketch, "E6921", {"start": v(10.25, 4.87) * mm, "end": v(10.32, 5.13) * mm});
            skLineSegment(sketch, "E6922", {"start": v(10.32, 5.13) * mm, "end": v(10.36, 5.37) * mm});
            skLineSegment(sketch, "E6923", {"start": v(10.36, 5.37) * mm, "end": v(10.38, 5.59) * mm});
            skLineSegment(sketch, "E6924", {"start": v(10.38, 5.59) * mm, "end": v(10.25, 5.43) * mm});
            skLineSegment(sketch, "E6925", {"start": v(10.25, 5.43) * mm, "end": v(10.11, 5.26) * mm});
            skLineSegment(sketch, "E6926", {"start": v(10.11, 5.26) * mm, "end": v(9.97, 5.1) * mm});
            skLineSegment(sketch, "E6927", {"start": v(9.97, 5.1) * mm, "end": v(9.83, 4.96) * mm});
            skLineSegment(sketch, "E6928", {"start": v(9.83, 4.96) * mm, "end": v(9.67, 4.8) * mm});
            skLineSegment(sketch, "E6929", {"start": v(9.67, 4.8) * mm, "end": v(9.48, 4.63) * mm});
            skLineSegment(sketch, "E6930", {"start": v(9.48, 4.63) * mm, "end": v(9.39, 4.55) * mm});
            skLineSegment(sketch, "E6931", {"start": v(9.39, 4.55) * mm, "end": v(9.3, 4.47) * mm});
            skLineSegment(sketch, "E6932", {"start": v(9.3, 4.47) * mm, "end": v(9.24, 4.4) * mm});
            skLineSegment(sketch, "E6933", {"start": v(9.24, 4.4) * mm, "end": v(9.2, 4.34) * mm});
            skLineSegment(sketch, "E6934", {"start": v(9.2, 4.34) * mm, "end": v(9.06, 4.05) * mm});
            skLineSegment(sketch, "E6935", {"start": v(9.06, 4.05) * mm, "end": v(8.9, 3.72) * mm});
            skLineSegment(sketch, "E6936", {"start": v(8.9, 3.72) * mm, "end": v(8.8, 3.55) * mm});
            skLineSegment(sketch, "E6937", {"start": v(8.8, 3.55) * mm, "end": v(8.72, 3.39) * mm});
            skLineSegment(sketch, "E6938", {"start": v(8.72, 3.39) * mm, "end": v(8.63, 3.24) * mm});
            skLineSegment(sketch, "E6939", {"start": v(8.63, 3.24) * mm, "end": v(8.54, 3.13) * mm});
            skLineSegment(sketch, "E6940", {"start": v(8.54, 3.13) * mm, "end": v(8.46, 3.04) * mm});
            skLineSegment(sketch, "E6941", {"start": v(8.46, 3.04) * mm, "end": v(8.4, 2.96) * mm});
            skLineSegment(sketch, "E6942", {"start": v(8.4, 2.96) * mm, "end": v(8.34, 2.87) * mm});
            skLineSegment(sketch, "E6943", {"start": v(8.34, 2.87) * mm, "end": v(8.28, 2.78) * mm});
            skLineSegment(sketch, "E6944", {"start": v(4.02, -14.7) * mm, "end": v(4.15, -14.8) * mm});
            skLineSegment(sketch, "E6945", {"start": v(4.15, -14.8) * mm, "end": v(4.27, -14.9) * mm});
            skLineSegment(sketch, "E6946", {"start": v(4.27, -14.9) * mm, "end": v(4.37, -15) * mm});
            skLineSegment(sketch, "E6947", {"start": v(4.37, -15) * mm, "end": v(4.5, -15.1) * mm});
            skLineSegment(sketch, "E6948", {"start": v(4.5, -15.1) * mm, "end": v(4.64, -15) * mm});
            skLineSegment(sketch, "E6949", {"start": v(4.64, -15) * mm, "end": v(4.77, -14.93) * mm});
            skLineSegment(sketch, "E6950", {"start": v(4.77, -14.93) * mm, "end": v(4.9, -14.87) * mm});
            skLineSegment(sketch, "E6951", {"start": v(4.9, -14.87) * mm, "end": v(5.03, -14.83) * mm});
            skLineSegment(sketch, "E6952", {"start": v(5.03, -14.83) * mm, "end": v(5.18, -14.81) * mm});
            skLineSegment(sketch, "E6953", {"start": v(5.18, -14.81) * mm, "end": v(5.33, -14.82) * mm});
            skLineSegment(sketch, "E6954", {"start": v(5.33, -14.82) * mm, "end": v(5.5, -14.86) * mm});
            skLineSegment(sketch, "E6955", {"start": v(5.5, -14.86) * mm, "end": v(5.7, -14.93) * mm});
            skLineSegment(sketch, "E6956", {"start": v(5.7, -14.93) * mm, "end": v(5.87, -15) * mm});
            skLineSegment(sketch, "E6957", {"start": v(5.87, -15) * mm, "end": v(6, -15.1) * mm});
            skLineSegment(sketch, "E6958", {"start": v(6, -15.1) * mm, "end": v(6.1, -15.19) * mm});
            skLineSegment(sketch, "E6959", {"start": v(6.1, -15.19) * mm, "end": v(6.2, -15.29) * mm});
            skLineSegment(sketch, "E6960", {"start": v(6.2, -15.29) * mm, "end": v(6.33, -15.52) * mm});
            skLineSegment(sketch, "E6961", {"start": v(6.33, -15.52) * mm, "end": v(6.5, -15.8) * mm});
            skLineSegment(sketch, "E6962", {"start": v(6.5, -15.8) * mm, "end": v(6.76, -15.81) * mm});
            skLineSegment(sketch, "E6963", {"start": v(6.76, -15.81) * mm, "end": v(6.66, -15.63) * mm});
            skLineSegment(sketch, "E6964", {"start": v(6.66, -15.63) * mm, "end": v(6.44, -15.38) * mm});
            skLineSegment(sketch, "E6965", {"start": v(6.44, -15.38) * mm, "end": v(6.12, -15.06) * mm});
            skLineSegment(sketch, "E6966", {"start": v(6.12, -15.06) * mm, "end": v(5.75, -14.73) * mm});
            skLineSegment(sketch, "E6967", {"start": v(5.75, -14.73) * mm, "end": v(5.37, -14.4) * mm});
            skLineSegment(sketch, "E6968", {"start": v(5.37, -14.4) * mm, "end": v(5, -14.1) * mm});
            skLineSegment(sketch, "E6969", {"start": v(5, -14.1) * mm, "end": v(4.7, -13.86) * mm});
            skLineSegment(sketch, "E6970", {"start": v(4.7, -13.86) * mm, "end": v(4.48, -13.7) * mm});
            skLineSegment(sketch, "E6971", {"start": v(4.48, -13.7) * mm, "end": v(4.02, -14.7) * mm});
            skLineSegment(sketch, "E6972", {"start": v(-8.07, -0.4) * mm, "end": v(-8.12, -0.23) * mm});
            skLineSegment(sketch, "E6973", {"start": v(-8.12, -0.23) * mm, "end": v(-8.17, -0.03) * mm});
            skLineSegment(sketch, "E6974", {"start": v(-8.17, -0.03) * mm, "end": v(-8.18, 0.07) * mm});
            skLineSegment(sketch, "E6975", {"start": v(-8.18, 0.07) * mm, "end": v(-8.19, 0.17) * mm});
            skLineSegment(sketch, "E6976", {"start": v(-8.19, 0.17) * mm, "end": v(-8.19, 0.27) * mm});
            skLineSegment(sketch, "E6977", {"start": v(-8.19, 0.27) * mm, "end": v(-8.17, 0.36) * mm});
            skLineSegment(sketch, "E6978", {"start": v(-8.17, 0.36) * mm, "end": v(-8.1, 0.38) * mm});
            skLineSegment(sketch, "E6979", {"start": v(-8.1, 0.38) * mm, "end": v(-8.01, 0.37) * mm});
            skLineSegment(sketch, "E6980", {"start": v(-8.01, 0.37) * mm, "end": v(-7.83, 0.3) * mm});
            skLineSegment(sketch, "E6981", {"start": v(-7.83, 0.3) * mm, "end": v(-7.74, 0.27) * mm});
            skLineSegment(sketch, "E6982", {"start": v(-7.74, 0.27) * mm, "end": v(-7.66, 0.23) * mm});
            skLineSegment(sketch, "E6983", {"start": v(-7.66, 0.23) * mm, "end": v(-7.58, 0.2) * mm});
            skLineSegment(sketch, "E6984", {"start": v(-7.58, 0.2) * mm, "end": v(-7.48, 0.19) * mm});
            skLineSegment(sketch, "E6985", {"start": v(-7.48, 0.19) * mm, "end": v(-7.64, 0.49) * mm});
            skLineSegment(sketch, "E6986", {"start": v(-7.64, 0.49) * mm, "end": v(-7.7, 0.63) * mm});
            skLineSegment(sketch, "E6987", {"start": v(-7.7, 0.63) * mm, "end": v(-7.76, 0.72) * mm});
            skLineSegment(sketch, "E6988", {"start": v(-7.76, 0.72) * mm, "end": v(-7.82, 0.77) * mm});
            skLineSegment(sketch, "E6989", {"start": v(-7.82, 0.77) * mm, "end": v(-7.9, 0.8) * mm});
            skLineSegment(sketch, "E6990", {"start": v(-7.9, 0.8) * mm, "end": v(-8, 0.83) * mm});
            skLineSegment(sketch, "E6991", {"start": v(-8, 0.83) * mm, "end": v(-8.12, 0.88) * mm});
            skLineSegment(sketch, "E6992", {"start": v(-8.12, 0.88) * mm, "end": v(-8.3, 0.96) * mm});
            skLineSegment(sketch, "E6993", {"start": v(-8.3, 0.96) * mm, "end": v(-8.53, 1.1) * mm});
            skLineSegment(sketch, "E6994", {"start": v(-8.53, 1.1) * mm, "end": v(-9.09, 1.5) * mm});
            skLineSegment(sketch, "E6995", {"start": v(-9.09, 1.5) * mm, "end": v(-9.35, 1.74) * mm});
            skLineSegment(sketch, "E6996", {"start": v(-9.35, 1.74) * mm, "end": v(-9.41, 1.8) * mm});
            skLineSegment(sketch, "E6997", {"start": v(-9.41, 1.8) * mm, "end": v(-9.46, 1.86) * mm});
            skLineSegment(sketch, "E6998", {"start": v(-9.46, 1.86) * mm, "end": v(-9.51, 1.91) * mm});
            skLineSegment(sketch, "E6999", {"start": v(-9.51, 1.91) * mm, "end": v(-9.6, 1.97) * mm});
            skLineSegment(sketch, "E7000", {"start": v(-9.6, 1.97) * mm, "end": v(-9.53, 1.7) * mm});
            skLineSegment(sketch, "E7001", {"start": v(-9.53, 1.7) * mm, "end": v(-9.4, 1.38) * mm});
            skLineSegment(sketch, "E7002", {"start": v(-9.4, 1.38) * mm, "end": v(-9.23, 1.04) * mm});
            skLineSegment(sketch, "E7003", {"start": v(-9.23, 1.04) * mm, "end": v(-9.02, 0.7) * mm});
            skLineSegment(sketch, "E7004", {"start": v(-9.02, 0.7) * mm, "end": v(-8.79, 0.36) * mm});
            skLineSegment(sketch, "E7005", {"start": v(-8.79, 0.36) * mm, "end": v(-8.54, 0.05) * mm});
            skLineSegment(sketch, "E7006", {"start": v(-8.54, 0.05) * mm, "end": v(-8.3, -0.21) * mm});
            skLineSegment(sketch, "E7007", {"start": v(-8.3, -0.21) * mm, "end": v(-8.07, -0.4) * mm});
            skLineSegment(sketch, "E7008", {"start": v(7.5, 0.2) * mm, "end": v(7.58, 0.21) * mm});
            skLineSegment(sketch, "E7009", {"start": v(7.58, 0.21) * mm, "end": v(7.66, 0.24) * mm});
            skLineSegment(sketch, "E7010", {"start": v(7.66, 0.24) * mm, "end": v(7.75, 0.27) * mm});
            skLineSegment(sketch, "E7011", {"start": v(7.75, 0.27) * mm, "end": v(7.83, 0.3) * mm});
            skLineSegment(sketch, "E7012", {"start": v(7.83, 0.3) * mm, "end": v(7.92, 0.34) * mm});
            skLineSegment(sketch, "E7013", {"start": v(7.92, 0.34) * mm, "end": v(8, 0.37) * mm});
            skLineSegment(sketch, "E7014", {"start": v(8, 0.37) * mm, "end": v(8.09, 0.38) * mm});
            skLineSegment(sketch, "E7015", {"start": v(8.09, 0.38) * mm, "end": v(8.17, 0.38) * mm});
            skLineSegment(sketch, "E7016", {"start": v(8.17, 0.38) * mm, "end": v(8.17, 0.17) * mm});
            skLineSegment(sketch, "E7017", {"start": v(8.17, 0.17) * mm, "end": v(8.15, 0) * mm});
            skLineSegment(sketch, "E7018", {"start": v(8.15, 0) * mm, "end": v(8.13, -0.18) * mm});
            skLineSegment(sketch, "E7019", {"start": v(8.13, -0.18) * mm, "end": v(8.1, -0.37) * mm});
            skLineSegment(sketch, "E7020", {"start": v(8.1, -0.37) * mm, "end": v(8.36, -0.15) * mm});
            skLineSegment(sketch, "E7021", {"start": v(8.36, -0.15) * mm, "end": v(8.6, 0.1) * mm});
            skLineSegment(sketch, "E7022", {"start": v(8.6, 0.1) * mm, "end": v(8.75, 0.3) * mm});
            skLineSegment(sketch, "E7023", {"start": v(8.75, 0.3) * mm, "end": v(8.9, 0.5) * mm});
            skLineSegment(sketch, "E7024", {"start": v(8.9, 0.5) * mm, "end": v(9.04, 0.74) * mm});
            skLineSegment(sketch, "E7025", {"start": v(9.04, 0.74) * mm, "end": v(9.18, 0.98) * mm});
            skLineSegment(sketch, "E7026", {"start": v(9.18, 0.98) * mm, "end": v(9.31, 1.23) * mm});
            skLineSegment(sketch, "E7027", {"start": v(9.31, 1.23) * mm, "end": v(9.43, 1.48) * mm});
            skLineSegment(sketch, "E7028", {"start": v(9.43, 1.48) * mm, "end": v(9.52, 1.73) * mm});
            skLineSegment(sketch, "E7029", {"start": v(9.52, 1.73) * mm, "end": v(9.6, 1.96) * mm});
            skLineSegment(sketch, "E7030", {"start": v(9.6, 1.96) * mm, "end": v(9.5, 1.9) * mm});
            skLineSegment(sketch, "E7031", {"start": v(9.5, 1.9) * mm, "end": v(9.4, 1.8) * mm});
            skLineSegment(sketch, "E7032", {"start": v(9.4, 1.8) * mm, "end": v(9.26, 1.66) * mm});
            skLineSegment(sketch, "E7033", {"start": v(9.26, 1.66) * mm, "end": v(9.1, 1.5) * mm});
            skLineSegment(sketch, "E7034", {"start": v(9.1, 1.5) * mm, "end": v(8.88, 1.33) * mm});
            skLineSegment(sketch, "E7035", {"start": v(8.88, 1.33) * mm, "end": v(8.62, 1.15) * mm});
            skLineSegment(sketch, "E7036", {"start": v(8.62, 1.15) * mm, "end": v(8.29, 0.96) * mm});
            skLineSegment(sketch, "E7037", {"start": v(8.29, 0.96) * mm, "end": v(7.88, 0.78) * mm});
            skLineSegment(sketch, "E7038", {"start": v(7.88, 0.78) * mm, "end": v(7.81, 0.75) * mm});
            skLineSegment(sketch, "E7039", {"start": v(7.81, 0.75) * mm, "end": v(7.75, 0.7) * mm});
            skLineSegment(sketch, "E7040", {"start": v(7.75, 0.7) * mm, "end": v(7.7, 0.66) * mm});
            skLineSegment(sketch, "E7041", {"start": v(7.7, 0.66) * mm, "end": v(7.67, 0.6) * mm});
            skLineSegment(sketch, "E7042", {"start": v(7.67, 0.6) * mm, "end": v(7.6, 0.44) * mm});
            skLineSegment(sketch, "E7043", {"start": v(7.6, 0.44) * mm, "end": v(7.5, 0.2) * mm});
            skLineSegment(sketch, "E7044", {"start": v(-7.57, -1.98) * mm, "end": v(-7.65, -1.85) * mm});
            skLineSegment(sketch, "E7045", {"start": v(-7.65, -1.85) * mm, "end": v(-7.75, -1.68) * mm});
            skLineSegment(sketch, "E7046", {"start": v(-7.75, -1.68) * mm, "end": v(-7.8, -1.58) * mm});
            skLineSegment(sketch, "E7047", {"start": v(-7.8, -1.58) * mm, "end": v(-7.83, -1.5) * mm});
            skLineSegment(sketch, "E7048", {"start": v(-7.83, -1.5) * mm, "end": v(-7.87, -1.4) * mm});
            skLineSegment(sketch, "E7049", {"start": v(-7.87, -1.4) * mm, "end": v(-7.89, -1.33) * mm});
            skLineSegment(sketch, "E7050", {"start": v(-7.89, -1.33) * mm, "end": v(-7.45, -1.38) * mm});
            skLineSegment(sketch, "E7051", {"start": v(-7.45, -1.38) * mm, "end": v(-7.8, -0.93) * mm});
            skLineSegment(sketch, "E7052", {"start": v(-7.8, -0.93) * mm, "end": v(-7.91, -0.87) * mm});
            skLineSegment(sketch, "E7053", {"start": v(-7.91, -0.87) * mm, "end": v(-8.07, -0.8) * mm});
            skLineSegment(sketch, "E7054", {"start": v(-8.07, -0.8) * mm, "end": v(-8.23, -0.74) * mm});
            skLineSegment(sketch, "E7055", {"start": v(-8.23, -0.74) * mm, "end": v(-8.35, -0.69) * mm});
            skLineSegment(sketch, "E7056", {"start": v(-8.35, -0.69) * mm, "end": v(-8.54, -0.58) * mm});
            skLineSegment(sketch, "E7057", {"start": v(-8.54, -0.58) * mm, "end": v(-8.69, -0.5) * mm});
            skLineSegment(sketch, "E7058", {"start": v(-8.69, -0.5) * mm, "end": v(-8.8, -0.41) * mm});
            skLineSegment(sketch, "E7059", {"start": v(-8.8, -0.41) * mm, "end": v(-8.9, -0.33) * mm});
            skLineSegment(sketch, "E7060", {"start": v(-8.9, -0.33) * mm, "end": v(-9.07, -0.19) * mm});
            skLineSegment(sketch, "E7061", {"start": v(-9.07, -0.19) * mm, "end": v(-9.28, -0.02) * mm});
            skLineSegment(sketch, "E7062", {"start": v(-9.28, -0.02) * mm, "end": v(-9.2, -0.33) * mm});
            skLineSegment(sketch, "E7063", {"start": v(-9.2, -0.33) * mm, "end": v(-9.06, -0.64) * mm});
            skLineSegment(sketch, "E7064", {"start": v(-9.06, -0.64) * mm, "end": v(-8.86, -0.95) * mm});
            skLineSegment(sketch, "E7065", {"start": v(-8.86, -0.95) * mm, "end": v(-8.63, -1.23) * mm});
            skLineSegment(sketch, "E7066", {"start": v(-8.63, -1.23) * mm, "end": v(-8.37, -1.49) * mm});
            skLineSegment(sketch, "E7067", {"start": v(-8.37, -1.49) * mm, "end": v(-8.1, -1.7) * mm});
            skLineSegment(sketch, "E7068", {"start": v(-8.1, -1.7) * mm, "end": v(-7.83, -1.87) * mm});
            skLineSegment(sketch, "E7069", {"start": v(-7.83, -1.87) * mm, "end": v(-7.57, -1.98) * mm});
            skLineSegment(sketch, "E7070", {"start": v(7.45, -1.37) * mm, "end": v(7.88, -1.34) * mm});
            skLineSegment(sketch, "E7071", {"start": v(7.88, -1.34) * mm, "end": v(7.84, -1.44) * mm});
            skLineSegment(sketch, "E7072", {"start": v(7.84, -1.44) * mm, "end": v(7.8, -1.53) * mm});
            skLineSegment(sketch, "E7073", {"start": v(7.8, -1.53) * mm, "end": v(7.77, -1.6) * mm});
            skLineSegment(sketch, "E7074", {"start": v(7.77, -1.6) * mm, "end": v(7.73, -1.68) * mm});
            skLineSegment(sketch, "E7075", {"start": v(7.73, -1.68) * mm, "end": v(7.66, -1.81) * mm});
            skLineSegment(sketch, "E7076", {"start": v(7.66, -1.81) * mm, "end": v(7.6, -1.96) * mm});
            skLineSegment(sketch, "E7077", {"start": v(7.6, -1.96) * mm, "end": v(7.77, -1.89) * mm});
            skLineSegment(sketch, "E7078", {"start": v(7.77, -1.89) * mm, "end": v(7.93, -1.8) * mm});
            skLineSegment(sketch, "E7079", {"start": v(7.93, -1.8) * mm, "end": v(8.1, -1.69) * mm});
            skLineSegment(sketch, "E7080", {"start": v(8.1, -1.69) * mm, "end": v(8.25, -1.57) * mm});
            skLineSegment(sketch, "E7081", {"start": v(8.25, -1.57) * mm, "end": v(8.4, -1.45) * mm});
            skLineSegment(sketch, "E7082", {"start": v(8.4, -1.45) * mm, "end": v(8.53, -1.32) * mm});
            skLineSegment(sketch, "E7083", {"start": v(8.53, -1.32) * mm, "end": v(8.65, -1.2) * mm});
            skLineSegment(sketch, "E7084", {"start": v(8.65, -1.2) * mm, "end": v(8.75, -1.09) * mm});
            skLineSegment(sketch, "E7085", {"start": v(8.75, -1.09) * mm, "end": v(8.84, -1) * mm});
            skLineSegment(sketch, "E7086", {"start": v(8.84, -1) * mm, "end": v(8.9, -0.92) * mm});
            skLineSegment(sketch, "E7087", {"start": v(8.9, -0.92) * mm, "end": v(8.96, -0.83) * mm});
            skLineSegment(sketch, "E7088", {"start": v(8.96, -0.83) * mm, "end": v(9.03, -0.7) * mm});
            skLineSegment(sketch, "E7089", {"start": v(9.03, -0.7) * mm, "end": v(9.11, -0.53) * mm});
            skLineSegment(sketch, "E7090", {"start": v(9.11, -0.53) * mm, "end": v(9.18, -0.37) * mm});
            skLineSegment(sketch, "E7091", {"start": v(9.18, -0.37) * mm, "end": v(9.23, -0.2) * mm});
            skLineSegment(sketch, "E7092", {"start": v(9.23, -0.2) * mm, "end": v(9.28, -0.02) * mm});
            skLineSegment(sketch, "E7093", {"start": v(9.28, -0.02) * mm, "end": v(8.84, -0.38) * mm});
            skLineSegment(sketch, "E7094", {"start": v(8.84, -0.38) * mm, "end": v(8.64, -0.52) * mm});
            skLineSegment(sketch, "E7095", {"start": v(8.64, -0.52) * mm, "end": v(8.46, -0.63) * mm});
            skLineSegment(sketch, "E7096", {"start": v(8.46, -0.63) * mm, "end": v(8.3, -0.7) * mm});
            skLineSegment(sketch, "E7097", {"start": v(8.3, -0.7) * mm, "end": v(8.17, -0.77) * mm});
            skLineSegment(sketch, "E7098", {"start": v(8.17, -0.77) * mm, "end": v(8.05, -0.81) * mm});
            skLineSegment(sketch, "E7099", {"start": v(8.05, -0.81) * mm, "end": v(7.95, -0.85) * mm});
            skLineSegment(sketch, "E7100", {"start": v(7.95, -0.85) * mm, "end": v(7.87, -0.88) * mm});
            skLineSegment(sketch, "E7101", {"start": v(7.87, -0.88) * mm, "end": v(7.8, -0.93) * mm});
            skLineSegment(sketch, "E7102", {"start": v(7.8, -0.93) * mm, "end": v(7.73, -1) * mm});
            skLineSegment(sketch, "E7103", {"start": v(7.73, -1) * mm, "end": v(7.62, -1.14) * mm});
            skLineSegment(sketch, "E7104", {"start": v(7.62, -1.14) * mm, "end": v(7.52, -1.27) * mm});
            skLineSegment(sketch, "E7105", {"start": v(7.52, -1.27) * mm, "end": v(7.45, -1.37) * mm});
            skLineSegment(sketch, "E7106", {"start": v(8.04, 6.2) * mm, "end": v(8.06, 6.2) * mm});
            skLineSegment(sketch, "E7107", {"start": v(8.06, 6.2) * mm, "end": v(8.06, 5.75) * mm});
            skLineSegment(sketch, "E7108", {"start": v(8.06, 5.75) * mm, "end": v(8.54, 6.08) * mm});
            skLineSegment(sketch, "E7109", {"start": v(8.54, 6.08) * mm, "end": v(9.03, 6.43) * mm});
            skLineSegment(sketch, "E7110", {"start": v(9.03, 6.43) * mm, "end": v(9.25, 6.59) * mm});
            skLineSegment(sketch, "E7111", {"start": v(9.25, 6.59) * mm, "end": v(9.52, 6.79) * mm});
            skLineSegment(sketch, "E7112", {"start": v(9.52, 6.79) * mm, "end": v(9.66, 6.89) * mm});
            skLineSegment(sketch, "E7113", {"start": v(9.66, 6.89) * mm, "end": v(9.78, 6.99) * mm});
            skLineSegment(sketch, "E7114", {"start": v(9.78, 6.99) * mm, "end": v(9.87, 7.08) * mm});
            skLineSegment(sketch, "E7115", {"start": v(9.87, 7.08) * mm, "end": v(9.94, 7.16) * mm});
            skLineSegment(sketch, "E7116", {"start": v(9.94, 7.16) * mm, "end": v(9.9, 7.19) * mm});
            skLineSegment(sketch, "E7117", {"start": v(9.9, 7.19) * mm, "end": v(9.95, 7.21) * mm});
            skLineSegment(sketch, "E7118", {"start": v(9.95, 7.21) * mm, "end": v(10.06, 7.31) * mm});
            skLineSegment(sketch, "E7119", {"start": v(10.06, 7.31) * mm, "end": v(10.15, 7.4) * mm});
            skLineSegment(sketch, "E7120", {"start": v(10.15, 7.4) * mm, "end": v(10.22, 7.5) * mm});
            skLineSegment(sketch, "E7121", {"start": v(10.22, 7.5) * mm, "end": v(10.29, 7.57) * mm});
            skLineSegment(sketch, "E7122", {"start": v(10.29, 7.57) * mm, "end": v(10.33, 7.65) * mm});
            skLineSegment(sketch, "E7123", {"start": v(10.33, 7.65) * mm, "end": v(10.37, 7.73) * mm});
            skLineSegment(sketch, "E7124", {"start": v(10.37, 7.73) * mm, "end": v(10.38, 7.82) * mm});
            skLineSegment(sketch, "E7125", {"start": v(10.38, 7.82) * mm, "end": v(10.38, 7.94) * mm});
            skLineSegment(sketch, "E7126", {"start": v(10.38, 7.94) * mm, "end": v(10.37, 8.07) * mm});
            skLineSegment(sketch, "E7127", {"start": v(10.37, 8.07) * mm, "end": v(10.34, 8.05) * mm});
            skLineSegment(sketch, "E7128", {"start": v(10.34, 8.05) * mm, "end": v(10.33, 8) * mm});
            skLineSegment(sketch, "E7129", {"start": v(10.33, 8) * mm, "end": v(10.32, 8) * mm});
            skLineSegment(sketch, "E7130", {"start": v(10.32, 8) * mm, "end": v(10.31, 8) * mm});
            skLineSegment(sketch, "E7131", {"start": v(10.31, 8) * mm, "end": v(10.3, 8) * mm});
            skLineSegment(sketch, "E7132", {"start": v(10.3, 8) * mm, "end": v(10.1, 7.82) * mm});
            skLineSegment(sketch, "E7133", {"start": v(10.1, 7.82) * mm, "end": v(9.81, 7.56) * mm});
            skLineSegment(sketch, "E7134", {"start": v(9.81, 7.56) * mm, "end": v(9.68, 7.43) * mm});
            skLineSegment(sketch, "E7135", {"start": v(9.68, 7.43) * mm, "end": v(9.54, 7.3) * mm});
            skLineSegment(sketch, "E7136", {"start": v(9.54, 7.3) * mm, "end": v(9.4, 7.19) * mm});
            skLineSegment(sketch, "E7137", {"start": v(9.4, 7.19) * mm, "end": v(9.26, 7.07) * mm});
            skLineSegment(sketch, "E7138", {"start": v(9.26, 7.07) * mm, "end": v(8.97, 6.86) * mm});
            skLineSegment(sketch, "E7139", {"start": v(8.97, 6.86) * mm, "end": v(8.66, 6.63) * mm});
            skLineSegment(sketch, "E7140", {"start": v(8.66, 6.63) * mm, "end": v(8.51, 6.54) * mm});
            skLineSegment(sketch, "E7141", {"start": v(8.51, 6.54) * mm, "end": v(8.32, 6.42) * mm});
            skLineSegment(sketch, "E7142", {"start": v(8.32, 6.42) * mm, "end": v(8.23, 6.36) * mm});
            skLineSegment(sketch, "E7143", {"start": v(8.23, 6.36) * mm, "end": v(8.14, 6.3) * mm});
            skLineSegment(sketch, "E7144", {"start": v(8.14, 6.3) * mm, "end": v(8.08, 6.24) * mm});
            skLineSegment(sketch, "E7145", {"start": v(8.08, 6.24) * mm, "end": v(8.04, 6.2) * mm});
            skLineSegment(sketch, "E7146", {"start": v(7.83, 2.26) * mm, "end": v(7.87, 1.95) * mm});
            skLineSegment(sketch, "E7147", {"start": v(7.87, 1.95) * mm, "end": v(7.89, 1.73) * mm});
            skLineSegment(sketch, "E7148", {"start": v(7.89, 1.73) * mm, "end": v(7.88, 1.5) * mm});
            skLineSegment(sketch, "E7149", {"start": v(7.88, 1.5) * mm, "end": v(7.85, 1.19) * mm});
            skLineSegment(sketch, "E7150", {"start": v(7.85, 1.19) * mm, "end": v(7.97, 1.26) * mm});
            skLineSegment(sketch, "E7151", {"start": v(7.97, 1.26) * mm, "end": v(8.09, 1.36) * mm});
            skLineSegment(sketch, "E7152", {"start": v(8.09, 1.36) * mm, "end": v(8.2, 1.47) * mm});
            skLineSegment(sketch, "E7153", {"start": v(8.2, 1.47) * mm, "end": v(8.3, 1.58) * mm});
            skLineSegment(sketch, "E7154", {"start": v(8.3, 1.58) * mm, "end": v(8.4, 1.68) * mm});
            skLineSegment(sketch, "E7155", {"start": v(8.4, 1.68) * mm, "end": v(8.5, 1.8) * mm});
            skLineSegment(sketch, "E7156", {"start": v(8.5, 1.8) * mm, "end": v(8.6, 1.94) * mm});
            skLineSegment(sketch, "E7157", {"start": v(8.6, 1.94) * mm, "end": v(8.7, 2.05) * mm});
            skLineSegment(sketch, "E7158", {"start": v(8.7, 2.05) * mm, "end": v(8.86, 2.3) * mm});
            skLineSegment(sketch, "E7159", {"start": v(8.86, 2.3) * mm, "end": v(9.03, 2.58) * mm});
            skLineSegment(sketch, "E7160", {"start": v(9.03, 2.58) * mm, "end": v(9.11, 2.73) * mm});
            skLineSegment(sketch, "E7161", {"start": v(9.11, 2.73) * mm, "end": v(9.18, 2.89) * mm});
            skLineSegment(sketch, "E7162", {"start": v(9.18, 2.89) * mm, "end": v(9.24, 3.05) * mm});
            skLineSegment(sketch, "E7163", {"start": v(9.24, 3.05) * mm, "end": v(9.3, 3.23) * mm});
            skLineSegment(sketch, "E7164", {"start": v(9.3, 3.23) * mm, "end": v(9.1, 3.1) * mm});
            skLineSegment(sketch, "E7165", {"start": v(9.1, 3.1) * mm, "end": v(8.76, 2.85) * mm});
            skLineSegment(sketch, "E7166", {"start": v(8.76, 2.85) * mm, "end": v(8.55, 2.7) * mm});
            skLineSegment(sketch, "E7167", {"start": v(8.55, 2.7) * mm, "end": v(8.31, 2.54) * mm});
            skLineSegment(sketch, "E7168", {"start": v(8.31, 2.54) * mm, "end": v(8.07, 2.4) * mm});
            skLineSegment(sketch, "E7169", {"start": v(8.07, 2.4) * mm, "end": v(7.83, 2.26) * mm});
            skLineSegment(sketch, "E7170", {"start": v(-6.43, -15.8) * mm, "end": v(-6.08, -15.81) * mm});
            skLineSegment(sketch, "E7171", {"start": v(-6.08, -15.81) * mm, "end": v(-5.96, -15.6) * mm});
            skLineSegment(sketch, "E7172", {"start": v(-5.96, -15.6) * mm, "end": v(-5.84, -15.37) * mm});
            skLineSegment(sketch, "E7173", {"start": v(-5.84, -15.37) * mm, "end": v(-5.76, -15.26) * mm});
            skLineSegment(sketch, "E7174", {"start": v(-5.76, -15.26) * mm, "end": v(-5.66, -15.15) * mm});
            skLineSegment(sketch, "E7175", {"start": v(-5.66, -15.15) * mm, "end": v(-5.52, -15.05) * mm});
            skLineSegment(sketch, "E7176", {"start": v(-5.52, -15.05) * mm, "end": v(-5.35, -14.96) * mm});
            skLineSegment(sketch, "E7177", {"start": v(-5.35, -14.96) * mm, "end": v(-5.11, -14.86) * mm});
            skLineSegment(sketch, "E7178", {"start": v(-5.11, -14.86) * mm, "end": v(-4.9, -14.82) * mm});
            skLineSegment(sketch, "E7179", {"start": v(-4.9, -14.82) * mm, "end": v(-4.73, -14.81) * mm});
            skLineSegment(sketch, "E7180", {"start": v(-4.73, -14.81) * mm, "end": v(-4.58, -14.84) * mm});
            skLineSegment(sketch, "E7181", {"start": v(-4.58, -14.84) * mm, "end": v(-4.45, -14.89) * mm});
            skLineSegment(sketch, "E7182", {"start": v(-4.45, -14.89) * mm, "end": v(-4.33, -14.95) * mm});
            skLineSegment(sketch, "E7183", {"start": v(-4.33, -14.95) * mm, "end": v(-4.2, -15.01) * mm});
            skLineSegment(sketch, "E7184", {"start": v(-4.2, -15.01) * mm, "end": v(-4.1, -15.07) * mm});
            skLineSegment(sketch, "E7185", {"start": v(-4.1, -15.07) * mm, "end": v(-3.94, -14.9) * mm});
            skLineSegment(sketch, "E7186", {"start": v(-3.94, -14.9) * mm, "end": v(-4.43, -13.95) * mm});
            skLineSegment(sketch, "E7187", {"start": v(-4.43, -13.95) * mm, "end": v(-4.54, -14.01) * mm});
            skLineSegment(sketch, "E7188", {"start": v(-4.54, -14.01) * mm, "end": v(-4.67, -14.1) * mm});
            skLineSegment(sketch, "E7189", {"start": v(-4.67, -14.1) * mm, "end": v(-4.82, -14.22) * mm});
            skLineSegment(sketch, "E7190", {"start": v(-4.82, -14.22) * mm, "end": v(-4.98, -14.35) * mm});
            skLineSegment(sketch, "E7191", {"start": v(-4.98, -14.35) * mm, "end": v(-5.28, -14.61) * mm});
            skLineSegment(sketch, "E7192", {"start": v(-5.28, -14.61) * mm, "end": v(-5.5, -14.8) * mm});
            skLineSegment(sketch, "E7193", {"start": v(-5.5, -14.8) * mm, "end": v(-5.64, -14.93) * mm});
            skLineSegment(sketch, "E7194", {"start": v(-5.64, -14.93) * mm, "end": v(-5.75, -15.05) * mm});
            skLineSegment(sketch, "E7195", {"start": v(-5.75, -15.05) * mm, "end": v(-5.86, -15.17) * mm});
            skLineSegment(sketch, "E7196", {"start": v(-5.86, -15.17) * mm, "end": v(-5.98, -15.29) * mm});
            skLineSegment(sketch, "E7197", {"start": v(-5.98, -15.29) * mm, "end": v(-6.11, -15.42) * mm});
            skLineSegment(sketch, "E7198", {"start": v(-6.11, -15.42) * mm, "end": v(-6.24, -15.55) * mm});
            skLineSegment(sketch, "E7199", {"start": v(-6.24, -15.55) * mm, "end": v(-6.3, -15.62) * mm});
            skLineSegment(sketch, "E7200", {"start": v(-6.3, -15.62) * mm, "end": v(-6.35, -15.7) * mm});
            skLineSegment(sketch, "E7201", {"start": v(-6.35, -15.7) * mm, "end": v(-6.4, -15.75) * mm});
            skLineSegment(sketch, "E7202", {"start": v(-6.4, -15.75) * mm, "end": v(-6.43, -15.8) * mm});
            skLineSegment(sketch, "E7203", {"start": v(-7.86, 1.18) * mm, "end": v(-7.88, 1.35) * mm});
            skLineSegment(sketch, "E7204", {"start": v(-7.88, 1.35) * mm, "end": v(-7.9, 1.48) * mm});
            skLineSegment(sketch, "E7205", {"start": v(-7.9, 1.48) * mm, "end": v(-7.9, 1.6) * mm});
            skLineSegment(sketch, "E7206", {"start": v(-7.9, 1.6) * mm, "end": v(-7.9, 1.72) * mm});
            skLineSegment(sketch, "E7207", {"start": v(-7.9, 1.72) * mm, "end": v(-7.9, 1.84) * mm});
            skLineSegment(sketch, "E7208", {"start": v(-7.9, 1.84) * mm, "end": v(-7.89, 1.96) * mm});
            skLineSegment(sketch, "E7209", {"start": v(-7.89, 1.96) * mm, "end": v(-7.86, 2.1) * mm});
            skLineSegment(sketch, "E7210", {"start": v(-7.86, 2.1) * mm, "end": v(-7.83, 2.25) * mm});
            skLineSegment(sketch, "E7211", {"start": v(-7.83, 2.25) * mm, "end": v(-8.07, 2.4) * mm});
            skLineSegment(sketch, "E7212", {"start": v(-8.07, 2.4) * mm, "end": v(-8.3, 2.54) * mm});
            skLineSegment(sketch, "E7213", {"start": v(-8.3, 2.54) * mm, "end": v(-8.54, 2.7) * mm});
            skLineSegment(sketch, "E7214", {"start": v(-8.54, 2.7) * mm, "end": v(-8.75, 2.84) * mm});
            skLineSegment(sketch, "E7215", {"start": v(-8.75, 2.84) * mm, "end": v(-9.1, 3.1) * mm});
            skLineSegment(sketch, "E7216", {"start": v(-9.1, 3.1) * mm, "end": v(-9.3, 3.22) * mm});
            skLineSegment(sketch, "E7217", {"start": v(-9.3, 3.22) * mm, "end": v(-9.21, 2.96) * mm});
            skLineSegment(sketch, "E7218", {"start": v(-9.21, 2.96) * mm, "end": v(-9.07, 2.66) * mm});
            skLineSegment(sketch, "E7219", {"start": v(-9.07, 2.66) * mm, "end": v(-8.89, 2.35) * mm});
            skLineSegment(sketch, "E7220", {"start": v(-8.89, 2.35) * mm, "end": v(-8.68, 2.04) * mm});
            skLineSegment(sketch, "E7221", {"start": v(-8.68, 2.04) * mm, "end": v(-8.45, 1.75) * mm});
            skLineSegment(sketch, "E7222", {"start": v(-8.45, 1.75) * mm, "end": v(-8.23, 1.5) * mm});
            skLineSegment(sketch, "E7223", {"start": v(-8.23, 1.5) * mm, "end": v(-8.03, 1.3) * mm});
            skLineSegment(sketch, "E7224", {"start": v(-8.03, 1.3) * mm, "end": v(-7.86, 1.18) * mm});
            skLineSegment(sketch, "E7225", {"start": v(7.49, 3.23) * mm, "end": v(7.48, 3.06) * mm});
            skLineSegment(sketch, "E7226", {"start": v(7.48, 3.06) * mm, "end": v(7.46, 2.9) * mm});
            skLineSegment(sketch, "E7227", {"start": v(7.46, 2.9) * mm, "end": v(7.43, 2.74) * mm});
            skLineSegment(sketch, "E7228", {"start": v(7.43, 2.74) * mm, "end": v(7.4, 2.6) * mm});
            skLineSegment(sketch, "E7229", {"start": v(7.4, 2.6) * mm, "end": v(7.33, 2.32) * mm});
            skLineSegment(sketch, "E7230", {"start": v(7.33, 2.32) * mm, "end": v(7.27, 2.02) * mm});
            skLineSegment(sketch, "E7231", {"start": v(7.27, 2.02) * mm, "end": v(7.48, 2.17) * mm});
            skLineSegment(sketch, "E7232", {"start": v(7.48, 2.17) * mm, "end": v(7.72, 2.4) * mm});
            skLineSegment(sketch, "E7233", {"start": v(7.72, 2.4) * mm, "end": v(7.97, 2.7) * mm});
            skLineSegment(sketch, "E7234", {"start": v(7.97, 2.7) * mm, "end": v(8.22, 3.01) * mm});
            skLineSegment(sketch, "E7235", {"start": v(8.22, 3.01) * mm, "end": v(8.45, 3.34) * mm});
            skLineSegment(sketch, "E7236", {"start": v(8.45, 3.34) * mm, "end": v(8.65, 3.65) * mm});
            skLineSegment(sketch, "E7237", {"start": v(8.65, 3.65) * mm, "end": v(8.8, 3.92) * mm});
            skLineSegment(sketch, "E7238", {"start": v(8.8, 3.92) * mm, "end": v(8.89, 4.13) * mm});
            skLineSegment(sketch, "E7239", {"start": v(8.89, 4.13) * mm, "end": v(8.21, 3.66) * mm});
            skLineSegment(sketch, "E7240", {"start": v(8.21, 3.66) * mm, "end": v(8.04, 3.55) * mm});
            skLineSegment(sketch, "E7241", {"start": v(8.04, 3.55) * mm, "end": v(7.86, 3.43) * mm});
            skLineSegment(sketch, "E7242", {"start": v(7.86, 3.43) * mm, "end": v(7.66, 3.32) * mm});
            skLineSegment(sketch, "E7243", {"start": v(7.66, 3.32) * mm, "end": v(7.49, 3.23) * mm});
            skLineSegment(sketch, "E7244", {"start": v(-7.25, 2.02) * mm, "end": v(-7.33, 2.32) * mm});
            skLineSegment(sketch, "E7245", {"start": v(-7.33, 2.32) * mm, "end": v(-7.4, 2.59) * mm});
            skLineSegment(sketch, "E7246", {"start": v(-7.4, 2.59) * mm, "end": v(-7.43, 2.72) * mm});
            skLineSegment(sketch, "E7247", {"start": v(-7.43, 2.72) * mm, "end": v(-7.45, 2.87) * mm});
            skLineSegment(sketch, "E7248", {"start": v(-7.45, 2.87) * mm, "end": v(-7.46, 3.04) * mm});
            skLineSegment(sketch, "E7249", {"start": v(-7.46, 3.04) * mm, "end": v(-7.47, 3.24) * mm});
            skLineSegment(sketch, "E7250", {"start": v(-7.47, 3.24) * mm, "end": v(-7.54, 3.27) * mm});
            skLineSegment(sketch, "E7251", {"start": v(-7.54, 3.27) * mm, "end": v(-7.64, 3.3) * mm});
            skLineSegment(sketch, "E7252", {"start": v(-7.64, 3.3) * mm, "end": v(-7.74, 3.36) * mm});
            skLineSegment(sketch, "E7253", {"start": v(-7.74, 3.36) * mm, "end": v(-7.85, 3.43) * mm});
            skLineSegment(sketch, "E7254", {"start": v(-7.85, 3.43) * mm, "end": v(-8.05, 3.55) * mm});
            skLineSegment(sketch, "E7255", {"start": v(-8.05, 3.55) * mm, "end": v(-8.22, 3.66) * mm});
            skLineSegment(sketch, "E7256", {"start": v(-8.22, 3.66) * mm, "end": v(-8.9, 4.13) * mm});
            skLineSegment(sketch, "E7257", {"start": v(-8.9, 4.13) * mm, "end": v(-8.8, 3.96) * mm});
            skLineSegment(sketch, "E7258", {"start": v(-8.8, 3.96) * mm, "end": v(-8.68, 3.74) * mm});
            skLineSegment(sketch, "E7259", {"start": v(-8.68, 3.74) * mm, "end": v(-8.53, 3.5) * mm});
            skLineSegment(sketch, "E7260", {"start": v(-8.53, 3.5) * mm, "end": v(-8.38, 3.24) * mm});
            skLineSegment(sketch, "E7261", {"start": v(-8.38, 3.24) * mm, "end": v(-8.21, 3) * mm});
            skLineSegment(sketch, "E7262", {"start": v(-8.21, 3) * mm, "end": v(-8.05, 2.77) * mm});
            skLineSegment(sketch, "E7263", {"start": v(-8.05, 2.77) * mm, "end": v(-7.9, 2.58) * mm});
            skLineSegment(sketch, "E7264", {"start": v(-7.9, 2.58) * mm, "end": v(-7.76, 2.45) * mm});
            skLineSegment(sketch, "E7265", {"start": v(-7.76, 2.45) * mm, "end": v(-7.63, 2.33) * mm});
            skLineSegment(sketch, "E7266", {"start": v(-7.63, 2.33) * mm, "end": v(-7.51, 2.2) * mm});
            skLineSegment(sketch, "E7267", {"start": v(-7.51, 2.2) * mm, "end": v(-7.45, 2.14) * mm});
            skLineSegment(sketch, "E7268", {"start": v(-7.45, 2.14) * mm, "end": v(-7.38, 2.1) * mm});
            skLineSegment(sketch, "E7269", {"start": v(-7.38, 2.1) * mm, "end": v(-7.32, 2.05) * mm});
            skLineSegment(sketch, "E7270", {"start": v(-7.32, 2.05) * mm, "end": v(-7.25, 2.02) * mm});
            skLineSegment(sketch, "E7271", {"start": v(4.35, -19.93) * mm, "end": v(4.46, -19.88) * mm});
            skLineSegment(sketch, "E7272", {"start": v(4.46, -19.88) * mm, "end": v(4.57, -19.82) * mm});
            skLineSegment(sketch, "E7273", {"start": v(4.57, -19.82) * mm, "end": v(4.68, -19.75) * mm});
            skLineSegment(sketch, "E7274", {"start": v(4.68, -19.75) * mm, "end": v(4.8, -19.67) * mm});
            skLineSegment(sketch, "E7275", {"start": v(4.8, -19.67) * mm, "end": v(4.9, -19.58) * mm});
            skLineSegment(sketch, "E7276", {"start": v(4.9, -19.58) * mm, "end": v(4.98, -19.5) * mm});
            skLineSegment(sketch, "E7277", {"start": v(4.98, -19.5) * mm, "end": v(5.06, -19.42) * mm});
            skLineSegment(sketch, "E7278", {"start": v(5.06, -19.42) * mm, "end": v(5.13, -19.35) * mm});
            skLineSegment(sketch, "E7279", {"start": v(5.13, -19.35) * mm, "end": v(5.18, -19.27) * mm});
            skLineSegment(sketch, "E7280", {"start": v(5.18, -19.27) * mm, "end": v(5.25, -19.17) * mm});
            skLineSegment(sketch, "E7281", {"start": v(5.25, -19.17) * mm, "end": v(5.33, -19.04) * mm});
            skLineSegment(sketch, "E7282", {"start": v(5.33, -19.04) * mm, "end": v(5.4, -18.9) * mm});
            skLineSegment(sketch, "E7283", {"start": v(5.4, -18.9) * mm, "end": v(5.44, -18.75) * mm});
            skLineSegment(sketch, "E7284", {"start": v(5.44, -18.75) * mm, "end": v(5.46, -18.62) * mm});
            skLineSegment(sketch, "E7285", {"start": v(5.46, -18.62) * mm, "end": v(5.44, -18.5) * mm});
            skLineSegment(sketch, "E7286", {"start": v(5.44, -18.5) * mm, "end": v(5.36, -18.4) * mm});
            skLineSegment(sketch, "E7287", {"start": v(5.36, -18.4) * mm, "end": v(5.3, -18.37) * mm});
            skLineSegment(sketch, "E7288", {"start": v(5.3, -18.37) * mm, "end": v(5.23, -18.36) * mm});
            skLineSegment(sketch, "E7289", {"start": v(5.23, -18.36) * mm, "end": v(5.16, -18.36) * mm});
            skLineSegment(sketch, "E7290", {"start": v(5.16, -18.36) * mm, "end": v(5.09, -18.36) * mm});
            skLineSegment(sketch, "E7291", {"start": v(5.09, -18.36) * mm, "end": v(5.02, -18.38) * mm});
            skLineSegment(sketch, "E7292", {"start": v(5.02, -18.38) * mm, "end": v(4.95, -18.41) * mm});
            skLineSegment(sketch, "E7293", {"start": v(4.95, -18.41) * mm, "end": v(4.9, -18.44) * mm});
            skLineSegment(sketch, "E7294", {"start": v(4.9, -18.44) * mm, "end": v(4.84, -18.48) * mm});
            skLineSegment(sketch, "E7295", {"start": v(4.84, -18.48) * mm, "end": v(4.78, -18.54) * mm});
            skLineSegment(sketch, "E7296", {"start": v(4.78, -18.54) * mm, "end": v(4.74, -18.59) * mm});
            skLineSegment(sketch, "E7297", {"start": v(4.74, -18.59) * mm, "end": v(4.72, -18.64) * mm});
            skLineSegment(sketch, "E7298", {"start": v(4.72, -18.64) * mm, "end": v(4.7, -18.69) * mm});
            skLineSegment(sketch, "E7299", {"start": v(4.7, -18.69) * mm, "end": v(4.69, -18.8) * mm});
            skLineSegment(sketch, "E7300", {"start": v(4.69, -18.8) * mm, "end": v(4.66, -18.96) * mm});
            skLineSegment(sketch, "E7301", {"start": v(4.66, -18.96) * mm, "end": v(4.6, -19.13) * mm});
            skLineSegment(sketch, "E7302", {"start": v(4.6, -19.13) * mm, "end": v(4.53, -19.26) * mm});
            skLineSegment(sketch, "E7303", {"start": v(4.53, -19.26) * mm, "end": v(4.48, -19.35) * mm});
            skLineSegment(sketch, "E7304", {"start": v(4.48, -19.35) * mm, "end": v(4.42, -19.43) * mm});
            skLineSegment(sketch, "E7305", {"start": v(4.42, -19.43) * mm, "end": v(4.38, -19.5) * mm});
            skLineSegment(sketch, "E7306", {"start": v(4.38, -19.5) * mm, "end": v(4.35, -19.6) * mm});
            skLineSegment(sketch, "E7307", {"start": v(4.35, -19.6) * mm, "end": v(4.34, -19.74) * mm});
            skLineSegment(sketch, "E7308", {"start": v(4.34, -19.74) * mm, "end": v(4.35, -19.93) * mm});
            skLineSegment(sketch, "E7309", {"start": v(-3.95, -19.93) * mm, "end": v(-3.91, -19.8) * mm});
            skLineSegment(sketch, "E7310", {"start": v(-3.91, -19.8) * mm, "end": v(-3.9, -19.69) * mm});
            skLineSegment(sketch, "E7311", {"start": v(-3.9, -19.69) * mm, "end": v(-3.93, -19.59) * mm});
            skLineSegment(sketch, "E7312", {"start": v(-3.93, -19.59) * mm, "end": v(-3.97, -19.5) * mm});
            skLineSegment(sketch, "E7313", {"start": v(-3.97, -19.5) * mm, "end": v(-4.02, -19.4) * mm});
            skLineSegment(sketch, "E7314", {"start": v(-4.02, -19.4) * mm, "end": v(-4.09, -19.3) * mm});
            skLineSegment(sketch, "E7315", {"start": v(-4.09, -19.3) * mm, "end": v(-4.16, -19.17) * mm});
            skLineSegment(sketch, "E7316", {"start": v(-4.16, -19.17) * mm, "end": v(-4.22, -19.02) * mm});
            skLineSegment(sketch, "E7317", {"start": v(-4.22, -19.02) * mm, "end": v(-4.25, -18.88) * mm});
            skLineSegment(sketch, "E7318", {"start": v(-4.25, -18.88) * mm, "end": v(-4.28, -18.75) * mm});
            skLineSegment(sketch, "E7319", {"start": v(-4.28, -18.75) * mm, "end": v(-4.3, -18.68) * mm});
            skLineSegment(sketch, "E7320", {"start": v(-4.3, -18.68) * mm, "end": v(-4.32, -18.62) * mm});
            skLineSegment(sketch, "E7321", {"start": v(-4.32, -18.62) * mm, "end": v(-4.35, -18.57) * mm});
            skLineSegment(sketch, "E7322", {"start": v(-4.35, -18.57) * mm, "end": v(-4.38, -18.52) * mm});
            skLineSegment(sketch, "E7323", {"start": v(-4.38, -18.52) * mm, "end": v(-4.42, -18.48) * mm});
            skLineSegment(sketch, "E7324", {"start": v(-4.42, -18.48) * mm, "end": v(-4.47, -18.45) * mm});
            skLineSegment(sketch, "E7325", {"start": v(-4.47, -18.45) * mm, "end": v(-4.53, -18.41) * mm});
            skLineSegment(sketch, "E7326", {"start": v(-4.53, -18.41) * mm, "end": v(-4.6, -18.38) * mm});
            skLineSegment(sketch, "E7327", {"start": v(-4.6, -18.38) * mm, "end": v(-4.68, -18.36) * mm});
            skLineSegment(sketch, "E7328", {"start": v(-4.68, -18.36) * mm, "end": v(-4.76, -18.36) * mm});
            skLineSegment(sketch, "E7329", {"start": v(-4.76, -18.36) * mm, "end": v(-4.84, -18.36) * mm});
            skLineSegment(sketch, "E7330", {"start": v(-4.84, -18.36) * mm, "end": v(-4.91, -18.4) * mm});
            skLineSegment(sketch, "E7331", {"start": v(-4.91, -18.4) * mm, "end": v(-5.01, -18.5) * mm});
            skLineSegment(sketch, "E7332", {"start": v(-5.01, -18.5) * mm, "end": v(-5.04, -18.64) * mm});
            skLineSegment(sketch, "E7333", {"start": v(-5.04, -18.64) * mm, "end": v(-5.01, -18.8) * mm});
            skLineSegment(sketch, "E7334", {"start": v(-5.01, -18.8) * mm, "end": v(-4.93, -19) * mm});
            skLineSegment(sketch, "E7335", {"start": v(-4.93, -19) * mm, "end": v(-4.81, -19.19) * mm});
            skLineSegment(sketch, "E7336", {"start": v(-4.81, -19.19) * mm, "end": v(-4.67, -19.37) * mm});
            skLineSegment(sketch, "E7337", {"start": v(-4.67, -19.37) * mm, "end": v(-4.52, -19.54) * mm});
            skLineSegment(sketch, "E7338", {"start": v(-4.52, -19.54) * mm, "end": v(-4.37, -19.67) * mm});
            skLineSegment(sketch, "E7339", {"start": v(-4.37, -19.67) * mm, "end": v(-3.95, -19.93) * mm});
            skLineSegment(sketch, "E7340", {"start": v(-3.13, -17.86) * mm, "end": v(-3.26, -17.93) * mm});
            skLineSegment(sketch, "E7341", {"start": v(-3.26, -17.93) * mm, "end": v(-3.35, -18) * mm});
            skLineSegment(sketch, "E7342", {"start": v(-3.35, -18) * mm, "end": v(-3.39, -18.1) * mm});
            skLineSegment(sketch, "E7343", {"start": v(-3.39, -18.1) * mm, "end": v(-3.4, -18.2) * mm});
            skLineSegment(sketch, "E7344", {"start": v(-3.4, -18.2) * mm, "end": v(-3.38, -18.3) * mm});
            skLineSegment(sketch, "E7345", {"start": v(-3.38, -18.3) * mm, "end": v(-3.35, -18.41) * mm});
            skLineSegment(sketch, "E7346", {"start": v(-3.35, -18.41) * mm, "end": v(-3.3, -18.54) * mm});
            skLineSegment(sketch, "E7347", {"start": v(-3.3, -18.54) * mm, "end": v(-3.23, -18.66) * mm});
            skLineSegment(sketch, "E7348", {"start": v(-3.23, -18.66) * mm, "end": v(-3.18, -18.77) * mm});
            skLineSegment(sketch, "E7349", {"start": v(-3.18, -18.77) * mm, "end": v(-3.14, -18.86) * mm});
            skLineSegment(sketch, "E7350", {"start": v(-3.14, -18.86) * mm, "end": v(-3.1, -18.94) * mm});
            skLineSegment(sketch, "E7351", {"start": v(-3.1, -18.94) * mm, "end": v(-3.04, -19) * mm});
            skLineSegment(sketch, "E7352", {"start": v(-3.04, -19) * mm, "end": v(-2.98, -19.09) * mm});
            skLineSegment(sketch, "E7353", {"start": v(-2.98, -19.09) * mm, "end": v(-2.89, -19.18) * mm});
            skLineSegment(sketch, "E7354", {"start": v(-2.89, -19.18) * mm, "end": v(-2.84, -19.22) * mm});
            skLineSegment(sketch, "E7355", {"start": v(-2.84, -19.22) * mm, "end": v(-2.8, -19.26) * mm});
            skLineSegment(sketch, "E7356", {"start": v(-2.8, -19.26) * mm, "end": v(-2.75, -19.29) * mm});
            skLineSegment(sketch, "E7357", {"start": v(-2.75, -19.29) * mm, "end": v(-2.7, -19.3) * mm});
            skLineSegment(sketch, "E7358", {"start": v(-2.7, -19.3) * mm, "end": v(-2.6, -19.3) * mm});
            skLineSegment(sketch, "E7359", {"start": v(-2.6, -19.3) * mm, "end": v(-2.55, -19.26) * mm});
            skLineSegment(sketch, "E7360", {"start": v(-2.55, -19.26) * mm, "end": v(-2.53, -19.17) * mm});
            skLineSegment(sketch, "E7361", {"start": v(-2.53, -19.17) * mm, "end": v(-2.55, -19.04) * mm});
            skLineSegment(sketch, "E7362", {"start": v(-2.55, -19.04) * mm, "end": v(-2.57, -18.9) * mm});
            skLineSegment(sketch, "E7363", {"start": v(-2.57, -18.9) * mm, "end": v(-2.6, -18.74) * mm});
            skLineSegment(sketch, "E7364", {"start": v(-2.6, -18.74) * mm, "end": v(-2.6, -18.58) * mm});
            skLineSegment(sketch, "E7365", {"start": v(-2.6, -18.58) * mm, "end": v(-2.59, -18.42) * mm});
            skLineSegment(sketch, "E7366", {"start": v(-2.59, -18.42) * mm, "end": v(-2.57, -18.28) * mm});
            skLineSegment(sketch, "E7367", {"start": v(-2.57, -18.28) * mm, "end": v(-2.58, -18.15) * mm});
            skLineSegment(sketch, "E7368", {"start": v(-2.58, -18.15) * mm, "end": v(-2.63, -18.04) * mm});
            skLineSegment(sketch, "E7369", {"start": v(-2.63, -18.04) * mm, "end": v(-2.7, -17.95) * mm});
            skLineSegment(sketch, "E7370", {"start": v(-2.7, -17.95) * mm, "end": v(-2.79, -17.88) * mm});
            skLineSegment(sketch, "E7371", {"start": v(-2.79, -17.88) * mm, "end": v(-2.9, -17.84) * mm});
            skLineSegment(sketch, "E7372", {"start": v(-2.9, -17.84) * mm, "end": v(-3, -17.83) * mm});
            skLineSegment(sketch, "E7373", {"start": v(-3, -17.83) * mm, "end": v(-3.13, -17.86) * mm});
            skLineSegment(sketch, "E7374", {"start": v(2.94, -18.16) * mm, "end": v(3.02, -18.34) * mm});
            skLineSegment(sketch, "E7375", {"start": v(3.02, -18.34) * mm, "end": v(3.05, -18.52) * mm});
            skLineSegment(sketch, "E7376", {"start": v(3.05, -18.52) * mm, "end": v(3.04, -18.69) * mm});
            skLineSegment(sketch, "E7377", {"start": v(3.04, -18.69) * mm, "end": v(3.01, -18.85) * mm});
            skLineSegment(sketch, "E7378", {"start": v(3.01, -18.85) * mm, "end": v(2.97, -18.99) * mm});
            skLineSegment(sketch, "E7379", {"start": v(2.97, -18.99) * mm, "end": v(2.95, -19.1) * mm});
            skLineSegment(sketch, "E7380", {"start": v(2.95, -19.1) * mm, "end": v(2.95, -19.2) * mm});
            skLineSegment(sketch, "E7381", {"start": v(2.95, -19.2) * mm, "end": v(3, -19.28) * mm});
            skLineSegment(sketch, "E7382", {"start": v(3, -19.28) * mm, "end": v(3.13, -19.3) * mm});
            skLineSegment(sketch, "E7383", {"start": v(3.13, -19.3) * mm, "end": v(3.3, -19.17) * mm});
            skLineSegment(sketch, "E7384", {"start": v(3.3, -19.17) * mm, "end": v(3.5, -18.96) * mm});
            skLineSegment(sketch, "E7385", {"start": v(3.5, -18.96) * mm, "end": v(3.66, -18.7) * mm});
            skLineSegment(sketch, "E7386", {"start": v(3.66, -18.7) * mm, "end": v(3.77, -18.41) * mm});
            skLineSegment(sketch, "E7387", {"start": v(3.77, -18.41) * mm, "end": v(3.8, -18.15) * mm});
            skLineSegment(sketch, "E7388", {"start": v(3.8, -18.15) * mm, "end": v(3.72, -17.95) * mm});
            skLineSegment(sketch, "E7389", {"start": v(3.72, -17.95) * mm, "end": v(3.5, -17.84) * mm});
            skLineSegment(sketch, "E7390", {"start": v(3.5, -17.84) * mm, "end": v(3.43, -17.83) * mm});
            skLineSegment(sketch, "E7391", {"start": v(3.43, -17.83) * mm, "end": v(3.35, -17.84) * mm});
            skLineSegment(sketch, "E7392", {"start": v(3.35, -17.84) * mm, "end": v(3.29, -17.85) * mm});
            skLineSegment(sketch, "E7393", {"start": v(3.29, -17.85) * mm, "end": v(3.23, -17.87) * mm});
            skLineSegment(sketch, "E7394", {"start": v(3.23, -17.87) * mm, "end": v(3.18, -17.9) * mm});
            skLineSegment(sketch, "E7395", {"start": v(3.18, -17.9) * mm, "end": v(3.14, -17.94) * mm});
            skLineSegment(sketch, "E7396", {"start": v(3.14, -17.94) * mm, "end": v(3.1, -17.98) * mm});
            skLineSegment(sketch, "E7397", {"start": v(3.1, -17.98) * mm, "end": v(3.06, -18.03) * mm});
            skLineSegment(sketch, "E7398", {"start": v(3.06, -18.03) * mm, "end": v(2.94, -18.16) * mm});
            skLineSegment(sketch, "E7399", {"start": v(4.47, -20.36) * mm, "end": v(4.6, -20.37) * mm});
            skLineSegment(sketch, "E7400", {"start": v(4.6, -20.37) * mm, "end": v(4.74, -20.37) * mm});
            skLineSegment(sketch, "E7401", {"start": v(4.74, -20.37) * mm, "end": v(4.87, -20.35) * mm});
            skLineSegment(sketch, "E7402", {"start": v(4.87, -20.35) * mm, "end": v(5, -20.33) * mm});
            skLineSegment(sketch, "E7403", {"start": v(5, -20.33) * mm, "end": v(5.11, -20.3) * mm});
            skLineSegment(sketch, "E7404", {"start": v(5.11, -20.3) * mm, "end": v(5.23, -20.27) * mm});
            skLineSegment(sketch, "E7405", {"start": v(5.23, -20.27) * mm, "end": v(5.34, -20.22) * mm});
            skLineSegment(sketch, "E7406", {"start": v(5.34, -20.22) * mm, "end": v(5.45, -20.17) * mm});
            skLineSegment(sketch, "E7407", {"start": v(5.45, -20.17) * mm, "end": v(5.68, -20.04) * mm});
            skLineSegment(sketch, "E7408", {"start": v(5.68, -20.04) * mm, "end": v(5.85, -19.91) * mm});
            skLineSegment(sketch, "E7409", {"start": v(5.85, -19.91) * mm, "end": v(5.97, -19.79) * mm});
            skLineSegment(sketch, "E7410", {"start": v(5.97, -19.79) * mm, "end": v(6.03, -19.67) * mm});
            skLineSegment(sketch, "E7411", {"start": v(6.03, -19.67) * mm, "end": v(6.02, -19.58) * mm});
            skLineSegment(sketch, "E7412", {"start": v(6.02, -19.58) * mm, "end": v(5.95, -19.5) * mm});
            skLineSegment(sketch, "E7413", {"start": v(5.95, -19.5) * mm, "end": v(5.81, -19.44) * mm});
            skLineSegment(sketch, "E7414", {"start": v(5.81, -19.44) * mm, "end": v(5.6, -19.41) * mm});
            skLineSegment(sketch, "E7415", {"start": v(5.6, -19.41) * mm, "end": v(5.5, -19.41) * mm});
            skLineSegment(sketch, "E7416", {"start": v(5.5, -19.41) * mm, "end": v(5.44, -19.43) * mm});
            skLineSegment(sketch, "E7417", {"start": v(5.44, -19.43) * mm, "end": v(5.39, -19.45) * mm});
            skLineSegment(sketch, "E7418", {"start": v(5.39, -19.45) * mm, "end": v(5.35, -19.48) * mm});
            skLineSegment(sketch, "E7419", {"start": v(5.35, -19.48) * mm, "end": v(5.27, -19.57) * mm});
            skLineSegment(sketch, "E7420", {"start": v(5.27, -19.57) * mm, "end": v(5.16, -19.67) * mm});
            skLineSegment(sketch, "E7421", {"start": v(5.16, -19.67) * mm, "end": v(4.94, -19.8) * mm});
            skLineSegment(sketch, "E7422", {"start": v(4.94, -19.8) * mm, "end": v(4.72, -19.94) * mm});
            skLineSegment(sketch, "E7423", {"start": v(4.72, -19.94) * mm, "end": v(4.62, -20.02) * mm});
            skLineSegment(sketch, "E7424", {"start": v(4.62, -20.02) * mm, "end": v(4.54, -20.11) * mm});
            skLineSegment(sketch, "E7425", {"start": v(4.54, -20.11) * mm, "end": v(4.49, -20.23) * mm});
            skLineSegment(sketch, "E7426", {"start": v(4.49, -20.23) * mm, "end": v(4.47, -20.36) * mm});
            skLineSegment(sketch, "E7427", {"start": v(-4.05, -20.36) * mm, "end": v(-4.07, -20.24) * mm});
            skLineSegment(sketch, "E7428", {"start": v(-4.07, -20.24) * mm, "end": v(-4.1, -20.14) * mm});
            skLineSegment(sketch, "E7429", {"start": v(-4.1, -20.14) * mm, "end": v(-4.16, -20.06) * mm});
            skLineSegment(sketch, "E7430", {"start": v(-4.16, -20.06) * mm, "end": v(-4.23, -19.99) * mm});
            skLineSegment(sketch, "E7431", {"start": v(-4.23, -19.99) * mm, "end": v(-4.42, -19.86) * mm});
            skLineSegment(sketch, "E7432", {"start": v(-4.42, -19.86) * mm, "end": v(-4.67, -19.72) * mm});
            skLineSegment(sketch, "E7433", {"start": v(-4.67, -19.72) * mm, "end": v(-4.78, -19.64) * mm});
            skLineSegment(sketch, "E7434", {"start": v(-4.78, -19.64) * mm, "end": v(-4.87, -19.56) * mm});
            skLineSegment(sketch, "E7435", {"start": v(-4.87, -19.56) * mm, "end": v(-4.94, -19.48) * mm});
            skLineSegment(sketch, "E7436", {"start": v(-4.94, -19.48) * mm, "end": v(-5, -19.43) * mm});
            skLineSegment(sketch, "E7437", {"start": v(-5, -19.43) * mm, "end": v(-5.12, -19.4) * mm});
            skLineSegment(sketch, "E7438", {"start": v(-5.12, -19.4) * mm, "end": v(-5.28, -19.42) * mm});
            skLineSegment(sketch, "E7439", {"start": v(-5.28, -19.42) * mm, "end": v(-5.43, -19.46) * mm});
            skLineSegment(sketch, "E7440", {"start": v(-5.43, -19.46) * mm, "end": v(-5.55, -19.53) * mm});
            skLineSegment(sketch, "E7441", {"start": v(-5.55, -19.53) * mm, "end": v(-5.61, -19.63) * mm});
            skLineSegment(sketch, "E7442", {"start": v(-5.61, -19.63) * mm, "end": v(-5.58, -19.76) * mm});
            skLineSegment(sketch, "E7443", {"start": v(-5.58, -19.76) * mm, "end": v(-5.41, -19.93) * mm});
            skLineSegment(sketch, "E7444", {"start": v(-5.41, -19.93) * mm, "end": v(-5.09, -20.14) * mm});
            skLineSegment(sketch, "E7445", {"start": v(-5.09, -20.14) * mm, "end": v(-4.97, -20.2) * mm});
            skLineSegment(sketch, "E7446", {"start": v(-4.97, -20.2) * mm, "end": v(-4.85, -20.25) * mm});
            skLineSegment(sketch, "E7447", {"start": v(-4.85, -20.25) * mm, "end": v(-4.73, -20.3) * mm});
            skLineSegment(sketch, "E7448", {"start": v(-4.73, -20.3) * mm, "end": v(-4.6, -20.32) * mm});
            skLineSegment(sketch, "E7449", {"start": v(-4.6, -20.32) * mm, "end": v(-4.47, -20.35) * mm});
            skLineSegment(sketch, "E7450", {"start": v(-4.47, -20.35) * mm, "end": v(-4.34, -20.36) * mm});
            skLineSegment(sketch, "E7451", {"start": v(-4.34, -20.36) * mm, "end": v(-4.2, -20.37) * mm});
            skLineSegment(sketch, "E7452", {"start": v(-4.2, -20.37) * mm, "end": v(-4.05, -20.36) * mm});
            skLineSegment(sketch, "E7453", {"start": v(6.98, -23.5) * mm, "end": v(7.02, -23.52) * mm});
            skLineSegment(sketch, "E7454", {"start": v(7.02, -23.52) * mm, "end": v(7.2, -23.56) * mm});
            skLineSegment(sketch, "E7455", {"start": v(7.2, -23.56) * mm, "end": v(7.4, -23.6) * mm});
            skLineSegment(sketch, "E7456", {"start": v(7.4, -23.6) * mm, "end": v(7.52, -23.64) * mm});
            skLineSegment(sketch, "E7457", {"start": v(7.52, -23.64) * mm, "end": v(7.62, -23.69) * mm});
            skLineSegment(sketch, "E7458", {"start": v(7.62, -23.69) * mm, "end": v(7.7, -23.75) * mm});
            skLineSegment(sketch, "E7459", {"start": v(7.7, -23.75) * mm, "end": v(7.77, -23.83) * mm});
            skLineSegment(sketch, "E7460", {"start": v(7.77, -23.83) * mm, "end": v(7.85, -23.7) * mm});
            skLineSegment(sketch, "E7461", {"start": v(7.85, -23.7) * mm, "end": v(7.94, -23.5) * mm});
            skLineSegment(sketch, "E7462", {"start": v(7.94, -23.5) * mm, "end": v(8.01, -23.3) * mm});
            skLineSegment(sketch, "E7463", {"start": v(8.01, -23.3) * mm, "end": v(8.08, -23.06) * mm});
            skLineSegment(sketch, "E7464", {"start": v(8.08, -23.06) * mm, "end": v(8.14, -22.82) * mm});
            skLineSegment(sketch, "E7465", {"start": v(8.14, -22.82) * mm, "end": v(8.2, -22.6) * mm});
            skLineSegment(sketch, "E7466", {"start": v(8.2, -22.6) * mm, "end": v(8.24, -22.4) * mm});
            skLineSegment(sketch, "E7467", {"start": v(8.24, -22.4) * mm, "end": v(8.27, -22.26) * mm});
            skLineSegment(sketch, "E7468", {"start": v(8.27, -22.26) * mm, "end": v(7.9, -22.21) * mm});
            skLineSegment(sketch, "E7469", {"start": v(7.9, -22.21) * mm, "end": v(7.85, -22.4) * mm});
            skLineSegment(sketch, "E7470", {"start": v(7.85, -22.4) * mm, "end": v(7.8, -22.59) * mm});
            skLineSegment(sketch, "E7471", {"start": v(7.8, -22.59) * mm, "end": v(7.75, -22.75) * mm});
            skLineSegment(sketch, "E7472", {"start": v(7.75, -22.75) * mm, "end": v(7.7, -22.9) * mm});
            skLineSegment(sketch, "E7473", {"start": v(7.7, -22.9) * mm, "end": v(7.6, -23.2) * mm});
            skLineSegment(sketch, "E7474", {"start": v(7.6, -23.2) * mm, "end": v(7.5, -23.52) * mm});
            skLineSegment(sketch, "E7475", {"start": v(7.5, -23.52) * mm, "end": v(6.98, -23.5) * mm});
            skLineSegment(sketch, "E7476", {"start": v(5.25, -7.26) * mm, "end": v(5.66, -7.32) * mm});
            skLineSegment(sketch, "E7477", {"start": v(5.66, -7.32) * mm, "end": v(6.02, -7.4) * mm});
            skLineSegment(sketch, "E7478", {"start": v(6.02, -7.4) * mm, "end": v(6.32, -7.5) * mm});
            skLineSegment(sketch, "E7479", {"start": v(6.32, -7.5) * mm, "end": v(6.57, -7.56) * mm});
            skLineSegment(sketch, "E7480", {"start": v(6.57, -7.56) * mm, "end": v(6.77, -7.57) * mm});
            skLineSegment(sketch, "E7481", {"start": v(6.77, -7.57) * mm, "end": v(6.93, -7.5) * mm});
            skLineSegment(sketch, "E7482", {"start": v(6.93, -7.5) * mm, "end": v(7.05, -7.32) * mm});
            skLineSegment(sketch, "E7483", {"start": v(7.05, -7.32) * mm, "end": v(7.13, -7) * mm});
            skLineSegment(sketch, "E7484", {"start": v(7.13, -7) * mm, "end": v(7.02, -7.1) * mm});
            skLineSegment(sketch, "E7485", {"start": v(7.02, -7.1) * mm, "end": v(6.87, -7.23) * mm});
            skLineSegment(sketch, "E7486", {"start": v(6.87, -7.23) * mm, "end": v(6.73, -7.3) * mm});
            skLineSegment(sketch, "E7487", {"start": v(6.73, -7.3) * mm, "end": v(6.6, -7.3) * mm});
            skLineSegment(sketch, "E7488", {"start": v(6.6, -7.3) * mm, "end": v(6.45, -7.28) * mm});
            skLineSegment(sketch, "E7489", {"start": v(6.45, -7.28) * mm, "end": v(6.1, -7.13) * mm});
            skLineSegment(sketch, "E7490", {"start": v(6.1, -7.13) * mm, "end": v(5.6, -6.91) * mm});
            skLineSegment(sketch, "E7491", {"start": v(5.6, -6.91) * mm, "end": v(5.45, -6.85) * mm});
            skLineSegment(sketch, "E7492", {"start": v(5.45, -6.85) * mm, "end": v(5.34, -6.8) * mm});
            skLineSegment(sketch, "E7493", {"start": v(5.34, -6.8) * mm, "end": v(5.23, -6.74) * mm});
            skLineSegment(sketch, "E7494", {"start": v(5.23, -6.74) * mm, "end": v(5.1, -6.69) * mm});
            skLineSegment(sketch, "E7495", {"start": v(5.1, -6.69) * mm, "end": v(5.25, -7.26) * mm});
            skLineSegment(sketch, "E7496", {"start": v(0.47, 17.8) * mm, "end": v(0.82, 16.6) * mm});
            skLineSegment(sketch, "E7497", {"start": v(0.82, 16.6) * mm, "end": v(1.96, 16.6) * mm});
            skLineSegment(sketch, "E7498", {"start": v(1.96, 16.6) * mm, "end": v(1.04, 15.86) * mm});
            skLineSegment(sketch, "E7499", {"start": v(1.04, 15.86) * mm, "end": v(1.4, 14.65) * mm});
            skLineSegment(sketch, "E7500", {"start": v(1.4, 14.65) * mm, "end": v(0.47, 15.4) * mm});
            skLineSegment(sketch, "E7501", {"start": v(0.47, 15.4) * mm, "end": v(-0.45, 14.65) * mm});
            skLineSegment(sketch, "E7502", {"start": v(-0.45, 14.65) * mm, "end": v(-0.1, 15.86) * mm});
            skLineSegment(sketch, "E7503", {"start": v(-0.1, 15.86) * mm, "end": v(-1.02, 16.6) * mm});
            skLineSegment(sketch, "E7504", {"start": v(-1.02, 16.6) * mm, "end": v(0.12, 16.6) * mm});
            skLineSegment(sketch, "E7505", {"start": v(0.12, 16.6) * mm, "end": v(0.47, 17.8) * mm});
            skLineSegment(sketch, "E7506", {"start": v(-2.75, 15.63) * mm, "end": v(-2.3, 14.08) * mm});
            skLineSegment(sketch, "E7507", {"start": v(-2.3, 14.08) * mm, "end": v(-0.83, 14.08) * mm});
            skLineSegment(sketch, "E7508", {"start": v(-0.83, 14.08) * mm, "end": v(-2.02, 13.12) * mm});
            skLineSegment(sketch, "E7509", {"start": v(-2.02, 13.12) * mm, "end": v(-1.56, 11.57) * mm});
            skLineSegment(sketch, "E7510", {"start": v(-1.56, 11.57) * mm, "end": v(-2.75, 12.53) * mm});
            skLineSegment(sketch, "E7511", {"start": v(-2.75, 12.53) * mm, "end": v(-3.93, 11.57) * mm});
            skLineSegment(sketch, "E7512", {"start": v(-3.93, 11.57) * mm, "end": v(-3.48, 13.12) * mm});
            skLineSegment(sketch, "E7513", {"start": v(-3.48, 13.12) * mm, "end": v(-4.67, 14.08) * mm});
            skLineSegment(sketch, "E7514", {"start": v(-4.67, 14.08) * mm, "end": v(-3.2, 14.08) * mm});
            skLineSegment(sketch, "E7515", {"start": v(-3.2, 14.08) * mm, "end": v(-2.75, 15.63) * mm});
            skLineSegment(sketch, "E7516", {"start": v(3.64, 15.63) * mm, "end": v(4.09, 14.08) * mm});
            skLineSegment(sketch, "E7517", {"start": v(4.09, 14.08) * mm, "end": v(5.56, 14.08) * mm});
            skLineSegment(sketch, "E7518", {"start": v(5.56, 14.08) * mm, "end": v(4.37, 13.12) * mm});
            skLineSegment(sketch, "E7519", {"start": v(4.37, 13.12) * mm, "end": v(4.82, 11.57) * mm});
            skLineSegment(sketch, "E7520", {"start": v(4.82, 11.57) * mm, "end": v(3.64, 12.53) * mm});
            skLineSegment(sketch, "E7521", {"start": v(3.64, 12.53) * mm, "end": v(2.45, 11.57) * mm});
            skLineSegment(sketch, "E7522", {"start": v(2.45, 11.57) * mm, "end": v(2.9, 13.12) * mm});
            skLineSegment(sketch, "E7523", {"start": v(2.9, 13.12) * mm, "end": v(1.72, 14.08) * mm});
            skLineSegment(sketch, "E7524", {"start": v(1.72, 14.08) * mm, "end": v(3.19, 14.08) * mm});
            skLineSegment(sketch, "E7525", {"start": v(3.19, 14.08) * mm, "end": v(3.64, 15.63) * mm});
            skLineSegment(sketch, "E7526", {"start": v(-6.77, 13) * mm, "end": v(-6.23, 11.12) * mm});
            skLineSegment(sketch, "E7527", {"start": v(-6.23, 11.12) * mm, "end": v(-4.45, 11.12) * mm});
            skLineSegment(sketch, "E7528", {"start": v(-4.45, 11.12) * mm, "end": v(-5.9, 9.96) * mm});
            skLineSegment(sketch, "E7529", {"start": v(-5.9, 9.96) * mm, "end": v(-5.34, 8.08) * mm});
            skLineSegment(sketch, "E7530", {"start": v(-5.34, 8.08) * mm, "end": v(-6.77, 9.25) * mm});
            skLineSegment(sketch, "E7531", {"start": v(-6.77, 9.25) * mm, "end": v(-8.2, 8.08) * mm});
            skLineSegment(sketch, "E7532", {"start": v(-8.2, 8.08) * mm, "end": v(-7.66, 9.96) * mm});
            skLineSegment(sketch, "E7533", {"start": v(-7.66, 9.96) * mm, "end": v(-9.1, 11.12) * mm});
            skLineSegment(sketch, "E7534", {"start": v(-9.1, 11.12) * mm, "end": v(-7.32, 11.12) * mm});
            skLineSegment(sketch, "E7535", {"start": v(-7.32, 11.12) * mm, "end": v(-6.77, 13) * mm});
            skLineSegment(sketch, "E7536", {"start": v(7.63, 12.92) * mm, "end": v(8.18, 11.04) * mm});
            skLineSegment(sketch, "E7537", {"start": v(8.18, 11.04) * mm, "end": v(9.95, 11.04) * mm});
            skLineSegment(sketch, "E7538", {"start": v(9.95, 11.04) * mm, "end": v(8.51, 9.88) * mm});
            skLineSegment(sketch, "E7539", {"start": v(8.51, 9.88) * mm, "end": v(9.07, 8) * mm});
            skLineSegment(sketch, "E7540", {"start": v(9.07, 8) * mm, "end": v(7.63, 9.17) * mm});
            skLineSegment(sketch, "E7541", {"start": v(7.63, 9.17) * mm, "end": v(6.2, 8) * mm});
            skLineSegment(sketch, "E7542", {"start": v(6.2, 8) * mm, "end": v(6.75, 9.88) * mm});
            skLineSegment(sketch, "E7543", {"start": v(6.75, 9.88) * mm, "end": v(5.31, 11.04) * mm});
            skLineSegment(sketch, "E7544", {"start": v(5.31, 11.04) * mm, "end": v(7.09, 11.04) * mm});
            skLineSegment(sketch, "E7545", {"start": v(7.09, 11.04) * mm, "end": v(7.63, 12.92) * mm});
            skEllipse(sketch, "E7546", {"center": v(0, 0) * mm, "majorRadius": 50.8 * mm, "minorRadius": 38.1 * mm, "majorAxis": v(1, 0)});
            skSolve(sketch);
        }
        {
            var Q0;
            Q0=makeQuery(id+"F0.imprint","IMPRINT",FACE,{"disambiguationData":[TD([[makeQuery(id+"F0.imprint","IMPRINT",EDGE,{"derivedFrom":sQuery(id+"F0.wireOp",EDGE,"E6758")}),1.0]])]});
            var Q1;
            Q1=makeQuery(id+"F0.imprint","IMPRINT",FACE,{"disambiguationData":[TD([[makeQuery(id+"F0.imprint","IMPRINT",EDGE,{"derivedFrom":sQuery(id+"F0.wireOp",EDGE,"E3370")}),1.0]])]});
            var Q2;
            Q2=makeQuery(id+"F0.imprint","IMPRINT",FACE,{"disambiguationData":[TD([[makeQuery(id+"F0.imprint","IMPRINT",EDGE,{"derivedFrom":sQuery(id+"F0.wireOp",EDGE,"E7526")}),-1.0]])]});
            var Q3;
            Q3=makeQuery(id+"F0.imprint","IMPRINT",FACE,{"disambiguationData":[TD([[makeQuery(id+"F0.imprint","IMPRINT",EDGE,{"derivedFrom":sQuery(id+"F0.wireOp",EDGE,"E7506")}),-1.0]])]});
            var Q4;
            Q4=makeQuery(id+"F0.imprint","IMPRINT",FACE,{"disambiguationData":[TD([[makeQuery(id+"F0.imprint","IMPRINT",EDGE,{"derivedFrom":sQuery(id+"F0.wireOp",EDGE,"E7496")}),-1.0]])]});
            var Q5;
            Q5=makeQuery(id+"F0.imprint","IMPRINT",FACE,{"disambiguationData":[TD([[makeQuery(id+"F0.imprint","IMPRINT",EDGE,{"derivedFrom":sQuery(id+"F0.wireOp",EDGE,"E7516")}),-1.0]])]});
            var Q6;
            Q6=makeQuery(id+"F0.imprint","IMPRINT",FACE,{"disambiguationData":[TD([[makeQuery(id+"F0.imprint","IMPRINT",EDGE,{"derivedFrom":sQuery(id+"F0.wireOp",EDGE,"E7536")}),-1.0]])]});
            var Q7;
            Q7=makeQuery(id+"F0.imprint","IMPRINT",FACE,{"disambiguationData":[TD([[makeQuery(id+"F0.imprint","IMPRINT",EDGE,{"derivedFrom":sQuery(id+"F0.wireOp",EDGE,"E7476")}),1.0]])]});
            extrude(context, id + "F1", {"entities" : qUnion([Q0, Q1, Q2, Q3, Q4, Q5, Q6, Q7]), "depth" : 7.11 * mm});
        }
        {
            var Q0;
            Q0=makeQuery(id+"F0.imprint","IMPRINT",FACE,{"disambiguationData":[TD([[makeQuery(id+"F0.imprint","IMPRINT",EDGE,{"derivedFrom":sQuery(id+"F0.wireOp",EDGE,"E5357")}),1.0]])]});
            var Q1;
            Q1=makeQuery(id+"F0.imprint","IMPRINT",FACE,{"disambiguationData":[TD([[makeQuery(id+"F0.imprint","IMPRINT",EDGE,{"derivedFrom":sQuery(id+"F0.wireOp",EDGE,"E6425")}),1.0]])]});
            var Q2;
            Q2=makeQuery(id+"F0.imprint","IMPRINT",FACE,{"disambiguationData":[TD([[makeQuery(id+"F0.imprint","IMPRINT",EDGE,{"derivedFrom":sQuery(id+"F0.wireOp",EDGE,"E6342")}),1.0]])]});
            var Q3;
            Q3=makeQuery(id+"F0.imprint","IMPRINT",FACE,{"disambiguationData":[TD([[makeQuery(id+"F0.imprint","IMPRINT",EDGE,{"derivedFrom":sQuery(id+"F0.wireOp",EDGE,"E6020")}),1.0]])]});
            var Q4;
            Q4=makeQuery(id+"F0.imprint","IMPRINT",FACE,{"disambiguationData":[TD([[makeQuery(id+"F0.imprint","IMPRINT",EDGE,{"derivedFrom":sQuery(id+"F0.wireOp",EDGE,"E6136")}),1.0]])]});
            var Q5;
            Q5=makeQuery(id+"F0.imprint","IMPRINT",FACE,{"disambiguationData":[TD([[makeQuery(id+"F0.imprint","IMPRINT",EDGE,{"derivedFrom":sQuery(id+"F0.wireOp",EDGE,"E5640")}),1.0]])]});
            var Q6;
            Q6=makeQuery(id+"F0.imprint","IMPRINT",FACE,{"disambiguationData":[TD([[makeQuery(id+"F0.imprint","IMPRINT",EDGE,{"derivedFrom":sQuery(id+"F0.wireOp",EDGE,"E5135")}),1.0]])]});
            var Q7;
            Q7=makeQuery(id+"F0.imprint","IMPRINT",FACE,{"disambiguationData":[TD([[makeQuery(id+"F0.imprint","IMPRINT",EDGE,{"derivedFrom":sQuery(id+"F0.wireOp",EDGE,"E4517")}),1.0]])]});
            var Q8;
            Q8=makeQuery(id+"F0.imprint","IMPRINT",FACE,{"disambiguationData":[TD([[makeQuery(id+"F0.imprint","IMPRINT",EDGE,{"derivedFrom":sQuery(id+"F0.wireOp",EDGE,"E4698")}),1.0]])]});
            var Q9;
            Q9=makeQuery(id+"F0.imprint","IMPRINT",FACE,{"disambiguationData":[TD([[makeQuery(id+"F0.imprint","IMPRINT",EDGE,{"derivedFrom":sQuery(id+"F0.wireOp",EDGE,"E4799")}),1.0]])]});
            var Q10;
            Q10=makeQuery(id+"F0.imprint","IMPRINT",FACE,{"disambiguationData":[TD([[makeQuery(id+"F0.imprint","IMPRINT",EDGE,{"derivedFrom":sQuery(id+"F0.wireOp",EDGE,"E2353")}),1.0]])]});
            var Q11;
            Q11=makeQuery(id+"F0.imprint","IMPRINT",FACE,{"disambiguationData":[TD([[makeQuery(id+"F0.imprint","IMPRINT",EDGE,{"derivedFrom":sQuery(id+"F0.wireOp",EDGE,"E3563")}),1.0]])]});
            var Q12;
            Q12=makeQuery(id+"F0.imprint","IMPRINT",FACE,{"disambiguationData":[TD([[makeQuery(id+"F0.imprint","IMPRINT",EDGE,{"derivedFrom":sQuery(id+"F0.wireOp",EDGE,"E5448")}),1.0]])]});
            var Q13;
            Q13=makeQuery(id+"F0.imprint","IMPRINT",FACE,{"disambiguationData":[TD([[makeQuery(id+"F0.imprint","IMPRINT",EDGE,{"derivedFrom":sQuery(id+"F0.wireOp",EDGE,"E4968")}),1.0]])]});
            var Q14;
            Q14=makeQuery(id+"F0.imprint","IMPRINT",FACE,{"disambiguationData":[TD([[makeQuery(id+"F0.imprint","IMPRINT",EDGE,{"derivedFrom":sQuery(id+"F0.wireOp",EDGE,"E5495")}),1.0]])]});
            var Q15;
            Q15=makeQuery(id+"F0.imprint","IMPRINT",FACE,{"disambiguationData":[TD([[makeQuery(id+"F0.imprint","IMPRINT",EDGE,{"derivedFrom":sQuery(id+"F0.wireOp",EDGE,"E4582")}),1.0]])]});
            var Q16;
            Q16=makeQuery(id+"F0.imprint","IMPRINT",FACE,{"disambiguationData":[TD([[makeQuery(id+"F0.imprint","IMPRINT",EDGE,{"derivedFrom":sQuery(id+"F0.wireOp",EDGE,"E4403")}),1.0]])]});
            var Q17;
            Q17=makeQuery(id+"F0.imprint","IMPRINT",FACE,{"disambiguationData":[TD([[makeQuery(id+"F0.imprint","IMPRINT",EDGE,{"derivedFrom":sQuery(id+"F0.wireOp",EDGE,"E5547")}),1.0]])]});
            var Q18;
            Q18=makeQuery(id+"F0.imprint","IMPRINT",FACE,{"disambiguationData":[TD([[makeQuery(id+"F0.imprint","IMPRINT",EDGE,{"derivedFrom":sQuery(id+"F0.wireOp",EDGE,"E5027")}),1.0]])]});
            var Q19;
            Q19=makeQuery(id+"F0.imprint","IMPRINT",FACE,{"disambiguationData":[TD([[makeQuery(id+"F0.imprint","IMPRINT",EDGE,{"derivedFrom":sQuery(id+"F0.wireOp",EDGE,"E5595")}),1.0]])]});
            var Q20;
            Q20=makeQuery(id+"F0.imprint","IMPRINT",FACE,{"disambiguationData":[TD([[makeQuery(id+"F0.imprint","IMPRINT",EDGE,{"derivedFrom":sQuery(id+"F0.wireOp",EDGE,"E5224")}),1.0]])]});
            var Q21;
            Q21=makeQuery(id+"F0.imprint","IMPRINT",FACE,{"disambiguationData":[TD([[makeQuery(id+"F0.imprint","IMPRINT",EDGE,{"derivedFrom":sQuery(id+"F0.wireOp",EDGE,"E6464")}),1.0]])]});
            var Q22;
            Q22=makeQuery(id+"F0.imprint","IMPRINT",FACE,{"disambiguationData":[TD([[makeQuery(id+"F0.imprint","IMPRINT",EDGE,{"derivedFrom":sQuery(id+"F0.wireOp",EDGE,"E6297")}),1.0]])]});
            var Q23;
            Q23=makeQuery(id+"F0.imprint","IMPRINT",FACE,{"disambiguationData":[TD([[makeQuery(id+"F0.imprint","IMPRINT",EDGE,{"derivedFrom":sQuery(id+"F0.wireOp",EDGE,"E5988")}),1.0]])]});
            var Q24;
            Q24=makeQuery(id+"F0.imprint","IMPRINT",FACE,{"disambiguationData":[TD([[makeQuery(id+"F0.imprint","IMPRINT",EDGE,{"derivedFrom":sQuery(id+"F0.wireOp",EDGE,"E6172")}),1.0]])]});
            var Q25;
            Q25=makeQuery(id+"F0.imprint","IMPRINT",FACE,{"disambiguationData":[TD([[makeQuery(id+"F0.imprint","IMPRINT",EDGE,{"derivedFrom":sQuery(id+"F0.wireOp",EDGE,"E5679")}),1.0]])]});
            var Q26;
            Q26=makeQuery(id+"F0.imprint","IMPRINT",FACE,{"disambiguationData":[TD([[makeQuery(id+"F0.imprint","IMPRINT",EDGE,{"derivedFrom":sQuery(id+"F0.wireOp",EDGE,"E5075")}),1.0]])]});
            var Q27;
            Q27=makeQuery(id+"F0.imprint","IMPRINT",FACE,{"disambiguationData":[TD([[makeQuery(id+"F0.imprint","IMPRINT",EDGE,{"derivedFrom":sQuery(id+"F0.wireOp",EDGE,"E4465")}),1.0]])]});
            var Q28;
            Q28=makeQuery(id+"F0.imprint","IMPRINT",FACE,{"disambiguationData":[TD([[makeQuery(id+"F0.imprint","IMPRINT",EDGE,{"derivedFrom":sQuery(id+"F0.wireOp",EDGE,"E4643")}),1.0]])]});
            var Q29;
            Q29=makeQuery(id+"F0.imprint","IMPRINT",FACE,{"disambiguationData":[TD([[makeQuery(id+"F0.imprint","IMPRINT",EDGE,{"derivedFrom":sQuery(id+"F0.wireOp",EDGE,"E4738")}),1.0]])]});
            var Q30;
            Q30=makeQuery(id+"F0.imprint","IMPRINT",FACE,{"disambiguationData":[TD([[makeQuery(id+"F0.imprint","IMPRINT",EDGE,{"derivedFrom":sQuery(id+"F0.wireOp",EDGE,"E2114")}),1.0]])]});
            var Q31;
            Q31=makeQuery(id+"F0.imprint","IMPRINT",FACE,{"disambiguationData":[TD([[makeQuery(id+"F0.imprint","IMPRINT",EDGE,{"derivedFrom":sQuery(id+"F0.wireOp",EDGE,"E3664")}),1.0]])]});
            extrude(context, id + "F2", {"entities" : qUnion([Q0, Q1, Q2, Q3, Q4, Q5, Q6, Q7, Q8, Q9, Q10, Q11, Q12, Q13, Q14, Q15, Q16, Q17, Q18, Q19, Q20, Q21, Q22, Q23, Q24, Q25, Q26, Q27, Q28, Q29, Q30, Q31]), "depth" : 3.8 * mm});
        }
        {
            var Q0;
            Q0=makeQuery(id+"F0.imprint","IMPRINT",FACE,{"disambiguationData":[TD([[makeQuery(id+"F0.imprint","IMPRINT",EDGE,{"derivedFrom":sQuery(id+"F0.wireOp",EDGE,"E1728")}),1.0]])]});
            var Q1;
            Q1=makeQuery(id+"F0.imprint","IMPRINT",FACE,{"disambiguationData":[TD([[makeQuery(id+"F0.imprint","IMPRINT",EDGE,{"derivedFrom":sQuery(id+"F0.wireOp",EDGE,"E3042")}),1.0]])]});
            var Q2;
            Q2=makeQuery(id+"F0.imprint","IMPRINT",FACE,{"disambiguationData":[TD([[makeQuery(id+"F0.imprint","IMPRINT",EDGE,{"derivedFrom":sQuery(id+"F0.wireOp",EDGE,"E4054")}),1.0]])]});
            var Q3;
            Q3=makeQuery(id+"F0.imprint","IMPRINT",FACE,{"disambiguationData":[TD([[makeQuery(id+"F0.imprint","IMPRINT",EDGE,{"derivedFrom":sQuery(id+"F0.wireOp",EDGE,"E7070")}),1.0]])]});
            var Q4;
            Q4=makeQuery(id+"F0.imprint","IMPRINT",FACE,{"disambiguationData":[TD([[makeQuery(id+"F0.imprint","IMPRINT",EDGE,{"derivedFrom":sQuery(id+"F0.wireOp",EDGE,"E7008")}),1.0]])]});
            var Q5;
            Q5=makeQuery(id+"F0.imprint","IMPRINT",FACE,{"disambiguationData":[TD([[makeQuery(id+"F0.imprint","IMPRINT",EDGE,{"derivedFrom":sQuery(id+"F0.wireOp",EDGE,"E6707")}),1.0]])]});
            var Q6;
            Q6=makeQuery(id+"F0.imprint","IMPRINT",FACE,{"disambiguationData":[TD([[makeQuery(id+"F0.imprint","IMPRINT",EDGE,{"derivedFrom":sQuery(id+"F0.wireOp",EDGE,"E6619")}),1.0]])]});
            var Q7;
            Q7=makeQuery(id+"F0.imprint","IMPRINT",FACE,{"disambiguationData":[TD([[makeQuery(id+"F0.imprint","IMPRINT",EDGE,{"derivedFrom":sQuery(id+"F0.wireOp",EDGE,"E7146")}),1.0]])]});
            var Q8;
            Q8=makeQuery(id+"F0.imprint","IMPRINT",FACE,{"disambiguationData":[TD([[makeQuery(id+"F0.imprint","IMPRINT",EDGE,{"derivedFrom":sQuery(id+"F0.wireOp",EDGE,"E7225")}),1.0]])]});
            var Q9;
            Q9=makeQuery(id+"F0.imprint","IMPRINT",FACE,{"disambiguationData":[TD([[makeQuery(id+"F0.imprint","IMPRINT",EDGE,{"derivedFrom":sQuery(id+"F0.wireOp",EDGE,"E6907")}),1.0]])]});
            var Q10;
            Q10=makeQuery(id+"F0.imprint","IMPRINT",FACE,{"disambiguationData":[TD([[makeQuery(id+"F0.imprint","IMPRINT",EDGE,{"derivedFrom":sQuery(id+"F0.wireOp",EDGE,"E7244")}),1.0]])]});
            var Q11;
            Q11=makeQuery(id+"F0.imprint","IMPRINT",FACE,{"disambiguationData":[TD([[makeQuery(id+"F0.imprint","IMPRINT",EDGE,{"derivedFrom":sQuery(id+"F0.wireOp",EDGE,"E6875")}),1.0]])]});
            var Q12;
            Q12=makeQuery(id+"F0.imprint","IMPRINT",FACE,{"disambiguationData":[TD([[makeQuery(id+"F0.imprint","IMPRINT",EDGE,{"derivedFrom":sQuery(id+"F0.wireOp",EDGE,"E6569")}),1.0]])]});
            var Q13;
            Q13=makeQuery(id+"F0.imprint","IMPRINT",FACE,{"disambiguationData":[TD([[makeQuery(id+"F0.imprint","IMPRINT",EDGE,{"derivedFrom":sQuery(id+"F0.wireOp",EDGE,"E7203")}),1.0]])]});
            var Q14;
            Q14=makeQuery(id+"F0.imprint","IMPRINT",FACE,{"disambiguationData":[TD([[makeQuery(id+"F0.imprint","IMPRINT",EDGE,{"derivedFrom":sQuery(id+"F0.wireOp",EDGE,"E6972")}),1.0]])]});
            var Q15;
            Q15=makeQuery(id+"F0.imprint","IMPRINT",FACE,{"disambiguationData":[TD([[makeQuery(id+"F0.imprint","IMPRINT",EDGE,{"derivedFrom":sQuery(id+"F0.wireOp",EDGE,"E7044")}),1.0]])]});
            var Q16;
            Q16=makeQuery(id+"F0.imprint","IMPRINT",FACE,{"disambiguationData":[TD([[makeQuery(id+"F0.imprint","IMPRINT",EDGE,{"derivedFrom":sQuery(id+"F0.wireOp",EDGE,"E6728")}),1.0]])]});
            var Q17;
            Q17=makeQuery(id+"F0.imprint","IMPRINT",FACE,{"disambiguationData":[TD([[makeQuery(id+"F0.imprint","IMPRINT",EDGE,{"derivedFrom":sQuery(id+"F0.wireOp",EDGE,"E2562")}),1.0]])]});
            var Q18;
            Q18=makeQuery(id+"F0.imprint","IMPRINT",FACE,{"disambiguationData":[TD([[makeQuery(id+"F0.imprint","IMPRINT",EDGE,{"derivedFrom":sQuery(id+"F0.wireOp",EDGE,"E6389")}),1.0]])]});
            var Q19;
            Q19=makeQuery(id+"F0.imprint","IMPRINT",FACE,{"disambiguationData":[TD([[makeQuery(id+"F0.imprint","IMPRINT",EDGE,{"derivedFrom":sQuery(id+"F0.wireOp",EDGE,"E5949")}),1.0]])]});
            var Q20;
            Q20=makeQuery(id+"F0.imprint","IMPRINT",FACE,{"disambiguationData":[TD([[makeQuery(id+"F0.imprint","IMPRINT",EDGE,{"derivedFrom":sQuery(id+"F0.wireOp",EDGE,"E6529")}),1.0]])]});
            var Q21;
            Q21=makeQuery(id+"F0.imprint","IMPRINT",FACE,{"disambiguationData":[TD([[makeQuery(id+"F0.imprint","IMPRINT",EDGE,{"derivedFrom":sQuery(id+"F0.wireOp",EDGE,"E5897")}),1.0]])]});
            var Q22;
            Q22=makeQuery(id+"F0.imprint","IMPRINT",FACE,{"disambiguationData":[TD([[makeQuery(id+"F0.imprint","IMPRINT",EDGE,{"derivedFrom":sQuery(id+"F0.wireOp",EDGE,"E6496")}),1.0]])]});
            extrude(context, id + "F3", {"entities" : qUnion([Q0, Q1, Q2, Q3, Q4, Q5, Q6, Q7, Q8, Q9, Q10, Q11, Q12, Q13, Q14, Q15, Q16, Q17, Q18, Q19, Q20, Q21, Q22]), "depth" : 5.84 * mm});
        }
        {
            var Q0;
            Q0=makeQuery(id+"F0.imprint","IMPRINT",FACE,{"disambiguationData":[TD([[makeQuery(id+"F0.imprint","IMPRINT",EDGE,{"derivedFrom":sQuery(id+"F0.wireOp",EDGE,"E3901")}),1.0]])]});
            var Q1;
            Q1=makeQuery(id+"F0.imprint","IMPRINT",FACE,{"disambiguationData":[TD([[makeQuery(id+"F0.imprint","IMPRINT",EDGE,{"derivedFrom":sQuery(id+"F0.wireOp",EDGE,"E3846")}),1.0]])]});
            var Q2;
            Q2=makeQuery(id+"F0.imprint","IMPRINT",FACE,{"disambiguationData":[TD([[makeQuery(id+"F0.imprint","IMPRINT",EDGE,{"derivedFrom":sQuery(id+"F0.wireOp",EDGE,"E4914")}),1.0]])]});
            var Q3;
            Q3=makeQuery(id+"F0.imprint","IMPRINT",FACE,{"disambiguationData":[TD([[makeQuery(id+"F0.imprint","IMPRINT",EDGE,{"derivedFrom":sQuery(id+"F0.wireOp",EDGE,"E5177")}),1.0]])]});
            var Q4;
            Q4=makeQuery(id+"F0.imprint","IMPRINT",FACE,{"disambiguationData":[TD([[makeQuery(id+"F0.imprint","IMPRINT",EDGE,{"derivedFrom":sQuery(id+"F0.wireOp",EDGE,"E5731")}),1.0]])]});
            var Q5;
            Q5=makeQuery(id+"F0.imprint","IMPRINT",FACE,{"disambiguationData":[TD([[makeQuery(id+"F0.imprint","IMPRINT",EDGE,{"derivedFrom":sQuery(id+"F0.wireOp",EDGE,"E6216")}),1.0]])]});
            var Q6;
            Q6=makeQuery(id+"F0.imprint","IMPRINT",FACE,{"disambiguationData":[TD([[makeQuery(id+"F0.imprint","IMPRINT",EDGE,{"derivedFrom":sQuery(id+"F0.wireOp",EDGE,"E3980")}),1.0]])]});
            var Q7;
            Q7=makeQuery(id+"F0.imprint","IMPRINT",FACE,{"disambiguationData":[TD([[makeQuery(id+"F0.imprint","IMPRINT",EDGE,{"derivedFrom":sQuery(id+"F0.wireOp",EDGE,"E4853")}),1.0]])]});
            var Q8;
            Q8=makeQuery(id+"F0.imprint","IMPRINT",FACE,{"disambiguationData":[TD([[makeQuery(id+"F0.imprint","IMPRINT",EDGE,{"derivedFrom":sQuery(id+"F0.wireOp",EDGE,"E5316")}),1.0]])]});
            var Q9;
            Q9=makeQuery(id+"F0.imprint","IMPRINT",FACE,{"disambiguationData":[TD([[makeQuery(id+"F0.imprint","IMPRINT",EDGE,{"derivedFrom":sQuery(id+"F0.wireOp",EDGE,"E5766")}),1.0]])]});
            var Q10;
            Q10=makeQuery(id+"F0.imprint","IMPRINT",FACE,{"disambiguationData":[TD([[makeQuery(id+"F0.imprint","IMPRINT",EDGE,{"derivedFrom":sQuery(id+"F0.wireOp",EDGE,"E6258")}),1.0]])]});
            var Q11;
            Q11=makeQuery(id+"F0.imprint","IMPRINT",FACE,{"disambiguationData":[TD([[makeQuery(id+"F0.imprint","IMPRINT",EDGE,{"derivedFrom":sQuery(id+"F0.wireOp",EDGE,"E4265")}),1.0]])]});
            var Q12;
            Q12=makeQuery(id+"F0.imprint","IMPRINT",FACE,{"disambiguationData":[TD([[makeQuery(id+"F0.imprint","IMPRINT",EDGE,{"derivedFrom":sQuery(id+"F0.wireOp",EDGE,"E4126")}),1.0]])]});
            var Q13;
            Q13=makeQuery(id+"F0.imprint","IMPRINT",FACE,{"disambiguationData":[TD([[makeQuery(id+"F0.imprint","IMPRINT",EDGE,{"derivedFrom":sQuery(id+"F0.wireOp",EDGE,"E5801")}),1.0]])]});
            var Q14;
            Q14=makeQuery(id+"F0.imprint","IMPRINT",FACE,{"disambiguationData":[TD([[makeQuery(id+"F0.imprint","IMPRINT",EDGE,{"derivedFrom":sQuery(id+"F0.wireOp",EDGE,"E6091")}),1.0]])]});
            var Q15;
            Q15=makeQuery(id+"F0.imprint","IMPRINT",FACE,{"disambiguationData":[TD([[makeQuery(id+"F0.imprint","IMPRINT",EDGE,{"derivedFrom":sQuery(id+"F0.wireOp",EDGE,"E7399")}),1.0]])]});
            var Q16;
            Q16=makeQuery(id+"F0.imprint","IMPRINT",FACE,{"disambiguationData":[TD([[makeQuery(id+"F0.imprint","IMPRINT",EDGE,{"derivedFrom":sQuery(id+"F0.wireOp",EDGE,"E7271")}),1.0]])]});
            var Q17;
            Q17=makeQuery(id+"F0.imprint","IMPRINT",FACE,{"disambiguationData":[TD([[makeQuery(id+"F0.imprint","IMPRINT",EDGE,{"derivedFrom":sQuery(id+"F0.wireOp",EDGE,"E6837")}),1.0]])]});
            var Q18;
            Q18=makeQuery(id+"F0.imprint","IMPRINT",FACE,{"disambiguationData":[TD([[makeQuery(id+"F0.imprint","IMPRINT",EDGE,{"derivedFrom":sQuery(id+"F0.wireOp",EDGE,"E7374")}),1.0]])]});
            var Q19;
            Q19=makeQuery(id+"F0.imprint","IMPRINT",FACE,{"disambiguationData":[TD([[makeQuery(id+"F0.imprint","IMPRINT",EDGE,{"derivedFrom":sQuery(id+"F0.wireOp",EDGE,"E5851")}),1.0]])]});
            var Q20;
            Q20=makeQuery(id+"F0.imprint","IMPRINT",FACE,{"disambiguationData":[TD([[makeQuery(id+"F0.imprint","IMPRINT",EDGE,{"derivedFrom":sQuery(id+"F0.wireOp",EDGE,"E6050")}),1.0]])]});
            var Q21;
            Q21=makeQuery(id+"F0.imprint","IMPRINT",FACE,{"disambiguationData":[TD([[makeQuery(id+"F0.imprint","IMPRINT",EDGE,{"derivedFrom":sQuery(id+"F0.wireOp",EDGE,"E6805")}),1.0]])]});
            var Q22;
            Q22=makeQuery(id+"F0.imprint","IMPRINT",FACE,{"disambiguationData":[TD([[makeQuery(id+"F0.imprint","IMPRINT",EDGE,{"derivedFrom":sQuery(id+"F0.wireOp",EDGE,"E7340")}),1.0]])]});
            var Q23;
            Q23=makeQuery(id+"F0.imprint","IMPRINT",FACE,{"disambiguationData":[TD([[makeQuery(id+"F0.imprint","IMPRINT",EDGE,{"derivedFrom":sQuery(id+"F0.wireOp",EDGE,"E7309")}),1.0]])]});
            var Q24;
            Q24=makeQuery(id+"F0.imprint","IMPRINT",FACE,{"disambiguationData":[TD([[makeQuery(id+"F0.imprint","IMPRINT",EDGE,{"derivedFrom":sQuery(id+"F0.wireOp",EDGE,"E7427")}),1.0]])]});
            extrude(context, id + "F4", {"entities" : qUnion([Q0, Q1, Q2, Q3, Q4, Q5, Q6, Q7, Q8, Q9, Q10, Q11, Q12, Q13, Q14, Q15, Q16, Q17, Q18, Q19, Q20, Q21, Q22, Q23, Q24]), "depth" : 4.57 * mm});
        }
        {
            var Q0;
            Q0=makeQuery(id+"F4.opExtrude","SWEPT_BODY",BODY,{"disambiguationData":[OSD([sQuery(id+"F0.wireOp",EDGE,"E3846"),sQuery(id+"F0.wireOp",EDGE,"E3847"),sQuery(id+"F0.wireOp",EDGE,"E3848"),sQuery(id+"F0.wireOp",EDGE,"E3849"),sQuery(id+"F0.wireOp",EDGE,"E3850"),sQuery(id+"F0.wireOp",EDGE,"E3851"),sQuery(id+"F0.wireOp",EDGE,"E3852"),sQuery(id+"F0.wireOp",EDGE,"E3853"),sQuery(id+"F0.wireOp",EDGE,"E3854"),sQuery(id+"F0.wireOp",EDGE,"E3855"),sQuery(id+"F0.wireOp",EDGE,"E3856"),sQuery(id+"F0.wireOp",EDGE,"E3857"),sQuery(id+"F0.wireOp",EDGE,"E3858"),sQuery(id+"F0.wireOp",EDGE,"E3859"),sQuery(id+"F0.wireOp",EDGE,"E3860"),sQuery(id+"F0.wireOp",EDGE,"E3861"),sQuery(id+"F0.wireOp",EDGE,"E3862"),sQuery(id+"F0.wireOp",EDGE,"E3863"),sQuery(id+"F0.wireOp",EDGE,"E3864"),sQuery(id+"F0.wireOp",EDGE,"E3865"),sQuery(id+"F0.wireOp",EDGE,"E3866"),sQuery(id+"F0.wireOp",EDGE,"E3867"),sQuery(id+"F0.wireOp",EDGE,"E3868"),sQuery(id+"F0.wireOp",EDGE,"E3869"),sQuery(id+"F0.wireOp",EDGE,"E3870"),sQuery(id+"F0.wireOp",EDGE,"E3871"),sQuery(id+"F0.wireOp",EDGE,"E3872"),sQuery(id+"F0.wireOp",EDGE,"E3873"),sQuery(id+"F0.wireOp",EDGE,"E3874"),sQuery(id+"F0.wireOp",EDGE,"E3875"),sQuery(id+"F0.wireOp",EDGE,"E3876"),sQuery(id+"F0.wireOp",EDGE,"E3877"),sQuery(id+"F0.wireOp",EDGE,"E3878"),sQuery(id+"F0.wireOp",EDGE,"E3879"),sQuery(id+"F0.wireOp",EDGE,"E3880"),sQuery(id+"F0.wireOp",EDGE,"E3881"),sQuery(id+"F0.wireOp",EDGE,"E3882"),sQuery(id+"F0.wireOp",EDGE,"E3883"),sQuery(id+"F0.wireOp",EDGE,"E3884"),sQuery(id+"F0.wireOp",EDGE,"E3885"),sQuery(id+"F0.wireOp",EDGE,"E3886"),sQuery(id+"F0.wireOp",EDGE,"E3887"),sQuery(id+"F0.wireOp",EDGE,"E3888"),sQuery(id+"F0.wireOp",EDGE,"E3889"),sQuery(id+"F0.wireOp",EDGE,"E3890"),sQuery(id+"F0.wireOp",EDGE,"E3891"),sQuery(id+"F0.wireOp",EDGE,"E3892"),sQuery(id+"F0.wireOp",EDGE,"E3893"),sQuery(id+"F0.wireOp",EDGE,"E3894"),sQuery(id+"F0.wireOp",EDGE,"E3895"),sQuery(id+"F0.wireOp",EDGE,"E3896"),sQuery(id+"F0.wireOp",EDGE,"E3897"),sQuery(id+"F0.wireOp",EDGE,"E3898"),sQuery(id+"F0.wireOp",EDGE,"E3899"),sQuery(id+"F0.wireOp",EDGE,"E3900")])]});
            var Q1;
            Q1=qCreatedBy(makeId("Right.planeOp"),FACE);
            mirror(context, id + "F5", {"entities" : qUnion([Q0]), "mirrorPlane" : qUnion([Q1])});
        }
        {
            var Q0;
            Q0=makeQuery(id+"F0.imprint","IMPRINT",FACE,{"disambiguationData":[TD([[makeQuery(id+"F0.imprint","IMPRINT",EDGE,{"derivedFrom":sQuery(id+"F0.wireOp",EDGE,"E224")}),-1.0]])]});
            extrude(context, id + "F6", {"entities" : qUnion([Q0]), "depth" : 3.17 * mm});
        }
    });
